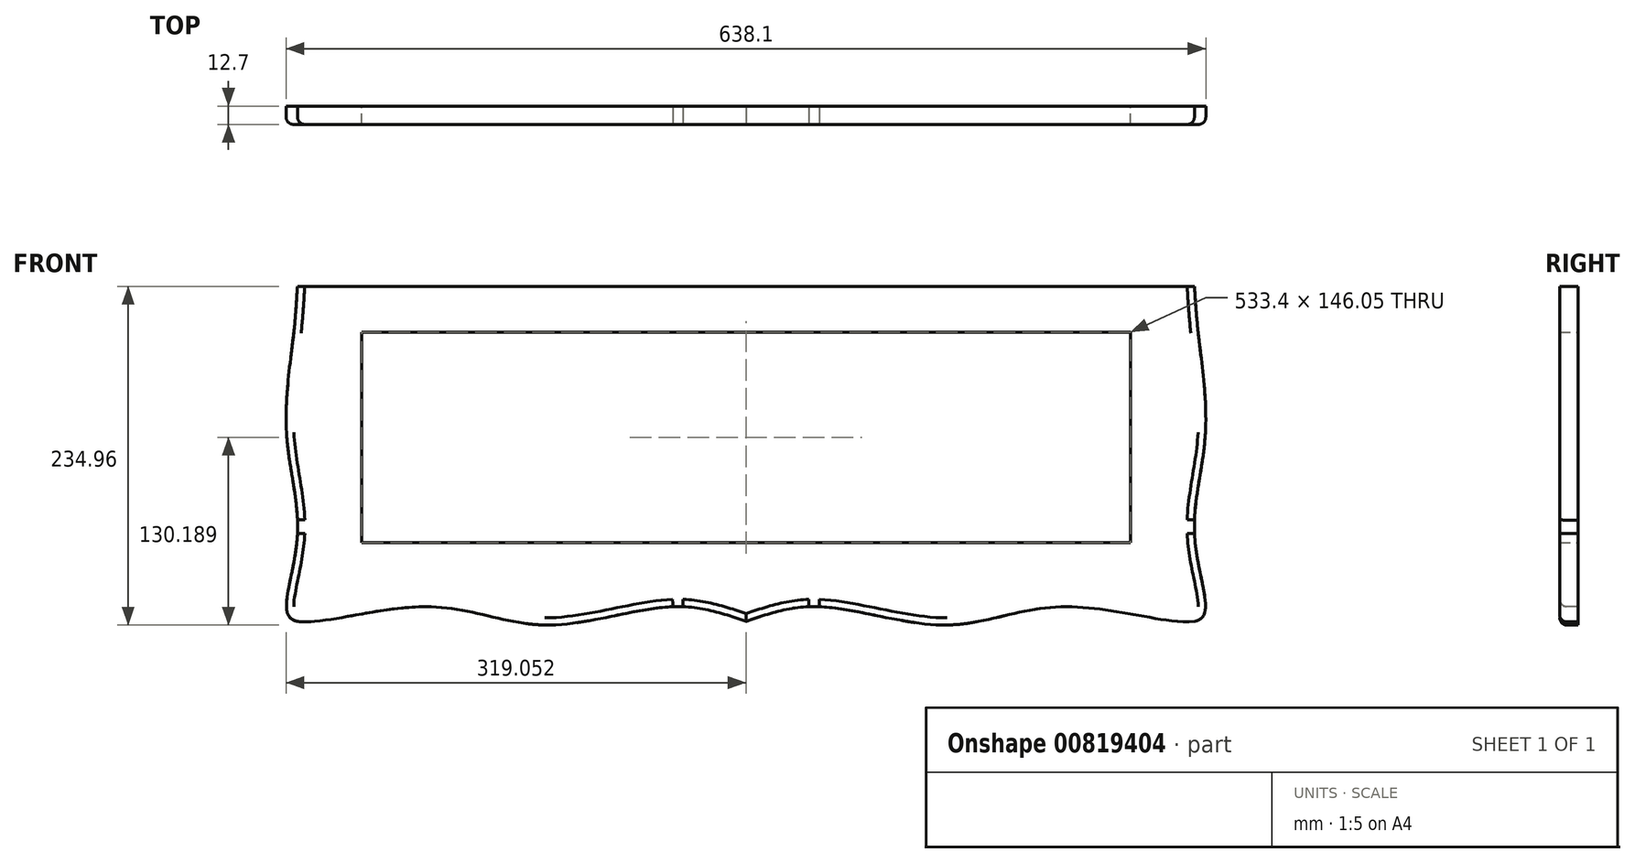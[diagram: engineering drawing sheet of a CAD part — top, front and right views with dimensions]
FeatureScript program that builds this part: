
annotation { "Feature Type Name" : "Feature", "Feature Type Description" : "" }
export const myFeature = defineFeature(function(context is Context, id is Id, definition is map)
    precondition{}
    {
        {
            var Q0;
            Q0=qCreatedBy(makeId("Front.planeOp"),FACE);
            var sketch = newSketch(context, id + "F0", { "sketchPlane" : qUnion([Q0])});
            skLineSegment(sketch, "E0.bottom", {"start": v(-290.57, 108.48) * mm, "end": v(331.73, 108.48) * mm});
            skLineSegment(sketch, "E0.top", {"start": v(-290.57, -113.77) * mm, "end": v(331.73, -113.77) * mm});
            skLineSegment(sketch, "E0.left", {"start": v(-290.57, 108.48) * mm, "end": v(-290.57, -113.77) * mm});
            skLineSegment(sketch, "E0.right", {"start": v(331.73, 108.48) * mm, "end": v(331.73, -113.77) * mm});
            skPoint(sketch, "E1", {"position": v(20.58, 108.48) * mm});
            skLineSegment(sketch, "E2.bottom", {"start": v(-246.12, 76.73) * mm, "end": v(287.28, 76.73) * mm});
            skLineSegment(sketch, "E2.top", {"start": v(-246.12, -69.32) * mm, "end": v(287.28, -69.32) * mm});
            skLineSegment(sketch, "E2.left", {"start": v(-246.12, 76.73) * mm, "end": v(-246.12, -69.32) * mm});
            skLineSegment(sketch, "E2.right", {"start": v(287.28, 76.73) * mm, "end": v(287.28, -69.32) * mm});
            skSolve(sketch);
        }
        {
            var Q0;
            Q0=makeQuery(id+"F0.imprint","IMPRINT",FACE,{"disambiguationData":[TD([[makeQuery(id+"F0.imprint","IMPRINT",EDGE,{"derivedFrom":sQuery(id+"F0.wireOp",EDGE,"E0.bottom")}),-1.0]])]});
            extrude(context, id + "F1", {"entities" : qUnion([Q0]), "depth" : 12.7 * mm, "offsetDistance" : 25.4 * mm});
        }
        {
            var Q0;
            Q0=makeQuery(id+"F1.opExtrude","CAP_FACE",FACE,{"disambiguationData":[OSD([sQuery(id+"F0.wireOp",EDGE,"E0.bottom"),sQuery(id+"F0.wireOp",EDGE,"E0.top"),sQuery(id+"F0.wireOp",EDGE,"E0.left"),sQuery(id+"F0.wireOp",EDGE,"E0.right")])],"isStart":false});
            var sketch = newSketch(context, id + "F2", { "sketchPlane" : qUnion([Q0])});
            skPoint(sketch, "E3", {"position": v(20.58, 108.48) * mm});
            skSolve(sketch);
        }
        {
            var Q0;
            {var subQ0=sQuery(id+"F0.wireOp",EDGE,"E0.right");var subQ1=sQuery(id+"F0.wireOp",EDGE,"E0.bottom");var subQ2=sQuery(id+"F0.wireOp",EDGE,"E0.left");var subQ3=sQuery(id+"F0.wireOp",EDGE,"E0.top");Q0=makeQuery(id+"FjgwLtvUwF4HY63_1.boolean.opBoolean","SPLIT",FACE,{"disambiguationData":[TD([makeQuery(id+"F1.opExtrude","SWEPT_FACE",FACE,{"disambiguationData":[OSD([subQ1])]})])],"derivedFrom":makeQuery(id+"F1.opExtrude","CAP_FACE",FACE,{"disambiguationData":[OSD([subQ1,subQ3,subQ2,subQ0])],"isStart":false})});}
            var sketch = newSketch(context, id + "F3", { "sketchPlane" : qUnion([Q0])});
            skPoint(sketch, "E4", {"position": v(-290.57, -62.97) * mm});
            skPoint(sketch, "E5", {"position": v(-290.57, 6.88) * mm});
            skPoint(sketch, "E6", {"position": v(-290.57, 76.73) * mm});
            skLineSegment(sketch, "E7", {"start": v(-290.57, 76.73) * mm, "end": v(-293.1, 76.73) * mm});
            skLineSegment(sketch, "E8", {"start": v(-290.57, 6.88) * mm, "end": v(-298.19, 6.88) * mm});
            skLineSegment(sketch, "E9", {"start": v(-290.57, -113.77) * mm, "end": v(-298.19, -113.77) * mm});
            skLineSegment(sketch, "E10", {"start": v(-290.57, -113.77) * mm, "end": v(-290.57, -123.93) * mm});
            skPoint(sketch, "E11", {"position": v(-201.67, -113.77) * mm});
            skPoint(sketch, "E12", {"position": v(20.58, -113.77) * mm});
            skPoint(sketch, "E13", {"position": v(-30.22, -113.77) * mm});
            skPoint(sketch, "E14", {"position": v(-119.12, -113.77) * mm});
            skPoint(sketch, "E15", {"position": v(71.38, -113.77) * mm});
            skPoint(sketch, "E16", {"position": v(160.28, -113.77) * mm});
            skPoint(sketch, "E17", {"position": v(242.83, -113.77) * mm});
            skPoint(sketch, "E18", {"position": v(331.73, -62.97) * mm});
            skPoint(sketch, "E19", {"position": v(331.73, 6.88) * mm});
            skPoint(sketch, "E20", {"position": v(331.73, 76.73) * mm});
            skLineSegment(sketch, "E21", {"start": v(331.73, 76.73) * mm, "end": v(334.27, 76.73) * mm});
            skLineSegment(sketch, "E22", {"start": v(331.73, 6.88) * mm, "end": v(339.35, 6.88) * mm});
            skLineSegment(sketch, "E23", {"start": v(331.73, -113.77) * mm, "end": v(339.35, -113.77) * mm});
            skLineSegment(sketch, "E24", {"start": v(331.73, -113.77) * mm, "end": v(331.73, -123.93) * mm});
            skLineSegment(sketch, "E25", {"start": v(-119.12, -113.77) * mm, "end": v(-119.12, -126.47) * mm});
            skLineSegment(sketch, "E26", {"start": v(20.58, -113.77) * mm, "end": v(20.58, -123.93) * mm});
            skLineSegment(sketch, "E27", {"start": v(160.28, -113.77) * mm, "end": v(160.28, -126.47) * mm});
            skFitSpline(sketch, "E28", {"points": [v(-290.57, 108.48) * mm, v(-293.1, 76.73) * mm, v(-298.19, 6.88) * mm, v(-290.57, -62.97) * mm, v(-298.19, -113.77) * mm, v(-290.57, -123.93) * mm, v(-201.67, -113.77) * mm, v(-119.12, -126.47) * mm, v(-30.22, -113.77) * mm, v(20.58, -123.93) * mm], "startDerivative": vector(-26.2, -341.82) * mm, "endDerivative": vector(438.15, -148.5) * mm});
            skFitSpline(sketch, "E29", {"points": [v(331.73, 108.48) * mm, v(334.27, 76.73) * mm, v(339.35, 6.88) * mm, v(331.73, -62.97) * mm, v(339.35, -113.77) * mm, v(331.73, -123.93) * mm, v(242.83, -113.77) * mm, v(160.28, -126.47) * mm, v(71.38, -113.77) * mm, v(20.58, -123.93) * mm], "startDerivative": vector(26.2, -341.82) * mm, "endDerivative": vector(-438.15, -148.5) * mm});
            skSolve(sketch);
        }
        {
            var Q0;
            {var subQ0=sQuery(id+"F3.wireOp",EDGE,"E26");Q0=makeQuery(id+"F3.imprint","IMPRINT",FACE,{"disambiguationData":[TD([[makeQuery(id+"F3.imprint","IMPRINT",EDGE,{"derivedFrom":subQ0}),-1.0]])]});}
            var Q1;
            {var subQ0=sQuery(id+"F3.wireOp",EDGE,"E26");Q1=makeQuery(id+"F3.imprint","IMPRINT",FACE,{"disambiguationData":[TD([[makeQuery(id+"F3.imprint","IMPRINT",EDGE,{"derivedFrom":subQ0}),1.0]])]});}
            var Q2;
            {var subQ0=sQuery(id+"F3.wireOp",EDGE,"E25");Q2=makeQuery(id+"F3.imprint","IMPRINT",FACE,{"disambiguationData":[TD([[makeQuery(id+"F3.imprint","IMPRINT",EDGE,{"derivedFrom":subQ0}),1.0]])]});}
            var Q3;
            {var subQ0=sQuery(id+"F3.wireOp",EDGE,"E25");Q3=makeQuery(id+"F3.imprint","IMPRINT",FACE,{"disambiguationData":[TD([[makeQuery(id+"F3.imprint","IMPRINT",EDGE,{"derivedFrom":subQ0}),-1.0]])]});}
            var Q4;
            {var subQ0=sQuery(id+"F3.wireOp",EDGE,"E10");Q4=makeQuery(id+"F3.imprint","IMPRINT",FACE,{"disambiguationData":[TD([[makeQuery(id+"F3.imprint","IMPRINT",EDGE,{"derivedFrom":subQ0}),1.0]])]});}
            var Q5;
            {var subQ0=sQuery(id+"F3.wireOp",EDGE,"E9");Q5=makeQuery(id+"F3.imprint","IMPRINT",FACE,{"disambiguationData":[TD([[makeQuery(id+"F3.imprint","IMPRINT",EDGE,{"derivedFrom":subQ0}),1.0]])]});}
            var Q6;
            {var subQ0=sQuery(id+"F3.wireOp",EDGE,"E9");Q6=makeQuery(id+"F3.imprint","IMPRINT",FACE,{"disambiguationData":[TD([[makeQuery(id+"F3.imprint","IMPRINT",EDGE,{"derivedFrom":subQ0}),-1.0]])]});}
            var Q7;
            {var subQ0=sQuery(id+"F3.wireOp",EDGE,"E8");Q7=makeQuery(id+"F3.imprint","IMPRINT",FACE,{"disambiguationData":[TD([[makeQuery(id+"F3.imprint","IMPRINT",EDGE,{"derivedFrom":subQ0}),1.0]])]});}
            var Q8;
            {var subQ0=sQuery(id+"F3.wireOp",EDGE,"E7");Q8=makeQuery(id+"F3.imprint","IMPRINT",FACE,{"disambiguationData":[TD([[makeQuery(id+"F3.imprint","IMPRINT",EDGE,{"derivedFrom":subQ0}),1.0]])]});}
            var Q9;
            {var subQ0=makeQuery(id+"F1.opExtrude","CAP_EDGE",EDGE,{"disambiguationData":[OSD([sQuery(id+"F0.wireOp",EDGE,"E0.bottom")])],"isStart":false});Q9=makeQuery(id+"F3.imprint","IMPRINT",FACE,{"disambiguationData":[TD([[makeQuery(id+"F3.imprint","IMPRINT",EDGE,{"derivedFrom":subQ0}),-1.0]])]});}
            var Q10;
            {var subQ0=sQuery(id+"F3.wireOp",EDGE,"E27");Q10=makeQuery(id+"F3.imprint","IMPRINT",FACE,{"disambiguationData":[TD([[makeQuery(id+"F3.imprint","IMPRINT",EDGE,{"derivedFrom":subQ0}),-1.0]])]});}
            var Q11;
            {var subQ0=sQuery(id+"F3.wireOp",EDGE,"E27");Q11=makeQuery(id+"F3.imprint","IMPRINT",FACE,{"disambiguationData":[TD([[makeQuery(id+"F3.imprint","IMPRINT",EDGE,{"derivedFrom":subQ0}),1.0]])]});}
            var Q12;
            {var subQ0=sQuery(id+"F3.wireOp",EDGE,"E24");Q12=makeQuery(id+"F3.imprint","IMPRINT",FACE,{"disambiguationData":[TD([[makeQuery(id+"F3.imprint","IMPRINT",EDGE,{"derivedFrom":subQ0}),-1.0]])]});}
            var Q13;
            {var subQ0=sQuery(id+"F3.wireOp",EDGE,"E23");Q13=makeQuery(id+"F3.imprint","IMPRINT",FACE,{"disambiguationData":[TD([[makeQuery(id+"F3.imprint","IMPRINT",EDGE,{"derivedFrom":subQ0}),-1.0]])]});}
            var Q14;
            {var subQ0=sQuery(id+"F3.wireOp",EDGE,"E23");Q14=makeQuery(id+"F3.imprint","IMPRINT",FACE,{"disambiguationData":[TD([[makeQuery(id+"F3.imprint","IMPRINT",EDGE,{"derivedFrom":subQ0}),1.0]])]});}
            var Q15;
            {var subQ0=sQuery(id+"F3.wireOp",EDGE,"E22");Q15=makeQuery(id+"F3.imprint","IMPRINT",FACE,{"disambiguationData":[TD([[makeQuery(id+"F3.imprint","IMPRINT",EDGE,{"derivedFrom":subQ0}),-1.0]])]});}
            var Q16;
            {var subQ0=sQuery(id+"F3.wireOp",EDGE,"E21");Q16=makeQuery(id+"F3.imprint","IMPRINT",FACE,{"disambiguationData":[TD([[makeQuery(id+"F3.imprint","IMPRINT",EDGE,{"derivedFrom":subQ0}),-1.0]])]});}
            var Q17;
            {var subQ0=sQuery(id+"F3.wireOp",EDGE,"E21");Q17=makeQuery(id+"F3.imprint","IMPRINT",FACE,{"disambiguationData":[TD([[makeQuery(id+"F3.imprint","IMPRINT",EDGE,{"derivedFrom":subQ0}),1.0]])]});}
            var Q18;
            {var subQ0=sQuery(id+"F3.wireOp",EDGE,"E7");Q18=makeQuery(id+"F3.imprint","IMPRINT",FACE,{"disambiguationData":[TD([[makeQuery(id+"F3.imprint","IMPRINT",EDGE,{"derivedFrom":subQ0}),-1.0]])]});}
            extrude(context, id + "F4", {"entities" : qUnion([Q0, Q1, Q2, Q3, Q4, Q5, Q6, Q7, Q8, Q9, Q10, Q11, Q12, Q13, Q14, Q15, Q16, Q17, Q18]), "operationType" : NewBodyOperationType.ADD, "depth" : -12.7 * mm, "offsetDistance" : 25.4 * mm});
        }
        {
            var Q0;
            {var subQ0=sQuery(id+"F3.wireOp",EDGE,"8007402e-1a4e-4a06-85a5-2af08e553504");var subQ1=sQuery(id+"F0.wireOp",EDGE,"E0.left");var subQ2=sQuery(id+"F0.wireOp",EDGE,"E0.top");var subQ3=sQuery(id+"F0.wireOp",EDGE,"E0.bottom");Q0=makeQuery(id+"F4.boolean.opBoolean","SPLIT",EDGE,{"disambiguationData":[TD([makeQuery(id+"F1.opExtrude","CAP_FACE",FACE,{"disambiguationData":[OSD([subQ3,subQ2,subQ1,sQuery(id+"F0.wireOp",EDGE,"E0.right")])],"isStart":false}),makeQuery(id+"F1.opExtrude","SWEPT_FACE",FACE,{"disambiguationData":[OSD([subQ2])]}),makeQuery(id+"F1.opExtrude","SWEPT_FACE",FACE,{"disambiguationData":[OSD([subQ1])]}),makeQuery(id+"F4.opExtrude","SWEPT_FACE",FACE,{"disambiguationData":[OSD([subQ0])]}),makeQuery(id+"F4.opExtrude","CAP_FACE",FACE,{"disambiguationData":[OSD([subQ3,sQuery(id+"F2.wireOp",EDGE,"fcba4419-a2ee-464f-be9d-58f11bf3418b.sketch_text.stroke-0"),sQuery(id+"F2.wireOp",EDGE,"fcba4419-a2ee-464f-be9d-58f11bf3418b.sketch_text.stroke-1"),sQuery(id+"F2.wireOp",EDGE,"fcba4419-a2ee-464f-be9d-58f11bf3418b.sketch_text.stroke-2"),sQuery(id+"F2.wireOp",EDGE,"fcba4419-a2ee-464f-be9d-58f11bf3418b.sketch_text.stroke-3"),sQuery(id+"F2.wireOp",EDGE,"fcba4419-a2ee-464f-be9d-58f11bf3418b.sketch_text.stroke-4"),sQuery(id+"F2.wireOp",EDGE,"fcba4419-a2ee-464f-be9d-58f11bf3418b.sketch_text.stroke-5"),sQuery(id+"F2.wireOp",EDGE,"fcba4419-a2ee-464f-be9d-58f11bf3418b.sketch_text.stroke-6"),sQuery(id+"F2.wireOp",EDGE,"fcba4419-a2ee-464f-be9d-58f11bf3418b.sketch_text.stroke-7"),sQuery(id+"F2.wireOp",EDGE,"fcba4419-a2ee-464f-be9d-58f11bf3418b.sketch_text.stroke-8"),sQuery(id+"F2.wireOp",EDGE,"fcba4419-a2ee-464f-be9d-58f11bf3418b.sketch_text.stroke-9"),sQuery(id+"F2.wireOp",EDGE,"fcba4419-a2ee-464f-be9d-58f11bf3418b.sketch_text.stroke-10"),sQuery(id+"F2.wireOp",EDGE,"fcba4419-a2ee-464f-be9d-58f11bf3418b.sketch_text.stroke-11"),sQuery(id+"F2.wireOp",EDGE,"fcba4419-a2ee-464f-be9d-58f11bf3418b.sketch_text.stroke-12"),sQuery(id+"F2.wireOp",EDGE,"fcba4419-a2ee-464f-be9d-58f11bf3418b.sketch_text.stroke-13"),sQuery(id+"F2.wireOp",EDGE,"fcba4419-a2ee-464f-be9d-58f11bf3418b.sketch_text.stroke-14"),sQuery(id+"F2.wireOp",EDGE,"fcba4419-a2ee-464f-be9d-58f11bf3418b.sketch_text.stroke-15"),sQuery(id+"F2.wireOp",EDGE,"fcba4419-a2ee-464f-be9d-58f11bf3418b.sketch_text.stroke-16"),sQuery(id+"F2.wireOp",EDGE,"fcba4419-a2ee-464f-be9d-58f11bf3418b.sketch_text.stroke-17"),sQuery(id+"F2.wireOp",EDGE,"fcba4419-a2ee-464f-be9d-58f11bf3418b.sketch_text.stroke-18"),sQuery(id+"F2.wireOp",EDGE,"fcba4419-a2ee-464f-be9d-58f11bf3418b.sketch_text.stroke-19"),sQuery(id+"F2.wireOp",EDGE,"fcba4419-a2ee-464f-be9d-58f11bf3418b.sketch_text.stroke-20"),sQuery(id+"F2.wireOp",EDGE,"fcba4419-a2ee-464f-be9d-58f11bf3418b.sketch_text.stroke-21"),sQuery(id+"F2.wireOp",EDGE,"fcba4419-a2ee-464f-be9d-58f11bf3418b.sketch_text.stroke-22"),sQuery(id+"F2.wireOp",EDGE,"fcba4419-a2ee-464f-be9d-58f11bf3418b.sketch_text.stroke-23"),sQuery(id+"F2.wireOp",EDGE,"fcba4419-a2ee-464f-be9d-58f11bf3418b.sketch_text.stroke-24"),sQuery(id+"F2.wireOp",EDGE,"fcba4419-a2ee-464f-be9d-58f11bf3418b.sketch_text.stroke-25"),sQuery(id+"F2.wireOp",EDGE,"fcba4419-a2ee-464f-be9d-58f11bf3418b.sketch_text.stroke-26"),sQuery(id+"F2.wireOp",EDGE,"fcba4419-a2ee-464f-be9d-58f11bf3418b.sketch_text.stroke-27"),sQuery(id+"F2.wireOp",EDGE,"fcba4419-a2ee-464f-be9d-58f11bf3418b.sketch_text.stroke-28"),sQuery(id+"F2.wireOp",EDGE,"fcba4419-a2ee-464f-be9d-58f11bf3418b.sketch_text.stroke-29"),sQuery(id+"F2.wireOp",EDGE,"fcba4419-a2ee-464f-be9d-58f11bf3418b.sketch_text.stroke-30"),sQuery(id+"F2.wireOp",EDGE,"fcba4419-a2ee-464f-be9d-58f11bf3418b.sketch_text.stroke-31"),sQuery(id+"F2.wireOp",EDGE,"fcba4419-a2ee-464f-be9d-58f11bf3418b.sketch_text.stroke-32"),sQuery(id+"F2.wireOp",EDGE,"fcba4419-a2ee-464f-be9d-58f11bf3418b.sketch_text.stroke-33"),sQuery(id+"F2.wireOp",EDGE,"fcba4419-a2ee-464f-be9d-58f11bf3418b.sketch_text.stroke-34"),sQuery(id+"F2.wireOp",EDGE,"fcba4419-a2ee-464f-be9d-58f11bf3418b.sketch_text.stroke-35"),sQuery(id+"F2.wireOp",EDGE,"fcba4419-a2ee-464f-be9d-58f11bf3418b.sketch_text.stroke-36"),sQuery(id+"F2.wireOp",EDGE,"fcba4419-a2ee-464f-be9d-58f11bf3418b.sketch_text.stroke-37"),sQuery(id+"F2.wireOp",EDGE,"fcba4419-a2ee-464f-be9d-58f11bf3418b.sketch_text.stroke-38"),sQuery(id+"F2.wireOp",EDGE,"fcba4419-a2ee-464f-be9d-58f11bf3418b.sketch_text.stroke-39"),sQuery(id+"F2.wireOp",EDGE,"fcba4419-a2ee-464f-be9d-58f11bf3418b.sketch_text.stroke-40"),sQuery(id+"F2.wireOp",EDGE,"fcba4419-a2ee-464f-be9d-58f11bf3418b.sketch_text.stroke-41"),sQuery(id+"F2.wireOp",EDGE,"fcba4419-a2ee-464f-be9d-58f11bf3418b.sketch_text.stroke-42"),sQuery(id+"F2.wireOp",EDGE,"fcba4419-a2ee-464f-be9d-58f11bf3418b.sketch_text.stroke-43"),sQuery(id+"F2.wireOp",EDGE,"fcba4419-a2ee-464f-be9d-58f11bf3418b.sketch_text.stroke-44"),sQuery(id+"F2.wireOp",EDGE,"fcba4419-a2ee-464f-be9d-58f11bf3418b.sketch_text.stroke-45"),sQuery(id+"F2.wireOp",EDGE,"fcba4419-a2ee-464f-be9d-58f11bf3418b.sketch_text.stroke-46"),sQuery(id+"F2.wireOp",EDGE,"fcba4419-a2ee-464f-be9d-58f11bf3418b.sketch_text.stroke-47"),sQuery(id+"F2.wireOp",EDGE,"fcba4419-a2ee-464f-be9d-58f11bf3418b.sketch_text.stroke-48"),sQuery(id+"F2.wireOp",EDGE,"fcba4419-a2ee-464f-be9d-58f11bf3418b.sketch_text.stroke-49"),sQuery(id+"F2.wireOp",EDGE,"fcba4419-a2ee-464f-be9d-58f11bf3418b.sketch_text.stroke-50"),sQuery(id+"F2.wireOp",EDGE,"fcba4419-a2ee-464f-be9d-58f11bf3418b.sketch_text.stroke-51"),sQuery(id+"F2.wireOp",EDGE,"fcba4419-a2ee-464f-be9d-58f11bf3418b.sketch_text.stroke-52"),sQuery(id+"F2.wireOp",EDGE,"fcba4419-a2ee-464f-be9d-58f11bf3418b.sketch_text.stroke-53"),sQuery(id+"F2.wireOp",EDGE,"fcba4419-a2ee-464f-be9d-58f11bf3418b.sketch_text.stroke-54"),sQuery(id+"F2.wireOp",EDGE,"fcba4419-a2ee-464f-be9d-58f11bf3418b.sketch_text.stroke-55"),sQuery(id+"F2.wireOp",EDGE,"fcba4419-a2ee-464f-be9d-58f11bf3418b.sketch_text.stroke-56"),sQuery(id+"F2.wireOp",EDGE,"fcba4419-a2ee-464f-be9d-58f11bf3418b.sketch_text.stroke-57"),sQuery(id+"F2.wireOp",EDGE,"fcba4419-a2ee-464f-be9d-58f11bf3418b.sketch_text.stroke-58"),sQuery(id+"F2.wireOp",EDGE,"fcba4419-a2ee-464f-be9d-58f11bf3418b.sketch_text.stroke-59"),sQuery(id+"F2.wireOp",EDGE,"fcba4419-a2ee-464f-be9d-58f11bf3418b.sketch_text.stroke-60"),sQuery(id+"F2.wireOp",EDGE,"fcba4419-a2ee-464f-be9d-58f11bf3418b.sketch_text.stroke-61"),sQuery(id+"F2.wireOp",EDGE,"fcba4419-a2ee-464f-be9d-58f11bf3418b.sketch_text.stroke-62"),sQuery(id+"F2.wireOp",EDGE,"fcba4419-a2ee-464f-be9d-58f11bf3418b.sketch_text.stroke-63"),sQuery(id+"F2.wireOp",EDGE,"fcba4419-a2ee-464f-be9d-58f11bf3418b.sketch_text.stroke-64"),sQuery(id+"F2.wireOp",EDGE,"fcba4419-a2ee-464f-be9d-58f11bf3418b.sketch_text.stroke-65"),sQuery(id+"F2.wireOp",EDGE,"fcba4419-a2ee-464f-be9d-58f11bf3418b.sketch_text.stroke-66"),sQuery(id+"F2.wireOp",EDGE,"fcba4419-a2ee-464f-be9d-58f11bf3418b.sketch_text.stroke-67"),sQuery(id+"F2.wireOp",EDGE,"fcba4419-a2ee-464f-be9d-58f11bf3418b.sketch_text.stroke-68"),sQuery(id+"F2.wireOp",EDGE,"fcba4419-a2ee-464f-be9d-58f11bf3418b.sketch_text.stroke-69"),sQuery(id+"F2.wireOp",EDGE,"fcba4419-a2ee-464f-be9d-58f11bf3418b.sketch_text.stroke-70"),sQuery(id+"F2.wireOp",EDGE,"fcba4419-a2ee-464f-be9d-58f11bf3418b.sketch_text.stroke-71"),sQuery(id+"F2.wireOp",EDGE,"fcba4419-a2ee-464f-be9d-58f11bf3418b.sketch_text.stroke-72"),sQuery(id+"F2.wireOp",EDGE,"fcba4419-a2ee-464f-be9d-58f11bf3418b.sketch_text.stroke-73"),sQuery(id+"F2.wireOp",EDGE,"fcba4419-a2ee-464f-be9d-58f11bf3418b.sketch_text.stroke-74"),sQuery(id+"F2.wireOp",EDGE,"fcba4419-a2ee-464f-be9d-58f11bf3418b.sketch_text.stroke-75"),sQuery(id+"F2.wireOp",EDGE,"fcba4419-a2ee-464f-be9d-58f11bf3418b.sketch_text.stroke-76"),sQuery(id+"F2.wireOp",EDGE,"fcba4419-a2ee-464f-be9d-58f11bf3418b.sketch_text.stroke-77"),sQuery(id+"F2.wireOp",EDGE,"fcba4419-a2ee-464f-be9d-58f11bf3418b.sketch_text.stroke-78"),sQuery(id+"F2.wireOp",EDGE,"fcba4419-a2ee-464f-be9d-58f11bf3418b.sketch_text.stroke-79"),sQuery(id+"F2.wireOp",EDGE,"fcba4419-a2ee-464f-be9d-58f11bf3418b.sketch_text.stroke-80"),sQuery(id+"F2.wireOp",EDGE,"fcba4419-a2ee-464f-be9d-58f11bf3418b.sketch_text.stroke-81"),sQuery(id+"F2.wireOp",EDGE,"fcba4419-a2ee-464f-be9d-58f11bf3418b.sketch_text.stroke-82"),sQuery(id+"F2.wireOp",EDGE,"fcba4419-a2ee-464f-be9d-58f11bf3418b.sketch_text.stroke-83"),sQuery(id+"F2.wireOp",EDGE,"fcba4419-a2ee-464f-be9d-58f11bf3418b.sketch_text.stroke-84"),sQuery(id+"F2.wireOp",EDGE,"fcba4419-a2ee-464f-be9d-58f11bf3418b.sketch_text.stroke-85"),sQuery(id+"F2.wireOp",EDGE,"fcba4419-a2ee-464f-be9d-58f11bf3418b.sketch_text.stroke-86"),sQuery(id+"F2.wireOp",EDGE,"fcba4419-a2ee-464f-be9d-58f11bf3418b.sketch_text.stroke-87"),sQuery(id+"F2.wireOp",EDGE,"fcba4419-a2ee-464f-be9d-58f11bf3418b.sketch_text.stroke-88"),sQuery(id+"F2.wireOp",EDGE,"fcba4419-a2ee-464f-be9d-58f11bf3418b.sketch_text.stroke-89"),sQuery(id+"F2.wireOp",EDGE,"fcba4419-a2ee-464f-be9d-58f11bf3418b.sketch_text.stroke-90"),sQuery(id+"F2.wireOp",EDGE,"fcba4419-a2ee-464f-be9d-58f11bf3418b.sketch_text.stroke-91"),sQuery(id+"F2.wireOp",EDGE,"fcba4419-a2ee-464f-be9d-58f11bf3418b.sketch_text.stroke-92"),sQuery(id+"F2.wireOp",EDGE,"fcba4419-a2ee-464f-be9d-58f11bf3418b.sketch_text.stroke-93"),sQuery(id+"F2.wireOp",EDGE,"fcba4419-a2ee-464f-be9d-58f11bf3418b.sketch_text.stroke-94"),sQuery(id+"F2.wireOp",EDGE,"fcba4419-a2ee-464f-be9d-58f11bf3418b.sketch_text.stroke-95"),sQuery(id+"F2.wireOp",EDGE,"fcba4419-a2ee-464f-be9d-58f11bf3418b.sketch_text.stroke-96"),sQuery(id+"F2.wireOp",EDGE,"fcba4419-a2ee-464f-be9d-58f11bf3418b.sketch_text.stroke-97"),sQuery(id+"F2.wireOp",EDGE,"fcba4419-a2ee-464f-be9d-58f11bf3418b.sketch_text.stroke-98"),sQuery(id+"F2.wireOp",EDGE,"fcba4419-a2ee-464f-be9d-58f11bf3418b.sketch_text.stroke-99"),sQuery(id+"F2.wireOp",EDGE,"fcba4419-a2ee-464f-be9d-58f11bf3418b.sketch_text.stroke-100"),sQuery(id+"F2.wireOp",EDGE,"fcba4419-a2ee-464f-be9d-58f11bf3418b.sketch_text.stroke-101"),sQuery(id+"F2.wireOp",EDGE,"fcba4419-a2ee-464f-be9d-58f11bf3418b.sketch_text.stroke-102"),sQuery(id+"F2.wireOp",EDGE,"fcba4419-a2ee-464f-be9d-58f11bf3418b.sketch_text.stroke-103"),sQuery(id+"F2.wireOp",EDGE,"fcba4419-a2ee-464f-be9d-58f11bf3418b.sketch_text.stroke-104"),sQuery(id+"F2.wireOp",EDGE,"fcba4419-a2ee-464f-be9d-58f11bf3418b.sketch_text.stroke-105"),sQuery(id+"F2.wireOp",EDGE,"fcba4419-a2ee-464f-be9d-58f11bf3418b.sketch_text.stroke-106"),sQuery(id+"F2.wireOp",EDGE,"fcba4419-a2ee-464f-be9d-58f11bf3418b.sketch_text.stroke-107"),sQuery(id+"F2.wireOp",EDGE,"fcba4419-a2ee-464f-be9d-58f11bf3418b.sketch_text.stroke-108"),sQuery(id+"F2.wireOp",EDGE,"fcba4419-a2ee-464f-be9d-58f11bf3418b.sketch_text.stroke-109"),sQuery(id+"F2.wireOp",EDGE,"fcba4419-a2ee-464f-be9d-58f11bf3418b.sketch_text.stroke-110"),sQuery(id+"F2.wireOp",EDGE,"fcba4419-a2ee-464f-be9d-58f11bf3418b.sketch_text.stroke-111"),sQuery(id+"F2.wireOp",EDGE,"fcba4419-a2ee-464f-be9d-58f11bf3418b.sketch_text.stroke-112"),sQuery(id+"F2.wireOp",EDGE,"fcba4419-a2ee-464f-be9d-58f11bf3418b.sketch_text.stroke-113"),sQuery(id+"F2.wireOp",EDGE,"fcba4419-a2ee-464f-be9d-58f11bf3418b.sketch_text.stroke-114"),sQuery(id+"F2.wireOp",EDGE,"fcba4419-a2ee-464f-be9d-58f11bf3418b.sketch_text.stroke-115"),sQuery(id+"F2.wireOp",EDGE,"fcba4419-a2ee-464f-be9d-58f11bf3418b.sketch_text.stroke-116"),sQuery(id+"F2.wireOp",EDGE,"fcba4419-a2ee-464f-be9d-58f11bf3418b.sketch_text.stroke-117"),sQuery(id+"F2.wireOp",EDGE,"fcba4419-a2ee-464f-be9d-58f11bf3418b.sketch_text.stroke-118"),sQuery(id+"F2.wireOp",EDGE,"fcba4419-a2ee-464f-be9d-58f11bf3418b.sketch_text.stroke-119"),sQuery(id+"F2.wireOp",EDGE,"fcba4419-a2ee-464f-be9d-58f11bf3418b.sketch_text.stroke-120"),sQuery(id+"F2.wireOp",EDGE,"fcba4419-a2ee-464f-be9d-58f11bf3418b.sketch_text.stroke-121"),sQuery(id+"F2.wireOp",EDGE,"fcba4419-a2ee-464f-be9d-58f11bf3418b.sketch_text.stroke-122"),sQuery(id+"F2.wireOp",EDGE,"fcba4419-a2ee-464f-be9d-58f11bf3418b.sketch_text.stroke-123"),sQuery(id+"F2.wireOp",EDGE,"fcba4419-a2ee-464f-be9d-58f11bf3418b.sketch_text.stroke-124"),sQuery(id+"F2.wireOp",EDGE,"fcba4419-a2ee-464f-be9d-58f11bf3418b.sketch_text.stroke-125"),sQuery(id+"F2.wireOp",EDGE,"fcba4419-a2ee-464f-be9d-58f11bf3418b.sketch_text.stroke-126"),sQuery(id+"F2.wireOp",EDGE,"fcba4419-a2ee-464f-be9d-58f11bf3418b.sketch_text.stroke-127"),sQuery(id+"F2.wireOp",EDGE,"fcba4419-a2ee-464f-be9d-58f11bf3418b.sketch_text.stroke-128"),sQuery(id+"F2.wireOp",EDGE,"fcba4419-a2ee-464f-be9d-58f11bf3418b.sketch_text.stroke-129"),sQuery(id+"F2.wireOp",EDGE,"fcba4419-a2ee-464f-be9d-58f11bf3418b.sketch_text.stroke-130"),sQuery(id+"F2.wireOp",EDGE,"fcba4419-a2ee-464f-be9d-58f11bf3418b.sketch_text.stroke-131"),sQuery(id+"F2.wireOp",EDGE,"fcba4419-a2ee-464f-be9d-58f11bf3418b.sketch_text.stroke-132"),sQuery(id+"F2.wireOp",EDGE,"fcba4419-a2ee-464f-be9d-58f11bf3418b.sketch_text.stroke-133"),sQuery(id+"F2.wireOp",EDGE,"fcba4419-a2ee-464f-be9d-58f11bf3418b.sketch_text.stroke-134"),sQuery(id+"F2.wireOp",EDGE,"fcba4419-a2ee-464f-be9d-58f11bf3418b.sketch_text.stroke-135"),sQuery(id+"F2.wireOp",EDGE,"fcba4419-a2ee-464f-be9d-58f11bf3418b.sketch_text.stroke-136"),sQuery(id+"F2.wireOp",EDGE,"fcba4419-a2ee-464f-be9d-58f11bf3418b.sketch_text.stroke-137"),sQuery(id+"F2.wireOp",EDGE,"fcba4419-a2ee-464f-be9d-58f11bf3418b.sketch_text.stroke-138"),sQuery(id+"F2.wireOp",EDGE,"fcba4419-a2ee-464f-be9d-58f11bf3418b.sketch_text.stroke-139"),sQuery(id+"F2.wireOp",EDGE,"fcba4419-a2ee-464f-be9d-58f11bf3418b.sketch_text.stroke-140"),sQuery(id+"F2.wireOp",EDGE,"fcba4419-a2ee-464f-be9d-58f11bf3418b.sketch_text.stroke-141"),sQuery(id+"F2.wireOp",EDGE,"fcba4419-a2ee-464f-be9d-58f11bf3418b.sketch_text.stroke-142"),sQuery(id+"F2.wireOp",EDGE,"fcba4419-a2ee-464f-be9d-58f11bf3418b.sketch_text.stroke-143"),sQuery(id+"F2.wireOp",EDGE,"fcba4419-a2ee-464f-be9d-58f11bf3418b.sketch_text.stroke-144"),sQuery(id+"F2.wireOp",EDGE,"fcba4419-a2ee-464f-be9d-58f11bf3418b.sketch_text.stroke-145"),sQuery(id+"F2.wireOp",EDGE,"fcba4419-a2ee-464f-be9d-58f11bf3418b.sketch_text.stroke-146"),sQuery(id+"F2.wireOp",EDGE,"fcba4419-a2ee-464f-be9d-58f11bf3418b.sketch_text.stroke-147"),sQuery(id+"F2.wireOp",EDGE,"fcba4419-a2ee-464f-be9d-58f11bf3418b.sketch_text.stroke-148"),sQuery(id+"F2.wireOp",EDGE,"fcba4419-a2ee-464f-be9d-58f11bf3418b.sketch_text.stroke-149"),sQuery(id+"F2.wireOp",EDGE,"fcba4419-a2ee-464f-be9d-58f11bf3418b.sketch_text.stroke-150"),sQuery(id+"F2.wireOp",EDGE,"fcba4419-a2ee-464f-be9d-58f11bf3418b.sketch_text.stroke-151"),sQuery(id+"F2.wireOp",EDGE,"fcba4419-a2ee-464f-be9d-58f11bf3418b.sketch_text.stroke-152"),sQuery(id+"F2.wireOp",EDGE,"fcba4419-a2ee-464f-be9d-58f11bf3418b.sketch_text.stroke-153"),sQuery(id+"F2.wireOp",EDGE,"fcba4419-a2ee-464f-be9d-58f11bf3418b.sketch_text.stroke-154"),sQuery(id+"F2.wireOp",EDGE,"fcba4419-a2ee-464f-be9d-58f11bf3418b.sketch_text.stroke-155"),sQuery(id+"F2.wireOp",EDGE,"fcba4419-a2ee-464f-be9d-58f11bf3418b.sketch_text.stroke-156"),sQuery(id+"F2.wireOp",EDGE,"fcba4419-a2ee-464f-be9d-58f11bf3418b.sketch_text.stroke-157"),sQuery(id+"F2.wireOp",EDGE,"fcba4419-a2ee-464f-be9d-58f11bf3418b.sketch_text.stroke-158"),sQuery(id+"F2.wireOp",EDGE,"fcba4419-a2ee-464f-be9d-58f11bf3418b.sketch_text.stroke-159"),sQuery(id+"F2.wireOp",EDGE,"fcba4419-a2ee-464f-be9d-58f11bf3418b.sketch_text.stroke-160"),sQuery(id+"F2.wireOp",EDGE,"fcba4419-a2ee-464f-be9d-58f11bf3418b.sketch_text.stroke-161"),sQuery(id+"F2.wireOp",EDGE,"fcba4419-a2ee-464f-be9d-58f11bf3418b.sketch_text.stroke-162"),sQuery(id+"F2.wireOp",EDGE,"fcba4419-a2ee-464f-be9d-58f11bf3418b.sketch_text.stroke-163"),sQuery(id+"F2.wireOp",EDGE,"fcba4419-a2ee-464f-be9d-58f11bf3418b.sketch_text.stroke-164"),sQuery(id+"F2.wireOp",EDGE,"fcba4419-a2ee-464f-be9d-58f11bf3418b.sketch_text.stroke-165"),sQuery(id+"F2.wireOp",EDGE,"fcba4419-a2ee-464f-be9d-58f11bf3418b.sketch_text.stroke-166"),sQuery(id+"F2.wireOp",EDGE,"fcba4419-a2ee-464f-be9d-58f11bf3418b.sketch_text.stroke-167"),sQuery(id+"F2.wireOp",EDGE,"fcba4419-a2ee-464f-be9d-58f11bf3418b.sketch_text.stroke-168"),sQuery(id+"F2.wireOp",EDGE,"fcba4419-a2ee-464f-be9d-58f11bf3418b.sketch_text.stroke-169"),sQuery(id+"F2.wireOp",EDGE,"fcba4419-a2ee-464f-be9d-58f11bf3418b.sketch_text.stroke-170"),sQuery(id+"F2.wireOp",EDGE,"fcba4419-a2ee-464f-be9d-58f11bf3418b.sketch_text.stroke-171"),sQuery(id+"F2.wireOp",EDGE,"fcba4419-a2ee-464f-be9d-58f11bf3418b.sketch_text.stroke-172"),sQuery(id+"F2.wireOp",EDGE,"fcba4419-a2ee-464f-be9d-58f11bf3418b.sketch_text.stroke-173"),sQuery(id+"FHMxAyK4CFUKdhS_1.wireOp",EDGE,"1cb9c079-ea9b-4899-8069-e0e3048e911d.sketch_text.stroke-0"),sQuery(id+"FHMxAyK4CFUKdhS_1.wireOp",EDGE,"1cb9c079-ea9b-4899-8069-e0e3048e911d.sketch_text.stroke-1"),sQuery(id+"FHMxAyK4CFUKdhS_1.wireOp",EDGE,"1cb9c079-ea9b-4899-8069-e0e3048e911d.sketch_text.stroke-2"),sQuery(id+"FHMxAyK4CFUKdhS_1.wireOp",EDGE,"1cb9c079-ea9b-4899-8069-e0e3048e911d.sketch_text.stroke-3"),sQuery(id+"FHMxAyK4CFUKdhS_1.wireOp",EDGE,"1cb9c079-ea9b-4899-8069-e0e3048e911d.sketch_text.stroke-4"),sQuery(id+"FHMxAyK4CFUKdhS_1.wireOp",EDGE,"1cb9c079-ea9b-4899-8069-e0e3048e911d.sketch_text.stroke-5"),sQuery(id+"FHMxAyK4CFUKdhS_1.wireOp",EDGE,"1cb9c079-ea9b-4899-8069-e0e3048e911d.sketch_text.stroke-6"),sQuery(id+"FHMxAyK4CFUKdhS_1.wireOp",EDGE,"1cb9c079-ea9b-4899-8069-e0e3048e911d.sketch_text.stroke-7"),sQuery(id+"FHMxAyK4CFUKdhS_1.wireOp",EDGE,"1cb9c079-ea9b-4899-8069-e0e3048e911d.sketch_text.stroke-8"),sQuery(id+"FHMxAyK4CFUKdhS_1.wireOp",EDGE,"1cb9c079-ea9b-4899-8069-e0e3048e911d.sketch_text.stroke-9"),sQuery(id+"FHMxAyK4CFUKdhS_1.wireOp",EDGE,"1cb9c079-ea9b-4899-8069-e0e3048e911d.sketch_text.stroke-10"),sQuery(id+"FHMxAyK4CFUKdhS_1.wireOp",EDGE,"1cb9c079-ea9b-4899-8069-e0e3048e911d.sketch_text.stroke-11"),sQuery(id+"FHMxAyK4CFUKdhS_1.wireOp",EDGE,"1cb9c079-ea9b-4899-8069-e0e3048e911d.sketch_text.stroke-12"),sQuery(id+"FHMxAyK4CFUKdhS_1.wireOp",EDGE,"1cb9c079-ea9b-4899-8069-e0e3048e911d.sketch_text.stroke-13"),sQuery(id+"FHMxAyK4CFUKdhS_1.wireOp",EDGE,"1cb9c079-ea9b-4899-8069-e0e3048e911d.sketch_text.stroke-14"),sQuery(id+"FHMxAyK4CFUKdhS_1.wireOp",EDGE,"1cb9c079-ea9b-4899-8069-e0e3048e911d.sketch_text.stroke-15"),sQuery(id+"FHMxAyK4CFUKdhS_1.wireOp",EDGE,"1cb9c079-ea9b-4899-8069-e0e3048e911d.sketch_text.stroke-16"),sQuery(id+"FHMxAyK4CFUKdhS_1.wireOp",EDGE,"1cb9c079-ea9b-4899-8069-e0e3048e911d.sketch_text.stroke-17"),sQuery(id+"FHMxAyK4CFUKdhS_1.wireOp",EDGE,"1cb9c079-ea9b-4899-8069-e0e3048e911d.sketch_text.stroke-18"),sQuery(id+"FHMxAyK4CFUKdhS_1.wireOp",EDGE,"1cb9c079-ea9b-4899-8069-e0e3048e911d.sketch_text.stroke-19"),sQuery(id+"FHMxAyK4CFUKdhS_1.wireOp",EDGE,"1cb9c079-ea9b-4899-8069-e0e3048e911d.sketch_text.stroke-20"),sQuery(id+"FHMxAyK4CFUKdhS_1.wireOp",EDGE,"1cb9c079-ea9b-4899-8069-e0e3048e911d.sketch_text.stroke-21"),sQuery(id+"FHMxAyK4CFUKdhS_1.wireOp",EDGE,"1cb9c079-ea9b-4899-8069-e0e3048e911d.sketch_text.stroke-22"),sQuery(id+"FHMxAyK4CFUKdhS_1.wireOp",EDGE,"1cb9c079-ea9b-4899-8069-e0e3048e911d.sketch_text.stroke-23"),sQuery(id+"FHMxAyK4CFUKdhS_1.wireOp",EDGE,"1cb9c079-ea9b-4899-8069-e0e3048e911d.sketch_text.stroke-24"),sQuery(id+"FHMxAyK4CFUKdhS_1.wireOp",EDGE,"1cb9c079-ea9b-4899-8069-e0e3048e911d.sketch_text.stroke-25"),sQuery(id+"FHMxAyK4CFUKdhS_1.wireOp",EDGE,"1cb9c079-ea9b-4899-8069-e0e3048e911d.sketch_text.stroke-26"),sQuery(id+"FHMxAyK4CFUKdhS_1.wireOp",EDGE,"1cb9c079-ea9b-4899-8069-e0e3048e911d.sketch_text.stroke-27"),sQuery(id+"FHMxAyK4CFUKdhS_1.wireOp",EDGE,"1cb9c079-ea9b-4899-8069-e0e3048e911d.sketch_text.stroke-28"),sQuery(id+"FHMxAyK4CFUKdhS_1.wireOp",EDGE,"1cb9c079-ea9b-4899-8069-e0e3048e911d.sketch_text.stroke-29"),sQuery(id+"FHMxAyK4CFUKdhS_1.wireOp",EDGE,"1cb9c079-ea9b-4899-8069-e0e3048e911d.sketch_text.stroke-30"),sQuery(id+"FHMxAyK4CFUKdhS_1.wireOp",EDGE,"1cb9c079-ea9b-4899-8069-e0e3048e911d.sketch_text.stroke-31"),sQuery(id+"FHMxAyK4CFUKdhS_1.wireOp",EDGE,"1cb9c079-ea9b-4899-8069-e0e3048e911d.sketch_text.stroke-32"),sQuery(id+"FHMxAyK4CFUKdhS_1.wireOp",EDGE,"1cb9c079-ea9b-4899-8069-e0e3048e911d.sketch_text.stroke-33"),sQuery(id+"FHMxAyK4CFUKdhS_1.wireOp",EDGE,"1cb9c079-ea9b-4899-8069-e0e3048e911d.sketch_text.stroke-34"),sQuery(id+"FHMxAyK4CFUKdhS_1.wireOp",EDGE,"1cb9c079-ea9b-4899-8069-e0e3048e911d.sketch_text.stroke-35"),sQuery(id+"FHMxAyK4CFUKdhS_1.wireOp",EDGE,"1cb9c079-ea9b-4899-8069-e0e3048e911d.sketch_text.stroke-36"),sQuery(id+"FHMxAyK4CFUKdhS_1.wireOp",EDGE,"1cb9c079-ea9b-4899-8069-e0e3048e911d.sketch_text.stroke-37"),sQuery(id+"FHMxAyK4CFUKdhS_1.wireOp",EDGE,"1cb9c079-ea9b-4899-8069-e0e3048e911d.sketch_text.stroke-38"),sQuery(id+"FHMxAyK4CFUKdhS_1.wireOp",EDGE,"1cb9c079-ea9b-4899-8069-e0e3048e911d.sketch_text.stroke-39"),sQuery(id+"FHMxAyK4CFUKdhS_1.wireOp",EDGE,"1cb9c079-ea9b-4899-8069-e0e3048e911d.sketch_text.stroke-40"),sQuery(id+"FHMxAyK4CFUKdhS_1.wireOp",EDGE,"1cb9c079-ea9b-4899-8069-e0e3048e911d.sketch_text.stroke-41"),sQuery(id+"FHMxAyK4CFUKdhS_1.wireOp",EDGE,"1cb9c079-ea9b-4899-8069-e0e3048e911d.sketch_text.stroke-42"),sQuery(id+"FHMxAyK4CFUKdhS_1.wireOp",EDGE,"1cb9c079-ea9b-4899-8069-e0e3048e911d.sketch_text.stroke-43"),sQuery(id+"FHMxAyK4CFUKdhS_1.wireOp",EDGE,"1cb9c079-ea9b-4899-8069-e0e3048e911d.sketch_text.stroke-44"),sQuery(id+"FHMxAyK4CFUKdhS_1.wireOp",EDGE,"1cb9c079-ea9b-4899-8069-e0e3048e911d.sketch_text.stroke-45"),sQuery(id+"FHMxAyK4CFUKdhS_1.wireOp",EDGE,"1cb9c079-ea9b-4899-8069-e0e3048e911d.sketch_text.stroke-46"),sQuery(id+"FHMxAyK4CFUKdhS_1.wireOp",EDGE,"1cb9c079-ea9b-4899-8069-e0e3048e911d.sketch_text.stroke-47"),sQuery(id+"FHMxAyK4CFUKdhS_1.wireOp",EDGE,"1cb9c079-ea9b-4899-8069-e0e3048e911d.sketch_text.stroke-48"),sQuery(id+"FHMxAyK4CFUKdhS_1.wireOp",EDGE,"1cb9c079-ea9b-4899-8069-e0e3048e911d.sketch_text.stroke-49"),sQuery(id+"FHMxAyK4CFUKdhS_1.wireOp",EDGE,"1cb9c079-ea9b-4899-8069-e0e3048e911d.sketch_text.stroke-50"),sQuery(id+"FHMxAyK4CFUKdhS_1.wireOp",EDGE,"1cb9c079-ea9b-4899-8069-e0e3048e911d.sketch_text.stroke-51"),sQuery(id+"FHMxAyK4CFUKdhS_1.wireOp",EDGE,"1cb9c079-ea9b-4899-8069-e0e3048e911d.sketch_text.stroke-52"),sQuery(id+"FHMxAyK4CFUKdhS_1.wireOp",EDGE,"1cb9c079-ea9b-4899-8069-e0e3048e911d.sketch_text.stroke-53"),sQuery(id+"FHMxAyK4CFUKdhS_1.wireOp",EDGE,"1cb9c079-ea9b-4899-8069-e0e3048e911d.sketch_text.stroke-54"),sQuery(id+"FHMxAyK4CFUKdhS_1.wireOp",EDGE,"1cb9c079-ea9b-4899-8069-e0e3048e911d.sketch_text.stroke-55"),sQuery(id+"FHMxAyK4CFUKdhS_1.wireOp",EDGE,"1cb9c079-ea9b-4899-8069-e0e3048e911d.sketch_text.stroke-56"),sQuery(id+"FHMxAyK4CFUKdhS_1.wireOp",EDGE,"1cb9c079-ea9b-4899-8069-e0e3048e911d.sketch_text.stroke-57"),sQuery(id+"FHMxAyK4CFUKdhS_1.wireOp",EDGE,"1cb9c079-ea9b-4899-8069-e0e3048e911d.sketch_text.stroke-58"),sQuery(id+"FHMxAyK4CFUKdhS_1.wireOp",EDGE,"1cb9c079-ea9b-4899-8069-e0e3048e911d.sketch_text.stroke-59"),sQuery(id+"FHMxAyK4CFUKdhS_1.wireOp",EDGE,"1cb9c079-ea9b-4899-8069-e0e3048e911d.sketch_text.stroke-60"),sQuery(id+"FHMxAyK4CFUKdhS_1.wireOp",EDGE,"1cb9c079-ea9b-4899-8069-e0e3048e911d.sketch_text.stroke-61"),sQuery(id+"FHMxAyK4CFUKdhS_1.wireOp",EDGE,"1cb9c079-ea9b-4899-8069-e0e3048e911d.sketch_text.stroke-62"),sQuery(id+"FHMxAyK4CFUKdhS_1.wireOp",EDGE,"1cb9c079-ea9b-4899-8069-e0e3048e911d.sketch_text.stroke-71"),sQuery(id+"FHMxAyK4CFUKdhS_1.wireOp",EDGE,"1cb9c079-ea9b-4899-8069-e0e3048e911d.sketch_text.stroke-72"),sQuery(id+"FHMxAyK4CFUKdhS_1.wireOp",EDGE,"1cb9c079-ea9b-4899-8069-e0e3048e911d.sketch_text.stroke-73"),sQuery(id+"FHMxAyK4CFUKdhS_1.wireOp",EDGE,"1cb9c079-ea9b-4899-8069-e0e3048e911d.sketch_text.stroke-74"),sQuery(id+"FHMxAyK4CFUKdhS_1.wireOp",EDGE,"1cb9c079-ea9b-4899-8069-e0e3048e911d.sketch_text.stroke-75"),sQuery(id+"FHMxAyK4CFUKdhS_1.wireOp",EDGE,"1cb9c079-ea9b-4899-8069-e0e3048e911d.sketch_text.stroke-76"),sQuery(id+"FHMxAyK4CFUKdhS_1.wireOp",EDGE,"1cb9c079-ea9b-4899-8069-e0e3048e911d.sketch_text.stroke-77"),sQuery(id+"FHMxAyK4CFUKdhS_1.wireOp",EDGE,"1cb9c079-ea9b-4899-8069-e0e3048e911d.sketch_text.stroke-78"),sQuery(id+"FHMxAyK4CFUKdhS_1.wireOp",EDGE,"1cb9c079-ea9b-4899-8069-e0e3048e911d.sketch_text.stroke-79"),sQuery(id+"FHMxAyK4CFUKdhS_1.wireOp",EDGE,"1cb9c079-ea9b-4899-8069-e0e3048e911d.sketch_text.stroke-80"),sQuery(id+"FHMxAyK4CFUKdhS_1.wireOp",EDGE,"1cb9c079-ea9b-4899-8069-e0e3048e911d.sketch_text.stroke-81"),sQuery(id+"FHMxAyK4CFUKdhS_1.wireOp",EDGE,"1cb9c079-ea9b-4899-8069-e0e3048e911d.sketch_text.stroke-82"),sQuery(id+"FHMxAyK4CFUKdhS_1.wireOp",EDGE,"1cb9c079-ea9b-4899-8069-e0e3048e911d.sketch_text.stroke-83"),sQuery(id+"FHMxAyK4CFUKdhS_1.wireOp",EDGE,"1cb9c079-ea9b-4899-8069-e0e3048e911d.sketch_text.stroke-84"),sQuery(id+"FHMxAyK4CFUKdhS_1.wireOp",EDGE,"1cb9c079-ea9b-4899-8069-e0e3048e911d.sketch_text.stroke-85"),sQuery(id+"FHMxAyK4CFUKdhS_1.wireOp",EDGE,"1cb9c079-ea9b-4899-8069-e0e3048e911d.sketch_text.stroke-86"),sQuery(id+"FHMxAyK4CFUKdhS_1.wireOp",EDGE,"1cb9c079-ea9b-4899-8069-e0e3048e911d.sketch_text.stroke-87"),sQuery(id+"FHMxAyK4CFUKdhS_1.wireOp",EDGE,"1cb9c079-ea9b-4899-8069-e0e3048e911d.sketch_text.stroke-88"),sQuery(id+"FHMxAyK4CFUKdhS_1.wireOp",EDGE,"1cb9c079-ea9b-4899-8069-e0e3048e911d.sketch_text.stroke-89"),sQuery(id+"FHMxAyK4CFUKdhS_1.wireOp",EDGE,"1cb9c079-ea9b-4899-8069-e0e3048e911d.sketch_text.stroke-90"),sQuery(id+"FHMxAyK4CFUKdhS_1.wireOp",EDGE,"1cb9c079-ea9b-4899-8069-e0e3048e911d.sketch_text.stroke-91"),sQuery(id+"FHMxAyK4CFUKdhS_1.wireOp",EDGE,"1cb9c079-ea9b-4899-8069-e0e3048e911d.sketch_text.stroke-92"),sQuery(id+"FHMxAyK4CFUKdhS_1.wireOp",EDGE,"1cb9c079-ea9b-4899-8069-e0e3048e911d.sketch_text.stroke-93"),sQuery(id+"FHMxAyK4CFUKdhS_1.wireOp",EDGE,"1cb9c079-ea9b-4899-8069-e0e3048e911d.sketch_text.stroke-94"),sQuery(id+"FHMxAyK4CFUKdhS_1.wireOp",EDGE,"1cb9c079-ea9b-4899-8069-e0e3048e911d.sketch_text.stroke-95"),sQuery(id+"FHMxAyK4CFUKdhS_1.wireOp",EDGE,"1cb9c079-ea9b-4899-8069-e0e3048e911d.sketch_text.stroke-96"),sQuery(id+"FHMxAyK4CFUKdhS_1.wireOp",EDGE,"1cb9c079-ea9b-4899-8069-e0e3048e911d.sketch_text.stroke-97"),sQuery(id+"FHMxAyK4CFUKdhS_1.wireOp",EDGE,"1cb9c079-ea9b-4899-8069-e0e3048e911d.sketch_text.stroke-103"),sQuery(id+"FHMxAyK4CFUKdhS_1.wireOp",EDGE,"1cb9c079-ea9b-4899-8069-e0e3048e911d.sketch_text.stroke-104"),sQuery(id+"FHMxAyK4CFUKdhS_1.wireOp",EDGE,"1cb9c079-ea9b-4899-8069-e0e3048e911d.sketch_text.stroke-105"),sQuery(id+"FHMxAyK4CFUKdhS_1.wireOp",EDGE,"1cb9c079-ea9b-4899-8069-e0e3048e911d.sketch_text.stroke-106"),sQuery(id+"FHMxAyK4CFUKdhS_1.wireOp",EDGE,"1cb9c079-ea9b-4899-8069-e0e3048e911d.sketch_text.stroke-107"),sQuery(id+"FHMxAyK4CFUKdhS_1.wireOp",EDGE,"1cb9c079-ea9b-4899-8069-e0e3048e911d.sketch_text.stroke-108"),sQuery(id+"FHMxAyK4CFUKdhS_1.wireOp",EDGE,"1cb9c079-ea9b-4899-8069-e0e3048e911d.sketch_text.stroke-109"),sQuery(id+"FHMxAyK4CFUKdhS_1.wireOp",EDGE,"1cb9c079-ea9b-4899-8069-e0e3048e911d.sketch_text.stroke-110"),sQuery(id+"FHMxAyK4CFUKdhS_1.wireOp",EDGE,"1cb9c079-ea9b-4899-8069-e0e3048e911d.sketch_text.stroke-111"),sQuery(id+"FHMxAyK4CFUKdhS_1.wireOp",EDGE,"1cb9c079-ea9b-4899-8069-e0e3048e911d.sketch_text.stroke-112"),sQuery(id+"FHMxAyK4CFUKdhS_1.wireOp",EDGE,"1cb9c079-ea9b-4899-8069-e0e3048e911d.sketch_text.stroke-113"),sQuery(id+"FHMxAyK4CFUKdhS_1.wireOp",EDGE,"1cb9c079-ea9b-4899-8069-e0e3048e911d.sketch_text.stroke-114"),sQuery(id+"FHMxAyK4CFUKdhS_1.wireOp",EDGE,"1cb9c079-ea9b-4899-8069-e0e3048e911d.sketch_text.stroke-115"),sQuery(id+"FHMxAyK4CFUKdhS_1.wireOp",EDGE,"1cb9c079-ea9b-4899-8069-e0e3048e911d.sketch_text.stroke-116"),sQuery(id+"FHMxAyK4CFUKdhS_1.wireOp",EDGE,"1cb9c079-ea9b-4899-8069-e0e3048e911d.sketch_text.stroke-117"),sQuery(id+"FHMxAyK4CFUKdhS_1.wireOp",EDGE,"1cb9c079-ea9b-4899-8069-e0e3048e911d.sketch_text.stroke-118"),sQuery(id+"FHMxAyK4CFUKdhS_1.wireOp",EDGE,"1cb9c079-ea9b-4899-8069-e0e3048e911d.sketch_text.stroke-119"),sQuery(id+"FHMxAyK4CFUKdhS_1.wireOp",EDGE,"1cb9c079-ea9b-4899-8069-e0e3048e911d.sketch_text.stroke-120"),sQuery(id+"FHMxAyK4CFUKdhS_1.wireOp",EDGE,"1cb9c079-ea9b-4899-8069-e0e3048e911d.sketch_text.stroke-121"),sQuery(id+"FHMxAyK4CFUKdhS_1.wireOp",EDGE,"1cb9c079-ea9b-4899-8069-e0e3048e911d.sketch_text.stroke-122"),sQuery(id+"FHMxAyK4CFUKdhS_1.wireOp",EDGE,"1cb9c079-ea9b-4899-8069-e0e3048e911d.sketch_text.stroke-123"),sQuery(id+"FHMxAyK4CFUKdhS_1.wireOp",EDGE,"1cb9c079-ea9b-4899-8069-e0e3048e911d.sketch_text.stroke-124"),sQuery(id+"FHMxAyK4CFUKdhS_1.wireOp",EDGE,"1cb9c079-ea9b-4899-8069-e0e3048e911d.sketch_text.stroke-125"),sQuery(id+"FHMxAyK4CFUKdhS_1.wireOp",EDGE,"1cb9c079-ea9b-4899-8069-e0e3048e911d.sketch_text.stroke-126"),sQuery(id+"FHMxAyK4CFUKdhS_1.wireOp",EDGE,"1cb9c079-ea9b-4899-8069-e0e3048e911d.sketch_text.stroke-127"),sQuery(id+"FHMxAyK4CFUKdhS_1.wireOp",EDGE,"1cb9c079-ea9b-4899-8069-e0e3048e911d.sketch_text.stroke-128"),sQuery(id+"FHMxAyK4CFUKdhS_1.wireOp",EDGE,"1cb9c079-ea9b-4899-8069-e0e3048e911d.sketch_text.stroke-129"),sQuery(id+"FHMxAyK4CFUKdhS_1.wireOp",EDGE,"1cb9c079-ea9b-4899-8069-e0e3048e911d.sketch_text.stroke-130"),sQuery(id+"FHMxAyK4CFUKdhS_1.wireOp",EDGE,"1cb9c079-ea9b-4899-8069-e0e3048e911d.sketch_text.stroke-131"),sQuery(id+"FHMxAyK4CFUKdhS_1.wireOp",EDGE,"1cb9c079-ea9b-4899-8069-e0e3048e911d.sketch_text.stroke-132"),sQuery(id+"FHMxAyK4CFUKdhS_1.wireOp",EDGE,"1cb9c079-ea9b-4899-8069-e0e3048e911d.sketch_text.stroke-133"),sQuery(id+"FHMxAyK4CFUKdhS_1.wireOp",EDGE,"1cb9c079-ea9b-4899-8069-e0e3048e911d.sketch_text.stroke-134"),sQuery(id+"FHMxAyK4CFUKdhS_1.wireOp",EDGE,"1cb9c079-ea9b-4899-8069-e0e3048e911d.sketch_text.stroke-135"),sQuery(id+"FHMxAyK4CFUKdhS_1.wireOp",EDGE,"1cb9c079-ea9b-4899-8069-e0e3048e911d.sketch_text.stroke-136"),sQuery(id+"FHMxAyK4CFUKdhS_1.wireOp",EDGE,"1cb9c079-ea9b-4899-8069-e0e3048e911d.sketch_text.stroke-137"),sQuery(id+"FHMxAyK4CFUKdhS_1.wireOp",EDGE,"1cb9c079-ea9b-4899-8069-e0e3048e911d.sketch_text.stroke-138"),sQuery(id+"FHMxAyK4CFUKdhS_1.wireOp",EDGE,"1cb9c079-ea9b-4899-8069-e0e3048e911d.sketch_text.stroke-139"),sQuery(id+"FHMxAyK4CFUKdhS_1.wireOp",EDGE,"1cb9c079-ea9b-4899-8069-e0e3048e911d.sketch_text.stroke-140"),sQuery(id+"FHMxAyK4CFUKdhS_1.wireOp",EDGE,"1cb9c079-ea9b-4899-8069-e0e3048e911d.sketch_text.stroke-141"),sQuery(id+"FHMxAyK4CFUKdhS_1.wireOp",EDGE,"1cb9c079-ea9b-4899-8069-e0e3048e911d.sketch_text.stroke-142"),sQuery(id+"FHMxAyK4CFUKdhS_1.wireOp",EDGE,"1cb9c079-ea9b-4899-8069-e0e3048e911d.sketch_text.stroke-143"),sQuery(id+"FHMxAyK4CFUKdhS_1.wireOp",EDGE,"1cb9c079-ea9b-4899-8069-e0e3048e911d.sketch_text.stroke-144"),sQuery(id+"FHMxAyK4CFUKdhS_1.wireOp",EDGE,"1cb9c079-ea9b-4899-8069-e0e3048e911d.sketch_text.stroke-145"),sQuery(id+"FHMxAyK4CFUKdhS_1.wireOp",EDGE,"1cb9c079-ea9b-4899-8069-e0e3048e911d.sketch_text.stroke-146"),sQuery(id+"FHMxAyK4CFUKdhS_1.wireOp",EDGE,"1cb9c079-ea9b-4899-8069-e0e3048e911d.sketch_text.stroke-147"),sQuery(id+"FHMxAyK4CFUKdhS_1.wireOp",EDGE,"1cb9c079-ea9b-4899-8069-e0e3048e911d.sketch_text.stroke-148"),sQuery(id+"FHMxAyK4CFUKdhS_1.wireOp",EDGE,"1cb9c079-ea9b-4899-8069-e0e3048e911d.sketch_text.stroke-149"),sQuery(id+"FHMxAyK4CFUKdhS_1.wireOp",EDGE,"1cb9c079-ea9b-4899-8069-e0e3048e911d.sketch_text.stroke-150"),sQuery(id+"FHMxAyK4CFUKdhS_1.wireOp",EDGE,"1cb9c079-ea9b-4899-8069-e0e3048e911d.sketch_text.stroke-151"),sQuery(id+"FHMxAyK4CFUKdhS_1.wireOp",EDGE,"1cb9c079-ea9b-4899-8069-e0e3048e911d.sketch_text.stroke-152"),sQuery(id+"FHMxAyK4CFUKdhS_1.wireOp",EDGE,"1cb9c079-ea9b-4899-8069-e0e3048e911d.sketch_text.stroke-153"),sQuery(id+"FHMxAyK4CFUKdhS_1.wireOp",EDGE,"1cb9c079-ea9b-4899-8069-e0e3048e911d.sketch_text.stroke-159"),sQuery(id+"FHMxAyK4CFUKdhS_1.wireOp",EDGE,"1cb9c079-ea9b-4899-8069-e0e3048e911d.sketch_text.stroke-160"),sQuery(id+"FHMxAyK4CFUKdhS_1.wireOp",EDGE,"1cb9c079-ea9b-4899-8069-e0e3048e911d.sketch_text.stroke-161"),sQuery(id+"FHMxAyK4CFUKdhS_1.wireOp",EDGE,"1cb9c079-ea9b-4899-8069-e0e3048e911d.sketch_text.stroke-162"),sQuery(id+"FHMxAyK4CFUKdhS_1.wireOp",EDGE,"1cb9c079-ea9b-4899-8069-e0e3048e911d.sketch_text.stroke-163"),sQuery(id+"FHMxAyK4CFUKdhS_1.wireOp",EDGE,"1cb9c079-ea9b-4899-8069-e0e3048e911d.sketch_text.stroke-164"),sQuery(id+"FHMxAyK4CFUKdhS_1.wireOp",EDGE,"1cb9c079-ea9b-4899-8069-e0e3048e911d.sketch_text.stroke-165"),sQuery(id+"FHMxAyK4CFUKdhS_1.wireOp",EDGE,"1cb9c079-ea9b-4899-8069-e0e3048e911d.sketch_text.stroke-166"),sQuery(id+"FHMxAyK4CFUKdhS_1.wireOp",EDGE,"1cb9c079-ea9b-4899-8069-e0e3048e911d.sketch_text.stroke-167"),sQuery(id+"FHMxAyK4CFUKdhS_1.wireOp",EDGE,"1cb9c079-ea9b-4899-8069-e0e3048e911d.sketch_text.stroke-168"),sQuery(id+"FHMxAyK4CFUKdhS_1.wireOp",EDGE,"1cb9c079-ea9b-4899-8069-e0e3048e911d.sketch_text.stroke-169"),sQuery(id+"FHMxAyK4CFUKdhS_1.wireOp",EDGE,"1cb9c079-ea9b-4899-8069-e0e3048e911d.sketch_text.stroke-170"),sQuery(id+"FHMxAyK4CFUKdhS_1.wireOp",EDGE,"1cb9c079-ea9b-4899-8069-e0e3048e911d.sketch_text.stroke-171"),sQuery(id+"FHMxAyK4CFUKdhS_1.wireOp",EDGE,"1cb9c079-ea9b-4899-8069-e0e3048e911d.sketch_text.stroke-172"),sQuery(id+"FHMxAyK4CFUKdhS_1.wireOp",EDGE,"1cb9c079-ea9b-4899-8069-e0e3048e911d.sketch_text.stroke-173"),sQuery(id+"FHMxAyK4CFUKdhS_1.wireOp",EDGE,"1cb9c079-ea9b-4899-8069-e0e3048e911d.sketch_text.stroke-174"),sQuery(id+"FHMxAyK4CFUKdhS_1.wireOp",EDGE,"1cb9c079-ea9b-4899-8069-e0e3048e911d.sketch_text.stroke-175"),sQuery(id+"FHMxAyK4CFUKdhS_1.wireOp",EDGE,"1cb9c079-ea9b-4899-8069-e0e3048e911d.sketch_text.stroke-176"),sQuery(id+"FHMxAyK4CFUKdhS_1.wireOp",EDGE,"1cb9c079-ea9b-4899-8069-e0e3048e911d.sketch_text.stroke-177"),sQuery(id+"FHMxAyK4CFUKdhS_1.wireOp",EDGE,"1cb9c079-ea9b-4899-8069-e0e3048e911d.sketch_text.stroke-178"),sQuery(id+"FHMxAyK4CFUKdhS_1.wireOp",EDGE,"1cb9c079-ea9b-4899-8069-e0e3048e911d.sketch_text.stroke-179"),sQuery(id+"FHMxAyK4CFUKdhS_1.wireOp",EDGE,"1cb9c079-ea9b-4899-8069-e0e3048e911d.sketch_text.stroke-180"),subQ0,sQuery(id+"F3.wireOp",EDGE,"6ee83ff3-586e-4dbe-aaea-af71240543bd")])],"isStart":true})])],"derivedFrom":makeQuery(id+"F4.opExtrude","CAP_EDGE",EDGE,{"disambiguationData":[OSD([subQ0])],"isStart":true})});}
            var Q1;
            Q1=makeQuery(id+"F1.opExtrude","CAP_EDGE",EDGE,{"disambiguationData":[OSD([sQuery(id+"F0.wireOp",EDGE,"E0.left")])],"isStart":false});
            var Q2;
            {var subQ0=sQuery(id+"F0.wireOp",EDGE,"E0.top");var subQ1=sQuery(id+"F0.wireOp",EDGE,"E0.bottom");var subQ2=sQuery(id+"F3.wireOp",EDGE,"8007402e-1a4e-4a06-85a5-2af08e553504");Q2=makeQuery(id+"F4.boolean.opBoolean","SPLIT",EDGE,{"disambiguationData":[TD([makeQuery(id+"F1.opExtrude","CAP_FACE",FACE,{"disambiguationData":[OSD([subQ1,subQ0,sQuery(id+"F0.wireOp",EDGE,"E0.left"),sQuery(id+"F0.wireOp",EDGE,"E0.right")])],"isStart":false}),makeQuery(id+"F1.opExtrude","SWEPT_FACE",FACE,{"disambiguationData":[OSD([subQ0])]}),makeQuery(id+"F4.opExtrude","SWEPT_FACE",FACE,{"disambiguationData":[OSD([subQ2])]}),makeQuery(id+"F4.opExtrude","CAP_FACE",FACE,{"disambiguationData":[OSD([subQ1,sQuery(id+"F2.wireOp",EDGE,"fcba4419-a2ee-464f-be9d-58f11bf3418b.sketch_text.stroke-0"),sQuery(id+"F2.wireOp",EDGE,"fcba4419-a2ee-464f-be9d-58f11bf3418b.sketch_text.stroke-1"),sQuery(id+"F2.wireOp",EDGE,"fcba4419-a2ee-464f-be9d-58f11bf3418b.sketch_text.stroke-2"),sQuery(id+"F2.wireOp",EDGE,"fcba4419-a2ee-464f-be9d-58f11bf3418b.sketch_text.stroke-3"),sQuery(id+"F2.wireOp",EDGE,"fcba4419-a2ee-464f-be9d-58f11bf3418b.sketch_text.stroke-4"),sQuery(id+"F2.wireOp",EDGE,"fcba4419-a2ee-464f-be9d-58f11bf3418b.sketch_text.stroke-5"),sQuery(id+"F2.wireOp",EDGE,"fcba4419-a2ee-464f-be9d-58f11bf3418b.sketch_text.stroke-6"),sQuery(id+"F2.wireOp",EDGE,"fcba4419-a2ee-464f-be9d-58f11bf3418b.sketch_text.stroke-7"),sQuery(id+"F2.wireOp",EDGE,"fcba4419-a2ee-464f-be9d-58f11bf3418b.sketch_text.stroke-8"),sQuery(id+"F2.wireOp",EDGE,"fcba4419-a2ee-464f-be9d-58f11bf3418b.sketch_text.stroke-9"),sQuery(id+"F2.wireOp",EDGE,"fcba4419-a2ee-464f-be9d-58f11bf3418b.sketch_text.stroke-10"),sQuery(id+"F2.wireOp",EDGE,"fcba4419-a2ee-464f-be9d-58f11bf3418b.sketch_text.stroke-11"),sQuery(id+"F2.wireOp",EDGE,"fcba4419-a2ee-464f-be9d-58f11bf3418b.sketch_text.stroke-12"),sQuery(id+"F2.wireOp",EDGE,"fcba4419-a2ee-464f-be9d-58f11bf3418b.sketch_text.stroke-13"),sQuery(id+"F2.wireOp",EDGE,"fcba4419-a2ee-464f-be9d-58f11bf3418b.sketch_text.stroke-14"),sQuery(id+"F2.wireOp",EDGE,"fcba4419-a2ee-464f-be9d-58f11bf3418b.sketch_text.stroke-15"),sQuery(id+"F2.wireOp",EDGE,"fcba4419-a2ee-464f-be9d-58f11bf3418b.sketch_text.stroke-16"),sQuery(id+"F2.wireOp",EDGE,"fcba4419-a2ee-464f-be9d-58f11bf3418b.sketch_text.stroke-17"),sQuery(id+"F2.wireOp",EDGE,"fcba4419-a2ee-464f-be9d-58f11bf3418b.sketch_text.stroke-18"),sQuery(id+"F2.wireOp",EDGE,"fcba4419-a2ee-464f-be9d-58f11bf3418b.sketch_text.stroke-19"),sQuery(id+"F2.wireOp",EDGE,"fcba4419-a2ee-464f-be9d-58f11bf3418b.sketch_text.stroke-20"),sQuery(id+"F2.wireOp",EDGE,"fcba4419-a2ee-464f-be9d-58f11bf3418b.sketch_text.stroke-21"),sQuery(id+"F2.wireOp",EDGE,"fcba4419-a2ee-464f-be9d-58f11bf3418b.sketch_text.stroke-22"),sQuery(id+"F2.wireOp",EDGE,"fcba4419-a2ee-464f-be9d-58f11bf3418b.sketch_text.stroke-23"),sQuery(id+"F2.wireOp",EDGE,"fcba4419-a2ee-464f-be9d-58f11bf3418b.sketch_text.stroke-24"),sQuery(id+"F2.wireOp",EDGE,"fcba4419-a2ee-464f-be9d-58f11bf3418b.sketch_text.stroke-25"),sQuery(id+"F2.wireOp",EDGE,"fcba4419-a2ee-464f-be9d-58f11bf3418b.sketch_text.stroke-26"),sQuery(id+"F2.wireOp",EDGE,"fcba4419-a2ee-464f-be9d-58f11bf3418b.sketch_text.stroke-27"),sQuery(id+"F2.wireOp",EDGE,"fcba4419-a2ee-464f-be9d-58f11bf3418b.sketch_text.stroke-28"),sQuery(id+"F2.wireOp",EDGE,"fcba4419-a2ee-464f-be9d-58f11bf3418b.sketch_text.stroke-29"),sQuery(id+"F2.wireOp",EDGE,"fcba4419-a2ee-464f-be9d-58f11bf3418b.sketch_text.stroke-30"),sQuery(id+"F2.wireOp",EDGE,"fcba4419-a2ee-464f-be9d-58f11bf3418b.sketch_text.stroke-31"),sQuery(id+"F2.wireOp",EDGE,"fcba4419-a2ee-464f-be9d-58f11bf3418b.sketch_text.stroke-32"),sQuery(id+"F2.wireOp",EDGE,"fcba4419-a2ee-464f-be9d-58f11bf3418b.sketch_text.stroke-33"),sQuery(id+"F2.wireOp",EDGE,"fcba4419-a2ee-464f-be9d-58f11bf3418b.sketch_text.stroke-34"),sQuery(id+"F2.wireOp",EDGE,"fcba4419-a2ee-464f-be9d-58f11bf3418b.sketch_text.stroke-35"),sQuery(id+"F2.wireOp",EDGE,"fcba4419-a2ee-464f-be9d-58f11bf3418b.sketch_text.stroke-36"),sQuery(id+"F2.wireOp",EDGE,"fcba4419-a2ee-464f-be9d-58f11bf3418b.sketch_text.stroke-37"),sQuery(id+"F2.wireOp",EDGE,"fcba4419-a2ee-464f-be9d-58f11bf3418b.sketch_text.stroke-38"),sQuery(id+"F2.wireOp",EDGE,"fcba4419-a2ee-464f-be9d-58f11bf3418b.sketch_text.stroke-39"),sQuery(id+"F2.wireOp",EDGE,"fcba4419-a2ee-464f-be9d-58f11bf3418b.sketch_text.stroke-40"),sQuery(id+"F2.wireOp",EDGE,"fcba4419-a2ee-464f-be9d-58f11bf3418b.sketch_text.stroke-41"),sQuery(id+"F2.wireOp",EDGE,"fcba4419-a2ee-464f-be9d-58f11bf3418b.sketch_text.stroke-42"),sQuery(id+"F2.wireOp",EDGE,"fcba4419-a2ee-464f-be9d-58f11bf3418b.sketch_text.stroke-43"),sQuery(id+"F2.wireOp",EDGE,"fcba4419-a2ee-464f-be9d-58f11bf3418b.sketch_text.stroke-44"),sQuery(id+"F2.wireOp",EDGE,"fcba4419-a2ee-464f-be9d-58f11bf3418b.sketch_text.stroke-45"),sQuery(id+"F2.wireOp",EDGE,"fcba4419-a2ee-464f-be9d-58f11bf3418b.sketch_text.stroke-46"),sQuery(id+"F2.wireOp",EDGE,"fcba4419-a2ee-464f-be9d-58f11bf3418b.sketch_text.stroke-47"),sQuery(id+"F2.wireOp",EDGE,"fcba4419-a2ee-464f-be9d-58f11bf3418b.sketch_text.stroke-48"),sQuery(id+"F2.wireOp",EDGE,"fcba4419-a2ee-464f-be9d-58f11bf3418b.sketch_text.stroke-49"),sQuery(id+"F2.wireOp",EDGE,"fcba4419-a2ee-464f-be9d-58f11bf3418b.sketch_text.stroke-50"),sQuery(id+"F2.wireOp",EDGE,"fcba4419-a2ee-464f-be9d-58f11bf3418b.sketch_text.stroke-51"),sQuery(id+"F2.wireOp",EDGE,"fcba4419-a2ee-464f-be9d-58f11bf3418b.sketch_text.stroke-52"),sQuery(id+"F2.wireOp",EDGE,"fcba4419-a2ee-464f-be9d-58f11bf3418b.sketch_text.stroke-53"),sQuery(id+"F2.wireOp",EDGE,"fcba4419-a2ee-464f-be9d-58f11bf3418b.sketch_text.stroke-54"),sQuery(id+"F2.wireOp",EDGE,"fcba4419-a2ee-464f-be9d-58f11bf3418b.sketch_text.stroke-55"),sQuery(id+"F2.wireOp",EDGE,"fcba4419-a2ee-464f-be9d-58f11bf3418b.sketch_text.stroke-56"),sQuery(id+"F2.wireOp",EDGE,"fcba4419-a2ee-464f-be9d-58f11bf3418b.sketch_text.stroke-57"),sQuery(id+"F2.wireOp",EDGE,"fcba4419-a2ee-464f-be9d-58f11bf3418b.sketch_text.stroke-58"),sQuery(id+"F2.wireOp",EDGE,"fcba4419-a2ee-464f-be9d-58f11bf3418b.sketch_text.stroke-59"),sQuery(id+"F2.wireOp",EDGE,"fcba4419-a2ee-464f-be9d-58f11bf3418b.sketch_text.stroke-60"),sQuery(id+"F2.wireOp",EDGE,"fcba4419-a2ee-464f-be9d-58f11bf3418b.sketch_text.stroke-61"),sQuery(id+"F2.wireOp",EDGE,"fcba4419-a2ee-464f-be9d-58f11bf3418b.sketch_text.stroke-62"),sQuery(id+"F2.wireOp",EDGE,"fcba4419-a2ee-464f-be9d-58f11bf3418b.sketch_text.stroke-63"),sQuery(id+"F2.wireOp",EDGE,"fcba4419-a2ee-464f-be9d-58f11bf3418b.sketch_text.stroke-64"),sQuery(id+"F2.wireOp",EDGE,"fcba4419-a2ee-464f-be9d-58f11bf3418b.sketch_text.stroke-65"),sQuery(id+"F2.wireOp",EDGE,"fcba4419-a2ee-464f-be9d-58f11bf3418b.sketch_text.stroke-66"),sQuery(id+"F2.wireOp",EDGE,"fcba4419-a2ee-464f-be9d-58f11bf3418b.sketch_text.stroke-67"),sQuery(id+"F2.wireOp",EDGE,"fcba4419-a2ee-464f-be9d-58f11bf3418b.sketch_text.stroke-68"),sQuery(id+"F2.wireOp",EDGE,"fcba4419-a2ee-464f-be9d-58f11bf3418b.sketch_text.stroke-69"),sQuery(id+"F2.wireOp",EDGE,"fcba4419-a2ee-464f-be9d-58f11bf3418b.sketch_text.stroke-70"),sQuery(id+"F2.wireOp",EDGE,"fcba4419-a2ee-464f-be9d-58f11bf3418b.sketch_text.stroke-71"),sQuery(id+"F2.wireOp",EDGE,"fcba4419-a2ee-464f-be9d-58f11bf3418b.sketch_text.stroke-72"),sQuery(id+"F2.wireOp",EDGE,"fcba4419-a2ee-464f-be9d-58f11bf3418b.sketch_text.stroke-73"),sQuery(id+"F2.wireOp",EDGE,"fcba4419-a2ee-464f-be9d-58f11bf3418b.sketch_text.stroke-74"),sQuery(id+"F2.wireOp",EDGE,"fcba4419-a2ee-464f-be9d-58f11bf3418b.sketch_text.stroke-75"),sQuery(id+"F2.wireOp",EDGE,"fcba4419-a2ee-464f-be9d-58f11bf3418b.sketch_text.stroke-76"),sQuery(id+"F2.wireOp",EDGE,"fcba4419-a2ee-464f-be9d-58f11bf3418b.sketch_text.stroke-77"),sQuery(id+"F2.wireOp",EDGE,"fcba4419-a2ee-464f-be9d-58f11bf3418b.sketch_text.stroke-78"),sQuery(id+"F2.wireOp",EDGE,"fcba4419-a2ee-464f-be9d-58f11bf3418b.sketch_text.stroke-79"),sQuery(id+"F2.wireOp",EDGE,"fcba4419-a2ee-464f-be9d-58f11bf3418b.sketch_text.stroke-80"),sQuery(id+"F2.wireOp",EDGE,"fcba4419-a2ee-464f-be9d-58f11bf3418b.sketch_text.stroke-81"),sQuery(id+"F2.wireOp",EDGE,"fcba4419-a2ee-464f-be9d-58f11bf3418b.sketch_text.stroke-82"),sQuery(id+"F2.wireOp",EDGE,"fcba4419-a2ee-464f-be9d-58f11bf3418b.sketch_text.stroke-83"),sQuery(id+"F2.wireOp",EDGE,"fcba4419-a2ee-464f-be9d-58f11bf3418b.sketch_text.stroke-84"),sQuery(id+"F2.wireOp",EDGE,"fcba4419-a2ee-464f-be9d-58f11bf3418b.sketch_text.stroke-85"),sQuery(id+"F2.wireOp",EDGE,"fcba4419-a2ee-464f-be9d-58f11bf3418b.sketch_text.stroke-86"),sQuery(id+"F2.wireOp",EDGE,"fcba4419-a2ee-464f-be9d-58f11bf3418b.sketch_text.stroke-87"),sQuery(id+"F2.wireOp",EDGE,"fcba4419-a2ee-464f-be9d-58f11bf3418b.sketch_text.stroke-88"),sQuery(id+"F2.wireOp",EDGE,"fcba4419-a2ee-464f-be9d-58f11bf3418b.sketch_text.stroke-89"),sQuery(id+"F2.wireOp",EDGE,"fcba4419-a2ee-464f-be9d-58f11bf3418b.sketch_text.stroke-90"),sQuery(id+"F2.wireOp",EDGE,"fcba4419-a2ee-464f-be9d-58f11bf3418b.sketch_text.stroke-91"),sQuery(id+"F2.wireOp",EDGE,"fcba4419-a2ee-464f-be9d-58f11bf3418b.sketch_text.stroke-92"),sQuery(id+"F2.wireOp",EDGE,"fcba4419-a2ee-464f-be9d-58f11bf3418b.sketch_text.stroke-93"),sQuery(id+"F2.wireOp",EDGE,"fcba4419-a2ee-464f-be9d-58f11bf3418b.sketch_text.stroke-94"),sQuery(id+"F2.wireOp",EDGE,"fcba4419-a2ee-464f-be9d-58f11bf3418b.sketch_text.stroke-95"),sQuery(id+"F2.wireOp",EDGE,"fcba4419-a2ee-464f-be9d-58f11bf3418b.sketch_text.stroke-96"),sQuery(id+"F2.wireOp",EDGE,"fcba4419-a2ee-464f-be9d-58f11bf3418b.sketch_text.stroke-97"),sQuery(id+"F2.wireOp",EDGE,"fcba4419-a2ee-464f-be9d-58f11bf3418b.sketch_text.stroke-98"),sQuery(id+"F2.wireOp",EDGE,"fcba4419-a2ee-464f-be9d-58f11bf3418b.sketch_text.stroke-99"),sQuery(id+"F2.wireOp",EDGE,"fcba4419-a2ee-464f-be9d-58f11bf3418b.sketch_text.stroke-100"),sQuery(id+"F2.wireOp",EDGE,"fcba4419-a2ee-464f-be9d-58f11bf3418b.sketch_text.stroke-101"),sQuery(id+"F2.wireOp",EDGE,"fcba4419-a2ee-464f-be9d-58f11bf3418b.sketch_text.stroke-102"),sQuery(id+"F2.wireOp",EDGE,"fcba4419-a2ee-464f-be9d-58f11bf3418b.sketch_text.stroke-103"),sQuery(id+"F2.wireOp",EDGE,"fcba4419-a2ee-464f-be9d-58f11bf3418b.sketch_text.stroke-104"),sQuery(id+"F2.wireOp",EDGE,"fcba4419-a2ee-464f-be9d-58f11bf3418b.sketch_text.stroke-105"),sQuery(id+"F2.wireOp",EDGE,"fcba4419-a2ee-464f-be9d-58f11bf3418b.sketch_text.stroke-106"),sQuery(id+"F2.wireOp",EDGE,"fcba4419-a2ee-464f-be9d-58f11bf3418b.sketch_text.stroke-107"),sQuery(id+"F2.wireOp",EDGE,"fcba4419-a2ee-464f-be9d-58f11bf3418b.sketch_text.stroke-108"),sQuery(id+"F2.wireOp",EDGE,"fcba4419-a2ee-464f-be9d-58f11bf3418b.sketch_text.stroke-109"),sQuery(id+"F2.wireOp",EDGE,"fcba4419-a2ee-464f-be9d-58f11bf3418b.sketch_text.stroke-110"),sQuery(id+"F2.wireOp",EDGE,"fcba4419-a2ee-464f-be9d-58f11bf3418b.sketch_text.stroke-111"),sQuery(id+"F2.wireOp",EDGE,"fcba4419-a2ee-464f-be9d-58f11bf3418b.sketch_text.stroke-112"),sQuery(id+"F2.wireOp",EDGE,"fcba4419-a2ee-464f-be9d-58f11bf3418b.sketch_text.stroke-113"),sQuery(id+"F2.wireOp",EDGE,"fcba4419-a2ee-464f-be9d-58f11bf3418b.sketch_text.stroke-114"),sQuery(id+"F2.wireOp",EDGE,"fcba4419-a2ee-464f-be9d-58f11bf3418b.sketch_text.stroke-115"),sQuery(id+"F2.wireOp",EDGE,"fcba4419-a2ee-464f-be9d-58f11bf3418b.sketch_text.stroke-116"),sQuery(id+"F2.wireOp",EDGE,"fcba4419-a2ee-464f-be9d-58f11bf3418b.sketch_text.stroke-117"),sQuery(id+"F2.wireOp",EDGE,"fcba4419-a2ee-464f-be9d-58f11bf3418b.sketch_text.stroke-118"),sQuery(id+"F2.wireOp",EDGE,"fcba4419-a2ee-464f-be9d-58f11bf3418b.sketch_text.stroke-119"),sQuery(id+"F2.wireOp",EDGE,"fcba4419-a2ee-464f-be9d-58f11bf3418b.sketch_text.stroke-120"),sQuery(id+"F2.wireOp",EDGE,"fcba4419-a2ee-464f-be9d-58f11bf3418b.sketch_text.stroke-121"),sQuery(id+"F2.wireOp",EDGE,"fcba4419-a2ee-464f-be9d-58f11bf3418b.sketch_text.stroke-122"),sQuery(id+"F2.wireOp",EDGE,"fcba4419-a2ee-464f-be9d-58f11bf3418b.sketch_text.stroke-123"),sQuery(id+"F2.wireOp",EDGE,"fcba4419-a2ee-464f-be9d-58f11bf3418b.sketch_text.stroke-124"),sQuery(id+"F2.wireOp",EDGE,"fcba4419-a2ee-464f-be9d-58f11bf3418b.sketch_text.stroke-125"),sQuery(id+"F2.wireOp",EDGE,"fcba4419-a2ee-464f-be9d-58f11bf3418b.sketch_text.stroke-126"),sQuery(id+"F2.wireOp",EDGE,"fcba4419-a2ee-464f-be9d-58f11bf3418b.sketch_text.stroke-127"),sQuery(id+"F2.wireOp",EDGE,"fcba4419-a2ee-464f-be9d-58f11bf3418b.sketch_text.stroke-128"),sQuery(id+"F2.wireOp",EDGE,"fcba4419-a2ee-464f-be9d-58f11bf3418b.sketch_text.stroke-129"),sQuery(id+"F2.wireOp",EDGE,"fcba4419-a2ee-464f-be9d-58f11bf3418b.sketch_text.stroke-130"),sQuery(id+"F2.wireOp",EDGE,"fcba4419-a2ee-464f-be9d-58f11bf3418b.sketch_text.stroke-131"),sQuery(id+"F2.wireOp",EDGE,"fcba4419-a2ee-464f-be9d-58f11bf3418b.sketch_text.stroke-132"),sQuery(id+"F2.wireOp",EDGE,"fcba4419-a2ee-464f-be9d-58f11bf3418b.sketch_text.stroke-133"),sQuery(id+"F2.wireOp",EDGE,"fcba4419-a2ee-464f-be9d-58f11bf3418b.sketch_text.stroke-134"),sQuery(id+"F2.wireOp",EDGE,"fcba4419-a2ee-464f-be9d-58f11bf3418b.sketch_text.stroke-135"),sQuery(id+"F2.wireOp",EDGE,"fcba4419-a2ee-464f-be9d-58f11bf3418b.sketch_text.stroke-136"),sQuery(id+"F2.wireOp",EDGE,"fcba4419-a2ee-464f-be9d-58f11bf3418b.sketch_text.stroke-137"),sQuery(id+"F2.wireOp",EDGE,"fcba4419-a2ee-464f-be9d-58f11bf3418b.sketch_text.stroke-138"),sQuery(id+"F2.wireOp",EDGE,"fcba4419-a2ee-464f-be9d-58f11bf3418b.sketch_text.stroke-139"),sQuery(id+"F2.wireOp",EDGE,"fcba4419-a2ee-464f-be9d-58f11bf3418b.sketch_text.stroke-140"),sQuery(id+"F2.wireOp",EDGE,"fcba4419-a2ee-464f-be9d-58f11bf3418b.sketch_text.stroke-141"),sQuery(id+"F2.wireOp",EDGE,"fcba4419-a2ee-464f-be9d-58f11bf3418b.sketch_text.stroke-142"),sQuery(id+"F2.wireOp",EDGE,"fcba4419-a2ee-464f-be9d-58f11bf3418b.sketch_text.stroke-143"),sQuery(id+"F2.wireOp",EDGE,"fcba4419-a2ee-464f-be9d-58f11bf3418b.sketch_text.stroke-144"),sQuery(id+"F2.wireOp",EDGE,"fcba4419-a2ee-464f-be9d-58f11bf3418b.sketch_text.stroke-145"),sQuery(id+"F2.wireOp",EDGE,"fcba4419-a2ee-464f-be9d-58f11bf3418b.sketch_text.stroke-146"),sQuery(id+"F2.wireOp",EDGE,"fcba4419-a2ee-464f-be9d-58f11bf3418b.sketch_text.stroke-147"),sQuery(id+"F2.wireOp",EDGE,"fcba4419-a2ee-464f-be9d-58f11bf3418b.sketch_text.stroke-148"),sQuery(id+"F2.wireOp",EDGE,"fcba4419-a2ee-464f-be9d-58f11bf3418b.sketch_text.stroke-149"),sQuery(id+"F2.wireOp",EDGE,"fcba4419-a2ee-464f-be9d-58f11bf3418b.sketch_text.stroke-150"),sQuery(id+"F2.wireOp",EDGE,"fcba4419-a2ee-464f-be9d-58f11bf3418b.sketch_text.stroke-151"),sQuery(id+"F2.wireOp",EDGE,"fcba4419-a2ee-464f-be9d-58f11bf3418b.sketch_text.stroke-152"),sQuery(id+"F2.wireOp",EDGE,"fcba4419-a2ee-464f-be9d-58f11bf3418b.sketch_text.stroke-153"),sQuery(id+"F2.wireOp",EDGE,"fcba4419-a2ee-464f-be9d-58f11bf3418b.sketch_text.stroke-154"),sQuery(id+"F2.wireOp",EDGE,"fcba4419-a2ee-464f-be9d-58f11bf3418b.sketch_text.stroke-155"),sQuery(id+"F2.wireOp",EDGE,"fcba4419-a2ee-464f-be9d-58f11bf3418b.sketch_text.stroke-156"),sQuery(id+"F2.wireOp",EDGE,"fcba4419-a2ee-464f-be9d-58f11bf3418b.sketch_text.stroke-157"),sQuery(id+"F2.wireOp",EDGE,"fcba4419-a2ee-464f-be9d-58f11bf3418b.sketch_text.stroke-158"),sQuery(id+"F2.wireOp",EDGE,"fcba4419-a2ee-464f-be9d-58f11bf3418b.sketch_text.stroke-159"),sQuery(id+"F2.wireOp",EDGE,"fcba4419-a2ee-464f-be9d-58f11bf3418b.sketch_text.stroke-160"),sQuery(id+"F2.wireOp",EDGE,"fcba4419-a2ee-464f-be9d-58f11bf3418b.sketch_text.stroke-161"),sQuery(id+"F2.wireOp",EDGE,"fcba4419-a2ee-464f-be9d-58f11bf3418b.sketch_text.stroke-162"),sQuery(id+"F2.wireOp",EDGE,"fcba4419-a2ee-464f-be9d-58f11bf3418b.sketch_text.stroke-163"),sQuery(id+"F2.wireOp",EDGE,"fcba4419-a2ee-464f-be9d-58f11bf3418b.sketch_text.stroke-164"),sQuery(id+"F2.wireOp",EDGE,"fcba4419-a2ee-464f-be9d-58f11bf3418b.sketch_text.stroke-165"),sQuery(id+"F2.wireOp",EDGE,"fcba4419-a2ee-464f-be9d-58f11bf3418b.sketch_text.stroke-166"),sQuery(id+"F2.wireOp",EDGE,"fcba4419-a2ee-464f-be9d-58f11bf3418b.sketch_text.stroke-167"),sQuery(id+"F2.wireOp",EDGE,"fcba4419-a2ee-464f-be9d-58f11bf3418b.sketch_text.stroke-168"),sQuery(id+"F2.wireOp",EDGE,"fcba4419-a2ee-464f-be9d-58f11bf3418b.sketch_text.stroke-169"),sQuery(id+"F2.wireOp",EDGE,"fcba4419-a2ee-464f-be9d-58f11bf3418b.sketch_text.stroke-170"),sQuery(id+"F2.wireOp",EDGE,"fcba4419-a2ee-464f-be9d-58f11bf3418b.sketch_text.stroke-171"),sQuery(id+"F2.wireOp",EDGE,"fcba4419-a2ee-464f-be9d-58f11bf3418b.sketch_text.stroke-172"),sQuery(id+"F2.wireOp",EDGE,"fcba4419-a2ee-464f-be9d-58f11bf3418b.sketch_text.stroke-173"),sQuery(id+"FHMxAyK4CFUKdhS_1.wireOp",EDGE,"1cb9c079-ea9b-4899-8069-e0e3048e911d.sketch_text.stroke-0"),sQuery(id+"FHMxAyK4CFUKdhS_1.wireOp",EDGE,"1cb9c079-ea9b-4899-8069-e0e3048e911d.sketch_text.stroke-1"),sQuery(id+"FHMxAyK4CFUKdhS_1.wireOp",EDGE,"1cb9c079-ea9b-4899-8069-e0e3048e911d.sketch_text.stroke-2"),sQuery(id+"FHMxAyK4CFUKdhS_1.wireOp",EDGE,"1cb9c079-ea9b-4899-8069-e0e3048e911d.sketch_text.stroke-3"),sQuery(id+"FHMxAyK4CFUKdhS_1.wireOp",EDGE,"1cb9c079-ea9b-4899-8069-e0e3048e911d.sketch_text.stroke-4"),sQuery(id+"FHMxAyK4CFUKdhS_1.wireOp",EDGE,"1cb9c079-ea9b-4899-8069-e0e3048e911d.sketch_text.stroke-5"),sQuery(id+"FHMxAyK4CFUKdhS_1.wireOp",EDGE,"1cb9c079-ea9b-4899-8069-e0e3048e911d.sketch_text.stroke-6"),sQuery(id+"FHMxAyK4CFUKdhS_1.wireOp",EDGE,"1cb9c079-ea9b-4899-8069-e0e3048e911d.sketch_text.stroke-7"),sQuery(id+"FHMxAyK4CFUKdhS_1.wireOp",EDGE,"1cb9c079-ea9b-4899-8069-e0e3048e911d.sketch_text.stroke-8"),sQuery(id+"FHMxAyK4CFUKdhS_1.wireOp",EDGE,"1cb9c079-ea9b-4899-8069-e0e3048e911d.sketch_text.stroke-9"),sQuery(id+"FHMxAyK4CFUKdhS_1.wireOp",EDGE,"1cb9c079-ea9b-4899-8069-e0e3048e911d.sketch_text.stroke-10"),sQuery(id+"FHMxAyK4CFUKdhS_1.wireOp",EDGE,"1cb9c079-ea9b-4899-8069-e0e3048e911d.sketch_text.stroke-11"),sQuery(id+"FHMxAyK4CFUKdhS_1.wireOp",EDGE,"1cb9c079-ea9b-4899-8069-e0e3048e911d.sketch_text.stroke-12"),sQuery(id+"FHMxAyK4CFUKdhS_1.wireOp",EDGE,"1cb9c079-ea9b-4899-8069-e0e3048e911d.sketch_text.stroke-13"),sQuery(id+"FHMxAyK4CFUKdhS_1.wireOp",EDGE,"1cb9c079-ea9b-4899-8069-e0e3048e911d.sketch_text.stroke-14"),sQuery(id+"FHMxAyK4CFUKdhS_1.wireOp",EDGE,"1cb9c079-ea9b-4899-8069-e0e3048e911d.sketch_text.stroke-15"),sQuery(id+"FHMxAyK4CFUKdhS_1.wireOp",EDGE,"1cb9c079-ea9b-4899-8069-e0e3048e911d.sketch_text.stroke-16"),sQuery(id+"FHMxAyK4CFUKdhS_1.wireOp",EDGE,"1cb9c079-ea9b-4899-8069-e0e3048e911d.sketch_text.stroke-17"),sQuery(id+"FHMxAyK4CFUKdhS_1.wireOp",EDGE,"1cb9c079-ea9b-4899-8069-e0e3048e911d.sketch_text.stroke-18"),sQuery(id+"FHMxAyK4CFUKdhS_1.wireOp",EDGE,"1cb9c079-ea9b-4899-8069-e0e3048e911d.sketch_text.stroke-19"),sQuery(id+"FHMxAyK4CFUKdhS_1.wireOp",EDGE,"1cb9c079-ea9b-4899-8069-e0e3048e911d.sketch_text.stroke-20"),sQuery(id+"FHMxAyK4CFUKdhS_1.wireOp",EDGE,"1cb9c079-ea9b-4899-8069-e0e3048e911d.sketch_text.stroke-21"),sQuery(id+"FHMxAyK4CFUKdhS_1.wireOp",EDGE,"1cb9c079-ea9b-4899-8069-e0e3048e911d.sketch_text.stroke-22"),sQuery(id+"FHMxAyK4CFUKdhS_1.wireOp",EDGE,"1cb9c079-ea9b-4899-8069-e0e3048e911d.sketch_text.stroke-23"),sQuery(id+"FHMxAyK4CFUKdhS_1.wireOp",EDGE,"1cb9c079-ea9b-4899-8069-e0e3048e911d.sketch_text.stroke-24"),sQuery(id+"FHMxAyK4CFUKdhS_1.wireOp",EDGE,"1cb9c079-ea9b-4899-8069-e0e3048e911d.sketch_text.stroke-25"),sQuery(id+"FHMxAyK4CFUKdhS_1.wireOp",EDGE,"1cb9c079-ea9b-4899-8069-e0e3048e911d.sketch_text.stroke-26"),sQuery(id+"FHMxAyK4CFUKdhS_1.wireOp",EDGE,"1cb9c079-ea9b-4899-8069-e0e3048e911d.sketch_text.stroke-27"),sQuery(id+"FHMxAyK4CFUKdhS_1.wireOp",EDGE,"1cb9c079-ea9b-4899-8069-e0e3048e911d.sketch_text.stroke-28"),sQuery(id+"FHMxAyK4CFUKdhS_1.wireOp",EDGE,"1cb9c079-ea9b-4899-8069-e0e3048e911d.sketch_text.stroke-29"),sQuery(id+"FHMxAyK4CFUKdhS_1.wireOp",EDGE,"1cb9c079-ea9b-4899-8069-e0e3048e911d.sketch_text.stroke-30"),sQuery(id+"FHMxAyK4CFUKdhS_1.wireOp",EDGE,"1cb9c079-ea9b-4899-8069-e0e3048e911d.sketch_text.stroke-31"),sQuery(id+"FHMxAyK4CFUKdhS_1.wireOp",EDGE,"1cb9c079-ea9b-4899-8069-e0e3048e911d.sketch_text.stroke-32"),sQuery(id+"FHMxAyK4CFUKdhS_1.wireOp",EDGE,"1cb9c079-ea9b-4899-8069-e0e3048e911d.sketch_text.stroke-33"),sQuery(id+"FHMxAyK4CFUKdhS_1.wireOp",EDGE,"1cb9c079-ea9b-4899-8069-e0e3048e911d.sketch_text.stroke-34"),sQuery(id+"FHMxAyK4CFUKdhS_1.wireOp",EDGE,"1cb9c079-ea9b-4899-8069-e0e3048e911d.sketch_text.stroke-35"),sQuery(id+"FHMxAyK4CFUKdhS_1.wireOp",EDGE,"1cb9c079-ea9b-4899-8069-e0e3048e911d.sketch_text.stroke-36"),sQuery(id+"FHMxAyK4CFUKdhS_1.wireOp",EDGE,"1cb9c079-ea9b-4899-8069-e0e3048e911d.sketch_text.stroke-37"),sQuery(id+"FHMxAyK4CFUKdhS_1.wireOp",EDGE,"1cb9c079-ea9b-4899-8069-e0e3048e911d.sketch_text.stroke-38"),sQuery(id+"FHMxAyK4CFUKdhS_1.wireOp",EDGE,"1cb9c079-ea9b-4899-8069-e0e3048e911d.sketch_text.stroke-39"),sQuery(id+"FHMxAyK4CFUKdhS_1.wireOp",EDGE,"1cb9c079-ea9b-4899-8069-e0e3048e911d.sketch_text.stroke-40"),sQuery(id+"FHMxAyK4CFUKdhS_1.wireOp",EDGE,"1cb9c079-ea9b-4899-8069-e0e3048e911d.sketch_text.stroke-41"),sQuery(id+"FHMxAyK4CFUKdhS_1.wireOp",EDGE,"1cb9c079-ea9b-4899-8069-e0e3048e911d.sketch_text.stroke-42"),sQuery(id+"FHMxAyK4CFUKdhS_1.wireOp",EDGE,"1cb9c079-ea9b-4899-8069-e0e3048e911d.sketch_text.stroke-43"),sQuery(id+"FHMxAyK4CFUKdhS_1.wireOp",EDGE,"1cb9c079-ea9b-4899-8069-e0e3048e911d.sketch_text.stroke-44"),sQuery(id+"FHMxAyK4CFUKdhS_1.wireOp",EDGE,"1cb9c079-ea9b-4899-8069-e0e3048e911d.sketch_text.stroke-45"),sQuery(id+"FHMxAyK4CFUKdhS_1.wireOp",EDGE,"1cb9c079-ea9b-4899-8069-e0e3048e911d.sketch_text.stroke-46"),sQuery(id+"FHMxAyK4CFUKdhS_1.wireOp",EDGE,"1cb9c079-ea9b-4899-8069-e0e3048e911d.sketch_text.stroke-47"),sQuery(id+"FHMxAyK4CFUKdhS_1.wireOp",EDGE,"1cb9c079-ea9b-4899-8069-e0e3048e911d.sketch_text.stroke-48"),sQuery(id+"FHMxAyK4CFUKdhS_1.wireOp",EDGE,"1cb9c079-ea9b-4899-8069-e0e3048e911d.sketch_text.stroke-49"),sQuery(id+"FHMxAyK4CFUKdhS_1.wireOp",EDGE,"1cb9c079-ea9b-4899-8069-e0e3048e911d.sketch_text.stroke-50"),sQuery(id+"FHMxAyK4CFUKdhS_1.wireOp",EDGE,"1cb9c079-ea9b-4899-8069-e0e3048e911d.sketch_text.stroke-51"),sQuery(id+"FHMxAyK4CFUKdhS_1.wireOp",EDGE,"1cb9c079-ea9b-4899-8069-e0e3048e911d.sketch_text.stroke-52"),sQuery(id+"FHMxAyK4CFUKdhS_1.wireOp",EDGE,"1cb9c079-ea9b-4899-8069-e0e3048e911d.sketch_text.stroke-53"),sQuery(id+"FHMxAyK4CFUKdhS_1.wireOp",EDGE,"1cb9c079-ea9b-4899-8069-e0e3048e911d.sketch_text.stroke-54"),sQuery(id+"FHMxAyK4CFUKdhS_1.wireOp",EDGE,"1cb9c079-ea9b-4899-8069-e0e3048e911d.sketch_text.stroke-55"),sQuery(id+"FHMxAyK4CFUKdhS_1.wireOp",EDGE,"1cb9c079-ea9b-4899-8069-e0e3048e911d.sketch_text.stroke-56"),sQuery(id+"FHMxAyK4CFUKdhS_1.wireOp",EDGE,"1cb9c079-ea9b-4899-8069-e0e3048e911d.sketch_text.stroke-57"),sQuery(id+"FHMxAyK4CFUKdhS_1.wireOp",EDGE,"1cb9c079-ea9b-4899-8069-e0e3048e911d.sketch_text.stroke-58"),sQuery(id+"FHMxAyK4CFUKdhS_1.wireOp",EDGE,"1cb9c079-ea9b-4899-8069-e0e3048e911d.sketch_text.stroke-59"),sQuery(id+"FHMxAyK4CFUKdhS_1.wireOp",EDGE,"1cb9c079-ea9b-4899-8069-e0e3048e911d.sketch_text.stroke-60"),sQuery(id+"FHMxAyK4CFUKdhS_1.wireOp",EDGE,"1cb9c079-ea9b-4899-8069-e0e3048e911d.sketch_text.stroke-61"),sQuery(id+"FHMxAyK4CFUKdhS_1.wireOp",EDGE,"1cb9c079-ea9b-4899-8069-e0e3048e911d.sketch_text.stroke-62"),sQuery(id+"FHMxAyK4CFUKdhS_1.wireOp",EDGE,"1cb9c079-ea9b-4899-8069-e0e3048e911d.sketch_text.stroke-71"),sQuery(id+"FHMxAyK4CFUKdhS_1.wireOp",EDGE,"1cb9c079-ea9b-4899-8069-e0e3048e911d.sketch_text.stroke-72"),sQuery(id+"FHMxAyK4CFUKdhS_1.wireOp",EDGE,"1cb9c079-ea9b-4899-8069-e0e3048e911d.sketch_text.stroke-73"),sQuery(id+"FHMxAyK4CFUKdhS_1.wireOp",EDGE,"1cb9c079-ea9b-4899-8069-e0e3048e911d.sketch_text.stroke-74"),sQuery(id+"FHMxAyK4CFUKdhS_1.wireOp",EDGE,"1cb9c079-ea9b-4899-8069-e0e3048e911d.sketch_text.stroke-75"),sQuery(id+"FHMxAyK4CFUKdhS_1.wireOp",EDGE,"1cb9c079-ea9b-4899-8069-e0e3048e911d.sketch_text.stroke-76"),sQuery(id+"FHMxAyK4CFUKdhS_1.wireOp",EDGE,"1cb9c079-ea9b-4899-8069-e0e3048e911d.sketch_text.stroke-77"),sQuery(id+"FHMxAyK4CFUKdhS_1.wireOp",EDGE,"1cb9c079-ea9b-4899-8069-e0e3048e911d.sketch_text.stroke-78"),sQuery(id+"FHMxAyK4CFUKdhS_1.wireOp",EDGE,"1cb9c079-ea9b-4899-8069-e0e3048e911d.sketch_text.stroke-79"),sQuery(id+"FHMxAyK4CFUKdhS_1.wireOp",EDGE,"1cb9c079-ea9b-4899-8069-e0e3048e911d.sketch_text.stroke-80"),sQuery(id+"FHMxAyK4CFUKdhS_1.wireOp",EDGE,"1cb9c079-ea9b-4899-8069-e0e3048e911d.sketch_text.stroke-81"),sQuery(id+"FHMxAyK4CFUKdhS_1.wireOp",EDGE,"1cb9c079-ea9b-4899-8069-e0e3048e911d.sketch_text.stroke-82"),sQuery(id+"FHMxAyK4CFUKdhS_1.wireOp",EDGE,"1cb9c079-ea9b-4899-8069-e0e3048e911d.sketch_text.stroke-83"),sQuery(id+"FHMxAyK4CFUKdhS_1.wireOp",EDGE,"1cb9c079-ea9b-4899-8069-e0e3048e911d.sketch_text.stroke-84"),sQuery(id+"FHMxAyK4CFUKdhS_1.wireOp",EDGE,"1cb9c079-ea9b-4899-8069-e0e3048e911d.sketch_text.stroke-85"),sQuery(id+"FHMxAyK4CFUKdhS_1.wireOp",EDGE,"1cb9c079-ea9b-4899-8069-e0e3048e911d.sketch_text.stroke-86"),sQuery(id+"FHMxAyK4CFUKdhS_1.wireOp",EDGE,"1cb9c079-ea9b-4899-8069-e0e3048e911d.sketch_text.stroke-87"),sQuery(id+"FHMxAyK4CFUKdhS_1.wireOp",EDGE,"1cb9c079-ea9b-4899-8069-e0e3048e911d.sketch_text.stroke-88"),sQuery(id+"FHMxAyK4CFUKdhS_1.wireOp",EDGE,"1cb9c079-ea9b-4899-8069-e0e3048e911d.sketch_text.stroke-89"),sQuery(id+"FHMxAyK4CFUKdhS_1.wireOp",EDGE,"1cb9c079-ea9b-4899-8069-e0e3048e911d.sketch_text.stroke-90"),sQuery(id+"FHMxAyK4CFUKdhS_1.wireOp",EDGE,"1cb9c079-ea9b-4899-8069-e0e3048e911d.sketch_text.stroke-91"),sQuery(id+"FHMxAyK4CFUKdhS_1.wireOp",EDGE,"1cb9c079-ea9b-4899-8069-e0e3048e911d.sketch_text.stroke-92"),sQuery(id+"FHMxAyK4CFUKdhS_1.wireOp",EDGE,"1cb9c079-ea9b-4899-8069-e0e3048e911d.sketch_text.stroke-93"),sQuery(id+"FHMxAyK4CFUKdhS_1.wireOp",EDGE,"1cb9c079-ea9b-4899-8069-e0e3048e911d.sketch_text.stroke-94"),sQuery(id+"FHMxAyK4CFUKdhS_1.wireOp",EDGE,"1cb9c079-ea9b-4899-8069-e0e3048e911d.sketch_text.stroke-95"),sQuery(id+"FHMxAyK4CFUKdhS_1.wireOp",EDGE,"1cb9c079-ea9b-4899-8069-e0e3048e911d.sketch_text.stroke-96"),sQuery(id+"FHMxAyK4CFUKdhS_1.wireOp",EDGE,"1cb9c079-ea9b-4899-8069-e0e3048e911d.sketch_text.stroke-97"),sQuery(id+"FHMxAyK4CFUKdhS_1.wireOp",EDGE,"1cb9c079-ea9b-4899-8069-e0e3048e911d.sketch_text.stroke-103"),sQuery(id+"FHMxAyK4CFUKdhS_1.wireOp",EDGE,"1cb9c079-ea9b-4899-8069-e0e3048e911d.sketch_text.stroke-104"),sQuery(id+"FHMxAyK4CFUKdhS_1.wireOp",EDGE,"1cb9c079-ea9b-4899-8069-e0e3048e911d.sketch_text.stroke-105"),sQuery(id+"FHMxAyK4CFUKdhS_1.wireOp",EDGE,"1cb9c079-ea9b-4899-8069-e0e3048e911d.sketch_text.stroke-106"),sQuery(id+"FHMxAyK4CFUKdhS_1.wireOp",EDGE,"1cb9c079-ea9b-4899-8069-e0e3048e911d.sketch_text.stroke-107"),sQuery(id+"FHMxAyK4CFUKdhS_1.wireOp",EDGE,"1cb9c079-ea9b-4899-8069-e0e3048e911d.sketch_text.stroke-108"),sQuery(id+"FHMxAyK4CFUKdhS_1.wireOp",EDGE,"1cb9c079-ea9b-4899-8069-e0e3048e911d.sketch_text.stroke-109"),sQuery(id+"FHMxAyK4CFUKdhS_1.wireOp",EDGE,"1cb9c079-ea9b-4899-8069-e0e3048e911d.sketch_text.stroke-110"),sQuery(id+"FHMxAyK4CFUKdhS_1.wireOp",EDGE,"1cb9c079-ea9b-4899-8069-e0e3048e911d.sketch_text.stroke-111"),sQuery(id+"FHMxAyK4CFUKdhS_1.wireOp",EDGE,"1cb9c079-ea9b-4899-8069-e0e3048e911d.sketch_text.stroke-112"),sQuery(id+"FHMxAyK4CFUKdhS_1.wireOp",EDGE,"1cb9c079-ea9b-4899-8069-e0e3048e911d.sketch_text.stroke-113"),sQuery(id+"FHMxAyK4CFUKdhS_1.wireOp",EDGE,"1cb9c079-ea9b-4899-8069-e0e3048e911d.sketch_text.stroke-114"),sQuery(id+"FHMxAyK4CFUKdhS_1.wireOp",EDGE,"1cb9c079-ea9b-4899-8069-e0e3048e911d.sketch_text.stroke-115"),sQuery(id+"FHMxAyK4CFUKdhS_1.wireOp",EDGE,"1cb9c079-ea9b-4899-8069-e0e3048e911d.sketch_text.stroke-116"),sQuery(id+"FHMxAyK4CFUKdhS_1.wireOp",EDGE,"1cb9c079-ea9b-4899-8069-e0e3048e911d.sketch_text.stroke-117"),sQuery(id+"FHMxAyK4CFUKdhS_1.wireOp",EDGE,"1cb9c079-ea9b-4899-8069-e0e3048e911d.sketch_text.stroke-118"),sQuery(id+"FHMxAyK4CFUKdhS_1.wireOp",EDGE,"1cb9c079-ea9b-4899-8069-e0e3048e911d.sketch_text.stroke-119"),sQuery(id+"FHMxAyK4CFUKdhS_1.wireOp",EDGE,"1cb9c079-ea9b-4899-8069-e0e3048e911d.sketch_text.stroke-120"),sQuery(id+"FHMxAyK4CFUKdhS_1.wireOp",EDGE,"1cb9c079-ea9b-4899-8069-e0e3048e911d.sketch_text.stroke-121"),sQuery(id+"FHMxAyK4CFUKdhS_1.wireOp",EDGE,"1cb9c079-ea9b-4899-8069-e0e3048e911d.sketch_text.stroke-122"),sQuery(id+"FHMxAyK4CFUKdhS_1.wireOp",EDGE,"1cb9c079-ea9b-4899-8069-e0e3048e911d.sketch_text.stroke-123"),sQuery(id+"FHMxAyK4CFUKdhS_1.wireOp",EDGE,"1cb9c079-ea9b-4899-8069-e0e3048e911d.sketch_text.stroke-124"),sQuery(id+"FHMxAyK4CFUKdhS_1.wireOp",EDGE,"1cb9c079-ea9b-4899-8069-e0e3048e911d.sketch_text.stroke-125"),sQuery(id+"FHMxAyK4CFUKdhS_1.wireOp",EDGE,"1cb9c079-ea9b-4899-8069-e0e3048e911d.sketch_text.stroke-126"),sQuery(id+"FHMxAyK4CFUKdhS_1.wireOp",EDGE,"1cb9c079-ea9b-4899-8069-e0e3048e911d.sketch_text.stroke-127"),sQuery(id+"FHMxAyK4CFUKdhS_1.wireOp",EDGE,"1cb9c079-ea9b-4899-8069-e0e3048e911d.sketch_text.stroke-128"),sQuery(id+"FHMxAyK4CFUKdhS_1.wireOp",EDGE,"1cb9c079-ea9b-4899-8069-e0e3048e911d.sketch_text.stroke-129"),sQuery(id+"FHMxAyK4CFUKdhS_1.wireOp",EDGE,"1cb9c079-ea9b-4899-8069-e0e3048e911d.sketch_text.stroke-130"),sQuery(id+"FHMxAyK4CFUKdhS_1.wireOp",EDGE,"1cb9c079-ea9b-4899-8069-e0e3048e911d.sketch_text.stroke-131"),sQuery(id+"FHMxAyK4CFUKdhS_1.wireOp",EDGE,"1cb9c079-ea9b-4899-8069-e0e3048e911d.sketch_text.stroke-132"),sQuery(id+"FHMxAyK4CFUKdhS_1.wireOp",EDGE,"1cb9c079-ea9b-4899-8069-e0e3048e911d.sketch_text.stroke-133"),sQuery(id+"FHMxAyK4CFUKdhS_1.wireOp",EDGE,"1cb9c079-ea9b-4899-8069-e0e3048e911d.sketch_text.stroke-134"),sQuery(id+"FHMxAyK4CFUKdhS_1.wireOp",EDGE,"1cb9c079-ea9b-4899-8069-e0e3048e911d.sketch_text.stroke-135"),sQuery(id+"FHMxAyK4CFUKdhS_1.wireOp",EDGE,"1cb9c079-ea9b-4899-8069-e0e3048e911d.sketch_text.stroke-136"),sQuery(id+"FHMxAyK4CFUKdhS_1.wireOp",EDGE,"1cb9c079-ea9b-4899-8069-e0e3048e911d.sketch_text.stroke-137"),sQuery(id+"FHMxAyK4CFUKdhS_1.wireOp",EDGE,"1cb9c079-ea9b-4899-8069-e0e3048e911d.sketch_text.stroke-138"),sQuery(id+"FHMxAyK4CFUKdhS_1.wireOp",EDGE,"1cb9c079-ea9b-4899-8069-e0e3048e911d.sketch_text.stroke-139"),sQuery(id+"FHMxAyK4CFUKdhS_1.wireOp",EDGE,"1cb9c079-ea9b-4899-8069-e0e3048e911d.sketch_text.stroke-140"),sQuery(id+"FHMxAyK4CFUKdhS_1.wireOp",EDGE,"1cb9c079-ea9b-4899-8069-e0e3048e911d.sketch_text.stroke-141"),sQuery(id+"FHMxAyK4CFUKdhS_1.wireOp",EDGE,"1cb9c079-ea9b-4899-8069-e0e3048e911d.sketch_text.stroke-142"),sQuery(id+"FHMxAyK4CFUKdhS_1.wireOp",EDGE,"1cb9c079-ea9b-4899-8069-e0e3048e911d.sketch_text.stroke-143"),sQuery(id+"FHMxAyK4CFUKdhS_1.wireOp",EDGE,"1cb9c079-ea9b-4899-8069-e0e3048e911d.sketch_text.stroke-144"),sQuery(id+"FHMxAyK4CFUKdhS_1.wireOp",EDGE,"1cb9c079-ea9b-4899-8069-e0e3048e911d.sketch_text.stroke-145"),sQuery(id+"FHMxAyK4CFUKdhS_1.wireOp",EDGE,"1cb9c079-ea9b-4899-8069-e0e3048e911d.sketch_text.stroke-146"),sQuery(id+"FHMxAyK4CFUKdhS_1.wireOp",EDGE,"1cb9c079-ea9b-4899-8069-e0e3048e911d.sketch_text.stroke-147"),sQuery(id+"FHMxAyK4CFUKdhS_1.wireOp",EDGE,"1cb9c079-ea9b-4899-8069-e0e3048e911d.sketch_text.stroke-148"),sQuery(id+"FHMxAyK4CFUKdhS_1.wireOp",EDGE,"1cb9c079-ea9b-4899-8069-e0e3048e911d.sketch_text.stroke-149"),sQuery(id+"FHMxAyK4CFUKdhS_1.wireOp",EDGE,"1cb9c079-ea9b-4899-8069-e0e3048e911d.sketch_text.stroke-150"),sQuery(id+"FHMxAyK4CFUKdhS_1.wireOp",EDGE,"1cb9c079-ea9b-4899-8069-e0e3048e911d.sketch_text.stroke-151"),sQuery(id+"FHMxAyK4CFUKdhS_1.wireOp",EDGE,"1cb9c079-ea9b-4899-8069-e0e3048e911d.sketch_text.stroke-152"),sQuery(id+"FHMxAyK4CFUKdhS_1.wireOp",EDGE,"1cb9c079-ea9b-4899-8069-e0e3048e911d.sketch_text.stroke-153"),sQuery(id+"FHMxAyK4CFUKdhS_1.wireOp",EDGE,"1cb9c079-ea9b-4899-8069-e0e3048e911d.sketch_text.stroke-159"),sQuery(id+"FHMxAyK4CFUKdhS_1.wireOp",EDGE,"1cb9c079-ea9b-4899-8069-e0e3048e911d.sketch_text.stroke-160"),sQuery(id+"FHMxAyK4CFUKdhS_1.wireOp",EDGE,"1cb9c079-ea9b-4899-8069-e0e3048e911d.sketch_text.stroke-161"),sQuery(id+"FHMxAyK4CFUKdhS_1.wireOp",EDGE,"1cb9c079-ea9b-4899-8069-e0e3048e911d.sketch_text.stroke-162"),sQuery(id+"FHMxAyK4CFUKdhS_1.wireOp",EDGE,"1cb9c079-ea9b-4899-8069-e0e3048e911d.sketch_text.stroke-163"),sQuery(id+"FHMxAyK4CFUKdhS_1.wireOp",EDGE,"1cb9c079-ea9b-4899-8069-e0e3048e911d.sketch_text.stroke-164"),sQuery(id+"FHMxAyK4CFUKdhS_1.wireOp",EDGE,"1cb9c079-ea9b-4899-8069-e0e3048e911d.sketch_text.stroke-165"),sQuery(id+"FHMxAyK4CFUKdhS_1.wireOp",EDGE,"1cb9c079-ea9b-4899-8069-e0e3048e911d.sketch_text.stroke-166"),sQuery(id+"FHMxAyK4CFUKdhS_1.wireOp",EDGE,"1cb9c079-ea9b-4899-8069-e0e3048e911d.sketch_text.stroke-167"),sQuery(id+"FHMxAyK4CFUKdhS_1.wireOp",EDGE,"1cb9c079-ea9b-4899-8069-e0e3048e911d.sketch_text.stroke-168"),sQuery(id+"FHMxAyK4CFUKdhS_1.wireOp",EDGE,"1cb9c079-ea9b-4899-8069-e0e3048e911d.sketch_text.stroke-169"),sQuery(id+"FHMxAyK4CFUKdhS_1.wireOp",EDGE,"1cb9c079-ea9b-4899-8069-e0e3048e911d.sketch_text.stroke-170"),sQuery(id+"FHMxAyK4CFUKdhS_1.wireOp",EDGE,"1cb9c079-ea9b-4899-8069-e0e3048e911d.sketch_text.stroke-171"),sQuery(id+"FHMxAyK4CFUKdhS_1.wireOp",EDGE,"1cb9c079-ea9b-4899-8069-e0e3048e911d.sketch_text.stroke-172"),sQuery(id+"FHMxAyK4CFUKdhS_1.wireOp",EDGE,"1cb9c079-ea9b-4899-8069-e0e3048e911d.sketch_text.stroke-173"),sQuery(id+"FHMxAyK4CFUKdhS_1.wireOp",EDGE,"1cb9c079-ea9b-4899-8069-e0e3048e911d.sketch_text.stroke-174"),sQuery(id+"FHMxAyK4CFUKdhS_1.wireOp",EDGE,"1cb9c079-ea9b-4899-8069-e0e3048e911d.sketch_text.stroke-175"),sQuery(id+"FHMxAyK4CFUKdhS_1.wireOp",EDGE,"1cb9c079-ea9b-4899-8069-e0e3048e911d.sketch_text.stroke-176"),sQuery(id+"FHMxAyK4CFUKdhS_1.wireOp",EDGE,"1cb9c079-ea9b-4899-8069-e0e3048e911d.sketch_text.stroke-177"),sQuery(id+"FHMxAyK4CFUKdhS_1.wireOp",EDGE,"1cb9c079-ea9b-4899-8069-e0e3048e911d.sketch_text.stroke-178"),sQuery(id+"FHMxAyK4CFUKdhS_1.wireOp",EDGE,"1cb9c079-ea9b-4899-8069-e0e3048e911d.sketch_text.stroke-179"),sQuery(id+"FHMxAyK4CFUKdhS_1.wireOp",EDGE,"1cb9c079-ea9b-4899-8069-e0e3048e911d.sketch_text.stroke-180"),subQ2,sQuery(id+"F3.wireOp",EDGE,"6ee83ff3-586e-4dbe-aaea-af71240543bd")])],"isStart":true})])],"derivedFrom":makeQuery(id+"F4.opExtrude","CAP_EDGE",EDGE,{"disambiguationData":[OSD([subQ2])],"isStart":true})});}
            var Q3;
            {var subQ0=sQuery(id+"F3.wireOp",EDGE,"8007402e-1a4e-4a06-85a5-2af08e553504");var subQ1=sQuery(id+"F0.wireOp",EDGE,"E0.top");var subQ2=sQuery(id+"F3.wireOp",EDGE,"6ee83ff3-586e-4dbe-aaea-af71240543bd");var subQ3=sQuery(id+"F0.wireOp",EDGE,"E0.bottom");Q3=makeQuery(id+"F4.boolean.opBoolean","SPLIT",EDGE,{"disambiguationData":[TD([makeQuery(id+"F1.opExtrude","CAP_FACE",FACE,{"disambiguationData":[OSD([subQ3,subQ1,sQuery(id+"F0.wireOp",EDGE,"E0.left"),sQuery(id+"F0.wireOp",EDGE,"E0.right")])],"isStart":false}),makeQuery(id+"F1.opExtrude","SWEPT_FACE",FACE,{"disambiguationData":[OSD([subQ1])]}),makeQuery(id+"F4.opExtrude","SWEPT_FACE",FACE,{"disambiguationData":[OSD([subQ0])]}),makeQuery(id+"F4.opExtrude","CAP_FACE",FACE,{"disambiguationData":[OSD([subQ3,sQuery(id+"F2.wireOp",EDGE,"fcba4419-a2ee-464f-be9d-58f11bf3418b.sketch_text.stroke-0"),sQuery(id+"F2.wireOp",EDGE,"fcba4419-a2ee-464f-be9d-58f11bf3418b.sketch_text.stroke-1"),sQuery(id+"F2.wireOp",EDGE,"fcba4419-a2ee-464f-be9d-58f11bf3418b.sketch_text.stroke-2"),sQuery(id+"F2.wireOp",EDGE,"fcba4419-a2ee-464f-be9d-58f11bf3418b.sketch_text.stroke-3"),sQuery(id+"F2.wireOp",EDGE,"fcba4419-a2ee-464f-be9d-58f11bf3418b.sketch_text.stroke-4"),sQuery(id+"F2.wireOp",EDGE,"fcba4419-a2ee-464f-be9d-58f11bf3418b.sketch_text.stroke-5"),sQuery(id+"F2.wireOp",EDGE,"fcba4419-a2ee-464f-be9d-58f11bf3418b.sketch_text.stroke-6"),sQuery(id+"F2.wireOp",EDGE,"fcba4419-a2ee-464f-be9d-58f11bf3418b.sketch_text.stroke-7"),sQuery(id+"F2.wireOp",EDGE,"fcba4419-a2ee-464f-be9d-58f11bf3418b.sketch_text.stroke-8"),sQuery(id+"F2.wireOp",EDGE,"fcba4419-a2ee-464f-be9d-58f11bf3418b.sketch_text.stroke-9"),sQuery(id+"F2.wireOp",EDGE,"fcba4419-a2ee-464f-be9d-58f11bf3418b.sketch_text.stroke-10"),sQuery(id+"F2.wireOp",EDGE,"fcba4419-a2ee-464f-be9d-58f11bf3418b.sketch_text.stroke-11"),sQuery(id+"F2.wireOp",EDGE,"fcba4419-a2ee-464f-be9d-58f11bf3418b.sketch_text.stroke-12"),sQuery(id+"F2.wireOp",EDGE,"fcba4419-a2ee-464f-be9d-58f11bf3418b.sketch_text.stroke-13"),sQuery(id+"F2.wireOp",EDGE,"fcba4419-a2ee-464f-be9d-58f11bf3418b.sketch_text.stroke-14"),sQuery(id+"F2.wireOp",EDGE,"fcba4419-a2ee-464f-be9d-58f11bf3418b.sketch_text.stroke-15"),sQuery(id+"F2.wireOp",EDGE,"fcba4419-a2ee-464f-be9d-58f11bf3418b.sketch_text.stroke-16"),sQuery(id+"F2.wireOp",EDGE,"fcba4419-a2ee-464f-be9d-58f11bf3418b.sketch_text.stroke-17"),sQuery(id+"F2.wireOp",EDGE,"fcba4419-a2ee-464f-be9d-58f11bf3418b.sketch_text.stroke-18"),sQuery(id+"F2.wireOp",EDGE,"fcba4419-a2ee-464f-be9d-58f11bf3418b.sketch_text.stroke-19"),sQuery(id+"F2.wireOp",EDGE,"fcba4419-a2ee-464f-be9d-58f11bf3418b.sketch_text.stroke-20"),sQuery(id+"F2.wireOp",EDGE,"fcba4419-a2ee-464f-be9d-58f11bf3418b.sketch_text.stroke-21"),sQuery(id+"F2.wireOp",EDGE,"fcba4419-a2ee-464f-be9d-58f11bf3418b.sketch_text.stroke-22"),sQuery(id+"F2.wireOp",EDGE,"fcba4419-a2ee-464f-be9d-58f11bf3418b.sketch_text.stroke-23"),sQuery(id+"F2.wireOp",EDGE,"fcba4419-a2ee-464f-be9d-58f11bf3418b.sketch_text.stroke-24"),sQuery(id+"F2.wireOp",EDGE,"fcba4419-a2ee-464f-be9d-58f11bf3418b.sketch_text.stroke-25"),sQuery(id+"F2.wireOp",EDGE,"fcba4419-a2ee-464f-be9d-58f11bf3418b.sketch_text.stroke-26"),sQuery(id+"F2.wireOp",EDGE,"fcba4419-a2ee-464f-be9d-58f11bf3418b.sketch_text.stroke-27"),sQuery(id+"F2.wireOp",EDGE,"fcba4419-a2ee-464f-be9d-58f11bf3418b.sketch_text.stroke-28"),sQuery(id+"F2.wireOp",EDGE,"fcba4419-a2ee-464f-be9d-58f11bf3418b.sketch_text.stroke-29"),sQuery(id+"F2.wireOp",EDGE,"fcba4419-a2ee-464f-be9d-58f11bf3418b.sketch_text.stroke-30"),sQuery(id+"F2.wireOp",EDGE,"fcba4419-a2ee-464f-be9d-58f11bf3418b.sketch_text.stroke-31"),sQuery(id+"F2.wireOp",EDGE,"fcba4419-a2ee-464f-be9d-58f11bf3418b.sketch_text.stroke-32"),sQuery(id+"F2.wireOp",EDGE,"fcba4419-a2ee-464f-be9d-58f11bf3418b.sketch_text.stroke-33"),sQuery(id+"F2.wireOp",EDGE,"fcba4419-a2ee-464f-be9d-58f11bf3418b.sketch_text.stroke-34"),sQuery(id+"F2.wireOp",EDGE,"fcba4419-a2ee-464f-be9d-58f11bf3418b.sketch_text.stroke-35"),sQuery(id+"F2.wireOp",EDGE,"fcba4419-a2ee-464f-be9d-58f11bf3418b.sketch_text.stroke-36"),sQuery(id+"F2.wireOp",EDGE,"fcba4419-a2ee-464f-be9d-58f11bf3418b.sketch_text.stroke-37"),sQuery(id+"F2.wireOp",EDGE,"fcba4419-a2ee-464f-be9d-58f11bf3418b.sketch_text.stroke-38"),sQuery(id+"F2.wireOp",EDGE,"fcba4419-a2ee-464f-be9d-58f11bf3418b.sketch_text.stroke-39"),sQuery(id+"F2.wireOp",EDGE,"fcba4419-a2ee-464f-be9d-58f11bf3418b.sketch_text.stroke-40"),sQuery(id+"F2.wireOp",EDGE,"fcba4419-a2ee-464f-be9d-58f11bf3418b.sketch_text.stroke-41"),sQuery(id+"F2.wireOp",EDGE,"fcba4419-a2ee-464f-be9d-58f11bf3418b.sketch_text.stroke-42"),sQuery(id+"F2.wireOp",EDGE,"fcba4419-a2ee-464f-be9d-58f11bf3418b.sketch_text.stroke-43"),sQuery(id+"F2.wireOp",EDGE,"fcba4419-a2ee-464f-be9d-58f11bf3418b.sketch_text.stroke-44"),sQuery(id+"F2.wireOp",EDGE,"fcba4419-a2ee-464f-be9d-58f11bf3418b.sketch_text.stroke-45"),sQuery(id+"F2.wireOp",EDGE,"fcba4419-a2ee-464f-be9d-58f11bf3418b.sketch_text.stroke-46"),sQuery(id+"F2.wireOp",EDGE,"fcba4419-a2ee-464f-be9d-58f11bf3418b.sketch_text.stroke-47"),sQuery(id+"F2.wireOp",EDGE,"fcba4419-a2ee-464f-be9d-58f11bf3418b.sketch_text.stroke-48"),sQuery(id+"F2.wireOp",EDGE,"fcba4419-a2ee-464f-be9d-58f11bf3418b.sketch_text.stroke-49"),sQuery(id+"F2.wireOp",EDGE,"fcba4419-a2ee-464f-be9d-58f11bf3418b.sketch_text.stroke-50"),sQuery(id+"F2.wireOp",EDGE,"fcba4419-a2ee-464f-be9d-58f11bf3418b.sketch_text.stroke-51"),sQuery(id+"F2.wireOp",EDGE,"fcba4419-a2ee-464f-be9d-58f11bf3418b.sketch_text.stroke-52"),sQuery(id+"F2.wireOp",EDGE,"fcba4419-a2ee-464f-be9d-58f11bf3418b.sketch_text.stroke-53"),sQuery(id+"F2.wireOp",EDGE,"fcba4419-a2ee-464f-be9d-58f11bf3418b.sketch_text.stroke-54"),sQuery(id+"F2.wireOp",EDGE,"fcba4419-a2ee-464f-be9d-58f11bf3418b.sketch_text.stroke-55"),sQuery(id+"F2.wireOp",EDGE,"fcba4419-a2ee-464f-be9d-58f11bf3418b.sketch_text.stroke-56"),sQuery(id+"F2.wireOp",EDGE,"fcba4419-a2ee-464f-be9d-58f11bf3418b.sketch_text.stroke-57"),sQuery(id+"F2.wireOp",EDGE,"fcba4419-a2ee-464f-be9d-58f11bf3418b.sketch_text.stroke-58"),sQuery(id+"F2.wireOp",EDGE,"fcba4419-a2ee-464f-be9d-58f11bf3418b.sketch_text.stroke-59"),sQuery(id+"F2.wireOp",EDGE,"fcba4419-a2ee-464f-be9d-58f11bf3418b.sketch_text.stroke-60"),sQuery(id+"F2.wireOp",EDGE,"fcba4419-a2ee-464f-be9d-58f11bf3418b.sketch_text.stroke-61"),sQuery(id+"F2.wireOp",EDGE,"fcba4419-a2ee-464f-be9d-58f11bf3418b.sketch_text.stroke-62"),sQuery(id+"F2.wireOp",EDGE,"fcba4419-a2ee-464f-be9d-58f11bf3418b.sketch_text.stroke-63"),sQuery(id+"F2.wireOp",EDGE,"fcba4419-a2ee-464f-be9d-58f11bf3418b.sketch_text.stroke-64"),sQuery(id+"F2.wireOp",EDGE,"fcba4419-a2ee-464f-be9d-58f11bf3418b.sketch_text.stroke-65"),sQuery(id+"F2.wireOp",EDGE,"fcba4419-a2ee-464f-be9d-58f11bf3418b.sketch_text.stroke-66"),sQuery(id+"F2.wireOp",EDGE,"fcba4419-a2ee-464f-be9d-58f11bf3418b.sketch_text.stroke-67"),sQuery(id+"F2.wireOp",EDGE,"fcba4419-a2ee-464f-be9d-58f11bf3418b.sketch_text.stroke-68"),sQuery(id+"F2.wireOp",EDGE,"fcba4419-a2ee-464f-be9d-58f11bf3418b.sketch_text.stroke-69"),sQuery(id+"F2.wireOp",EDGE,"fcba4419-a2ee-464f-be9d-58f11bf3418b.sketch_text.stroke-70"),sQuery(id+"F2.wireOp",EDGE,"fcba4419-a2ee-464f-be9d-58f11bf3418b.sketch_text.stroke-71"),sQuery(id+"F2.wireOp",EDGE,"fcba4419-a2ee-464f-be9d-58f11bf3418b.sketch_text.stroke-72"),sQuery(id+"F2.wireOp",EDGE,"fcba4419-a2ee-464f-be9d-58f11bf3418b.sketch_text.stroke-73"),sQuery(id+"F2.wireOp",EDGE,"fcba4419-a2ee-464f-be9d-58f11bf3418b.sketch_text.stroke-74"),sQuery(id+"F2.wireOp",EDGE,"fcba4419-a2ee-464f-be9d-58f11bf3418b.sketch_text.stroke-75"),sQuery(id+"F2.wireOp",EDGE,"fcba4419-a2ee-464f-be9d-58f11bf3418b.sketch_text.stroke-76"),sQuery(id+"F2.wireOp",EDGE,"fcba4419-a2ee-464f-be9d-58f11bf3418b.sketch_text.stroke-77"),sQuery(id+"F2.wireOp",EDGE,"fcba4419-a2ee-464f-be9d-58f11bf3418b.sketch_text.stroke-78"),sQuery(id+"F2.wireOp",EDGE,"fcba4419-a2ee-464f-be9d-58f11bf3418b.sketch_text.stroke-79"),sQuery(id+"F2.wireOp",EDGE,"fcba4419-a2ee-464f-be9d-58f11bf3418b.sketch_text.stroke-80"),sQuery(id+"F2.wireOp",EDGE,"fcba4419-a2ee-464f-be9d-58f11bf3418b.sketch_text.stroke-81"),sQuery(id+"F2.wireOp",EDGE,"fcba4419-a2ee-464f-be9d-58f11bf3418b.sketch_text.stroke-82"),sQuery(id+"F2.wireOp",EDGE,"fcba4419-a2ee-464f-be9d-58f11bf3418b.sketch_text.stroke-83"),sQuery(id+"F2.wireOp",EDGE,"fcba4419-a2ee-464f-be9d-58f11bf3418b.sketch_text.stroke-84"),sQuery(id+"F2.wireOp",EDGE,"fcba4419-a2ee-464f-be9d-58f11bf3418b.sketch_text.stroke-85"),sQuery(id+"F2.wireOp",EDGE,"fcba4419-a2ee-464f-be9d-58f11bf3418b.sketch_text.stroke-86"),sQuery(id+"F2.wireOp",EDGE,"fcba4419-a2ee-464f-be9d-58f11bf3418b.sketch_text.stroke-87"),sQuery(id+"F2.wireOp",EDGE,"fcba4419-a2ee-464f-be9d-58f11bf3418b.sketch_text.stroke-88"),sQuery(id+"F2.wireOp",EDGE,"fcba4419-a2ee-464f-be9d-58f11bf3418b.sketch_text.stroke-89"),sQuery(id+"F2.wireOp",EDGE,"fcba4419-a2ee-464f-be9d-58f11bf3418b.sketch_text.stroke-90"),sQuery(id+"F2.wireOp",EDGE,"fcba4419-a2ee-464f-be9d-58f11bf3418b.sketch_text.stroke-91"),sQuery(id+"F2.wireOp",EDGE,"fcba4419-a2ee-464f-be9d-58f11bf3418b.sketch_text.stroke-92"),sQuery(id+"F2.wireOp",EDGE,"fcba4419-a2ee-464f-be9d-58f11bf3418b.sketch_text.stroke-93"),sQuery(id+"F2.wireOp",EDGE,"fcba4419-a2ee-464f-be9d-58f11bf3418b.sketch_text.stroke-94"),sQuery(id+"F2.wireOp",EDGE,"fcba4419-a2ee-464f-be9d-58f11bf3418b.sketch_text.stroke-95"),sQuery(id+"F2.wireOp",EDGE,"fcba4419-a2ee-464f-be9d-58f11bf3418b.sketch_text.stroke-96"),sQuery(id+"F2.wireOp",EDGE,"fcba4419-a2ee-464f-be9d-58f11bf3418b.sketch_text.stroke-97"),sQuery(id+"F2.wireOp",EDGE,"fcba4419-a2ee-464f-be9d-58f11bf3418b.sketch_text.stroke-98"),sQuery(id+"F2.wireOp",EDGE,"fcba4419-a2ee-464f-be9d-58f11bf3418b.sketch_text.stroke-99"),sQuery(id+"F2.wireOp",EDGE,"fcba4419-a2ee-464f-be9d-58f11bf3418b.sketch_text.stroke-100"),sQuery(id+"F2.wireOp",EDGE,"fcba4419-a2ee-464f-be9d-58f11bf3418b.sketch_text.stroke-101"),sQuery(id+"F2.wireOp",EDGE,"fcba4419-a2ee-464f-be9d-58f11bf3418b.sketch_text.stroke-102"),sQuery(id+"F2.wireOp",EDGE,"fcba4419-a2ee-464f-be9d-58f11bf3418b.sketch_text.stroke-103"),sQuery(id+"F2.wireOp",EDGE,"fcba4419-a2ee-464f-be9d-58f11bf3418b.sketch_text.stroke-104"),sQuery(id+"F2.wireOp",EDGE,"fcba4419-a2ee-464f-be9d-58f11bf3418b.sketch_text.stroke-105"),sQuery(id+"F2.wireOp",EDGE,"fcba4419-a2ee-464f-be9d-58f11bf3418b.sketch_text.stroke-106"),sQuery(id+"F2.wireOp",EDGE,"fcba4419-a2ee-464f-be9d-58f11bf3418b.sketch_text.stroke-107"),sQuery(id+"F2.wireOp",EDGE,"fcba4419-a2ee-464f-be9d-58f11bf3418b.sketch_text.stroke-108"),sQuery(id+"F2.wireOp",EDGE,"fcba4419-a2ee-464f-be9d-58f11bf3418b.sketch_text.stroke-109"),sQuery(id+"F2.wireOp",EDGE,"fcba4419-a2ee-464f-be9d-58f11bf3418b.sketch_text.stroke-110"),sQuery(id+"F2.wireOp",EDGE,"fcba4419-a2ee-464f-be9d-58f11bf3418b.sketch_text.stroke-111"),sQuery(id+"F2.wireOp",EDGE,"fcba4419-a2ee-464f-be9d-58f11bf3418b.sketch_text.stroke-112"),sQuery(id+"F2.wireOp",EDGE,"fcba4419-a2ee-464f-be9d-58f11bf3418b.sketch_text.stroke-113"),sQuery(id+"F2.wireOp",EDGE,"fcba4419-a2ee-464f-be9d-58f11bf3418b.sketch_text.stroke-114"),sQuery(id+"F2.wireOp",EDGE,"fcba4419-a2ee-464f-be9d-58f11bf3418b.sketch_text.stroke-115"),sQuery(id+"F2.wireOp",EDGE,"fcba4419-a2ee-464f-be9d-58f11bf3418b.sketch_text.stroke-116"),sQuery(id+"F2.wireOp",EDGE,"fcba4419-a2ee-464f-be9d-58f11bf3418b.sketch_text.stroke-117"),sQuery(id+"F2.wireOp",EDGE,"fcba4419-a2ee-464f-be9d-58f11bf3418b.sketch_text.stroke-118"),sQuery(id+"F2.wireOp",EDGE,"fcba4419-a2ee-464f-be9d-58f11bf3418b.sketch_text.stroke-119"),sQuery(id+"F2.wireOp",EDGE,"fcba4419-a2ee-464f-be9d-58f11bf3418b.sketch_text.stroke-120"),sQuery(id+"F2.wireOp",EDGE,"fcba4419-a2ee-464f-be9d-58f11bf3418b.sketch_text.stroke-121"),sQuery(id+"F2.wireOp",EDGE,"fcba4419-a2ee-464f-be9d-58f11bf3418b.sketch_text.stroke-122"),sQuery(id+"F2.wireOp",EDGE,"fcba4419-a2ee-464f-be9d-58f11bf3418b.sketch_text.stroke-123"),sQuery(id+"F2.wireOp",EDGE,"fcba4419-a2ee-464f-be9d-58f11bf3418b.sketch_text.stroke-124"),sQuery(id+"F2.wireOp",EDGE,"fcba4419-a2ee-464f-be9d-58f11bf3418b.sketch_text.stroke-125"),sQuery(id+"F2.wireOp",EDGE,"fcba4419-a2ee-464f-be9d-58f11bf3418b.sketch_text.stroke-126"),sQuery(id+"F2.wireOp",EDGE,"fcba4419-a2ee-464f-be9d-58f11bf3418b.sketch_text.stroke-127"),sQuery(id+"F2.wireOp",EDGE,"fcba4419-a2ee-464f-be9d-58f11bf3418b.sketch_text.stroke-128"),sQuery(id+"F2.wireOp",EDGE,"fcba4419-a2ee-464f-be9d-58f11bf3418b.sketch_text.stroke-129"),sQuery(id+"F2.wireOp",EDGE,"fcba4419-a2ee-464f-be9d-58f11bf3418b.sketch_text.stroke-130"),sQuery(id+"F2.wireOp",EDGE,"fcba4419-a2ee-464f-be9d-58f11bf3418b.sketch_text.stroke-131"),sQuery(id+"F2.wireOp",EDGE,"fcba4419-a2ee-464f-be9d-58f11bf3418b.sketch_text.stroke-132"),sQuery(id+"F2.wireOp",EDGE,"fcba4419-a2ee-464f-be9d-58f11bf3418b.sketch_text.stroke-133"),sQuery(id+"F2.wireOp",EDGE,"fcba4419-a2ee-464f-be9d-58f11bf3418b.sketch_text.stroke-134"),sQuery(id+"F2.wireOp",EDGE,"fcba4419-a2ee-464f-be9d-58f11bf3418b.sketch_text.stroke-135"),sQuery(id+"F2.wireOp",EDGE,"fcba4419-a2ee-464f-be9d-58f11bf3418b.sketch_text.stroke-136"),sQuery(id+"F2.wireOp",EDGE,"fcba4419-a2ee-464f-be9d-58f11bf3418b.sketch_text.stroke-137"),sQuery(id+"F2.wireOp",EDGE,"fcba4419-a2ee-464f-be9d-58f11bf3418b.sketch_text.stroke-138"),sQuery(id+"F2.wireOp",EDGE,"fcba4419-a2ee-464f-be9d-58f11bf3418b.sketch_text.stroke-139"),sQuery(id+"F2.wireOp",EDGE,"fcba4419-a2ee-464f-be9d-58f11bf3418b.sketch_text.stroke-140"),sQuery(id+"F2.wireOp",EDGE,"fcba4419-a2ee-464f-be9d-58f11bf3418b.sketch_text.stroke-141"),sQuery(id+"F2.wireOp",EDGE,"fcba4419-a2ee-464f-be9d-58f11bf3418b.sketch_text.stroke-142"),sQuery(id+"F2.wireOp",EDGE,"fcba4419-a2ee-464f-be9d-58f11bf3418b.sketch_text.stroke-143"),sQuery(id+"F2.wireOp",EDGE,"fcba4419-a2ee-464f-be9d-58f11bf3418b.sketch_text.stroke-144"),sQuery(id+"F2.wireOp",EDGE,"fcba4419-a2ee-464f-be9d-58f11bf3418b.sketch_text.stroke-145"),sQuery(id+"F2.wireOp",EDGE,"fcba4419-a2ee-464f-be9d-58f11bf3418b.sketch_text.stroke-146"),sQuery(id+"F2.wireOp",EDGE,"fcba4419-a2ee-464f-be9d-58f11bf3418b.sketch_text.stroke-147"),sQuery(id+"F2.wireOp",EDGE,"fcba4419-a2ee-464f-be9d-58f11bf3418b.sketch_text.stroke-148"),sQuery(id+"F2.wireOp",EDGE,"fcba4419-a2ee-464f-be9d-58f11bf3418b.sketch_text.stroke-149"),sQuery(id+"F2.wireOp",EDGE,"fcba4419-a2ee-464f-be9d-58f11bf3418b.sketch_text.stroke-150"),sQuery(id+"F2.wireOp",EDGE,"fcba4419-a2ee-464f-be9d-58f11bf3418b.sketch_text.stroke-151"),sQuery(id+"F2.wireOp",EDGE,"fcba4419-a2ee-464f-be9d-58f11bf3418b.sketch_text.stroke-152"),sQuery(id+"F2.wireOp",EDGE,"fcba4419-a2ee-464f-be9d-58f11bf3418b.sketch_text.stroke-153"),sQuery(id+"F2.wireOp",EDGE,"fcba4419-a2ee-464f-be9d-58f11bf3418b.sketch_text.stroke-154"),sQuery(id+"F2.wireOp",EDGE,"fcba4419-a2ee-464f-be9d-58f11bf3418b.sketch_text.stroke-155"),sQuery(id+"F2.wireOp",EDGE,"fcba4419-a2ee-464f-be9d-58f11bf3418b.sketch_text.stroke-156"),sQuery(id+"F2.wireOp",EDGE,"fcba4419-a2ee-464f-be9d-58f11bf3418b.sketch_text.stroke-157"),sQuery(id+"F2.wireOp",EDGE,"fcba4419-a2ee-464f-be9d-58f11bf3418b.sketch_text.stroke-158"),sQuery(id+"F2.wireOp",EDGE,"fcba4419-a2ee-464f-be9d-58f11bf3418b.sketch_text.stroke-159"),sQuery(id+"F2.wireOp",EDGE,"fcba4419-a2ee-464f-be9d-58f11bf3418b.sketch_text.stroke-160"),sQuery(id+"F2.wireOp",EDGE,"fcba4419-a2ee-464f-be9d-58f11bf3418b.sketch_text.stroke-161"),sQuery(id+"F2.wireOp",EDGE,"fcba4419-a2ee-464f-be9d-58f11bf3418b.sketch_text.stroke-162"),sQuery(id+"F2.wireOp",EDGE,"fcba4419-a2ee-464f-be9d-58f11bf3418b.sketch_text.stroke-163"),sQuery(id+"F2.wireOp",EDGE,"fcba4419-a2ee-464f-be9d-58f11bf3418b.sketch_text.stroke-164"),sQuery(id+"F2.wireOp",EDGE,"fcba4419-a2ee-464f-be9d-58f11bf3418b.sketch_text.stroke-165"),sQuery(id+"F2.wireOp",EDGE,"fcba4419-a2ee-464f-be9d-58f11bf3418b.sketch_text.stroke-166"),sQuery(id+"F2.wireOp",EDGE,"fcba4419-a2ee-464f-be9d-58f11bf3418b.sketch_text.stroke-167"),sQuery(id+"F2.wireOp",EDGE,"fcba4419-a2ee-464f-be9d-58f11bf3418b.sketch_text.stroke-168"),sQuery(id+"F2.wireOp",EDGE,"fcba4419-a2ee-464f-be9d-58f11bf3418b.sketch_text.stroke-169"),sQuery(id+"F2.wireOp",EDGE,"fcba4419-a2ee-464f-be9d-58f11bf3418b.sketch_text.stroke-170"),sQuery(id+"F2.wireOp",EDGE,"fcba4419-a2ee-464f-be9d-58f11bf3418b.sketch_text.stroke-171"),sQuery(id+"F2.wireOp",EDGE,"fcba4419-a2ee-464f-be9d-58f11bf3418b.sketch_text.stroke-172"),sQuery(id+"F2.wireOp",EDGE,"fcba4419-a2ee-464f-be9d-58f11bf3418b.sketch_text.stroke-173"),sQuery(id+"FHMxAyK4CFUKdhS_1.wireOp",EDGE,"1cb9c079-ea9b-4899-8069-e0e3048e911d.sketch_text.stroke-0"),sQuery(id+"FHMxAyK4CFUKdhS_1.wireOp",EDGE,"1cb9c079-ea9b-4899-8069-e0e3048e911d.sketch_text.stroke-1"),sQuery(id+"FHMxAyK4CFUKdhS_1.wireOp",EDGE,"1cb9c079-ea9b-4899-8069-e0e3048e911d.sketch_text.stroke-2"),sQuery(id+"FHMxAyK4CFUKdhS_1.wireOp",EDGE,"1cb9c079-ea9b-4899-8069-e0e3048e911d.sketch_text.stroke-3"),sQuery(id+"FHMxAyK4CFUKdhS_1.wireOp",EDGE,"1cb9c079-ea9b-4899-8069-e0e3048e911d.sketch_text.stroke-4"),sQuery(id+"FHMxAyK4CFUKdhS_1.wireOp",EDGE,"1cb9c079-ea9b-4899-8069-e0e3048e911d.sketch_text.stroke-5"),sQuery(id+"FHMxAyK4CFUKdhS_1.wireOp",EDGE,"1cb9c079-ea9b-4899-8069-e0e3048e911d.sketch_text.stroke-6"),sQuery(id+"FHMxAyK4CFUKdhS_1.wireOp",EDGE,"1cb9c079-ea9b-4899-8069-e0e3048e911d.sketch_text.stroke-7"),sQuery(id+"FHMxAyK4CFUKdhS_1.wireOp",EDGE,"1cb9c079-ea9b-4899-8069-e0e3048e911d.sketch_text.stroke-8"),sQuery(id+"FHMxAyK4CFUKdhS_1.wireOp",EDGE,"1cb9c079-ea9b-4899-8069-e0e3048e911d.sketch_text.stroke-9"),sQuery(id+"FHMxAyK4CFUKdhS_1.wireOp",EDGE,"1cb9c079-ea9b-4899-8069-e0e3048e911d.sketch_text.stroke-10"),sQuery(id+"FHMxAyK4CFUKdhS_1.wireOp",EDGE,"1cb9c079-ea9b-4899-8069-e0e3048e911d.sketch_text.stroke-11"),sQuery(id+"FHMxAyK4CFUKdhS_1.wireOp",EDGE,"1cb9c079-ea9b-4899-8069-e0e3048e911d.sketch_text.stroke-12"),sQuery(id+"FHMxAyK4CFUKdhS_1.wireOp",EDGE,"1cb9c079-ea9b-4899-8069-e0e3048e911d.sketch_text.stroke-13"),sQuery(id+"FHMxAyK4CFUKdhS_1.wireOp",EDGE,"1cb9c079-ea9b-4899-8069-e0e3048e911d.sketch_text.stroke-14"),sQuery(id+"FHMxAyK4CFUKdhS_1.wireOp",EDGE,"1cb9c079-ea9b-4899-8069-e0e3048e911d.sketch_text.stroke-15"),sQuery(id+"FHMxAyK4CFUKdhS_1.wireOp",EDGE,"1cb9c079-ea9b-4899-8069-e0e3048e911d.sketch_text.stroke-16"),sQuery(id+"FHMxAyK4CFUKdhS_1.wireOp",EDGE,"1cb9c079-ea9b-4899-8069-e0e3048e911d.sketch_text.stroke-17"),sQuery(id+"FHMxAyK4CFUKdhS_1.wireOp",EDGE,"1cb9c079-ea9b-4899-8069-e0e3048e911d.sketch_text.stroke-18"),sQuery(id+"FHMxAyK4CFUKdhS_1.wireOp",EDGE,"1cb9c079-ea9b-4899-8069-e0e3048e911d.sketch_text.stroke-19"),sQuery(id+"FHMxAyK4CFUKdhS_1.wireOp",EDGE,"1cb9c079-ea9b-4899-8069-e0e3048e911d.sketch_text.stroke-20"),sQuery(id+"FHMxAyK4CFUKdhS_1.wireOp",EDGE,"1cb9c079-ea9b-4899-8069-e0e3048e911d.sketch_text.stroke-21"),sQuery(id+"FHMxAyK4CFUKdhS_1.wireOp",EDGE,"1cb9c079-ea9b-4899-8069-e0e3048e911d.sketch_text.stroke-22"),sQuery(id+"FHMxAyK4CFUKdhS_1.wireOp",EDGE,"1cb9c079-ea9b-4899-8069-e0e3048e911d.sketch_text.stroke-23"),sQuery(id+"FHMxAyK4CFUKdhS_1.wireOp",EDGE,"1cb9c079-ea9b-4899-8069-e0e3048e911d.sketch_text.stroke-24"),sQuery(id+"FHMxAyK4CFUKdhS_1.wireOp",EDGE,"1cb9c079-ea9b-4899-8069-e0e3048e911d.sketch_text.stroke-25"),sQuery(id+"FHMxAyK4CFUKdhS_1.wireOp",EDGE,"1cb9c079-ea9b-4899-8069-e0e3048e911d.sketch_text.stroke-26"),sQuery(id+"FHMxAyK4CFUKdhS_1.wireOp",EDGE,"1cb9c079-ea9b-4899-8069-e0e3048e911d.sketch_text.stroke-27"),sQuery(id+"FHMxAyK4CFUKdhS_1.wireOp",EDGE,"1cb9c079-ea9b-4899-8069-e0e3048e911d.sketch_text.stroke-28"),sQuery(id+"FHMxAyK4CFUKdhS_1.wireOp",EDGE,"1cb9c079-ea9b-4899-8069-e0e3048e911d.sketch_text.stroke-29"),sQuery(id+"FHMxAyK4CFUKdhS_1.wireOp",EDGE,"1cb9c079-ea9b-4899-8069-e0e3048e911d.sketch_text.stroke-30"),sQuery(id+"FHMxAyK4CFUKdhS_1.wireOp",EDGE,"1cb9c079-ea9b-4899-8069-e0e3048e911d.sketch_text.stroke-31"),sQuery(id+"FHMxAyK4CFUKdhS_1.wireOp",EDGE,"1cb9c079-ea9b-4899-8069-e0e3048e911d.sketch_text.stroke-32"),sQuery(id+"FHMxAyK4CFUKdhS_1.wireOp",EDGE,"1cb9c079-ea9b-4899-8069-e0e3048e911d.sketch_text.stroke-33"),sQuery(id+"FHMxAyK4CFUKdhS_1.wireOp",EDGE,"1cb9c079-ea9b-4899-8069-e0e3048e911d.sketch_text.stroke-34"),sQuery(id+"FHMxAyK4CFUKdhS_1.wireOp",EDGE,"1cb9c079-ea9b-4899-8069-e0e3048e911d.sketch_text.stroke-35"),sQuery(id+"FHMxAyK4CFUKdhS_1.wireOp",EDGE,"1cb9c079-ea9b-4899-8069-e0e3048e911d.sketch_text.stroke-36"),sQuery(id+"FHMxAyK4CFUKdhS_1.wireOp",EDGE,"1cb9c079-ea9b-4899-8069-e0e3048e911d.sketch_text.stroke-37"),sQuery(id+"FHMxAyK4CFUKdhS_1.wireOp",EDGE,"1cb9c079-ea9b-4899-8069-e0e3048e911d.sketch_text.stroke-38"),sQuery(id+"FHMxAyK4CFUKdhS_1.wireOp",EDGE,"1cb9c079-ea9b-4899-8069-e0e3048e911d.sketch_text.stroke-39"),sQuery(id+"FHMxAyK4CFUKdhS_1.wireOp",EDGE,"1cb9c079-ea9b-4899-8069-e0e3048e911d.sketch_text.stroke-40"),sQuery(id+"FHMxAyK4CFUKdhS_1.wireOp",EDGE,"1cb9c079-ea9b-4899-8069-e0e3048e911d.sketch_text.stroke-41"),sQuery(id+"FHMxAyK4CFUKdhS_1.wireOp",EDGE,"1cb9c079-ea9b-4899-8069-e0e3048e911d.sketch_text.stroke-42"),sQuery(id+"FHMxAyK4CFUKdhS_1.wireOp",EDGE,"1cb9c079-ea9b-4899-8069-e0e3048e911d.sketch_text.stroke-43"),sQuery(id+"FHMxAyK4CFUKdhS_1.wireOp",EDGE,"1cb9c079-ea9b-4899-8069-e0e3048e911d.sketch_text.stroke-44"),sQuery(id+"FHMxAyK4CFUKdhS_1.wireOp",EDGE,"1cb9c079-ea9b-4899-8069-e0e3048e911d.sketch_text.stroke-45"),sQuery(id+"FHMxAyK4CFUKdhS_1.wireOp",EDGE,"1cb9c079-ea9b-4899-8069-e0e3048e911d.sketch_text.stroke-46"),sQuery(id+"FHMxAyK4CFUKdhS_1.wireOp",EDGE,"1cb9c079-ea9b-4899-8069-e0e3048e911d.sketch_text.stroke-47"),sQuery(id+"FHMxAyK4CFUKdhS_1.wireOp",EDGE,"1cb9c079-ea9b-4899-8069-e0e3048e911d.sketch_text.stroke-48"),sQuery(id+"FHMxAyK4CFUKdhS_1.wireOp",EDGE,"1cb9c079-ea9b-4899-8069-e0e3048e911d.sketch_text.stroke-49"),sQuery(id+"FHMxAyK4CFUKdhS_1.wireOp",EDGE,"1cb9c079-ea9b-4899-8069-e0e3048e911d.sketch_text.stroke-50"),sQuery(id+"FHMxAyK4CFUKdhS_1.wireOp",EDGE,"1cb9c079-ea9b-4899-8069-e0e3048e911d.sketch_text.stroke-51"),sQuery(id+"FHMxAyK4CFUKdhS_1.wireOp",EDGE,"1cb9c079-ea9b-4899-8069-e0e3048e911d.sketch_text.stroke-52"),sQuery(id+"FHMxAyK4CFUKdhS_1.wireOp",EDGE,"1cb9c079-ea9b-4899-8069-e0e3048e911d.sketch_text.stroke-53"),sQuery(id+"FHMxAyK4CFUKdhS_1.wireOp",EDGE,"1cb9c079-ea9b-4899-8069-e0e3048e911d.sketch_text.stroke-54"),sQuery(id+"FHMxAyK4CFUKdhS_1.wireOp",EDGE,"1cb9c079-ea9b-4899-8069-e0e3048e911d.sketch_text.stroke-55"),sQuery(id+"FHMxAyK4CFUKdhS_1.wireOp",EDGE,"1cb9c079-ea9b-4899-8069-e0e3048e911d.sketch_text.stroke-56"),sQuery(id+"FHMxAyK4CFUKdhS_1.wireOp",EDGE,"1cb9c079-ea9b-4899-8069-e0e3048e911d.sketch_text.stroke-57"),sQuery(id+"FHMxAyK4CFUKdhS_1.wireOp",EDGE,"1cb9c079-ea9b-4899-8069-e0e3048e911d.sketch_text.stroke-58"),sQuery(id+"FHMxAyK4CFUKdhS_1.wireOp",EDGE,"1cb9c079-ea9b-4899-8069-e0e3048e911d.sketch_text.stroke-59"),sQuery(id+"FHMxAyK4CFUKdhS_1.wireOp",EDGE,"1cb9c079-ea9b-4899-8069-e0e3048e911d.sketch_text.stroke-60"),sQuery(id+"FHMxAyK4CFUKdhS_1.wireOp",EDGE,"1cb9c079-ea9b-4899-8069-e0e3048e911d.sketch_text.stroke-61"),sQuery(id+"FHMxAyK4CFUKdhS_1.wireOp",EDGE,"1cb9c079-ea9b-4899-8069-e0e3048e911d.sketch_text.stroke-62"),sQuery(id+"FHMxAyK4CFUKdhS_1.wireOp",EDGE,"1cb9c079-ea9b-4899-8069-e0e3048e911d.sketch_text.stroke-71"),sQuery(id+"FHMxAyK4CFUKdhS_1.wireOp",EDGE,"1cb9c079-ea9b-4899-8069-e0e3048e911d.sketch_text.stroke-72"),sQuery(id+"FHMxAyK4CFUKdhS_1.wireOp",EDGE,"1cb9c079-ea9b-4899-8069-e0e3048e911d.sketch_text.stroke-73"),sQuery(id+"FHMxAyK4CFUKdhS_1.wireOp",EDGE,"1cb9c079-ea9b-4899-8069-e0e3048e911d.sketch_text.stroke-74"),sQuery(id+"FHMxAyK4CFUKdhS_1.wireOp",EDGE,"1cb9c079-ea9b-4899-8069-e0e3048e911d.sketch_text.stroke-75"),sQuery(id+"FHMxAyK4CFUKdhS_1.wireOp",EDGE,"1cb9c079-ea9b-4899-8069-e0e3048e911d.sketch_text.stroke-76"),sQuery(id+"FHMxAyK4CFUKdhS_1.wireOp",EDGE,"1cb9c079-ea9b-4899-8069-e0e3048e911d.sketch_text.stroke-77"),sQuery(id+"FHMxAyK4CFUKdhS_1.wireOp",EDGE,"1cb9c079-ea9b-4899-8069-e0e3048e911d.sketch_text.stroke-78"),sQuery(id+"FHMxAyK4CFUKdhS_1.wireOp",EDGE,"1cb9c079-ea9b-4899-8069-e0e3048e911d.sketch_text.stroke-79"),sQuery(id+"FHMxAyK4CFUKdhS_1.wireOp",EDGE,"1cb9c079-ea9b-4899-8069-e0e3048e911d.sketch_text.stroke-80"),sQuery(id+"FHMxAyK4CFUKdhS_1.wireOp",EDGE,"1cb9c079-ea9b-4899-8069-e0e3048e911d.sketch_text.stroke-81"),sQuery(id+"FHMxAyK4CFUKdhS_1.wireOp",EDGE,"1cb9c079-ea9b-4899-8069-e0e3048e911d.sketch_text.stroke-82"),sQuery(id+"FHMxAyK4CFUKdhS_1.wireOp",EDGE,"1cb9c079-ea9b-4899-8069-e0e3048e911d.sketch_text.stroke-83"),sQuery(id+"FHMxAyK4CFUKdhS_1.wireOp",EDGE,"1cb9c079-ea9b-4899-8069-e0e3048e911d.sketch_text.stroke-84"),sQuery(id+"FHMxAyK4CFUKdhS_1.wireOp",EDGE,"1cb9c079-ea9b-4899-8069-e0e3048e911d.sketch_text.stroke-85"),sQuery(id+"FHMxAyK4CFUKdhS_1.wireOp",EDGE,"1cb9c079-ea9b-4899-8069-e0e3048e911d.sketch_text.stroke-86"),sQuery(id+"FHMxAyK4CFUKdhS_1.wireOp",EDGE,"1cb9c079-ea9b-4899-8069-e0e3048e911d.sketch_text.stroke-87"),sQuery(id+"FHMxAyK4CFUKdhS_1.wireOp",EDGE,"1cb9c079-ea9b-4899-8069-e0e3048e911d.sketch_text.stroke-88"),sQuery(id+"FHMxAyK4CFUKdhS_1.wireOp",EDGE,"1cb9c079-ea9b-4899-8069-e0e3048e911d.sketch_text.stroke-89"),sQuery(id+"FHMxAyK4CFUKdhS_1.wireOp",EDGE,"1cb9c079-ea9b-4899-8069-e0e3048e911d.sketch_text.stroke-90"),sQuery(id+"FHMxAyK4CFUKdhS_1.wireOp",EDGE,"1cb9c079-ea9b-4899-8069-e0e3048e911d.sketch_text.stroke-91"),sQuery(id+"FHMxAyK4CFUKdhS_1.wireOp",EDGE,"1cb9c079-ea9b-4899-8069-e0e3048e911d.sketch_text.stroke-92"),sQuery(id+"FHMxAyK4CFUKdhS_1.wireOp",EDGE,"1cb9c079-ea9b-4899-8069-e0e3048e911d.sketch_text.stroke-93"),sQuery(id+"FHMxAyK4CFUKdhS_1.wireOp",EDGE,"1cb9c079-ea9b-4899-8069-e0e3048e911d.sketch_text.stroke-94"),sQuery(id+"FHMxAyK4CFUKdhS_1.wireOp",EDGE,"1cb9c079-ea9b-4899-8069-e0e3048e911d.sketch_text.stroke-95"),sQuery(id+"FHMxAyK4CFUKdhS_1.wireOp",EDGE,"1cb9c079-ea9b-4899-8069-e0e3048e911d.sketch_text.stroke-96"),sQuery(id+"FHMxAyK4CFUKdhS_1.wireOp",EDGE,"1cb9c079-ea9b-4899-8069-e0e3048e911d.sketch_text.stroke-97"),sQuery(id+"FHMxAyK4CFUKdhS_1.wireOp",EDGE,"1cb9c079-ea9b-4899-8069-e0e3048e911d.sketch_text.stroke-103"),sQuery(id+"FHMxAyK4CFUKdhS_1.wireOp",EDGE,"1cb9c079-ea9b-4899-8069-e0e3048e911d.sketch_text.stroke-104"),sQuery(id+"FHMxAyK4CFUKdhS_1.wireOp",EDGE,"1cb9c079-ea9b-4899-8069-e0e3048e911d.sketch_text.stroke-105"),sQuery(id+"FHMxAyK4CFUKdhS_1.wireOp",EDGE,"1cb9c079-ea9b-4899-8069-e0e3048e911d.sketch_text.stroke-106"),sQuery(id+"FHMxAyK4CFUKdhS_1.wireOp",EDGE,"1cb9c079-ea9b-4899-8069-e0e3048e911d.sketch_text.stroke-107"),sQuery(id+"FHMxAyK4CFUKdhS_1.wireOp",EDGE,"1cb9c079-ea9b-4899-8069-e0e3048e911d.sketch_text.stroke-108"),sQuery(id+"FHMxAyK4CFUKdhS_1.wireOp",EDGE,"1cb9c079-ea9b-4899-8069-e0e3048e911d.sketch_text.stroke-109"),sQuery(id+"FHMxAyK4CFUKdhS_1.wireOp",EDGE,"1cb9c079-ea9b-4899-8069-e0e3048e911d.sketch_text.stroke-110"),sQuery(id+"FHMxAyK4CFUKdhS_1.wireOp",EDGE,"1cb9c079-ea9b-4899-8069-e0e3048e911d.sketch_text.stroke-111"),sQuery(id+"FHMxAyK4CFUKdhS_1.wireOp",EDGE,"1cb9c079-ea9b-4899-8069-e0e3048e911d.sketch_text.stroke-112"),sQuery(id+"FHMxAyK4CFUKdhS_1.wireOp",EDGE,"1cb9c079-ea9b-4899-8069-e0e3048e911d.sketch_text.stroke-113"),sQuery(id+"FHMxAyK4CFUKdhS_1.wireOp",EDGE,"1cb9c079-ea9b-4899-8069-e0e3048e911d.sketch_text.stroke-114"),sQuery(id+"FHMxAyK4CFUKdhS_1.wireOp",EDGE,"1cb9c079-ea9b-4899-8069-e0e3048e911d.sketch_text.stroke-115"),sQuery(id+"FHMxAyK4CFUKdhS_1.wireOp",EDGE,"1cb9c079-ea9b-4899-8069-e0e3048e911d.sketch_text.stroke-116"),sQuery(id+"FHMxAyK4CFUKdhS_1.wireOp",EDGE,"1cb9c079-ea9b-4899-8069-e0e3048e911d.sketch_text.stroke-117"),sQuery(id+"FHMxAyK4CFUKdhS_1.wireOp",EDGE,"1cb9c079-ea9b-4899-8069-e0e3048e911d.sketch_text.stroke-118"),sQuery(id+"FHMxAyK4CFUKdhS_1.wireOp",EDGE,"1cb9c079-ea9b-4899-8069-e0e3048e911d.sketch_text.stroke-119"),sQuery(id+"FHMxAyK4CFUKdhS_1.wireOp",EDGE,"1cb9c079-ea9b-4899-8069-e0e3048e911d.sketch_text.stroke-120"),sQuery(id+"FHMxAyK4CFUKdhS_1.wireOp",EDGE,"1cb9c079-ea9b-4899-8069-e0e3048e911d.sketch_text.stroke-121"),sQuery(id+"FHMxAyK4CFUKdhS_1.wireOp",EDGE,"1cb9c079-ea9b-4899-8069-e0e3048e911d.sketch_text.stroke-122"),sQuery(id+"FHMxAyK4CFUKdhS_1.wireOp",EDGE,"1cb9c079-ea9b-4899-8069-e0e3048e911d.sketch_text.stroke-123"),sQuery(id+"FHMxAyK4CFUKdhS_1.wireOp",EDGE,"1cb9c079-ea9b-4899-8069-e0e3048e911d.sketch_text.stroke-124"),sQuery(id+"FHMxAyK4CFUKdhS_1.wireOp",EDGE,"1cb9c079-ea9b-4899-8069-e0e3048e911d.sketch_text.stroke-125"),sQuery(id+"FHMxAyK4CFUKdhS_1.wireOp",EDGE,"1cb9c079-ea9b-4899-8069-e0e3048e911d.sketch_text.stroke-126"),sQuery(id+"FHMxAyK4CFUKdhS_1.wireOp",EDGE,"1cb9c079-ea9b-4899-8069-e0e3048e911d.sketch_text.stroke-127"),sQuery(id+"FHMxAyK4CFUKdhS_1.wireOp",EDGE,"1cb9c079-ea9b-4899-8069-e0e3048e911d.sketch_text.stroke-128"),sQuery(id+"FHMxAyK4CFUKdhS_1.wireOp",EDGE,"1cb9c079-ea9b-4899-8069-e0e3048e911d.sketch_text.stroke-129"),sQuery(id+"FHMxAyK4CFUKdhS_1.wireOp",EDGE,"1cb9c079-ea9b-4899-8069-e0e3048e911d.sketch_text.stroke-130"),sQuery(id+"FHMxAyK4CFUKdhS_1.wireOp",EDGE,"1cb9c079-ea9b-4899-8069-e0e3048e911d.sketch_text.stroke-131"),sQuery(id+"FHMxAyK4CFUKdhS_1.wireOp",EDGE,"1cb9c079-ea9b-4899-8069-e0e3048e911d.sketch_text.stroke-132"),sQuery(id+"FHMxAyK4CFUKdhS_1.wireOp",EDGE,"1cb9c079-ea9b-4899-8069-e0e3048e911d.sketch_text.stroke-133"),sQuery(id+"FHMxAyK4CFUKdhS_1.wireOp",EDGE,"1cb9c079-ea9b-4899-8069-e0e3048e911d.sketch_text.stroke-134"),sQuery(id+"FHMxAyK4CFUKdhS_1.wireOp",EDGE,"1cb9c079-ea9b-4899-8069-e0e3048e911d.sketch_text.stroke-135"),sQuery(id+"FHMxAyK4CFUKdhS_1.wireOp",EDGE,"1cb9c079-ea9b-4899-8069-e0e3048e911d.sketch_text.stroke-136"),sQuery(id+"FHMxAyK4CFUKdhS_1.wireOp",EDGE,"1cb9c079-ea9b-4899-8069-e0e3048e911d.sketch_text.stroke-137"),sQuery(id+"FHMxAyK4CFUKdhS_1.wireOp",EDGE,"1cb9c079-ea9b-4899-8069-e0e3048e911d.sketch_text.stroke-138"),sQuery(id+"FHMxAyK4CFUKdhS_1.wireOp",EDGE,"1cb9c079-ea9b-4899-8069-e0e3048e911d.sketch_text.stroke-139"),sQuery(id+"FHMxAyK4CFUKdhS_1.wireOp",EDGE,"1cb9c079-ea9b-4899-8069-e0e3048e911d.sketch_text.stroke-140"),sQuery(id+"FHMxAyK4CFUKdhS_1.wireOp",EDGE,"1cb9c079-ea9b-4899-8069-e0e3048e911d.sketch_text.stroke-141"),sQuery(id+"FHMxAyK4CFUKdhS_1.wireOp",EDGE,"1cb9c079-ea9b-4899-8069-e0e3048e911d.sketch_text.stroke-142"),sQuery(id+"FHMxAyK4CFUKdhS_1.wireOp",EDGE,"1cb9c079-ea9b-4899-8069-e0e3048e911d.sketch_text.stroke-143"),sQuery(id+"FHMxAyK4CFUKdhS_1.wireOp",EDGE,"1cb9c079-ea9b-4899-8069-e0e3048e911d.sketch_text.stroke-144"),sQuery(id+"FHMxAyK4CFUKdhS_1.wireOp",EDGE,"1cb9c079-ea9b-4899-8069-e0e3048e911d.sketch_text.stroke-145"),sQuery(id+"FHMxAyK4CFUKdhS_1.wireOp",EDGE,"1cb9c079-ea9b-4899-8069-e0e3048e911d.sketch_text.stroke-146"),sQuery(id+"FHMxAyK4CFUKdhS_1.wireOp",EDGE,"1cb9c079-ea9b-4899-8069-e0e3048e911d.sketch_text.stroke-147"),sQuery(id+"FHMxAyK4CFUKdhS_1.wireOp",EDGE,"1cb9c079-ea9b-4899-8069-e0e3048e911d.sketch_text.stroke-148"),sQuery(id+"FHMxAyK4CFUKdhS_1.wireOp",EDGE,"1cb9c079-ea9b-4899-8069-e0e3048e911d.sketch_text.stroke-149"),sQuery(id+"FHMxAyK4CFUKdhS_1.wireOp",EDGE,"1cb9c079-ea9b-4899-8069-e0e3048e911d.sketch_text.stroke-150"),sQuery(id+"FHMxAyK4CFUKdhS_1.wireOp",EDGE,"1cb9c079-ea9b-4899-8069-e0e3048e911d.sketch_text.stroke-151"),sQuery(id+"FHMxAyK4CFUKdhS_1.wireOp",EDGE,"1cb9c079-ea9b-4899-8069-e0e3048e911d.sketch_text.stroke-152"),sQuery(id+"FHMxAyK4CFUKdhS_1.wireOp",EDGE,"1cb9c079-ea9b-4899-8069-e0e3048e911d.sketch_text.stroke-153"),sQuery(id+"FHMxAyK4CFUKdhS_1.wireOp",EDGE,"1cb9c079-ea9b-4899-8069-e0e3048e911d.sketch_text.stroke-159"),sQuery(id+"FHMxAyK4CFUKdhS_1.wireOp",EDGE,"1cb9c079-ea9b-4899-8069-e0e3048e911d.sketch_text.stroke-160"),sQuery(id+"FHMxAyK4CFUKdhS_1.wireOp",EDGE,"1cb9c079-ea9b-4899-8069-e0e3048e911d.sketch_text.stroke-161"),sQuery(id+"FHMxAyK4CFUKdhS_1.wireOp",EDGE,"1cb9c079-ea9b-4899-8069-e0e3048e911d.sketch_text.stroke-162"),sQuery(id+"FHMxAyK4CFUKdhS_1.wireOp",EDGE,"1cb9c079-ea9b-4899-8069-e0e3048e911d.sketch_text.stroke-163"),sQuery(id+"FHMxAyK4CFUKdhS_1.wireOp",EDGE,"1cb9c079-ea9b-4899-8069-e0e3048e911d.sketch_text.stroke-164"),sQuery(id+"FHMxAyK4CFUKdhS_1.wireOp",EDGE,"1cb9c079-ea9b-4899-8069-e0e3048e911d.sketch_text.stroke-165"),sQuery(id+"FHMxAyK4CFUKdhS_1.wireOp",EDGE,"1cb9c079-ea9b-4899-8069-e0e3048e911d.sketch_text.stroke-166"),sQuery(id+"FHMxAyK4CFUKdhS_1.wireOp",EDGE,"1cb9c079-ea9b-4899-8069-e0e3048e911d.sketch_text.stroke-167"),sQuery(id+"FHMxAyK4CFUKdhS_1.wireOp",EDGE,"1cb9c079-ea9b-4899-8069-e0e3048e911d.sketch_text.stroke-168"),sQuery(id+"FHMxAyK4CFUKdhS_1.wireOp",EDGE,"1cb9c079-ea9b-4899-8069-e0e3048e911d.sketch_text.stroke-169"),sQuery(id+"FHMxAyK4CFUKdhS_1.wireOp",EDGE,"1cb9c079-ea9b-4899-8069-e0e3048e911d.sketch_text.stroke-170"),sQuery(id+"FHMxAyK4CFUKdhS_1.wireOp",EDGE,"1cb9c079-ea9b-4899-8069-e0e3048e911d.sketch_text.stroke-171"),sQuery(id+"FHMxAyK4CFUKdhS_1.wireOp",EDGE,"1cb9c079-ea9b-4899-8069-e0e3048e911d.sketch_text.stroke-172"),sQuery(id+"FHMxAyK4CFUKdhS_1.wireOp",EDGE,"1cb9c079-ea9b-4899-8069-e0e3048e911d.sketch_text.stroke-173"),sQuery(id+"FHMxAyK4CFUKdhS_1.wireOp",EDGE,"1cb9c079-ea9b-4899-8069-e0e3048e911d.sketch_text.stroke-174"),sQuery(id+"FHMxAyK4CFUKdhS_1.wireOp",EDGE,"1cb9c079-ea9b-4899-8069-e0e3048e911d.sketch_text.stroke-175"),sQuery(id+"FHMxAyK4CFUKdhS_1.wireOp",EDGE,"1cb9c079-ea9b-4899-8069-e0e3048e911d.sketch_text.stroke-176"),sQuery(id+"FHMxAyK4CFUKdhS_1.wireOp",EDGE,"1cb9c079-ea9b-4899-8069-e0e3048e911d.sketch_text.stroke-177"),sQuery(id+"FHMxAyK4CFUKdhS_1.wireOp",EDGE,"1cb9c079-ea9b-4899-8069-e0e3048e911d.sketch_text.stroke-178"),sQuery(id+"FHMxAyK4CFUKdhS_1.wireOp",EDGE,"1cb9c079-ea9b-4899-8069-e0e3048e911d.sketch_text.stroke-179"),sQuery(id+"FHMxAyK4CFUKdhS_1.wireOp",EDGE,"1cb9c079-ea9b-4899-8069-e0e3048e911d.sketch_text.stroke-180"),subQ0,subQ2])],"isStart":true}),makeQuery(id+"F4.opExtrude","SWEPT_FACE",FACE,{"disambiguationData":[OSD([subQ2])]})])],"derivedFrom":makeQuery(id+"F4.opExtrude","CAP_EDGE",EDGE,{"disambiguationData":[OSD([subQ0])],"isStart":true})});}
            var Q4;
            {var subQ0=sQuery(id+"F0.wireOp",EDGE,"E0.top");var subQ1=sQuery(id+"F0.wireOp",EDGE,"E0.bottom");var subQ2=sQuery(id+"F3.wireOp",EDGE,"8007402e-1a4e-4a06-85a5-2af08e553504");Q4=makeQuery(id+"F4.boolean.opBoolean","SPLIT",EDGE,{"disambiguationData":[TD([makeQuery(id+"F1.opExtrude","CAP_FACE",FACE,{"disambiguationData":[OSD([subQ1,subQ0,sQuery(id+"F0.wireOp",EDGE,"E0.left"),sQuery(id+"F0.wireOp",EDGE,"E0.right")])],"isStart":false}),makeQuery(id+"F1.opExtrude","SWEPT_FACE",FACE,{"disambiguationData":[OSD([subQ0])]}),makeQuery(id+"F4.opExtrude","SWEPT_FACE",FACE,{"disambiguationData":[OSD([subQ2])]}),makeQuery(id+"F4.opExtrude","CAP_FACE",FACE,{"disambiguationData":[OSD([subQ1,sQuery(id+"F2.wireOp",EDGE,"fcba4419-a2ee-464f-be9d-58f11bf3418b.sketch_text.stroke-0"),sQuery(id+"F2.wireOp",EDGE,"fcba4419-a2ee-464f-be9d-58f11bf3418b.sketch_text.stroke-1"),sQuery(id+"F2.wireOp",EDGE,"fcba4419-a2ee-464f-be9d-58f11bf3418b.sketch_text.stroke-2"),sQuery(id+"F2.wireOp",EDGE,"fcba4419-a2ee-464f-be9d-58f11bf3418b.sketch_text.stroke-3"),sQuery(id+"F2.wireOp",EDGE,"fcba4419-a2ee-464f-be9d-58f11bf3418b.sketch_text.stroke-4"),sQuery(id+"F2.wireOp",EDGE,"fcba4419-a2ee-464f-be9d-58f11bf3418b.sketch_text.stroke-5"),sQuery(id+"F2.wireOp",EDGE,"fcba4419-a2ee-464f-be9d-58f11bf3418b.sketch_text.stroke-6"),sQuery(id+"F2.wireOp",EDGE,"fcba4419-a2ee-464f-be9d-58f11bf3418b.sketch_text.stroke-7"),sQuery(id+"F2.wireOp",EDGE,"fcba4419-a2ee-464f-be9d-58f11bf3418b.sketch_text.stroke-8"),sQuery(id+"F2.wireOp",EDGE,"fcba4419-a2ee-464f-be9d-58f11bf3418b.sketch_text.stroke-9"),sQuery(id+"F2.wireOp",EDGE,"fcba4419-a2ee-464f-be9d-58f11bf3418b.sketch_text.stroke-10"),sQuery(id+"F2.wireOp",EDGE,"fcba4419-a2ee-464f-be9d-58f11bf3418b.sketch_text.stroke-11"),sQuery(id+"F2.wireOp",EDGE,"fcba4419-a2ee-464f-be9d-58f11bf3418b.sketch_text.stroke-12"),sQuery(id+"F2.wireOp",EDGE,"fcba4419-a2ee-464f-be9d-58f11bf3418b.sketch_text.stroke-13"),sQuery(id+"F2.wireOp",EDGE,"fcba4419-a2ee-464f-be9d-58f11bf3418b.sketch_text.stroke-14"),sQuery(id+"F2.wireOp",EDGE,"fcba4419-a2ee-464f-be9d-58f11bf3418b.sketch_text.stroke-15"),sQuery(id+"F2.wireOp",EDGE,"fcba4419-a2ee-464f-be9d-58f11bf3418b.sketch_text.stroke-16"),sQuery(id+"F2.wireOp",EDGE,"fcba4419-a2ee-464f-be9d-58f11bf3418b.sketch_text.stroke-17"),sQuery(id+"F2.wireOp",EDGE,"fcba4419-a2ee-464f-be9d-58f11bf3418b.sketch_text.stroke-18"),sQuery(id+"F2.wireOp",EDGE,"fcba4419-a2ee-464f-be9d-58f11bf3418b.sketch_text.stroke-19"),sQuery(id+"F2.wireOp",EDGE,"fcba4419-a2ee-464f-be9d-58f11bf3418b.sketch_text.stroke-20"),sQuery(id+"F2.wireOp",EDGE,"fcba4419-a2ee-464f-be9d-58f11bf3418b.sketch_text.stroke-21"),sQuery(id+"F2.wireOp",EDGE,"fcba4419-a2ee-464f-be9d-58f11bf3418b.sketch_text.stroke-22"),sQuery(id+"F2.wireOp",EDGE,"fcba4419-a2ee-464f-be9d-58f11bf3418b.sketch_text.stroke-23"),sQuery(id+"F2.wireOp",EDGE,"fcba4419-a2ee-464f-be9d-58f11bf3418b.sketch_text.stroke-24"),sQuery(id+"F2.wireOp",EDGE,"fcba4419-a2ee-464f-be9d-58f11bf3418b.sketch_text.stroke-25"),sQuery(id+"F2.wireOp",EDGE,"fcba4419-a2ee-464f-be9d-58f11bf3418b.sketch_text.stroke-26"),sQuery(id+"F2.wireOp",EDGE,"fcba4419-a2ee-464f-be9d-58f11bf3418b.sketch_text.stroke-27"),sQuery(id+"F2.wireOp",EDGE,"fcba4419-a2ee-464f-be9d-58f11bf3418b.sketch_text.stroke-28"),sQuery(id+"F2.wireOp",EDGE,"fcba4419-a2ee-464f-be9d-58f11bf3418b.sketch_text.stroke-29"),sQuery(id+"F2.wireOp",EDGE,"fcba4419-a2ee-464f-be9d-58f11bf3418b.sketch_text.stroke-30"),sQuery(id+"F2.wireOp",EDGE,"fcba4419-a2ee-464f-be9d-58f11bf3418b.sketch_text.stroke-31"),sQuery(id+"F2.wireOp",EDGE,"fcba4419-a2ee-464f-be9d-58f11bf3418b.sketch_text.stroke-32"),sQuery(id+"F2.wireOp",EDGE,"fcba4419-a2ee-464f-be9d-58f11bf3418b.sketch_text.stroke-33"),sQuery(id+"F2.wireOp",EDGE,"fcba4419-a2ee-464f-be9d-58f11bf3418b.sketch_text.stroke-34"),sQuery(id+"F2.wireOp",EDGE,"fcba4419-a2ee-464f-be9d-58f11bf3418b.sketch_text.stroke-35"),sQuery(id+"F2.wireOp",EDGE,"fcba4419-a2ee-464f-be9d-58f11bf3418b.sketch_text.stroke-36"),sQuery(id+"F2.wireOp",EDGE,"fcba4419-a2ee-464f-be9d-58f11bf3418b.sketch_text.stroke-37"),sQuery(id+"F2.wireOp",EDGE,"fcba4419-a2ee-464f-be9d-58f11bf3418b.sketch_text.stroke-38"),sQuery(id+"F2.wireOp",EDGE,"fcba4419-a2ee-464f-be9d-58f11bf3418b.sketch_text.stroke-39"),sQuery(id+"F2.wireOp",EDGE,"fcba4419-a2ee-464f-be9d-58f11bf3418b.sketch_text.stroke-40"),sQuery(id+"F2.wireOp",EDGE,"fcba4419-a2ee-464f-be9d-58f11bf3418b.sketch_text.stroke-41"),sQuery(id+"F2.wireOp",EDGE,"fcba4419-a2ee-464f-be9d-58f11bf3418b.sketch_text.stroke-42"),sQuery(id+"F2.wireOp",EDGE,"fcba4419-a2ee-464f-be9d-58f11bf3418b.sketch_text.stroke-43"),sQuery(id+"F2.wireOp",EDGE,"fcba4419-a2ee-464f-be9d-58f11bf3418b.sketch_text.stroke-44"),sQuery(id+"F2.wireOp",EDGE,"fcba4419-a2ee-464f-be9d-58f11bf3418b.sketch_text.stroke-45"),sQuery(id+"F2.wireOp",EDGE,"fcba4419-a2ee-464f-be9d-58f11bf3418b.sketch_text.stroke-46"),sQuery(id+"F2.wireOp",EDGE,"fcba4419-a2ee-464f-be9d-58f11bf3418b.sketch_text.stroke-47"),sQuery(id+"F2.wireOp",EDGE,"fcba4419-a2ee-464f-be9d-58f11bf3418b.sketch_text.stroke-48"),sQuery(id+"F2.wireOp",EDGE,"fcba4419-a2ee-464f-be9d-58f11bf3418b.sketch_text.stroke-49"),sQuery(id+"F2.wireOp",EDGE,"fcba4419-a2ee-464f-be9d-58f11bf3418b.sketch_text.stroke-50"),sQuery(id+"F2.wireOp",EDGE,"fcba4419-a2ee-464f-be9d-58f11bf3418b.sketch_text.stroke-51"),sQuery(id+"F2.wireOp",EDGE,"fcba4419-a2ee-464f-be9d-58f11bf3418b.sketch_text.stroke-52"),sQuery(id+"F2.wireOp",EDGE,"fcba4419-a2ee-464f-be9d-58f11bf3418b.sketch_text.stroke-53"),sQuery(id+"F2.wireOp",EDGE,"fcba4419-a2ee-464f-be9d-58f11bf3418b.sketch_text.stroke-54"),sQuery(id+"F2.wireOp",EDGE,"fcba4419-a2ee-464f-be9d-58f11bf3418b.sketch_text.stroke-55"),sQuery(id+"F2.wireOp",EDGE,"fcba4419-a2ee-464f-be9d-58f11bf3418b.sketch_text.stroke-56"),sQuery(id+"F2.wireOp",EDGE,"fcba4419-a2ee-464f-be9d-58f11bf3418b.sketch_text.stroke-57"),sQuery(id+"F2.wireOp",EDGE,"fcba4419-a2ee-464f-be9d-58f11bf3418b.sketch_text.stroke-58"),sQuery(id+"F2.wireOp",EDGE,"fcba4419-a2ee-464f-be9d-58f11bf3418b.sketch_text.stroke-59"),sQuery(id+"F2.wireOp",EDGE,"fcba4419-a2ee-464f-be9d-58f11bf3418b.sketch_text.stroke-60"),sQuery(id+"F2.wireOp",EDGE,"fcba4419-a2ee-464f-be9d-58f11bf3418b.sketch_text.stroke-61"),sQuery(id+"F2.wireOp",EDGE,"fcba4419-a2ee-464f-be9d-58f11bf3418b.sketch_text.stroke-62"),sQuery(id+"F2.wireOp",EDGE,"fcba4419-a2ee-464f-be9d-58f11bf3418b.sketch_text.stroke-63"),sQuery(id+"F2.wireOp",EDGE,"fcba4419-a2ee-464f-be9d-58f11bf3418b.sketch_text.stroke-64"),sQuery(id+"F2.wireOp",EDGE,"fcba4419-a2ee-464f-be9d-58f11bf3418b.sketch_text.stroke-65"),sQuery(id+"F2.wireOp",EDGE,"fcba4419-a2ee-464f-be9d-58f11bf3418b.sketch_text.stroke-66"),sQuery(id+"F2.wireOp",EDGE,"fcba4419-a2ee-464f-be9d-58f11bf3418b.sketch_text.stroke-67"),sQuery(id+"F2.wireOp",EDGE,"fcba4419-a2ee-464f-be9d-58f11bf3418b.sketch_text.stroke-68"),sQuery(id+"F2.wireOp",EDGE,"fcba4419-a2ee-464f-be9d-58f11bf3418b.sketch_text.stroke-69"),sQuery(id+"F2.wireOp",EDGE,"fcba4419-a2ee-464f-be9d-58f11bf3418b.sketch_text.stroke-70"),sQuery(id+"F2.wireOp",EDGE,"fcba4419-a2ee-464f-be9d-58f11bf3418b.sketch_text.stroke-71"),sQuery(id+"F2.wireOp",EDGE,"fcba4419-a2ee-464f-be9d-58f11bf3418b.sketch_text.stroke-72"),sQuery(id+"F2.wireOp",EDGE,"fcba4419-a2ee-464f-be9d-58f11bf3418b.sketch_text.stroke-73"),sQuery(id+"F2.wireOp",EDGE,"fcba4419-a2ee-464f-be9d-58f11bf3418b.sketch_text.stroke-74"),sQuery(id+"F2.wireOp",EDGE,"fcba4419-a2ee-464f-be9d-58f11bf3418b.sketch_text.stroke-75"),sQuery(id+"F2.wireOp",EDGE,"fcba4419-a2ee-464f-be9d-58f11bf3418b.sketch_text.stroke-76"),sQuery(id+"F2.wireOp",EDGE,"fcba4419-a2ee-464f-be9d-58f11bf3418b.sketch_text.stroke-77"),sQuery(id+"F2.wireOp",EDGE,"fcba4419-a2ee-464f-be9d-58f11bf3418b.sketch_text.stroke-78"),sQuery(id+"F2.wireOp",EDGE,"fcba4419-a2ee-464f-be9d-58f11bf3418b.sketch_text.stroke-79"),sQuery(id+"F2.wireOp",EDGE,"fcba4419-a2ee-464f-be9d-58f11bf3418b.sketch_text.stroke-80"),sQuery(id+"F2.wireOp",EDGE,"fcba4419-a2ee-464f-be9d-58f11bf3418b.sketch_text.stroke-81"),sQuery(id+"F2.wireOp",EDGE,"fcba4419-a2ee-464f-be9d-58f11bf3418b.sketch_text.stroke-82"),sQuery(id+"F2.wireOp",EDGE,"fcba4419-a2ee-464f-be9d-58f11bf3418b.sketch_text.stroke-83"),sQuery(id+"F2.wireOp",EDGE,"fcba4419-a2ee-464f-be9d-58f11bf3418b.sketch_text.stroke-84"),sQuery(id+"F2.wireOp",EDGE,"fcba4419-a2ee-464f-be9d-58f11bf3418b.sketch_text.stroke-85"),sQuery(id+"F2.wireOp",EDGE,"fcba4419-a2ee-464f-be9d-58f11bf3418b.sketch_text.stroke-86"),sQuery(id+"F2.wireOp",EDGE,"fcba4419-a2ee-464f-be9d-58f11bf3418b.sketch_text.stroke-87"),sQuery(id+"F2.wireOp",EDGE,"fcba4419-a2ee-464f-be9d-58f11bf3418b.sketch_text.stroke-88"),sQuery(id+"F2.wireOp",EDGE,"fcba4419-a2ee-464f-be9d-58f11bf3418b.sketch_text.stroke-89"),sQuery(id+"F2.wireOp",EDGE,"fcba4419-a2ee-464f-be9d-58f11bf3418b.sketch_text.stroke-90"),sQuery(id+"F2.wireOp",EDGE,"fcba4419-a2ee-464f-be9d-58f11bf3418b.sketch_text.stroke-91"),sQuery(id+"F2.wireOp",EDGE,"fcba4419-a2ee-464f-be9d-58f11bf3418b.sketch_text.stroke-92"),sQuery(id+"F2.wireOp",EDGE,"fcba4419-a2ee-464f-be9d-58f11bf3418b.sketch_text.stroke-93"),sQuery(id+"F2.wireOp",EDGE,"fcba4419-a2ee-464f-be9d-58f11bf3418b.sketch_text.stroke-94"),sQuery(id+"F2.wireOp",EDGE,"fcba4419-a2ee-464f-be9d-58f11bf3418b.sketch_text.stroke-95"),sQuery(id+"F2.wireOp",EDGE,"fcba4419-a2ee-464f-be9d-58f11bf3418b.sketch_text.stroke-96"),sQuery(id+"F2.wireOp",EDGE,"fcba4419-a2ee-464f-be9d-58f11bf3418b.sketch_text.stroke-97"),sQuery(id+"F2.wireOp",EDGE,"fcba4419-a2ee-464f-be9d-58f11bf3418b.sketch_text.stroke-98"),sQuery(id+"F2.wireOp",EDGE,"fcba4419-a2ee-464f-be9d-58f11bf3418b.sketch_text.stroke-99"),sQuery(id+"F2.wireOp",EDGE,"fcba4419-a2ee-464f-be9d-58f11bf3418b.sketch_text.stroke-100"),sQuery(id+"F2.wireOp",EDGE,"fcba4419-a2ee-464f-be9d-58f11bf3418b.sketch_text.stroke-101"),sQuery(id+"F2.wireOp",EDGE,"fcba4419-a2ee-464f-be9d-58f11bf3418b.sketch_text.stroke-102"),sQuery(id+"F2.wireOp",EDGE,"fcba4419-a2ee-464f-be9d-58f11bf3418b.sketch_text.stroke-103"),sQuery(id+"F2.wireOp",EDGE,"fcba4419-a2ee-464f-be9d-58f11bf3418b.sketch_text.stroke-104"),sQuery(id+"F2.wireOp",EDGE,"fcba4419-a2ee-464f-be9d-58f11bf3418b.sketch_text.stroke-105"),sQuery(id+"F2.wireOp",EDGE,"fcba4419-a2ee-464f-be9d-58f11bf3418b.sketch_text.stroke-106"),sQuery(id+"F2.wireOp",EDGE,"fcba4419-a2ee-464f-be9d-58f11bf3418b.sketch_text.stroke-107"),sQuery(id+"F2.wireOp",EDGE,"fcba4419-a2ee-464f-be9d-58f11bf3418b.sketch_text.stroke-108"),sQuery(id+"F2.wireOp",EDGE,"fcba4419-a2ee-464f-be9d-58f11bf3418b.sketch_text.stroke-109"),sQuery(id+"F2.wireOp",EDGE,"fcba4419-a2ee-464f-be9d-58f11bf3418b.sketch_text.stroke-110"),sQuery(id+"F2.wireOp",EDGE,"fcba4419-a2ee-464f-be9d-58f11bf3418b.sketch_text.stroke-111"),sQuery(id+"F2.wireOp",EDGE,"fcba4419-a2ee-464f-be9d-58f11bf3418b.sketch_text.stroke-112"),sQuery(id+"F2.wireOp",EDGE,"fcba4419-a2ee-464f-be9d-58f11bf3418b.sketch_text.stroke-113"),sQuery(id+"F2.wireOp",EDGE,"fcba4419-a2ee-464f-be9d-58f11bf3418b.sketch_text.stroke-114"),sQuery(id+"F2.wireOp",EDGE,"fcba4419-a2ee-464f-be9d-58f11bf3418b.sketch_text.stroke-115"),sQuery(id+"F2.wireOp",EDGE,"fcba4419-a2ee-464f-be9d-58f11bf3418b.sketch_text.stroke-116"),sQuery(id+"F2.wireOp",EDGE,"fcba4419-a2ee-464f-be9d-58f11bf3418b.sketch_text.stroke-117"),sQuery(id+"F2.wireOp",EDGE,"fcba4419-a2ee-464f-be9d-58f11bf3418b.sketch_text.stroke-118"),sQuery(id+"F2.wireOp",EDGE,"fcba4419-a2ee-464f-be9d-58f11bf3418b.sketch_text.stroke-119"),sQuery(id+"F2.wireOp",EDGE,"fcba4419-a2ee-464f-be9d-58f11bf3418b.sketch_text.stroke-120"),sQuery(id+"F2.wireOp",EDGE,"fcba4419-a2ee-464f-be9d-58f11bf3418b.sketch_text.stroke-121"),sQuery(id+"F2.wireOp",EDGE,"fcba4419-a2ee-464f-be9d-58f11bf3418b.sketch_text.stroke-122"),sQuery(id+"F2.wireOp",EDGE,"fcba4419-a2ee-464f-be9d-58f11bf3418b.sketch_text.stroke-123"),sQuery(id+"F2.wireOp",EDGE,"fcba4419-a2ee-464f-be9d-58f11bf3418b.sketch_text.stroke-124"),sQuery(id+"F2.wireOp",EDGE,"fcba4419-a2ee-464f-be9d-58f11bf3418b.sketch_text.stroke-125"),sQuery(id+"F2.wireOp",EDGE,"fcba4419-a2ee-464f-be9d-58f11bf3418b.sketch_text.stroke-126"),sQuery(id+"F2.wireOp",EDGE,"fcba4419-a2ee-464f-be9d-58f11bf3418b.sketch_text.stroke-127"),sQuery(id+"F2.wireOp",EDGE,"fcba4419-a2ee-464f-be9d-58f11bf3418b.sketch_text.stroke-128"),sQuery(id+"F2.wireOp",EDGE,"fcba4419-a2ee-464f-be9d-58f11bf3418b.sketch_text.stroke-129"),sQuery(id+"F2.wireOp",EDGE,"fcba4419-a2ee-464f-be9d-58f11bf3418b.sketch_text.stroke-130"),sQuery(id+"F2.wireOp",EDGE,"fcba4419-a2ee-464f-be9d-58f11bf3418b.sketch_text.stroke-131"),sQuery(id+"F2.wireOp",EDGE,"fcba4419-a2ee-464f-be9d-58f11bf3418b.sketch_text.stroke-132"),sQuery(id+"F2.wireOp",EDGE,"fcba4419-a2ee-464f-be9d-58f11bf3418b.sketch_text.stroke-133"),sQuery(id+"F2.wireOp",EDGE,"fcba4419-a2ee-464f-be9d-58f11bf3418b.sketch_text.stroke-134"),sQuery(id+"F2.wireOp",EDGE,"fcba4419-a2ee-464f-be9d-58f11bf3418b.sketch_text.stroke-135"),sQuery(id+"F2.wireOp",EDGE,"fcba4419-a2ee-464f-be9d-58f11bf3418b.sketch_text.stroke-136"),sQuery(id+"F2.wireOp",EDGE,"fcba4419-a2ee-464f-be9d-58f11bf3418b.sketch_text.stroke-137"),sQuery(id+"F2.wireOp",EDGE,"fcba4419-a2ee-464f-be9d-58f11bf3418b.sketch_text.stroke-138"),sQuery(id+"F2.wireOp",EDGE,"fcba4419-a2ee-464f-be9d-58f11bf3418b.sketch_text.stroke-139"),sQuery(id+"F2.wireOp",EDGE,"fcba4419-a2ee-464f-be9d-58f11bf3418b.sketch_text.stroke-140"),sQuery(id+"F2.wireOp",EDGE,"fcba4419-a2ee-464f-be9d-58f11bf3418b.sketch_text.stroke-141"),sQuery(id+"F2.wireOp",EDGE,"fcba4419-a2ee-464f-be9d-58f11bf3418b.sketch_text.stroke-142"),sQuery(id+"F2.wireOp",EDGE,"fcba4419-a2ee-464f-be9d-58f11bf3418b.sketch_text.stroke-143"),sQuery(id+"F2.wireOp",EDGE,"fcba4419-a2ee-464f-be9d-58f11bf3418b.sketch_text.stroke-144"),sQuery(id+"F2.wireOp",EDGE,"fcba4419-a2ee-464f-be9d-58f11bf3418b.sketch_text.stroke-145"),sQuery(id+"F2.wireOp",EDGE,"fcba4419-a2ee-464f-be9d-58f11bf3418b.sketch_text.stroke-146"),sQuery(id+"F2.wireOp",EDGE,"fcba4419-a2ee-464f-be9d-58f11bf3418b.sketch_text.stroke-147"),sQuery(id+"F2.wireOp",EDGE,"fcba4419-a2ee-464f-be9d-58f11bf3418b.sketch_text.stroke-148"),sQuery(id+"F2.wireOp",EDGE,"fcba4419-a2ee-464f-be9d-58f11bf3418b.sketch_text.stroke-149"),sQuery(id+"F2.wireOp",EDGE,"fcba4419-a2ee-464f-be9d-58f11bf3418b.sketch_text.stroke-150"),sQuery(id+"F2.wireOp",EDGE,"fcba4419-a2ee-464f-be9d-58f11bf3418b.sketch_text.stroke-151"),sQuery(id+"F2.wireOp",EDGE,"fcba4419-a2ee-464f-be9d-58f11bf3418b.sketch_text.stroke-152"),sQuery(id+"F2.wireOp",EDGE,"fcba4419-a2ee-464f-be9d-58f11bf3418b.sketch_text.stroke-153"),sQuery(id+"F2.wireOp",EDGE,"fcba4419-a2ee-464f-be9d-58f11bf3418b.sketch_text.stroke-154"),sQuery(id+"F2.wireOp",EDGE,"fcba4419-a2ee-464f-be9d-58f11bf3418b.sketch_text.stroke-155"),sQuery(id+"F2.wireOp",EDGE,"fcba4419-a2ee-464f-be9d-58f11bf3418b.sketch_text.stroke-156"),sQuery(id+"F2.wireOp",EDGE,"fcba4419-a2ee-464f-be9d-58f11bf3418b.sketch_text.stroke-157"),sQuery(id+"F2.wireOp",EDGE,"fcba4419-a2ee-464f-be9d-58f11bf3418b.sketch_text.stroke-158"),sQuery(id+"F2.wireOp",EDGE,"fcba4419-a2ee-464f-be9d-58f11bf3418b.sketch_text.stroke-159"),sQuery(id+"F2.wireOp",EDGE,"fcba4419-a2ee-464f-be9d-58f11bf3418b.sketch_text.stroke-160"),sQuery(id+"F2.wireOp",EDGE,"fcba4419-a2ee-464f-be9d-58f11bf3418b.sketch_text.stroke-161"),sQuery(id+"F2.wireOp",EDGE,"fcba4419-a2ee-464f-be9d-58f11bf3418b.sketch_text.stroke-162"),sQuery(id+"F2.wireOp",EDGE,"fcba4419-a2ee-464f-be9d-58f11bf3418b.sketch_text.stroke-163"),sQuery(id+"F2.wireOp",EDGE,"fcba4419-a2ee-464f-be9d-58f11bf3418b.sketch_text.stroke-164"),sQuery(id+"F2.wireOp",EDGE,"fcba4419-a2ee-464f-be9d-58f11bf3418b.sketch_text.stroke-165"),sQuery(id+"F2.wireOp",EDGE,"fcba4419-a2ee-464f-be9d-58f11bf3418b.sketch_text.stroke-166"),sQuery(id+"F2.wireOp",EDGE,"fcba4419-a2ee-464f-be9d-58f11bf3418b.sketch_text.stroke-167"),sQuery(id+"F2.wireOp",EDGE,"fcba4419-a2ee-464f-be9d-58f11bf3418b.sketch_text.stroke-168"),sQuery(id+"F2.wireOp",EDGE,"fcba4419-a2ee-464f-be9d-58f11bf3418b.sketch_text.stroke-169"),sQuery(id+"F2.wireOp",EDGE,"fcba4419-a2ee-464f-be9d-58f11bf3418b.sketch_text.stroke-170"),sQuery(id+"F2.wireOp",EDGE,"fcba4419-a2ee-464f-be9d-58f11bf3418b.sketch_text.stroke-171"),sQuery(id+"F2.wireOp",EDGE,"fcba4419-a2ee-464f-be9d-58f11bf3418b.sketch_text.stroke-172"),sQuery(id+"F2.wireOp",EDGE,"fcba4419-a2ee-464f-be9d-58f11bf3418b.sketch_text.stroke-173"),sQuery(id+"FHMxAyK4CFUKdhS_1.wireOp",EDGE,"1cb9c079-ea9b-4899-8069-e0e3048e911d.sketch_text.stroke-0"),sQuery(id+"FHMxAyK4CFUKdhS_1.wireOp",EDGE,"1cb9c079-ea9b-4899-8069-e0e3048e911d.sketch_text.stroke-1"),sQuery(id+"FHMxAyK4CFUKdhS_1.wireOp",EDGE,"1cb9c079-ea9b-4899-8069-e0e3048e911d.sketch_text.stroke-2"),sQuery(id+"FHMxAyK4CFUKdhS_1.wireOp",EDGE,"1cb9c079-ea9b-4899-8069-e0e3048e911d.sketch_text.stroke-3"),sQuery(id+"FHMxAyK4CFUKdhS_1.wireOp",EDGE,"1cb9c079-ea9b-4899-8069-e0e3048e911d.sketch_text.stroke-4"),sQuery(id+"FHMxAyK4CFUKdhS_1.wireOp",EDGE,"1cb9c079-ea9b-4899-8069-e0e3048e911d.sketch_text.stroke-5"),sQuery(id+"FHMxAyK4CFUKdhS_1.wireOp",EDGE,"1cb9c079-ea9b-4899-8069-e0e3048e911d.sketch_text.stroke-6"),sQuery(id+"FHMxAyK4CFUKdhS_1.wireOp",EDGE,"1cb9c079-ea9b-4899-8069-e0e3048e911d.sketch_text.stroke-7"),sQuery(id+"FHMxAyK4CFUKdhS_1.wireOp",EDGE,"1cb9c079-ea9b-4899-8069-e0e3048e911d.sketch_text.stroke-8"),sQuery(id+"FHMxAyK4CFUKdhS_1.wireOp",EDGE,"1cb9c079-ea9b-4899-8069-e0e3048e911d.sketch_text.stroke-9"),sQuery(id+"FHMxAyK4CFUKdhS_1.wireOp",EDGE,"1cb9c079-ea9b-4899-8069-e0e3048e911d.sketch_text.stroke-10"),sQuery(id+"FHMxAyK4CFUKdhS_1.wireOp",EDGE,"1cb9c079-ea9b-4899-8069-e0e3048e911d.sketch_text.stroke-11"),sQuery(id+"FHMxAyK4CFUKdhS_1.wireOp",EDGE,"1cb9c079-ea9b-4899-8069-e0e3048e911d.sketch_text.stroke-12"),sQuery(id+"FHMxAyK4CFUKdhS_1.wireOp",EDGE,"1cb9c079-ea9b-4899-8069-e0e3048e911d.sketch_text.stroke-13"),sQuery(id+"FHMxAyK4CFUKdhS_1.wireOp",EDGE,"1cb9c079-ea9b-4899-8069-e0e3048e911d.sketch_text.stroke-14"),sQuery(id+"FHMxAyK4CFUKdhS_1.wireOp",EDGE,"1cb9c079-ea9b-4899-8069-e0e3048e911d.sketch_text.stroke-15"),sQuery(id+"FHMxAyK4CFUKdhS_1.wireOp",EDGE,"1cb9c079-ea9b-4899-8069-e0e3048e911d.sketch_text.stroke-16"),sQuery(id+"FHMxAyK4CFUKdhS_1.wireOp",EDGE,"1cb9c079-ea9b-4899-8069-e0e3048e911d.sketch_text.stroke-17"),sQuery(id+"FHMxAyK4CFUKdhS_1.wireOp",EDGE,"1cb9c079-ea9b-4899-8069-e0e3048e911d.sketch_text.stroke-18"),sQuery(id+"FHMxAyK4CFUKdhS_1.wireOp",EDGE,"1cb9c079-ea9b-4899-8069-e0e3048e911d.sketch_text.stroke-19"),sQuery(id+"FHMxAyK4CFUKdhS_1.wireOp",EDGE,"1cb9c079-ea9b-4899-8069-e0e3048e911d.sketch_text.stroke-20"),sQuery(id+"FHMxAyK4CFUKdhS_1.wireOp",EDGE,"1cb9c079-ea9b-4899-8069-e0e3048e911d.sketch_text.stroke-21"),sQuery(id+"FHMxAyK4CFUKdhS_1.wireOp",EDGE,"1cb9c079-ea9b-4899-8069-e0e3048e911d.sketch_text.stroke-22"),sQuery(id+"FHMxAyK4CFUKdhS_1.wireOp",EDGE,"1cb9c079-ea9b-4899-8069-e0e3048e911d.sketch_text.stroke-23"),sQuery(id+"FHMxAyK4CFUKdhS_1.wireOp",EDGE,"1cb9c079-ea9b-4899-8069-e0e3048e911d.sketch_text.stroke-24"),sQuery(id+"FHMxAyK4CFUKdhS_1.wireOp",EDGE,"1cb9c079-ea9b-4899-8069-e0e3048e911d.sketch_text.stroke-25"),sQuery(id+"FHMxAyK4CFUKdhS_1.wireOp",EDGE,"1cb9c079-ea9b-4899-8069-e0e3048e911d.sketch_text.stroke-26"),sQuery(id+"FHMxAyK4CFUKdhS_1.wireOp",EDGE,"1cb9c079-ea9b-4899-8069-e0e3048e911d.sketch_text.stroke-27"),sQuery(id+"FHMxAyK4CFUKdhS_1.wireOp",EDGE,"1cb9c079-ea9b-4899-8069-e0e3048e911d.sketch_text.stroke-28"),sQuery(id+"FHMxAyK4CFUKdhS_1.wireOp",EDGE,"1cb9c079-ea9b-4899-8069-e0e3048e911d.sketch_text.stroke-29"),sQuery(id+"FHMxAyK4CFUKdhS_1.wireOp",EDGE,"1cb9c079-ea9b-4899-8069-e0e3048e911d.sketch_text.stroke-30"),sQuery(id+"FHMxAyK4CFUKdhS_1.wireOp",EDGE,"1cb9c079-ea9b-4899-8069-e0e3048e911d.sketch_text.stroke-31"),sQuery(id+"FHMxAyK4CFUKdhS_1.wireOp",EDGE,"1cb9c079-ea9b-4899-8069-e0e3048e911d.sketch_text.stroke-32"),sQuery(id+"FHMxAyK4CFUKdhS_1.wireOp",EDGE,"1cb9c079-ea9b-4899-8069-e0e3048e911d.sketch_text.stroke-33"),sQuery(id+"FHMxAyK4CFUKdhS_1.wireOp",EDGE,"1cb9c079-ea9b-4899-8069-e0e3048e911d.sketch_text.stroke-34"),sQuery(id+"FHMxAyK4CFUKdhS_1.wireOp",EDGE,"1cb9c079-ea9b-4899-8069-e0e3048e911d.sketch_text.stroke-35"),sQuery(id+"FHMxAyK4CFUKdhS_1.wireOp",EDGE,"1cb9c079-ea9b-4899-8069-e0e3048e911d.sketch_text.stroke-36"),sQuery(id+"FHMxAyK4CFUKdhS_1.wireOp",EDGE,"1cb9c079-ea9b-4899-8069-e0e3048e911d.sketch_text.stroke-37"),sQuery(id+"FHMxAyK4CFUKdhS_1.wireOp",EDGE,"1cb9c079-ea9b-4899-8069-e0e3048e911d.sketch_text.stroke-38"),sQuery(id+"FHMxAyK4CFUKdhS_1.wireOp",EDGE,"1cb9c079-ea9b-4899-8069-e0e3048e911d.sketch_text.stroke-39"),sQuery(id+"FHMxAyK4CFUKdhS_1.wireOp",EDGE,"1cb9c079-ea9b-4899-8069-e0e3048e911d.sketch_text.stroke-40"),sQuery(id+"FHMxAyK4CFUKdhS_1.wireOp",EDGE,"1cb9c079-ea9b-4899-8069-e0e3048e911d.sketch_text.stroke-41"),sQuery(id+"FHMxAyK4CFUKdhS_1.wireOp",EDGE,"1cb9c079-ea9b-4899-8069-e0e3048e911d.sketch_text.stroke-42"),sQuery(id+"FHMxAyK4CFUKdhS_1.wireOp",EDGE,"1cb9c079-ea9b-4899-8069-e0e3048e911d.sketch_text.stroke-43"),sQuery(id+"FHMxAyK4CFUKdhS_1.wireOp",EDGE,"1cb9c079-ea9b-4899-8069-e0e3048e911d.sketch_text.stroke-44"),sQuery(id+"FHMxAyK4CFUKdhS_1.wireOp",EDGE,"1cb9c079-ea9b-4899-8069-e0e3048e911d.sketch_text.stroke-45"),sQuery(id+"FHMxAyK4CFUKdhS_1.wireOp",EDGE,"1cb9c079-ea9b-4899-8069-e0e3048e911d.sketch_text.stroke-46"),sQuery(id+"FHMxAyK4CFUKdhS_1.wireOp",EDGE,"1cb9c079-ea9b-4899-8069-e0e3048e911d.sketch_text.stroke-47"),sQuery(id+"FHMxAyK4CFUKdhS_1.wireOp",EDGE,"1cb9c079-ea9b-4899-8069-e0e3048e911d.sketch_text.stroke-48"),sQuery(id+"FHMxAyK4CFUKdhS_1.wireOp",EDGE,"1cb9c079-ea9b-4899-8069-e0e3048e911d.sketch_text.stroke-49"),sQuery(id+"FHMxAyK4CFUKdhS_1.wireOp",EDGE,"1cb9c079-ea9b-4899-8069-e0e3048e911d.sketch_text.stroke-50"),sQuery(id+"FHMxAyK4CFUKdhS_1.wireOp",EDGE,"1cb9c079-ea9b-4899-8069-e0e3048e911d.sketch_text.stroke-51"),sQuery(id+"FHMxAyK4CFUKdhS_1.wireOp",EDGE,"1cb9c079-ea9b-4899-8069-e0e3048e911d.sketch_text.stroke-52"),sQuery(id+"FHMxAyK4CFUKdhS_1.wireOp",EDGE,"1cb9c079-ea9b-4899-8069-e0e3048e911d.sketch_text.stroke-53"),sQuery(id+"FHMxAyK4CFUKdhS_1.wireOp",EDGE,"1cb9c079-ea9b-4899-8069-e0e3048e911d.sketch_text.stroke-54"),sQuery(id+"FHMxAyK4CFUKdhS_1.wireOp",EDGE,"1cb9c079-ea9b-4899-8069-e0e3048e911d.sketch_text.stroke-55"),sQuery(id+"FHMxAyK4CFUKdhS_1.wireOp",EDGE,"1cb9c079-ea9b-4899-8069-e0e3048e911d.sketch_text.stroke-56"),sQuery(id+"FHMxAyK4CFUKdhS_1.wireOp",EDGE,"1cb9c079-ea9b-4899-8069-e0e3048e911d.sketch_text.stroke-57"),sQuery(id+"FHMxAyK4CFUKdhS_1.wireOp",EDGE,"1cb9c079-ea9b-4899-8069-e0e3048e911d.sketch_text.stroke-58"),sQuery(id+"FHMxAyK4CFUKdhS_1.wireOp",EDGE,"1cb9c079-ea9b-4899-8069-e0e3048e911d.sketch_text.stroke-59"),sQuery(id+"FHMxAyK4CFUKdhS_1.wireOp",EDGE,"1cb9c079-ea9b-4899-8069-e0e3048e911d.sketch_text.stroke-60"),sQuery(id+"FHMxAyK4CFUKdhS_1.wireOp",EDGE,"1cb9c079-ea9b-4899-8069-e0e3048e911d.sketch_text.stroke-61"),sQuery(id+"FHMxAyK4CFUKdhS_1.wireOp",EDGE,"1cb9c079-ea9b-4899-8069-e0e3048e911d.sketch_text.stroke-62"),sQuery(id+"FHMxAyK4CFUKdhS_1.wireOp",EDGE,"1cb9c079-ea9b-4899-8069-e0e3048e911d.sketch_text.stroke-71"),sQuery(id+"FHMxAyK4CFUKdhS_1.wireOp",EDGE,"1cb9c079-ea9b-4899-8069-e0e3048e911d.sketch_text.stroke-72"),sQuery(id+"FHMxAyK4CFUKdhS_1.wireOp",EDGE,"1cb9c079-ea9b-4899-8069-e0e3048e911d.sketch_text.stroke-73"),sQuery(id+"FHMxAyK4CFUKdhS_1.wireOp",EDGE,"1cb9c079-ea9b-4899-8069-e0e3048e911d.sketch_text.stroke-74"),sQuery(id+"FHMxAyK4CFUKdhS_1.wireOp",EDGE,"1cb9c079-ea9b-4899-8069-e0e3048e911d.sketch_text.stroke-75"),sQuery(id+"FHMxAyK4CFUKdhS_1.wireOp",EDGE,"1cb9c079-ea9b-4899-8069-e0e3048e911d.sketch_text.stroke-76"),sQuery(id+"FHMxAyK4CFUKdhS_1.wireOp",EDGE,"1cb9c079-ea9b-4899-8069-e0e3048e911d.sketch_text.stroke-77"),sQuery(id+"FHMxAyK4CFUKdhS_1.wireOp",EDGE,"1cb9c079-ea9b-4899-8069-e0e3048e911d.sketch_text.stroke-78"),sQuery(id+"FHMxAyK4CFUKdhS_1.wireOp",EDGE,"1cb9c079-ea9b-4899-8069-e0e3048e911d.sketch_text.stroke-79"),sQuery(id+"FHMxAyK4CFUKdhS_1.wireOp",EDGE,"1cb9c079-ea9b-4899-8069-e0e3048e911d.sketch_text.stroke-80"),sQuery(id+"FHMxAyK4CFUKdhS_1.wireOp",EDGE,"1cb9c079-ea9b-4899-8069-e0e3048e911d.sketch_text.stroke-81"),sQuery(id+"FHMxAyK4CFUKdhS_1.wireOp",EDGE,"1cb9c079-ea9b-4899-8069-e0e3048e911d.sketch_text.stroke-82"),sQuery(id+"FHMxAyK4CFUKdhS_1.wireOp",EDGE,"1cb9c079-ea9b-4899-8069-e0e3048e911d.sketch_text.stroke-83"),sQuery(id+"FHMxAyK4CFUKdhS_1.wireOp",EDGE,"1cb9c079-ea9b-4899-8069-e0e3048e911d.sketch_text.stroke-84"),sQuery(id+"FHMxAyK4CFUKdhS_1.wireOp",EDGE,"1cb9c079-ea9b-4899-8069-e0e3048e911d.sketch_text.stroke-85"),sQuery(id+"FHMxAyK4CFUKdhS_1.wireOp",EDGE,"1cb9c079-ea9b-4899-8069-e0e3048e911d.sketch_text.stroke-86"),sQuery(id+"FHMxAyK4CFUKdhS_1.wireOp",EDGE,"1cb9c079-ea9b-4899-8069-e0e3048e911d.sketch_text.stroke-87"),sQuery(id+"FHMxAyK4CFUKdhS_1.wireOp",EDGE,"1cb9c079-ea9b-4899-8069-e0e3048e911d.sketch_text.stroke-88"),sQuery(id+"FHMxAyK4CFUKdhS_1.wireOp",EDGE,"1cb9c079-ea9b-4899-8069-e0e3048e911d.sketch_text.stroke-89"),sQuery(id+"FHMxAyK4CFUKdhS_1.wireOp",EDGE,"1cb9c079-ea9b-4899-8069-e0e3048e911d.sketch_text.stroke-90"),sQuery(id+"FHMxAyK4CFUKdhS_1.wireOp",EDGE,"1cb9c079-ea9b-4899-8069-e0e3048e911d.sketch_text.stroke-91"),sQuery(id+"FHMxAyK4CFUKdhS_1.wireOp",EDGE,"1cb9c079-ea9b-4899-8069-e0e3048e911d.sketch_text.stroke-92"),sQuery(id+"FHMxAyK4CFUKdhS_1.wireOp",EDGE,"1cb9c079-ea9b-4899-8069-e0e3048e911d.sketch_text.stroke-93"),sQuery(id+"FHMxAyK4CFUKdhS_1.wireOp",EDGE,"1cb9c079-ea9b-4899-8069-e0e3048e911d.sketch_text.stroke-94"),sQuery(id+"FHMxAyK4CFUKdhS_1.wireOp",EDGE,"1cb9c079-ea9b-4899-8069-e0e3048e911d.sketch_text.stroke-95"),sQuery(id+"FHMxAyK4CFUKdhS_1.wireOp",EDGE,"1cb9c079-ea9b-4899-8069-e0e3048e911d.sketch_text.stroke-96"),sQuery(id+"FHMxAyK4CFUKdhS_1.wireOp",EDGE,"1cb9c079-ea9b-4899-8069-e0e3048e911d.sketch_text.stroke-97"),sQuery(id+"FHMxAyK4CFUKdhS_1.wireOp",EDGE,"1cb9c079-ea9b-4899-8069-e0e3048e911d.sketch_text.stroke-103"),sQuery(id+"FHMxAyK4CFUKdhS_1.wireOp",EDGE,"1cb9c079-ea9b-4899-8069-e0e3048e911d.sketch_text.stroke-104"),sQuery(id+"FHMxAyK4CFUKdhS_1.wireOp",EDGE,"1cb9c079-ea9b-4899-8069-e0e3048e911d.sketch_text.stroke-105"),sQuery(id+"FHMxAyK4CFUKdhS_1.wireOp",EDGE,"1cb9c079-ea9b-4899-8069-e0e3048e911d.sketch_text.stroke-106"),sQuery(id+"FHMxAyK4CFUKdhS_1.wireOp",EDGE,"1cb9c079-ea9b-4899-8069-e0e3048e911d.sketch_text.stroke-107"),sQuery(id+"FHMxAyK4CFUKdhS_1.wireOp",EDGE,"1cb9c079-ea9b-4899-8069-e0e3048e911d.sketch_text.stroke-108"),sQuery(id+"FHMxAyK4CFUKdhS_1.wireOp",EDGE,"1cb9c079-ea9b-4899-8069-e0e3048e911d.sketch_text.stroke-109"),sQuery(id+"FHMxAyK4CFUKdhS_1.wireOp",EDGE,"1cb9c079-ea9b-4899-8069-e0e3048e911d.sketch_text.stroke-110"),sQuery(id+"FHMxAyK4CFUKdhS_1.wireOp",EDGE,"1cb9c079-ea9b-4899-8069-e0e3048e911d.sketch_text.stroke-111"),sQuery(id+"FHMxAyK4CFUKdhS_1.wireOp",EDGE,"1cb9c079-ea9b-4899-8069-e0e3048e911d.sketch_text.stroke-112"),sQuery(id+"FHMxAyK4CFUKdhS_1.wireOp",EDGE,"1cb9c079-ea9b-4899-8069-e0e3048e911d.sketch_text.stroke-113"),sQuery(id+"FHMxAyK4CFUKdhS_1.wireOp",EDGE,"1cb9c079-ea9b-4899-8069-e0e3048e911d.sketch_text.stroke-114"),sQuery(id+"FHMxAyK4CFUKdhS_1.wireOp",EDGE,"1cb9c079-ea9b-4899-8069-e0e3048e911d.sketch_text.stroke-115"),sQuery(id+"FHMxAyK4CFUKdhS_1.wireOp",EDGE,"1cb9c079-ea9b-4899-8069-e0e3048e911d.sketch_text.stroke-116"),sQuery(id+"FHMxAyK4CFUKdhS_1.wireOp",EDGE,"1cb9c079-ea9b-4899-8069-e0e3048e911d.sketch_text.stroke-117"),sQuery(id+"FHMxAyK4CFUKdhS_1.wireOp",EDGE,"1cb9c079-ea9b-4899-8069-e0e3048e911d.sketch_text.stroke-118"),sQuery(id+"FHMxAyK4CFUKdhS_1.wireOp",EDGE,"1cb9c079-ea9b-4899-8069-e0e3048e911d.sketch_text.stroke-119"),sQuery(id+"FHMxAyK4CFUKdhS_1.wireOp",EDGE,"1cb9c079-ea9b-4899-8069-e0e3048e911d.sketch_text.stroke-120"),sQuery(id+"FHMxAyK4CFUKdhS_1.wireOp",EDGE,"1cb9c079-ea9b-4899-8069-e0e3048e911d.sketch_text.stroke-121"),sQuery(id+"FHMxAyK4CFUKdhS_1.wireOp",EDGE,"1cb9c079-ea9b-4899-8069-e0e3048e911d.sketch_text.stroke-122"),sQuery(id+"FHMxAyK4CFUKdhS_1.wireOp",EDGE,"1cb9c079-ea9b-4899-8069-e0e3048e911d.sketch_text.stroke-123"),sQuery(id+"FHMxAyK4CFUKdhS_1.wireOp",EDGE,"1cb9c079-ea9b-4899-8069-e0e3048e911d.sketch_text.stroke-124"),sQuery(id+"FHMxAyK4CFUKdhS_1.wireOp",EDGE,"1cb9c079-ea9b-4899-8069-e0e3048e911d.sketch_text.stroke-125"),sQuery(id+"FHMxAyK4CFUKdhS_1.wireOp",EDGE,"1cb9c079-ea9b-4899-8069-e0e3048e911d.sketch_text.stroke-126"),sQuery(id+"FHMxAyK4CFUKdhS_1.wireOp",EDGE,"1cb9c079-ea9b-4899-8069-e0e3048e911d.sketch_text.stroke-127"),sQuery(id+"FHMxAyK4CFUKdhS_1.wireOp",EDGE,"1cb9c079-ea9b-4899-8069-e0e3048e911d.sketch_text.stroke-128"),sQuery(id+"FHMxAyK4CFUKdhS_1.wireOp",EDGE,"1cb9c079-ea9b-4899-8069-e0e3048e911d.sketch_text.stroke-129"),sQuery(id+"FHMxAyK4CFUKdhS_1.wireOp",EDGE,"1cb9c079-ea9b-4899-8069-e0e3048e911d.sketch_text.stroke-130"),sQuery(id+"FHMxAyK4CFUKdhS_1.wireOp",EDGE,"1cb9c079-ea9b-4899-8069-e0e3048e911d.sketch_text.stroke-131"),sQuery(id+"FHMxAyK4CFUKdhS_1.wireOp",EDGE,"1cb9c079-ea9b-4899-8069-e0e3048e911d.sketch_text.stroke-132"),sQuery(id+"FHMxAyK4CFUKdhS_1.wireOp",EDGE,"1cb9c079-ea9b-4899-8069-e0e3048e911d.sketch_text.stroke-133"),sQuery(id+"FHMxAyK4CFUKdhS_1.wireOp",EDGE,"1cb9c079-ea9b-4899-8069-e0e3048e911d.sketch_text.stroke-134"),sQuery(id+"FHMxAyK4CFUKdhS_1.wireOp",EDGE,"1cb9c079-ea9b-4899-8069-e0e3048e911d.sketch_text.stroke-135"),sQuery(id+"FHMxAyK4CFUKdhS_1.wireOp",EDGE,"1cb9c079-ea9b-4899-8069-e0e3048e911d.sketch_text.stroke-136"),sQuery(id+"FHMxAyK4CFUKdhS_1.wireOp",EDGE,"1cb9c079-ea9b-4899-8069-e0e3048e911d.sketch_text.stroke-137"),sQuery(id+"FHMxAyK4CFUKdhS_1.wireOp",EDGE,"1cb9c079-ea9b-4899-8069-e0e3048e911d.sketch_text.stroke-138"),sQuery(id+"FHMxAyK4CFUKdhS_1.wireOp",EDGE,"1cb9c079-ea9b-4899-8069-e0e3048e911d.sketch_text.stroke-139"),sQuery(id+"FHMxAyK4CFUKdhS_1.wireOp",EDGE,"1cb9c079-ea9b-4899-8069-e0e3048e911d.sketch_text.stroke-140"),sQuery(id+"FHMxAyK4CFUKdhS_1.wireOp",EDGE,"1cb9c079-ea9b-4899-8069-e0e3048e911d.sketch_text.stroke-141"),sQuery(id+"FHMxAyK4CFUKdhS_1.wireOp",EDGE,"1cb9c079-ea9b-4899-8069-e0e3048e911d.sketch_text.stroke-142"),sQuery(id+"FHMxAyK4CFUKdhS_1.wireOp",EDGE,"1cb9c079-ea9b-4899-8069-e0e3048e911d.sketch_text.stroke-143"),sQuery(id+"FHMxAyK4CFUKdhS_1.wireOp",EDGE,"1cb9c079-ea9b-4899-8069-e0e3048e911d.sketch_text.stroke-144"),sQuery(id+"FHMxAyK4CFUKdhS_1.wireOp",EDGE,"1cb9c079-ea9b-4899-8069-e0e3048e911d.sketch_text.stroke-145"),sQuery(id+"FHMxAyK4CFUKdhS_1.wireOp",EDGE,"1cb9c079-ea9b-4899-8069-e0e3048e911d.sketch_text.stroke-146"),sQuery(id+"FHMxAyK4CFUKdhS_1.wireOp",EDGE,"1cb9c079-ea9b-4899-8069-e0e3048e911d.sketch_text.stroke-147"),sQuery(id+"FHMxAyK4CFUKdhS_1.wireOp",EDGE,"1cb9c079-ea9b-4899-8069-e0e3048e911d.sketch_text.stroke-148"),sQuery(id+"FHMxAyK4CFUKdhS_1.wireOp",EDGE,"1cb9c079-ea9b-4899-8069-e0e3048e911d.sketch_text.stroke-149"),sQuery(id+"FHMxAyK4CFUKdhS_1.wireOp",EDGE,"1cb9c079-ea9b-4899-8069-e0e3048e911d.sketch_text.stroke-150"),sQuery(id+"FHMxAyK4CFUKdhS_1.wireOp",EDGE,"1cb9c079-ea9b-4899-8069-e0e3048e911d.sketch_text.stroke-151"),sQuery(id+"FHMxAyK4CFUKdhS_1.wireOp",EDGE,"1cb9c079-ea9b-4899-8069-e0e3048e911d.sketch_text.stroke-152"),sQuery(id+"FHMxAyK4CFUKdhS_1.wireOp",EDGE,"1cb9c079-ea9b-4899-8069-e0e3048e911d.sketch_text.stroke-153"),sQuery(id+"FHMxAyK4CFUKdhS_1.wireOp",EDGE,"1cb9c079-ea9b-4899-8069-e0e3048e911d.sketch_text.stroke-159"),sQuery(id+"FHMxAyK4CFUKdhS_1.wireOp",EDGE,"1cb9c079-ea9b-4899-8069-e0e3048e911d.sketch_text.stroke-160"),sQuery(id+"FHMxAyK4CFUKdhS_1.wireOp",EDGE,"1cb9c079-ea9b-4899-8069-e0e3048e911d.sketch_text.stroke-161"),sQuery(id+"FHMxAyK4CFUKdhS_1.wireOp",EDGE,"1cb9c079-ea9b-4899-8069-e0e3048e911d.sketch_text.stroke-162"),sQuery(id+"FHMxAyK4CFUKdhS_1.wireOp",EDGE,"1cb9c079-ea9b-4899-8069-e0e3048e911d.sketch_text.stroke-163"),sQuery(id+"FHMxAyK4CFUKdhS_1.wireOp",EDGE,"1cb9c079-ea9b-4899-8069-e0e3048e911d.sketch_text.stroke-164"),sQuery(id+"FHMxAyK4CFUKdhS_1.wireOp",EDGE,"1cb9c079-ea9b-4899-8069-e0e3048e911d.sketch_text.stroke-165"),sQuery(id+"FHMxAyK4CFUKdhS_1.wireOp",EDGE,"1cb9c079-ea9b-4899-8069-e0e3048e911d.sketch_text.stroke-166"),sQuery(id+"FHMxAyK4CFUKdhS_1.wireOp",EDGE,"1cb9c079-ea9b-4899-8069-e0e3048e911d.sketch_text.stroke-167"),sQuery(id+"FHMxAyK4CFUKdhS_1.wireOp",EDGE,"1cb9c079-ea9b-4899-8069-e0e3048e911d.sketch_text.stroke-168"),sQuery(id+"FHMxAyK4CFUKdhS_1.wireOp",EDGE,"1cb9c079-ea9b-4899-8069-e0e3048e911d.sketch_text.stroke-169"),sQuery(id+"FHMxAyK4CFUKdhS_1.wireOp",EDGE,"1cb9c079-ea9b-4899-8069-e0e3048e911d.sketch_text.stroke-170"),sQuery(id+"FHMxAyK4CFUKdhS_1.wireOp",EDGE,"1cb9c079-ea9b-4899-8069-e0e3048e911d.sketch_text.stroke-171"),sQuery(id+"FHMxAyK4CFUKdhS_1.wireOp",EDGE,"1cb9c079-ea9b-4899-8069-e0e3048e911d.sketch_text.stroke-172"),sQuery(id+"FHMxAyK4CFUKdhS_1.wireOp",EDGE,"1cb9c079-ea9b-4899-8069-e0e3048e911d.sketch_text.stroke-173"),sQuery(id+"FHMxAyK4CFUKdhS_1.wireOp",EDGE,"1cb9c079-ea9b-4899-8069-e0e3048e911d.sketch_text.stroke-174"),sQuery(id+"FHMxAyK4CFUKdhS_1.wireOp",EDGE,"1cb9c079-ea9b-4899-8069-e0e3048e911d.sketch_text.stroke-175"),sQuery(id+"FHMxAyK4CFUKdhS_1.wireOp",EDGE,"1cb9c079-ea9b-4899-8069-e0e3048e911d.sketch_text.stroke-176"),sQuery(id+"FHMxAyK4CFUKdhS_1.wireOp",EDGE,"1cb9c079-ea9b-4899-8069-e0e3048e911d.sketch_text.stroke-177"),sQuery(id+"FHMxAyK4CFUKdhS_1.wireOp",EDGE,"1cb9c079-ea9b-4899-8069-e0e3048e911d.sketch_text.stroke-178"),sQuery(id+"FHMxAyK4CFUKdhS_1.wireOp",EDGE,"1cb9c079-ea9b-4899-8069-e0e3048e911d.sketch_text.stroke-179"),sQuery(id+"FHMxAyK4CFUKdhS_1.wireOp",EDGE,"1cb9c079-ea9b-4899-8069-e0e3048e911d.sketch_text.stroke-180"),subQ2,sQuery(id+"F3.wireOp",EDGE,"6ee83ff3-586e-4dbe-aaea-af71240543bd")])],"isStart":true})]),OD(1.0)],"derivedFrom":makeQuery(id+"F1.opExtrude","CAP_EDGE",EDGE,{"disambiguationData":[OSD([subQ0])],"isStart":false})});}
            var Q5;
            {var subQ0=sQuery(id+"F0.wireOp",EDGE,"E0.top");var subQ1=sQuery(id+"F0.wireOp",EDGE,"E0.bottom");var subQ2=sQuery(id+"F3.wireOp",EDGE,"8007402e-1a4e-4a06-85a5-2af08e553504");Q5=makeQuery(id+"F4.boolean.opBoolean","SPLIT",EDGE,{"disambiguationData":[TD([makeQuery(id+"F1.opExtrude","CAP_FACE",FACE,{"disambiguationData":[OSD([subQ1,subQ0,sQuery(id+"F0.wireOp",EDGE,"E0.left"),sQuery(id+"F0.wireOp",EDGE,"E0.right")])],"isStart":false}),makeQuery(id+"F1.opExtrude","SWEPT_FACE",FACE,{"disambiguationData":[OSD([subQ0])]}),makeQuery(id+"F4.opExtrude","SWEPT_FACE",FACE,{"disambiguationData":[OSD([subQ2])]}),makeQuery(id+"F4.opExtrude","CAP_FACE",FACE,{"disambiguationData":[OSD([subQ1,sQuery(id+"F2.wireOp",EDGE,"fcba4419-a2ee-464f-be9d-58f11bf3418b.sketch_text.stroke-0"),sQuery(id+"F2.wireOp",EDGE,"fcba4419-a2ee-464f-be9d-58f11bf3418b.sketch_text.stroke-1"),sQuery(id+"F2.wireOp",EDGE,"fcba4419-a2ee-464f-be9d-58f11bf3418b.sketch_text.stroke-2"),sQuery(id+"F2.wireOp",EDGE,"fcba4419-a2ee-464f-be9d-58f11bf3418b.sketch_text.stroke-3"),sQuery(id+"F2.wireOp",EDGE,"fcba4419-a2ee-464f-be9d-58f11bf3418b.sketch_text.stroke-4"),sQuery(id+"F2.wireOp",EDGE,"fcba4419-a2ee-464f-be9d-58f11bf3418b.sketch_text.stroke-5"),sQuery(id+"F2.wireOp",EDGE,"fcba4419-a2ee-464f-be9d-58f11bf3418b.sketch_text.stroke-6"),sQuery(id+"F2.wireOp",EDGE,"fcba4419-a2ee-464f-be9d-58f11bf3418b.sketch_text.stroke-7"),sQuery(id+"F2.wireOp",EDGE,"fcba4419-a2ee-464f-be9d-58f11bf3418b.sketch_text.stroke-8"),sQuery(id+"F2.wireOp",EDGE,"fcba4419-a2ee-464f-be9d-58f11bf3418b.sketch_text.stroke-9"),sQuery(id+"F2.wireOp",EDGE,"fcba4419-a2ee-464f-be9d-58f11bf3418b.sketch_text.stroke-10"),sQuery(id+"F2.wireOp",EDGE,"fcba4419-a2ee-464f-be9d-58f11bf3418b.sketch_text.stroke-11"),sQuery(id+"F2.wireOp",EDGE,"fcba4419-a2ee-464f-be9d-58f11bf3418b.sketch_text.stroke-12"),sQuery(id+"F2.wireOp",EDGE,"fcba4419-a2ee-464f-be9d-58f11bf3418b.sketch_text.stroke-13"),sQuery(id+"F2.wireOp",EDGE,"fcba4419-a2ee-464f-be9d-58f11bf3418b.sketch_text.stroke-14"),sQuery(id+"F2.wireOp",EDGE,"fcba4419-a2ee-464f-be9d-58f11bf3418b.sketch_text.stroke-15"),sQuery(id+"F2.wireOp",EDGE,"fcba4419-a2ee-464f-be9d-58f11bf3418b.sketch_text.stroke-16"),sQuery(id+"F2.wireOp",EDGE,"fcba4419-a2ee-464f-be9d-58f11bf3418b.sketch_text.stroke-17"),sQuery(id+"F2.wireOp",EDGE,"fcba4419-a2ee-464f-be9d-58f11bf3418b.sketch_text.stroke-18"),sQuery(id+"F2.wireOp",EDGE,"fcba4419-a2ee-464f-be9d-58f11bf3418b.sketch_text.stroke-19"),sQuery(id+"F2.wireOp",EDGE,"fcba4419-a2ee-464f-be9d-58f11bf3418b.sketch_text.stroke-20"),sQuery(id+"F2.wireOp",EDGE,"fcba4419-a2ee-464f-be9d-58f11bf3418b.sketch_text.stroke-21"),sQuery(id+"F2.wireOp",EDGE,"fcba4419-a2ee-464f-be9d-58f11bf3418b.sketch_text.stroke-22"),sQuery(id+"F2.wireOp",EDGE,"fcba4419-a2ee-464f-be9d-58f11bf3418b.sketch_text.stroke-23"),sQuery(id+"F2.wireOp",EDGE,"fcba4419-a2ee-464f-be9d-58f11bf3418b.sketch_text.stroke-24"),sQuery(id+"F2.wireOp",EDGE,"fcba4419-a2ee-464f-be9d-58f11bf3418b.sketch_text.stroke-25"),sQuery(id+"F2.wireOp",EDGE,"fcba4419-a2ee-464f-be9d-58f11bf3418b.sketch_text.stroke-26"),sQuery(id+"F2.wireOp",EDGE,"fcba4419-a2ee-464f-be9d-58f11bf3418b.sketch_text.stroke-27"),sQuery(id+"F2.wireOp",EDGE,"fcba4419-a2ee-464f-be9d-58f11bf3418b.sketch_text.stroke-28"),sQuery(id+"F2.wireOp",EDGE,"fcba4419-a2ee-464f-be9d-58f11bf3418b.sketch_text.stroke-29"),sQuery(id+"F2.wireOp",EDGE,"fcba4419-a2ee-464f-be9d-58f11bf3418b.sketch_text.stroke-30"),sQuery(id+"F2.wireOp",EDGE,"fcba4419-a2ee-464f-be9d-58f11bf3418b.sketch_text.stroke-31"),sQuery(id+"F2.wireOp",EDGE,"fcba4419-a2ee-464f-be9d-58f11bf3418b.sketch_text.stroke-32"),sQuery(id+"F2.wireOp",EDGE,"fcba4419-a2ee-464f-be9d-58f11bf3418b.sketch_text.stroke-33"),sQuery(id+"F2.wireOp",EDGE,"fcba4419-a2ee-464f-be9d-58f11bf3418b.sketch_text.stroke-34"),sQuery(id+"F2.wireOp",EDGE,"fcba4419-a2ee-464f-be9d-58f11bf3418b.sketch_text.stroke-35"),sQuery(id+"F2.wireOp",EDGE,"fcba4419-a2ee-464f-be9d-58f11bf3418b.sketch_text.stroke-36"),sQuery(id+"F2.wireOp",EDGE,"fcba4419-a2ee-464f-be9d-58f11bf3418b.sketch_text.stroke-37"),sQuery(id+"F2.wireOp",EDGE,"fcba4419-a2ee-464f-be9d-58f11bf3418b.sketch_text.stroke-38"),sQuery(id+"F2.wireOp",EDGE,"fcba4419-a2ee-464f-be9d-58f11bf3418b.sketch_text.stroke-39"),sQuery(id+"F2.wireOp",EDGE,"fcba4419-a2ee-464f-be9d-58f11bf3418b.sketch_text.stroke-40"),sQuery(id+"F2.wireOp",EDGE,"fcba4419-a2ee-464f-be9d-58f11bf3418b.sketch_text.stroke-41"),sQuery(id+"F2.wireOp",EDGE,"fcba4419-a2ee-464f-be9d-58f11bf3418b.sketch_text.stroke-42"),sQuery(id+"F2.wireOp",EDGE,"fcba4419-a2ee-464f-be9d-58f11bf3418b.sketch_text.stroke-43"),sQuery(id+"F2.wireOp",EDGE,"fcba4419-a2ee-464f-be9d-58f11bf3418b.sketch_text.stroke-44"),sQuery(id+"F2.wireOp",EDGE,"fcba4419-a2ee-464f-be9d-58f11bf3418b.sketch_text.stroke-45"),sQuery(id+"F2.wireOp",EDGE,"fcba4419-a2ee-464f-be9d-58f11bf3418b.sketch_text.stroke-46"),sQuery(id+"F2.wireOp",EDGE,"fcba4419-a2ee-464f-be9d-58f11bf3418b.sketch_text.stroke-47"),sQuery(id+"F2.wireOp",EDGE,"fcba4419-a2ee-464f-be9d-58f11bf3418b.sketch_text.stroke-48"),sQuery(id+"F2.wireOp",EDGE,"fcba4419-a2ee-464f-be9d-58f11bf3418b.sketch_text.stroke-49"),sQuery(id+"F2.wireOp",EDGE,"fcba4419-a2ee-464f-be9d-58f11bf3418b.sketch_text.stroke-50"),sQuery(id+"F2.wireOp",EDGE,"fcba4419-a2ee-464f-be9d-58f11bf3418b.sketch_text.stroke-51"),sQuery(id+"F2.wireOp",EDGE,"fcba4419-a2ee-464f-be9d-58f11bf3418b.sketch_text.stroke-52"),sQuery(id+"F2.wireOp",EDGE,"fcba4419-a2ee-464f-be9d-58f11bf3418b.sketch_text.stroke-53"),sQuery(id+"F2.wireOp",EDGE,"fcba4419-a2ee-464f-be9d-58f11bf3418b.sketch_text.stroke-54"),sQuery(id+"F2.wireOp",EDGE,"fcba4419-a2ee-464f-be9d-58f11bf3418b.sketch_text.stroke-55"),sQuery(id+"F2.wireOp",EDGE,"fcba4419-a2ee-464f-be9d-58f11bf3418b.sketch_text.stroke-56"),sQuery(id+"F2.wireOp",EDGE,"fcba4419-a2ee-464f-be9d-58f11bf3418b.sketch_text.stroke-57"),sQuery(id+"F2.wireOp",EDGE,"fcba4419-a2ee-464f-be9d-58f11bf3418b.sketch_text.stroke-58"),sQuery(id+"F2.wireOp",EDGE,"fcba4419-a2ee-464f-be9d-58f11bf3418b.sketch_text.stroke-59"),sQuery(id+"F2.wireOp",EDGE,"fcba4419-a2ee-464f-be9d-58f11bf3418b.sketch_text.stroke-60"),sQuery(id+"F2.wireOp",EDGE,"fcba4419-a2ee-464f-be9d-58f11bf3418b.sketch_text.stroke-61"),sQuery(id+"F2.wireOp",EDGE,"fcba4419-a2ee-464f-be9d-58f11bf3418b.sketch_text.stroke-62"),sQuery(id+"F2.wireOp",EDGE,"fcba4419-a2ee-464f-be9d-58f11bf3418b.sketch_text.stroke-63"),sQuery(id+"F2.wireOp",EDGE,"fcba4419-a2ee-464f-be9d-58f11bf3418b.sketch_text.stroke-64"),sQuery(id+"F2.wireOp",EDGE,"fcba4419-a2ee-464f-be9d-58f11bf3418b.sketch_text.stroke-65"),sQuery(id+"F2.wireOp",EDGE,"fcba4419-a2ee-464f-be9d-58f11bf3418b.sketch_text.stroke-66"),sQuery(id+"F2.wireOp",EDGE,"fcba4419-a2ee-464f-be9d-58f11bf3418b.sketch_text.stroke-67"),sQuery(id+"F2.wireOp",EDGE,"fcba4419-a2ee-464f-be9d-58f11bf3418b.sketch_text.stroke-68"),sQuery(id+"F2.wireOp",EDGE,"fcba4419-a2ee-464f-be9d-58f11bf3418b.sketch_text.stroke-69"),sQuery(id+"F2.wireOp",EDGE,"fcba4419-a2ee-464f-be9d-58f11bf3418b.sketch_text.stroke-70"),sQuery(id+"F2.wireOp",EDGE,"fcba4419-a2ee-464f-be9d-58f11bf3418b.sketch_text.stroke-71"),sQuery(id+"F2.wireOp",EDGE,"fcba4419-a2ee-464f-be9d-58f11bf3418b.sketch_text.stroke-72"),sQuery(id+"F2.wireOp",EDGE,"fcba4419-a2ee-464f-be9d-58f11bf3418b.sketch_text.stroke-73"),sQuery(id+"F2.wireOp",EDGE,"fcba4419-a2ee-464f-be9d-58f11bf3418b.sketch_text.stroke-74"),sQuery(id+"F2.wireOp",EDGE,"fcba4419-a2ee-464f-be9d-58f11bf3418b.sketch_text.stroke-75"),sQuery(id+"F2.wireOp",EDGE,"fcba4419-a2ee-464f-be9d-58f11bf3418b.sketch_text.stroke-76"),sQuery(id+"F2.wireOp",EDGE,"fcba4419-a2ee-464f-be9d-58f11bf3418b.sketch_text.stroke-77"),sQuery(id+"F2.wireOp",EDGE,"fcba4419-a2ee-464f-be9d-58f11bf3418b.sketch_text.stroke-78"),sQuery(id+"F2.wireOp",EDGE,"fcba4419-a2ee-464f-be9d-58f11bf3418b.sketch_text.stroke-79"),sQuery(id+"F2.wireOp",EDGE,"fcba4419-a2ee-464f-be9d-58f11bf3418b.sketch_text.stroke-80"),sQuery(id+"F2.wireOp",EDGE,"fcba4419-a2ee-464f-be9d-58f11bf3418b.sketch_text.stroke-81"),sQuery(id+"F2.wireOp",EDGE,"fcba4419-a2ee-464f-be9d-58f11bf3418b.sketch_text.stroke-82"),sQuery(id+"F2.wireOp",EDGE,"fcba4419-a2ee-464f-be9d-58f11bf3418b.sketch_text.stroke-83"),sQuery(id+"F2.wireOp",EDGE,"fcba4419-a2ee-464f-be9d-58f11bf3418b.sketch_text.stroke-84"),sQuery(id+"F2.wireOp",EDGE,"fcba4419-a2ee-464f-be9d-58f11bf3418b.sketch_text.stroke-85"),sQuery(id+"F2.wireOp",EDGE,"fcba4419-a2ee-464f-be9d-58f11bf3418b.sketch_text.stroke-86"),sQuery(id+"F2.wireOp",EDGE,"fcba4419-a2ee-464f-be9d-58f11bf3418b.sketch_text.stroke-87"),sQuery(id+"F2.wireOp",EDGE,"fcba4419-a2ee-464f-be9d-58f11bf3418b.sketch_text.stroke-88"),sQuery(id+"F2.wireOp",EDGE,"fcba4419-a2ee-464f-be9d-58f11bf3418b.sketch_text.stroke-89"),sQuery(id+"F2.wireOp",EDGE,"fcba4419-a2ee-464f-be9d-58f11bf3418b.sketch_text.stroke-90"),sQuery(id+"F2.wireOp",EDGE,"fcba4419-a2ee-464f-be9d-58f11bf3418b.sketch_text.stroke-91"),sQuery(id+"F2.wireOp",EDGE,"fcba4419-a2ee-464f-be9d-58f11bf3418b.sketch_text.stroke-92"),sQuery(id+"F2.wireOp",EDGE,"fcba4419-a2ee-464f-be9d-58f11bf3418b.sketch_text.stroke-93"),sQuery(id+"F2.wireOp",EDGE,"fcba4419-a2ee-464f-be9d-58f11bf3418b.sketch_text.stroke-94"),sQuery(id+"F2.wireOp",EDGE,"fcba4419-a2ee-464f-be9d-58f11bf3418b.sketch_text.stroke-95"),sQuery(id+"F2.wireOp",EDGE,"fcba4419-a2ee-464f-be9d-58f11bf3418b.sketch_text.stroke-96"),sQuery(id+"F2.wireOp",EDGE,"fcba4419-a2ee-464f-be9d-58f11bf3418b.sketch_text.stroke-97"),sQuery(id+"F2.wireOp",EDGE,"fcba4419-a2ee-464f-be9d-58f11bf3418b.sketch_text.stroke-98"),sQuery(id+"F2.wireOp",EDGE,"fcba4419-a2ee-464f-be9d-58f11bf3418b.sketch_text.stroke-99"),sQuery(id+"F2.wireOp",EDGE,"fcba4419-a2ee-464f-be9d-58f11bf3418b.sketch_text.stroke-100"),sQuery(id+"F2.wireOp",EDGE,"fcba4419-a2ee-464f-be9d-58f11bf3418b.sketch_text.stroke-101"),sQuery(id+"F2.wireOp",EDGE,"fcba4419-a2ee-464f-be9d-58f11bf3418b.sketch_text.stroke-102"),sQuery(id+"F2.wireOp",EDGE,"fcba4419-a2ee-464f-be9d-58f11bf3418b.sketch_text.stroke-103"),sQuery(id+"F2.wireOp",EDGE,"fcba4419-a2ee-464f-be9d-58f11bf3418b.sketch_text.stroke-104"),sQuery(id+"F2.wireOp",EDGE,"fcba4419-a2ee-464f-be9d-58f11bf3418b.sketch_text.stroke-105"),sQuery(id+"F2.wireOp",EDGE,"fcba4419-a2ee-464f-be9d-58f11bf3418b.sketch_text.stroke-106"),sQuery(id+"F2.wireOp",EDGE,"fcba4419-a2ee-464f-be9d-58f11bf3418b.sketch_text.stroke-107"),sQuery(id+"F2.wireOp",EDGE,"fcba4419-a2ee-464f-be9d-58f11bf3418b.sketch_text.stroke-108"),sQuery(id+"F2.wireOp",EDGE,"fcba4419-a2ee-464f-be9d-58f11bf3418b.sketch_text.stroke-109"),sQuery(id+"F2.wireOp",EDGE,"fcba4419-a2ee-464f-be9d-58f11bf3418b.sketch_text.stroke-110"),sQuery(id+"F2.wireOp",EDGE,"fcba4419-a2ee-464f-be9d-58f11bf3418b.sketch_text.stroke-111"),sQuery(id+"F2.wireOp",EDGE,"fcba4419-a2ee-464f-be9d-58f11bf3418b.sketch_text.stroke-112"),sQuery(id+"F2.wireOp",EDGE,"fcba4419-a2ee-464f-be9d-58f11bf3418b.sketch_text.stroke-113"),sQuery(id+"F2.wireOp",EDGE,"fcba4419-a2ee-464f-be9d-58f11bf3418b.sketch_text.stroke-114"),sQuery(id+"F2.wireOp",EDGE,"fcba4419-a2ee-464f-be9d-58f11bf3418b.sketch_text.stroke-115"),sQuery(id+"F2.wireOp",EDGE,"fcba4419-a2ee-464f-be9d-58f11bf3418b.sketch_text.stroke-116"),sQuery(id+"F2.wireOp",EDGE,"fcba4419-a2ee-464f-be9d-58f11bf3418b.sketch_text.stroke-117"),sQuery(id+"F2.wireOp",EDGE,"fcba4419-a2ee-464f-be9d-58f11bf3418b.sketch_text.stroke-118"),sQuery(id+"F2.wireOp",EDGE,"fcba4419-a2ee-464f-be9d-58f11bf3418b.sketch_text.stroke-119"),sQuery(id+"F2.wireOp",EDGE,"fcba4419-a2ee-464f-be9d-58f11bf3418b.sketch_text.stroke-120"),sQuery(id+"F2.wireOp",EDGE,"fcba4419-a2ee-464f-be9d-58f11bf3418b.sketch_text.stroke-121"),sQuery(id+"F2.wireOp",EDGE,"fcba4419-a2ee-464f-be9d-58f11bf3418b.sketch_text.stroke-122"),sQuery(id+"F2.wireOp",EDGE,"fcba4419-a2ee-464f-be9d-58f11bf3418b.sketch_text.stroke-123"),sQuery(id+"F2.wireOp",EDGE,"fcba4419-a2ee-464f-be9d-58f11bf3418b.sketch_text.stroke-124"),sQuery(id+"F2.wireOp",EDGE,"fcba4419-a2ee-464f-be9d-58f11bf3418b.sketch_text.stroke-125"),sQuery(id+"F2.wireOp",EDGE,"fcba4419-a2ee-464f-be9d-58f11bf3418b.sketch_text.stroke-126"),sQuery(id+"F2.wireOp",EDGE,"fcba4419-a2ee-464f-be9d-58f11bf3418b.sketch_text.stroke-127"),sQuery(id+"F2.wireOp",EDGE,"fcba4419-a2ee-464f-be9d-58f11bf3418b.sketch_text.stroke-128"),sQuery(id+"F2.wireOp",EDGE,"fcba4419-a2ee-464f-be9d-58f11bf3418b.sketch_text.stroke-129"),sQuery(id+"F2.wireOp",EDGE,"fcba4419-a2ee-464f-be9d-58f11bf3418b.sketch_text.stroke-130"),sQuery(id+"F2.wireOp",EDGE,"fcba4419-a2ee-464f-be9d-58f11bf3418b.sketch_text.stroke-131"),sQuery(id+"F2.wireOp",EDGE,"fcba4419-a2ee-464f-be9d-58f11bf3418b.sketch_text.stroke-132"),sQuery(id+"F2.wireOp",EDGE,"fcba4419-a2ee-464f-be9d-58f11bf3418b.sketch_text.stroke-133"),sQuery(id+"F2.wireOp",EDGE,"fcba4419-a2ee-464f-be9d-58f11bf3418b.sketch_text.stroke-134"),sQuery(id+"F2.wireOp",EDGE,"fcba4419-a2ee-464f-be9d-58f11bf3418b.sketch_text.stroke-135"),sQuery(id+"F2.wireOp",EDGE,"fcba4419-a2ee-464f-be9d-58f11bf3418b.sketch_text.stroke-136"),sQuery(id+"F2.wireOp",EDGE,"fcba4419-a2ee-464f-be9d-58f11bf3418b.sketch_text.stroke-137"),sQuery(id+"F2.wireOp",EDGE,"fcba4419-a2ee-464f-be9d-58f11bf3418b.sketch_text.stroke-138"),sQuery(id+"F2.wireOp",EDGE,"fcba4419-a2ee-464f-be9d-58f11bf3418b.sketch_text.stroke-139"),sQuery(id+"F2.wireOp",EDGE,"fcba4419-a2ee-464f-be9d-58f11bf3418b.sketch_text.stroke-140"),sQuery(id+"F2.wireOp",EDGE,"fcba4419-a2ee-464f-be9d-58f11bf3418b.sketch_text.stroke-141"),sQuery(id+"F2.wireOp",EDGE,"fcba4419-a2ee-464f-be9d-58f11bf3418b.sketch_text.stroke-142"),sQuery(id+"F2.wireOp",EDGE,"fcba4419-a2ee-464f-be9d-58f11bf3418b.sketch_text.stroke-143"),sQuery(id+"F2.wireOp",EDGE,"fcba4419-a2ee-464f-be9d-58f11bf3418b.sketch_text.stroke-144"),sQuery(id+"F2.wireOp",EDGE,"fcba4419-a2ee-464f-be9d-58f11bf3418b.sketch_text.stroke-145"),sQuery(id+"F2.wireOp",EDGE,"fcba4419-a2ee-464f-be9d-58f11bf3418b.sketch_text.stroke-146"),sQuery(id+"F2.wireOp",EDGE,"fcba4419-a2ee-464f-be9d-58f11bf3418b.sketch_text.stroke-147"),sQuery(id+"F2.wireOp",EDGE,"fcba4419-a2ee-464f-be9d-58f11bf3418b.sketch_text.stroke-148"),sQuery(id+"F2.wireOp",EDGE,"fcba4419-a2ee-464f-be9d-58f11bf3418b.sketch_text.stroke-149"),sQuery(id+"F2.wireOp",EDGE,"fcba4419-a2ee-464f-be9d-58f11bf3418b.sketch_text.stroke-150"),sQuery(id+"F2.wireOp",EDGE,"fcba4419-a2ee-464f-be9d-58f11bf3418b.sketch_text.stroke-151"),sQuery(id+"F2.wireOp",EDGE,"fcba4419-a2ee-464f-be9d-58f11bf3418b.sketch_text.stroke-152"),sQuery(id+"F2.wireOp",EDGE,"fcba4419-a2ee-464f-be9d-58f11bf3418b.sketch_text.stroke-153"),sQuery(id+"F2.wireOp",EDGE,"fcba4419-a2ee-464f-be9d-58f11bf3418b.sketch_text.stroke-154"),sQuery(id+"F2.wireOp",EDGE,"fcba4419-a2ee-464f-be9d-58f11bf3418b.sketch_text.stroke-155"),sQuery(id+"F2.wireOp",EDGE,"fcba4419-a2ee-464f-be9d-58f11bf3418b.sketch_text.stroke-156"),sQuery(id+"F2.wireOp",EDGE,"fcba4419-a2ee-464f-be9d-58f11bf3418b.sketch_text.stroke-157"),sQuery(id+"F2.wireOp",EDGE,"fcba4419-a2ee-464f-be9d-58f11bf3418b.sketch_text.stroke-158"),sQuery(id+"F2.wireOp",EDGE,"fcba4419-a2ee-464f-be9d-58f11bf3418b.sketch_text.stroke-159"),sQuery(id+"F2.wireOp",EDGE,"fcba4419-a2ee-464f-be9d-58f11bf3418b.sketch_text.stroke-160"),sQuery(id+"F2.wireOp",EDGE,"fcba4419-a2ee-464f-be9d-58f11bf3418b.sketch_text.stroke-161"),sQuery(id+"F2.wireOp",EDGE,"fcba4419-a2ee-464f-be9d-58f11bf3418b.sketch_text.stroke-162"),sQuery(id+"F2.wireOp",EDGE,"fcba4419-a2ee-464f-be9d-58f11bf3418b.sketch_text.stroke-163"),sQuery(id+"F2.wireOp",EDGE,"fcba4419-a2ee-464f-be9d-58f11bf3418b.sketch_text.stroke-164"),sQuery(id+"F2.wireOp",EDGE,"fcba4419-a2ee-464f-be9d-58f11bf3418b.sketch_text.stroke-165"),sQuery(id+"F2.wireOp",EDGE,"fcba4419-a2ee-464f-be9d-58f11bf3418b.sketch_text.stroke-166"),sQuery(id+"F2.wireOp",EDGE,"fcba4419-a2ee-464f-be9d-58f11bf3418b.sketch_text.stroke-167"),sQuery(id+"F2.wireOp",EDGE,"fcba4419-a2ee-464f-be9d-58f11bf3418b.sketch_text.stroke-168"),sQuery(id+"F2.wireOp",EDGE,"fcba4419-a2ee-464f-be9d-58f11bf3418b.sketch_text.stroke-169"),sQuery(id+"F2.wireOp",EDGE,"fcba4419-a2ee-464f-be9d-58f11bf3418b.sketch_text.stroke-170"),sQuery(id+"F2.wireOp",EDGE,"fcba4419-a2ee-464f-be9d-58f11bf3418b.sketch_text.stroke-171"),sQuery(id+"F2.wireOp",EDGE,"fcba4419-a2ee-464f-be9d-58f11bf3418b.sketch_text.stroke-172"),sQuery(id+"F2.wireOp",EDGE,"fcba4419-a2ee-464f-be9d-58f11bf3418b.sketch_text.stroke-173"),sQuery(id+"FHMxAyK4CFUKdhS_1.wireOp",EDGE,"1cb9c079-ea9b-4899-8069-e0e3048e911d.sketch_text.stroke-0"),sQuery(id+"FHMxAyK4CFUKdhS_1.wireOp",EDGE,"1cb9c079-ea9b-4899-8069-e0e3048e911d.sketch_text.stroke-1"),sQuery(id+"FHMxAyK4CFUKdhS_1.wireOp",EDGE,"1cb9c079-ea9b-4899-8069-e0e3048e911d.sketch_text.stroke-2"),sQuery(id+"FHMxAyK4CFUKdhS_1.wireOp",EDGE,"1cb9c079-ea9b-4899-8069-e0e3048e911d.sketch_text.stroke-3"),sQuery(id+"FHMxAyK4CFUKdhS_1.wireOp",EDGE,"1cb9c079-ea9b-4899-8069-e0e3048e911d.sketch_text.stroke-4"),sQuery(id+"FHMxAyK4CFUKdhS_1.wireOp",EDGE,"1cb9c079-ea9b-4899-8069-e0e3048e911d.sketch_text.stroke-5"),sQuery(id+"FHMxAyK4CFUKdhS_1.wireOp",EDGE,"1cb9c079-ea9b-4899-8069-e0e3048e911d.sketch_text.stroke-6"),sQuery(id+"FHMxAyK4CFUKdhS_1.wireOp",EDGE,"1cb9c079-ea9b-4899-8069-e0e3048e911d.sketch_text.stroke-7"),sQuery(id+"FHMxAyK4CFUKdhS_1.wireOp",EDGE,"1cb9c079-ea9b-4899-8069-e0e3048e911d.sketch_text.stroke-8"),sQuery(id+"FHMxAyK4CFUKdhS_1.wireOp",EDGE,"1cb9c079-ea9b-4899-8069-e0e3048e911d.sketch_text.stroke-9"),sQuery(id+"FHMxAyK4CFUKdhS_1.wireOp",EDGE,"1cb9c079-ea9b-4899-8069-e0e3048e911d.sketch_text.stroke-10"),sQuery(id+"FHMxAyK4CFUKdhS_1.wireOp",EDGE,"1cb9c079-ea9b-4899-8069-e0e3048e911d.sketch_text.stroke-11"),sQuery(id+"FHMxAyK4CFUKdhS_1.wireOp",EDGE,"1cb9c079-ea9b-4899-8069-e0e3048e911d.sketch_text.stroke-12"),sQuery(id+"FHMxAyK4CFUKdhS_1.wireOp",EDGE,"1cb9c079-ea9b-4899-8069-e0e3048e911d.sketch_text.stroke-13"),sQuery(id+"FHMxAyK4CFUKdhS_1.wireOp",EDGE,"1cb9c079-ea9b-4899-8069-e0e3048e911d.sketch_text.stroke-14"),sQuery(id+"FHMxAyK4CFUKdhS_1.wireOp",EDGE,"1cb9c079-ea9b-4899-8069-e0e3048e911d.sketch_text.stroke-15"),sQuery(id+"FHMxAyK4CFUKdhS_1.wireOp",EDGE,"1cb9c079-ea9b-4899-8069-e0e3048e911d.sketch_text.stroke-16"),sQuery(id+"FHMxAyK4CFUKdhS_1.wireOp",EDGE,"1cb9c079-ea9b-4899-8069-e0e3048e911d.sketch_text.stroke-17"),sQuery(id+"FHMxAyK4CFUKdhS_1.wireOp",EDGE,"1cb9c079-ea9b-4899-8069-e0e3048e911d.sketch_text.stroke-18"),sQuery(id+"FHMxAyK4CFUKdhS_1.wireOp",EDGE,"1cb9c079-ea9b-4899-8069-e0e3048e911d.sketch_text.stroke-19"),sQuery(id+"FHMxAyK4CFUKdhS_1.wireOp",EDGE,"1cb9c079-ea9b-4899-8069-e0e3048e911d.sketch_text.stroke-20"),sQuery(id+"FHMxAyK4CFUKdhS_1.wireOp",EDGE,"1cb9c079-ea9b-4899-8069-e0e3048e911d.sketch_text.stroke-21"),sQuery(id+"FHMxAyK4CFUKdhS_1.wireOp",EDGE,"1cb9c079-ea9b-4899-8069-e0e3048e911d.sketch_text.stroke-22"),sQuery(id+"FHMxAyK4CFUKdhS_1.wireOp",EDGE,"1cb9c079-ea9b-4899-8069-e0e3048e911d.sketch_text.stroke-23"),sQuery(id+"FHMxAyK4CFUKdhS_1.wireOp",EDGE,"1cb9c079-ea9b-4899-8069-e0e3048e911d.sketch_text.stroke-24"),sQuery(id+"FHMxAyK4CFUKdhS_1.wireOp",EDGE,"1cb9c079-ea9b-4899-8069-e0e3048e911d.sketch_text.stroke-25"),sQuery(id+"FHMxAyK4CFUKdhS_1.wireOp",EDGE,"1cb9c079-ea9b-4899-8069-e0e3048e911d.sketch_text.stroke-26"),sQuery(id+"FHMxAyK4CFUKdhS_1.wireOp",EDGE,"1cb9c079-ea9b-4899-8069-e0e3048e911d.sketch_text.stroke-27"),sQuery(id+"FHMxAyK4CFUKdhS_1.wireOp",EDGE,"1cb9c079-ea9b-4899-8069-e0e3048e911d.sketch_text.stroke-28"),sQuery(id+"FHMxAyK4CFUKdhS_1.wireOp",EDGE,"1cb9c079-ea9b-4899-8069-e0e3048e911d.sketch_text.stroke-29"),sQuery(id+"FHMxAyK4CFUKdhS_1.wireOp",EDGE,"1cb9c079-ea9b-4899-8069-e0e3048e911d.sketch_text.stroke-30"),sQuery(id+"FHMxAyK4CFUKdhS_1.wireOp",EDGE,"1cb9c079-ea9b-4899-8069-e0e3048e911d.sketch_text.stroke-31"),sQuery(id+"FHMxAyK4CFUKdhS_1.wireOp",EDGE,"1cb9c079-ea9b-4899-8069-e0e3048e911d.sketch_text.stroke-32"),sQuery(id+"FHMxAyK4CFUKdhS_1.wireOp",EDGE,"1cb9c079-ea9b-4899-8069-e0e3048e911d.sketch_text.stroke-33"),sQuery(id+"FHMxAyK4CFUKdhS_1.wireOp",EDGE,"1cb9c079-ea9b-4899-8069-e0e3048e911d.sketch_text.stroke-34"),sQuery(id+"FHMxAyK4CFUKdhS_1.wireOp",EDGE,"1cb9c079-ea9b-4899-8069-e0e3048e911d.sketch_text.stroke-35"),sQuery(id+"FHMxAyK4CFUKdhS_1.wireOp",EDGE,"1cb9c079-ea9b-4899-8069-e0e3048e911d.sketch_text.stroke-36"),sQuery(id+"FHMxAyK4CFUKdhS_1.wireOp",EDGE,"1cb9c079-ea9b-4899-8069-e0e3048e911d.sketch_text.stroke-37"),sQuery(id+"FHMxAyK4CFUKdhS_1.wireOp",EDGE,"1cb9c079-ea9b-4899-8069-e0e3048e911d.sketch_text.stroke-38"),sQuery(id+"FHMxAyK4CFUKdhS_1.wireOp",EDGE,"1cb9c079-ea9b-4899-8069-e0e3048e911d.sketch_text.stroke-39"),sQuery(id+"FHMxAyK4CFUKdhS_1.wireOp",EDGE,"1cb9c079-ea9b-4899-8069-e0e3048e911d.sketch_text.stroke-40"),sQuery(id+"FHMxAyK4CFUKdhS_1.wireOp",EDGE,"1cb9c079-ea9b-4899-8069-e0e3048e911d.sketch_text.stroke-41"),sQuery(id+"FHMxAyK4CFUKdhS_1.wireOp",EDGE,"1cb9c079-ea9b-4899-8069-e0e3048e911d.sketch_text.stroke-42"),sQuery(id+"FHMxAyK4CFUKdhS_1.wireOp",EDGE,"1cb9c079-ea9b-4899-8069-e0e3048e911d.sketch_text.stroke-43"),sQuery(id+"FHMxAyK4CFUKdhS_1.wireOp",EDGE,"1cb9c079-ea9b-4899-8069-e0e3048e911d.sketch_text.stroke-44"),sQuery(id+"FHMxAyK4CFUKdhS_1.wireOp",EDGE,"1cb9c079-ea9b-4899-8069-e0e3048e911d.sketch_text.stroke-45"),sQuery(id+"FHMxAyK4CFUKdhS_1.wireOp",EDGE,"1cb9c079-ea9b-4899-8069-e0e3048e911d.sketch_text.stroke-46"),sQuery(id+"FHMxAyK4CFUKdhS_1.wireOp",EDGE,"1cb9c079-ea9b-4899-8069-e0e3048e911d.sketch_text.stroke-47"),sQuery(id+"FHMxAyK4CFUKdhS_1.wireOp",EDGE,"1cb9c079-ea9b-4899-8069-e0e3048e911d.sketch_text.stroke-48"),sQuery(id+"FHMxAyK4CFUKdhS_1.wireOp",EDGE,"1cb9c079-ea9b-4899-8069-e0e3048e911d.sketch_text.stroke-49"),sQuery(id+"FHMxAyK4CFUKdhS_1.wireOp",EDGE,"1cb9c079-ea9b-4899-8069-e0e3048e911d.sketch_text.stroke-50"),sQuery(id+"FHMxAyK4CFUKdhS_1.wireOp",EDGE,"1cb9c079-ea9b-4899-8069-e0e3048e911d.sketch_text.stroke-51"),sQuery(id+"FHMxAyK4CFUKdhS_1.wireOp",EDGE,"1cb9c079-ea9b-4899-8069-e0e3048e911d.sketch_text.stroke-52"),sQuery(id+"FHMxAyK4CFUKdhS_1.wireOp",EDGE,"1cb9c079-ea9b-4899-8069-e0e3048e911d.sketch_text.stroke-53"),sQuery(id+"FHMxAyK4CFUKdhS_1.wireOp",EDGE,"1cb9c079-ea9b-4899-8069-e0e3048e911d.sketch_text.stroke-54"),sQuery(id+"FHMxAyK4CFUKdhS_1.wireOp",EDGE,"1cb9c079-ea9b-4899-8069-e0e3048e911d.sketch_text.stroke-55"),sQuery(id+"FHMxAyK4CFUKdhS_1.wireOp",EDGE,"1cb9c079-ea9b-4899-8069-e0e3048e911d.sketch_text.stroke-56"),sQuery(id+"FHMxAyK4CFUKdhS_1.wireOp",EDGE,"1cb9c079-ea9b-4899-8069-e0e3048e911d.sketch_text.stroke-57"),sQuery(id+"FHMxAyK4CFUKdhS_1.wireOp",EDGE,"1cb9c079-ea9b-4899-8069-e0e3048e911d.sketch_text.stroke-58"),sQuery(id+"FHMxAyK4CFUKdhS_1.wireOp",EDGE,"1cb9c079-ea9b-4899-8069-e0e3048e911d.sketch_text.stroke-59"),sQuery(id+"FHMxAyK4CFUKdhS_1.wireOp",EDGE,"1cb9c079-ea9b-4899-8069-e0e3048e911d.sketch_text.stroke-60"),sQuery(id+"FHMxAyK4CFUKdhS_1.wireOp",EDGE,"1cb9c079-ea9b-4899-8069-e0e3048e911d.sketch_text.stroke-61"),sQuery(id+"FHMxAyK4CFUKdhS_1.wireOp",EDGE,"1cb9c079-ea9b-4899-8069-e0e3048e911d.sketch_text.stroke-62"),sQuery(id+"FHMxAyK4CFUKdhS_1.wireOp",EDGE,"1cb9c079-ea9b-4899-8069-e0e3048e911d.sketch_text.stroke-71"),sQuery(id+"FHMxAyK4CFUKdhS_1.wireOp",EDGE,"1cb9c079-ea9b-4899-8069-e0e3048e911d.sketch_text.stroke-72"),sQuery(id+"FHMxAyK4CFUKdhS_1.wireOp",EDGE,"1cb9c079-ea9b-4899-8069-e0e3048e911d.sketch_text.stroke-73"),sQuery(id+"FHMxAyK4CFUKdhS_1.wireOp",EDGE,"1cb9c079-ea9b-4899-8069-e0e3048e911d.sketch_text.stroke-74"),sQuery(id+"FHMxAyK4CFUKdhS_1.wireOp",EDGE,"1cb9c079-ea9b-4899-8069-e0e3048e911d.sketch_text.stroke-75"),sQuery(id+"FHMxAyK4CFUKdhS_1.wireOp",EDGE,"1cb9c079-ea9b-4899-8069-e0e3048e911d.sketch_text.stroke-76"),sQuery(id+"FHMxAyK4CFUKdhS_1.wireOp",EDGE,"1cb9c079-ea9b-4899-8069-e0e3048e911d.sketch_text.stroke-77"),sQuery(id+"FHMxAyK4CFUKdhS_1.wireOp",EDGE,"1cb9c079-ea9b-4899-8069-e0e3048e911d.sketch_text.stroke-78"),sQuery(id+"FHMxAyK4CFUKdhS_1.wireOp",EDGE,"1cb9c079-ea9b-4899-8069-e0e3048e911d.sketch_text.stroke-79"),sQuery(id+"FHMxAyK4CFUKdhS_1.wireOp",EDGE,"1cb9c079-ea9b-4899-8069-e0e3048e911d.sketch_text.stroke-80"),sQuery(id+"FHMxAyK4CFUKdhS_1.wireOp",EDGE,"1cb9c079-ea9b-4899-8069-e0e3048e911d.sketch_text.stroke-81"),sQuery(id+"FHMxAyK4CFUKdhS_1.wireOp",EDGE,"1cb9c079-ea9b-4899-8069-e0e3048e911d.sketch_text.stroke-82"),sQuery(id+"FHMxAyK4CFUKdhS_1.wireOp",EDGE,"1cb9c079-ea9b-4899-8069-e0e3048e911d.sketch_text.stroke-83"),sQuery(id+"FHMxAyK4CFUKdhS_1.wireOp",EDGE,"1cb9c079-ea9b-4899-8069-e0e3048e911d.sketch_text.stroke-84"),sQuery(id+"FHMxAyK4CFUKdhS_1.wireOp",EDGE,"1cb9c079-ea9b-4899-8069-e0e3048e911d.sketch_text.stroke-85"),sQuery(id+"FHMxAyK4CFUKdhS_1.wireOp",EDGE,"1cb9c079-ea9b-4899-8069-e0e3048e911d.sketch_text.stroke-86"),sQuery(id+"FHMxAyK4CFUKdhS_1.wireOp",EDGE,"1cb9c079-ea9b-4899-8069-e0e3048e911d.sketch_text.stroke-87"),sQuery(id+"FHMxAyK4CFUKdhS_1.wireOp",EDGE,"1cb9c079-ea9b-4899-8069-e0e3048e911d.sketch_text.stroke-88"),sQuery(id+"FHMxAyK4CFUKdhS_1.wireOp",EDGE,"1cb9c079-ea9b-4899-8069-e0e3048e911d.sketch_text.stroke-89"),sQuery(id+"FHMxAyK4CFUKdhS_1.wireOp",EDGE,"1cb9c079-ea9b-4899-8069-e0e3048e911d.sketch_text.stroke-90"),sQuery(id+"FHMxAyK4CFUKdhS_1.wireOp",EDGE,"1cb9c079-ea9b-4899-8069-e0e3048e911d.sketch_text.stroke-91"),sQuery(id+"FHMxAyK4CFUKdhS_1.wireOp",EDGE,"1cb9c079-ea9b-4899-8069-e0e3048e911d.sketch_text.stroke-92"),sQuery(id+"FHMxAyK4CFUKdhS_1.wireOp",EDGE,"1cb9c079-ea9b-4899-8069-e0e3048e911d.sketch_text.stroke-93"),sQuery(id+"FHMxAyK4CFUKdhS_1.wireOp",EDGE,"1cb9c079-ea9b-4899-8069-e0e3048e911d.sketch_text.stroke-94"),sQuery(id+"FHMxAyK4CFUKdhS_1.wireOp",EDGE,"1cb9c079-ea9b-4899-8069-e0e3048e911d.sketch_text.stroke-95"),sQuery(id+"FHMxAyK4CFUKdhS_1.wireOp",EDGE,"1cb9c079-ea9b-4899-8069-e0e3048e911d.sketch_text.stroke-96"),sQuery(id+"FHMxAyK4CFUKdhS_1.wireOp",EDGE,"1cb9c079-ea9b-4899-8069-e0e3048e911d.sketch_text.stroke-97"),sQuery(id+"FHMxAyK4CFUKdhS_1.wireOp",EDGE,"1cb9c079-ea9b-4899-8069-e0e3048e911d.sketch_text.stroke-103"),sQuery(id+"FHMxAyK4CFUKdhS_1.wireOp",EDGE,"1cb9c079-ea9b-4899-8069-e0e3048e911d.sketch_text.stroke-104"),sQuery(id+"FHMxAyK4CFUKdhS_1.wireOp",EDGE,"1cb9c079-ea9b-4899-8069-e0e3048e911d.sketch_text.stroke-105"),sQuery(id+"FHMxAyK4CFUKdhS_1.wireOp",EDGE,"1cb9c079-ea9b-4899-8069-e0e3048e911d.sketch_text.stroke-106"),sQuery(id+"FHMxAyK4CFUKdhS_1.wireOp",EDGE,"1cb9c079-ea9b-4899-8069-e0e3048e911d.sketch_text.stroke-107"),sQuery(id+"FHMxAyK4CFUKdhS_1.wireOp",EDGE,"1cb9c079-ea9b-4899-8069-e0e3048e911d.sketch_text.stroke-108"),sQuery(id+"FHMxAyK4CFUKdhS_1.wireOp",EDGE,"1cb9c079-ea9b-4899-8069-e0e3048e911d.sketch_text.stroke-109"),sQuery(id+"FHMxAyK4CFUKdhS_1.wireOp",EDGE,"1cb9c079-ea9b-4899-8069-e0e3048e911d.sketch_text.stroke-110"),sQuery(id+"FHMxAyK4CFUKdhS_1.wireOp",EDGE,"1cb9c079-ea9b-4899-8069-e0e3048e911d.sketch_text.stroke-111"),sQuery(id+"FHMxAyK4CFUKdhS_1.wireOp",EDGE,"1cb9c079-ea9b-4899-8069-e0e3048e911d.sketch_text.stroke-112"),sQuery(id+"FHMxAyK4CFUKdhS_1.wireOp",EDGE,"1cb9c079-ea9b-4899-8069-e0e3048e911d.sketch_text.stroke-113"),sQuery(id+"FHMxAyK4CFUKdhS_1.wireOp",EDGE,"1cb9c079-ea9b-4899-8069-e0e3048e911d.sketch_text.stroke-114"),sQuery(id+"FHMxAyK4CFUKdhS_1.wireOp",EDGE,"1cb9c079-ea9b-4899-8069-e0e3048e911d.sketch_text.stroke-115"),sQuery(id+"FHMxAyK4CFUKdhS_1.wireOp",EDGE,"1cb9c079-ea9b-4899-8069-e0e3048e911d.sketch_text.stroke-116"),sQuery(id+"FHMxAyK4CFUKdhS_1.wireOp",EDGE,"1cb9c079-ea9b-4899-8069-e0e3048e911d.sketch_text.stroke-117"),sQuery(id+"FHMxAyK4CFUKdhS_1.wireOp",EDGE,"1cb9c079-ea9b-4899-8069-e0e3048e911d.sketch_text.stroke-118"),sQuery(id+"FHMxAyK4CFUKdhS_1.wireOp",EDGE,"1cb9c079-ea9b-4899-8069-e0e3048e911d.sketch_text.stroke-119"),sQuery(id+"FHMxAyK4CFUKdhS_1.wireOp",EDGE,"1cb9c079-ea9b-4899-8069-e0e3048e911d.sketch_text.stroke-120"),sQuery(id+"FHMxAyK4CFUKdhS_1.wireOp",EDGE,"1cb9c079-ea9b-4899-8069-e0e3048e911d.sketch_text.stroke-121"),sQuery(id+"FHMxAyK4CFUKdhS_1.wireOp",EDGE,"1cb9c079-ea9b-4899-8069-e0e3048e911d.sketch_text.stroke-122"),sQuery(id+"FHMxAyK4CFUKdhS_1.wireOp",EDGE,"1cb9c079-ea9b-4899-8069-e0e3048e911d.sketch_text.stroke-123"),sQuery(id+"FHMxAyK4CFUKdhS_1.wireOp",EDGE,"1cb9c079-ea9b-4899-8069-e0e3048e911d.sketch_text.stroke-124"),sQuery(id+"FHMxAyK4CFUKdhS_1.wireOp",EDGE,"1cb9c079-ea9b-4899-8069-e0e3048e911d.sketch_text.stroke-125"),sQuery(id+"FHMxAyK4CFUKdhS_1.wireOp",EDGE,"1cb9c079-ea9b-4899-8069-e0e3048e911d.sketch_text.stroke-126"),sQuery(id+"FHMxAyK4CFUKdhS_1.wireOp",EDGE,"1cb9c079-ea9b-4899-8069-e0e3048e911d.sketch_text.stroke-127"),sQuery(id+"FHMxAyK4CFUKdhS_1.wireOp",EDGE,"1cb9c079-ea9b-4899-8069-e0e3048e911d.sketch_text.stroke-128"),sQuery(id+"FHMxAyK4CFUKdhS_1.wireOp",EDGE,"1cb9c079-ea9b-4899-8069-e0e3048e911d.sketch_text.stroke-129"),sQuery(id+"FHMxAyK4CFUKdhS_1.wireOp",EDGE,"1cb9c079-ea9b-4899-8069-e0e3048e911d.sketch_text.stroke-130"),sQuery(id+"FHMxAyK4CFUKdhS_1.wireOp",EDGE,"1cb9c079-ea9b-4899-8069-e0e3048e911d.sketch_text.stroke-131"),sQuery(id+"FHMxAyK4CFUKdhS_1.wireOp",EDGE,"1cb9c079-ea9b-4899-8069-e0e3048e911d.sketch_text.stroke-132"),sQuery(id+"FHMxAyK4CFUKdhS_1.wireOp",EDGE,"1cb9c079-ea9b-4899-8069-e0e3048e911d.sketch_text.stroke-133"),sQuery(id+"FHMxAyK4CFUKdhS_1.wireOp",EDGE,"1cb9c079-ea9b-4899-8069-e0e3048e911d.sketch_text.stroke-134"),sQuery(id+"FHMxAyK4CFUKdhS_1.wireOp",EDGE,"1cb9c079-ea9b-4899-8069-e0e3048e911d.sketch_text.stroke-135"),sQuery(id+"FHMxAyK4CFUKdhS_1.wireOp",EDGE,"1cb9c079-ea9b-4899-8069-e0e3048e911d.sketch_text.stroke-136"),sQuery(id+"FHMxAyK4CFUKdhS_1.wireOp",EDGE,"1cb9c079-ea9b-4899-8069-e0e3048e911d.sketch_text.stroke-137"),sQuery(id+"FHMxAyK4CFUKdhS_1.wireOp",EDGE,"1cb9c079-ea9b-4899-8069-e0e3048e911d.sketch_text.stroke-138"),sQuery(id+"FHMxAyK4CFUKdhS_1.wireOp",EDGE,"1cb9c079-ea9b-4899-8069-e0e3048e911d.sketch_text.stroke-139"),sQuery(id+"FHMxAyK4CFUKdhS_1.wireOp",EDGE,"1cb9c079-ea9b-4899-8069-e0e3048e911d.sketch_text.stroke-140"),sQuery(id+"FHMxAyK4CFUKdhS_1.wireOp",EDGE,"1cb9c079-ea9b-4899-8069-e0e3048e911d.sketch_text.stroke-141"),sQuery(id+"FHMxAyK4CFUKdhS_1.wireOp",EDGE,"1cb9c079-ea9b-4899-8069-e0e3048e911d.sketch_text.stroke-142"),sQuery(id+"FHMxAyK4CFUKdhS_1.wireOp",EDGE,"1cb9c079-ea9b-4899-8069-e0e3048e911d.sketch_text.stroke-143"),sQuery(id+"FHMxAyK4CFUKdhS_1.wireOp",EDGE,"1cb9c079-ea9b-4899-8069-e0e3048e911d.sketch_text.stroke-144"),sQuery(id+"FHMxAyK4CFUKdhS_1.wireOp",EDGE,"1cb9c079-ea9b-4899-8069-e0e3048e911d.sketch_text.stroke-145"),sQuery(id+"FHMxAyK4CFUKdhS_1.wireOp",EDGE,"1cb9c079-ea9b-4899-8069-e0e3048e911d.sketch_text.stroke-146"),sQuery(id+"FHMxAyK4CFUKdhS_1.wireOp",EDGE,"1cb9c079-ea9b-4899-8069-e0e3048e911d.sketch_text.stroke-147"),sQuery(id+"FHMxAyK4CFUKdhS_1.wireOp",EDGE,"1cb9c079-ea9b-4899-8069-e0e3048e911d.sketch_text.stroke-148"),sQuery(id+"FHMxAyK4CFUKdhS_1.wireOp",EDGE,"1cb9c079-ea9b-4899-8069-e0e3048e911d.sketch_text.stroke-149"),sQuery(id+"FHMxAyK4CFUKdhS_1.wireOp",EDGE,"1cb9c079-ea9b-4899-8069-e0e3048e911d.sketch_text.stroke-150"),sQuery(id+"FHMxAyK4CFUKdhS_1.wireOp",EDGE,"1cb9c079-ea9b-4899-8069-e0e3048e911d.sketch_text.stroke-151"),sQuery(id+"FHMxAyK4CFUKdhS_1.wireOp",EDGE,"1cb9c079-ea9b-4899-8069-e0e3048e911d.sketch_text.stroke-152"),sQuery(id+"FHMxAyK4CFUKdhS_1.wireOp",EDGE,"1cb9c079-ea9b-4899-8069-e0e3048e911d.sketch_text.stroke-153"),sQuery(id+"FHMxAyK4CFUKdhS_1.wireOp",EDGE,"1cb9c079-ea9b-4899-8069-e0e3048e911d.sketch_text.stroke-159"),sQuery(id+"FHMxAyK4CFUKdhS_1.wireOp",EDGE,"1cb9c079-ea9b-4899-8069-e0e3048e911d.sketch_text.stroke-160"),sQuery(id+"FHMxAyK4CFUKdhS_1.wireOp",EDGE,"1cb9c079-ea9b-4899-8069-e0e3048e911d.sketch_text.stroke-161"),sQuery(id+"FHMxAyK4CFUKdhS_1.wireOp",EDGE,"1cb9c079-ea9b-4899-8069-e0e3048e911d.sketch_text.stroke-162"),sQuery(id+"FHMxAyK4CFUKdhS_1.wireOp",EDGE,"1cb9c079-ea9b-4899-8069-e0e3048e911d.sketch_text.stroke-163"),sQuery(id+"FHMxAyK4CFUKdhS_1.wireOp",EDGE,"1cb9c079-ea9b-4899-8069-e0e3048e911d.sketch_text.stroke-164"),sQuery(id+"FHMxAyK4CFUKdhS_1.wireOp",EDGE,"1cb9c079-ea9b-4899-8069-e0e3048e911d.sketch_text.stroke-165"),sQuery(id+"FHMxAyK4CFUKdhS_1.wireOp",EDGE,"1cb9c079-ea9b-4899-8069-e0e3048e911d.sketch_text.stroke-166"),sQuery(id+"FHMxAyK4CFUKdhS_1.wireOp",EDGE,"1cb9c079-ea9b-4899-8069-e0e3048e911d.sketch_text.stroke-167"),sQuery(id+"FHMxAyK4CFUKdhS_1.wireOp",EDGE,"1cb9c079-ea9b-4899-8069-e0e3048e911d.sketch_text.stroke-168"),sQuery(id+"FHMxAyK4CFUKdhS_1.wireOp",EDGE,"1cb9c079-ea9b-4899-8069-e0e3048e911d.sketch_text.stroke-169"),sQuery(id+"FHMxAyK4CFUKdhS_1.wireOp",EDGE,"1cb9c079-ea9b-4899-8069-e0e3048e911d.sketch_text.stroke-170"),sQuery(id+"FHMxAyK4CFUKdhS_1.wireOp",EDGE,"1cb9c079-ea9b-4899-8069-e0e3048e911d.sketch_text.stroke-171"),sQuery(id+"FHMxAyK4CFUKdhS_1.wireOp",EDGE,"1cb9c079-ea9b-4899-8069-e0e3048e911d.sketch_text.stroke-172"),sQuery(id+"FHMxAyK4CFUKdhS_1.wireOp",EDGE,"1cb9c079-ea9b-4899-8069-e0e3048e911d.sketch_text.stroke-173"),sQuery(id+"FHMxAyK4CFUKdhS_1.wireOp",EDGE,"1cb9c079-ea9b-4899-8069-e0e3048e911d.sketch_text.stroke-174"),sQuery(id+"FHMxAyK4CFUKdhS_1.wireOp",EDGE,"1cb9c079-ea9b-4899-8069-e0e3048e911d.sketch_text.stroke-175"),sQuery(id+"FHMxAyK4CFUKdhS_1.wireOp",EDGE,"1cb9c079-ea9b-4899-8069-e0e3048e911d.sketch_text.stroke-176"),sQuery(id+"FHMxAyK4CFUKdhS_1.wireOp",EDGE,"1cb9c079-ea9b-4899-8069-e0e3048e911d.sketch_text.stroke-177"),sQuery(id+"FHMxAyK4CFUKdhS_1.wireOp",EDGE,"1cb9c079-ea9b-4899-8069-e0e3048e911d.sketch_text.stroke-178"),sQuery(id+"FHMxAyK4CFUKdhS_1.wireOp",EDGE,"1cb9c079-ea9b-4899-8069-e0e3048e911d.sketch_text.stroke-179"),sQuery(id+"FHMxAyK4CFUKdhS_1.wireOp",EDGE,"1cb9c079-ea9b-4899-8069-e0e3048e911d.sketch_text.stroke-180"),subQ2,sQuery(id+"F3.wireOp",EDGE,"6ee83ff3-586e-4dbe-aaea-af71240543bd")])],"isStart":true})]),OD(0.0)],"derivedFrom":makeQuery(id+"F1.opExtrude","CAP_EDGE",EDGE,{"disambiguationData":[OSD([subQ0])],"isStart":false})});}
            var Q6;
            {var subQ0=sQuery(id+"F3.wireOp",EDGE,"6ee83ff3-586e-4dbe-aaea-af71240543bd");var subQ1=sQuery(id+"F0.wireOp",EDGE,"E0.bottom");var subQ2=sQuery(id+"F0.wireOp",EDGE,"E0.right");Q6=makeQuery(id+"F4.boolean.opBoolean","SPLIT",EDGE,{"disambiguationData":[TD([makeQuery(id+"F1.opExtrude","SWEPT_FACE",FACE,{"disambiguationData":[OSD([subQ1])]}),makeQuery(id+"F1.opExtrude","CAP_FACE",FACE,{"disambiguationData":[OSD([subQ1,sQuery(id+"F0.wireOp",EDGE,"E0.top"),sQuery(id+"F0.wireOp",EDGE,"E0.left"),subQ2])],"isStart":false}),makeQuery(id+"F1.opExtrude","SWEPT_FACE",FACE,{"disambiguationData":[OSD([subQ2])]}),makeQuery(id+"F4.opExtrude","CAP_FACE",FACE,{"disambiguationData":[OSD([subQ1,sQuery(id+"F2.wireOp",EDGE,"fcba4419-a2ee-464f-be9d-58f11bf3418b.sketch_text.stroke-0"),sQuery(id+"F2.wireOp",EDGE,"fcba4419-a2ee-464f-be9d-58f11bf3418b.sketch_text.stroke-1"),sQuery(id+"F2.wireOp",EDGE,"fcba4419-a2ee-464f-be9d-58f11bf3418b.sketch_text.stroke-2"),sQuery(id+"F2.wireOp",EDGE,"fcba4419-a2ee-464f-be9d-58f11bf3418b.sketch_text.stroke-3"),sQuery(id+"F2.wireOp",EDGE,"fcba4419-a2ee-464f-be9d-58f11bf3418b.sketch_text.stroke-4"),sQuery(id+"F2.wireOp",EDGE,"fcba4419-a2ee-464f-be9d-58f11bf3418b.sketch_text.stroke-5"),sQuery(id+"F2.wireOp",EDGE,"fcba4419-a2ee-464f-be9d-58f11bf3418b.sketch_text.stroke-6"),sQuery(id+"F2.wireOp",EDGE,"fcba4419-a2ee-464f-be9d-58f11bf3418b.sketch_text.stroke-7"),sQuery(id+"F2.wireOp",EDGE,"fcba4419-a2ee-464f-be9d-58f11bf3418b.sketch_text.stroke-8"),sQuery(id+"F2.wireOp",EDGE,"fcba4419-a2ee-464f-be9d-58f11bf3418b.sketch_text.stroke-9"),sQuery(id+"F2.wireOp",EDGE,"fcba4419-a2ee-464f-be9d-58f11bf3418b.sketch_text.stroke-10"),sQuery(id+"F2.wireOp",EDGE,"fcba4419-a2ee-464f-be9d-58f11bf3418b.sketch_text.stroke-11"),sQuery(id+"F2.wireOp",EDGE,"fcba4419-a2ee-464f-be9d-58f11bf3418b.sketch_text.stroke-12"),sQuery(id+"F2.wireOp",EDGE,"fcba4419-a2ee-464f-be9d-58f11bf3418b.sketch_text.stroke-13"),sQuery(id+"F2.wireOp",EDGE,"fcba4419-a2ee-464f-be9d-58f11bf3418b.sketch_text.stroke-14"),sQuery(id+"F2.wireOp",EDGE,"fcba4419-a2ee-464f-be9d-58f11bf3418b.sketch_text.stroke-15"),sQuery(id+"F2.wireOp",EDGE,"fcba4419-a2ee-464f-be9d-58f11bf3418b.sketch_text.stroke-16"),sQuery(id+"F2.wireOp",EDGE,"fcba4419-a2ee-464f-be9d-58f11bf3418b.sketch_text.stroke-17"),sQuery(id+"F2.wireOp",EDGE,"fcba4419-a2ee-464f-be9d-58f11bf3418b.sketch_text.stroke-18"),sQuery(id+"F2.wireOp",EDGE,"fcba4419-a2ee-464f-be9d-58f11bf3418b.sketch_text.stroke-19"),sQuery(id+"F2.wireOp",EDGE,"fcba4419-a2ee-464f-be9d-58f11bf3418b.sketch_text.stroke-20"),sQuery(id+"F2.wireOp",EDGE,"fcba4419-a2ee-464f-be9d-58f11bf3418b.sketch_text.stroke-21"),sQuery(id+"F2.wireOp",EDGE,"fcba4419-a2ee-464f-be9d-58f11bf3418b.sketch_text.stroke-22"),sQuery(id+"F2.wireOp",EDGE,"fcba4419-a2ee-464f-be9d-58f11bf3418b.sketch_text.stroke-23"),sQuery(id+"F2.wireOp",EDGE,"fcba4419-a2ee-464f-be9d-58f11bf3418b.sketch_text.stroke-24"),sQuery(id+"F2.wireOp",EDGE,"fcba4419-a2ee-464f-be9d-58f11bf3418b.sketch_text.stroke-25"),sQuery(id+"F2.wireOp",EDGE,"fcba4419-a2ee-464f-be9d-58f11bf3418b.sketch_text.stroke-26"),sQuery(id+"F2.wireOp",EDGE,"fcba4419-a2ee-464f-be9d-58f11bf3418b.sketch_text.stroke-27"),sQuery(id+"F2.wireOp",EDGE,"fcba4419-a2ee-464f-be9d-58f11bf3418b.sketch_text.stroke-28"),sQuery(id+"F2.wireOp",EDGE,"fcba4419-a2ee-464f-be9d-58f11bf3418b.sketch_text.stroke-29"),sQuery(id+"F2.wireOp",EDGE,"fcba4419-a2ee-464f-be9d-58f11bf3418b.sketch_text.stroke-30"),sQuery(id+"F2.wireOp",EDGE,"fcba4419-a2ee-464f-be9d-58f11bf3418b.sketch_text.stroke-31"),sQuery(id+"F2.wireOp",EDGE,"fcba4419-a2ee-464f-be9d-58f11bf3418b.sketch_text.stroke-32"),sQuery(id+"F2.wireOp",EDGE,"fcba4419-a2ee-464f-be9d-58f11bf3418b.sketch_text.stroke-33"),sQuery(id+"F2.wireOp",EDGE,"fcba4419-a2ee-464f-be9d-58f11bf3418b.sketch_text.stroke-34"),sQuery(id+"F2.wireOp",EDGE,"fcba4419-a2ee-464f-be9d-58f11bf3418b.sketch_text.stroke-35"),sQuery(id+"F2.wireOp",EDGE,"fcba4419-a2ee-464f-be9d-58f11bf3418b.sketch_text.stroke-36"),sQuery(id+"F2.wireOp",EDGE,"fcba4419-a2ee-464f-be9d-58f11bf3418b.sketch_text.stroke-37"),sQuery(id+"F2.wireOp",EDGE,"fcba4419-a2ee-464f-be9d-58f11bf3418b.sketch_text.stroke-38"),sQuery(id+"F2.wireOp",EDGE,"fcba4419-a2ee-464f-be9d-58f11bf3418b.sketch_text.stroke-39"),sQuery(id+"F2.wireOp",EDGE,"fcba4419-a2ee-464f-be9d-58f11bf3418b.sketch_text.stroke-40"),sQuery(id+"F2.wireOp",EDGE,"fcba4419-a2ee-464f-be9d-58f11bf3418b.sketch_text.stroke-41"),sQuery(id+"F2.wireOp",EDGE,"fcba4419-a2ee-464f-be9d-58f11bf3418b.sketch_text.stroke-42"),sQuery(id+"F2.wireOp",EDGE,"fcba4419-a2ee-464f-be9d-58f11bf3418b.sketch_text.stroke-43"),sQuery(id+"F2.wireOp",EDGE,"fcba4419-a2ee-464f-be9d-58f11bf3418b.sketch_text.stroke-44"),sQuery(id+"F2.wireOp",EDGE,"fcba4419-a2ee-464f-be9d-58f11bf3418b.sketch_text.stroke-45"),sQuery(id+"F2.wireOp",EDGE,"fcba4419-a2ee-464f-be9d-58f11bf3418b.sketch_text.stroke-46"),sQuery(id+"F2.wireOp",EDGE,"fcba4419-a2ee-464f-be9d-58f11bf3418b.sketch_text.stroke-47"),sQuery(id+"F2.wireOp",EDGE,"fcba4419-a2ee-464f-be9d-58f11bf3418b.sketch_text.stroke-48"),sQuery(id+"F2.wireOp",EDGE,"fcba4419-a2ee-464f-be9d-58f11bf3418b.sketch_text.stroke-49"),sQuery(id+"F2.wireOp",EDGE,"fcba4419-a2ee-464f-be9d-58f11bf3418b.sketch_text.stroke-50"),sQuery(id+"F2.wireOp",EDGE,"fcba4419-a2ee-464f-be9d-58f11bf3418b.sketch_text.stroke-51"),sQuery(id+"F2.wireOp",EDGE,"fcba4419-a2ee-464f-be9d-58f11bf3418b.sketch_text.stroke-52"),sQuery(id+"F2.wireOp",EDGE,"fcba4419-a2ee-464f-be9d-58f11bf3418b.sketch_text.stroke-53"),sQuery(id+"F2.wireOp",EDGE,"fcba4419-a2ee-464f-be9d-58f11bf3418b.sketch_text.stroke-54"),sQuery(id+"F2.wireOp",EDGE,"fcba4419-a2ee-464f-be9d-58f11bf3418b.sketch_text.stroke-55"),sQuery(id+"F2.wireOp",EDGE,"fcba4419-a2ee-464f-be9d-58f11bf3418b.sketch_text.stroke-56"),sQuery(id+"F2.wireOp",EDGE,"fcba4419-a2ee-464f-be9d-58f11bf3418b.sketch_text.stroke-57"),sQuery(id+"F2.wireOp",EDGE,"fcba4419-a2ee-464f-be9d-58f11bf3418b.sketch_text.stroke-58"),sQuery(id+"F2.wireOp",EDGE,"fcba4419-a2ee-464f-be9d-58f11bf3418b.sketch_text.stroke-59"),sQuery(id+"F2.wireOp",EDGE,"fcba4419-a2ee-464f-be9d-58f11bf3418b.sketch_text.stroke-60"),sQuery(id+"F2.wireOp",EDGE,"fcba4419-a2ee-464f-be9d-58f11bf3418b.sketch_text.stroke-61"),sQuery(id+"F2.wireOp",EDGE,"fcba4419-a2ee-464f-be9d-58f11bf3418b.sketch_text.stroke-62"),sQuery(id+"F2.wireOp",EDGE,"fcba4419-a2ee-464f-be9d-58f11bf3418b.sketch_text.stroke-63"),sQuery(id+"F2.wireOp",EDGE,"fcba4419-a2ee-464f-be9d-58f11bf3418b.sketch_text.stroke-64"),sQuery(id+"F2.wireOp",EDGE,"fcba4419-a2ee-464f-be9d-58f11bf3418b.sketch_text.stroke-65"),sQuery(id+"F2.wireOp",EDGE,"fcba4419-a2ee-464f-be9d-58f11bf3418b.sketch_text.stroke-66"),sQuery(id+"F2.wireOp",EDGE,"fcba4419-a2ee-464f-be9d-58f11bf3418b.sketch_text.stroke-67"),sQuery(id+"F2.wireOp",EDGE,"fcba4419-a2ee-464f-be9d-58f11bf3418b.sketch_text.stroke-68"),sQuery(id+"F2.wireOp",EDGE,"fcba4419-a2ee-464f-be9d-58f11bf3418b.sketch_text.stroke-69"),sQuery(id+"F2.wireOp",EDGE,"fcba4419-a2ee-464f-be9d-58f11bf3418b.sketch_text.stroke-70"),sQuery(id+"F2.wireOp",EDGE,"fcba4419-a2ee-464f-be9d-58f11bf3418b.sketch_text.stroke-71"),sQuery(id+"F2.wireOp",EDGE,"fcba4419-a2ee-464f-be9d-58f11bf3418b.sketch_text.stroke-72"),sQuery(id+"F2.wireOp",EDGE,"fcba4419-a2ee-464f-be9d-58f11bf3418b.sketch_text.stroke-73"),sQuery(id+"F2.wireOp",EDGE,"fcba4419-a2ee-464f-be9d-58f11bf3418b.sketch_text.stroke-74"),sQuery(id+"F2.wireOp",EDGE,"fcba4419-a2ee-464f-be9d-58f11bf3418b.sketch_text.stroke-75"),sQuery(id+"F2.wireOp",EDGE,"fcba4419-a2ee-464f-be9d-58f11bf3418b.sketch_text.stroke-76"),sQuery(id+"F2.wireOp",EDGE,"fcba4419-a2ee-464f-be9d-58f11bf3418b.sketch_text.stroke-77"),sQuery(id+"F2.wireOp",EDGE,"fcba4419-a2ee-464f-be9d-58f11bf3418b.sketch_text.stroke-78"),sQuery(id+"F2.wireOp",EDGE,"fcba4419-a2ee-464f-be9d-58f11bf3418b.sketch_text.stroke-79"),sQuery(id+"F2.wireOp",EDGE,"fcba4419-a2ee-464f-be9d-58f11bf3418b.sketch_text.stroke-80"),sQuery(id+"F2.wireOp",EDGE,"fcba4419-a2ee-464f-be9d-58f11bf3418b.sketch_text.stroke-81"),sQuery(id+"F2.wireOp",EDGE,"fcba4419-a2ee-464f-be9d-58f11bf3418b.sketch_text.stroke-82"),sQuery(id+"F2.wireOp",EDGE,"fcba4419-a2ee-464f-be9d-58f11bf3418b.sketch_text.stroke-83"),sQuery(id+"F2.wireOp",EDGE,"fcba4419-a2ee-464f-be9d-58f11bf3418b.sketch_text.stroke-84"),sQuery(id+"F2.wireOp",EDGE,"fcba4419-a2ee-464f-be9d-58f11bf3418b.sketch_text.stroke-85"),sQuery(id+"F2.wireOp",EDGE,"fcba4419-a2ee-464f-be9d-58f11bf3418b.sketch_text.stroke-86"),sQuery(id+"F2.wireOp",EDGE,"fcba4419-a2ee-464f-be9d-58f11bf3418b.sketch_text.stroke-87"),sQuery(id+"F2.wireOp",EDGE,"fcba4419-a2ee-464f-be9d-58f11bf3418b.sketch_text.stroke-88"),sQuery(id+"F2.wireOp",EDGE,"fcba4419-a2ee-464f-be9d-58f11bf3418b.sketch_text.stroke-89"),sQuery(id+"F2.wireOp",EDGE,"fcba4419-a2ee-464f-be9d-58f11bf3418b.sketch_text.stroke-90"),sQuery(id+"F2.wireOp",EDGE,"fcba4419-a2ee-464f-be9d-58f11bf3418b.sketch_text.stroke-91"),sQuery(id+"F2.wireOp",EDGE,"fcba4419-a2ee-464f-be9d-58f11bf3418b.sketch_text.stroke-92"),sQuery(id+"F2.wireOp",EDGE,"fcba4419-a2ee-464f-be9d-58f11bf3418b.sketch_text.stroke-93"),sQuery(id+"F2.wireOp",EDGE,"fcba4419-a2ee-464f-be9d-58f11bf3418b.sketch_text.stroke-94"),sQuery(id+"F2.wireOp",EDGE,"fcba4419-a2ee-464f-be9d-58f11bf3418b.sketch_text.stroke-95"),sQuery(id+"F2.wireOp",EDGE,"fcba4419-a2ee-464f-be9d-58f11bf3418b.sketch_text.stroke-96"),sQuery(id+"F2.wireOp",EDGE,"fcba4419-a2ee-464f-be9d-58f11bf3418b.sketch_text.stroke-97"),sQuery(id+"F2.wireOp",EDGE,"fcba4419-a2ee-464f-be9d-58f11bf3418b.sketch_text.stroke-98"),sQuery(id+"F2.wireOp",EDGE,"fcba4419-a2ee-464f-be9d-58f11bf3418b.sketch_text.stroke-99"),sQuery(id+"F2.wireOp",EDGE,"fcba4419-a2ee-464f-be9d-58f11bf3418b.sketch_text.stroke-100"),sQuery(id+"F2.wireOp",EDGE,"fcba4419-a2ee-464f-be9d-58f11bf3418b.sketch_text.stroke-101"),sQuery(id+"F2.wireOp",EDGE,"fcba4419-a2ee-464f-be9d-58f11bf3418b.sketch_text.stroke-102"),sQuery(id+"F2.wireOp",EDGE,"fcba4419-a2ee-464f-be9d-58f11bf3418b.sketch_text.stroke-103"),sQuery(id+"F2.wireOp",EDGE,"fcba4419-a2ee-464f-be9d-58f11bf3418b.sketch_text.stroke-104"),sQuery(id+"F2.wireOp",EDGE,"fcba4419-a2ee-464f-be9d-58f11bf3418b.sketch_text.stroke-105"),sQuery(id+"F2.wireOp",EDGE,"fcba4419-a2ee-464f-be9d-58f11bf3418b.sketch_text.stroke-106"),sQuery(id+"F2.wireOp",EDGE,"fcba4419-a2ee-464f-be9d-58f11bf3418b.sketch_text.stroke-107"),sQuery(id+"F2.wireOp",EDGE,"fcba4419-a2ee-464f-be9d-58f11bf3418b.sketch_text.stroke-108"),sQuery(id+"F2.wireOp",EDGE,"fcba4419-a2ee-464f-be9d-58f11bf3418b.sketch_text.stroke-109"),sQuery(id+"F2.wireOp",EDGE,"fcba4419-a2ee-464f-be9d-58f11bf3418b.sketch_text.stroke-110"),sQuery(id+"F2.wireOp",EDGE,"fcba4419-a2ee-464f-be9d-58f11bf3418b.sketch_text.stroke-111"),sQuery(id+"F2.wireOp",EDGE,"fcba4419-a2ee-464f-be9d-58f11bf3418b.sketch_text.stroke-112"),sQuery(id+"F2.wireOp",EDGE,"fcba4419-a2ee-464f-be9d-58f11bf3418b.sketch_text.stroke-113"),sQuery(id+"F2.wireOp",EDGE,"fcba4419-a2ee-464f-be9d-58f11bf3418b.sketch_text.stroke-114"),sQuery(id+"F2.wireOp",EDGE,"fcba4419-a2ee-464f-be9d-58f11bf3418b.sketch_text.stroke-115"),sQuery(id+"F2.wireOp",EDGE,"fcba4419-a2ee-464f-be9d-58f11bf3418b.sketch_text.stroke-116"),sQuery(id+"F2.wireOp",EDGE,"fcba4419-a2ee-464f-be9d-58f11bf3418b.sketch_text.stroke-117"),sQuery(id+"F2.wireOp",EDGE,"fcba4419-a2ee-464f-be9d-58f11bf3418b.sketch_text.stroke-118"),sQuery(id+"F2.wireOp",EDGE,"fcba4419-a2ee-464f-be9d-58f11bf3418b.sketch_text.stroke-119"),sQuery(id+"F2.wireOp",EDGE,"fcba4419-a2ee-464f-be9d-58f11bf3418b.sketch_text.stroke-120"),sQuery(id+"F2.wireOp",EDGE,"fcba4419-a2ee-464f-be9d-58f11bf3418b.sketch_text.stroke-121"),sQuery(id+"F2.wireOp",EDGE,"fcba4419-a2ee-464f-be9d-58f11bf3418b.sketch_text.stroke-122"),sQuery(id+"F2.wireOp",EDGE,"fcba4419-a2ee-464f-be9d-58f11bf3418b.sketch_text.stroke-123"),sQuery(id+"F2.wireOp",EDGE,"fcba4419-a2ee-464f-be9d-58f11bf3418b.sketch_text.stroke-124"),sQuery(id+"F2.wireOp",EDGE,"fcba4419-a2ee-464f-be9d-58f11bf3418b.sketch_text.stroke-125"),sQuery(id+"F2.wireOp",EDGE,"fcba4419-a2ee-464f-be9d-58f11bf3418b.sketch_text.stroke-126"),sQuery(id+"F2.wireOp",EDGE,"fcba4419-a2ee-464f-be9d-58f11bf3418b.sketch_text.stroke-127"),sQuery(id+"F2.wireOp",EDGE,"fcba4419-a2ee-464f-be9d-58f11bf3418b.sketch_text.stroke-128"),sQuery(id+"F2.wireOp",EDGE,"fcba4419-a2ee-464f-be9d-58f11bf3418b.sketch_text.stroke-129"),sQuery(id+"F2.wireOp",EDGE,"fcba4419-a2ee-464f-be9d-58f11bf3418b.sketch_text.stroke-130"),sQuery(id+"F2.wireOp",EDGE,"fcba4419-a2ee-464f-be9d-58f11bf3418b.sketch_text.stroke-131"),sQuery(id+"F2.wireOp",EDGE,"fcba4419-a2ee-464f-be9d-58f11bf3418b.sketch_text.stroke-132"),sQuery(id+"F2.wireOp",EDGE,"fcba4419-a2ee-464f-be9d-58f11bf3418b.sketch_text.stroke-133"),sQuery(id+"F2.wireOp",EDGE,"fcba4419-a2ee-464f-be9d-58f11bf3418b.sketch_text.stroke-134"),sQuery(id+"F2.wireOp",EDGE,"fcba4419-a2ee-464f-be9d-58f11bf3418b.sketch_text.stroke-135"),sQuery(id+"F2.wireOp",EDGE,"fcba4419-a2ee-464f-be9d-58f11bf3418b.sketch_text.stroke-136"),sQuery(id+"F2.wireOp",EDGE,"fcba4419-a2ee-464f-be9d-58f11bf3418b.sketch_text.stroke-137"),sQuery(id+"F2.wireOp",EDGE,"fcba4419-a2ee-464f-be9d-58f11bf3418b.sketch_text.stroke-138"),sQuery(id+"F2.wireOp",EDGE,"fcba4419-a2ee-464f-be9d-58f11bf3418b.sketch_text.stroke-139"),sQuery(id+"F2.wireOp",EDGE,"fcba4419-a2ee-464f-be9d-58f11bf3418b.sketch_text.stroke-140"),sQuery(id+"F2.wireOp",EDGE,"fcba4419-a2ee-464f-be9d-58f11bf3418b.sketch_text.stroke-141"),sQuery(id+"F2.wireOp",EDGE,"fcba4419-a2ee-464f-be9d-58f11bf3418b.sketch_text.stroke-142"),sQuery(id+"F2.wireOp",EDGE,"fcba4419-a2ee-464f-be9d-58f11bf3418b.sketch_text.stroke-143"),sQuery(id+"F2.wireOp",EDGE,"fcba4419-a2ee-464f-be9d-58f11bf3418b.sketch_text.stroke-144"),sQuery(id+"F2.wireOp",EDGE,"fcba4419-a2ee-464f-be9d-58f11bf3418b.sketch_text.stroke-145"),sQuery(id+"F2.wireOp",EDGE,"fcba4419-a2ee-464f-be9d-58f11bf3418b.sketch_text.stroke-146"),sQuery(id+"F2.wireOp",EDGE,"fcba4419-a2ee-464f-be9d-58f11bf3418b.sketch_text.stroke-147"),sQuery(id+"F2.wireOp",EDGE,"fcba4419-a2ee-464f-be9d-58f11bf3418b.sketch_text.stroke-148"),sQuery(id+"F2.wireOp",EDGE,"fcba4419-a2ee-464f-be9d-58f11bf3418b.sketch_text.stroke-149"),sQuery(id+"F2.wireOp",EDGE,"fcba4419-a2ee-464f-be9d-58f11bf3418b.sketch_text.stroke-150"),sQuery(id+"F2.wireOp",EDGE,"fcba4419-a2ee-464f-be9d-58f11bf3418b.sketch_text.stroke-151"),sQuery(id+"F2.wireOp",EDGE,"fcba4419-a2ee-464f-be9d-58f11bf3418b.sketch_text.stroke-152"),sQuery(id+"F2.wireOp",EDGE,"fcba4419-a2ee-464f-be9d-58f11bf3418b.sketch_text.stroke-153"),sQuery(id+"F2.wireOp",EDGE,"fcba4419-a2ee-464f-be9d-58f11bf3418b.sketch_text.stroke-154"),sQuery(id+"F2.wireOp",EDGE,"fcba4419-a2ee-464f-be9d-58f11bf3418b.sketch_text.stroke-155"),sQuery(id+"F2.wireOp",EDGE,"fcba4419-a2ee-464f-be9d-58f11bf3418b.sketch_text.stroke-156"),sQuery(id+"F2.wireOp",EDGE,"fcba4419-a2ee-464f-be9d-58f11bf3418b.sketch_text.stroke-157"),sQuery(id+"F2.wireOp",EDGE,"fcba4419-a2ee-464f-be9d-58f11bf3418b.sketch_text.stroke-158"),sQuery(id+"F2.wireOp",EDGE,"fcba4419-a2ee-464f-be9d-58f11bf3418b.sketch_text.stroke-159"),sQuery(id+"F2.wireOp",EDGE,"fcba4419-a2ee-464f-be9d-58f11bf3418b.sketch_text.stroke-160"),sQuery(id+"F2.wireOp",EDGE,"fcba4419-a2ee-464f-be9d-58f11bf3418b.sketch_text.stroke-161"),sQuery(id+"F2.wireOp",EDGE,"fcba4419-a2ee-464f-be9d-58f11bf3418b.sketch_text.stroke-162"),sQuery(id+"F2.wireOp",EDGE,"fcba4419-a2ee-464f-be9d-58f11bf3418b.sketch_text.stroke-163"),sQuery(id+"F2.wireOp",EDGE,"fcba4419-a2ee-464f-be9d-58f11bf3418b.sketch_text.stroke-164"),sQuery(id+"F2.wireOp",EDGE,"fcba4419-a2ee-464f-be9d-58f11bf3418b.sketch_text.stroke-165"),sQuery(id+"F2.wireOp",EDGE,"fcba4419-a2ee-464f-be9d-58f11bf3418b.sketch_text.stroke-166"),sQuery(id+"F2.wireOp",EDGE,"fcba4419-a2ee-464f-be9d-58f11bf3418b.sketch_text.stroke-167"),sQuery(id+"F2.wireOp",EDGE,"fcba4419-a2ee-464f-be9d-58f11bf3418b.sketch_text.stroke-168"),sQuery(id+"F2.wireOp",EDGE,"fcba4419-a2ee-464f-be9d-58f11bf3418b.sketch_text.stroke-169"),sQuery(id+"F2.wireOp",EDGE,"fcba4419-a2ee-464f-be9d-58f11bf3418b.sketch_text.stroke-170"),sQuery(id+"F2.wireOp",EDGE,"fcba4419-a2ee-464f-be9d-58f11bf3418b.sketch_text.stroke-171"),sQuery(id+"F2.wireOp",EDGE,"fcba4419-a2ee-464f-be9d-58f11bf3418b.sketch_text.stroke-172"),sQuery(id+"F2.wireOp",EDGE,"fcba4419-a2ee-464f-be9d-58f11bf3418b.sketch_text.stroke-173"),sQuery(id+"FHMxAyK4CFUKdhS_1.wireOp",EDGE,"1cb9c079-ea9b-4899-8069-e0e3048e911d.sketch_text.stroke-0"),sQuery(id+"FHMxAyK4CFUKdhS_1.wireOp",EDGE,"1cb9c079-ea9b-4899-8069-e0e3048e911d.sketch_text.stroke-1"),sQuery(id+"FHMxAyK4CFUKdhS_1.wireOp",EDGE,"1cb9c079-ea9b-4899-8069-e0e3048e911d.sketch_text.stroke-2"),sQuery(id+"FHMxAyK4CFUKdhS_1.wireOp",EDGE,"1cb9c079-ea9b-4899-8069-e0e3048e911d.sketch_text.stroke-3"),sQuery(id+"FHMxAyK4CFUKdhS_1.wireOp",EDGE,"1cb9c079-ea9b-4899-8069-e0e3048e911d.sketch_text.stroke-4"),sQuery(id+"FHMxAyK4CFUKdhS_1.wireOp",EDGE,"1cb9c079-ea9b-4899-8069-e0e3048e911d.sketch_text.stroke-5"),sQuery(id+"FHMxAyK4CFUKdhS_1.wireOp",EDGE,"1cb9c079-ea9b-4899-8069-e0e3048e911d.sketch_text.stroke-6"),sQuery(id+"FHMxAyK4CFUKdhS_1.wireOp",EDGE,"1cb9c079-ea9b-4899-8069-e0e3048e911d.sketch_text.stroke-7"),sQuery(id+"FHMxAyK4CFUKdhS_1.wireOp",EDGE,"1cb9c079-ea9b-4899-8069-e0e3048e911d.sketch_text.stroke-8"),sQuery(id+"FHMxAyK4CFUKdhS_1.wireOp",EDGE,"1cb9c079-ea9b-4899-8069-e0e3048e911d.sketch_text.stroke-9"),sQuery(id+"FHMxAyK4CFUKdhS_1.wireOp",EDGE,"1cb9c079-ea9b-4899-8069-e0e3048e911d.sketch_text.stroke-10"),sQuery(id+"FHMxAyK4CFUKdhS_1.wireOp",EDGE,"1cb9c079-ea9b-4899-8069-e0e3048e911d.sketch_text.stroke-11"),sQuery(id+"FHMxAyK4CFUKdhS_1.wireOp",EDGE,"1cb9c079-ea9b-4899-8069-e0e3048e911d.sketch_text.stroke-12"),sQuery(id+"FHMxAyK4CFUKdhS_1.wireOp",EDGE,"1cb9c079-ea9b-4899-8069-e0e3048e911d.sketch_text.stroke-13"),sQuery(id+"FHMxAyK4CFUKdhS_1.wireOp",EDGE,"1cb9c079-ea9b-4899-8069-e0e3048e911d.sketch_text.stroke-14"),sQuery(id+"FHMxAyK4CFUKdhS_1.wireOp",EDGE,"1cb9c079-ea9b-4899-8069-e0e3048e911d.sketch_text.stroke-15"),sQuery(id+"FHMxAyK4CFUKdhS_1.wireOp",EDGE,"1cb9c079-ea9b-4899-8069-e0e3048e911d.sketch_text.stroke-16"),sQuery(id+"FHMxAyK4CFUKdhS_1.wireOp",EDGE,"1cb9c079-ea9b-4899-8069-e0e3048e911d.sketch_text.stroke-17"),sQuery(id+"FHMxAyK4CFUKdhS_1.wireOp",EDGE,"1cb9c079-ea9b-4899-8069-e0e3048e911d.sketch_text.stroke-18"),sQuery(id+"FHMxAyK4CFUKdhS_1.wireOp",EDGE,"1cb9c079-ea9b-4899-8069-e0e3048e911d.sketch_text.stroke-19"),sQuery(id+"FHMxAyK4CFUKdhS_1.wireOp",EDGE,"1cb9c079-ea9b-4899-8069-e0e3048e911d.sketch_text.stroke-20"),sQuery(id+"FHMxAyK4CFUKdhS_1.wireOp",EDGE,"1cb9c079-ea9b-4899-8069-e0e3048e911d.sketch_text.stroke-21"),sQuery(id+"FHMxAyK4CFUKdhS_1.wireOp",EDGE,"1cb9c079-ea9b-4899-8069-e0e3048e911d.sketch_text.stroke-22"),sQuery(id+"FHMxAyK4CFUKdhS_1.wireOp",EDGE,"1cb9c079-ea9b-4899-8069-e0e3048e911d.sketch_text.stroke-23"),sQuery(id+"FHMxAyK4CFUKdhS_1.wireOp",EDGE,"1cb9c079-ea9b-4899-8069-e0e3048e911d.sketch_text.stroke-24"),sQuery(id+"FHMxAyK4CFUKdhS_1.wireOp",EDGE,"1cb9c079-ea9b-4899-8069-e0e3048e911d.sketch_text.stroke-25"),sQuery(id+"FHMxAyK4CFUKdhS_1.wireOp",EDGE,"1cb9c079-ea9b-4899-8069-e0e3048e911d.sketch_text.stroke-26"),sQuery(id+"FHMxAyK4CFUKdhS_1.wireOp",EDGE,"1cb9c079-ea9b-4899-8069-e0e3048e911d.sketch_text.stroke-27"),sQuery(id+"FHMxAyK4CFUKdhS_1.wireOp",EDGE,"1cb9c079-ea9b-4899-8069-e0e3048e911d.sketch_text.stroke-28"),sQuery(id+"FHMxAyK4CFUKdhS_1.wireOp",EDGE,"1cb9c079-ea9b-4899-8069-e0e3048e911d.sketch_text.stroke-29"),sQuery(id+"FHMxAyK4CFUKdhS_1.wireOp",EDGE,"1cb9c079-ea9b-4899-8069-e0e3048e911d.sketch_text.stroke-30"),sQuery(id+"FHMxAyK4CFUKdhS_1.wireOp",EDGE,"1cb9c079-ea9b-4899-8069-e0e3048e911d.sketch_text.stroke-31"),sQuery(id+"FHMxAyK4CFUKdhS_1.wireOp",EDGE,"1cb9c079-ea9b-4899-8069-e0e3048e911d.sketch_text.stroke-32"),sQuery(id+"FHMxAyK4CFUKdhS_1.wireOp",EDGE,"1cb9c079-ea9b-4899-8069-e0e3048e911d.sketch_text.stroke-33"),sQuery(id+"FHMxAyK4CFUKdhS_1.wireOp",EDGE,"1cb9c079-ea9b-4899-8069-e0e3048e911d.sketch_text.stroke-34"),sQuery(id+"FHMxAyK4CFUKdhS_1.wireOp",EDGE,"1cb9c079-ea9b-4899-8069-e0e3048e911d.sketch_text.stroke-35"),sQuery(id+"FHMxAyK4CFUKdhS_1.wireOp",EDGE,"1cb9c079-ea9b-4899-8069-e0e3048e911d.sketch_text.stroke-36"),sQuery(id+"FHMxAyK4CFUKdhS_1.wireOp",EDGE,"1cb9c079-ea9b-4899-8069-e0e3048e911d.sketch_text.stroke-37"),sQuery(id+"FHMxAyK4CFUKdhS_1.wireOp",EDGE,"1cb9c079-ea9b-4899-8069-e0e3048e911d.sketch_text.stroke-38"),sQuery(id+"FHMxAyK4CFUKdhS_1.wireOp",EDGE,"1cb9c079-ea9b-4899-8069-e0e3048e911d.sketch_text.stroke-39"),sQuery(id+"FHMxAyK4CFUKdhS_1.wireOp",EDGE,"1cb9c079-ea9b-4899-8069-e0e3048e911d.sketch_text.stroke-40"),sQuery(id+"FHMxAyK4CFUKdhS_1.wireOp",EDGE,"1cb9c079-ea9b-4899-8069-e0e3048e911d.sketch_text.stroke-41"),sQuery(id+"FHMxAyK4CFUKdhS_1.wireOp",EDGE,"1cb9c079-ea9b-4899-8069-e0e3048e911d.sketch_text.stroke-42"),sQuery(id+"FHMxAyK4CFUKdhS_1.wireOp",EDGE,"1cb9c079-ea9b-4899-8069-e0e3048e911d.sketch_text.stroke-43"),sQuery(id+"FHMxAyK4CFUKdhS_1.wireOp",EDGE,"1cb9c079-ea9b-4899-8069-e0e3048e911d.sketch_text.stroke-44"),sQuery(id+"FHMxAyK4CFUKdhS_1.wireOp",EDGE,"1cb9c079-ea9b-4899-8069-e0e3048e911d.sketch_text.stroke-45"),sQuery(id+"FHMxAyK4CFUKdhS_1.wireOp",EDGE,"1cb9c079-ea9b-4899-8069-e0e3048e911d.sketch_text.stroke-46"),sQuery(id+"FHMxAyK4CFUKdhS_1.wireOp",EDGE,"1cb9c079-ea9b-4899-8069-e0e3048e911d.sketch_text.stroke-47"),sQuery(id+"FHMxAyK4CFUKdhS_1.wireOp",EDGE,"1cb9c079-ea9b-4899-8069-e0e3048e911d.sketch_text.stroke-48"),sQuery(id+"FHMxAyK4CFUKdhS_1.wireOp",EDGE,"1cb9c079-ea9b-4899-8069-e0e3048e911d.sketch_text.stroke-49"),sQuery(id+"FHMxAyK4CFUKdhS_1.wireOp",EDGE,"1cb9c079-ea9b-4899-8069-e0e3048e911d.sketch_text.stroke-50"),sQuery(id+"FHMxAyK4CFUKdhS_1.wireOp",EDGE,"1cb9c079-ea9b-4899-8069-e0e3048e911d.sketch_text.stroke-51"),sQuery(id+"FHMxAyK4CFUKdhS_1.wireOp",EDGE,"1cb9c079-ea9b-4899-8069-e0e3048e911d.sketch_text.stroke-52"),sQuery(id+"FHMxAyK4CFUKdhS_1.wireOp",EDGE,"1cb9c079-ea9b-4899-8069-e0e3048e911d.sketch_text.stroke-53"),sQuery(id+"FHMxAyK4CFUKdhS_1.wireOp",EDGE,"1cb9c079-ea9b-4899-8069-e0e3048e911d.sketch_text.stroke-54"),sQuery(id+"FHMxAyK4CFUKdhS_1.wireOp",EDGE,"1cb9c079-ea9b-4899-8069-e0e3048e911d.sketch_text.stroke-55"),sQuery(id+"FHMxAyK4CFUKdhS_1.wireOp",EDGE,"1cb9c079-ea9b-4899-8069-e0e3048e911d.sketch_text.stroke-56"),sQuery(id+"FHMxAyK4CFUKdhS_1.wireOp",EDGE,"1cb9c079-ea9b-4899-8069-e0e3048e911d.sketch_text.stroke-57"),sQuery(id+"FHMxAyK4CFUKdhS_1.wireOp",EDGE,"1cb9c079-ea9b-4899-8069-e0e3048e911d.sketch_text.stroke-58"),sQuery(id+"FHMxAyK4CFUKdhS_1.wireOp",EDGE,"1cb9c079-ea9b-4899-8069-e0e3048e911d.sketch_text.stroke-59"),sQuery(id+"FHMxAyK4CFUKdhS_1.wireOp",EDGE,"1cb9c079-ea9b-4899-8069-e0e3048e911d.sketch_text.stroke-60"),sQuery(id+"FHMxAyK4CFUKdhS_1.wireOp",EDGE,"1cb9c079-ea9b-4899-8069-e0e3048e911d.sketch_text.stroke-61"),sQuery(id+"FHMxAyK4CFUKdhS_1.wireOp",EDGE,"1cb9c079-ea9b-4899-8069-e0e3048e911d.sketch_text.stroke-62"),sQuery(id+"FHMxAyK4CFUKdhS_1.wireOp",EDGE,"1cb9c079-ea9b-4899-8069-e0e3048e911d.sketch_text.stroke-71"),sQuery(id+"FHMxAyK4CFUKdhS_1.wireOp",EDGE,"1cb9c079-ea9b-4899-8069-e0e3048e911d.sketch_text.stroke-72"),sQuery(id+"FHMxAyK4CFUKdhS_1.wireOp",EDGE,"1cb9c079-ea9b-4899-8069-e0e3048e911d.sketch_text.stroke-73"),sQuery(id+"FHMxAyK4CFUKdhS_1.wireOp",EDGE,"1cb9c079-ea9b-4899-8069-e0e3048e911d.sketch_text.stroke-74"),sQuery(id+"FHMxAyK4CFUKdhS_1.wireOp",EDGE,"1cb9c079-ea9b-4899-8069-e0e3048e911d.sketch_text.stroke-75"),sQuery(id+"FHMxAyK4CFUKdhS_1.wireOp",EDGE,"1cb9c079-ea9b-4899-8069-e0e3048e911d.sketch_text.stroke-76"),sQuery(id+"FHMxAyK4CFUKdhS_1.wireOp",EDGE,"1cb9c079-ea9b-4899-8069-e0e3048e911d.sketch_text.stroke-77"),sQuery(id+"FHMxAyK4CFUKdhS_1.wireOp",EDGE,"1cb9c079-ea9b-4899-8069-e0e3048e911d.sketch_text.stroke-78"),sQuery(id+"FHMxAyK4CFUKdhS_1.wireOp",EDGE,"1cb9c079-ea9b-4899-8069-e0e3048e911d.sketch_text.stroke-79"),sQuery(id+"FHMxAyK4CFUKdhS_1.wireOp",EDGE,"1cb9c079-ea9b-4899-8069-e0e3048e911d.sketch_text.stroke-80"),sQuery(id+"FHMxAyK4CFUKdhS_1.wireOp",EDGE,"1cb9c079-ea9b-4899-8069-e0e3048e911d.sketch_text.stroke-81"),sQuery(id+"FHMxAyK4CFUKdhS_1.wireOp",EDGE,"1cb9c079-ea9b-4899-8069-e0e3048e911d.sketch_text.stroke-82"),sQuery(id+"FHMxAyK4CFUKdhS_1.wireOp",EDGE,"1cb9c079-ea9b-4899-8069-e0e3048e911d.sketch_text.stroke-83"),sQuery(id+"FHMxAyK4CFUKdhS_1.wireOp",EDGE,"1cb9c079-ea9b-4899-8069-e0e3048e911d.sketch_text.stroke-84"),sQuery(id+"FHMxAyK4CFUKdhS_1.wireOp",EDGE,"1cb9c079-ea9b-4899-8069-e0e3048e911d.sketch_text.stroke-85"),sQuery(id+"FHMxAyK4CFUKdhS_1.wireOp",EDGE,"1cb9c079-ea9b-4899-8069-e0e3048e911d.sketch_text.stroke-86"),sQuery(id+"FHMxAyK4CFUKdhS_1.wireOp",EDGE,"1cb9c079-ea9b-4899-8069-e0e3048e911d.sketch_text.stroke-87"),sQuery(id+"FHMxAyK4CFUKdhS_1.wireOp",EDGE,"1cb9c079-ea9b-4899-8069-e0e3048e911d.sketch_text.stroke-88"),sQuery(id+"FHMxAyK4CFUKdhS_1.wireOp",EDGE,"1cb9c079-ea9b-4899-8069-e0e3048e911d.sketch_text.stroke-89"),sQuery(id+"FHMxAyK4CFUKdhS_1.wireOp",EDGE,"1cb9c079-ea9b-4899-8069-e0e3048e911d.sketch_text.stroke-90"),sQuery(id+"FHMxAyK4CFUKdhS_1.wireOp",EDGE,"1cb9c079-ea9b-4899-8069-e0e3048e911d.sketch_text.stroke-91"),sQuery(id+"FHMxAyK4CFUKdhS_1.wireOp",EDGE,"1cb9c079-ea9b-4899-8069-e0e3048e911d.sketch_text.stroke-92"),sQuery(id+"FHMxAyK4CFUKdhS_1.wireOp",EDGE,"1cb9c079-ea9b-4899-8069-e0e3048e911d.sketch_text.stroke-93"),sQuery(id+"FHMxAyK4CFUKdhS_1.wireOp",EDGE,"1cb9c079-ea9b-4899-8069-e0e3048e911d.sketch_text.stroke-94"),sQuery(id+"FHMxAyK4CFUKdhS_1.wireOp",EDGE,"1cb9c079-ea9b-4899-8069-e0e3048e911d.sketch_text.stroke-95"),sQuery(id+"FHMxAyK4CFUKdhS_1.wireOp",EDGE,"1cb9c079-ea9b-4899-8069-e0e3048e911d.sketch_text.stroke-96"),sQuery(id+"FHMxAyK4CFUKdhS_1.wireOp",EDGE,"1cb9c079-ea9b-4899-8069-e0e3048e911d.sketch_text.stroke-97"),sQuery(id+"FHMxAyK4CFUKdhS_1.wireOp",EDGE,"1cb9c079-ea9b-4899-8069-e0e3048e911d.sketch_text.stroke-103"),sQuery(id+"FHMxAyK4CFUKdhS_1.wireOp",EDGE,"1cb9c079-ea9b-4899-8069-e0e3048e911d.sketch_text.stroke-104"),sQuery(id+"FHMxAyK4CFUKdhS_1.wireOp",EDGE,"1cb9c079-ea9b-4899-8069-e0e3048e911d.sketch_text.stroke-105"),sQuery(id+"FHMxAyK4CFUKdhS_1.wireOp",EDGE,"1cb9c079-ea9b-4899-8069-e0e3048e911d.sketch_text.stroke-106"),sQuery(id+"FHMxAyK4CFUKdhS_1.wireOp",EDGE,"1cb9c079-ea9b-4899-8069-e0e3048e911d.sketch_text.stroke-107"),sQuery(id+"FHMxAyK4CFUKdhS_1.wireOp",EDGE,"1cb9c079-ea9b-4899-8069-e0e3048e911d.sketch_text.stroke-108"),sQuery(id+"FHMxAyK4CFUKdhS_1.wireOp",EDGE,"1cb9c079-ea9b-4899-8069-e0e3048e911d.sketch_text.stroke-109"),sQuery(id+"FHMxAyK4CFUKdhS_1.wireOp",EDGE,"1cb9c079-ea9b-4899-8069-e0e3048e911d.sketch_text.stroke-110"),sQuery(id+"FHMxAyK4CFUKdhS_1.wireOp",EDGE,"1cb9c079-ea9b-4899-8069-e0e3048e911d.sketch_text.stroke-111"),sQuery(id+"FHMxAyK4CFUKdhS_1.wireOp",EDGE,"1cb9c079-ea9b-4899-8069-e0e3048e911d.sketch_text.stroke-112"),sQuery(id+"FHMxAyK4CFUKdhS_1.wireOp",EDGE,"1cb9c079-ea9b-4899-8069-e0e3048e911d.sketch_text.stroke-113"),sQuery(id+"FHMxAyK4CFUKdhS_1.wireOp",EDGE,"1cb9c079-ea9b-4899-8069-e0e3048e911d.sketch_text.stroke-114"),sQuery(id+"FHMxAyK4CFUKdhS_1.wireOp",EDGE,"1cb9c079-ea9b-4899-8069-e0e3048e911d.sketch_text.stroke-115"),sQuery(id+"FHMxAyK4CFUKdhS_1.wireOp",EDGE,"1cb9c079-ea9b-4899-8069-e0e3048e911d.sketch_text.stroke-116"),sQuery(id+"FHMxAyK4CFUKdhS_1.wireOp",EDGE,"1cb9c079-ea9b-4899-8069-e0e3048e911d.sketch_text.stroke-117"),sQuery(id+"FHMxAyK4CFUKdhS_1.wireOp",EDGE,"1cb9c079-ea9b-4899-8069-e0e3048e911d.sketch_text.stroke-118"),sQuery(id+"FHMxAyK4CFUKdhS_1.wireOp",EDGE,"1cb9c079-ea9b-4899-8069-e0e3048e911d.sketch_text.stroke-119"),sQuery(id+"FHMxAyK4CFUKdhS_1.wireOp",EDGE,"1cb9c079-ea9b-4899-8069-e0e3048e911d.sketch_text.stroke-120"),sQuery(id+"FHMxAyK4CFUKdhS_1.wireOp",EDGE,"1cb9c079-ea9b-4899-8069-e0e3048e911d.sketch_text.stroke-121"),sQuery(id+"FHMxAyK4CFUKdhS_1.wireOp",EDGE,"1cb9c079-ea9b-4899-8069-e0e3048e911d.sketch_text.stroke-122"),sQuery(id+"FHMxAyK4CFUKdhS_1.wireOp",EDGE,"1cb9c079-ea9b-4899-8069-e0e3048e911d.sketch_text.stroke-123"),sQuery(id+"FHMxAyK4CFUKdhS_1.wireOp",EDGE,"1cb9c079-ea9b-4899-8069-e0e3048e911d.sketch_text.stroke-124"),sQuery(id+"FHMxAyK4CFUKdhS_1.wireOp",EDGE,"1cb9c079-ea9b-4899-8069-e0e3048e911d.sketch_text.stroke-125"),sQuery(id+"FHMxAyK4CFUKdhS_1.wireOp",EDGE,"1cb9c079-ea9b-4899-8069-e0e3048e911d.sketch_text.stroke-126"),sQuery(id+"FHMxAyK4CFUKdhS_1.wireOp",EDGE,"1cb9c079-ea9b-4899-8069-e0e3048e911d.sketch_text.stroke-127"),sQuery(id+"FHMxAyK4CFUKdhS_1.wireOp",EDGE,"1cb9c079-ea9b-4899-8069-e0e3048e911d.sketch_text.stroke-128"),sQuery(id+"FHMxAyK4CFUKdhS_1.wireOp",EDGE,"1cb9c079-ea9b-4899-8069-e0e3048e911d.sketch_text.stroke-129"),sQuery(id+"FHMxAyK4CFUKdhS_1.wireOp",EDGE,"1cb9c079-ea9b-4899-8069-e0e3048e911d.sketch_text.stroke-130"),sQuery(id+"FHMxAyK4CFUKdhS_1.wireOp",EDGE,"1cb9c079-ea9b-4899-8069-e0e3048e911d.sketch_text.stroke-131"),sQuery(id+"FHMxAyK4CFUKdhS_1.wireOp",EDGE,"1cb9c079-ea9b-4899-8069-e0e3048e911d.sketch_text.stroke-132"),sQuery(id+"FHMxAyK4CFUKdhS_1.wireOp",EDGE,"1cb9c079-ea9b-4899-8069-e0e3048e911d.sketch_text.stroke-133"),sQuery(id+"FHMxAyK4CFUKdhS_1.wireOp",EDGE,"1cb9c079-ea9b-4899-8069-e0e3048e911d.sketch_text.stroke-134"),sQuery(id+"FHMxAyK4CFUKdhS_1.wireOp",EDGE,"1cb9c079-ea9b-4899-8069-e0e3048e911d.sketch_text.stroke-135"),sQuery(id+"FHMxAyK4CFUKdhS_1.wireOp",EDGE,"1cb9c079-ea9b-4899-8069-e0e3048e911d.sketch_text.stroke-136"),sQuery(id+"FHMxAyK4CFUKdhS_1.wireOp",EDGE,"1cb9c079-ea9b-4899-8069-e0e3048e911d.sketch_text.stroke-137"),sQuery(id+"FHMxAyK4CFUKdhS_1.wireOp",EDGE,"1cb9c079-ea9b-4899-8069-e0e3048e911d.sketch_text.stroke-138"),sQuery(id+"FHMxAyK4CFUKdhS_1.wireOp",EDGE,"1cb9c079-ea9b-4899-8069-e0e3048e911d.sketch_text.stroke-139"),sQuery(id+"FHMxAyK4CFUKdhS_1.wireOp",EDGE,"1cb9c079-ea9b-4899-8069-e0e3048e911d.sketch_text.stroke-140"),sQuery(id+"FHMxAyK4CFUKdhS_1.wireOp",EDGE,"1cb9c079-ea9b-4899-8069-e0e3048e911d.sketch_text.stroke-141"),sQuery(id+"FHMxAyK4CFUKdhS_1.wireOp",EDGE,"1cb9c079-ea9b-4899-8069-e0e3048e911d.sketch_text.stroke-142"),sQuery(id+"FHMxAyK4CFUKdhS_1.wireOp",EDGE,"1cb9c079-ea9b-4899-8069-e0e3048e911d.sketch_text.stroke-143"),sQuery(id+"FHMxAyK4CFUKdhS_1.wireOp",EDGE,"1cb9c079-ea9b-4899-8069-e0e3048e911d.sketch_text.stroke-144"),sQuery(id+"FHMxAyK4CFUKdhS_1.wireOp",EDGE,"1cb9c079-ea9b-4899-8069-e0e3048e911d.sketch_text.stroke-145"),sQuery(id+"FHMxAyK4CFUKdhS_1.wireOp",EDGE,"1cb9c079-ea9b-4899-8069-e0e3048e911d.sketch_text.stroke-146"),sQuery(id+"FHMxAyK4CFUKdhS_1.wireOp",EDGE,"1cb9c079-ea9b-4899-8069-e0e3048e911d.sketch_text.stroke-147"),sQuery(id+"FHMxAyK4CFUKdhS_1.wireOp",EDGE,"1cb9c079-ea9b-4899-8069-e0e3048e911d.sketch_text.stroke-148"),sQuery(id+"FHMxAyK4CFUKdhS_1.wireOp",EDGE,"1cb9c079-ea9b-4899-8069-e0e3048e911d.sketch_text.stroke-149"),sQuery(id+"FHMxAyK4CFUKdhS_1.wireOp",EDGE,"1cb9c079-ea9b-4899-8069-e0e3048e911d.sketch_text.stroke-150"),sQuery(id+"FHMxAyK4CFUKdhS_1.wireOp",EDGE,"1cb9c079-ea9b-4899-8069-e0e3048e911d.sketch_text.stroke-151"),sQuery(id+"FHMxAyK4CFUKdhS_1.wireOp",EDGE,"1cb9c079-ea9b-4899-8069-e0e3048e911d.sketch_text.stroke-152"),sQuery(id+"FHMxAyK4CFUKdhS_1.wireOp",EDGE,"1cb9c079-ea9b-4899-8069-e0e3048e911d.sketch_text.stroke-153"),sQuery(id+"FHMxAyK4CFUKdhS_1.wireOp",EDGE,"1cb9c079-ea9b-4899-8069-e0e3048e911d.sketch_text.stroke-159"),sQuery(id+"FHMxAyK4CFUKdhS_1.wireOp",EDGE,"1cb9c079-ea9b-4899-8069-e0e3048e911d.sketch_text.stroke-160"),sQuery(id+"FHMxAyK4CFUKdhS_1.wireOp",EDGE,"1cb9c079-ea9b-4899-8069-e0e3048e911d.sketch_text.stroke-161"),sQuery(id+"FHMxAyK4CFUKdhS_1.wireOp",EDGE,"1cb9c079-ea9b-4899-8069-e0e3048e911d.sketch_text.stroke-162"),sQuery(id+"FHMxAyK4CFUKdhS_1.wireOp",EDGE,"1cb9c079-ea9b-4899-8069-e0e3048e911d.sketch_text.stroke-163"),sQuery(id+"FHMxAyK4CFUKdhS_1.wireOp",EDGE,"1cb9c079-ea9b-4899-8069-e0e3048e911d.sketch_text.stroke-164"),sQuery(id+"FHMxAyK4CFUKdhS_1.wireOp",EDGE,"1cb9c079-ea9b-4899-8069-e0e3048e911d.sketch_text.stroke-165"),sQuery(id+"FHMxAyK4CFUKdhS_1.wireOp",EDGE,"1cb9c079-ea9b-4899-8069-e0e3048e911d.sketch_text.stroke-166"),sQuery(id+"FHMxAyK4CFUKdhS_1.wireOp",EDGE,"1cb9c079-ea9b-4899-8069-e0e3048e911d.sketch_text.stroke-167"),sQuery(id+"FHMxAyK4CFUKdhS_1.wireOp",EDGE,"1cb9c079-ea9b-4899-8069-e0e3048e911d.sketch_text.stroke-168"),sQuery(id+"FHMxAyK4CFUKdhS_1.wireOp",EDGE,"1cb9c079-ea9b-4899-8069-e0e3048e911d.sketch_text.stroke-169"),sQuery(id+"FHMxAyK4CFUKdhS_1.wireOp",EDGE,"1cb9c079-ea9b-4899-8069-e0e3048e911d.sketch_text.stroke-170"),sQuery(id+"FHMxAyK4CFUKdhS_1.wireOp",EDGE,"1cb9c079-ea9b-4899-8069-e0e3048e911d.sketch_text.stroke-171"),sQuery(id+"FHMxAyK4CFUKdhS_1.wireOp",EDGE,"1cb9c079-ea9b-4899-8069-e0e3048e911d.sketch_text.stroke-172"),sQuery(id+"FHMxAyK4CFUKdhS_1.wireOp",EDGE,"1cb9c079-ea9b-4899-8069-e0e3048e911d.sketch_text.stroke-173"),sQuery(id+"FHMxAyK4CFUKdhS_1.wireOp",EDGE,"1cb9c079-ea9b-4899-8069-e0e3048e911d.sketch_text.stroke-174"),sQuery(id+"FHMxAyK4CFUKdhS_1.wireOp",EDGE,"1cb9c079-ea9b-4899-8069-e0e3048e911d.sketch_text.stroke-175"),sQuery(id+"FHMxAyK4CFUKdhS_1.wireOp",EDGE,"1cb9c079-ea9b-4899-8069-e0e3048e911d.sketch_text.stroke-176"),sQuery(id+"FHMxAyK4CFUKdhS_1.wireOp",EDGE,"1cb9c079-ea9b-4899-8069-e0e3048e911d.sketch_text.stroke-177"),sQuery(id+"FHMxAyK4CFUKdhS_1.wireOp",EDGE,"1cb9c079-ea9b-4899-8069-e0e3048e911d.sketch_text.stroke-178"),sQuery(id+"FHMxAyK4CFUKdhS_1.wireOp",EDGE,"1cb9c079-ea9b-4899-8069-e0e3048e911d.sketch_text.stroke-179"),sQuery(id+"FHMxAyK4CFUKdhS_1.wireOp",EDGE,"1cb9c079-ea9b-4899-8069-e0e3048e911d.sketch_text.stroke-180"),sQuery(id+"F3.wireOp",EDGE,"8007402e-1a4e-4a06-85a5-2af08e553504"),subQ0])],"isStart":true}),makeQuery(id+"F4.opExtrude","SWEPT_FACE",FACE,{"disambiguationData":[OSD([subQ0])]})])],"derivedFrom":makeQuery(id+"F4.opExtrude","CAP_EDGE",EDGE,{"disambiguationData":[OSD([subQ0])],"isStart":true})});}
            var Q7;
            {var subQ0=sQuery(id+"F0.wireOp",EDGE,"E0.right");var subQ1=sQuery(id+"F0.wireOp",EDGE,"E0.top");var subQ2=sQuery(id+"F3.wireOp",EDGE,"6ee83ff3-586e-4dbe-aaea-af71240543bd");var subQ3=sQuery(id+"F0.wireOp",EDGE,"E0.bottom");Q7=makeQuery(id+"F4.boolean.opBoolean","SPLIT",EDGE,{"disambiguationData":[TD([makeQuery(id+"F1.opExtrude","CAP_FACE",FACE,{"disambiguationData":[OSD([subQ3,subQ1,sQuery(id+"F0.wireOp",EDGE,"E0.left"),subQ0])],"isStart":false}),makeQuery(id+"F1.opExtrude","SWEPT_FACE",FACE,{"disambiguationData":[OSD([subQ1])]}),makeQuery(id+"F1.opExtrude","SWEPT_FACE",FACE,{"disambiguationData":[OSD([subQ0])]}),makeQuery(id+"F4.opExtrude","CAP_FACE",FACE,{"disambiguationData":[OSD([subQ3,sQuery(id+"F2.wireOp",EDGE,"fcba4419-a2ee-464f-be9d-58f11bf3418b.sketch_text.stroke-0"),sQuery(id+"F2.wireOp",EDGE,"fcba4419-a2ee-464f-be9d-58f11bf3418b.sketch_text.stroke-1"),sQuery(id+"F2.wireOp",EDGE,"fcba4419-a2ee-464f-be9d-58f11bf3418b.sketch_text.stroke-2"),sQuery(id+"F2.wireOp",EDGE,"fcba4419-a2ee-464f-be9d-58f11bf3418b.sketch_text.stroke-3"),sQuery(id+"F2.wireOp",EDGE,"fcba4419-a2ee-464f-be9d-58f11bf3418b.sketch_text.stroke-4"),sQuery(id+"F2.wireOp",EDGE,"fcba4419-a2ee-464f-be9d-58f11bf3418b.sketch_text.stroke-5"),sQuery(id+"F2.wireOp",EDGE,"fcba4419-a2ee-464f-be9d-58f11bf3418b.sketch_text.stroke-6"),sQuery(id+"F2.wireOp",EDGE,"fcba4419-a2ee-464f-be9d-58f11bf3418b.sketch_text.stroke-7"),sQuery(id+"F2.wireOp",EDGE,"fcba4419-a2ee-464f-be9d-58f11bf3418b.sketch_text.stroke-8"),sQuery(id+"F2.wireOp",EDGE,"fcba4419-a2ee-464f-be9d-58f11bf3418b.sketch_text.stroke-9"),sQuery(id+"F2.wireOp",EDGE,"fcba4419-a2ee-464f-be9d-58f11bf3418b.sketch_text.stroke-10"),sQuery(id+"F2.wireOp",EDGE,"fcba4419-a2ee-464f-be9d-58f11bf3418b.sketch_text.stroke-11"),sQuery(id+"F2.wireOp",EDGE,"fcba4419-a2ee-464f-be9d-58f11bf3418b.sketch_text.stroke-12"),sQuery(id+"F2.wireOp",EDGE,"fcba4419-a2ee-464f-be9d-58f11bf3418b.sketch_text.stroke-13"),sQuery(id+"F2.wireOp",EDGE,"fcba4419-a2ee-464f-be9d-58f11bf3418b.sketch_text.stroke-14"),sQuery(id+"F2.wireOp",EDGE,"fcba4419-a2ee-464f-be9d-58f11bf3418b.sketch_text.stroke-15"),sQuery(id+"F2.wireOp",EDGE,"fcba4419-a2ee-464f-be9d-58f11bf3418b.sketch_text.stroke-16"),sQuery(id+"F2.wireOp",EDGE,"fcba4419-a2ee-464f-be9d-58f11bf3418b.sketch_text.stroke-17"),sQuery(id+"F2.wireOp",EDGE,"fcba4419-a2ee-464f-be9d-58f11bf3418b.sketch_text.stroke-18"),sQuery(id+"F2.wireOp",EDGE,"fcba4419-a2ee-464f-be9d-58f11bf3418b.sketch_text.stroke-19"),sQuery(id+"F2.wireOp",EDGE,"fcba4419-a2ee-464f-be9d-58f11bf3418b.sketch_text.stroke-20"),sQuery(id+"F2.wireOp",EDGE,"fcba4419-a2ee-464f-be9d-58f11bf3418b.sketch_text.stroke-21"),sQuery(id+"F2.wireOp",EDGE,"fcba4419-a2ee-464f-be9d-58f11bf3418b.sketch_text.stroke-22"),sQuery(id+"F2.wireOp",EDGE,"fcba4419-a2ee-464f-be9d-58f11bf3418b.sketch_text.stroke-23"),sQuery(id+"F2.wireOp",EDGE,"fcba4419-a2ee-464f-be9d-58f11bf3418b.sketch_text.stroke-24"),sQuery(id+"F2.wireOp",EDGE,"fcba4419-a2ee-464f-be9d-58f11bf3418b.sketch_text.stroke-25"),sQuery(id+"F2.wireOp",EDGE,"fcba4419-a2ee-464f-be9d-58f11bf3418b.sketch_text.stroke-26"),sQuery(id+"F2.wireOp",EDGE,"fcba4419-a2ee-464f-be9d-58f11bf3418b.sketch_text.stroke-27"),sQuery(id+"F2.wireOp",EDGE,"fcba4419-a2ee-464f-be9d-58f11bf3418b.sketch_text.stroke-28"),sQuery(id+"F2.wireOp",EDGE,"fcba4419-a2ee-464f-be9d-58f11bf3418b.sketch_text.stroke-29"),sQuery(id+"F2.wireOp",EDGE,"fcba4419-a2ee-464f-be9d-58f11bf3418b.sketch_text.stroke-30"),sQuery(id+"F2.wireOp",EDGE,"fcba4419-a2ee-464f-be9d-58f11bf3418b.sketch_text.stroke-31"),sQuery(id+"F2.wireOp",EDGE,"fcba4419-a2ee-464f-be9d-58f11bf3418b.sketch_text.stroke-32"),sQuery(id+"F2.wireOp",EDGE,"fcba4419-a2ee-464f-be9d-58f11bf3418b.sketch_text.stroke-33"),sQuery(id+"F2.wireOp",EDGE,"fcba4419-a2ee-464f-be9d-58f11bf3418b.sketch_text.stroke-34"),sQuery(id+"F2.wireOp",EDGE,"fcba4419-a2ee-464f-be9d-58f11bf3418b.sketch_text.stroke-35"),sQuery(id+"F2.wireOp",EDGE,"fcba4419-a2ee-464f-be9d-58f11bf3418b.sketch_text.stroke-36"),sQuery(id+"F2.wireOp",EDGE,"fcba4419-a2ee-464f-be9d-58f11bf3418b.sketch_text.stroke-37"),sQuery(id+"F2.wireOp",EDGE,"fcba4419-a2ee-464f-be9d-58f11bf3418b.sketch_text.stroke-38"),sQuery(id+"F2.wireOp",EDGE,"fcba4419-a2ee-464f-be9d-58f11bf3418b.sketch_text.stroke-39"),sQuery(id+"F2.wireOp",EDGE,"fcba4419-a2ee-464f-be9d-58f11bf3418b.sketch_text.stroke-40"),sQuery(id+"F2.wireOp",EDGE,"fcba4419-a2ee-464f-be9d-58f11bf3418b.sketch_text.stroke-41"),sQuery(id+"F2.wireOp",EDGE,"fcba4419-a2ee-464f-be9d-58f11bf3418b.sketch_text.stroke-42"),sQuery(id+"F2.wireOp",EDGE,"fcba4419-a2ee-464f-be9d-58f11bf3418b.sketch_text.stroke-43"),sQuery(id+"F2.wireOp",EDGE,"fcba4419-a2ee-464f-be9d-58f11bf3418b.sketch_text.stroke-44"),sQuery(id+"F2.wireOp",EDGE,"fcba4419-a2ee-464f-be9d-58f11bf3418b.sketch_text.stroke-45"),sQuery(id+"F2.wireOp",EDGE,"fcba4419-a2ee-464f-be9d-58f11bf3418b.sketch_text.stroke-46"),sQuery(id+"F2.wireOp",EDGE,"fcba4419-a2ee-464f-be9d-58f11bf3418b.sketch_text.stroke-47"),sQuery(id+"F2.wireOp",EDGE,"fcba4419-a2ee-464f-be9d-58f11bf3418b.sketch_text.stroke-48"),sQuery(id+"F2.wireOp",EDGE,"fcba4419-a2ee-464f-be9d-58f11bf3418b.sketch_text.stroke-49"),sQuery(id+"F2.wireOp",EDGE,"fcba4419-a2ee-464f-be9d-58f11bf3418b.sketch_text.stroke-50"),sQuery(id+"F2.wireOp",EDGE,"fcba4419-a2ee-464f-be9d-58f11bf3418b.sketch_text.stroke-51"),sQuery(id+"F2.wireOp",EDGE,"fcba4419-a2ee-464f-be9d-58f11bf3418b.sketch_text.stroke-52"),sQuery(id+"F2.wireOp",EDGE,"fcba4419-a2ee-464f-be9d-58f11bf3418b.sketch_text.stroke-53"),sQuery(id+"F2.wireOp",EDGE,"fcba4419-a2ee-464f-be9d-58f11bf3418b.sketch_text.stroke-54"),sQuery(id+"F2.wireOp",EDGE,"fcba4419-a2ee-464f-be9d-58f11bf3418b.sketch_text.stroke-55"),sQuery(id+"F2.wireOp",EDGE,"fcba4419-a2ee-464f-be9d-58f11bf3418b.sketch_text.stroke-56"),sQuery(id+"F2.wireOp",EDGE,"fcba4419-a2ee-464f-be9d-58f11bf3418b.sketch_text.stroke-57"),sQuery(id+"F2.wireOp",EDGE,"fcba4419-a2ee-464f-be9d-58f11bf3418b.sketch_text.stroke-58"),sQuery(id+"F2.wireOp",EDGE,"fcba4419-a2ee-464f-be9d-58f11bf3418b.sketch_text.stroke-59"),sQuery(id+"F2.wireOp",EDGE,"fcba4419-a2ee-464f-be9d-58f11bf3418b.sketch_text.stroke-60"),sQuery(id+"F2.wireOp",EDGE,"fcba4419-a2ee-464f-be9d-58f11bf3418b.sketch_text.stroke-61"),sQuery(id+"F2.wireOp",EDGE,"fcba4419-a2ee-464f-be9d-58f11bf3418b.sketch_text.stroke-62"),sQuery(id+"F2.wireOp",EDGE,"fcba4419-a2ee-464f-be9d-58f11bf3418b.sketch_text.stroke-63"),sQuery(id+"F2.wireOp",EDGE,"fcba4419-a2ee-464f-be9d-58f11bf3418b.sketch_text.stroke-64"),sQuery(id+"F2.wireOp",EDGE,"fcba4419-a2ee-464f-be9d-58f11bf3418b.sketch_text.stroke-65"),sQuery(id+"F2.wireOp",EDGE,"fcba4419-a2ee-464f-be9d-58f11bf3418b.sketch_text.stroke-66"),sQuery(id+"F2.wireOp",EDGE,"fcba4419-a2ee-464f-be9d-58f11bf3418b.sketch_text.stroke-67"),sQuery(id+"F2.wireOp",EDGE,"fcba4419-a2ee-464f-be9d-58f11bf3418b.sketch_text.stroke-68"),sQuery(id+"F2.wireOp",EDGE,"fcba4419-a2ee-464f-be9d-58f11bf3418b.sketch_text.stroke-69"),sQuery(id+"F2.wireOp",EDGE,"fcba4419-a2ee-464f-be9d-58f11bf3418b.sketch_text.stroke-70"),sQuery(id+"F2.wireOp",EDGE,"fcba4419-a2ee-464f-be9d-58f11bf3418b.sketch_text.stroke-71"),sQuery(id+"F2.wireOp",EDGE,"fcba4419-a2ee-464f-be9d-58f11bf3418b.sketch_text.stroke-72"),sQuery(id+"F2.wireOp",EDGE,"fcba4419-a2ee-464f-be9d-58f11bf3418b.sketch_text.stroke-73"),sQuery(id+"F2.wireOp",EDGE,"fcba4419-a2ee-464f-be9d-58f11bf3418b.sketch_text.stroke-74"),sQuery(id+"F2.wireOp",EDGE,"fcba4419-a2ee-464f-be9d-58f11bf3418b.sketch_text.stroke-75"),sQuery(id+"F2.wireOp",EDGE,"fcba4419-a2ee-464f-be9d-58f11bf3418b.sketch_text.stroke-76"),sQuery(id+"F2.wireOp",EDGE,"fcba4419-a2ee-464f-be9d-58f11bf3418b.sketch_text.stroke-77"),sQuery(id+"F2.wireOp",EDGE,"fcba4419-a2ee-464f-be9d-58f11bf3418b.sketch_text.stroke-78"),sQuery(id+"F2.wireOp",EDGE,"fcba4419-a2ee-464f-be9d-58f11bf3418b.sketch_text.stroke-79"),sQuery(id+"F2.wireOp",EDGE,"fcba4419-a2ee-464f-be9d-58f11bf3418b.sketch_text.stroke-80"),sQuery(id+"F2.wireOp",EDGE,"fcba4419-a2ee-464f-be9d-58f11bf3418b.sketch_text.stroke-81"),sQuery(id+"F2.wireOp",EDGE,"fcba4419-a2ee-464f-be9d-58f11bf3418b.sketch_text.stroke-82"),sQuery(id+"F2.wireOp",EDGE,"fcba4419-a2ee-464f-be9d-58f11bf3418b.sketch_text.stroke-83"),sQuery(id+"F2.wireOp",EDGE,"fcba4419-a2ee-464f-be9d-58f11bf3418b.sketch_text.stroke-84"),sQuery(id+"F2.wireOp",EDGE,"fcba4419-a2ee-464f-be9d-58f11bf3418b.sketch_text.stroke-85"),sQuery(id+"F2.wireOp",EDGE,"fcba4419-a2ee-464f-be9d-58f11bf3418b.sketch_text.stroke-86"),sQuery(id+"F2.wireOp",EDGE,"fcba4419-a2ee-464f-be9d-58f11bf3418b.sketch_text.stroke-87"),sQuery(id+"F2.wireOp",EDGE,"fcba4419-a2ee-464f-be9d-58f11bf3418b.sketch_text.stroke-88"),sQuery(id+"F2.wireOp",EDGE,"fcba4419-a2ee-464f-be9d-58f11bf3418b.sketch_text.stroke-89"),sQuery(id+"F2.wireOp",EDGE,"fcba4419-a2ee-464f-be9d-58f11bf3418b.sketch_text.stroke-90"),sQuery(id+"F2.wireOp",EDGE,"fcba4419-a2ee-464f-be9d-58f11bf3418b.sketch_text.stroke-91"),sQuery(id+"F2.wireOp",EDGE,"fcba4419-a2ee-464f-be9d-58f11bf3418b.sketch_text.stroke-92"),sQuery(id+"F2.wireOp",EDGE,"fcba4419-a2ee-464f-be9d-58f11bf3418b.sketch_text.stroke-93"),sQuery(id+"F2.wireOp",EDGE,"fcba4419-a2ee-464f-be9d-58f11bf3418b.sketch_text.stroke-94"),sQuery(id+"F2.wireOp",EDGE,"fcba4419-a2ee-464f-be9d-58f11bf3418b.sketch_text.stroke-95"),sQuery(id+"F2.wireOp",EDGE,"fcba4419-a2ee-464f-be9d-58f11bf3418b.sketch_text.stroke-96"),sQuery(id+"F2.wireOp",EDGE,"fcba4419-a2ee-464f-be9d-58f11bf3418b.sketch_text.stroke-97"),sQuery(id+"F2.wireOp",EDGE,"fcba4419-a2ee-464f-be9d-58f11bf3418b.sketch_text.stroke-98"),sQuery(id+"F2.wireOp",EDGE,"fcba4419-a2ee-464f-be9d-58f11bf3418b.sketch_text.stroke-99"),sQuery(id+"F2.wireOp",EDGE,"fcba4419-a2ee-464f-be9d-58f11bf3418b.sketch_text.stroke-100"),sQuery(id+"F2.wireOp",EDGE,"fcba4419-a2ee-464f-be9d-58f11bf3418b.sketch_text.stroke-101"),sQuery(id+"F2.wireOp",EDGE,"fcba4419-a2ee-464f-be9d-58f11bf3418b.sketch_text.stroke-102"),sQuery(id+"F2.wireOp",EDGE,"fcba4419-a2ee-464f-be9d-58f11bf3418b.sketch_text.stroke-103"),sQuery(id+"F2.wireOp",EDGE,"fcba4419-a2ee-464f-be9d-58f11bf3418b.sketch_text.stroke-104"),sQuery(id+"F2.wireOp",EDGE,"fcba4419-a2ee-464f-be9d-58f11bf3418b.sketch_text.stroke-105"),sQuery(id+"F2.wireOp",EDGE,"fcba4419-a2ee-464f-be9d-58f11bf3418b.sketch_text.stroke-106"),sQuery(id+"F2.wireOp",EDGE,"fcba4419-a2ee-464f-be9d-58f11bf3418b.sketch_text.stroke-107"),sQuery(id+"F2.wireOp",EDGE,"fcba4419-a2ee-464f-be9d-58f11bf3418b.sketch_text.stroke-108"),sQuery(id+"F2.wireOp",EDGE,"fcba4419-a2ee-464f-be9d-58f11bf3418b.sketch_text.stroke-109"),sQuery(id+"F2.wireOp",EDGE,"fcba4419-a2ee-464f-be9d-58f11bf3418b.sketch_text.stroke-110"),sQuery(id+"F2.wireOp",EDGE,"fcba4419-a2ee-464f-be9d-58f11bf3418b.sketch_text.stroke-111"),sQuery(id+"F2.wireOp",EDGE,"fcba4419-a2ee-464f-be9d-58f11bf3418b.sketch_text.stroke-112"),sQuery(id+"F2.wireOp",EDGE,"fcba4419-a2ee-464f-be9d-58f11bf3418b.sketch_text.stroke-113"),sQuery(id+"F2.wireOp",EDGE,"fcba4419-a2ee-464f-be9d-58f11bf3418b.sketch_text.stroke-114"),sQuery(id+"F2.wireOp",EDGE,"fcba4419-a2ee-464f-be9d-58f11bf3418b.sketch_text.stroke-115"),sQuery(id+"F2.wireOp",EDGE,"fcba4419-a2ee-464f-be9d-58f11bf3418b.sketch_text.stroke-116"),sQuery(id+"F2.wireOp",EDGE,"fcba4419-a2ee-464f-be9d-58f11bf3418b.sketch_text.stroke-117"),sQuery(id+"F2.wireOp",EDGE,"fcba4419-a2ee-464f-be9d-58f11bf3418b.sketch_text.stroke-118"),sQuery(id+"F2.wireOp",EDGE,"fcba4419-a2ee-464f-be9d-58f11bf3418b.sketch_text.stroke-119"),sQuery(id+"F2.wireOp",EDGE,"fcba4419-a2ee-464f-be9d-58f11bf3418b.sketch_text.stroke-120"),sQuery(id+"F2.wireOp",EDGE,"fcba4419-a2ee-464f-be9d-58f11bf3418b.sketch_text.stroke-121"),sQuery(id+"F2.wireOp",EDGE,"fcba4419-a2ee-464f-be9d-58f11bf3418b.sketch_text.stroke-122"),sQuery(id+"F2.wireOp",EDGE,"fcba4419-a2ee-464f-be9d-58f11bf3418b.sketch_text.stroke-123"),sQuery(id+"F2.wireOp",EDGE,"fcba4419-a2ee-464f-be9d-58f11bf3418b.sketch_text.stroke-124"),sQuery(id+"F2.wireOp",EDGE,"fcba4419-a2ee-464f-be9d-58f11bf3418b.sketch_text.stroke-125"),sQuery(id+"F2.wireOp",EDGE,"fcba4419-a2ee-464f-be9d-58f11bf3418b.sketch_text.stroke-126"),sQuery(id+"F2.wireOp",EDGE,"fcba4419-a2ee-464f-be9d-58f11bf3418b.sketch_text.stroke-127"),sQuery(id+"F2.wireOp",EDGE,"fcba4419-a2ee-464f-be9d-58f11bf3418b.sketch_text.stroke-128"),sQuery(id+"F2.wireOp",EDGE,"fcba4419-a2ee-464f-be9d-58f11bf3418b.sketch_text.stroke-129"),sQuery(id+"F2.wireOp",EDGE,"fcba4419-a2ee-464f-be9d-58f11bf3418b.sketch_text.stroke-130"),sQuery(id+"F2.wireOp",EDGE,"fcba4419-a2ee-464f-be9d-58f11bf3418b.sketch_text.stroke-131"),sQuery(id+"F2.wireOp",EDGE,"fcba4419-a2ee-464f-be9d-58f11bf3418b.sketch_text.stroke-132"),sQuery(id+"F2.wireOp",EDGE,"fcba4419-a2ee-464f-be9d-58f11bf3418b.sketch_text.stroke-133"),sQuery(id+"F2.wireOp",EDGE,"fcba4419-a2ee-464f-be9d-58f11bf3418b.sketch_text.stroke-134"),sQuery(id+"F2.wireOp",EDGE,"fcba4419-a2ee-464f-be9d-58f11bf3418b.sketch_text.stroke-135"),sQuery(id+"F2.wireOp",EDGE,"fcba4419-a2ee-464f-be9d-58f11bf3418b.sketch_text.stroke-136"),sQuery(id+"F2.wireOp",EDGE,"fcba4419-a2ee-464f-be9d-58f11bf3418b.sketch_text.stroke-137"),sQuery(id+"F2.wireOp",EDGE,"fcba4419-a2ee-464f-be9d-58f11bf3418b.sketch_text.stroke-138"),sQuery(id+"F2.wireOp",EDGE,"fcba4419-a2ee-464f-be9d-58f11bf3418b.sketch_text.stroke-139"),sQuery(id+"F2.wireOp",EDGE,"fcba4419-a2ee-464f-be9d-58f11bf3418b.sketch_text.stroke-140"),sQuery(id+"F2.wireOp",EDGE,"fcba4419-a2ee-464f-be9d-58f11bf3418b.sketch_text.stroke-141"),sQuery(id+"F2.wireOp",EDGE,"fcba4419-a2ee-464f-be9d-58f11bf3418b.sketch_text.stroke-142"),sQuery(id+"F2.wireOp",EDGE,"fcba4419-a2ee-464f-be9d-58f11bf3418b.sketch_text.stroke-143"),sQuery(id+"F2.wireOp",EDGE,"fcba4419-a2ee-464f-be9d-58f11bf3418b.sketch_text.stroke-144"),sQuery(id+"F2.wireOp",EDGE,"fcba4419-a2ee-464f-be9d-58f11bf3418b.sketch_text.stroke-145"),sQuery(id+"F2.wireOp",EDGE,"fcba4419-a2ee-464f-be9d-58f11bf3418b.sketch_text.stroke-146"),sQuery(id+"F2.wireOp",EDGE,"fcba4419-a2ee-464f-be9d-58f11bf3418b.sketch_text.stroke-147"),sQuery(id+"F2.wireOp",EDGE,"fcba4419-a2ee-464f-be9d-58f11bf3418b.sketch_text.stroke-148"),sQuery(id+"F2.wireOp",EDGE,"fcba4419-a2ee-464f-be9d-58f11bf3418b.sketch_text.stroke-149"),sQuery(id+"F2.wireOp",EDGE,"fcba4419-a2ee-464f-be9d-58f11bf3418b.sketch_text.stroke-150"),sQuery(id+"F2.wireOp",EDGE,"fcba4419-a2ee-464f-be9d-58f11bf3418b.sketch_text.stroke-151"),sQuery(id+"F2.wireOp",EDGE,"fcba4419-a2ee-464f-be9d-58f11bf3418b.sketch_text.stroke-152"),sQuery(id+"F2.wireOp",EDGE,"fcba4419-a2ee-464f-be9d-58f11bf3418b.sketch_text.stroke-153"),sQuery(id+"F2.wireOp",EDGE,"fcba4419-a2ee-464f-be9d-58f11bf3418b.sketch_text.stroke-154"),sQuery(id+"F2.wireOp",EDGE,"fcba4419-a2ee-464f-be9d-58f11bf3418b.sketch_text.stroke-155"),sQuery(id+"F2.wireOp",EDGE,"fcba4419-a2ee-464f-be9d-58f11bf3418b.sketch_text.stroke-156"),sQuery(id+"F2.wireOp",EDGE,"fcba4419-a2ee-464f-be9d-58f11bf3418b.sketch_text.stroke-157"),sQuery(id+"F2.wireOp",EDGE,"fcba4419-a2ee-464f-be9d-58f11bf3418b.sketch_text.stroke-158"),sQuery(id+"F2.wireOp",EDGE,"fcba4419-a2ee-464f-be9d-58f11bf3418b.sketch_text.stroke-159"),sQuery(id+"F2.wireOp",EDGE,"fcba4419-a2ee-464f-be9d-58f11bf3418b.sketch_text.stroke-160"),sQuery(id+"F2.wireOp",EDGE,"fcba4419-a2ee-464f-be9d-58f11bf3418b.sketch_text.stroke-161"),sQuery(id+"F2.wireOp",EDGE,"fcba4419-a2ee-464f-be9d-58f11bf3418b.sketch_text.stroke-162"),sQuery(id+"F2.wireOp",EDGE,"fcba4419-a2ee-464f-be9d-58f11bf3418b.sketch_text.stroke-163"),sQuery(id+"F2.wireOp",EDGE,"fcba4419-a2ee-464f-be9d-58f11bf3418b.sketch_text.stroke-164"),sQuery(id+"F2.wireOp",EDGE,"fcba4419-a2ee-464f-be9d-58f11bf3418b.sketch_text.stroke-165"),sQuery(id+"F2.wireOp",EDGE,"fcba4419-a2ee-464f-be9d-58f11bf3418b.sketch_text.stroke-166"),sQuery(id+"F2.wireOp",EDGE,"fcba4419-a2ee-464f-be9d-58f11bf3418b.sketch_text.stroke-167"),sQuery(id+"F2.wireOp",EDGE,"fcba4419-a2ee-464f-be9d-58f11bf3418b.sketch_text.stroke-168"),sQuery(id+"F2.wireOp",EDGE,"fcba4419-a2ee-464f-be9d-58f11bf3418b.sketch_text.stroke-169"),sQuery(id+"F2.wireOp",EDGE,"fcba4419-a2ee-464f-be9d-58f11bf3418b.sketch_text.stroke-170"),sQuery(id+"F2.wireOp",EDGE,"fcba4419-a2ee-464f-be9d-58f11bf3418b.sketch_text.stroke-171"),sQuery(id+"F2.wireOp",EDGE,"fcba4419-a2ee-464f-be9d-58f11bf3418b.sketch_text.stroke-172"),sQuery(id+"F2.wireOp",EDGE,"fcba4419-a2ee-464f-be9d-58f11bf3418b.sketch_text.stroke-173"),sQuery(id+"FHMxAyK4CFUKdhS_1.wireOp",EDGE,"1cb9c079-ea9b-4899-8069-e0e3048e911d.sketch_text.stroke-0"),sQuery(id+"FHMxAyK4CFUKdhS_1.wireOp",EDGE,"1cb9c079-ea9b-4899-8069-e0e3048e911d.sketch_text.stroke-1"),sQuery(id+"FHMxAyK4CFUKdhS_1.wireOp",EDGE,"1cb9c079-ea9b-4899-8069-e0e3048e911d.sketch_text.stroke-2"),sQuery(id+"FHMxAyK4CFUKdhS_1.wireOp",EDGE,"1cb9c079-ea9b-4899-8069-e0e3048e911d.sketch_text.stroke-3"),sQuery(id+"FHMxAyK4CFUKdhS_1.wireOp",EDGE,"1cb9c079-ea9b-4899-8069-e0e3048e911d.sketch_text.stroke-4"),sQuery(id+"FHMxAyK4CFUKdhS_1.wireOp",EDGE,"1cb9c079-ea9b-4899-8069-e0e3048e911d.sketch_text.stroke-5"),sQuery(id+"FHMxAyK4CFUKdhS_1.wireOp",EDGE,"1cb9c079-ea9b-4899-8069-e0e3048e911d.sketch_text.stroke-6"),sQuery(id+"FHMxAyK4CFUKdhS_1.wireOp",EDGE,"1cb9c079-ea9b-4899-8069-e0e3048e911d.sketch_text.stroke-7"),sQuery(id+"FHMxAyK4CFUKdhS_1.wireOp",EDGE,"1cb9c079-ea9b-4899-8069-e0e3048e911d.sketch_text.stroke-8"),sQuery(id+"FHMxAyK4CFUKdhS_1.wireOp",EDGE,"1cb9c079-ea9b-4899-8069-e0e3048e911d.sketch_text.stroke-9"),sQuery(id+"FHMxAyK4CFUKdhS_1.wireOp",EDGE,"1cb9c079-ea9b-4899-8069-e0e3048e911d.sketch_text.stroke-10"),sQuery(id+"FHMxAyK4CFUKdhS_1.wireOp",EDGE,"1cb9c079-ea9b-4899-8069-e0e3048e911d.sketch_text.stroke-11"),sQuery(id+"FHMxAyK4CFUKdhS_1.wireOp",EDGE,"1cb9c079-ea9b-4899-8069-e0e3048e911d.sketch_text.stroke-12"),sQuery(id+"FHMxAyK4CFUKdhS_1.wireOp",EDGE,"1cb9c079-ea9b-4899-8069-e0e3048e911d.sketch_text.stroke-13"),sQuery(id+"FHMxAyK4CFUKdhS_1.wireOp",EDGE,"1cb9c079-ea9b-4899-8069-e0e3048e911d.sketch_text.stroke-14"),sQuery(id+"FHMxAyK4CFUKdhS_1.wireOp",EDGE,"1cb9c079-ea9b-4899-8069-e0e3048e911d.sketch_text.stroke-15"),sQuery(id+"FHMxAyK4CFUKdhS_1.wireOp",EDGE,"1cb9c079-ea9b-4899-8069-e0e3048e911d.sketch_text.stroke-16"),sQuery(id+"FHMxAyK4CFUKdhS_1.wireOp",EDGE,"1cb9c079-ea9b-4899-8069-e0e3048e911d.sketch_text.stroke-17"),sQuery(id+"FHMxAyK4CFUKdhS_1.wireOp",EDGE,"1cb9c079-ea9b-4899-8069-e0e3048e911d.sketch_text.stroke-18"),sQuery(id+"FHMxAyK4CFUKdhS_1.wireOp",EDGE,"1cb9c079-ea9b-4899-8069-e0e3048e911d.sketch_text.stroke-19"),sQuery(id+"FHMxAyK4CFUKdhS_1.wireOp",EDGE,"1cb9c079-ea9b-4899-8069-e0e3048e911d.sketch_text.stroke-20"),sQuery(id+"FHMxAyK4CFUKdhS_1.wireOp",EDGE,"1cb9c079-ea9b-4899-8069-e0e3048e911d.sketch_text.stroke-21"),sQuery(id+"FHMxAyK4CFUKdhS_1.wireOp",EDGE,"1cb9c079-ea9b-4899-8069-e0e3048e911d.sketch_text.stroke-22"),sQuery(id+"FHMxAyK4CFUKdhS_1.wireOp",EDGE,"1cb9c079-ea9b-4899-8069-e0e3048e911d.sketch_text.stroke-23"),sQuery(id+"FHMxAyK4CFUKdhS_1.wireOp",EDGE,"1cb9c079-ea9b-4899-8069-e0e3048e911d.sketch_text.stroke-24"),sQuery(id+"FHMxAyK4CFUKdhS_1.wireOp",EDGE,"1cb9c079-ea9b-4899-8069-e0e3048e911d.sketch_text.stroke-25"),sQuery(id+"FHMxAyK4CFUKdhS_1.wireOp",EDGE,"1cb9c079-ea9b-4899-8069-e0e3048e911d.sketch_text.stroke-26"),sQuery(id+"FHMxAyK4CFUKdhS_1.wireOp",EDGE,"1cb9c079-ea9b-4899-8069-e0e3048e911d.sketch_text.stroke-27"),sQuery(id+"FHMxAyK4CFUKdhS_1.wireOp",EDGE,"1cb9c079-ea9b-4899-8069-e0e3048e911d.sketch_text.stroke-28"),sQuery(id+"FHMxAyK4CFUKdhS_1.wireOp",EDGE,"1cb9c079-ea9b-4899-8069-e0e3048e911d.sketch_text.stroke-29"),sQuery(id+"FHMxAyK4CFUKdhS_1.wireOp",EDGE,"1cb9c079-ea9b-4899-8069-e0e3048e911d.sketch_text.stroke-30"),sQuery(id+"FHMxAyK4CFUKdhS_1.wireOp",EDGE,"1cb9c079-ea9b-4899-8069-e0e3048e911d.sketch_text.stroke-31"),sQuery(id+"FHMxAyK4CFUKdhS_1.wireOp",EDGE,"1cb9c079-ea9b-4899-8069-e0e3048e911d.sketch_text.stroke-32"),sQuery(id+"FHMxAyK4CFUKdhS_1.wireOp",EDGE,"1cb9c079-ea9b-4899-8069-e0e3048e911d.sketch_text.stroke-33"),sQuery(id+"FHMxAyK4CFUKdhS_1.wireOp",EDGE,"1cb9c079-ea9b-4899-8069-e0e3048e911d.sketch_text.stroke-34"),sQuery(id+"FHMxAyK4CFUKdhS_1.wireOp",EDGE,"1cb9c079-ea9b-4899-8069-e0e3048e911d.sketch_text.stroke-35"),sQuery(id+"FHMxAyK4CFUKdhS_1.wireOp",EDGE,"1cb9c079-ea9b-4899-8069-e0e3048e911d.sketch_text.stroke-36"),sQuery(id+"FHMxAyK4CFUKdhS_1.wireOp",EDGE,"1cb9c079-ea9b-4899-8069-e0e3048e911d.sketch_text.stroke-37"),sQuery(id+"FHMxAyK4CFUKdhS_1.wireOp",EDGE,"1cb9c079-ea9b-4899-8069-e0e3048e911d.sketch_text.stroke-38"),sQuery(id+"FHMxAyK4CFUKdhS_1.wireOp",EDGE,"1cb9c079-ea9b-4899-8069-e0e3048e911d.sketch_text.stroke-39"),sQuery(id+"FHMxAyK4CFUKdhS_1.wireOp",EDGE,"1cb9c079-ea9b-4899-8069-e0e3048e911d.sketch_text.stroke-40"),sQuery(id+"FHMxAyK4CFUKdhS_1.wireOp",EDGE,"1cb9c079-ea9b-4899-8069-e0e3048e911d.sketch_text.stroke-41"),sQuery(id+"FHMxAyK4CFUKdhS_1.wireOp",EDGE,"1cb9c079-ea9b-4899-8069-e0e3048e911d.sketch_text.stroke-42"),sQuery(id+"FHMxAyK4CFUKdhS_1.wireOp",EDGE,"1cb9c079-ea9b-4899-8069-e0e3048e911d.sketch_text.stroke-43"),sQuery(id+"FHMxAyK4CFUKdhS_1.wireOp",EDGE,"1cb9c079-ea9b-4899-8069-e0e3048e911d.sketch_text.stroke-44"),sQuery(id+"FHMxAyK4CFUKdhS_1.wireOp",EDGE,"1cb9c079-ea9b-4899-8069-e0e3048e911d.sketch_text.stroke-45"),sQuery(id+"FHMxAyK4CFUKdhS_1.wireOp",EDGE,"1cb9c079-ea9b-4899-8069-e0e3048e911d.sketch_text.stroke-46"),sQuery(id+"FHMxAyK4CFUKdhS_1.wireOp",EDGE,"1cb9c079-ea9b-4899-8069-e0e3048e911d.sketch_text.stroke-47"),sQuery(id+"FHMxAyK4CFUKdhS_1.wireOp",EDGE,"1cb9c079-ea9b-4899-8069-e0e3048e911d.sketch_text.stroke-48"),sQuery(id+"FHMxAyK4CFUKdhS_1.wireOp",EDGE,"1cb9c079-ea9b-4899-8069-e0e3048e911d.sketch_text.stroke-49"),sQuery(id+"FHMxAyK4CFUKdhS_1.wireOp",EDGE,"1cb9c079-ea9b-4899-8069-e0e3048e911d.sketch_text.stroke-50"),sQuery(id+"FHMxAyK4CFUKdhS_1.wireOp",EDGE,"1cb9c079-ea9b-4899-8069-e0e3048e911d.sketch_text.stroke-51"),sQuery(id+"FHMxAyK4CFUKdhS_1.wireOp",EDGE,"1cb9c079-ea9b-4899-8069-e0e3048e911d.sketch_text.stroke-52"),sQuery(id+"FHMxAyK4CFUKdhS_1.wireOp",EDGE,"1cb9c079-ea9b-4899-8069-e0e3048e911d.sketch_text.stroke-53"),sQuery(id+"FHMxAyK4CFUKdhS_1.wireOp",EDGE,"1cb9c079-ea9b-4899-8069-e0e3048e911d.sketch_text.stroke-54"),sQuery(id+"FHMxAyK4CFUKdhS_1.wireOp",EDGE,"1cb9c079-ea9b-4899-8069-e0e3048e911d.sketch_text.stroke-55"),sQuery(id+"FHMxAyK4CFUKdhS_1.wireOp",EDGE,"1cb9c079-ea9b-4899-8069-e0e3048e911d.sketch_text.stroke-56"),sQuery(id+"FHMxAyK4CFUKdhS_1.wireOp",EDGE,"1cb9c079-ea9b-4899-8069-e0e3048e911d.sketch_text.stroke-57"),sQuery(id+"FHMxAyK4CFUKdhS_1.wireOp",EDGE,"1cb9c079-ea9b-4899-8069-e0e3048e911d.sketch_text.stroke-58"),sQuery(id+"FHMxAyK4CFUKdhS_1.wireOp",EDGE,"1cb9c079-ea9b-4899-8069-e0e3048e911d.sketch_text.stroke-59"),sQuery(id+"FHMxAyK4CFUKdhS_1.wireOp",EDGE,"1cb9c079-ea9b-4899-8069-e0e3048e911d.sketch_text.stroke-60"),sQuery(id+"FHMxAyK4CFUKdhS_1.wireOp",EDGE,"1cb9c079-ea9b-4899-8069-e0e3048e911d.sketch_text.stroke-61"),sQuery(id+"FHMxAyK4CFUKdhS_1.wireOp",EDGE,"1cb9c079-ea9b-4899-8069-e0e3048e911d.sketch_text.stroke-62"),sQuery(id+"FHMxAyK4CFUKdhS_1.wireOp",EDGE,"1cb9c079-ea9b-4899-8069-e0e3048e911d.sketch_text.stroke-71"),sQuery(id+"FHMxAyK4CFUKdhS_1.wireOp",EDGE,"1cb9c079-ea9b-4899-8069-e0e3048e911d.sketch_text.stroke-72"),sQuery(id+"FHMxAyK4CFUKdhS_1.wireOp",EDGE,"1cb9c079-ea9b-4899-8069-e0e3048e911d.sketch_text.stroke-73"),sQuery(id+"FHMxAyK4CFUKdhS_1.wireOp",EDGE,"1cb9c079-ea9b-4899-8069-e0e3048e911d.sketch_text.stroke-74"),sQuery(id+"FHMxAyK4CFUKdhS_1.wireOp",EDGE,"1cb9c079-ea9b-4899-8069-e0e3048e911d.sketch_text.stroke-75"),sQuery(id+"FHMxAyK4CFUKdhS_1.wireOp",EDGE,"1cb9c079-ea9b-4899-8069-e0e3048e911d.sketch_text.stroke-76"),sQuery(id+"FHMxAyK4CFUKdhS_1.wireOp",EDGE,"1cb9c079-ea9b-4899-8069-e0e3048e911d.sketch_text.stroke-77"),sQuery(id+"FHMxAyK4CFUKdhS_1.wireOp",EDGE,"1cb9c079-ea9b-4899-8069-e0e3048e911d.sketch_text.stroke-78"),sQuery(id+"FHMxAyK4CFUKdhS_1.wireOp",EDGE,"1cb9c079-ea9b-4899-8069-e0e3048e911d.sketch_text.stroke-79"),sQuery(id+"FHMxAyK4CFUKdhS_1.wireOp",EDGE,"1cb9c079-ea9b-4899-8069-e0e3048e911d.sketch_text.stroke-80"),sQuery(id+"FHMxAyK4CFUKdhS_1.wireOp",EDGE,"1cb9c079-ea9b-4899-8069-e0e3048e911d.sketch_text.stroke-81"),sQuery(id+"FHMxAyK4CFUKdhS_1.wireOp",EDGE,"1cb9c079-ea9b-4899-8069-e0e3048e911d.sketch_text.stroke-82"),sQuery(id+"FHMxAyK4CFUKdhS_1.wireOp",EDGE,"1cb9c079-ea9b-4899-8069-e0e3048e911d.sketch_text.stroke-83"),sQuery(id+"FHMxAyK4CFUKdhS_1.wireOp",EDGE,"1cb9c079-ea9b-4899-8069-e0e3048e911d.sketch_text.stroke-84"),sQuery(id+"FHMxAyK4CFUKdhS_1.wireOp",EDGE,"1cb9c079-ea9b-4899-8069-e0e3048e911d.sketch_text.stroke-85"),sQuery(id+"FHMxAyK4CFUKdhS_1.wireOp",EDGE,"1cb9c079-ea9b-4899-8069-e0e3048e911d.sketch_text.stroke-86"),sQuery(id+"FHMxAyK4CFUKdhS_1.wireOp",EDGE,"1cb9c079-ea9b-4899-8069-e0e3048e911d.sketch_text.stroke-87"),sQuery(id+"FHMxAyK4CFUKdhS_1.wireOp",EDGE,"1cb9c079-ea9b-4899-8069-e0e3048e911d.sketch_text.stroke-88"),sQuery(id+"FHMxAyK4CFUKdhS_1.wireOp",EDGE,"1cb9c079-ea9b-4899-8069-e0e3048e911d.sketch_text.stroke-89"),sQuery(id+"FHMxAyK4CFUKdhS_1.wireOp",EDGE,"1cb9c079-ea9b-4899-8069-e0e3048e911d.sketch_text.stroke-90"),sQuery(id+"FHMxAyK4CFUKdhS_1.wireOp",EDGE,"1cb9c079-ea9b-4899-8069-e0e3048e911d.sketch_text.stroke-91"),sQuery(id+"FHMxAyK4CFUKdhS_1.wireOp",EDGE,"1cb9c079-ea9b-4899-8069-e0e3048e911d.sketch_text.stroke-92"),sQuery(id+"FHMxAyK4CFUKdhS_1.wireOp",EDGE,"1cb9c079-ea9b-4899-8069-e0e3048e911d.sketch_text.stroke-93"),sQuery(id+"FHMxAyK4CFUKdhS_1.wireOp",EDGE,"1cb9c079-ea9b-4899-8069-e0e3048e911d.sketch_text.stroke-94"),sQuery(id+"FHMxAyK4CFUKdhS_1.wireOp",EDGE,"1cb9c079-ea9b-4899-8069-e0e3048e911d.sketch_text.stroke-95"),sQuery(id+"FHMxAyK4CFUKdhS_1.wireOp",EDGE,"1cb9c079-ea9b-4899-8069-e0e3048e911d.sketch_text.stroke-96"),sQuery(id+"FHMxAyK4CFUKdhS_1.wireOp",EDGE,"1cb9c079-ea9b-4899-8069-e0e3048e911d.sketch_text.stroke-97"),sQuery(id+"FHMxAyK4CFUKdhS_1.wireOp",EDGE,"1cb9c079-ea9b-4899-8069-e0e3048e911d.sketch_text.stroke-103"),sQuery(id+"FHMxAyK4CFUKdhS_1.wireOp",EDGE,"1cb9c079-ea9b-4899-8069-e0e3048e911d.sketch_text.stroke-104"),sQuery(id+"FHMxAyK4CFUKdhS_1.wireOp",EDGE,"1cb9c079-ea9b-4899-8069-e0e3048e911d.sketch_text.stroke-105"),sQuery(id+"FHMxAyK4CFUKdhS_1.wireOp",EDGE,"1cb9c079-ea9b-4899-8069-e0e3048e911d.sketch_text.stroke-106"),sQuery(id+"FHMxAyK4CFUKdhS_1.wireOp",EDGE,"1cb9c079-ea9b-4899-8069-e0e3048e911d.sketch_text.stroke-107"),sQuery(id+"FHMxAyK4CFUKdhS_1.wireOp",EDGE,"1cb9c079-ea9b-4899-8069-e0e3048e911d.sketch_text.stroke-108"),sQuery(id+"FHMxAyK4CFUKdhS_1.wireOp",EDGE,"1cb9c079-ea9b-4899-8069-e0e3048e911d.sketch_text.stroke-109"),sQuery(id+"FHMxAyK4CFUKdhS_1.wireOp",EDGE,"1cb9c079-ea9b-4899-8069-e0e3048e911d.sketch_text.stroke-110"),sQuery(id+"FHMxAyK4CFUKdhS_1.wireOp",EDGE,"1cb9c079-ea9b-4899-8069-e0e3048e911d.sketch_text.stroke-111"),sQuery(id+"FHMxAyK4CFUKdhS_1.wireOp",EDGE,"1cb9c079-ea9b-4899-8069-e0e3048e911d.sketch_text.stroke-112"),sQuery(id+"FHMxAyK4CFUKdhS_1.wireOp",EDGE,"1cb9c079-ea9b-4899-8069-e0e3048e911d.sketch_text.stroke-113"),sQuery(id+"FHMxAyK4CFUKdhS_1.wireOp",EDGE,"1cb9c079-ea9b-4899-8069-e0e3048e911d.sketch_text.stroke-114"),sQuery(id+"FHMxAyK4CFUKdhS_1.wireOp",EDGE,"1cb9c079-ea9b-4899-8069-e0e3048e911d.sketch_text.stroke-115"),sQuery(id+"FHMxAyK4CFUKdhS_1.wireOp",EDGE,"1cb9c079-ea9b-4899-8069-e0e3048e911d.sketch_text.stroke-116"),sQuery(id+"FHMxAyK4CFUKdhS_1.wireOp",EDGE,"1cb9c079-ea9b-4899-8069-e0e3048e911d.sketch_text.stroke-117"),sQuery(id+"FHMxAyK4CFUKdhS_1.wireOp",EDGE,"1cb9c079-ea9b-4899-8069-e0e3048e911d.sketch_text.stroke-118"),sQuery(id+"FHMxAyK4CFUKdhS_1.wireOp",EDGE,"1cb9c079-ea9b-4899-8069-e0e3048e911d.sketch_text.stroke-119"),sQuery(id+"FHMxAyK4CFUKdhS_1.wireOp",EDGE,"1cb9c079-ea9b-4899-8069-e0e3048e911d.sketch_text.stroke-120"),sQuery(id+"FHMxAyK4CFUKdhS_1.wireOp",EDGE,"1cb9c079-ea9b-4899-8069-e0e3048e911d.sketch_text.stroke-121"),sQuery(id+"FHMxAyK4CFUKdhS_1.wireOp",EDGE,"1cb9c079-ea9b-4899-8069-e0e3048e911d.sketch_text.stroke-122"),sQuery(id+"FHMxAyK4CFUKdhS_1.wireOp",EDGE,"1cb9c079-ea9b-4899-8069-e0e3048e911d.sketch_text.stroke-123"),sQuery(id+"FHMxAyK4CFUKdhS_1.wireOp",EDGE,"1cb9c079-ea9b-4899-8069-e0e3048e911d.sketch_text.stroke-124"),sQuery(id+"FHMxAyK4CFUKdhS_1.wireOp",EDGE,"1cb9c079-ea9b-4899-8069-e0e3048e911d.sketch_text.stroke-125"),sQuery(id+"FHMxAyK4CFUKdhS_1.wireOp",EDGE,"1cb9c079-ea9b-4899-8069-e0e3048e911d.sketch_text.stroke-126"),sQuery(id+"FHMxAyK4CFUKdhS_1.wireOp",EDGE,"1cb9c079-ea9b-4899-8069-e0e3048e911d.sketch_text.stroke-127"),sQuery(id+"FHMxAyK4CFUKdhS_1.wireOp",EDGE,"1cb9c079-ea9b-4899-8069-e0e3048e911d.sketch_text.stroke-128"),sQuery(id+"FHMxAyK4CFUKdhS_1.wireOp",EDGE,"1cb9c079-ea9b-4899-8069-e0e3048e911d.sketch_text.stroke-129"),sQuery(id+"FHMxAyK4CFUKdhS_1.wireOp",EDGE,"1cb9c079-ea9b-4899-8069-e0e3048e911d.sketch_text.stroke-130"),sQuery(id+"FHMxAyK4CFUKdhS_1.wireOp",EDGE,"1cb9c079-ea9b-4899-8069-e0e3048e911d.sketch_text.stroke-131"),sQuery(id+"FHMxAyK4CFUKdhS_1.wireOp",EDGE,"1cb9c079-ea9b-4899-8069-e0e3048e911d.sketch_text.stroke-132"),sQuery(id+"FHMxAyK4CFUKdhS_1.wireOp",EDGE,"1cb9c079-ea9b-4899-8069-e0e3048e911d.sketch_text.stroke-133"),sQuery(id+"FHMxAyK4CFUKdhS_1.wireOp",EDGE,"1cb9c079-ea9b-4899-8069-e0e3048e911d.sketch_text.stroke-134"),sQuery(id+"FHMxAyK4CFUKdhS_1.wireOp",EDGE,"1cb9c079-ea9b-4899-8069-e0e3048e911d.sketch_text.stroke-135"),sQuery(id+"FHMxAyK4CFUKdhS_1.wireOp",EDGE,"1cb9c079-ea9b-4899-8069-e0e3048e911d.sketch_text.stroke-136"),sQuery(id+"FHMxAyK4CFUKdhS_1.wireOp",EDGE,"1cb9c079-ea9b-4899-8069-e0e3048e911d.sketch_text.stroke-137"),sQuery(id+"FHMxAyK4CFUKdhS_1.wireOp",EDGE,"1cb9c079-ea9b-4899-8069-e0e3048e911d.sketch_text.stroke-138"),sQuery(id+"FHMxAyK4CFUKdhS_1.wireOp",EDGE,"1cb9c079-ea9b-4899-8069-e0e3048e911d.sketch_text.stroke-139"),sQuery(id+"FHMxAyK4CFUKdhS_1.wireOp",EDGE,"1cb9c079-ea9b-4899-8069-e0e3048e911d.sketch_text.stroke-140"),sQuery(id+"FHMxAyK4CFUKdhS_1.wireOp",EDGE,"1cb9c079-ea9b-4899-8069-e0e3048e911d.sketch_text.stroke-141"),sQuery(id+"FHMxAyK4CFUKdhS_1.wireOp",EDGE,"1cb9c079-ea9b-4899-8069-e0e3048e911d.sketch_text.stroke-142"),sQuery(id+"FHMxAyK4CFUKdhS_1.wireOp",EDGE,"1cb9c079-ea9b-4899-8069-e0e3048e911d.sketch_text.stroke-143"),sQuery(id+"FHMxAyK4CFUKdhS_1.wireOp",EDGE,"1cb9c079-ea9b-4899-8069-e0e3048e911d.sketch_text.stroke-144"),sQuery(id+"FHMxAyK4CFUKdhS_1.wireOp",EDGE,"1cb9c079-ea9b-4899-8069-e0e3048e911d.sketch_text.stroke-145"),sQuery(id+"FHMxAyK4CFUKdhS_1.wireOp",EDGE,"1cb9c079-ea9b-4899-8069-e0e3048e911d.sketch_text.stroke-146"),sQuery(id+"FHMxAyK4CFUKdhS_1.wireOp",EDGE,"1cb9c079-ea9b-4899-8069-e0e3048e911d.sketch_text.stroke-147"),sQuery(id+"FHMxAyK4CFUKdhS_1.wireOp",EDGE,"1cb9c079-ea9b-4899-8069-e0e3048e911d.sketch_text.stroke-148"),sQuery(id+"FHMxAyK4CFUKdhS_1.wireOp",EDGE,"1cb9c079-ea9b-4899-8069-e0e3048e911d.sketch_text.stroke-149"),sQuery(id+"FHMxAyK4CFUKdhS_1.wireOp",EDGE,"1cb9c079-ea9b-4899-8069-e0e3048e911d.sketch_text.stroke-150"),sQuery(id+"FHMxAyK4CFUKdhS_1.wireOp",EDGE,"1cb9c079-ea9b-4899-8069-e0e3048e911d.sketch_text.stroke-151"),sQuery(id+"FHMxAyK4CFUKdhS_1.wireOp",EDGE,"1cb9c079-ea9b-4899-8069-e0e3048e911d.sketch_text.stroke-152"),sQuery(id+"FHMxAyK4CFUKdhS_1.wireOp",EDGE,"1cb9c079-ea9b-4899-8069-e0e3048e911d.sketch_text.stroke-153"),sQuery(id+"FHMxAyK4CFUKdhS_1.wireOp",EDGE,"1cb9c079-ea9b-4899-8069-e0e3048e911d.sketch_text.stroke-159"),sQuery(id+"FHMxAyK4CFUKdhS_1.wireOp",EDGE,"1cb9c079-ea9b-4899-8069-e0e3048e911d.sketch_text.stroke-160"),sQuery(id+"FHMxAyK4CFUKdhS_1.wireOp",EDGE,"1cb9c079-ea9b-4899-8069-e0e3048e911d.sketch_text.stroke-161"),sQuery(id+"FHMxAyK4CFUKdhS_1.wireOp",EDGE,"1cb9c079-ea9b-4899-8069-e0e3048e911d.sketch_text.stroke-162"),sQuery(id+"FHMxAyK4CFUKdhS_1.wireOp",EDGE,"1cb9c079-ea9b-4899-8069-e0e3048e911d.sketch_text.stroke-163"),sQuery(id+"FHMxAyK4CFUKdhS_1.wireOp",EDGE,"1cb9c079-ea9b-4899-8069-e0e3048e911d.sketch_text.stroke-164"),sQuery(id+"FHMxAyK4CFUKdhS_1.wireOp",EDGE,"1cb9c079-ea9b-4899-8069-e0e3048e911d.sketch_text.stroke-165"),sQuery(id+"FHMxAyK4CFUKdhS_1.wireOp",EDGE,"1cb9c079-ea9b-4899-8069-e0e3048e911d.sketch_text.stroke-166"),sQuery(id+"FHMxAyK4CFUKdhS_1.wireOp",EDGE,"1cb9c079-ea9b-4899-8069-e0e3048e911d.sketch_text.stroke-167"),sQuery(id+"FHMxAyK4CFUKdhS_1.wireOp",EDGE,"1cb9c079-ea9b-4899-8069-e0e3048e911d.sketch_text.stroke-168"),sQuery(id+"FHMxAyK4CFUKdhS_1.wireOp",EDGE,"1cb9c079-ea9b-4899-8069-e0e3048e911d.sketch_text.stroke-169"),sQuery(id+"FHMxAyK4CFUKdhS_1.wireOp",EDGE,"1cb9c079-ea9b-4899-8069-e0e3048e911d.sketch_text.stroke-170"),sQuery(id+"FHMxAyK4CFUKdhS_1.wireOp",EDGE,"1cb9c079-ea9b-4899-8069-e0e3048e911d.sketch_text.stroke-171"),sQuery(id+"FHMxAyK4CFUKdhS_1.wireOp",EDGE,"1cb9c079-ea9b-4899-8069-e0e3048e911d.sketch_text.stroke-172"),sQuery(id+"FHMxAyK4CFUKdhS_1.wireOp",EDGE,"1cb9c079-ea9b-4899-8069-e0e3048e911d.sketch_text.stroke-173"),sQuery(id+"FHMxAyK4CFUKdhS_1.wireOp",EDGE,"1cb9c079-ea9b-4899-8069-e0e3048e911d.sketch_text.stroke-174"),sQuery(id+"FHMxAyK4CFUKdhS_1.wireOp",EDGE,"1cb9c079-ea9b-4899-8069-e0e3048e911d.sketch_text.stroke-175"),sQuery(id+"FHMxAyK4CFUKdhS_1.wireOp",EDGE,"1cb9c079-ea9b-4899-8069-e0e3048e911d.sketch_text.stroke-176"),sQuery(id+"FHMxAyK4CFUKdhS_1.wireOp",EDGE,"1cb9c079-ea9b-4899-8069-e0e3048e911d.sketch_text.stroke-177"),sQuery(id+"FHMxAyK4CFUKdhS_1.wireOp",EDGE,"1cb9c079-ea9b-4899-8069-e0e3048e911d.sketch_text.stroke-178"),sQuery(id+"FHMxAyK4CFUKdhS_1.wireOp",EDGE,"1cb9c079-ea9b-4899-8069-e0e3048e911d.sketch_text.stroke-179"),sQuery(id+"FHMxAyK4CFUKdhS_1.wireOp",EDGE,"1cb9c079-ea9b-4899-8069-e0e3048e911d.sketch_text.stroke-180"),sQuery(id+"F3.wireOp",EDGE,"8007402e-1a4e-4a06-85a5-2af08e553504"),subQ2])],"isStart":true}),makeQuery(id+"F4.opExtrude","SWEPT_FACE",FACE,{"disambiguationData":[OSD([subQ2])]})])],"derivedFrom":makeQuery(id+"F4.opExtrude","CAP_EDGE",EDGE,{"disambiguationData":[OSD([subQ2])],"isStart":true})});}
            var Q8;
            Q8=makeQuery(id+"F1.opExtrude","CAP_EDGE",EDGE,{"disambiguationData":[OSD([sQuery(id+"F0.wireOp",EDGE,"E0.right")])],"isStart":false});
            var Q9;
            {var subQ0=sQuery(id+"F0.wireOp",EDGE,"E0.top");var subQ1=sQuery(id+"F0.wireOp",EDGE,"E0.bottom");var subQ2=sQuery(id+"F3.wireOp",EDGE,"6ee83ff3-586e-4dbe-aaea-af71240543bd");Q9=makeQuery(id+"F4.boolean.opBoolean","SPLIT",EDGE,{"disambiguationData":[TD([makeQuery(id+"F1.opExtrude","CAP_FACE",FACE,{"disambiguationData":[OSD([subQ1,subQ0,sQuery(id+"F0.wireOp",EDGE,"E0.left"),sQuery(id+"F0.wireOp",EDGE,"E0.right")])],"isStart":false}),makeQuery(id+"F1.opExtrude","SWEPT_FACE",FACE,{"disambiguationData":[OSD([subQ0])]}),makeQuery(id+"F4.opExtrude","CAP_FACE",FACE,{"disambiguationData":[OSD([subQ1,sQuery(id+"F2.wireOp",EDGE,"fcba4419-a2ee-464f-be9d-58f11bf3418b.sketch_text.stroke-0"),sQuery(id+"F2.wireOp",EDGE,"fcba4419-a2ee-464f-be9d-58f11bf3418b.sketch_text.stroke-1"),sQuery(id+"F2.wireOp",EDGE,"fcba4419-a2ee-464f-be9d-58f11bf3418b.sketch_text.stroke-2"),sQuery(id+"F2.wireOp",EDGE,"fcba4419-a2ee-464f-be9d-58f11bf3418b.sketch_text.stroke-3"),sQuery(id+"F2.wireOp",EDGE,"fcba4419-a2ee-464f-be9d-58f11bf3418b.sketch_text.stroke-4"),sQuery(id+"F2.wireOp",EDGE,"fcba4419-a2ee-464f-be9d-58f11bf3418b.sketch_text.stroke-5"),sQuery(id+"F2.wireOp",EDGE,"fcba4419-a2ee-464f-be9d-58f11bf3418b.sketch_text.stroke-6"),sQuery(id+"F2.wireOp",EDGE,"fcba4419-a2ee-464f-be9d-58f11bf3418b.sketch_text.stroke-7"),sQuery(id+"F2.wireOp",EDGE,"fcba4419-a2ee-464f-be9d-58f11bf3418b.sketch_text.stroke-8"),sQuery(id+"F2.wireOp",EDGE,"fcba4419-a2ee-464f-be9d-58f11bf3418b.sketch_text.stroke-9"),sQuery(id+"F2.wireOp",EDGE,"fcba4419-a2ee-464f-be9d-58f11bf3418b.sketch_text.stroke-10"),sQuery(id+"F2.wireOp",EDGE,"fcba4419-a2ee-464f-be9d-58f11bf3418b.sketch_text.stroke-11"),sQuery(id+"F2.wireOp",EDGE,"fcba4419-a2ee-464f-be9d-58f11bf3418b.sketch_text.stroke-12"),sQuery(id+"F2.wireOp",EDGE,"fcba4419-a2ee-464f-be9d-58f11bf3418b.sketch_text.stroke-13"),sQuery(id+"F2.wireOp",EDGE,"fcba4419-a2ee-464f-be9d-58f11bf3418b.sketch_text.stroke-14"),sQuery(id+"F2.wireOp",EDGE,"fcba4419-a2ee-464f-be9d-58f11bf3418b.sketch_text.stroke-15"),sQuery(id+"F2.wireOp",EDGE,"fcba4419-a2ee-464f-be9d-58f11bf3418b.sketch_text.stroke-16"),sQuery(id+"F2.wireOp",EDGE,"fcba4419-a2ee-464f-be9d-58f11bf3418b.sketch_text.stroke-17"),sQuery(id+"F2.wireOp",EDGE,"fcba4419-a2ee-464f-be9d-58f11bf3418b.sketch_text.stroke-18"),sQuery(id+"F2.wireOp",EDGE,"fcba4419-a2ee-464f-be9d-58f11bf3418b.sketch_text.stroke-19"),sQuery(id+"F2.wireOp",EDGE,"fcba4419-a2ee-464f-be9d-58f11bf3418b.sketch_text.stroke-20"),sQuery(id+"F2.wireOp",EDGE,"fcba4419-a2ee-464f-be9d-58f11bf3418b.sketch_text.stroke-21"),sQuery(id+"F2.wireOp",EDGE,"fcba4419-a2ee-464f-be9d-58f11bf3418b.sketch_text.stroke-22"),sQuery(id+"F2.wireOp",EDGE,"fcba4419-a2ee-464f-be9d-58f11bf3418b.sketch_text.stroke-23"),sQuery(id+"F2.wireOp",EDGE,"fcba4419-a2ee-464f-be9d-58f11bf3418b.sketch_text.stroke-24"),sQuery(id+"F2.wireOp",EDGE,"fcba4419-a2ee-464f-be9d-58f11bf3418b.sketch_text.stroke-25"),sQuery(id+"F2.wireOp",EDGE,"fcba4419-a2ee-464f-be9d-58f11bf3418b.sketch_text.stroke-26"),sQuery(id+"F2.wireOp",EDGE,"fcba4419-a2ee-464f-be9d-58f11bf3418b.sketch_text.stroke-27"),sQuery(id+"F2.wireOp",EDGE,"fcba4419-a2ee-464f-be9d-58f11bf3418b.sketch_text.stroke-28"),sQuery(id+"F2.wireOp",EDGE,"fcba4419-a2ee-464f-be9d-58f11bf3418b.sketch_text.stroke-29"),sQuery(id+"F2.wireOp",EDGE,"fcba4419-a2ee-464f-be9d-58f11bf3418b.sketch_text.stroke-30"),sQuery(id+"F2.wireOp",EDGE,"fcba4419-a2ee-464f-be9d-58f11bf3418b.sketch_text.stroke-31"),sQuery(id+"F2.wireOp",EDGE,"fcba4419-a2ee-464f-be9d-58f11bf3418b.sketch_text.stroke-32"),sQuery(id+"F2.wireOp",EDGE,"fcba4419-a2ee-464f-be9d-58f11bf3418b.sketch_text.stroke-33"),sQuery(id+"F2.wireOp",EDGE,"fcba4419-a2ee-464f-be9d-58f11bf3418b.sketch_text.stroke-34"),sQuery(id+"F2.wireOp",EDGE,"fcba4419-a2ee-464f-be9d-58f11bf3418b.sketch_text.stroke-35"),sQuery(id+"F2.wireOp",EDGE,"fcba4419-a2ee-464f-be9d-58f11bf3418b.sketch_text.stroke-36"),sQuery(id+"F2.wireOp",EDGE,"fcba4419-a2ee-464f-be9d-58f11bf3418b.sketch_text.stroke-37"),sQuery(id+"F2.wireOp",EDGE,"fcba4419-a2ee-464f-be9d-58f11bf3418b.sketch_text.stroke-38"),sQuery(id+"F2.wireOp",EDGE,"fcba4419-a2ee-464f-be9d-58f11bf3418b.sketch_text.stroke-39"),sQuery(id+"F2.wireOp",EDGE,"fcba4419-a2ee-464f-be9d-58f11bf3418b.sketch_text.stroke-40"),sQuery(id+"F2.wireOp",EDGE,"fcba4419-a2ee-464f-be9d-58f11bf3418b.sketch_text.stroke-41"),sQuery(id+"F2.wireOp",EDGE,"fcba4419-a2ee-464f-be9d-58f11bf3418b.sketch_text.stroke-42"),sQuery(id+"F2.wireOp",EDGE,"fcba4419-a2ee-464f-be9d-58f11bf3418b.sketch_text.stroke-43"),sQuery(id+"F2.wireOp",EDGE,"fcba4419-a2ee-464f-be9d-58f11bf3418b.sketch_text.stroke-44"),sQuery(id+"F2.wireOp",EDGE,"fcba4419-a2ee-464f-be9d-58f11bf3418b.sketch_text.stroke-45"),sQuery(id+"F2.wireOp",EDGE,"fcba4419-a2ee-464f-be9d-58f11bf3418b.sketch_text.stroke-46"),sQuery(id+"F2.wireOp",EDGE,"fcba4419-a2ee-464f-be9d-58f11bf3418b.sketch_text.stroke-47"),sQuery(id+"F2.wireOp",EDGE,"fcba4419-a2ee-464f-be9d-58f11bf3418b.sketch_text.stroke-48"),sQuery(id+"F2.wireOp",EDGE,"fcba4419-a2ee-464f-be9d-58f11bf3418b.sketch_text.stroke-49"),sQuery(id+"F2.wireOp",EDGE,"fcba4419-a2ee-464f-be9d-58f11bf3418b.sketch_text.stroke-50"),sQuery(id+"F2.wireOp",EDGE,"fcba4419-a2ee-464f-be9d-58f11bf3418b.sketch_text.stroke-51"),sQuery(id+"F2.wireOp",EDGE,"fcba4419-a2ee-464f-be9d-58f11bf3418b.sketch_text.stroke-52"),sQuery(id+"F2.wireOp",EDGE,"fcba4419-a2ee-464f-be9d-58f11bf3418b.sketch_text.stroke-53"),sQuery(id+"F2.wireOp",EDGE,"fcba4419-a2ee-464f-be9d-58f11bf3418b.sketch_text.stroke-54"),sQuery(id+"F2.wireOp",EDGE,"fcba4419-a2ee-464f-be9d-58f11bf3418b.sketch_text.stroke-55"),sQuery(id+"F2.wireOp",EDGE,"fcba4419-a2ee-464f-be9d-58f11bf3418b.sketch_text.stroke-56"),sQuery(id+"F2.wireOp",EDGE,"fcba4419-a2ee-464f-be9d-58f11bf3418b.sketch_text.stroke-57"),sQuery(id+"F2.wireOp",EDGE,"fcba4419-a2ee-464f-be9d-58f11bf3418b.sketch_text.stroke-58"),sQuery(id+"F2.wireOp",EDGE,"fcba4419-a2ee-464f-be9d-58f11bf3418b.sketch_text.stroke-59"),sQuery(id+"F2.wireOp",EDGE,"fcba4419-a2ee-464f-be9d-58f11bf3418b.sketch_text.stroke-60"),sQuery(id+"F2.wireOp",EDGE,"fcba4419-a2ee-464f-be9d-58f11bf3418b.sketch_text.stroke-61"),sQuery(id+"F2.wireOp",EDGE,"fcba4419-a2ee-464f-be9d-58f11bf3418b.sketch_text.stroke-62"),sQuery(id+"F2.wireOp",EDGE,"fcba4419-a2ee-464f-be9d-58f11bf3418b.sketch_text.stroke-63"),sQuery(id+"F2.wireOp",EDGE,"fcba4419-a2ee-464f-be9d-58f11bf3418b.sketch_text.stroke-64"),sQuery(id+"F2.wireOp",EDGE,"fcba4419-a2ee-464f-be9d-58f11bf3418b.sketch_text.stroke-65"),sQuery(id+"F2.wireOp",EDGE,"fcba4419-a2ee-464f-be9d-58f11bf3418b.sketch_text.stroke-66"),sQuery(id+"F2.wireOp",EDGE,"fcba4419-a2ee-464f-be9d-58f11bf3418b.sketch_text.stroke-67"),sQuery(id+"F2.wireOp",EDGE,"fcba4419-a2ee-464f-be9d-58f11bf3418b.sketch_text.stroke-68"),sQuery(id+"F2.wireOp",EDGE,"fcba4419-a2ee-464f-be9d-58f11bf3418b.sketch_text.stroke-69"),sQuery(id+"F2.wireOp",EDGE,"fcba4419-a2ee-464f-be9d-58f11bf3418b.sketch_text.stroke-70"),sQuery(id+"F2.wireOp",EDGE,"fcba4419-a2ee-464f-be9d-58f11bf3418b.sketch_text.stroke-71"),sQuery(id+"F2.wireOp",EDGE,"fcba4419-a2ee-464f-be9d-58f11bf3418b.sketch_text.stroke-72"),sQuery(id+"F2.wireOp",EDGE,"fcba4419-a2ee-464f-be9d-58f11bf3418b.sketch_text.stroke-73"),sQuery(id+"F2.wireOp",EDGE,"fcba4419-a2ee-464f-be9d-58f11bf3418b.sketch_text.stroke-74"),sQuery(id+"F2.wireOp",EDGE,"fcba4419-a2ee-464f-be9d-58f11bf3418b.sketch_text.stroke-75"),sQuery(id+"F2.wireOp",EDGE,"fcba4419-a2ee-464f-be9d-58f11bf3418b.sketch_text.stroke-76"),sQuery(id+"F2.wireOp",EDGE,"fcba4419-a2ee-464f-be9d-58f11bf3418b.sketch_text.stroke-77"),sQuery(id+"F2.wireOp",EDGE,"fcba4419-a2ee-464f-be9d-58f11bf3418b.sketch_text.stroke-78"),sQuery(id+"F2.wireOp",EDGE,"fcba4419-a2ee-464f-be9d-58f11bf3418b.sketch_text.stroke-79"),sQuery(id+"F2.wireOp",EDGE,"fcba4419-a2ee-464f-be9d-58f11bf3418b.sketch_text.stroke-80"),sQuery(id+"F2.wireOp",EDGE,"fcba4419-a2ee-464f-be9d-58f11bf3418b.sketch_text.stroke-81"),sQuery(id+"F2.wireOp",EDGE,"fcba4419-a2ee-464f-be9d-58f11bf3418b.sketch_text.stroke-82"),sQuery(id+"F2.wireOp",EDGE,"fcba4419-a2ee-464f-be9d-58f11bf3418b.sketch_text.stroke-83"),sQuery(id+"F2.wireOp",EDGE,"fcba4419-a2ee-464f-be9d-58f11bf3418b.sketch_text.stroke-84"),sQuery(id+"F2.wireOp",EDGE,"fcba4419-a2ee-464f-be9d-58f11bf3418b.sketch_text.stroke-85"),sQuery(id+"F2.wireOp",EDGE,"fcba4419-a2ee-464f-be9d-58f11bf3418b.sketch_text.stroke-86"),sQuery(id+"F2.wireOp",EDGE,"fcba4419-a2ee-464f-be9d-58f11bf3418b.sketch_text.stroke-87"),sQuery(id+"F2.wireOp",EDGE,"fcba4419-a2ee-464f-be9d-58f11bf3418b.sketch_text.stroke-88"),sQuery(id+"F2.wireOp",EDGE,"fcba4419-a2ee-464f-be9d-58f11bf3418b.sketch_text.stroke-89"),sQuery(id+"F2.wireOp",EDGE,"fcba4419-a2ee-464f-be9d-58f11bf3418b.sketch_text.stroke-90"),sQuery(id+"F2.wireOp",EDGE,"fcba4419-a2ee-464f-be9d-58f11bf3418b.sketch_text.stroke-91"),sQuery(id+"F2.wireOp",EDGE,"fcba4419-a2ee-464f-be9d-58f11bf3418b.sketch_text.stroke-92"),sQuery(id+"F2.wireOp",EDGE,"fcba4419-a2ee-464f-be9d-58f11bf3418b.sketch_text.stroke-93"),sQuery(id+"F2.wireOp",EDGE,"fcba4419-a2ee-464f-be9d-58f11bf3418b.sketch_text.stroke-94"),sQuery(id+"F2.wireOp",EDGE,"fcba4419-a2ee-464f-be9d-58f11bf3418b.sketch_text.stroke-95"),sQuery(id+"F2.wireOp",EDGE,"fcba4419-a2ee-464f-be9d-58f11bf3418b.sketch_text.stroke-96"),sQuery(id+"F2.wireOp",EDGE,"fcba4419-a2ee-464f-be9d-58f11bf3418b.sketch_text.stroke-97"),sQuery(id+"F2.wireOp",EDGE,"fcba4419-a2ee-464f-be9d-58f11bf3418b.sketch_text.stroke-98"),sQuery(id+"F2.wireOp",EDGE,"fcba4419-a2ee-464f-be9d-58f11bf3418b.sketch_text.stroke-99"),sQuery(id+"F2.wireOp",EDGE,"fcba4419-a2ee-464f-be9d-58f11bf3418b.sketch_text.stroke-100"),sQuery(id+"F2.wireOp",EDGE,"fcba4419-a2ee-464f-be9d-58f11bf3418b.sketch_text.stroke-101"),sQuery(id+"F2.wireOp",EDGE,"fcba4419-a2ee-464f-be9d-58f11bf3418b.sketch_text.stroke-102"),sQuery(id+"F2.wireOp",EDGE,"fcba4419-a2ee-464f-be9d-58f11bf3418b.sketch_text.stroke-103"),sQuery(id+"F2.wireOp",EDGE,"fcba4419-a2ee-464f-be9d-58f11bf3418b.sketch_text.stroke-104"),sQuery(id+"F2.wireOp",EDGE,"fcba4419-a2ee-464f-be9d-58f11bf3418b.sketch_text.stroke-105"),sQuery(id+"F2.wireOp",EDGE,"fcba4419-a2ee-464f-be9d-58f11bf3418b.sketch_text.stroke-106"),sQuery(id+"F2.wireOp",EDGE,"fcba4419-a2ee-464f-be9d-58f11bf3418b.sketch_text.stroke-107"),sQuery(id+"F2.wireOp",EDGE,"fcba4419-a2ee-464f-be9d-58f11bf3418b.sketch_text.stroke-108"),sQuery(id+"F2.wireOp",EDGE,"fcba4419-a2ee-464f-be9d-58f11bf3418b.sketch_text.stroke-109"),sQuery(id+"F2.wireOp",EDGE,"fcba4419-a2ee-464f-be9d-58f11bf3418b.sketch_text.stroke-110"),sQuery(id+"F2.wireOp",EDGE,"fcba4419-a2ee-464f-be9d-58f11bf3418b.sketch_text.stroke-111"),sQuery(id+"F2.wireOp",EDGE,"fcba4419-a2ee-464f-be9d-58f11bf3418b.sketch_text.stroke-112"),sQuery(id+"F2.wireOp",EDGE,"fcba4419-a2ee-464f-be9d-58f11bf3418b.sketch_text.stroke-113"),sQuery(id+"F2.wireOp",EDGE,"fcba4419-a2ee-464f-be9d-58f11bf3418b.sketch_text.stroke-114"),sQuery(id+"F2.wireOp",EDGE,"fcba4419-a2ee-464f-be9d-58f11bf3418b.sketch_text.stroke-115"),sQuery(id+"F2.wireOp",EDGE,"fcba4419-a2ee-464f-be9d-58f11bf3418b.sketch_text.stroke-116"),sQuery(id+"F2.wireOp",EDGE,"fcba4419-a2ee-464f-be9d-58f11bf3418b.sketch_text.stroke-117"),sQuery(id+"F2.wireOp",EDGE,"fcba4419-a2ee-464f-be9d-58f11bf3418b.sketch_text.stroke-118"),sQuery(id+"F2.wireOp",EDGE,"fcba4419-a2ee-464f-be9d-58f11bf3418b.sketch_text.stroke-119"),sQuery(id+"F2.wireOp",EDGE,"fcba4419-a2ee-464f-be9d-58f11bf3418b.sketch_text.stroke-120"),sQuery(id+"F2.wireOp",EDGE,"fcba4419-a2ee-464f-be9d-58f11bf3418b.sketch_text.stroke-121"),sQuery(id+"F2.wireOp",EDGE,"fcba4419-a2ee-464f-be9d-58f11bf3418b.sketch_text.stroke-122"),sQuery(id+"F2.wireOp",EDGE,"fcba4419-a2ee-464f-be9d-58f11bf3418b.sketch_text.stroke-123"),sQuery(id+"F2.wireOp",EDGE,"fcba4419-a2ee-464f-be9d-58f11bf3418b.sketch_text.stroke-124"),sQuery(id+"F2.wireOp",EDGE,"fcba4419-a2ee-464f-be9d-58f11bf3418b.sketch_text.stroke-125"),sQuery(id+"F2.wireOp",EDGE,"fcba4419-a2ee-464f-be9d-58f11bf3418b.sketch_text.stroke-126"),sQuery(id+"F2.wireOp",EDGE,"fcba4419-a2ee-464f-be9d-58f11bf3418b.sketch_text.stroke-127"),sQuery(id+"F2.wireOp",EDGE,"fcba4419-a2ee-464f-be9d-58f11bf3418b.sketch_text.stroke-128"),sQuery(id+"F2.wireOp",EDGE,"fcba4419-a2ee-464f-be9d-58f11bf3418b.sketch_text.stroke-129"),sQuery(id+"F2.wireOp",EDGE,"fcba4419-a2ee-464f-be9d-58f11bf3418b.sketch_text.stroke-130"),sQuery(id+"F2.wireOp",EDGE,"fcba4419-a2ee-464f-be9d-58f11bf3418b.sketch_text.stroke-131"),sQuery(id+"F2.wireOp",EDGE,"fcba4419-a2ee-464f-be9d-58f11bf3418b.sketch_text.stroke-132"),sQuery(id+"F2.wireOp",EDGE,"fcba4419-a2ee-464f-be9d-58f11bf3418b.sketch_text.stroke-133"),sQuery(id+"F2.wireOp",EDGE,"fcba4419-a2ee-464f-be9d-58f11bf3418b.sketch_text.stroke-134"),sQuery(id+"F2.wireOp",EDGE,"fcba4419-a2ee-464f-be9d-58f11bf3418b.sketch_text.stroke-135"),sQuery(id+"F2.wireOp",EDGE,"fcba4419-a2ee-464f-be9d-58f11bf3418b.sketch_text.stroke-136"),sQuery(id+"F2.wireOp",EDGE,"fcba4419-a2ee-464f-be9d-58f11bf3418b.sketch_text.stroke-137"),sQuery(id+"F2.wireOp",EDGE,"fcba4419-a2ee-464f-be9d-58f11bf3418b.sketch_text.stroke-138"),sQuery(id+"F2.wireOp",EDGE,"fcba4419-a2ee-464f-be9d-58f11bf3418b.sketch_text.stroke-139"),sQuery(id+"F2.wireOp",EDGE,"fcba4419-a2ee-464f-be9d-58f11bf3418b.sketch_text.stroke-140"),sQuery(id+"F2.wireOp",EDGE,"fcba4419-a2ee-464f-be9d-58f11bf3418b.sketch_text.stroke-141"),sQuery(id+"F2.wireOp",EDGE,"fcba4419-a2ee-464f-be9d-58f11bf3418b.sketch_text.stroke-142"),sQuery(id+"F2.wireOp",EDGE,"fcba4419-a2ee-464f-be9d-58f11bf3418b.sketch_text.stroke-143"),sQuery(id+"F2.wireOp",EDGE,"fcba4419-a2ee-464f-be9d-58f11bf3418b.sketch_text.stroke-144"),sQuery(id+"F2.wireOp",EDGE,"fcba4419-a2ee-464f-be9d-58f11bf3418b.sketch_text.stroke-145"),sQuery(id+"F2.wireOp",EDGE,"fcba4419-a2ee-464f-be9d-58f11bf3418b.sketch_text.stroke-146"),sQuery(id+"F2.wireOp",EDGE,"fcba4419-a2ee-464f-be9d-58f11bf3418b.sketch_text.stroke-147"),sQuery(id+"F2.wireOp",EDGE,"fcba4419-a2ee-464f-be9d-58f11bf3418b.sketch_text.stroke-148"),sQuery(id+"F2.wireOp",EDGE,"fcba4419-a2ee-464f-be9d-58f11bf3418b.sketch_text.stroke-149"),sQuery(id+"F2.wireOp",EDGE,"fcba4419-a2ee-464f-be9d-58f11bf3418b.sketch_text.stroke-150"),sQuery(id+"F2.wireOp",EDGE,"fcba4419-a2ee-464f-be9d-58f11bf3418b.sketch_text.stroke-151"),sQuery(id+"F2.wireOp",EDGE,"fcba4419-a2ee-464f-be9d-58f11bf3418b.sketch_text.stroke-152"),sQuery(id+"F2.wireOp",EDGE,"fcba4419-a2ee-464f-be9d-58f11bf3418b.sketch_text.stroke-153"),sQuery(id+"F2.wireOp",EDGE,"fcba4419-a2ee-464f-be9d-58f11bf3418b.sketch_text.stroke-154"),sQuery(id+"F2.wireOp",EDGE,"fcba4419-a2ee-464f-be9d-58f11bf3418b.sketch_text.stroke-155"),sQuery(id+"F2.wireOp",EDGE,"fcba4419-a2ee-464f-be9d-58f11bf3418b.sketch_text.stroke-156"),sQuery(id+"F2.wireOp",EDGE,"fcba4419-a2ee-464f-be9d-58f11bf3418b.sketch_text.stroke-157"),sQuery(id+"F2.wireOp",EDGE,"fcba4419-a2ee-464f-be9d-58f11bf3418b.sketch_text.stroke-158"),sQuery(id+"F2.wireOp",EDGE,"fcba4419-a2ee-464f-be9d-58f11bf3418b.sketch_text.stroke-159"),sQuery(id+"F2.wireOp",EDGE,"fcba4419-a2ee-464f-be9d-58f11bf3418b.sketch_text.stroke-160"),sQuery(id+"F2.wireOp",EDGE,"fcba4419-a2ee-464f-be9d-58f11bf3418b.sketch_text.stroke-161"),sQuery(id+"F2.wireOp",EDGE,"fcba4419-a2ee-464f-be9d-58f11bf3418b.sketch_text.stroke-162"),sQuery(id+"F2.wireOp",EDGE,"fcba4419-a2ee-464f-be9d-58f11bf3418b.sketch_text.stroke-163"),sQuery(id+"F2.wireOp",EDGE,"fcba4419-a2ee-464f-be9d-58f11bf3418b.sketch_text.stroke-164"),sQuery(id+"F2.wireOp",EDGE,"fcba4419-a2ee-464f-be9d-58f11bf3418b.sketch_text.stroke-165"),sQuery(id+"F2.wireOp",EDGE,"fcba4419-a2ee-464f-be9d-58f11bf3418b.sketch_text.stroke-166"),sQuery(id+"F2.wireOp",EDGE,"fcba4419-a2ee-464f-be9d-58f11bf3418b.sketch_text.stroke-167"),sQuery(id+"F2.wireOp",EDGE,"fcba4419-a2ee-464f-be9d-58f11bf3418b.sketch_text.stroke-168"),sQuery(id+"F2.wireOp",EDGE,"fcba4419-a2ee-464f-be9d-58f11bf3418b.sketch_text.stroke-169"),sQuery(id+"F2.wireOp",EDGE,"fcba4419-a2ee-464f-be9d-58f11bf3418b.sketch_text.stroke-170"),sQuery(id+"F2.wireOp",EDGE,"fcba4419-a2ee-464f-be9d-58f11bf3418b.sketch_text.stroke-171"),sQuery(id+"F2.wireOp",EDGE,"fcba4419-a2ee-464f-be9d-58f11bf3418b.sketch_text.stroke-172"),sQuery(id+"F2.wireOp",EDGE,"fcba4419-a2ee-464f-be9d-58f11bf3418b.sketch_text.stroke-173"),sQuery(id+"FHMxAyK4CFUKdhS_1.wireOp",EDGE,"1cb9c079-ea9b-4899-8069-e0e3048e911d.sketch_text.stroke-0"),sQuery(id+"FHMxAyK4CFUKdhS_1.wireOp",EDGE,"1cb9c079-ea9b-4899-8069-e0e3048e911d.sketch_text.stroke-1"),sQuery(id+"FHMxAyK4CFUKdhS_1.wireOp",EDGE,"1cb9c079-ea9b-4899-8069-e0e3048e911d.sketch_text.stroke-2"),sQuery(id+"FHMxAyK4CFUKdhS_1.wireOp",EDGE,"1cb9c079-ea9b-4899-8069-e0e3048e911d.sketch_text.stroke-3"),sQuery(id+"FHMxAyK4CFUKdhS_1.wireOp",EDGE,"1cb9c079-ea9b-4899-8069-e0e3048e911d.sketch_text.stroke-4"),sQuery(id+"FHMxAyK4CFUKdhS_1.wireOp",EDGE,"1cb9c079-ea9b-4899-8069-e0e3048e911d.sketch_text.stroke-5"),sQuery(id+"FHMxAyK4CFUKdhS_1.wireOp",EDGE,"1cb9c079-ea9b-4899-8069-e0e3048e911d.sketch_text.stroke-6"),sQuery(id+"FHMxAyK4CFUKdhS_1.wireOp",EDGE,"1cb9c079-ea9b-4899-8069-e0e3048e911d.sketch_text.stroke-7"),sQuery(id+"FHMxAyK4CFUKdhS_1.wireOp",EDGE,"1cb9c079-ea9b-4899-8069-e0e3048e911d.sketch_text.stroke-8"),sQuery(id+"FHMxAyK4CFUKdhS_1.wireOp",EDGE,"1cb9c079-ea9b-4899-8069-e0e3048e911d.sketch_text.stroke-9"),sQuery(id+"FHMxAyK4CFUKdhS_1.wireOp",EDGE,"1cb9c079-ea9b-4899-8069-e0e3048e911d.sketch_text.stroke-10"),sQuery(id+"FHMxAyK4CFUKdhS_1.wireOp",EDGE,"1cb9c079-ea9b-4899-8069-e0e3048e911d.sketch_text.stroke-11"),sQuery(id+"FHMxAyK4CFUKdhS_1.wireOp",EDGE,"1cb9c079-ea9b-4899-8069-e0e3048e911d.sketch_text.stroke-12"),sQuery(id+"FHMxAyK4CFUKdhS_1.wireOp",EDGE,"1cb9c079-ea9b-4899-8069-e0e3048e911d.sketch_text.stroke-13"),sQuery(id+"FHMxAyK4CFUKdhS_1.wireOp",EDGE,"1cb9c079-ea9b-4899-8069-e0e3048e911d.sketch_text.stroke-14"),sQuery(id+"FHMxAyK4CFUKdhS_1.wireOp",EDGE,"1cb9c079-ea9b-4899-8069-e0e3048e911d.sketch_text.stroke-15"),sQuery(id+"FHMxAyK4CFUKdhS_1.wireOp",EDGE,"1cb9c079-ea9b-4899-8069-e0e3048e911d.sketch_text.stroke-16"),sQuery(id+"FHMxAyK4CFUKdhS_1.wireOp",EDGE,"1cb9c079-ea9b-4899-8069-e0e3048e911d.sketch_text.stroke-17"),sQuery(id+"FHMxAyK4CFUKdhS_1.wireOp",EDGE,"1cb9c079-ea9b-4899-8069-e0e3048e911d.sketch_text.stroke-18"),sQuery(id+"FHMxAyK4CFUKdhS_1.wireOp",EDGE,"1cb9c079-ea9b-4899-8069-e0e3048e911d.sketch_text.stroke-19"),sQuery(id+"FHMxAyK4CFUKdhS_1.wireOp",EDGE,"1cb9c079-ea9b-4899-8069-e0e3048e911d.sketch_text.stroke-20"),sQuery(id+"FHMxAyK4CFUKdhS_1.wireOp",EDGE,"1cb9c079-ea9b-4899-8069-e0e3048e911d.sketch_text.stroke-21"),sQuery(id+"FHMxAyK4CFUKdhS_1.wireOp",EDGE,"1cb9c079-ea9b-4899-8069-e0e3048e911d.sketch_text.stroke-22"),sQuery(id+"FHMxAyK4CFUKdhS_1.wireOp",EDGE,"1cb9c079-ea9b-4899-8069-e0e3048e911d.sketch_text.stroke-23"),sQuery(id+"FHMxAyK4CFUKdhS_1.wireOp",EDGE,"1cb9c079-ea9b-4899-8069-e0e3048e911d.sketch_text.stroke-24"),sQuery(id+"FHMxAyK4CFUKdhS_1.wireOp",EDGE,"1cb9c079-ea9b-4899-8069-e0e3048e911d.sketch_text.stroke-25"),sQuery(id+"FHMxAyK4CFUKdhS_1.wireOp",EDGE,"1cb9c079-ea9b-4899-8069-e0e3048e911d.sketch_text.stroke-26"),sQuery(id+"FHMxAyK4CFUKdhS_1.wireOp",EDGE,"1cb9c079-ea9b-4899-8069-e0e3048e911d.sketch_text.stroke-27"),sQuery(id+"FHMxAyK4CFUKdhS_1.wireOp",EDGE,"1cb9c079-ea9b-4899-8069-e0e3048e911d.sketch_text.stroke-28"),sQuery(id+"FHMxAyK4CFUKdhS_1.wireOp",EDGE,"1cb9c079-ea9b-4899-8069-e0e3048e911d.sketch_text.stroke-29"),sQuery(id+"FHMxAyK4CFUKdhS_1.wireOp",EDGE,"1cb9c079-ea9b-4899-8069-e0e3048e911d.sketch_text.stroke-30"),sQuery(id+"FHMxAyK4CFUKdhS_1.wireOp",EDGE,"1cb9c079-ea9b-4899-8069-e0e3048e911d.sketch_text.stroke-31"),sQuery(id+"FHMxAyK4CFUKdhS_1.wireOp",EDGE,"1cb9c079-ea9b-4899-8069-e0e3048e911d.sketch_text.stroke-32"),sQuery(id+"FHMxAyK4CFUKdhS_1.wireOp",EDGE,"1cb9c079-ea9b-4899-8069-e0e3048e911d.sketch_text.stroke-33"),sQuery(id+"FHMxAyK4CFUKdhS_1.wireOp",EDGE,"1cb9c079-ea9b-4899-8069-e0e3048e911d.sketch_text.stroke-34"),sQuery(id+"FHMxAyK4CFUKdhS_1.wireOp",EDGE,"1cb9c079-ea9b-4899-8069-e0e3048e911d.sketch_text.stroke-35"),sQuery(id+"FHMxAyK4CFUKdhS_1.wireOp",EDGE,"1cb9c079-ea9b-4899-8069-e0e3048e911d.sketch_text.stroke-36"),sQuery(id+"FHMxAyK4CFUKdhS_1.wireOp",EDGE,"1cb9c079-ea9b-4899-8069-e0e3048e911d.sketch_text.stroke-37"),sQuery(id+"FHMxAyK4CFUKdhS_1.wireOp",EDGE,"1cb9c079-ea9b-4899-8069-e0e3048e911d.sketch_text.stroke-38"),sQuery(id+"FHMxAyK4CFUKdhS_1.wireOp",EDGE,"1cb9c079-ea9b-4899-8069-e0e3048e911d.sketch_text.stroke-39"),sQuery(id+"FHMxAyK4CFUKdhS_1.wireOp",EDGE,"1cb9c079-ea9b-4899-8069-e0e3048e911d.sketch_text.stroke-40"),sQuery(id+"FHMxAyK4CFUKdhS_1.wireOp",EDGE,"1cb9c079-ea9b-4899-8069-e0e3048e911d.sketch_text.stroke-41"),sQuery(id+"FHMxAyK4CFUKdhS_1.wireOp",EDGE,"1cb9c079-ea9b-4899-8069-e0e3048e911d.sketch_text.stroke-42"),sQuery(id+"FHMxAyK4CFUKdhS_1.wireOp",EDGE,"1cb9c079-ea9b-4899-8069-e0e3048e911d.sketch_text.stroke-43"),sQuery(id+"FHMxAyK4CFUKdhS_1.wireOp",EDGE,"1cb9c079-ea9b-4899-8069-e0e3048e911d.sketch_text.stroke-44"),sQuery(id+"FHMxAyK4CFUKdhS_1.wireOp",EDGE,"1cb9c079-ea9b-4899-8069-e0e3048e911d.sketch_text.stroke-45"),sQuery(id+"FHMxAyK4CFUKdhS_1.wireOp",EDGE,"1cb9c079-ea9b-4899-8069-e0e3048e911d.sketch_text.stroke-46"),sQuery(id+"FHMxAyK4CFUKdhS_1.wireOp",EDGE,"1cb9c079-ea9b-4899-8069-e0e3048e911d.sketch_text.stroke-47"),sQuery(id+"FHMxAyK4CFUKdhS_1.wireOp",EDGE,"1cb9c079-ea9b-4899-8069-e0e3048e911d.sketch_text.stroke-48"),sQuery(id+"FHMxAyK4CFUKdhS_1.wireOp",EDGE,"1cb9c079-ea9b-4899-8069-e0e3048e911d.sketch_text.stroke-49"),sQuery(id+"FHMxAyK4CFUKdhS_1.wireOp",EDGE,"1cb9c079-ea9b-4899-8069-e0e3048e911d.sketch_text.stroke-50"),sQuery(id+"FHMxAyK4CFUKdhS_1.wireOp",EDGE,"1cb9c079-ea9b-4899-8069-e0e3048e911d.sketch_text.stroke-51"),sQuery(id+"FHMxAyK4CFUKdhS_1.wireOp",EDGE,"1cb9c079-ea9b-4899-8069-e0e3048e911d.sketch_text.stroke-52"),sQuery(id+"FHMxAyK4CFUKdhS_1.wireOp",EDGE,"1cb9c079-ea9b-4899-8069-e0e3048e911d.sketch_text.stroke-53"),sQuery(id+"FHMxAyK4CFUKdhS_1.wireOp",EDGE,"1cb9c079-ea9b-4899-8069-e0e3048e911d.sketch_text.stroke-54"),sQuery(id+"FHMxAyK4CFUKdhS_1.wireOp",EDGE,"1cb9c079-ea9b-4899-8069-e0e3048e911d.sketch_text.stroke-55"),sQuery(id+"FHMxAyK4CFUKdhS_1.wireOp",EDGE,"1cb9c079-ea9b-4899-8069-e0e3048e911d.sketch_text.stroke-56"),sQuery(id+"FHMxAyK4CFUKdhS_1.wireOp",EDGE,"1cb9c079-ea9b-4899-8069-e0e3048e911d.sketch_text.stroke-57"),sQuery(id+"FHMxAyK4CFUKdhS_1.wireOp",EDGE,"1cb9c079-ea9b-4899-8069-e0e3048e911d.sketch_text.stroke-58"),sQuery(id+"FHMxAyK4CFUKdhS_1.wireOp",EDGE,"1cb9c079-ea9b-4899-8069-e0e3048e911d.sketch_text.stroke-59"),sQuery(id+"FHMxAyK4CFUKdhS_1.wireOp",EDGE,"1cb9c079-ea9b-4899-8069-e0e3048e911d.sketch_text.stroke-60"),sQuery(id+"FHMxAyK4CFUKdhS_1.wireOp",EDGE,"1cb9c079-ea9b-4899-8069-e0e3048e911d.sketch_text.stroke-61"),sQuery(id+"FHMxAyK4CFUKdhS_1.wireOp",EDGE,"1cb9c079-ea9b-4899-8069-e0e3048e911d.sketch_text.stroke-62"),sQuery(id+"FHMxAyK4CFUKdhS_1.wireOp",EDGE,"1cb9c079-ea9b-4899-8069-e0e3048e911d.sketch_text.stroke-71"),sQuery(id+"FHMxAyK4CFUKdhS_1.wireOp",EDGE,"1cb9c079-ea9b-4899-8069-e0e3048e911d.sketch_text.stroke-72"),sQuery(id+"FHMxAyK4CFUKdhS_1.wireOp",EDGE,"1cb9c079-ea9b-4899-8069-e0e3048e911d.sketch_text.stroke-73"),sQuery(id+"FHMxAyK4CFUKdhS_1.wireOp",EDGE,"1cb9c079-ea9b-4899-8069-e0e3048e911d.sketch_text.stroke-74"),sQuery(id+"FHMxAyK4CFUKdhS_1.wireOp",EDGE,"1cb9c079-ea9b-4899-8069-e0e3048e911d.sketch_text.stroke-75"),sQuery(id+"FHMxAyK4CFUKdhS_1.wireOp",EDGE,"1cb9c079-ea9b-4899-8069-e0e3048e911d.sketch_text.stroke-76"),sQuery(id+"FHMxAyK4CFUKdhS_1.wireOp",EDGE,"1cb9c079-ea9b-4899-8069-e0e3048e911d.sketch_text.stroke-77"),sQuery(id+"FHMxAyK4CFUKdhS_1.wireOp",EDGE,"1cb9c079-ea9b-4899-8069-e0e3048e911d.sketch_text.stroke-78"),sQuery(id+"FHMxAyK4CFUKdhS_1.wireOp",EDGE,"1cb9c079-ea9b-4899-8069-e0e3048e911d.sketch_text.stroke-79"),sQuery(id+"FHMxAyK4CFUKdhS_1.wireOp",EDGE,"1cb9c079-ea9b-4899-8069-e0e3048e911d.sketch_text.stroke-80"),sQuery(id+"FHMxAyK4CFUKdhS_1.wireOp",EDGE,"1cb9c079-ea9b-4899-8069-e0e3048e911d.sketch_text.stroke-81"),sQuery(id+"FHMxAyK4CFUKdhS_1.wireOp",EDGE,"1cb9c079-ea9b-4899-8069-e0e3048e911d.sketch_text.stroke-82"),sQuery(id+"FHMxAyK4CFUKdhS_1.wireOp",EDGE,"1cb9c079-ea9b-4899-8069-e0e3048e911d.sketch_text.stroke-83"),sQuery(id+"FHMxAyK4CFUKdhS_1.wireOp",EDGE,"1cb9c079-ea9b-4899-8069-e0e3048e911d.sketch_text.stroke-84"),sQuery(id+"FHMxAyK4CFUKdhS_1.wireOp",EDGE,"1cb9c079-ea9b-4899-8069-e0e3048e911d.sketch_text.stroke-85"),sQuery(id+"FHMxAyK4CFUKdhS_1.wireOp",EDGE,"1cb9c079-ea9b-4899-8069-e0e3048e911d.sketch_text.stroke-86"),sQuery(id+"FHMxAyK4CFUKdhS_1.wireOp",EDGE,"1cb9c079-ea9b-4899-8069-e0e3048e911d.sketch_text.stroke-87"),sQuery(id+"FHMxAyK4CFUKdhS_1.wireOp",EDGE,"1cb9c079-ea9b-4899-8069-e0e3048e911d.sketch_text.stroke-88"),sQuery(id+"FHMxAyK4CFUKdhS_1.wireOp",EDGE,"1cb9c079-ea9b-4899-8069-e0e3048e911d.sketch_text.stroke-89"),sQuery(id+"FHMxAyK4CFUKdhS_1.wireOp",EDGE,"1cb9c079-ea9b-4899-8069-e0e3048e911d.sketch_text.stroke-90"),sQuery(id+"FHMxAyK4CFUKdhS_1.wireOp",EDGE,"1cb9c079-ea9b-4899-8069-e0e3048e911d.sketch_text.stroke-91"),sQuery(id+"FHMxAyK4CFUKdhS_1.wireOp",EDGE,"1cb9c079-ea9b-4899-8069-e0e3048e911d.sketch_text.stroke-92"),sQuery(id+"FHMxAyK4CFUKdhS_1.wireOp",EDGE,"1cb9c079-ea9b-4899-8069-e0e3048e911d.sketch_text.stroke-93"),sQuery(id+"FHMxAyK4CFUKdhS_1.wireOp",EDGE,"1cb9c079-ea9b-4899-8069-e0e3048e911d.sketch_text.stroke-94"),sQuery(id+"FHMxAyK4CFUKdhS_1.wireOp",EDGE,"1cb9c079-ea9b-4899-8069-e0e3048e911d.sketch_text.stroke-95"),sQuery(id+"FHMxAyK4CFUKdhS_1.wireOp",EDGE,"1cb9c079-ea9b-4899-8069-e0e3048e911d.sketch_text.stroke-96"),sQuery(id+"FHMxAyK4CFUKdhS_1.wireOp",EDGE,"1cb9c079-ea9b-4899-8069-e0e3048e911d.sketch_text.stroke-97"),sQuery(id+"FHMxAyK4CFUKdhS_1.wireOp",EDGE,"1cb9c079-ea9b-4899-8069-e0e3048e911d.sketch_text.stroke-103"),sQuery(id+"FHMxAyK4CFUKdhS_1.wireOp",EDGE,"1cb9c079-ea9b-4899-8069-e0e3048e911d.sketch_text.stroke-104"),sQuery(id+"FHMxAyK4CFUKdhS_1.wireOp",EDGE,"1cb9c079-ea9b-4899-8069-e0e3048e911d.sketch_text.stroke-105"),sQuery(id+"FHMxAyK4CFUKdhS_1.wireOp",EDGE,"1cb9c079-ea9b-4899-8069-e0e3048e911d.sketch_text.stroke-106"),sQuery(id+"FHMxAyK4CFUKdhS_1.wireOp",EDGE,"1cb9c079-ea9b-4899-8069-e0e3048e911d.sketch_text.stroke-107"),sQuery(id+"FHMxAyK4CFUKdhS_1.wireOp",EDGE,"1cb9c079-ea9b-4899-8069-e0e3048e911d.sketch_text.stroke-108"),sQuery(id+"FHMxAyK4CFUKdhS_1.wireOp",EDGE,"1cb9c079-ea9b-4899-8069-e0e3048e911d.sketch_text.stroke-109"),sQuery(id+"FHMxAyK4CFUKdhS_1.wireOp",EDGE,"1cb9c079-ea9b-4899-8069-e0e3048e911d.sketch_text.stroke-110"),sQuery(id+"FHMxAyK4CFUKdhS_1.wireOp",EDGE,"1cb9c079-ea9b-4899-8069-e0e3048e911d.sketch_text.stroke-111"),sQuery(id+"FHMxAyK4CFUKdhS_1.wireOp",EDGE,"1cb9c079-ea9b-4899-8069-e0e3048e911d.sketch_text.stroke-112"),sQuery(id+"FHMxAyK4CFUKdhS_1.wireOp",EDGE,"1cb9c079-ea9b-4899-8069-e0e3048e911d.sketch_text.stroke-113"),sQuery(id+"FHMxAyK4CFUKdhS_1.wireOp",EDGE,"1cb9c079-ea9b-4899-8069-e0e3048e911d.sketch_text.stroke-114"),sQuery(id+"FHMxAyK4CFUKdhS_1.wireOp",EDGE,"1cb9c079-ea9b-4899-8069-e0e3048e911d.sketch_text.stroke-115"),sQuery(id+"FHMxAyK4CFUKdhS_1.wireOp",EDGE,"1cb9c079-ea9b-4899-8069-e0e3048e911d.sketch_text.stroke-116"),sQuery(id+"FHMxAyK4CFUKdhS_1.wireOp",EDGE,"1cb9c079-ea9b-4899-8069-e0e3048e911d.sketch_text.stroke-117"),sQuery(id+"FHMxAyK4CFUKdhS_1.wireOp",EDGE,"1cb9c079-ea9b-4899-8069-e0e3048e911d.sketch_text.stroke-118"),sQuery(id+"FHMxAyK4CFUKdhS_1.wireOp",EDGE,"1cb9c079-ea9b-4899-8069-e0e3048e911d.sketch_text.stroke-119"),sQuery(id+"FHMxAyK4CFUKdhS_1.wireOp",EDGE,"1cb9c079-ea9b-4899-8069-e0e3048e911d.sketch_text.stroke-120"),sQuery(id+"FHMxAyK4CFUKdhS_1.wireOp",EDGE,"1cb9c079-ea9b-4899-8069-e0e3048e911d.sketch_text.stroke-121"),sQuery(id+"FHMxAyK4CFUKdhS_1.wireOp",EDGE,"1cb9c079-ea9b-4899-8069-e0e3048e911d.sketch_text.stroke-122"),sQuery(id+"FHMxAyK4CFUKdhS_1.wireOp",EDGE,"1cb9c079-ea9b-4899-8069-e0e3048e911d.sketch_text.stroke-123"),sQuery(id+"FHMxAyK4CFUKdhS_1.wireOp",EDGE,"1cb9c079-ea9b-4899-8069-e0e3048e911d.sketch_text.stroke-124"),sQuery(id+"FHMxAyK4CFUKdhS_1.wireOp",EDGE,"1cb9c079-ea9b-4899-8069-e0e3048e911d.sketch_text.stroke-125"),sQuery(id+"FHMxAyK4CFUKdhS_1.wireOp",EDGE,"1cb9c079-ea9b-4899-8069-e0e3048e911d.sketch_text.stroke-126"),sQuery(id+"FHMxAyK4CFUKdhS_1.wireOp",EDGE,"1cb9c079-ea9b-4899-8069-e0e3048e911d.sketch_text.stroke-127"),sQuery(id+"FHMxAyK4CFUKdhS_1.wireOp",EDGE,"1cb9c079-ea9b-4899-8069-e0e3048e911d.sketch_text.stroke-128"),sQuery(id+"FHMxAyK4CFUKdhS_1.wireOp",EDGE,"1cb9c079-ea9b-4899-8069-e0e3048e911d.sketch_text.stroke-129"),sQuery(id+"FHMxAyK4CFUKdhS_1.wireOp",EDGE,"1cb9c079-ea9b-4899-8069-e0e3048e911d.sketch_text.stroke-130"),sQuery(id+"FHMxAyK4CFUKdhS_1.wireOp",EDGE,"1cb9c079-ea9b-4899-8069-e0e3048e911d.sketch_text.stroke-131"),sQuery(id+"FHMxAyK4CFUKdhS_1.wireOp",EDGE,"1cb9c079-ea9b-4899-8069-e0e3048e911d.sketch_text.stroke-132"),sQuery(id+"FHMxAyK4CFUKdhS_1.wireOp",EDGE,"1cb9c079-ea9b-4899-8069-e0e3048e911d.sketch_text.stroke-133"),sQuery(id+"FHMxAyK4CFUKdhS_1.wireOp",EDGE,"1cb9c079-ea9b-4899-8069-e0e3048e911d.sketch_text.stroke-134"),sQuery(id+"FHMxAyK4CFUKdhS_1.wireOp",EDGE,"1cb9c079-ea9b-4899-8069-e0e3048e911d.sketch_text.stroke-135"),sQuery(id+"FHMxAyK4CFUKdhS_1.wireOp",EDGE,"1cb9c079-ea9b-4899-8069-e0e3048e911d.sketch_text.stroke-136"),sQuery(id+"FHMxAyK4CFUKdhS_1.wireOp",EDGE,"1cb9c079-ea9b-4899-8069-e0e3048e911d.sketch_text.stroke-137"),sQuery(id+"FHMxAyK4CFUKdhS_1.wireOp",EDGE,"1cb9c079-ea9b-4899-8069-e0e3048e911d.sketch_text.stroke-138"),sQuery(id+"FHMxAyK4CFUKdhS_1.wireOp",EDGE,"1cb9c079-ea9b-4899-8069-e0e3048e911d.sketch_text.stroke-139"),sQuery(id+"FHMxAyK4CFUKdhS_1.wireOp",EDGE,"1cb9c079-ea9b-4899-8069-e0e3048e911d.sketch_text.stroke-140"),sQuery(id+"FHMxAyK4CFUKdhS_1.wireOp",EDGE,"1cb9c079-ea9b-4899-8069-e0e3048e911d.sketch_text.stroke-141"),sQuery(id+"FHMxAyK4CFUKdhS_1.wireOp",EDGE,"1cb9c079-ea9b-4899-8069-e0e3048e911d.sketch_text.stroke-142"),sQuery(id+"FHMxAyK4CFUKdhS_1.wireOp",EDGE,"1cb9c079-ea9b-4899-8069-e0e3048e911d.sketch_text.stroke-143"),sQuery(id+"FHMxAyK4CFUKdhS_1.wireOp",EDGE,"1cb9c079-ea9b-4899-8069-e0e3048e911d.sketch_text.stroke-144"),sQuery(id+"FHMxAyK4CFUKdhS_1.wireOp",EDGE,"1cb9c079-ea9b-4899-8069-e0e3048e911d.sketch_text.stroke-145"),sQuery(id+"FHMxAyK4CFUKdhS_1.wireOp",EDGE,"1cb9c079-ea9b-4899-8069-e0e3048e911d.sketch_text.stroke-146"),sQuery(id+"FHMxAyK4CFUKdhS_1.wireOp",EDGE,"1cb9c079-ea9b-4899-8069-e0e3048e911d.sketch_text.stroke-147"),sQuery(id+"FHMxAyK4CFUKdhS_1.wireOp",EDGE,"1cb9c079-ea9b-4899-8069-e0e3048e911d.sketch_text.stroke-148"),sQuery(id+"FHMxAyK4CFUKdhS_1.wireOp",EDGE,"1cb9c079-ea9b-4899-8069-e0e3048e911d.sketch_text.stroke-149"),sQuery(id+"FHMxAyK4CFUKdhS_1.wireOp",EDGE,"1cb9c079-ea9b-4899-8069-e0e3048e911d.sketch_text.stroke-150"),sQuery(id+"FHMxAyK4CFUKdhS_1.wireOp",EDGE,"1cb9c079-ea9b-4899-8069-e0e3048e911d.sketch_text.stroke-151"),sQuery(id+"FHMxAyK4CFUKdhS_1.wireOp",EDGE,"1cb9c079-ea9b-4899-8069-e0e3048e911d.sketch_text.stroke-152"),sQuery(id+"FHMxAyK4CFUKdhS_1.wireOp",EDGE,"1cb9c079-ea9b-4899-8069-e0e3048e911d.sketch_text.stroke-153"),sQuery(id+"FHMxAyK4CFUKdhS_1.wireOp",EDGE,"1cb9c079-ea9b-4899-8069-e0e3048e911d.sketch_text.stroke-159"),sQuery(id+"FHMxAyK4CFUKdhS_1.wireOp",EDGE,"1cb9c079-ea9b-4899-8069-e0e3048e911d.sketch_text.stroke-160"),sQuery(id+"FHMxAyK4CFUKdhS_1.wireOp",EDGE,"1cb9c079-ea9b-4899-8069-e0e3048e911d.sketch_text.stroke-161"),sQuery(id+"FHMxAyK4CFUKdhS_1.wireOp",EDGE,"1cb9c079-ea9b-4899-8069-e0e3048e911d.sketch_text.stroke-162"),sQuery(id+"FHMxAyK4CFUKdhS_1.wireOp",EDGE,"1cb9c079-ea9b-4899-8069-e0e3048e911d.sketch_text.stroke-163"),sQuery(id+"FHMxAyK4CFUKdhS_1.wireOp",EDGE,"1cb9c079-ea9b-4899-8069-e0e3048e911d.sketch_text.stroke-164"),sQuery(id+"FHMxAyK4CFUKdhS_1.wireOp",EDGE,"1cb9c079-ea9b-4899-8069-e0e3048e911d.sketch_text.stroke-165"),sQuery(id+"FHMxAyK4CFUKdhS_1.wireOp",EDGE,"1cb9c079-ea9b-4899-8069-e0e3048e911d.sketch_text.stroke-166"),sQuery(id+"FHMxAyK4CFUKdhS_1.wireOp",EDGE,"1cb9c079-ea9b-4899-8069-e0e3048e911d.sketch_text.stroke-167"),sQuery(id+"FHMxAyK4CFUKdhS_1.wireOp",EDGE,"1cb9c079-ea9b-4899-8069-e0e3048e911d.sketch_text.stroke-168"),sQuery(id+"FHMxAyK4CFUKdhS_1.wireOp",EDGE,"1cb9c079-ea9b-4899-8069-e0e3048e911d.sketch_text.stroke-169"),sQuery(id+"FHMxAyK4CFUKdhS_1.wireOp",EDGE,"1cb9c079-ea9b-4899-8069-e0e3048e911d.sketch_text.stroke-170"),sQuery(id+"FHMxAyK4CFUKdhS_1.wireOp",EDGE,"1cb9c079-ea9b-4899-8069-e0e3048e911d.sketch_text.stroke-171"),sQuery(id+"FHMxAyK4CFUKdhS_1.wireOp",EDGE,"1cb9c079-ea9b-4899-8069-e0e3048e911d.sketch_text.stroke-172"),sQuery(id+"FHMxAyK4CFUKdhS_1.wireOp",EDGE,"1cb9c079-ea9b-4899-8069-e0e3048e911d.sketch_text.stroke-173"),sQuery(id+"FHMxAyK4CFUKdhS_1.wireOp",EDGE,"1cb9c079-ea9b-4899-8069-e0e3048e911d.sketch_text.stroke-174"),sQuery(id+"FHMxAyK4CFUKdhS_1.wireOp",EDGE,"1cb9c079-ea9b-4899-8069-e0e3048e911d.sketch_text.stroke-175"),sQuery(id+"FHMxAyK4CFUKdhS_1.wireOp",EDGE,"1cb9c079-ea9b-4899-8069-e0e3048e911d.sketch_text.stroke-176"),sQuery(id+"FHMxAyK4CFUKdhS_1.wireOp",EDGE,"1cb9c079-ea9b-4899-8069-e0e3048e911d.sketch_text.stroke-177"),sQuery(id+"FHMxAyK4CFUKdhS_1.wireOp",EDGE,"1cb9c079-ea9b-4899-8069-e0e3048e911d.sketch_text.stroke-178"),sQuery(id+"FHMxAyK4CFUKdhS_1.wireOp",EDGE,"1cb9c079-ea9b-4899-8069-e0e3048e911d.sketch_text.stroke-179"),sQuery(id+"FHMxAyK4CFUKdhS_1.wireOp",EDGE,"1cb9c079-ea9b-4899-8069-e0e3048e911d.sketch_text.stroke-180"),sQuery(id+"F3.wireOp",EDGE,"8007402e-1a4e-4a06-85a5-2af08e553504"),subQ2])],"isStart":true}),makeQuery(id+"F4.opExtrude","SWEPT_FACE",FACE,{"disambiguationData":[OSD([subQ2])]})])],"derivedFrom":makeQuery(id+"F4.opExtrude","CAP_EDGE",EDGE,{"disambiguationData":[OSD([subQ2])],"isStart":true})});}
            var Q10;
            {var subQ0=sQuery(id+"F3.wireOp",EDGE,"8007402e-1a4e-4a06-85a5-2af08e553504");var subQ1=sQuery(id+"F0.wireOp",EDGE,"E0.top");var subQ2=sQuery(id+"F3.wireOp",EDGE,"6ee83ff3-586e-4dbe-aaea-af71240543bd");var subQ3=sQuery(id+"F0.wireOp",EDGE,"E0.bottom");Q10=makeQuery(id+"F4.boolean.opBoolean","SPLIT",EDGE,{"disambiguationData":[TD([makeQuery(id+"F1.opExtrude","CAP_FACE",FACE,{"disambiguationData":[OSD([subQ3,subQ1,sQuery(id+"F0.wireOp",EDGE,"E0.left"),sQuery(id+"F0.wireOp",EDGE,"E0.right")])],"isStart":false}),makeQuery(id+"F1.opExtrude","SWEPT_FACE",FACE,{"disambiguationData":[OSD([subQ1])]}),makeQuery(id+"F4.opExtrude","SWEPT_FACE",FACE,{"disambiguationData":[OSD([subQ0])]}),makeQuery(id+"F4.opExtrude","CAP_FACE",FACE,{"disambiguationData":[OSD([subQ3,sQuery(id+"F2.wireOp",EDGE,"fcba4419-a2ee-464f-be9d-58f11bf3418b.sketch_text.stroke-0"),sQuery(id+"F2.wireOp",EDGE,"fcba4419-a2ee-464f-be9d-58f11bf3418b.sketch_text.stroke-1"),sQuery(id+"F2.wireOp",EDGE,"fcba4419-a2ee-464f-be9d-58f11bf3418b.sketch_text.stroke-2"),sQuery(id+"F2.wireOp",EDGE,"fcba4419-a2ee-464f-be9d-58f11bf3418b.sketch_text.stroke-3"),sQuery(id+"F2.wireOp",EDGE,"fcba4419-a2ee-464f-be9d-58f11bf3418b.sketch_text.stroke-4"),sQuery(id+"F2.wireOp",EDGE,"fcba4419-a2ee-464f-be9d-58f11bf3418b.sketch_text.stroke-5"),sQuery(id+"F2.wireOp",EDGE,"fcba4419-a2ee-464f-be9d-58f11bf3418b.sketch_text.stroke-6"),sQuery(id+"F2.wireOp",EDGE,"fcba4419-a2ee-464f-be9d-58f11bf3418b.sketch_text.stroke-7"),sQuery(id+"F2.wireOp",EDGE,"fcba4419-a2ee-464f-be9d-58f11bf3418b.sketch_text.stroke-8"),sQuery(id+"F2.wireOp",EDGE,"fcba4419-a2ee-464f-be9d-58f11bf3418b.sketch_text.stroke-9"),sQuery(id+"F2.wireOp",EDGE,"fcba4419-a2ee-464f-be9d-58f11bf3418b.sketch_text.stroke-10"),sQuery(id+"F2.wireOp",EDGE,"fcba4419-a2ee-464f-be9d-58f11bf3418b.sketch_text.stroke-11"),sQuery(id+"F2.wireOp",EDGE,"fcba4419-a2ee-464f-be9d-58f11bf3418b.sketch_text.stroke-12"),sQuery(id+"F2.wireOp",EDGE,"fcba4419-a2ee-464f-be9d-58f11bf3418b.sketch_text.stroke-13"),sQuery(id+"F2.wireOp",EDGE,"fcba4419-a2ee-464f-be9d-58f11bf3418b.sketch_text.stroke-14"),sQuery(id+"F2.wireOp",EDGE,"fcba4419-a2ee-464f-be9d-58f11bf3418b.sketch_text.stroke-15"),sQuery(id+"F2.wireOp",EDGE,"fcba4419-a2ee-464f-be9d-58f11bf3418b.sketch_text.stroke-16"),sQuery(id+"F2.wireOp",EDGE,"fcba4419-a2ee-464f-be9d-58f11bf3418b.sketch_text.stroke-17"),sQuery(id+"F2.wireOp",EDGE,"fcba4419-a2ee-464f-be9d-58f11bf3418b.sketch_text.stroke-18"),sQuery(id+"F2.wireOp",EDGE,"fcba4419-a2ee-464f-be9d-58f11bf3418b.sketch_text.stroke-19"),sQuery(id+"F2.wireOp",EDGE,"fcba4419-a2ee-464f-be9d-58f11bf3418b.sketch_text.stroke-20"),sQuery(id+"F2.wireOp",EDGE,"fcba4419-a2ee-464f-be9d-58f11bf3418b.sketch_text.stroke-21"),sQuery(id+"F2.wireOp",EDGE,"fcba4419-a2ee-464f-be9d-58f11bf3418b.sketch_text.stroke-22"),sQuery(id+"F2.wireOp",EDGE,"fcba4419-a2ee-464f-be9d-58f11bf3418b.sketch_text.stroke-23"),sQuery(id+"F2.wireOp",EDGE,"fcba4419-a2ee-464f-be9d-58f11bf3418b.sketch_text.stroke-24"),sQuery(id+"F2.wireOp",EDGE,"fcba4419-a2ee-464f-be9d-58f11bf3418b.sketch_text.stroke-25"),sQuery(id+"F2.wireOp",EDGE,"fcba4419-a2ee-464f-be9d-58f11bf3418b.sketch_text.stroke-26"),sQuery(id+"F2.wireOp",EDGE,"fcba4419-a2ee-464f-be9d-58f11bf3418b.sketch_text.stroke-27"),sQuery(id+"F2.wireOp",EDGE,"fcba4419-a2ee-464f-be9d-58f11bf3418b.sketch_text.stroke-28"),sQuery(id+"F2.wireOp",EDGE,"fcba4419-a2ee-464f-be9d-58f11bf3418b.sketch_text.stroke-29"),sQuery(id+"F2.wireOp",EDGE,"fcba4419-a2ee-464f-be9d-58f11bf3418b.sketch_text.stroke-30"),sQuery(id+"F2.wireOp",EDGE,"fcba4419-a2ee-464f-be9d-58f11bf3418b.sketch_text.stroke-31"),sQuery(id+"F2.wireOp",EDGE,"fcba4419-a2ee-464f-be9d-58f11bf3418b.sketch_text.stroke-32"),sQuery(id+"F2.wireOp",EDGE,"fcba4419-a2ee-464f-be9d-58f11bf3418b.sketch_text.stroke-33"),sQuery(id+"F2.wireOp",EDGE,"fcba4419-a2ee-464f-be9d-58f11bf3418b.sketch_text.stroke-34"),sQuery(id+"F2.wireOp",EDGE,"fcba4419-a2ee-464f-be9d-58f11bf3418b.sketch_text.stroke-35"),sQuery(id+"F2.wireOp",EDGE,"fcba4419-a2ee-464f-be9d-58f11bf3418b.sketch_text.stroke-36"),sQuery(id+"F2.wireOp",EDGE,"fcba4419-a2ee-464f-be9d-58f11bf3418b.sketch_text.stroke-37"),sQuery(id+"F2.wireOp",EDGE,"fcba4419-a2ee-464f-be9d-58f11bf3418b.sketch_text.stroke-38"),sQuery(id+"F2.wireOp",EDGE,"fcba4419-a2ee-464f-be9d-58f11bf3418b.sketch_text.stroke-39"),sQuery(id+"F2.wireOp",EDGE,"fcba4419-a2ee-464f-be9d-58f11bf3418b.sketch_text.stroke-40"),sQuery(id+"F2.wireOp",EDGE,"fcba4419-a2ee-464f-be9d-58f11bf3418b.sketch_text.stroke-41"),sQuery(id+"F2.wireOp",EDGE,"fcba4419-a2ee-464f-be9d-58f11bf3418b.sketch_text.stroke-42"),sQuery(id+"F2.wireOp",EDGE,"fcba4419-a2ee-464f-be9d-58f11bf3418b.sketch_text.stroke-43"),sQuery(id+"F2.wireOp",EDGE,"fcba4419-a2ee-464f-be9d-58f11bf3418b.sketch_text.stroke-44"),sQuery(id+"F2.wireOp",EDGE,"fcba4419-a2ee-464f-be9d-58f11bf3418b.sketch_text.stroke-45"),sQuery(id+"F2.wireOp",EDGE,"fcba4419-a2ee-464f-be9d-58f11bf3418b.sketch_text.stroke-46"),sQuery(id+"F2.wireOp",EDGE,"fcba4419-a2ee-464f-be9d-58f11bf3418b.sketch_text.stroke-47"),sQuery(id+"F2.wireOp",EDGE,"fcba4419-a2ee-464f-be9d-58f11bf3418b.sketch_text.stroke-48"),sQuery(id+"F2.wireOp",EDGE,"fcba4419-a2ee-464f-be9d-58f11bf3418b.sketch_text.stroke-49"),sQuery(id+"F2.wireOp",EDGE,"fcba4419-a2ee-464f-be9d-58f11bf3418b.sketch_text.stroke-50"),sQuery(id+"F2.wireOp",EDGE,"fcba4419-a2ee-464f-be9d-58f11bf3418b.sketch_text.stroke-51"),sQuery(id+"F2.wireOp",EDGE,"fcba4419-a2ee-464f-be9d-58f11bf3418b.sketch_text.stroke-52"),sQuery(id+"F2.wireOp",EDGE,"fcba4419-a2ee-464f-be9d-58f11bf3418b.sketch_text.stroke-53"),sQuery(id+"F2.wireOp",EDGE,"fcba4419-a2ee-464f-be9d-58f11bf3418b.sketch_text.stroke-54"),sQuery(id+"F2.wireOp",EDGE,"fcba4419-a2ee-464f-be9d-58f11bf3418b.sketch_text.stroke-55"),sQuery(id+"F2.wireOp",EDGE,"fcba4419-a2ee-464f-be9d-58f11bf3418b.sketch_text.stroke-56"),sQuery(id+"F2.wireOp",EDGE,"fcba4419-a2ee-464f-be9d-58f11bf3418b.sketch_text.stroke-57"),sQuery(id+"F2.wireOp",EDGE,"fcba4419-a2ee-464f-be9d-58f11bf3418b.sketch_text.stroke-58"),sQuery(id+"F2.wireOp",EDGE,"fcba4419-a2ee-464f-be9d-58f11bf3418b.sketch_text.stroke-59"),sQuery(id+"F2.wireOp",EDGE,"fcba4419-a2ee-464f-be9d-58f11bf3418b.sketch_text.stroke-60"),sQuery(id+"F2.wireOp",EDGE,"fcba4419-a2ee-464f-be9d-58f11bf3418b.sketch_text.stroke-61"),sQuery(id+"F2.wireOp",EDGE,"fcba4419-a2ee-464f-be9d-58f11bf3418b.sketch_text.stroke-62"),sQuery(id+"F2.wireOp",EDGE,"fcba4419-a2ee-464f-be9d-58f11bf3418b.sketch_text.stroke-63"),sQuery(id+"F2.wireOp",EDGE,"fcba4419-a2ee-464f-be9d-58f11bf3418b.sketch_text.stroke-64"),sQuery(id+"F2.wireOp",EDGE,"fcba4419-a2ee-464f-be9d-58f11bf3418b.sketch_text.stroke-65"),sQuery(id+"F2.wireOp",EDGE,"fcba4419-a2ee-464f-be9d-58f11bf3418b.sketch_text.stroke-66"),sQuery(id+"F2.wireOp",EDGE,"fcba4419-a2ee-464f-be9d-58f11bf3418b.sketch_text.stroke-67"),sQuery(id+"F2.wireOp",EDGE,"fcba4419-a2ee-464f-be9d-58f11bf3418b.sketch_text.stroke-68"),sQuery(id+"F2.wireOp",EDGE,"fcba4419-a2ee-464f-be9d-58f11bf3418b.sketch_text.stroke-69"),sQuery(id+"F2.wireOp",EDGE,"fcba4419-a2ee-464f-be9d-58f11bf3418b.sketch_text.stroke-70"),sQuery(id+"F2.wireOp",EDGE,"fcba4419-a2ee-464f-be9d-58f11bf3418b.sketch_text.stroke-71"),sQuery(id+"F2.wireOp",EDGE,"fcba4419-a2ee-464f-be9d-58f11bf3418b.sketch_text.stroke-72"),sQuery(id+"F2.wireOp",EDGE,"fcba4419-a2ee-464f-be9d-58f11bf3418b.sketch_text.stroke-73"),sQuery(id+"F2.wireOp",EDGE,"fcba4419-a2ee-464f-be9d-58f11bf3418b.sketch_text.stroke-74"),sQuery(id+"F2.wireOp",EDGE,"fcba4419-a2ee-464f-be9d-58f11bf3418b.sketch_text.stroke-75"),sQuery(id+"F2.wireOp",EDGE,"fcba4419-a2ee-464f-be9d-58f11bf3418b.sketch_text.stroke-76"),sQuery(id+"F2.wireOp",EDGE,"fcba4419-a2ee-464f-be9d-58f11bf3418b.sketch_text.stroke-77"),sQuery(id+"F2.wireOp",EDGE,"fcba4419-a2ee-464f-be9d-58f11bf3418b.sketch_text.stroke-78"),sQuery(id+"F2.wireOp",EDGE,"fcba4419-a2ee-464f-be9d-58f11bf3418b.sketch_text.stroke-79"),sQuery(id+"F2.wireOp",EDGE,"fcba4419-a2ee-464f-be9d-58f11bf3418b.sketch_text.stroke-80"),sQuery(id+"F2.wireOp",EDGE,"fcba4419-a2ee-464f-be9d-58f11bf3418b.sketch_text.stroke-81"),sQuery(id+"F2.wireOp",EDGE,"fcba4419-a2ee-464f-be9d-58f11bf3418b.sketch_text.stroke-82"),sQuery(id+"F2.wireOp",EDGE,"fcba4419-a2ee-464f-be9d-58f11bf3418b.sketch_text.stroke-83"),sQuery(id+"F2.wireOp",EDGE,"fcba4419-a2ee-464f-be9d-58f11bf3418b.sketch_text.stroke-84"),sQuery(id+"F2.wireOp",EDGE,"fcba4419-a2ee-464f-be9d-58f11bf3418b.sketch_text.stroke-85"),sQuery(id+"F2.wireOp",EDGE,"fcba4419-a2ee-464f-be9d-58f11bf3418b.sketch_text.stroke-86"),sQuery(id+"F2.wireOp",EDGE,"fcba4419-a2ee-464f-be9d-58f11bf3418b.sketch_text.stroke-87"),sQuery(id+"F2.wireOp",EDGE,"fcba4419-a2ee-464f-be9d-58f11bf3418b.sketch_text.stroke-88"),sQuery(id+"F2.wireOp",EDGE,"fcba4419-a2ee-464f-be9d-58f11bf3418b.sketch_text.stroke-89"),sQuery(id+"F2.wireOp",EDGE,"fcba4419-a2ee-464f-be9d-58f11bf3418b.sketch_text.stroke-90"),sQuery(id+"F2.wireOp",EDGE,"fcba4419-a2ee-464f-be9d-58f11bf3418b.sketch_text.stroke-91"),sQuery(id+"F2.wireOp",EDGE,"fcba4419-a2ee-464f-be9d-58f11bf3418b.sketch_text.stroke-92"),sQuery(id+"F2.wireOp",EDGE,"fcba4419-a2ee-464f-be9d-58f11bf3418b.sketch_text.stroke-93"),sQuery(id+"F2.wireOp",EDGE,"fcba4419-a2ee-464f-be9d-58f11bf3418b.sketch_text.stroke-94"),sQuery(id+"F2.wireOp",EDGE,"fcba4419-a2ee-464f-be9d-58f11bf3418b.sketch_text.stroke-95"),sQuery(id+"F2.wireOp",EDGE,"fcba4419-a2ee-464f-be9d-58f11bf3418b.sketch_text.stroke-96"),sQuery(id+"F2.wireOp",EDGE,"fcba4419-a2ee-464f-be9d-58f11bf3418b.sketch_text.stroke-97"),sQuery(id+"F2.wireOp",EDGE,"fcba4419-a2ee-464f-be9d-58f11bf3418b.sketch_text.stroke-98"),sQuery(id+"F2.wireOp",EDGE,"fcba4419-a2ee-464f-be9d-58f11bf3418b.sketch_text.stroke-99"),sQuery(id+"F2.wireOp",EDGE,"fcba4419-a2ee-464f-be9d-58f11bf3418b.sketch_text.stroke-100"),sQuery(id+"F2.wireOp",EDGE,"fcba4419-a2ee-464f-be9d-58f11bf3418b.sketch_text.stroke-101"),sQuery(id+"F2.wireOp",EDGE,"fcba4419-a2ee-464f-be9d-58f11bf3418b.sketch_text.stroke-102"),sQuery(id+"F2.wireOp",EDGE,"fcba4419-a2ee-464f-be9d-58f11bf3418b.sketch_text.stroke-103"),sQuery(id+"F2.wireOp",EDGE,"fcba4419-a2ee-464f-be9d-58f11bf3418b.sketch_text.stroke-104"),sQuery(id+"F2.wireOp",EDGE,"fcba4419-a2ee-464f-be9d-58f11bf3418b.sketch_text.stroke-105"),sQuery(id+"F2.wireOp",EDGE,"fcba4419-a2ee-464f-be9d-58f11bf3418b.sketch_text.stroke-106"),sQuery(id+"F2.wireOp",EDGE,"fcba4419-a2ee-464f-be9d-58f11bf3418b.sketch_text.stroke-107"),sQuery(id+"F2.wireOp",EDGE,"fcba4419-a2ee-464f-be9d-58f11bf3418b.sketch_text.stroke-108"),sQuery(id+"F2.wireOp",EDGE,"fcba4419-a2ee-464f-be9d-58f11bf3418b.sketch_text.stroke-109"),sQuery(id+"F2.wireOp",EDGE,"fcba4419-a2ee-464f-be9d-58f11bf3418b.sketch_text.stroke-110"),sQuery(id+"F2.wireOp",EDGE,"fcba4419-a2ee-464f-be9d-58f11bf3418b.sketch_text.stroke-111"),sQuery(id+"F2.wireOp",EDGE,"fcba4419-a2ee-464f-be9d-58f11bf3418b.sketch_text.stroke-112"),sQuery(id+"F2.wireOp",EDGE,"fcba4419-a2ee-464f-be9d-58f11bf3418b.sketch_text.stroke-113"),sQuery(id+"F2.wireOp",EDGE,"fcba4419-a2ee-464f-be9d-58f11bf3418b.sketch_text.stroke-114"),sQuery(id+"F2.wireOp",EDGE,"fcba4419-a2ee-464f-be9d-58f11bf3418b.sketch_text.stroke-115"),sQuery(id+"F2.wireOp",EDGE,"fcba4419-a2ee-464f-be9d-58f11bf3418b.sketch_text.stroke-116"),sQuery(id+"F2.wireOp",EDGE,"fcba4419-a2ee-464f-be9d-58f11bf3418b.sketch_text.stroke-117"),sQuery(id+"F2.wireOp",EDGE,"fcba4419-a2ee-464f-be9d-58f11bf3418b.sketch_text.stroke-118"),sQuery(id+"F2.wireOp",EDGE,"fcba4419-a2ee-464f-be9d-58f11bf3418b.sketch_text.stroke-119"),sQuery(id+"F2.wireOp",EDGE,"fcba4419-a2ee-464f-be9d-58f11bf3418b.sketch_text.stroke-120"),sQuery(id+"F2.wireOp",EDGE,"fcba4419-a2ee-464f-be9d-58f11bf3418b.sketch_text.stroke-121"),sQuery(id+"F2.wireOp",EDGE,"fcba4419-a2ee-464f-be9d-58f11bf3418b.sketch_text.stroke-122"),sQuery(id+"F2.wireOp",EDGE,"fcba4419-a2ee-464f-be9d-58f11bf3418b.sketch_text.stroke-123"),sQuery(id+"F2.wireOp",EDGE,"fcba4419-a2ee-464f-be9d-58f11bf3418b.sketch_text.stroke-124"),sQuery(id+"F2.wireOp",EDGE,"fcba4419-a2ee-464f-be9d-58f11bf3418b.sketch_text.stroke-125"),sQuery(id+"F2.wireOp",EDGE,"fcba4419-a2ee-464f-be9d-58f11bf3418b.sketch_text.stroke-126"),sQuery(id+"F2.wireOp",EDGE,"fcba4419-a2ee-464f-be9d-58f11bf3418b.sketch_text.stroke-127"),sQuery(id+"F2.wireOp",EDGE,"fcba4419-a2ee-464f-be9d-58f11bf3418b.sketch_text.stroke-128"),sQuery(id+"F2.wireOp",EDGE,"fcba4419-a2ee-464f-be9d-58f11bf3418b.sketch_text.stroke-129"),sQuery(id+"F2.wireOp",EDGE,"fcba4419-a2ee-464f-be9d-58f11bf3418b.sketch_text.stroke-130"),sQuery(id+"F2.wireOp",EDGE,"fcba4419-a2ee-464f-be9d-58f11bf3418b.sketch_text.stroke-131"),sQuery(id+"F2.wireOp",EDGE,"fcba4419-a2ee-464f-be9d-58f11bf3418b.sketch_text.stroke-132"),sQuery(id+"F2.wireOp",EDGE,"fcba4419-a2ee-464f-be9d-58f11bf3418b.sketch_text.stroke-133"),sQuery(id+"F2.wireOp",EDGE,"fcba4419-a2ee-464f-be9d-58f11bf3418b.sketch_text.stroke-134"),sQuery(id+"F2.wireOp",EDGE,"fcba4419-a2ee-464f-be9d-58f11bf3418b.sketch_text.stroke-135"),sQuery(id+"F2.wireOp",EDGE,"fcba4419-a2ee-464f-be9d-58f11bf3418b.sketch_text.stroke-136"),sQuery(id+"F2.wireOp",EDGE,"fcba4419-a2ee-464f-be9d-58f11bf3418b.sketch_text.stroke-137"),sQuery(id+"F2.wireOp",EDGE,"fcba4419-a2ee-464f-be9d-58f11bf3418b.sketch_text.stroke-138"),sQuery(id+"F2.wireOp",EDGE,"fcba4419-a2ee-464f-be9d-58f11bf3418b.sketch_text.stroke-139"),sQuery(id+"F2.wireOp",EDGE,"fcba4419-a2ee-464f-be9d-58f11bf3418b.sketch_text.stroke-140"),sQuery(id+"F2.wireOp",EDGE,"fcba4419-a2ee-464f-be9d-58f11bf3418b.sketch_text.stroke-141"),sQuery(id+"F2.wireOp",EDGE,"fcba4419-a2ee-464f-be9d-58f11bf3418b.sketch_text.stroke-142"),sQuery(id+"F2.wireOp",EDGE,"fcba4419-a2ee-464f-be9d-58f11bf3418b.sketch_text.stroke-143"),sQuery(id+"F2.wireOp",EDGE,"fcba4419-a2ee-464f-be9d-58f11bf3418b.sketch_text.stroke-144"),sQuery(id+"F2.wireOp",EDGE,"fcba4419-a2ee-464f-be9d-58f11bf3418b.sketch_text.stroke-145"),sQuery(id+"F2.wireOp",EDGE,"fcba4419-a2ee-464f-be9d-58f11bf3418b.sketch_text.stroke-146"),sQuery(id+"F2.wireOp",EDGE,"fcba4419-a2ee-464f-be9d-58f11bf3418b.sketch_text.stroke-147"),sQuery(id+"F2.wireOp",EDGE,"fcba4419-a2ee-464f-be9d-58f11bf3418b.sketch_text.stroke-148"),sQuery(id+"F2.wireOp",EDGE,"fcba4419-a2ee-464f-be9d-58f11bf3418b.sketch_text.stroke-149"),sQuery(id+"F2.wireOp",EDGE,"fcba4419-a2ee-464f-be9d-58f11bf3418b.sketch_text.stroke-150"),sQuery(id+"F2.wireOp",EDGE,"fcba4419-a2ee-464f-be9d-58f11bf3418b.sketch_text.stroke-151"),sQuery(id+"F2.wireOp",EDGE,"fcba4419-a2ee-464f-be9d-58f11bf3418b.sketch_text.stroke-152"),sQuery(id+"F2.wireOp",EDGE,"fcba4419-a2ee-464f-be9d-58f11bf3418b.sketch_text.stroke-153"),sQuery(id+"F2.wireOp",EDGE,"fcba4419-a2ee-464f-be9d-58f11bf3418b.sketch_text.stroke-154"),sQuery(id+"F2.wireOp",EDGE,"fcba4419-a2ee-464f-be9d-58f11bf3418b.sketch_text.stroke-155"),sQuery(id+"F2.wireOp",EDGE,"fcba4419-a2ee-464f-be9d-58f11bf3418b.sketch_text.stroke-156"),sQuery(id+"F2.wireOp",EDGE,"fcba4419-a2ee-464f-be9d-58f11bf3418b.sketch_text.stroke-157"),sQuery(id+"F2.wireOp",EDGE,"fcba4419-a2ee-464f-be9d-58f11bf3418b.sketch_text.stroke-158"),sQuery(id+"F2.wireOp",EDGE,"fcba4419-a2ee-464f-be9d-58f11bf3418b.sketch_text.stroke-159"),sQuery(id+"F2.wireOp",EDGE,"fcba4419-a2ee-464f-be9d-58f11bf3418b.sketch_text.stroke-160"),sQuery(id+"F2.wireOp",EDGE,"fcba4419-a2ee-464f-be9d-58f11bf3418b.sketch_text.stroke-161"),sQuery(id+"F2.wireOp",EDGE,"fcba4419-a2ee-464f-be9d-58f11bf3418b.sketch_text.stroke-162"),sQuery(id+"F2.wireOp",EDGE,"fcba4419-a2ee-464f-be9d-58f11bf3418b.sketch_text.stroke-163"),sQuery(id+"F2.wireOp",EDGE,"fcba4419-a2ee-464f-be9d-58f11bf3418b.sketch_text.stroke-164"),sQuery(id+"F2.wireOp",EDGE,"fcba4419-a2ee-464f-be9d-58f11bf3418b.sketch_text.stroke-165"),sQuery(id+"F2.wireOp",EDGE,"fcba4419-a2ee-464f-be9d-58f11bf3418b.sketch_text.stroke-166"),sQuery(id+"F2.wireOp",EDGE,"fcba4419-a2ee-464f-be9d-58f11bf3418b.sketch_text.stroke-167"),sQuery(id+"F2.wireOp",EDGE,"fcba4419-a2ee-464f-be9d-58f11bf3418b.sketch_text.stroke-168"),sQuery(id+"F2.wireOp",EDGE,"fcba4419-a2ee-464f-be9d-58f11bf3418b.sketch_text.stroke-169"),sQuery(id+"F2.wireOp",EDGE,"fcba4419-a2ee-464f-be9d-58f11bf3418b.sketch_text.stroke-170"),sQuery(id+"F2.wireOp",EDGE,"fcba4419-a2ee-464f-be9d-58f11bf3418b.sketch_text.stroke-171"),sQuery(id+"F2.wireOp",EDGE,"fcba4419-a2ee-464f-be9d-58f11bf3418b.sketch_text.stroke-172"),sQuery(id+"F2.wireOp",EDGE,"fcba4419-a2ee-464f-be9d-58f11bf3418b.sketch_text.stroke-173"),sQuery(id+"FHMxAyK4CFUKdhS_1.wireOp",EDGE,"1cb9c079-ea9b-4899-8069-e0e3048e911d.sketch_text.stroke-0"),sQuery(id+"FHMxAyK4CFUKdhS_1.wireOp",EDGE,"1cb9c079-ea9b-4899-8069-e0e3048e911d.sketch_text.stroke-1"),sQuery(id+"FHMxAyK4CFUKdhS_1.wireOp",EDGE,"1cb9c079-ea9b-4899-8069-e0e3048e911d.sketch_text.stroke-2"),sQuery(id+"FHMxAyK4CFUKdhS_1.wireOp",EDGE,"1cb9c079-ea9b-4899-8069-e0e3048e911d.sketch_text.stroke-3"),sQuery(id+"FHMxAyK4CFUKdhS_1.wireOp",EDGE,"1cb9c079-ea9b-4899-8069-e0e3048e911d.sketch_text.stroke-4"),sQuery(id+"FHMxAyK4CFUKdhS_1.wireOp",EDGE,"1cb9c079-ea9b-4899-8069-e0e3048e911d.sketch_text.stroke-5"),sQuery(id+"FHMxAyK4CFUKdhS_1.wireOp",EDGE,"1cb9c079-ea9b-4899-8069-e0e3048e911d.sketch_text.stroke-6"),sQuery(id+"FHMxAyK4CFUKdhS_1.wireOp",EDGE,"1cb9c079-ea9b-4899-8069-e0e3048e911d.sketch_text.stroke-7"),sQuery(id+"FHMxAyK4CFUKdhS_1.wireOp",EDGE,"1cb9c079-ea9b-4899-8069-e0e3048e911d.sketch_text.stroke-8"),sQuery(id+"FHMxAyK4CFUKdhS_1.wireOp",EDGE,"1cb9c079-ea9b-4899-8069-e0e3048e911d.sketch_text.stroke-9"),sQuery(id+"FHMxAyK4CFUKdhS_1.wireOp",EDGE,"1cb9c079-ea9b-4899-8069-e0e3048e911d.sketch_text.stroke-10"),sQuery(id+"FHMxAyK4CFUKdhS_1.wireOp",EDGE,"1cb9c079-ea9b-4899-8069-e0e3048e911d.sketch_text.stroke-11"),sQuery(id+"FHMxAyK4CFUKdhS_1.wireOp",EDGE,"1cb9c079-ea9b-4899-8069-e0e3048e911d.sketch_text.stroke-12"),sQuery(id+"FHMxAyK4CFUKdhS_1.wireOp",EDGE,"1cb9c079-ea9b-4899-8069-e0e3048e911d.sketch_text.stroke-13"),sQuery(id+"FHMxAyK4CFUKdhS_1.wireOp",EDGE,"1cb9c079-ea9b-4899-8069-e0e3048e911d.sketch_text.stroke-14"),sQuery(id+"FHMxAyK4CFUKdhS_1.wireOp",EDGE,"1cb9c079-ea9b-4899-8069-e0e3048e911d.sketch_text.stroke-15"),sQuery(id+"FHMxAyK4CFUKdhS_1.wireOp",EDGE,"1cb9c079-ea9b-4899-8069-e0e3048e911d.sketch_text.stroke-16"),sQuery(id+"FHMxAyK4CFUKdhS_1.wireOp",EDGE,"1cb9c079-ea9b-4899-8069-e0e3048e911d.sketch_text.stroke-17"),sQuery(id+"FHMxAyK4CFUKdhS_1.wireOp",EDGE,"1cb9c079-ea9b-4899-8069-e0e3048e911d.sketch_text.stroke-18"),sQuery(id+"FHMxAyK4CFUKdhS_1.wireOp",EDGE,"1cb9c079-ea9b-4899-8069-e0e3048e911d.sketch_text.stroke-19"),sQuery(id+"FHMxAyK4CFUKdhS_1.wireOp",EDGE,"1cb9c079-ea9b-4899-8069-e0e3048e911d.sketch_text.stroke-20"),sQuery(id+"FHMxAyK4CFUKdhS_1.wireOp",EDGE,"1cb9c079-ea9b-4899-8069-e0e3048e911d.sketch_text.stroke-21"),sQuery(id+"FHMxAyK4CFUKdhS_1.wireOp",EDGE,"1cb9c079-ea9b-4899-8069-e0e3048e911d.sketch_text.stroke-22"),sQuery(id+"FHMxAyK4CFUKdhS_1.wireOp",EDGE,"1cb9c079-ea9b-4899-8069-e0e3048e911d.sketch_text.stroke-23"),sQuery(id+"FHMxAyK4CFUKdhS_1.wireOp",EDGE,"1cb9c079-ea9b-4899-8069-e0e3048e911d.sketch_text.stroke-24"),sQuery(id+"FHMxAyK4CFUKdhS_1.wireOp",EDGE,"1cb9c079-ea9b-4899-8069-e0e3048e911d.sketch_text.stroke-25"),sQuery(id+"FHMxAyK4CFUKdhS_1.wireOp",EDGE,"1cb9c079-ea9b-4899-8069-e0e3048e911d.sketch_text.stroke-26"),sQuery(id+"FHMxAyK4CFUKdhS_1.wireOp",EDGE,"1cb9c079-ea9b-4899-8069-e0e3048e911d.sketch_text.stroke-27"),sQuery(id+"FHMxAyK4CFUKdhS_1.wireOp",EDGE,"1cb9c079-ea9b-4899-8069-e0e3048e911d.sketch_text.stroke-28"),sQuery(id+"FHMxAyK4CFUKdhS_1.wireOp",EDGE,"1cb9c079-ea9b-4899-8069-e0e3048e911d.sketch_text.stroke-29"),sQuery(id+"FHMxAyK4CFUKdhS_1.wireOp",EDGE,"1cb9c079-ea9b-4899-8069-e0e3048e911d.sketch_text.stroke-30"),sQuery(id+"FHMxAyK4CFUKdhS_1.wireOp",EDGE,"1cb9c079-ea9b-4899-8069-e0e3048e911d.sketch_text.stroke-31"),sQuery(id+"FHMxAyK4CFUKdhS_1.wireOp",EDGE,"1cb9c079-ea9b-4899-8069-e0e3048e911d.sketch_text.stroke-32"),sQuery(id+"FHMxAyK4CFUKdhS_1.wireOp",EDGE,"1cb9c079-ea9b-4899-8069-e0e3048e911d.sketch_text.stroke-33"),sQuery(id+"FHMxAyK4CFUKdhS_1.wireOp",EDGE,"1cb9c079-ea9b-4899-8069-e0e3048e911d.sketch_text.stroke-34"),sQuery(id+"FHMxAyK4CFUKdhS_1.wireOp",EDGE,"1cb9c079-ea9b-4899-8069-e0e3048e911d.sketch_text.stroke-35"),sQuery(id+"FHMxAyK4CFUKdhS_1.wireOp",EDGE,"1cb9c079-ea9b-4899-8069-e0e3048e911d.sketch_text.stroke-36"),sQuery(id+"FHMxAyK4CFUKdhS_1.wireOp",EDGE,"1cb9c079-ea9b-4899-8069-e0e3048e911d.sketch_text.stroke-37"),sQuery(id+"FHMxAyK4CFUKdhS_1.wireOp",EDGE,"1cb9c079-ea9b-4899-8069-e0e3048e911d.sketch_text.stroke-38"),sQuery(id+"FHMxAyK4CFUKdhS_1.wireOp",EDGE,"1cb9c079-ea9b-4899-8069-e0e3048e911d.sketch_text.stroke-39"),sQuery(id+"FHMxAyK4CFUKdhS_1.wireOp",EDGE,"1cb9c079-ea9b-4899-8069-e0e3048e911d.sketch_text.stroke-40"),sQuery(id+"FHMxAyK4CFUKdhS_1.wireOp",EDGE,"1cb9c079-ea9b-4899-8069-e0e3048e911d.sketch_text.stroke-41"),sQuery(id+"FHMxAyK4CFUKdhS_1.wireOp",EDGE,"1cb9c079-ea9b-4899-8069-e0e3048e911d.sketch_text.stroke-42"),sQuery(id+"FHMxAyK4CFUKdhS_1.wireOp",EDGE,"1cb9c079-ea9b-4899-8069-e0e3048e911d.sketch_text.stroke-43"),sQuery(id+"FHMxAyK4CFUKdhS_1.wireOp",EDGE,"1cb9c079-ea9b-4899-8069-e0e3048e911d.sketch_text.stroke-44"),sQuery(id+"FHMxAyK4CFUKdhS_1.wireOp",EDGE,"1cb9c079-ea9b-4899-8069-e0e3048e911d.sketch_text.stroke-45"),sQuery(id+"FHMxAyK4CFUKdhS_1.wireOp",EDGE,"1cb9c079-ea9b-4899-8069-e0e3048e911d.sketch_text.stroke-46"),sQuery(id+"FHMxAyK4CFUKdhS_1.wireOp",EDGE,"1cb9c079-ea9b-4899-8069-e0e3048e911d.sketch_text.stroke-47"),sQuery(id+"FHMxAyK4CFUKdhS_1.wireOp",EDGE,"1cb9c079-ea9b-4899-8069-e0e3048e911d.sketch_text.stroke-48"),sQuery(id+"FHMxAyK4CFUKdhS_1.wireOp",EDGE,"1cb9c079-ea9b-4899-8069-e0e3048e911d.sketch_text.stroke-49"),sQuery(id+"FHMxAyK4CFUKdhS_1.wireOp",EDGE,"1cb9c079-ea9b-4899-8069-e0e3048e911d.sketch_text.stroke-50"),sQuery(id+"FHMxAyK4CFUKdhS_1.wireOp",EDGE,"1cb9c079-ea9b-4899-8069-e0e3048e911d.sketch_text.stroke-51"),sQuery(id+"FHMxAyK4CFUKdhS_1.wireOp",EDGE,"1cb9c079-ea9b-4899-8069-e0e3048e911d.sketch_text.stroke-52"),sQuery(id+"FHMxAyK4CFUKdhS_1.wireOp",EDGE,"1cb9c079-ea9b-4899-8069-e0e3048e911d.sketch_text.stroke-53"),sQuery(id+"FHMxAyK4CFUKdhS_1.wireOp",EDGE,"1cb9c079-ea9b-4899-8069-e0e3048e911d.sketch_text.stroke-54"),sQuery(id+"FHMxAyK4CFUKdhS_1.wireOp",EDGE,"1cb9c079-ea9b-4899-8069-e0e3048e911d.sketch_text.stroke-55"),sQuery(id+"FHMxAyK4CFUKdhS_1.wireOp",EDGE,"1cb9c079-ea9b-4899-8069-e0e3048e911d.sketch_text.stroke-56"),sQuery(id+"FHMxAyK4CFUKdhS_1.wireOp",EDGE,"1cb9c079-ea9b-4899-8069-e0e3048e911d.sketch_text.stroke-57"),sQuery(id+"FHMxAyK4CFUKdhS_1.wireOp",EDGE,"1cb9c079-ea9b-4899-8069-e0e3048e911d.sketch_text.stroke-58"),sQuery(id+"FHMxAyK4CFUKdhS_1.wireOp",EDGE,"1cb9c079-ea9b-4899-8069-e0e3048e911d.sketch_text.stroke-59"),sQuery(id+"FHMxAyK4CFUKdhS_1.wireOp",EDGE,"1cb9c079-ea9b-4899-8069-e0e3048e911d.sketch_text.stroke-60"),sQuery(id+"FHMxAyK4CFUKdhS_1.wireOp",EDGE,"1cb9c079-ea9b-4899-8069-e0e3048e911d.sketch_text.stroke-61"),sQuery(id+"FHMxAyK4CFUKdhS_1.wireOp",EDGE,"1cb9c079-ea9b-4899-8069-e0e3048e911d.sketch_text.stroke-62"),sQuery(id+"FHMxAyK4CFUKdhS_1.wireOp",EDGE,"1cb9c079-ea9b-4899-8069-e0e3048e911d.sketch_text.stroke-71"),sQuery(id+"FHMxAyK4CFUKdhS_1.wireOp",EDGE,"1cb9c079-ea9b-4899-8069-e0e3048e911d.sketch_text.stroke-72"),sQuery(id+"FHMxAyK4CFUKdhS_1.wireOp",EDGE,"1cb9c079-ea9b-4899-8069-e0e3048e911d.sketch_text.stroke-73"),sQuery(id+"FHMxAyK4CFUKdhS_1.wireOp",EDGE,"1cb9c079-ea9b-4899-8069-e0e3048e911d.sketch_text.stroke-74"),sQuery(id+"FHMxAyK4CFUKdhS_1.wireOp",EDGE,"1cb9c079-ea9b-4899-8069-e0e3048e911d.sketch_text.stroke-75"),sQuery(id+"FHMxAyK4CFUKdhS_1.wireOp",EDGE,"1cb9c079-ea9b-4899-8069-e0e3048e911d.sketch_text.stroke-76"),sQuery(id+"FHMxAyK4CFUKdhS_1.wireOp",EDGE,"1cb9c079-ea9b-4899-8069-e0e3048e911d.sketch_text.stroke-77"),sQuery(id+"FHMxAyK4CFUKdhS_1.wireOp",EDGE,"1cb9c079-ea9b-4899-8069-e0e3048e911d.sketch_text.stroke-78"),sQuery(id+"FHMxAyK4CFUKdhS_1.wireOp",EDGE,"1cb9c079-ea9b-4899-8069-e0e3048e911d.sketch_text.stroke-79"),sQuery(id+"FHMxAyK4CFUKdhS_1.wireOp",EDGE,"1cb9c079-ea9b-4899-8069-e0e3048e911d.sketch_text.stroke-80"),sQuery(id+"FHMxAyK4CFUKdhS_1.wireOp",EDGE,"1cb9c079-ea9b-4899-8069-e0e3048e911d.sketch_text.stroke-81"),sQuery(id+"FHMxAyK4CFUKdhS_1.wireOp",EDGE,"1cb9c079-ea9b-4899-8069-e0e3048e911d.sketch_text.stroke-82"),sQuery(id+"FHMxAyK4CFUKdhS_1.wireOp",EDGE,"1cb9c079-ea9b-4899-8069-e0e3048e911d.sketch_text.stroke-83"),sQuery(id+"FHMxAyK4CFUKdhS_1.wireOp",EDGE,"1cb9c079-ea9b-4899-8069-e0e3048e911d.sketch_text.stroke-84"),sQuery(id+"FHMxAyK4CFUKdhS_1.wireOp",EDGE,"1cb9c079-ea9b-4899-8069-e0e3048e911d.sketch_text.stroke-85"),sQuery(id+"FHMxAyK4CFUKdhS_1.wireOp",EDGE,"1cb9c079-ea9b-4899-8069-e0e3048e911d.sketch_text.stroke-86"),sQuery(id+"FHMxAyK4CFUKdhS_1.wireOp",EDGE,"1cb9c079-ea9b-4899-8069-e0e3048e911d.sketch_text.stroke-87"),sQuery(id+"FHMxAyK4CFUKdhS_1.wireOp",EDGE,"1cb9c079-ea9b-4899-8069-e0e3048e911d.sketch_text.stroke-88"),sQuery(id+"FHMxAyK4CFUKdhS_1.wireOp",EDGE,"1cb9c079-ea9b-4899-8069-e0e3048e911d.sketch_text.stroke-89"),sQuery(id+"FHMxAyK4CFUKdhS_1.wireOp",EDGE,"1cb9c079-ea9b-4899-8069-e0e3048e911d.sketch_text.stroke-90"),sQuery(id+"FHMxAyK4CFUKdhS_1.wireOp",EDGE,"1cb9c079-ea9b-4899-8069-e0e3048e911d.sketch_text.stroke-91"),sQuery(id+"FHMxAyK4CFUKdhS_1.wireOp",EDGE,"1cb9c079-ea9b-4899-8069-e0e3048e911d.sketch_text.stroke-92"),sQuery(id+"FHMxAyK4CFUKdhS_1.wireOp",EDGE,"1cb9c079-ea9b-4899-8069-e0e3048e911d.sketch_text.stroke-93"),sQuery(id+"FHMxAyK4CFUKdhS_1.wireOp",EDGE,"1cb9c079-ea9b-4899-8069-e0e3048e911d.sketch_text.stroke-94"),sQuery(id+"FHMxAyK4CFUKdhS_1.wireOp",EDGE,"1cb9c079-ea9b-4899-8069-e0e3048e911d.sketch_text.stroke-95"),sQuery(id+"FHMxAyK4CFUKdhS_1.wireOp",EDGE,"1cb9c079-ea9b-4899-8069-e0e3048e911d.sketch_text.stroke-96"),sQuery(id+"FHMxAyK4CFUKdhS_1.wireOp",EDGE,"1cb9c079-ea9b-4899-8069-e0e3048e911d.sketch_text.stroke-97"),sQuery(id+"FHMxAyK4CFUKdhS_1.wireOp",EDGE,"1cb9c079-ea9b-4899-8069-e0e3048e911d.sketch_text.stroke-103"),sQuery(id+"FHMxAyK4CFUKdhS_1.wireOp",EDGE,"1cb9c079-ea9b-4899-8069-e0e3048e911d.sketch_text.stroke-104"),sQuery(id+"FHMxAyK4CFUKdhS_1.wireOp",EDGE,"1cb9c079-ea9b-4899-8069-e0e3048e911d.sketch_text.stroke-105"),sQuery(id+"FHMxAyK4CFUKdhS_1.wireOp",EDGE,"1cb9c079-ea9b-4899-8069-e0e3048e911d.sketch_text.stroke-106"),sQuery(id+"FHMxAyK4CFUKdhS_1.wireOp",EDGE,"1cb9c079-ea9b-4899-8069-e0e3048e911d.sketch_text.stroke-107"),sQuery(id+"FHMxAyK4CFUKdhS_1.wireOp",EDGE,"1cb9c079-ea9b-4899-8069-e0e3048e911d.sketch_text.stroke-108"),sQuery(id+"FHMxAyK4CFUKdhS_1.wireOp",EDGE,"1cb9c079-ea9b-4899-8069-e0e3048e911d.sketch_text.stroke-109"),sQuery(id+"FHMxAyK4CFUKdhS_1.wireOp",EDGE,"1cb9c079-ea9b-4899-8069-e0e3048e911d.sketch_text.stroke-110"),sQuery(id+"FHMxAyK4CFUKdhS_1.wireOp",EDGE,"1cb9c079-ea9b-4899-8069-e0e3048e911d.sketch_text.stroke-111"),sQuery(id+"FHMxAyK4CFUKdhS_1.wireOp",EDGE,"1cb9c079-ea9b-4899-8069-e0e3048e911d.sketch_text.stroke-112"),sQuery(id+"FHMxAyK4CFUKdhS_1.wireOp",EDGE,"1cb9c079-ea9b-4899-8069-e0e3048e911d.sketch_text.stroke-113"),sQuery(id+"FHMxAyK4CFUKdhS_1.wireOp",EDGE,"1cb9c079-ea9b-4899-8069-e0e3048e911d.sketch_text.stroke-114"),sQuery(id+"FHMxAyK4CFUKdhS_1.wireOp",EDGE,"1cb9c079-ea9b-4899-8069-e0e3048e911d.sketch_text.stroke-115"),sQuery(id+"FHMxAyK4CFUKdhS_1.wireOp",EDGE,"1cb9c079-ea9b-4899-8069-e0e3048e911d.sketch_text.stroke-116"),sQuery(id+"FHMxAyK4CFUKdhS_1.wireOp",EDGE,"1cb9c079-ea9b-4899-8069-e0e3048e911d.sketch_text.stroke-117"),sQuery(id+"FHMxAyK4CFUKdhS_1.wireOp",EDGE,"1cb9c079-ea9b-4899-8069-e0e3048e911d.sketch_text.stroke-118"),sQuery(id+"FHMxAyK4CFUKdhS_1.wireOp",EDGE,"1cb9c079-ea9b-4899-8069-e0e3048e911d.sketch_text.stroke-119"),sQuery(id+"FHMxAyK4CFUKdhS_1.wireOp",EDGE,"1cb9c079-ea9b-4899-8069-e0e3048e911d.sketch_text.stroke-120"),sQuery(id+"FHMxAyK4CFUKdhS_1.wireOp",EDGE,"1cb9c079-ea9b-4899-8069-e0e3048e911d.sketch_text.stroke-121"),sQuery(id+"FHMxAyK4CFUKdhS_1.wireOp",EDGE,"1cb9c079-ea9b-4899-8069-e0e3048e911d.sketch_text.stroke-122"),sQuery(id+"FHMxAyK4CFUKdhS_1.wireOp",EDGE,"1cb9c079-ea9b-4899-8069-e0e3048e911d.sketch_text.stroke-123"),sQuery(id+"FHMxAyK4CFUKdhS_1.wireOp",EDGE,"1cb9c079-ea9b-4899-8069-e0e3048e911d.sketch_text.stroke-124"),sQuery(id+"FHMxAyK4CFUKdhS_1.wireOp",EDGE,"1cb9c079-ea9b-4899-8069-e0e3048e911d.sketch_text.stroke-125"),sQuery(id+"FHMxAyK4CFUKdhS_1.wireOp",EDGE,"1cb9c079-ea9b-4899-8069-e0e3048e911d.sketch_text.stroke-126"),sQuery(id+"FHMxAyK4CFUKdhS_1.wireOp",EDGE,"1cb9c079-ea9b-4899-8069-e0e3048e911d.sketch_text.stroke-127"),sQuery(id+"FHMxAyK4CFUKdhS_1.wireOp",EDGE,"1cb9c079-ea9b-4899-8069-e0e3048e911d.sketch_text.stroke-128"),sQuery(id+"FHMxAyK4CFUKdhS_1.wireOp",EDGE,"1cb9c079-ea9b-4899-8069-e0e3048e911d.sketch_text.stroke-129"),sQuery(id+"FHMxAyK4CFUKdhS_1.wireOp",EDGE,"1cb9c079-ea9b-4899-8069-e0e3048e911d.sketch_text.stroke-130"),sQuery(id+"FHMxAyK4CFUKdhS_1.wireOp",EDGE,"1cb9c079-ea9b-4899-8069-e0e3048e911d.sketch_text.stroke-131"),sQuery(id+"FHMxAyK4CFUKdhS_1.wireOp",EDGE,"1cb9c079-ea9b-4899-8069-e0e3048e911d.sketch_text.stroke-132"),sQuery(id+"FHMxAyK4CFUKdhS_1.wireOp",EDGE,"1cb9c079-ea9b-4899-8069-e0e3048e911d.sketch_text.stroke-133"),sQuery(id+"FHMxAyK4CFUKdhS_1.wireOp",EDGE,"1cb9c079-ea9b-4899-8069-e0e3048e911d.sketch_text.stroke-134"),sQuery(id+"FHMxAyK4CFUKdhS_1.wireOp",EDGE,"1cb9c079-ea9b-4899-8069-e0e3048e911d.sketch_text.stroke-135"),sQuery(id+"FHMxAyK4CFUKdhS_1.wireOp",EDGE,"1cb9c079-ea9b-4899-8069-e0e3048e911d.sketch_text.stroke-136"),sQuery(id+"FHMxAyK4CFUKdhS_1.wireOp",EDGE,"1cb9c079-ea9b-4899-8069-e0e3048e911d.sketch_text.stroke-137"),sQuery(id+"FHMxAyK4CFUKdhS_1.wireOp",EDGE,"1cb9c079-ea9b-4899-8069-e0e3048e911d.sketch_text.stroke-138"),sQuery(id+"FHMxAyK4CFUKdhS_1.wireOp",EDGE,"1cb9c079-ea9b-4899-8069-e0e3048e911d.sketch_text.stroke-139"),sQuery(id+"FHMxAyK4CFUKdhS_1.wireOp",EDGE,"1cb9c079-ea9b-4899-8069-e0e3048e911d.sketch_text.stroke-140"),sQuery(id+"FHMxAyK4CFUKdhS_1.wireOp",EDGE,"1cb9c079-ea9b-4899-8069-e0e3048e911d.sketch_text.stroke-141"),sQuery(id+"FHMxAyK4CFUKdhS_1.wireOp",EDGE,"1cb9c079-ea9b-4899-8069-e0e3048e911d.sketch_text.stroke-142"),sQuery(id+"FHMxAyK4CFUKdhS_1.wireOp",EDGE,"1cb9c079-ea9b-4899-8069-e0e3048e911d.sketch_text.stroke-143"),sQuery(id+"FHMxAyK4CFUKdhS_1.wireOp",EDGE,"1cb9c079-ea9b-4899-8069-e0e3048e911d.sketch_text.stroke-144"),sQuery(id+"FHMxAyK4CFUKdhS_1.wireOp",EDGE,"1cb9c079-ea9b-4899-8069-e0e3048e911d.sketch_text.stroke-145"),sQuery(id+"FHMxAyK4CFUKdhS_1.wireOp",EDGE,"1cb9c079-ea9b-4899-8069-e0e3048e911d.sketch_text.stroke-146"),sQuery(id+"FHMxAyK4CFUKdhS_1.wireOp",EDGE,"1cb9c079-ea9b-4899-8069-e0e3048e911d.sketch_text.stroke-147"),sQuery(id+"FHMxAyK4CFUKdhS_1.wireOp",EDGE,"1cb9c079-ea9b-4899-8069-e0e3048e911d.sketch_text.stroke-148"),sQuery(id+"FHMxAyK4CFUKdhS_1.wireOp",EDGE,"1cb9c079-ea9b-4899-8069-e0e3048e911d.sketch_text.stroke-149"),sQuery(id+"FHMxAyK4CFUKdhS_1.wireOp",EDGE,"1cb9c079-ea9b-4899-8069-e0e3048e911d.sketch_text.stroke-150"),sQuery(id+"FHMxAyK4CFUKdhS_1.wireOp",EDGE,"1cb9c079-ea9b-4899-8069-e0e3048e911d.sketch_text.stroke-151"),sQuery(id+"FHMxAyK4CFUKdhS_1.wireOp",EDGE,"1cb9c079-ea9b-4899-8069-e0e3048e911d.sketch_text.stroke-152"),sQuery(id+"FHMxAyK4CFUKdhS_1.wireOp",EDGE,"1cb9c079-ea9b-4899-8069-e0e3048e911d.sketch_text.stroke-153"),sQuery(id+"FHMxAyK4CFUKdhS_1.wireOp",EDGE,"1cb9c079-ea9b-4899-8069-e0e3048e911d.sketch_text.stroke-159"),sQuery(id+"FHMxAyK4CFUKdhS_1.wireOp",EDGE,"1cb9c079-ea9b-4899-8069-e0e3048e911d.sketch_text.stroke-160"),sQuery(id+"FHMxAyK4CFUKdhS_1.wireOp",EDGE,"1cb9c079-ea9b-4899-8069-e0e3048e911d.sketch_text.stroke-161"),sQuery(id+"FHMxAyK4CFUKdhS_1.wireOp",EDGE,"1cb9c079-ea9b-4899-8069-e0e3048e911d.sketch_text.stroke-162"),sQuery(id+"FHMxAyK4CFUKdhS_1.wireOp",EDGE,"1cb9c079-ea9b-4899-8069-e0e3048e911d.sketch_text.stroke-163"),sQuery(id+"FHMxAyK4CFUKdhS_1.wireOp",EDGE,"1cb9c079-ea9b-4899-8069-e0e3048e911d.sketch_text.stroke-164"),sQuery(id+"FHMxAyK4CFUKdhS_1.wireOp",EDGE,"1cb9c079-ea9b-4899-8069-e0e3048e911d.sketch_text.stroke-165"),sQuery(id+"FHMxAyK4CFUKdhS_1.wireOp",EDGE,"1cb9c079-ea9b-4899-8069-e0e3048e911d.sketch_text.stroke-166"),sQuery(id+"FHMxAyK4CFUKdhS_1.wireOp",EDGE,"1cb9c079-ea9b-4899-8069-e0e3048e911d.sketch_text.stroke-167"),sQuery(id+"FHMxAyK4CFUKdhS_1.wireOp",EDGE,"1cb9c079-ea9b-4899-8069-e0e3048e911d.sketch_text.stroke-168"),sQuery(id+"FHMxAyK4CFUKdhS_1.wireOp",EDGE,"1cb9c079-ea9b-4899-8069-e0e3048e911d.sketch_text.stroke-169"),sQuery(id+"FHMxAyK4CFUKdhS_1.wireOp",EDGE,"1cb9c079-ea9b-4899-8069-e0e3048e911d.sketch_text.stroke-170"),sQuery(id+"FHMxAyK4CFUKdhS_1.wireOp",EDGE,"1cb9c079-ea9b-4899-8069-e0e3048e911d.sketch_text.stroke-171"),sQuery(id+"FHMxAyK4CFUKdhS_1.wireOp",EDGE,"1cb9c079-ea9b-4899-8069-e0e3048e911d.sketch_text.stroke-172"),sQuery(id+"FHMxAyK4CFUKdhS_1.wireOp",EDGE,"1cb9c079-ea9b-4899-8069-e0e3048e911d.sketch_text.stroke-173"),sQuery(id+"FHMxAyK4CFUKdhS_1.wireOp",EDGE,"1cb9c079-ea9b-4899-8069-e0e3048e911d.sketch_text.stroke-174"),sQuery(id+"FHMxAyK4CFUKdhS_1.wireOp",EDGE,"1cb9c079-ea9b-4899-8069-e0e3048e911d.sketch_text.stroke-175"),sQuery(id+"FHMxAyK4CFUKdhS_1.wireOp",EDGE,"1cb9c079-ea9b-4899-8069-e0e3048e911d.sketch_text.stroke-176"),sQuery(id+"FHMxAyK4CFUKdhS_1.wireOp",EDGE,"1cb9c079-ea9b-4899-8069-e0e3048e911d.sketch_text.stroke-177"),sQuery(id+"FHMxAyK4CFUKdhS_1.wireOp",EDGE,"1cb9c079-ea9b-4899-8069-e0e3048e911d.sketch_text.stroke-178"),sQuery(id+"FHMxAyK4CFUKdhS_1.wireOp",EDGE,"1cb9c079-ea9b-4899-8069-e0e3048e911d.sketch_text.stroke-179"),sQuery(id+"FHMxAyK4CFUKdhS_1.wireOp",EDGE,"1cb9c079-ea9b-4899-8069-e0e3048e911d.sketch_text.stroke-180"),subQ0,subQ2])],"isStart":true}),makeQuery(id+"F4.opExtrude","SWEPT_FACE",FACE,{"disambiguationData":[OSD([subQ2])]})])],"derivedFrom":makeQuery(id+"F4.opExtrude","CAP_EDGE",EDGE,{"disambiguationData":[OSD([subQ2])],"isStart":true})});}
            var Q11;
            {var subQ0=sQuery(id+"F0.wireOp",EDGE,"E0.top");var subQ1=sQuery(id+"F0.wireOp",EDGE,"E0.bottom");var subQ2=sQuery(id+"F3.wireOp",EDGE,"6ee83ff3-586e-4dbe-aaea-af71240543bd");Q11=makeQuery(id+"F4.boolean.opBoolean","SPLIT",EDGE,{"disambiguationData":[TD([makeQuery(id+"F1.opExtrude","CAP_FACE",FACE,{"disambiguationData":[OSD([subQ1,subQ0,sQuery(id+"F0.wireOp",EDGE,"E0.left"),sQuery(id+"F0.wireOp",EDGE,"E0.right")])],"isStart":false}),makeQuery(id+"F1.opExtrude","SWEPT_FACE",FACE,{"disambiguationData":[OSD([subQ0])]}),makeQuery(id+"F4.opExtrude","CAP_FACE",FACE,{"disambiguationData":[OSD([subQ1,sQuery(id+"F2.wireOp",EDGE,"fcba4419-a2ee-464f-be9d-58f11bf3418b.sketch_text.stroke-0"),sQuery(id+"F2.wireOp",EDGE,"fcba4419-a2ee-464f-be9d-58f11bf3418b.sketch_text.stroke-1"),sQuery(id+"F2.wireOp",EDGE,"fcba4419-a2ee-464f-be9d-58f11bf3418b.sketch_text.stroke-2"),sQuery(id+"F2.wireOp",EDGE,"fcba4419-a2ee-464f-be9d-58f11bf3418b.sketch_text.stroke-3"),sQuery(id+"F2.wireOp",EDGE,"fcba4419-a2ee-464f-be9d-58f11bf3418b.sketch_text.stroke-4"),sQuery(id+"F2.wireOp",EDGE,"fcba4419-a2ee-464f-be9d-58f11bf3418b.sketch_text.stroke-5"),sQuery(id+"F2.wireOp",EDGE,"fcba4419-a2ee-464f-be9d-58f11bf3418b.sketch_text.stroke-6"),sQuery(id+"F2.wireOp",EDGE,"fcba4419-a2ee-464f-be9d-58f11bf3418b.sketch_text.stroke-7"),sQuery(id+"F2.wireOp",EDGE,"fcba4419-a2ee-464f-be9d-58f11bf3418b.sketch_text.stroke-8"),sQuery(id+"F2.wireOp",EDGE,"fcba4419-a2ee-464f-be9d-58f11bf3418b.sketch_text.stroke-9"),sQuery(id+"F2.wireOp",EDGE,"fcba4419-a2ee-464f-be9d-58f11bf3418b.sketch_text.stroke-10"),sQuery(id+"F2.wireOp",EDGE,"fcba4419-a2ee-464f-be9d-58f11bf3418b.sketch_text.stroke-11"),sQuery(id+"F2.wireOp",EDGE,"fcba4419-a2ee-464f-be9d-58f11bf3418b.sketch_text.stroke-12"),sQuery(id+"F2.wireOp",EDGE,"fcba4419-a2ee-464f-be9d-58f11bf3418b.sketch_text.stroke-13"),sQuery(id+"F2.wireOp",EDGE,"fcba4419-a2ee-464f-be9d-58f11bf3418b.sketch_text.stroke-14"),sQuery(id+"F2.wireOp",EDGE,"fcba4419-a2ee-464f-be9d-58f11bf3418b.sketch_text.stroke-15"),sQuery(id+"F2.wireOp",EDGE,"fcba4419-a2ee-464f-be9d-58f11bf3418b.sketch_text.stroke-16"),sQuery(id+"F2.wireOp",EDGE,"fcba4419-a2ee-464f-be9d-58f11bf3418b.sketch_text.stroke-17"),sQuery(id+"F2.wireOp",EDGE,"fcba4419-a2ee-464f-be9d-58f11bf3418b.sketch_text.stroke-18"),sQuery(id+"F2.wireOp",EDGE,"fcba4419-a2ee-464f-be9d-58f11bf3418b.sketch_text.stroke-19"),sQuery(id+"F2.wireOp",EDGE,"fcba4419-a2ee-464f-be9d-58f11bf3418b.sketch_text.stroke-20"),sQuery(id+"F2.wireOp",EDGE,"fcba4419-a2ee-464f-be9d-58f11bf3418b.sketch_text.stroke-21"),sQuery(id+"F2.wireOp",EDGE,"fcba4419-a2ee-464f-be9d-58f11bf3418b.sketch_text.stroke-22"),sQuery(id+"F2.wireOp",EDGE,"fcba4419-a2ee-464f-be9d-58f11bf3418b.sketch_text.stroke-23"),sQuery(id+"F2.wireOp",EDGE,"fcba4419-a2ee-464f-be9d-58f11bf3418b.sketch_text.stroke-24"),sQuery(id+"F2.wireOp",EDGE,"fcba4419-a2ee-464f-be9d-58f11bf3418b.sketch_text.stroke-25"),sQuery(id+"F2.wireOp",EDGE,"fcba4419-a2ee-464f-be9d-58f11bf3418b.sketch_text.stroke-26"),sQuery(id+"F2.wireOp",EDGE,"fcba4419-a2ee-464f-be9d-58f11bf3418b.sketch_text.stroke-27"),sQuery(id+"F2.wireOp",EDGE,"fcba4419-a2ee-464f-be9d-58f11bf3418b.sketch_text.stroke-28"),sQuery(id+"F2.wireOp",EDGE,"fcba4419-a2ee-464f-be9d-58f11bf3418b.sketch_text.stroke-29"),sQuery(id+"F2.wireOp",EDGE,"fcba4419-a2ee-464f-be9d-58f11bf3418b.sketch_text.stroke-30"),sQuery(id+"F2.wireOp",EDGE,"fcba4419-a2ee-464f-be9d-58f11bf3418b.sketch_text.stroke-31"),sQuery(id+"F2.wireOp",EDGE,"fcba4419-a2ee-464f-be9d-58f11bf3418b.sketch_text.stroke-32"),sQuery(id+"F2.wireOp",EDGE,"fcba4419-a2ee-464f-be9d-58f11bf3418b.sketch_text.stroke-33"),sQuery(id+"F2.wireOp",EDGE,"fcba4419-a2ee-464f-be9d-58f11bf3418b.sketch_text.stroke-34"),sQuery(id+"F2.wireOp",EDGE,"fcba4419-a2ee-464f-be9d-58f11bf3418b.sketch_text.stroke-35"),sQuery(id+"F2.wireOp",EDGE,"fcba4419-a2ee-464f-be9d-58f11bf3418b.sketch_text.stroke-36"),sQuery(id+"F2.wireOp",EDGE,"fcba4419-a2ee-464f-be9d-58f11bf3418b.sketch_text.stroke-37"),sQuery(id+"F2.wireOp",EDGE,"fcba4419-a2ee-464f-be9d-58f11bf3418b.sketch_text.stroke-38"),sQuery(id+"F2.wireOp",EDGE,"fcba4419-a2ee-464f-be9d-58f11bf3418b.sketch_text.stroke-39"),sQuery(id+"F2.wireOp",EDGE,"fcba4419-a2ee-464f-be9d-58f11bf3418b.sketch_text.stroke-40"),sQuery(id+"F2.wireOp",EDGE,"fcba4419-a2ee-464f-be9d-58f11bf3418b.sketch_text.stroke-41"),sQuery(id+"F2.wireOp",EDGE,"fcba4419-a2ee-464f-be9d-58f11bf3418b.sketch_text.stroke-42"),sQuery(id+"F2.wireOp",EDGE,"fcba4419-a2ee-464f-be9d-58f11bf3418b.sketch_text.stroke-43"),sQuery(id+"F2.wireOp",EDGE,"fcba4419-a2ee-464f-be9d-58f11bf3418b.sketch_text.stroke-44"),sQuery(id+"F2.wireOp",EDGE,"fcba4419-a2ee-464f-be9d-58f11bf3418b.sketch_text.stroke-45"),sQuery(id+"F2.wireOp",EDGE,"fcba4419-a2ee-464f-be9d-58f11bf3418b.sketch_text.stroke-46"),sQuery(id+"F2.wireOp",EDGE,"fcba4419-a2ee-464f-be9d-58f11bf3418b.sketch_text.stroke-47"),sQuery(id+"F2.wireOp",EDGE,"fcba4419-a2ee-464f-be9d-58f11bf3418b.sketch_text.stroke-48"),sQuery(id+"F2.wireOp",EDGE,"fcba4419-a2ee-464f-be9d-58f11bf3418b.sketch_text.stroke-49"),sQuery(id+"F2.wireOp",EDGE,"fcba4419-a2ee-464f-be9d-58f11bf3418b.sketch_text.stroke-50"),sQuery(id+"F2.wireOp",EDGE,"fcba4419-a2ee-464f-be9d-58f11bf3418b.sketch_text.stroke-51"),sQuery(id+"F2.wireOp",EDGE,"fcba4419-a2ee-464f-be9d-58f11bf3418b.sketch_text.stroke-52"),sQuery(id+"F2.wireOp",EDGE,"fcba4419-a2ee-464f-be9d-58f11bf3418b.sketch_text.stroke-53"),sQuery(id+"F2.wireOp",EDGE,"fcba4419-a2ee-464f-be9d-58f11bf3418b.sketch_text.stroke-54"),sQuery(id+"F2.wireOp",EDGE,"fcba4419-a2ee-464f-be9d-58f11bf3418b.sketch_text.stroke-55"),sQuery(id+"F2.wireOp",EDGE,"fcba4419-a2ee-464f-be9d-58f11bf3418b.sketch_text.stroke-56"),sQuery(id+"F2.wireOp",EDGE,"fcba4419-a2ee-464f-be9d-58f11bf3418b.sketch_text.stroke-57"),sQuery(id+"F2.wireOp",EDGE,"fcba4419-a2ee-464f-be9d-58f11bf3418b.sketch_text.stroke-58"),sQuery(id+"F2.wireOp",EDGE,"fcba4419-a2ee-464f-be9d-58f11bf3418b.sketch_text.stroke-59"),sQuery(id+"F2.wireOp",EDGE,"fcba4419-a2ee-464f-be9d-58f11bf3418b.sketch_text.stroke-60"),sQuery(id+"F2.wireOp",EDGE,"fcba4419-a2ee-464f-be9d-58f11bf3418b.sketch_text.stroke-61"),sQuery(id+"F2.wireOp",EDGE,"fcba4419-a2ee-464f-be9d-58f11bf3418b.sketch_text.stroke-62"),sQuery(id+"F2.wireOp",EDGE,"fcba4419-a2ee-464f-be9d-58f11bf3418b.sketch_text.stroke-63"),sQuery(id+"F2.wireOp",EDGE,"fcba4419-a2ee-464f-be9d-58f11bf3418b.sketch_text.stroke-64"),sQuery(id+"F2.wireOp",EDGE,"fcba4419-a2ee-464f-be9d-58f11bf3418b.sketch_text.stroke-65"),sQuery(id+"F2.wireOp",EDGE,"fcba4419-a2ee-464f-be9d-58f11bf3418b.sketch_text.stroke-66"),sQuery(id+"F2.wireOp",EDGE,"fcba4419-a2ee-464f-be9d-58f11bf3418b.sketch_text.stroke-67"),sQuery(id+"F2.wireOp",EDGE,"fcba4419-a2ee-464f-be9d-58f11bf3418b.sketch_text.stroke-68"),sQuery(id+"F2.wireOp",EDGE,"fcba4419-a2ee-464f-be9d-58f11bf3418b.sketch_text.stroke-69"),sQuery(id+"F2.wireOp",EDGE,"fcba4419-a2ee-464f-be9d-58f11bf3418b.sketch_text.stroke-70"),sQuery(id+"F2.wireOp",EDGE,"fcba4419-a2ee-464f-be9d-58f11bf3418b.sketch_text.stroke-71"),sQuery(id+"F2.wireOp",EDGE,"fcba4419-a2ee-464f-be9d-58f11bf3418b.sketch_text.stroke-72"),sQuery(id+"F2.wireOp",EDGE,"fcba4419-a2ee-464f-be9d-58f11bf3418b.sketch_text.stroke-73"),sQuery(id+"F2.wireOp",EDGE,"fcba4419-a2ee-464f-be9d-58f11bf3418b.sketch_text.stroke-74"),sQuery(id+"F2.wireOp",EDGE,"fcba4419-a2ee-464f-be9d-58f11bf3418b.sketch_text.stroke-75"),sQuery(id+"F2.wireOp",EDGE,"fcba4419-a2ee-464f-be9d-58f11bf3418b.sketch_text.stroke-76"),sQuery(id+"F2.wireOp",EDGE,"fcba4419-a2ee-464f-be9d-58f11bf3418b.sketch_text.stroke-77"),sQuery(id+"F2.wireOp",EDGE,"fcba4419-a2ee-464f-be9d-58f11bf3418b.sketch_text.stroke-78"),sQuery(id+"F2.wireOp",EDGE,"fcba4419-a2ee-464f-be9d-58f11bf3418b.sketch_text.stroke-79"),sQuery(id+"F2.wireOp",EDGE,"fcba4419-a2ee-464f-be9d-58f11bf3418b.sketch_text.stroke-80"),sQuery(id+"F2.wireOp",EDGE,"fcba4419-a2ee-464f-be9d-58f11bf3418b.sketch_text.stroke-81"),sQuery(id+"F2.wireOp",EDGE,"fcba4419-a2ee-464f-be9d-58f11bf3418b.sketch_text.stroke-82"),sQuery(id+"F2.wireOp",EDGE,"fcba4419-a2ee-464f-be9d-58f11bf3418b.sketch_text.stroke-83"),sQuery(id+"F2.wireOp",EDGE,"fcba4419-a2ee-464f-be9d-58f11bf3418b.sketch_text.stroke-84"),sQuery(id+"F2.wireOp",EDGE,"fcba4419-a2ee-464f-be9d-58f11bf3418b.sketch_text.stroke-85"),sQuery(id+"F2.wireOp",EDGE,"fcba4419-a2ee-464f-be9d-58f11bf3418b.sketch_text.stroke-86"),sQuery(id+"F2.wireOp",EDGE,"fcba4419-a2ee-464f-be9d-58f11bf3418b.sketch_text.stroke-87"),sQuery(id+"F2.wireOp",EDGE,"fcba4419-a2ee-464f-be9d-58f11bf3418b.sketch_text.stroke-88"),sQuery(id+"F2.wireOp",EDGE,"fcba4419-a2ee-464f-be9d-58f11bf3418b.sketch_text.stroke-89"),sQuery(id+"F2.wireOp",EDGE,"fcba4419-a2ee-464f-be9d-58f11bf3418b.sketch_text.stroke-90"),sQuery(id+"F2.wireOp",EDGE,"fcba4419-a2ee-464f-be9d-58f11bf3418b.sketch_text.stroke-91"),sQuery(id+"F2.wireOp",EDGE,"fcba4419-a2ee-464f-be9d-58f11bf3418b.sketch_text.stroke-92"),sQuery(id+"F2.wireOp",EDGE,"fcba4419-a2ee-464f-be9d-58f11bf3418b.sketch_text.stroke-93"),sQuery(id+"F2.wireOp",EDGE,"fcba4419-a2ee-464f-be9d-58f11bf3418b.sketch_text.stroke-94"),sQuery(id+"F2.wireOp",EDGE,"fcba4419-a2ee-464f-be9d-58f11bf3418b.sketch_text.stroke-95"),sQuery(id+"F2.wireOp",EDGE,"fcba4419-a2ee-464f-be9d-58f11bf3418b.sketch_text.stroke-96"),sQuery(id+"F2.wireOp",EDGE,"fcba4419-a2ee-464f-be9d-58f11bf3418b.sketch_text.stroke-97"),sQuery(id+"F2.wireOp",EDGE,"fcba4419-a2ee-464f-be9d-58f11bf3418b.sketch_text.stroke-98"),sQuery(id+"F2.wireOp",EDGE,"fcba4419-a2ee-464f-be9d-58f11bf3418b.sketch_text.stroke-99"),sQuery(id+"F2.wireOp",EDGE,"fcba4419-a2ee-464f-be9d-58f11bf3418b.sketch_text.stroke-100"),sQuery(id+"F2.wireOp",EDGE,"fcba4419-a2ee-464f-be9d-58f11bf3418b.sketch_text.stroke-101"),sQuery(id+"F2.wireOp",EDGE,"fcba4419-a2ee-464f-be9d-58f11bf3418b.sketch_text.stroke-102"),sQuery(id+"F2.wireOp",EDGE,"fcba4419-a2ee-464f-be9d-58f11bf3418b.sketch_text.stroke-103"),sQuery(id+"F2.wireOp",EDGE,"fcba4419-a2ee-464f-be9d-58f11bf3418b.sketch_text.stroke-104"),sQuery(id+"F2.wireOp",EDGE,"fcba4419-a2ee-464f-be9d-58f11bf3418b.sketch_text.stroke-105"),sQuery(id+"F2.wireOp",EDGE,"fcba4419-a2ee-464f-be9d-58f11bf3418b.sketch_text.stroke-106"),sQuery(id+"F2.wireOp",EDGE,"fcba4419-a2ee-464f-be9d-58f11bf3418b.sketch_text.stroke-107"),sQuery(id+"F2.wireOp",EDGE,"fcba4419-a2ee-464f-be9d-58f11bf3418b.sketch_text.stroke-108"),sQuery(id+"F2.wireOp",EDGE,"fcba4419-a2ee-464f-be9d-58f11bf3418b.sketch_text.stroke-109"),sQuery(id+"F2.wireOp",EDGE,"fcba4419-a2ee-464f-be9d-58f11bf3418b.sketch_text.stroke-110"),sQuery(id+"F2.wireOp",EDGE,"fcba4419-a2ee-464f-be9d-58f11bf3418b.sketch_text.stroke-111"),sQuery(id+"F2.wireOp",EDGE,"fcba4419-a2ee-464f-be9d-58f11bf3418b.sketch_text.stroke-112"),sQuery(id+"F2.wireOp",EDGE,"fcba4419-a2ee-464f-be9d-58f11bf3418b.sketch_text.stroke-113"),sQuery(id+"F2.wireOp",EDGE,"fcba4419-a2ee-464f-be9d-58f11bf3418b.sketch_text.stroke-114"),sQuery(id+"F2.wireOp",EDGE,"fcba4419-a2ee-464f-be9d-58f11bf3418b.sketch_text.stroke-115"),sQuery(id+"F2.wireOp",EDGE,"fcba4419-a2ee-464f-be9d-58f11bf3418b.sketch_text.stroke-116"),sQuery(id+"F2.wireOp",EDGE,"fcba4419-a2ee-464f-be9d-58f11bf3418b.sketch_text.stroke-117"),sQuery(id+"F2.wireOp",EDGE,"fcba4419-a2ee-464f-be9d-58f11bf3418b.sketch_text.stroke-118"),sQuery(id+"F2.wireOp",EDGE,"fcba4419-a2ee-464f-be9d-58f11bf3418b.sketch_text.stroke-119"),sQuery(id+"F2.wireOp",EDGE,"fcba4419-a2ee-464f-be9d-58f11bf3418b.sketch_text.stroke-120"),sQuery(id+"F2.wireOp",EDGE,"fcba4419-a2ee-464f-be9d-58f11bf3418b.sketch_text.stroke-121"),sQuery(id+"F2.wireOp",EDGE,"fcba4419-a2ee-464f-be9d-58f11bf3418b.sketch_text.stroke-122"),sQuery(id+"F2.wireOp",EDGE,"fcba4419-a2ee-464f-be9d-58f11bf3418b.sketch_text.stroke-123"),sQuery(id+"F2.wireOp",EDGE,"fcba4419-a2ee-464f-be9d-58f11bf3418b.sketch_text.stroke-124"),sQuery(id+"F2.wireOp",EDGE,"fcba4419-a2ee-464f-be9d-58f11bf3418b.sketch_text.stroke-125"),sQuery(id+"F2.wireOp",EDGE,"fcba4419-a2ee-464f-be9d-58f11bf3418b.sketch_text.stroke-126"),sQuery(id+"F2.wireOp",EDGE,"fcba4419-a2ee-464f-be9d-58f11bf3418b.sketch_text.stroke-127"),sQuery(id+"F2.wireOp",EDGE,"fcba4419-a2ee-464f-be9d-58f11bf3418b.sketch_text.stroke-128"),sQuery(id+"F2.wireOp",EDGE,"fcba4419-a2ee-464f-be9d-58f11bf3418b.sketch_text.stroke-129"),sQuery(id+"F2.wireOp",EDGE,"fcba4419-a2ee-464f-be9d-58f11bf3418b.sketch_text.stroke-130"),sQuery(id+"F2.wireOp",EDGE,"fcba4419-a2ee-464f-be9d-58f11bf3418b.sketch_text.stroke-131"),sQuery(id+"F2.wireOp",EDGE,"fcba4419-a2ee-464f-be9d-58f11bf3418b.sketch_text.stroke-132"),sQuery(id+"F2.wireOp",EDGE,"fcba4419-a2ee-464f-be9d-58f11bf3418b.sketch_text.stroke-133"),sQuery(id+"F2.wireOp",EDGE,"fcba4419-a2ee-464f-be9d-58f11bf3418b.sketch_text.stroke-134"),sQuery(id+"F2.wireOp",EDGE,"fcba4419-a2ee-464f-be9d-58f11bf3418b.sketch_text.stroke-135"),sQuery(id+"F2.wireOp",EDGE,"fcba4419-a2ee-464f-be9d-58f11bf3418b.sketch_text.stroke-136"),sQuery(id+"F2.wireOp",EDGE,"fcba4419-a2ee-464f-be9d-58f11bf3418b.sketch_text.stroke-137"),sQuery(id+"F2.wireOp",EDGE,"fcba4419-a2ee-464f-be9d-58f11bf3418b.sketch_text.stroke-138"),sQuery(id+"F2.wireOp",EDGE,"fcba4419-a2ee-464f-be9d-58f11bf3418b.sketch_text.stroke-139"),sQuery(id+"F2.wireOp",EDGE,"fcba4419-a2ee-464f-be9d-58f11bf3418b.sketch_text.stroke-140"),sQuery(id+"F2.wireOp",EDGE,"fcba4419-a2ee-464f-be9d-58f11bf3418b.sketch_text.stroke-141"),sQuery(id+"F2.wireOp",EDGE,"fcba4419-a2ee-464f-be9d-58f11bf3418b.sketch_text.stroke-142"),sQuery(id+"F2.wireOp",EDGE,"fcba4419-a2ee-464f-be9d-58f11bf3418b.sketch_text.stroke-143"),sQuery(id+"F2.wireOp",EDGE,"fcba4419-a2ee-464f-be9d-58f11bf3418b.sketch_text.stroke-144"),sQuery(id+"F2.wireOp",EDGE,"fcba4419-a2ee-464f-be9d-58f11bf3418b.sketch_text.stroke-145"),sQuery(id+"F2.wireOp",EDGE,"fcba4419-a2ee-464f-be9d-58f11bf3418b.sketch_text.stroke-146"),sQuery(id+"F2.wireOp",EDGE,"fcba4419-a2ee-464f-be9d-58f11bf3418b.sketch_text.stroke-147"),sQuery(id+"F2.wireOp",EDGE,"fcba4419-a2ee-464f-be9d-58f11bf3418b.sketch_text.stroke-148"),sQuery(id+"F2.wireOp",EDGE,"fcba4419-a2ee-464f-be9d-58f11bf3418b.sketch_text.stroke-149"),sQuery(id+"F2.wireOp",EDGE,"fcba4419-a2ee-464f-be9d-58f11bf3418b.sketch_text.stroke-150"),sQuery(id+"F2.wireOp",EDGE,"fcba4419-a2ee-464f-be9d-58f11bf3418b.sketch_text.stroke-151"),sQuery(id+"F2.wireOp",EDGE,"fcba4419-a2ee-464f-be9d-58f11bf3418b.sketch_text.stroke-152"),sQuery(id+"F2.wireOp",EDGE,"fcba4419-a2ee-464f-be9d-58f11bf3418b.sketch_text.stroke-153"),sQuery(id+"F2.wireOp",EDGE,"fcba4419-a2ee-464f-be9d-58f11bf3418b.sketch_text.stroke-154"),sQuery(id+"F2.wireOp",EDGE,"fcba4419-a2ee-464f-be9d-58f11bf3418b.sketch_text.stroke-155"),sQuery(id+"F2.wireOp",EDGE,"fcba4419-a2ee-464f-be9d-58f11bf3418b.sketch_text.stroke-156"),sQuery(id+"F2.wireOp",EDGE,"fcba4419-a2ee-464f-be9d-58f11bf3418b.sketch_text.stroke-157"),sQuery(id+"F2.wireOp",EDGE,"fcba4419-a2ee-464f-be9d-58f11bf3418b.sketch_text.stroke-158"),sQuery(id+"F2.wireOp",EDGE,"fcba4419-a2ee-464f-be9d-58f11bf3418b.sketch_text.stroke-159"),sQuery(id+"F2.wireOp",EDGE,"fcba4419-a2ee-464f-be9d-58f11bf3418b.sketch_text.stroke-160"),sQuery(id+"F2.wireOp",EDGE,"fcba4419-a2ee-464f-be9d-58f11bf3418b.sketch_text.stroke-161"),sQuery(id+"F2.wireOp",EDGE,"fcba4419-a2ee-464f-be9d-58f11bf3418b.sketch_text.stroke-162"),sQuery(id+"F2.wireOp",EDGE,"fcba4419-a2ee-464f-be9d-58f11bf3418b.sketch_text.stroke-163"),sQuery(id+"F2.wireOp",EDGE,"fcba4419-a2ee-464f-be9d-58f11bf3418b.sketch_text.stroke-164"),sQuery(id+"F2.wireOp",EDGE,"fcba4419-a2ee-464f-be9d-58f11bf3418b.sketch_text.stroke-165"),sQuery(id+"F2.wireOp",EDGE,"fcba4419-a2ee-464f-be9d-58f11bf3418b.sketch_text.stroke-166"),sQuery(id+"F2.wireOp",EDGE,"fcba4419-a2ee-464f-be9d-58f11bf3418b.sketch_text.stroke-167"),sQuery(id+"F2.wireOp",EDGE,"fcba4419-a2ee-464f-be9d-58f11bf3418b.sketch_text.stroke-168"),sQuery(id+"F2.wireOp",EDGE,"fcba4419-a2ee-464f-be9d-58f11bf3418b.sketch_text.stroke-169"),sQuery(id+"F2.wireOp",EDGE,"fcba4419-a2ee-464f-be9d-58f11bf3418b.sketch_text.stroke-170"),sQuery(id+"F2.wireOp",EDGE,"fcba4419-a2ee-464f-be9d-58f11bf3418b.sketch_text.stroke-171"),sQuery(id+"F2.wireOp",EDGE,"fcba4419-a2ee-464f-be9d-58f11bf3418b.sketch_text.stroke-172"),sQuery(id+"F2.wireOp",EDGE,"fcba4419-a2ee-464f-be9d-58f11bf3418b.sketch_text.stroke-173"),sQuery(id+"FHMxAyK4CFUKdhS_1.wireOp",EDGE,"1cb9c079-ea9b-4899-8069-e0e3048e911d.sketch_text.stroke-0"),sQuery(id+"FHMxAyK4CFUKdhS_1.wireOp",EDGE,"1cb9c079-ea9b-4899-8069-e0e3048e911d.sketch_text.stroke-1"),sQuery(id+"FHMxAyK4CFUKdhS_1.wireOp",EDGE,"1cb9c079-ea9b-4899-8069-e0e3048e911d.sketch_text.stroke-2"),sQuery(id+"FHMxAyK4CFUKdhS_1.wireOp",EDGE,"1cb9c079-ea9b-4899-8069-e0e3048e911d.sketch_text.stroke-3"),sQuery(id+"FHMxAyK4CFUKdhS_1.wireOp",EDGE,"1cb9c079-ea9b-4899-8069-e0e3048e911d.sketch_text.stroke-4"),sQuery(id+"FHMxAyK4CFUKdhS_1.wireOp",EDGE,"1cb9c079-ea9b-4899-8069-e0e3048e911d.sketch_text.stroke-5"),sQuery(id+"FHMxAyK4CFUKdhS_1.wireOp",EDGE,"1cb9c079-ea9b-4899-8069-e0e3048e911d.sketch_text.stroke-6"),sQuery(id+"FHMxAyK4CFUKdhS_1.wireOp",EDGE,"1cb9c079-ea9b-4899-8069-e0e3048e911d.sketch_text.stroke-7"),sQuery(id+"FHMxAyK4CFUKdhS_1.wireOp",EDGE,"1cb9c079-ea9b-4899-8069-e0e3048e911d.sketch_text.stroke-8"),sQuery(id+"FHMxAyK4CFUKdhS_1.wireOp",EDGE,"1cb9c079-ea9b-4899-8069-e0e3048e911d.sketch_text.stroke-9"),sQuery(id+"FHMxAyK4CFUKdhS_1.wireOp",EDGE,"1cb9c079-ea9b-4899-8069-e0e3048e911d.sketch_text.stroke-10"),sQuery(id+"FHMxAyK4CFUKdhS_1.wireOp",EDGE,"1cb9c079-ea9b-4899-8069-e0e3048e911d.sketch_text.stroke-11"),sQuery(id+"FHMxAyK4CFUKdhS_1.wireOp",EDGE,"1cb9c079-ea9b-4899-8069-e0e3048e911d.sketch_text.stroke-12"),sQuery(id+"FHMxAyK4CFUKdhS_1.wireOp",EDGE,"1cb9c079-ea9b-4899-8069-e0e3048e911d.sketch_text.stroke-13"),sQuery(id+"FHMxAyK4CFUKdhS_1.wireOp",EDGE,"1cb9c079-ea9b-4899-8069-e0e3048e911d.sketch_text.stroke-14"),sQuery(id+"FHMxAyK4CFUKdhS_1.wireOp",EDGE,"1cb9c079-ea9b-4899-8069-e0e3048e911d.sketch_text.stroke-15"),sQuery(id+"FHMxAyK4CFUKdhS_1.wireOp",EDGE,"1cb9c079-ea9b-4899-8069-e0e3048e911d.sketch_text.stroke-16"),sQuery(id+"FHMxAyK4CFUKdhS_1.wireOp",EDGE,"1cb9c079-ea9b-4899-8069-e0e3048e911d.sketch_text.stroke-17"),sQuery(id+"FHMxAyK4CFUKdhS_1.wireOp",EDGE,"1cb9c079-ea9b-4899-8069-e0e3048e911d.sketch_text.stroke-18"),sQuery(id+"FHMxAyK4CFUKdhS_1.wireOp",EDGE,"1cb9c079-ea9b-4899-8069-e0e3048e911d.sketch_text.stroke-19"),sQuery(id+"FHMxAyK4CFUKdhS_1.wireOp",EDGE,"1cb9c079-ea9b-4899-8069-e0e3048e911d.sketch_text.stroke-20"),sQuery(id+"FHMxAyK4CFUKdhS_1.wireOp",EDGE,"1cb9c079-ea9b-4899-8069-e0e3048e911d.sketch_text.stroke-21"),sQuery(id+"FHMxAyK4CFUKdhS_1.wireOp",EDGE,"1cb9c079-ea9b-4899-8069-e0e3048e911d.sketch_text.stroke-22"),sQuery(id+"FHMxAyK4CFUKdhS_1.wireOp",EDGE,"1cb9c079-ea9b-4899-8069-e0e3048e911d.sketch_text.stroke-23"),sQuery(id+"FHMxAyK4CFUKdhS_1.wireOp",EDGE,"1cb9c079-ea9b-4899-8069-e0e3048e911d.sketch_text.stroke-24"),sQuery(id+"FHMxAyK4CFUKdhS_1.wireOp",EDGE,"1cb9c079-ea9b-4899-8069-e0e3048e911d.sketch_text.stroke-25"),sQuery(id+"FHMxAyK4CFUKdhS_1.wireOp",EDGE,"1cb9c079-ea9b-4899-8069-e0e3048e911d.sketch_text.stroke-26"),sQuery(id+"FHMxAyK4CFUKdhS_1.wireOp",EDGE,"1cb9c079-ea9b-4899-8069-e0e3048e911d.sketch_text.stroke-27"),sQuery(id+"FHMxAyK4CFUKdhS_1.wireOp",EDGE,"1cb9c079-ea9b-4899-8069-e0e3048e911d.sketch_text.stroke-28"),sQuery(id+"FHMxAyK4CFUKdhS_1.wireOp",EDGE,"1cb9c079-ea9b-4899-8069-e0e3048e911d.sketch_text.stroke-29"),sQuery(id+"FHMxAyK4CFUKdhS_1.wireOp",EDGE,"1cb9c079-ea9b-4899-8069-e0e3048e911d.sketch_text.stroke-30"),sQuery(id+"FHMxAyK4CFUKdhS_1.wireOp",EDGE,"1cb9c079-ea9b-4899-8069-e0e3048e911d.sketch_text.stroke-31"),sQuery(id+"FHMxAyK4CFUKdhS_1.wireOp",EDGE,"1cb9c079-ea9b-4899-8069-e0e3048e911d.sketch_text.stroke-32"),sQuery(id+"FHMxAyK4CFUKdhS_1.wireOp",EDGE,"1cb9c079-ea9b-4899-8069-e0e3048e911d.sketch_text.stroke-33"),sQuery(id+"FHMxAyK4CFUKdhS_1.wireOp",EDGE,"1cb9c079-ea9b-4899-8069-e0e3048e911d.sketch_text.stroke-34"),sQuery(id+"FHMxAyK4CFUKdhS_1.wireOp",EDGE,"1cb9c079-ea9b-4899-8069-e0e3048e911d.sketch_text.stroke-35"),sQuery(id+"FHMxAyK4CFUKdhS_1.wireOp",EDGE,"1cb9c079-ea9b-4899-8069-e0e3048e911d.sketch_text.stroke-36"),sQuery(id+"FHMxAyK4CFUKdhS_1.wireOp",EDGE,"1cb9c079-ea9b-4899-8069-e0e3048e911d.sketch_text.stroke-37"),sQuery(id+"FHMxAyK4CFUKdhS_1.wireOp",EDGE,"1cb9c079-ea9b-4899-8069-e0e3048e911d.sketch_text.stroke-38"),sQuery(id+"FHMxAyK4CFUKdhS_1.wireOp",EDGE,"1cb9c079-ea9b-4899-8069-e0e3048e911d.sketch_text.stroke-39"),sQuery(id+"FHMxAyK4CFUKdhS_1.wireOp",EDGE,"1cb9c079-ea9b-4899-8069-e0e3048e911d.sketch_text.stroke-40"),sQuery(id+"FHMxAyK4CFUKdhS_1.wireOp",EDGE,"1cb9c079-ea9b-4899-8069-e0e3048e911d.sketch_text.stroke-41"),sQuery(id+"FHMxAyK4CFUKdhS_1.wireOp",EDGE,"1cb9c079-ea9b-4899-8069-e0e3048e911d.sketch_text.stroke-42"),sQuery(id+"FHMxAyK4CFUKdhS_1.wireOp",EDGE,"1cb9c079-ea9b-4899-8069-e0e3048e911d.sketch_text.stroke-43"),sQuery(id+"FHMxAyK4CFUKdhS_1.wireOp",EDGE,"1cb9c079-ea9b-4899-8069-e0e3048e911d.sketch_text.stroke-44"),sQuery(id+"FHMxAyK4CFUKdhS_1.wireOp",EDGE,"1cb9c079-ea9b-4899-8069-e0e3048e911d.sketch_text.stroke-45"),sQuery(id+"FHMxAyK4CFUKdhS_1.wireOp",EDGE,"1cb9c079-ea9b-4899-8069-e0e3048e911d.sketch_text.stroke-46"),sQuery(id+"FHMxAyK4CFUKdhS_1.wireOp",EDGE,"1cb9c079-ea9b-4899-8069-e0e3048e911d.sketch_text.stroke-47"),sQuery(id+"FHMxAyK4CFUKdhS_1.wireOp",EDGE,"1cb9c079-ea9b-4899-8069-e0e3048e911d.sketch_text.stroke-48"),sQuery(id+"FHMxAyK4CFUKdhS_1.wireOp",EDGE,"1cb9c079-ea9b-4899-8069-e0e3048e911d.sketch_text.stroke-49"),sQuery(id+"FHMxAyK4CFUKdhS_1.wireOp",EDGE,"1cb9c079-ea9b-4899-8069-e0e3048e911d.sketch_text.stroke-50"),sQuery(id+"FHMxAyK4CFUKdhS_1.wireOp",EDGE,"1cb9c079-ea9b-4899-8069-e0e3048e911d.sketch_text.stroke-51"),sQuery(id+"FHMxAyK4CFUKdhS_1.wireOp",EDGE,"1cb9c079-ea9b-4899-8069-e0e3048e911d.sketch_text.stroke-52"),sQuery(id+"FHMxAyK4CFUKdhS_1.wireOp",EDGE,"1cb9c079-ea9b-4899-8069-e0e3048e911d.sketch_text.stroke-53"),sQuery(id+"FHMxAyK4CFUKdhS_1.wireOp",EDGE,"1cb9c079-ea9b-4899-8069-e0e3048e911d.sketch_text.stroke-54"),sQuery(id+"FHMxAyK4CFUKdhS_1.wireOp",EDGE,"1cb9c079-ea9b-4899-8069-e0e3048e911d.sketch_text.stroke-55"),sQuery(id+"FHMxAyK4CFUKdhS_1.wireOp",EDGE,"1cb9c079-ea9b-4899-8069-e0e3048e911d.sketch_text.stroke-56"),sQuery(id+"FHMxAyK4CFUKdhS_1.wireOp",EDGE,"1cb9c079-ea9b-4899-8069-e0e3048e911d.sketch_text.stroke-57"),sQuery(id+"FHMxAyK4CFUKdhS_1.wireOp",EDGE,"1cb9c079-ea9b-4899-8069-e0e3048e911d.sketch_text.stroke-58"),sQuery(id+"FHMxAyK4CFUKdhS_1.wireOp",EDGE,"1cb9c079-ea9b-4899-8069-e0e3048e911d.sketch_text.stroke-59"),sQuery(id+"FHMxAyK4CFUKdhS_1.wireOp",EDGE,"1cb9c079-ea9b-4899-8069-e0e3048e911d.sketch_text.stroke-60"),sQuery(id+"FHMxAyK4CFUKdhS_1.wireOp",EDGE,"1cb9c079-ea9b-4899-8069-e0e3048e911d.sketch_text.stroke-61"),sQuery(id+"FHMxAyK4CFUKdhS_1.wireOp",EDGE,"1cb9c079-ea9b-4899-8069-e0e3048e911d.sketch_text.stroke-62"),sQuery(id+"FHMxAyK4CFUKdhS_1.wireOp",EDGE,"1cb9c079-ea9b-4899-8069-e0e3048e911d.sketch_text.stroke-71"),sQuery(id+"FHMxAyK4CFUKdhS_1.wireOp",EDGE,"1cb9c079-ea9b-4899-8069-e0e3048e911d.sketch_text.stroke-72"),sQuery(id+"FHMxAyK4CFUKdhS_1.wireOp",EDGE,"1cb9c079-ea9b-4899-8069-e0e3048e911d.sketch_text.stroke-73"),sQuery(id+"FHMxAyK4CFUKdhS_1.wireOp",EDGE,"1cb9c079-ea9b-4899-8069-e0e3048e911d.sketch_text.stroke-74"),sQuery(id+"FHMxAyK4CFUKdhS_1.wireOp",EDGE,"1cb9c079-ea9b-4899-8069-e0e3048e911d.sketch_text.stroke-75"),sQuery(id+"FHMxAyK4CFUKdhS_1.wireOp",EDGE,"1cb9c079-ea9b-4899-8069-e0e3048e911d.sketch_text.stroke-76"),sQuery(id+"FHMxAyK4CFUKdhS_1.wireOp",EDGE,"1cb9c079-ea9b-4899-8069-e0e3048e911d.sketch_text.stroke-77"),sQuery(id+"FHMxAyK4CFUKdhS_1.wireOp",EDGE,"1cb9c079-ea9b-4899-8069-e0e3048e911d.sketch_text.stroke-78"),sQuery(id+"FHMxAyK4CFUKdhS_1.wireOp",EDGE,"1cb9c079-ea9b-4899-8069-e0e3048e911d.sketch_text.stroke-79"),sQuery(id+"FHMxAyK4CFUKdhS_1.wireOp",EDGE,"1cb9c079-ea9b-4899-8069-e0e3048e911d.sketch_text.stroke-80"),sQuery(id+"FHMxAyK4CFUKdhS_1.wireOp",EDGE,"1cb9c079-ea9b-4899-8069-e0e3048e911d.sketch_text.stroke-81"),sQuery(id+"FHMxAyK4CFUKdhS_1.wireOp",EDGE,"1cb9c079-ea9b-4899-8069-e0e3048e911d.sketch_text.stroke-82"),sQuery(id+"FHMxAyK4CFUKdhS_1.wireOp",EDGE,"1cb9c079-ea9b-4899-8069-e0e3048e911d.sketch_text.stroke-83"),sQuery(id+"FHMxAyK4CFUKdhS_1.wireOp",EDGE,"1cb9c079-ea9b-4899-8069-e0e3048e911d.sketch_text.stroke-84"),sQuery(id+"FHMxAyK4CFUKdhS_1.wireOp",EDGE,"1cb9c079-ea9b-4899-8069-e0e3048e911d.sketch_text.stroke-85"),sQuery(id+"FHMxAyK4CFUKdhS_1.wireOp",EDGE,"1cb9c079-ea9b-4899-8069-e0e3048e911d.sketch_text.stroke-86"),sQuery(id+"FHMxAyK4CFUKdhS_1.wireOp",EDGE,"1cb9c079-ea9b-4899-8069-e0e3048e911d.sketch_text.stroke-87"),sQuery(id+"FHMxAyK4CFUKdhS_1.wireOp",EDGE,"1cb9c079-ea9b-4899-8069-e0e3048e911d.sketch_text.stroke-88"),sQuery(id+"FHMxAyK4CFUKdhS_1.wireOp",EDGE,"1cb9c079-ea9b-4899-8069-e0e3048e911d.sketch_text.stroke-89"),sQuery(id+"FHMxAyK4CFUKdhS_1.wireOp",EDGE,"1cb9c079-ea9b-4899-8069-e0e3048e911d.sketch_text.stroke-90"),sQuery(id+"FHMxAyK4CFUKdhS_1.wireOp",EDGE,"1cb9c079-ea9b-4899-8069-e0e3048e911d.sketch_text.stroke-91"),sQuery(id+"FHMxAyK4CFUKdhS_1.wireOp",EDGE,"1cb9c079-ea9b-4899-8069-e0e3048e911d.sketch_text.stroke-92"),sQuery(id+"FHMxAyK4CFUKdhS_1.wireOp",EDGE,"1cb9c079-ea9b-4899-8069-e0e3048e911d.sketch_text.stroke-93"),sQuery(id+"FHMxAyK4CFUKdhS_1.wireOp",EDGE,"1cb9c079-ea9b-4899-8069-e0e3048e911d.sketch_text.stroke-94"),sQuery(id+"FHMxAyK4CFUKdhS_1.wireOp",EDGE,"1cb9c079-ea9b-4899-8069-e0e3048e911d.sketch_text.stroke-95"),sQuery(id+"FHMxAyK4CFUKdhS_1.wireOp",EDGE,"1cb9c079-ea9b-4899-8069-e0e3048e911d.sketch_text.stroke-96"),sQuery(id+"FHMxAyK4CFUKdhS_1.wireOp",EDGE,"1cb9c079-ea9b-4899-8069-e0e3048e911d.sketch_text.stroke-97"),sQuery(id+"FHMxAyK4CFUKdhS_1.wireOp",EDGE,"1cb9c079-ea9b-4899-8069-e0e3048e911d.sketch_text.stroke-103"),sQuery(id+"FHMxAyK4CFUKdhS_1.wireOp",EDGE,"1cb9c079-ea9b-4899-8069-e0e3048e911d.sketch_text.stroke-104"),sQuery(id+"FHMxAyK4CFUKdhS_1.wireOp",EDGE,"1cb9c079-ea9b-4899-8069-e0e3048e911d.sketch_text.stroke-105"),sQuery(id+"FHMxAyK4CFUKdhS_1.wireOp",EDGE,"1cb9c079-ea9b-4899-8069-e0e3048e911d.sketch_text.stroke-106"),sQuery(id+"FHMxAyK4CFUKdhS_1.wireOp",EDGE,"1cb9c079-ea9b-4899-8069-e0e3048e911d.sketch_text.stroke-107"),sQuery(id+"FHMxAyK4CFUKdhS_1.wireOp",EDGE,"1cb9c079-ea9b-4899-8069-e0e3048e911d.sketch_text.stroke-108"),sQuery(id+"FHMxAyK4CFUKdhS_1.wireOp",EDGE,"1cb9c079-ea9b-4899-8069-e0e3048e911d.sketch_text.stroke-109"),sQuery(id+"FHMxAyK4CFUKdhS_1.wireOp",EDGE,"1cb9c079-ea9b-4899-8069-e0e3048e911d.sketch_text.stroke-110"),sQuery(id+"FHMxAyK4CFUKdhS_1.wireOp",EDGE,"1cb9c079-ea9b-4899-8069-e0e3048e911d.sketch_text.stroke-111"),sQuery(id+"FHMxAyK4CFUKdhS_1.wireOp",EDGE,"1cb9c079-ea9b-4899-8069-e0e3048e911d.sketch_text.stroke-112"),sQuery(id+"FHMxAyK4CFUKdhS_1.wireOp",EDGE,"1cb9c079-ea9b-4899-8069-e0e3048e911d.sketch_text.stroke-113"),sQuery(id+"FHMxAyK4CFUKdhS_1.wireOp",EDGE,"1cb9c079-ea9b-4899-8069-e0e3048e911d.sketch_text.stroke-114"),sQuery(id+"FHMxAyK4CFUKdhS_1.wireOp",EDGE,"1cb9c079-ea9b-4899-8069-e0e3048e911d.sketch_text.stroke-115"),sQuery(id+"FHMxAyK4CFUKdhS_1.wireOp",EDGE,"1cb9c079-ea9b-4899-8069-e0e3048e911d.sketch_text.stroke-116"),sQuery(id+"FHMxAyK4CFUKdhS_1.wireOp",EDGE,"1cb9c079-ea9b-4899-8069-e0e3048e911d.sketch_text.stroke-117"),sQuery(id+"FHMxAyK4CFUKdhS_1.wireOp",EDGE,"1cb9c079-ea9b-4899-8069-e0e3048e911d.sketch_text.stroke-118"),sQuery(id+"FHMxAyK4CFUKdhS_1.wireOp",EDGE,"1cb9c079-ea9b-4899-8069-e0e3048e911d.sketch_text.stroke-119"),sQuery(id+"FHMxAyK4CFUKdhS_1.wireOp",EDGE,"1cb9c079-ea9b-4899-8069-e0e3048e911d.sketch_text.stroke-120"),sQuery(id+"FHMxAyK4CFUKdhS_1.wireOp",EDGE,"1cb9c079-ea9b-4899-8069-e0e3048e911d.sketch_text.stroke-121"),sQuery(id+"FHMxAyK4CFUKdhS_1.wireOp",EDGE,"1cb9c079-ea9b-4899-8069-e0e3048e911d.sketch_text.stroke-122"),sQuery(id+"FHMxAyK4CFUKdhS_1.wireOp",EDGE,"1cb9c079-ea9b-4899-8069-e0e3048e911d.sketch_text.stroke-123"),sQuery(id+"FHMxAyK4CFUKdhS_1.wireOp",EDGE,"1cb9c079-ea9b-4899-8069-e0e3048e911d.sketch_text.stroke-124"),sQuery(id+"FHMxAyK4CFUKdhS_1.wireOp",EDGE,"1cb9c079-ea9b-4899-8069-e0e3048e911d.sketch_text.stroke-125"),sQuery(id+"FHMxAyK4CFUKdhS_1.wireOp",EDGE,"1cb9c079-ea9b-4899-8069-e0e3048e911d.sketch_text.stroke-126"),sQuery(id+"FHMxAyK4CFUKdhS_1.wireOp",EDGE,"1cb9c079-ea9b-4899-8069-e0e3048e911d.sketch_text.stroke-127"),sQuery(id+"FHMxAyK4CFUKdhS_1.wireOp",EDGE,"1cb9c079-ea9b-4899-8069-e0e3048e911d.sketch_text.stroke-128"),sQuery(id+"FHMxAyK4CFUKdhS_1.wireOp",EDGE,"1cb9c079-ea9b-4899-8069-e0e3048e911d.sketch_text.stroke-129"),sQuery(id+"FHMxAyK4CFUKdhS_1.wireOp",EDGE,"1cb9c079-ea9b-4899-8069-e0e3048e911d.sketch_text.stroke-130"),sQuery(id+"FHMxAyK4CFUKdhS_1.wireOp",EDGE,"1cb9c079-ea9b-4899-8069-e0e3048e911d.sketch_text.stroke-131"),sQuery(id+"FHMxAyK4CFUKdhS_1.wireOp",EDGE,"1cb9c079-ea9b-4899-8069-e0e3048e911d.sketch_text.stroke-132"),sQuery(id+"FHMxAyK4CFUKdhS_1.wireOp",EDGE,"1cb9c079-ea9b-4899-8069-e0e3048e911d.sketch_text.stroke-133"),sQuery(id+"FHMxAyK4CFUKdhS_1.wireOp",EDGE,"1cb9c079-ea9b-4899-8069-e0e3048e911d.sketch_text.stroke-134"),sQuery(id+"FHMxAyK4CFUKdhS_1.wireOp",EDGE,"1cb9c079-ea9b-4899-8069-e0e3048e911d.sketch_text.stroke-135"),sQuery(id+"FHMxAyK4CFUKdhS_1.wireOp",EDGE,"1cb9c079-ea9b-4899-8069-e0e3048e911d.sketch_text.stroke-136"),sQuery(id+"FHMxAyK4CFUKdhS_1.wireOp",EDGE,"1cb9c079-ea9b-4899-8069-e0e3048e911d.sketch_text.stroke-137"),sQuery(id+"FHMxAyK4CFUKdhS_1.wireOp",EDGE,"1cb9c079-ea9b-4899-8069-e0e3048e911d.sketch_text.stroke-138"),sQuery(id+"FHMxAyK4CFUKdhS_1.wireOp",EDGE,"1cb9c079-ea9b-4899-8069-e0e3048e911d.sketch_text.stroke-139"),sQuery(id+"FHMxAyK4CFUKdhS_1.wireOp",EDGE,"1cb9c079-ea9b-4899-8069-e0e3048e911d.sketch_text.stroke-140"),sQuery(id+"FHMxAyK4CFUKdhS_1.wireOp",EDGE,"1cb9c079-ea9b-4899-8069-e0e3048e911d.sketch_text.stroke-141"),sQuery(id+"FHMxAyK4CFUKdhS_1.wireOp",EDGE,"1cb9c079-ea9b-4899-8069-e0e3048e911d.sketch_text.stroke-142"),sQuery(id+"FHMxAyK4CFUKdhS_1.wireOp",EDGE,"1cb9c079-ea9b-4899-8069-e0e3048e911d.sketch_text.stroke-143"),sQuery(id+"FHMxAyK4CFUKdhS_1.wireOp",EDGE,"1cb9c079-ea9b-4899-8069-e0e3048e911d.sketch_text.stroke-144"),sQuery(id+"FHMxAyK4CFUKdhS_1.wireOp",EDGE,"1cb9c079-ea9b-4899-8069-e0e3048e911d.sketch_text.stroke-145"),sQuery(id+"FHMxAyK4CFUKdhS_1.wireOp",EDGE,"1cb9c079-ea9b-4899-8069-e0e3048e911d.sketch_text.stroke-146"),sQuery(id+"FHMxAyK4CFUKdhS_1.wireOp",EDGE,"1cb9c079-ea9b-4899-8069-e0e3048e911d.sketch_text.stroke-147"),sQuery(id+"FHMxAyK4CFUKdhS_1.wireOp",EDGE,"1cb9c079-ea9b-4899-8069-e0e3048e911d.sketch_text.stroke-148"),sQuery(id+"FHMxAyK4CFUKdhS_1.wireOp",EDGE,"1cb9c079-ea9b-4899-8069-e0e3048e911d.sketch_text.stroke-149"),sQuery(id+"FHMxAyK4CFUKdhS_1.wireOp",EDGE,"1cb9c079-ea9b-4899-8069-e0e3048e911d.sketch_text.stroke-150"),sQuery(id+"FHMxAyK4CFUKdhS_1.wireOp",EDGE,"1cb9c079-ea9b-4899-8069-e0e3048e911d.sketch_text.stroke-151"),sQuery(id+"FHMxAyK4CFUKdhS_1.wireOp",EDGE,"1cb9c079-ea9b-4899-8069-e0e3048e911d.sketch_text.stroke-152"),sQuery(id+"FHMxAyK4CFUKdhS_1.wireOp",EDGE,"1cb9c079-ea9b-4899-8069-e0e3048e911d.sketch_text.stroke-153"),sQuery(id+"FHMxAyK4CFUKdhS_1.wireOp",EDGE,"1cb9c079-ea9b-4899-8069-e0e3048e911d.sketch_text.stroke-159"),sQuery(id+"FHMxAyK4CFUKdhS_1.wireOp",EDGE,"1cb9c079-ea9b-4899-8069-e0e3048e911d.sketch_text.stroke-160"),sQuery(id+"FHMxAyK4CFUKdhS_1.wireOp",EDGE,"1cb9c079-ea9b-4899-8069-e0e3048e911d.sketch_text.stroke-161"),sQuery(id+"FHMxAyK4CFUKdhS_1.wireOp",EDGE,"1cb9c079-ea9b-4899-8069-e0e3048e911d.sketch_text.stroke-162"),sQuery(id+"FHMxAyK4CFUKdhS_1.wireOp",EDGE,"1cb9c079-ea9b-4899-8069-e0e3048e911d.sketch_text.stroke-163"),sQuery(id+"FHMxAyK4CFUKdhS_1.wireOp",EDGE,"1cb9c079-ea9b-4899-8069-e0e3048e911d.sketch_text.stroke-164"),sQuery(id+"FHMxAyK4CFUKdhS_1.wireOp",EDGE,"1cb9c079-ea9b-4899-8069-e0e3048e911d.sketch_text.stroke-165"),sQuery(id+"FHMxAyK4CFUKdhS_1.wireOp",EDGE,"1cb9c079-ea9b-4899-8069-e0e3048e911d.sketch_text.stroke-166"),sQuery(id+"FHMxAyK4CFUKdhS_1.wireOp",EDGE,"1cb9c079-ea9b-4899-8069-e0e3048e911d.sketch_text.stroke-167"),sQuery(id+"FHMxAyK4CFUKdhS_1.wireOp",EDGE,"1cb9c079-ea9b-4899-8069-e0e3048e911d.sketch_text.stroke-168"),sQuery(id+"FHMxAyK4CFUKdhS_1.wireOp",EDGE,"1cb9c079-ea9b-4899-8069-e0e3048e911d.sketch_text.stroke-169"),sQuery(id+"FHMxAyK4CFUKdhS_1.wireOp",EDGE,"1cb9c079-ea9b-4899-8069-e0e3048e911d.sketch_text.stroke-170"),sQuery(id+"FHMxAyK4CFUKdhS_1.wireOp",EDGE,"1cb9c079-ea9b-4899-8069-e0e3048e911d.sketch_text.stroke-171"),sQuery(id+"FHMxAyK4CFUKdhS_1.wireOp",EDGE,"1cb9c079-ea9b-4899-8069-e0e3048e911d.sketch_text.stroke-172"),sQuery(id+"FHMxAyK4CFUKdhS_1.wireOp",EDGE,"1cb9c079-ea9b-4899-8069-e0e3048e911d.sketch_text.stroke-173"),sQuery(id+"FHMxAyK4CFUKdhS_1.wireOp",EDGE,"1cb9c079-ea9b-4899-8069-e0e3048e911d.sketch_text.stroke-174"),sQuery(id+"FHMxAyK4CFUKdhS_1.wireOp",EDGE,"1cb9c079-ea9b-4899-8069-e0e3048e911d.sketch_text.stroke-175"),sQuery(id+"FHMxAyK4CFUKdhS_1.wireOp",EDGE,"1cb9c079-ea9b-4899-8069-e0e3048e911d.sketch_text.stroke-176"),sQuery(id+"FHMxAyK4CFUKdhS_1.wireOp",EDGE,"1cb9c079-ea9b-4899-8069-e0e3048e911d.sketch_text.stroke-177"),sQuery(id+"FHMxAyK4CFUKdhS_1.wireOp",EDGE,"1cb9c079-ea9b-4899-8069-e0e3048e911d.sketch_text.stroke-178"),sQuery(id+"FHMxAyK4CFUKdhS_1.wireOp",EDGE,"1cb9c079-ea9b-4899-8069-e0e3048e911d.sketch_text.stroke-179"),sQuery(id+"FHMxAyK4CFUKdhS_1.wireOp",EDGE,"1cb9c079-ea9b-4899-8069-e0e3048e911d.sketch_text.stroke-180"),sQuery(id+"F3.wireOp",EDGE,"8007402e-1a4e-4a06-85a5-2af08e553504"),subQ2])],"isStart":true}),makeQuery(id+"F4.opExtrude","SWEPT_FACE",FACE,{"disambiguationData":[OSD([subQ2])]})]),OD(0.0)],"derivedFrom":makeQuery(id+"F1.opExtrude","CAP_EDGE",EDGE,{"disambiguationData":[OSD([subQ0])],"isStart":false})});}
            var Q12;
            {var subQ0=sQuery(id+"F0.wireOp",EDGE,"E0.top");var subQ1=sQuery(id+"F0.wireOp",EDGE,"E0.bottom");var subQ2=sQuery(id+"F3.wireOp",EDGE,"6ee83ff3-586e-4dbe-aaea-af71240543bd");Q12=makeQuery(id+"F4.boolean.opBoolean","SPLIT",EDGE,{"disambiguationData":[TD([makeQuery(id+"F1.opExtrude","CAP_FACE",FACE,{"disambiguationData":[OSD([subQ1,subQ0,sQuery(id+"F0.wireOp",EDGE,"E0.left"),sQuery(id+"F0.wireOp",EDGE,"E0.right")])],"isStart":false}),makeQuery(id+"F1.opExtrude","SWEPT_FACE",FACE,{"disambiguationData":[OSD([subQ0])]}),makeQuery(id+"F4.opExtrude","CAP_FACE",FACE,{"disambiguationData":[OSD([subQ1,sQuery(id+"F2.wireOp",EDGE,"fcba4419-a2ee-464f-be9d-58f11bf3418b.sketch_text.stroke-0"),sQuery(id+"F2.wireOp",EDGE,"fcba4419-a2ee-464f-be9d-58f11bf3418b.sketch_text.stroke-1"),sQuery(id+"F2.wireOp",EDGE,"fcba4419-a2ee-464f-be9d-58f11bf3418b.sketch_text.stroke-2"),sQuery(id+"F2.wireOp",EDGE,"fcba4419-a2ee-464f-be9d-58f11bf3418b.sketch_text.stroke-3"),sQuery(id+"F2.wireOp",EDGE,"fcba4419-a2ee-464f-be9d-58f11bf3418b.sketch_text.stroke-4"),sQuery(id+"F2.wireOp",EDGE,"fcba4419-a2ee-464f-be9d-58f11bf3418b.sketch_text.stroke-5"),sQuery(id+"F2.wireOp",EDGE,"fcba4419-a2ee-464f-be9d-58f11bf3418b.sketch_text.stroke-6"),sQuery(id+"F2.wireOp",EDGE,"fcba4419-a2ee-464f-be9d-58f11bf3418b.sketch_text.stroke-7"),sQuery(id+"F2.wireOp",EDGE,"fcba4419-a2ee-464f-be9d-58f11bf3418b.sketch_text.stroke-8"),sQuery(id+"F2.wireOp",EDGE,"fcba4419-a2ee-464f-be9d-58f11bf3418b.sketch_text.stroke-9"),sQuery(id+"F2.wireOp",EDGE,"fcba4419-a2ee-464f-be9d-58f11bf3418b.sketch_text.stroke-10"),sQuery(id+"F2.wireOp",EDGE,"fcba4419-a2ee-464f-be9d-58f11bf3418b.sketch_text.stroke-11"),sQuery(id+"F2.wireOp",EDGE,"fcba4419-a2ee-464f-be9d-58f11bf3418b.sketch_text.stroke-12"),sQuery(id+"F2.wireOp",EDGE,"fcba4419-a2ee-464f-be9d-58f11bf3418b.sketch_text.stroke-13"),sQuery(id+"F2.wireOp",EDGE,"fcba4419-a2ee-464f-be9d-58f11bf3418b.sketch_text.stroke-14"),sQuery(id+"F2.wireOp",EDGE,"fcba4419-a2ee-464f-be9d-58f11bf3418b.sketch_text.stroke-15"),sQuery(id+"F2.wireOp",EDGE,"fcba4419-a2ee-464f-be9d-58f11bf3418b.sketch_text.stroke-16"),sQuery(id+"F2.wireOp",EDGE,"fcba4419-a2ee-464f-be9d-58f11bf3418b.sketch_text.stroke-17"),sQuery(id+"F2.wireOp",EDGE,"fcba4419-a2ee-464f-be9d-58f11bf3418b.sketch_text.stroke-18"),sQuery(id+"F2.wireOp",EDGE,"fcba4419-a2ee-464f-be9d-58f11bf3418b.sketch_text.stroke-19"),sQuery(id+"F2.wireOp",EDGE,"fcba4419-a2ee-464f-be9d-58f11bf3418b.sketch_text.stroke-20"),sQuery(id+"F2.wireOp",EDGE,"fcba4419-a2ee-464f-be9d-58f11bf3418b.sketch_text.stroke-21"),sQuery(id+"F2.wireOp",EDGE,"fcba4419-a2ee-464f-be9d-58f11bf3418b.sketch_text.stroke-22"),sQuery(id+"F2.wireOp",EDGE,"fcba4419-a2ee-464f-be9d-58f11bf3418b.sketch_text.stroke-23"),sQuery(id+"F2.wireOp",EDGE,"fcba4419-a2ee-464f-be9d-58f11bf3418b.sketch_text.stroke-24"),sQuery(id+"F2.wireOp",EDGE,"fcba4419-a2ee-464f-be9d-58f11bf3418b.sketch_text.stroke-25"),sQuery(id+"F2.wireOp",EDGE,"fcba4419-a2ee-464f-be9d-58f11bf3418b.sketch_text.stroke-26"),sQuery(id+"F2.wireOp",EDGE,"fcba4419-a2ee-464f-be9d-58f11bf3418b.sketch_text.stroke-27"),sQuery(id+"F2.wireOp",EDGE,"fcba4419-a2ee-464f-be9d-58f11bf3418b.sketch_text.stroke-28"),sQuery(id+"F2.wireOp",EDGE,"fcba4419-a2ee-464f-be9d-58f11bf3418b.sketch_text.stroke-29"),sQuery(id+"F2.wireOp",EDGE,"fcba4419-a2ee-464f-be9d-58f11bf3418b.sketch_text.stroke-30"),sQuery(id+"F2.wireOp",EDGE,"fcba4419-a2ee-464f-be9d-58f11bf3418b.sketch_text.stroke-31"),sQuery(id+"F2.wireOp",EDGE,"fcba4419-a2ee-464f-be9d-58f11bf3418b.sketch_text.stroke-32"),sQuery(id+"F2.wireOp",EDGE,"fcba4419-a2ee-464f-be9d-58f11bf3418b.sketch_text.stroke-33"),sQuery(id+"F2.wireOp",EDGE,"fcba4419-a2ee-464f-be9d-58f11bf3418b.sketch_text.stroke-34"),sQuery(id+"F2.wireOp",EDGE,"fcba4419-a2ee-464f-be9d-58f11bf3418b.sketch_text.stroke-35"),sQuery(id+"F2.wireOp",EDGE,"fcba4419-a2ee-464f-be9d-58f11bf3418b.sketch_text.stroke-36"),sQuery(id+"F2.wireOp",EDGE,"fcba4419-a2ee-464f-be9d-58f11bf3418b.sketch_text.stroke-37"),sQuery(id+"F2.wireOp",EDGE,"fcba4419-a2ee-464f-be9d-58f11bf3418b.sketch_text.stroke-38"),sQuery(id+"F2.wireOp",EDGE,"fcba4419-a2ee-464f-be9d-58f11bf3418b.sketch_text.stroke-39"),sQuery(id+"F2.wireOp",EDGE,"fcba4419-a2ee-464f-be9d-58f11bf3418b.sketch_text.stroke-40"),sQuery(id+"F2.wireOp",EDGE,"fcba4419-a2ee-464f-be9d-58f11bf3418b.sketch_text.stroke-41"),sQuery(id+"F2.wireOp",EDGE,"fcba4419-a2ee-464f-be9d-58f11bf3418b.sketch_text.stroke-42"),sQuery(id+"F2.wireOp",EDGE,"fcba4419-a2ee-464f-be9d-58f11bf3418b.sketch_text.stroke-43"),sQuery(id+"F2.wireOp",EDGE,"fcba4419-a2ee-464f-be9d-58f11bf3418b.sketch_text.stroke-44"),sQuery(id+"F2.wireOp",EDGE,"fcba4419-a2ee-464f-be9d-58f11bf3418b.sketch_text.stroke-45"),sQuery(id+"F2.wireOp",EDGE,"fcba4419-a2ee-464f-be9d-58f11bf3418b.sketch_text.stroke-46"),sQuery(id+"F2.wireOp",EDGE,"fcba4419-a2ee-464f-be9d-58f11bf3418b.sketch_text.stroke-47"),sQuery(id+"F2.wireOp",EDGE,"fcba4419-a2ee-464f-be9d-58f11bf3418b.sketch_text.stroke-48"),sQuery(id+"F2.wireOp",EDGE,"fcba4419-a2ee-464f-be9d-58f11bf3418b.sketch_text.stroke-49"),sQuery(id+"F2.wireOp",EDGE,"fcba4419-a2ee-464f-be9d-58f11bf3418b.sketch_text.stroke-50"),sQuery(id+"F2.wireOp",EDGE,"fcba4419-a2ee-464f-be9d-58f11bf3418b.sketch_text.stroke-51"),sQuery(id+"F2.wireOp",EDGE,"fcba4419-a2ee-464f-be9d-58f11bf3418b.sketch_text.stroke-52"),sQuery(id+"F2.wireOp",EDGE,"fcba4419-a2ee-464f-be9d-58f11bf3418b.sketch_text.stroke-53"),sQuery(id+"F2.wireOp",EDGE,"fcba4419-a2ee-464f-be9d-58f11bf3418b.sketch_text.stroke-54"),sQuery(id+"F2.wireOp",EDGE,"fcba4419-a2ee-464f-be9d-58f11bf3418b.sketch_text.stroke-55"),sQuery(id+"F2.wireOp",EDGE,"fcba4419-a2ee-464f-be9d-58f11bf3418b.sketch_text.stroke-56"),sQuery(id+"F2.wireOp",EDGE,"fcba4419-a2ee-464f-be9d-58f11bf3418b.sketch_text.stroke-57"),sQuery(id+"F2.wireOp",EDGE,"fcba4419-a2ee-464f-be9d-58f11bf3418b.sketch_text.stroke-58"),sQuery(id+"F2.wireOp",EDGE,"fcba4419-a2ee-464f-be9d-58f11bf3418b.sketch_text.stroke-59"),sQuery(id+"F2.wireOp",EDGE,"fcba4419-a2ee-464f-be9d-58f11bf3418b.sketch_text.stroke-60"),sQuery(id+"F2.wireOp",EDGE,"fcba4419-a2ee-464f-be9d-58f11bf3418b.sketch_text.stroke-61"),sQuery(id+"F2.wireOp",EDGE,"fcba4419-a2ee-464f-be9d-58f11bf3418b.sketch_text.stroke-62"),sQuery(id+"F2.wireOp",EDGE,"fcba4419-a2ee-464f-be9d-58f11bf3418b.sketch_text.stroke-63"),sQuery(id+"F2.wireOp",EDGE,"fcba4419-a2ee-464f-be9d-58f11bf3418b.sketch_text.stroke-64"),sQuery(id+"F2.wireOp",EDGE,"fcba4419-a2ee-464f-be9d-58f11bf3418b.sketch_text.stroke-65"),sQuery(id+"F2.wireOp",EDGE,"fcba4419-a2ee-464f-be9d-58f11bf3418b.sketch_text.stroke-66"),sQuery(id+"F2.wireOp",EDGE,"fcba4419-a2ee-464f-be9d-58f11bf3418b.sketch_text.stroke-67"),sQuery(id+"F2.wireOp",EDGE,"fcba4419-a2ee-464f-be9d-58f11bf3418b.sketch_text.stroke-68"),sQuery(id+"F2.wireOp",EDGE,"fcba4419-a2ee-464f-be9d-58f11bf3418b.sketch_text.stroke-69"),sQuery(id+"F2.wireOp",EDGE,"fcba4419-a2ee-464f-be9d-58f11bf3418b.sketch_text.stroke-70"),sQuery(id+"F2.wireOp",EDGE,"fcba4419-a2ee-464f-be9d-58f11bf3418b.sketch_text.stroke-71"),sQuery(id+"F2.wireOp",EDGE,"fcba4419-a2ee-464f-be9d-58f11bf3418b.sketch_text.stroke-72"),sQuery(id+"F2.wireOp",EDGE,"fcba4419-a2ee-464f-be9d-58f11bf3418b.sketch_text.stroke-73"),sQuery(id+"F2.wireOp",EDGE,"fcba4419-a2ee-464f-be9d-58f11bf3418b.sketch_text.stroke-74"),sQuery(id+"F2.wireOp",EDGE,"fcba4419-a2ee-464f-be9d-58f11bf3418b.sketch_text.stroke-75"),sQuery(id+"F2.wireOp",EDGE,"fcba4419-a2ee-464f-be9d-58f11bf3418b.sketch_text.stroke-76"),sQuery(id+"F2.wireOp",EDGE,"fcba4419-a2ee-464f-be9d-58f11bf3418b.sketch_text.stroke-77"),sQuery(id+"F2.wireOp",EDGE,"fcba4419-a2ee-464f-be9d-58f11bf3418b.sketch_text.stroke-78"),sQuery(id+"F2.wireOp",EDGE,"fcba4419-a2ee-464f-be9d-58f11bf3418b.sketch_text.stroke-79"),sQuery(id+"F2.wireOp",EDGE,"fcba4419-a2ee-464f-be9d-58f11bf3418b.sketch_text.stroke-80"),sQuery(id+"F2.wireOp",EDGE,"fcba4419-a2ee-464f-be9d-58f11bf3418b.sketch_text.stroke-81"),sQuery(id+"F2.wireOp",EDGE,"fcba4419-a2ee-464f-be9d-58f11bf3418b.sketch_text.stroke-82"),sQuery(id+"F2.wireOp",EDGE,"fcba4419-a2ee-464f-be9d-58f11bf3418b.sketch_text.stroke-83"),sQuery(id+"F2.wireOp",EDGE,"fcba4419-a2ee-464f-be9d-58f11bf3418b.sketch_text.stroke-84"),sQuery(id+"F2.wireOp",EDGE,"fcba4419-a2ee-464f-be9d-58f11bf3418b.sketch_text.stroke-85"),sQuery(id+"F2.wireOp",EDGE,"fcba4419-a2ee-464f-be9d-58f11bf3418b.sketch_text.stroke-86"),sQuery(id+"F2.wireOp",EDGE,"fcba4419-a2ee-464f-be9d-58f11bf3418b.sketch_text.stroke-87"),sQuery(id+"F2.wireOp",EDGE,"fcba4419-a2ee-464f-be9d-58f11bf3418b.sketch_text.stroke-88"),sQuery(id+"F2.wireOp",EDGE,"fcba4419-a2ee-464f-be9d-58f11bf3418b.sketch_text.stroke-89"),sQuery(id+"F2.wireOp",EDGE,"fcba4419-a2ee-464f-be9d-58f11bf3418b.sketch_text.stroke-90"),sQuery(id+"F2.wireOp",EDGE,"fcba4419-a2ee-464f-be9d-58f11bf3418b.sketch_text.stroke-91"),sQuery(id+"F2.wireOp",EDGE,"fcba4419-a2ee-464f-be9d-58f11bf3418b.sketch_text.stroke-92"),sQuery(id+"F2.wireOp",EDGE,"fcba4419-a2ee-464f-be9d-58f11bf3418b.sketch_text.stroke-93"),sQuery(id+"F2.wireOp",EDGE,"fcba4419-a2ee-464f-be9d-58f11bf3418b.sketch_text.stroke-94"),sQuery(id+"F2.wireOp",EDGE,"fcba4419-a2ee-464f-be9d-58f11bf3418b.sketch_text.stroke-95"),sQuery(id+"F2.wireOp",EDGE,"fcba4419-a2ee-464f-be9d-58f11bf3418b.sketch_text.stroke-96"),sQuery(id+"F2.wireOp",EDGE,"fcba4419-a2ee-464f-be9d-58f11bf3418b.sketch_text.stroke-97"),sQuery(id+"F2.wireOp",EDGE,"fcba4419-a2ee-464f-be9d-58f11bf3418b.sketch_text.stroke-98"),sQuery(id+"F2.wireOp",EDGE,"fcba4419-a2ee-464f-be9d-58f11bf3418b.sketch_text.stroke-99"),sQuery(id+"F2.wireOp",EDGE,"fcba4419-a2ee-464f-be9d-58f11bf3418b.sketch_text.stroke-100"),sQuery(id+"F2.wireOp",EDGE,"fcba4419-a2ee-464f-be9d-58f11bf3418b.sketch_text.stroke-101"),sQuery(id+"F2.wireOp",EDGE,"fcba4419-a2ee-464f-be9d-58f11bf3418b.sketch_text.stroke-102"),sQuery(id+"F2.wireOp",EDGE,"fcba4419-a2ee-464f-be9d-58f11bf3418b.sketch_text.stroke-103"),sQuery(id+"F2.wireOp",EDGE,"fcba4419-a2ee-464f-be9d-58f11bf3418b.sketch_text.stroke-104"),sQuery(id+"F2.wireOp",EDGE,"fcba4419-a2ee-464f-be9d-58f11bf3418b.sketch_text.stroke-105"),sQuery(id+"F2.wireOp",EDGE,"fcba4419-a2ee-464f-be9d-58f11bf3418b.sketch_text.stroke-106"),sQuery(id+"F2.wireOp",EDGE,"fcba4419-a2ee-464f-be9d-58f11bf3418b.sketch_text.stroke-107"),sQuery(id+"F2.wireOp",EDGE,"fcba4419-a2ee-464f-be9d-58f11bf3418b.sketch_text.stroke-108"),sQuery(id+"F2.wireOp",EDGE,"fcba4419-a2ee-464f-be9d-58f11bf3418b.sketch_text.stroke-109"),sQuery(id+"F2.wireOp",EDGE,"fcba4419-a2ee-464f-be9d-58f11bf3418b.sketch_text.stroke-110"),sQuery(id+"F2.wireOp",EDGE,"fcba4419-a2ee-464f-be9d-58f11bf3418b.sketch_text.stroke-111"),sQuery(id+"F2.wireOp",EDGE,"fcba4419-a2ee-464f-be9d-58f11bf3418b.sketch_text.stroke-112"),sQuery(id+"F2.wireOp",EDGE,"fcba4419-a2ee-464f-be9d-58f11bf3418b.sketch_text.stroke-113"),sQuery(id+"F2.wireOp",EDGE,"fcba4419-a2ee-464f-be9d-58f11bf3418b.sketch_text.stroke-114"),sQuery(id+"F2.wireOp",EDGE,"fcba4419-a2ee-464f-be9d-58f11bf3418b.sketch_text.stroke-115"),sQuery(id+"F2.wireOp",EDGE,"fcba4419-a2ee-464f-be9d-58f11bf3418b.sketch_text.stroke-116"),sQuery(id+"F2.wireOp",EDGE,"fcba4419-a2ee-464f-be9d-58f11bf3418b.sketch_text.stroke-117"),sQuery(id+"F2.wireOp",EDGE,"fcba4419-a2ee-464f-be9d-58f11bf3418b.sketch_text.stroke-118"),sQuery(id+"F2.wireOp",EDGE,"fcba4419-a2ee-464f-be9d-58f11bf3418b.sketch_text.stroke-119"),sQuery(id+"F2.wireOp",EDGE,"fcba4419-a2ee-464f-be9d-58f11bf3418b.sketch_text.stroke-120"),sQuery(id+"F2.wireOp",EDGE,"fcba4419-a2ee-464f-be9d-58f11bf3418b.sketch_text.stroke-121"),sQuery(id+"F2.wireOp",EDGE,"fcba4419-a2ee-464f-be9d-58f11bf3418b.sketch_text.stroke-122"),sQuery(id+"F2.wireOp",EDGE,"fcba4419-a2ee-464f-be9d-58f11bf3418b.sketch_text.stroke-123"),sQuery(id+"F2.wireOp",EDGE,"fcba4419-a2ee-464f-be9d-58f11bf3418b.sketch_text.stroke-124"),sQuery(id+"F2.wireOp",EDGE,"fcba4419-a2ee-464f-be9d-58f11bf3418b.sketch_text.stroke-125"),sQuery(id+"F2.wireOp",EDGE,"fcba4419-a2ee-464f-be9d-58f11bf3418b.sketch_text.stroke-126"),sQuery(id+"F2.wireOp",EDGE,"fcba4419-a2ee-464f-be9d-58f11bf3418b.sketch_text.stroke-127"),sQuery(id+"F2.wireOp",EDGE,"fcba4419-a2ee-464f-be9d-58f11bf3418b.sketch_text.stroke-128"),sQuery(id+"F2.wireOp",EDGE,"fcba4419-a2ee-464f-be9d-58f11bf3418b.sketch_text.stroke-129"),sQuery(id+"F2.wireOp",EDGE,"fcba4419-a2ee-464f-be9d-58f11bf3418b.sketch_text.stroke-130"),sQuery(id+"F2.wireOp",EDGE,"fcba4419-a2ee-464f-be9d-58f11bf3418b.sketch_text.stroke-131"),sQuery(id+"F2.wireOp",EDGE,"fcba4419-a2ee-464f-be9d-58f11bf3418b.sketch_text.stroke-132"),sQuery(id+"F2.wireOp",EDGE,"fcba4419-a2ee-464f-be9d-58f11bf3418b.sketch_text.stroke-133"),sQuery(id+"F2.wireOp",EDGE,"fcba4419-a2ee-464f-be9d-58f11bf3418b.sketch_text.stroke-134"),sQuery(id+"F2.wireOp",EDGE,"fcba4419-a2ee-464f-be9d-58f11bf3418b.sketch_text.stroke-135"),sQuery(id+"F2.wireOp",EDGE,"fcba4419-a2ee-464f-be9d-58f11bf3418b.sketch_text.stroke-136"),sQuery(id+"F2.wireOp",EDGE,"fcba4419-a2ee-464f-be9d-58f11bf3418b.sketch_text.stroke-137"),sQuery(id+"F2.wireOp",EDGE,"fcba4419-a2ee-464f-be9d-58f11bf3418b.sketch_text.stroke-138"),sQuery(id+"F2.wireOp",EDGE,"fcba4419-a2ee-464f-be9d-58f11bf3418b.sketch_text.stroke-139"),sQuery(id+"F2.wireOp",EDGE,"fcba4419-a2ee-464f-be9d-58f11bf3418b.sketch_text.stroke-140"),sQuery(id+"F2.wireOp",EDGE,"fcba4419-a2ee-464f-be9d-58f11bf3418b.sketch_text.stroke-141"),sQuery(id+"F2.wireOp",EDGE,"fcba4419-a2ee-464f-be9d-58f11bf3418b.sketch_text.stroke-142"),sQuery(id+"F2.wireOp",EDGE,"fcba4419-a2ee-464f-be9d-58f11bf3418b.sketch_text.stroke-143"),sQuery(id+"F2.wireOp",EDGE,"fcba4419-a2ee-464f-be9d-58f11bf3418b.sketch_text.stroke-144"),sQuery(id+"F2.wireOp",EDGE,"fcba4419-a2ee-464f-be9d-58f11bf3418b.sketch_text.stroke-145"),sQuery(id+"F2.wireOp",EDGE,"fcba4419-a2ee-464f-be9d-58f11bf3418b.sketch_text.stroke-146"),sQuery(id+"F2.wireOp",EDGE,"fcba4419-a2ee-464f-be9d-58f11bf3418b.sketch_text.stroke-147"),sQuery(id+"F2.wireOp",EDGE,"fcba4419-a2ee-464f-be9d-58f11bf3418b.sketch_text.stroke-148"),sQuery(id+"F2.wireOp",EDGE,"fcba4419-a2ee-464f-be9d-58f11bf3418b.sketch_text.stroke-149"),sQuery(id+"F2.wireOp",EDGE,"fcba4419-a2ee-464f-be9d-58f11bf3418b.sketch_text.stroke-150"),sQuery(id+"F2.wireOp",EDGE,"fcba4419-a2ee-464f-be9d-58f11bf3418b.sketch_text.stroke-151"),sQuery(id+"F2.wireOp",EDGE,"fcba4419-a2ee-464f-be9d-58f11bf3418b.sketch_text.stroke-152"),sQuery(id+"F2.wireOp",EDGE,"fcba4419-a2ee-464f-be9d-58f11bf3418b.sketch_text.stroke-153"),sQuery(id+"F2.wireOp",EDGE,"fcba4419-a2ee-464f-be9d-58f11bf3418b.sketch_text.stroke-154"),sQuery(id+"F2.wireOp",EDGE,"fcba4419-a2ee-464f-be9d-58f11bf3418b.sketch_text.stroke-155"),sQuery(id+"F2.wireOp",EDGE,"fcba4419-a2ee-464f-be9d-58f11bf3418b.sketch_text.stroke-156"),sQuery(id+"F2.wireOp",EDGE,"fcba4419-a2ee-464f-be9d-58f11bf3418b.sketch_text.stroke-157"),sQuery(id+"F2.wireOp",EDGE,"fcba4419-a2ee-464f-be9d-58f11bf3418b.sketch_text.stroke-158"),sQuery(id+"F2.wireOp",EDGE,"fcba4419-a2ee-464f-be9d-58f11bf3418b.sketch_text.stroke-159"),sQuery(id+"F2.wireOp",EDGE,"fcba4419-a2ee-464f-be9d-58f11bf3418b.sketch_text.stroke-160"),sQuery(id+"F2.wireOp",EDGE,"fcba4419-a2ee-464f-be9d-58f11bf3418b.sketch_text.stroke-161"),sQuery(id+"F2.wireOp",EDGE,"fcba4419-a2ee-464f-be9d-58f11bf3418b.sketch_text.stroke-162"),sQuery(id+"F2.wireOp",EDGE,"fcba4419-a2ee-464f-be9d-58f11bf3418b.sketch_text.stroke-163"),sQuery(id+"F2.wireOp",EDGE,"fcba4419-a2ee-464f-be9d-58f11bf3418b.sketch_text.stroke-164"),sQuery(id+"F2.wireOp",EDGE,"fcba4419-a2ee-464f-be9d-58f11bf3418b.sketch_text.stroke-165"),sQuery(id+"F2.wireOp",EDGE,"fcba4419-a2ee-464f-be9d-58f11bf3418b.sketch_text.stroke-166"),sQuery(id+"F2.wireOp",EDGE,"fcba4419-a2ee-464f-be9d-58f11bf3418b.sketch_text.stroke-167"),sQuery(id+"F2.wireOp",EDGE,"fcba4419-a2ee-464f-be9d-58f11bf3418b.sketch_text.stroke-168"),sQuery(id+"F2.wireOp",EDGE,"fcba4419-a2ee-464f-be9d-58f11bf3418b.sketch_text.stroke-169"),sQuery(id+"F2.wireOp",EDGE,"fcba4419-a2ee-464f-be9d-58f11bf3418b.sketch_text.stroke-170"),sQuery(id+"F2.wireOp",EDGE,"fcba4419-a2ee-464f-be9d-58f11bf3418b.sketch_text.stroke-171"),sQuery(id+"F2.wireOp",EDGE,"fcba4419-a2ee-464f-be9d-58f11bf3418b.sketch_text.stroke-172"),sQuery(id+"F2.wireOp",EDGE,"fcba4419-a2ee-464f-be9d-58f11bf3418b.sketch_text.stroke-173"),sQuery(id+"FHMxAyK4CFUKdhS_1.wireOp",EDGE,"1cb9c079-ea9b-4899-8069-e0e3048e911d.sketch_text.stroke-0"),sQuery(id+"FHMxAyK4CFUKdhS_1.wireOp",EDGE,"1cb9c079-ea9b-4899-8069-e0e3048e911d.sketch_text.stroke-1"),sQuery(id+"FHMxAyK4CFUKdhS_1.wireOp",EDGE,"1cb9c079-ea9b-4899-8069-e0e3048e911d.sketch_text.stroke-2"),sQuery(id+"FHMxAyK4CFUKdhS_1.wireOp",EDGE,"1cb9c079-ea9b-4899-8069-e0e3048e911d.sketch_text.stroke-3"),sQuery(id+"FHMxAyK4CFUKdhS_1.wireOp",EDGE,"1cb9c079-ea9b-4899-8069-e0e3048e911d.sketch_text.stroke-4"),sQuery(id+"FHMxAyK4CFUKdhS_1.wireOp",EDGE,"1cb9c079-ea9b-4899-8069-e0e3048e911d.sketch_text.stroke-5"),sQuery(id+"FHMxAyK4CFUKdhS_1.wireOp",EDGE,"1cb9c079-ea9b-4899-8069-e0e3048e911d.sketch_text.stroke-6"),sQuery(id+"FHMxAyK4CFUKdhS_1.wireOp",EDGE,"1cb9c079-ea9b-4899-8069-e0e3048e911d.sketch_text.stroke-7"),sQuery(id+"FHMxAyK4CFUKdhS_1.wireOp",EDGE,"1cb9c079-ea9b-4899-8069-e0e3048e911d.sketch_text.stroke-8"),sQuery(id+"FHMxAyK4CFUKdhS_1.wireOp",EDGE,"1cb9c079-ea9b-4899-8069-e0e3048e911d.sketch_text.stroke-9"),sQuery(id+"FHMxAyK4CFUKdhS_1.wireOp",EDGE,"1cb9c079-ea9b-4899-8069-e0e3048e911d.sketch_text.stroke-10"),sQuery(id+"FHMxAyK4CFUKdhS_1.wireOp",EDGE,"1cb9c079-ea9b-4899-8069-e0e3048e911d.sketch_text.stroke-11"),sQuery(id+"FHMxAyK4CFUKdhS_1.wireOp",EDGE,"1cb9c079-ea9b-4899-8069-e0e3048e911d.sketch_text.stroke-12"),sQuery(id+"FHMxAyK4CFUKdhS_1.wireOp",EDGE,"1cb9c079-ea9b-4899-8069-e0e3048e911d.sketch_text.stroke-13"),sQuery(id+"FHMxAyK4CFUKdhS_1.wireOp",EDGE,"1cb9c079-ea9b-4899-8069-e0e3048e911d.sketch_text.stroke-14"),sQuery(id+"FHMxAyK4CFUKdhS_1.wireOp",EDGE,"1cb9c079-ea9b-4899-8069-e0e3048e911d.sketch_text.stroke-15"),sQuery(id+"FHMxAyK4CFUKdhS_1.wireOp",EDGE,"1cb9c079-ea9b-4899-8069-e0e3048e911d.sketch_text.stroke-16"),sQuery(id+"FHMxAyK4CFUKdhS_1.wireOp",EDGE,"1cb9c079-ea9b-4899-8069-e0e3048e911d.sketch_text.stroke-17"),sQuery(id+"FHMxAyK4CFUKdhS_1.wireOp",EDGE,"1cb9c079-ea9b-4899-8069-e0e3048e911d.sketch_text.stroke-18"),sQuery(id+"FHMxAyK4CFUKdhS_1.wireOp",EDGE,"1cb9c079-ea9b-4899-8069-e0e3048e911d.sketch_text.stroke-19"),sQuery(id+"FHMxAyK4CFUKdhS_1.wireOp",EDGE,"1cb9c079-ea9b-4899-8069-e0e3048e911d.sketch_text.stroke-20"),sQuery(id+"FHMxAyK4CFUKdhS_1.wireOp",EDGE,"1cb9c079-ea9b-4899-8069-e0e3048e911d.sketch_text.stroke-21"),sQuery(id+"FHMxAyK4CFUKdhS_1.wireOp",EDGE,"1cb9c079-ea9b-4899-8069-e0e3048e911d.sketch_text.stroke-22"),sQuery(id+"FHMxAyK4CFUKdhS_1.wireOp",EDGE,"1cb9c079-ea9b-4899-8069-e0e3048e911d.sketch_text.stroke-23"),sQuery(id+"FHMxAyK4CFUKdhS_1.wireOp",EDGE,"1cb9c079-ea9b-4899-8069-e0e3048e911d.sketch_text.stroke-24"),sQuery(id+"FHMxAyK4CFUKdhS_1.wireOp",EDGE,"1cb9c079-ea9b-4899-8069-e0e3048e911d.sketch_text.stroke-25"),sQuery(id+"FHMxAyK4CFUKdhS_1.wireOp",EDGE,"1cb9c079-ea9b-4899-8069-e0e3048e911d.sketch_text.stroke-26"),sQuery(id+"FHMxAyK4CFUKdhS_1.wireOp",EDGE,"1cb9c079-ea9b-4899-8069-e0e3048e911d.sketch_text.stroke-27"),sQuery(id+"FHMxAyK4CFUKdhS_1.wireOp",EDGE,"1cb9c079-ea9b-4899-8069-e0e3048e911d.sketch_text.stroke-28"),sQuery(id+"FHMxAyK4CFUKdhS_1.wireOp",EDGE,"1cb9c079-ea9b-4899-8069-e0e3048e911d.sketch_text.stroke-29"),sQuery(id+"FHMxAyK4CFUKdhS_1.wireOp",EDGE,"1cb9c079-ea9b-4899-8069-e0e3048e911d.sketch_text.stroke-30"),sQuery(id+"FHMxAyK4CFUKdhS_1.wireOp",EDGE,"1cb9c079-ea9b-4899-8069-e0e3048e911d.sketch_text.stroke-31"),sQuery(id+"FHMxAyK4CFUKdhS_1.wireOp",EDGE,"1cb9c079-ea9b-4899-8069-e0e3048e911d.sketch_text.stroke-32"),sQuery(id+"FHMxAyK4CFUKdhS_1.wireOp",EDGE,"1cb9c079-ea9b-4899-8069-e0e3048e911d.sketch_text.stroke-33"),sQuery(id+"FHMxAyK4CFUKdhS_1.wireOp",EDGE,"1cb9c079-ea9b-4899-8069-e0e3048e911d.sketch_text.stroke-34"),sQuery(id+"FHMxAyK4CFUKdhS_1.wireOp",EDGE,"1cb9c079-ea9b-4899-8069-e0e3048e911d.sketch_text.stroke-35"),sQuery(id+"FHMxAyK4CFUKdhS_1.wireOp",EDGE,"1cb9c079-ea9b-4899-8069-e0e3048e911d.sketch_text.stroke-36"),sQuery(id+"FHMxAyK4CFUKdhS_1.wireOp",EDGE,"1cb9c079-ea9b-4899-8069-e0e3048e911d.sketch_text.stroke-37"),sQuery(id+"FHMxAyK4CFUKdhS_1.wireOp",EDGE,"1cb9c079-ea9b-4899-8069-e0e3048e911d.sketch_text.stroke-38"),sQuery(id+"FHMxAyK4CFUKdhS_1.wireOp",EDGE,"1cb9c079-ea9b-4899-8069-e0e3048e911d.sketch_text.stroke-39"),sQuery(id+"FHMxAyK4CFUKdhS_1.wireOp",EDGE,"1cb9c079-ea9b-4899-8069-e0e3048e911d.sketch_text.stroke-40"),sQuery(id+"FHMxAyK4CFUKdhS_1.wireOp",EDGE,"1cb9c079-ea9b-4899-8069-e0e3048e911d.sketch_text.stroke-41"),sQuery(id+"FHMxAyK4CFUKdhS_1.wireOp",EDGE,"1cb9c079-ea9b-4899-8069-e0e3048e911d.sketch_text.stroke-42"),sQuery(id+"FHMxAyK4CFUKdhS_1.wireOp",EDGE,"1cb9c079-ea9b-4899-8069-e0e3048e911d.sketch_text.stroke-43"),sQuery(id+"FHMxAyK4CFUKdhS_1.wireOp",EDGE,"1cb9c079-ea9b-4899-8069-e0e3048e911d.sketch_text.stroke-44"),sQuery(id+"FHMxAyK4CFUKdhS_1.wireOp",EDGE,"1cb9c079-ea9b-4899-8069-e0e3048e911d.sketch_text.stroke-45"),sQuery(id+"FHMxAyK4CFUKdhS_1.wireOp",EDGE,"1cb9c079-ea9b-4899-8069-e0e3048e911d.sketch_text.stroke-46"),sQuery(id+"FHMxAyK4CFUKdhS_1.wireOp",EDGE,"1cb9c079-ea9b-4899-8069-e0e3048e911d.sketch_text.stroke-47"),sQuery(id+"FHMxAyK4CFUKdhS_1.wireOp",EDGE,"1cb9c079-ea9b-4899-8069-e0e3048e911d.sketch_text.stroke-48"),sQuery(id+"FHMxAyK4CFUKdhS_1.wireOp",EDGE,"1cb9c079-ea9b-4899-8069-e0e3048e911d.sketch_text.stroke-49"),sQuery(id+"FHMxAyK4CFUKdhS_1.wireOp",EDGE,"1cb9c079-ea9b-4899-8069-e0e3048e911d.sketch_text.stroke-50"),sQuery(id+"FHMxAyK4CFUKdhS_1.wireOp",EDGE,"1cb9c079-ea9b-4899-8069-e0e3048e911d.sketch_text.stroke-51"),sQuery(id+"FHMxAyK4CFUKdhS_1.wireOp",EDGE,"1cb9c079-ea9b-4899-8069-e0e3048e911d.sketch_text.stroke-52"),sQuery(id+"FHMxAyK4CFUKdhS_1.wireOp",EDGE,"1cb9c079-ea9b-4899-8069-e0e3048e911d.sketch_text.stroke-53"),sQuery(id+"FHMxAyK4CFUKdhS_1.wireOp",EDGE,"1cb9c079-ea9b-4899-8069-e0e3048e911d.sketch_text.stroke-54"),sQuery(id+"FHMxAyK4CFUKdhS_1.wireOp",EDGE,"1cb9c079-ea9b-4899-8069-e0e3048e911d.sketch_text.stroke-55"),sQuery(id+"FHMxAyK4CFUKdhS_1.wireOp",EDGE,"1cb9c079-ea9b-4899-8069-e0e3048e911d.sketch_text.stroke-56"),sQuery(id+"FHMxAyK4CFUKdhS_1.wireOp",EDGE,"1cb9c079-ea9b-4899-8069-e0e3048e911d.sketch_text.stroke-57"),sQuery(id+"FHMxAyK4CFUKdhS_1.wireOp",EDGE,"1cb9c079-ea9b-4899-8069-e0e3048e911d.sketch_text.stroke-58"),sQuery(id+"FHMxAyK4CFUKdhS_1.wireOp",EDGE,"1cb9c079-ea9b-4899-8069-e0e3048e911d.sketch_text.stroke-59"),sQuery(id+"FHMxAyK4CFUKdhS_1.wireOp",EDGE,"1cb9c079-ea9b-4899-8069-e0e3048e911d.sketch_text.stroke-60"),sQuery(id+"FHMxAyK4CFUKdhS_1.wireOp",EDGE,"1cb9c079-ea9b-4899-8069-e0e3048e911d.sketch_text.stroke-61"),sQuery(id+"FHMxAyK4CFUKdhS_1.wireOp",EDGE,"1cb9c079-ea9b-4899-8069-e0e3048e911d.sketch_text.stroke-62"),sQuery(id+"FHMxAyK4CFUKdhS_1.wireOp",EDGE,"1cb9c079-ea9b-4899-8069-e0e3048e911d.sketch_text.stroke-71"),sQuery(id+"FHMxAyK4CFUKdhS_1.wireOp",EDGE,"1cb9c079-ea9b-4899-8069-e0e3048e911d.sketch_text.stroke-72"),sQuery(id+"FHMxAyK4CFUKdhS_1.wireOp",EDGE,"1cb9c079-ea9b-4899-8069-e0e3048e911d.sketch_text.stroke-73"),sQuery(id+"FHMxAyK4CFUKdhS_1.wireOp",EDGE,"1cb9c079-ea9b-4899-8069-e0e3048e911d.sketch_text.stroke-74"),sQuery(id+"FHMxAyK4CFUKdhS_1.wireOp",EDGE,"1cb9c079-ea9b-4899-8069-e0e3048e911d.sketch_text.stroke-75"),sQuery(id+"FHMxAyK4CFUKdhS_1.wireOp",EDGE,"1cb9c079-ea9b-4899-8069-e0e3048e911d.sketch_text.stroke-76"),sQuery(id+"FHMxAyK4CFUKdhS_1.wireOp",EDGE,"1cb9c079-ea9b-4899-8069-e0e3048e911d.sketch_text.stroke-77"),sQuery(id+"FHMxAyK4CFUKdhS_1.wireOp",EDGE,"1cb9c079-ea9b-4899-8069-e0e3048e911d.sketch_text.stroke-78"),sQuery(id+"FHMxAyK4CFUKdhS_1.wireOp",EDGE,"1cb9c079-ea9b-4899-8069-e0e3048e911d.sketch_text.stroke-79"),sQuery(id+"FHMxAyK4CFUKdhS_1.wireOp",EDGE,"1cb9c079-ea9b-4899-8069-e0e3048e911d.sketch_text.stroke-80"),sQuery(id+"FHMxAyK4CFUKdhS_1.wireOp",EDGE,"1cb9c079-ea9b-4899-8069-e0e3048e911d.sketch_text.stroke-81"),sQuery(id+"FHMxAyK4CFUKdhS_1.wireOp",EDGE,"1cb9c079-ea9b-4899-8069-e0e3048e911d.sketch_text.stroke-82"),sQuery(id+"FHMxAyK4CFUKdhS_1.wireOp",EDGE,"1cb9c079-ea9b-4899-8069-e0e3048e911d.sketch_text.stroke-83"),sQuery(id+"FHMxAyK4CFUKdhS_1.wireOp",EDGE,"1cb9c079-ea9b-4899-8069-e0e3048e911d.sketch_text.stroke-84"),sQuery(id+"FHMxAyK4CFUKdhS_1.wireOp",EDGE,"1cb9c079-ea9b-4899-8069-e0e3048e911d.sketch_text.stroke-85"),sQuery(id+"FHMxAyK4CFUKdhS_1.wireOp",EDGE,"1cb9c079-ea9b-4899-8069-e0e3048e911d.sketch_text.stroke-86"),sQuery(id+"FHMxAyK4CFUKdhS_1.wireOp",EDGE,"1cb9c079-ea9b-4899-8069-e0e3048e911d.sketch_text.stroke-87"),sQuery(id+"FHMxAyK4CFUKdhS_1.wireOp",EDGE,"1cb9c079-ea9b-4899-8069-e0e3048e911d.sketch_text.stroke-88"),sQuery(id+"FHMxAyK4CFUKdhS_1.wireOp",EDGE,"1cb9c079-ea9b-4899-8069-e0e3048e911d.sketch_text.stroke-89"),sQuery(id+"FHMxAyK4CFUKdhS_1.wireOp",EDGE,"1cb9c079-ea9b-4899-8069-e0e3048e911d.sketch_text.stroke-90"),sQuery(id+"FHMxAyK4CFUKdhS_1.wireOp",EDGE,"1cb9c079-ea9b-4899-8069-e0e3048e911d.sketch_text.stroke-91"),sQuery(id+"FHMxAyK4CFUKdhS_1.wireOp",EDGE,"1cb9c079-ea9b-4899-8069-e0e3048e911d.sketch_text.stroke-92"),sQuery(id+"FHMxAyK4CFUKdhS_1.wireOp",EDGE,"1cb9c079-ea9b-4899-8069-e0e3048e911d.sketch_text.stroke-93"),sQuery(id+"FHMxAyK4CFUKdhS_1.wireOp",EDGE,"1cb9c079-ea9b-4899-8069-e0e3048e911d.sketch_text.stroke-94"),sQuery(id+"FHMxAyK4CFUKdhS_1.wireOp",EDGE,"1cb9c079-ea9b-4899-8069-e0e3048e911d.sketch_text.stroke-95"),sQuery(id+"FHMxAyK4CFUKdhS_1.wireOp",EDGE,"1cb9c079-ea9b-4899-8069-e0e3048e911d.sketch_text.stroke-96"),sQuery(id+"FHMxAyK4CFUKdhS_1.wireOp",EDGE,"1cb9c079-ea9b-4899-8069-e0e3048e911d.sketch_text.stroke-97"),sQuery(id+"FHMxAyK4CFUKdhS_1.wireOp",EDGE,"1cb9c079-ea9b-4899-8069-e0e3048e911d.sketch_text.stroke-103"),sQuery(id+"FHMxAyK4CFUKdhS_1.wireOp",EDGE,"1cb9c079-ea9b-4899-8069-e0e3048e911d.sketch_text.stroke-104"),sQuery(id+"FHMxAyK4CFUKdhS_1.wireOp",EDGE,"1cb9c079-ea9b-4899-8069-e0e3048e911d.sketch_text.stroke-105"),sQuery(id+"FHMxAyK4CFUKdhS_1.wireOp",EDGE,"1cb9c079-ea9b-4899-8069-e0e3048e911d.sketch_text.stroke-106"),sQuery(id+"FHMxAyK4CFUKdhS_1.wireOp",EDGE,"1cb9c079-ea9b-4899-8069-e0e3048e911d.sketch_text.stroke-107"),sQuery(id+"FHMxAyK4CFUKdhS_1.wireOp",EDGE,"1cb9c079-ea9b-4899-8069-e0e3048e911d.sketch_text.stroke-108"),sQuery(id+"FHMxAyK4CFUKdhS_1.wireOp",EDGE,"1cb9c079-ea9b-4899-8069-e0e3048e911d.sketch_text.stroke-109"),sQuery(id+"FHMxAyK4CFUKdhS_1.wireOp",EDGE,"1cb9c079-ea9b-4899-8069-e0e3048e911d.sketch_text.stroke-110"),sQuery(id+"FHMxAyK4CFUKdhS_1.wireOp",EDGE,"1cb9c079-ea9b-4899-8069-e0e3048e911d.sketch_text.stroke-111"),sQuery(id+"FHMxAyK4CFUKdhS_1.wireOp",EDGE,"1cb9c079-ea9b-4899-8069-e0e3048e911d.sketch_text.stroke-112"),sQuery(id+"FHMxAyK4CFUKdhS_1.wireOp",EDGE,"1cb9c079-ea9b-4899-8069-e0e3048e911d.sketch_text.stroke-113"),sQuery(id+"FHMxAyK4CFUKdhS_1.wireOp",EDGE,"1cb9c079-ea9b-4899-8069-e0e3048e911d.sketch_text.stroke-114"),sQuery(id+"FHMxAyK4CFUKdhS_1.wireOp",EDGE,"1cb9c079-ea9b-4899-8069-e0e3048e911d.sketch_text.stroke-115"),sQuery(id+"FHMxAyK4CFUKdhS_1.wireOp",EDGE,"1cb9c079-ea9b-4899-8069-e0e3048e911d.sketch_text.stroke-116"),sQuery(id+"FHMxAyK4CFUKdhS_1.wireOp",EDGE,"1cb9c079-ea9b-4899-8069-e0e3048e911d.sketch_text.stroke-117"),sQuery(id+"FHMxAyK4CFUKdhS_1.wireOp",EDGE,"1cb9c079-ea9b-4899-8069-e0e3048e911d.sketch_text.stroke-118"),sQuery(id+"FHMxAyK4CFUKdhS_1.wireOp",EDGE,"1cb9c079-ea9b-4899-8069-e0e3048e911d.sketch_text.stroke-119"),sQuery(id+"FHMxAyK4CFUKdhS_1.wireOp",EDGE,"1cb9c079-ea9b-4899-8069-e0e3048e911d.sketch_text.stroke-120"),sQuery(id+"FHMxAyK4CFUKdhS_1.wireOp",EDGE,"1cb9c079-ea9b-4899-8069-e0e3048e911d.sketch_text.stroke-121"),sQuery(id+"FHMxAyK4CFUKdhS_1.wireOp",EDGE,"1cb9c079-ea9b-4899-8069-e0e3048e911d.sketch_text.stroke-122"),sQuery(id+"FHMxAyK4CFUKdhS_1.wireOp",EDGE,"1cb9c079-ea9b-4899-8069-e0e3048e911d.sketch_text.stroke-123"),sQuery(id+"FHMxAyK4CFUKdhS_1.wireOp",EDGE,"1cb9c079-ea9b-4899-8069-e0e3048e911d.sketch_text.stroke-124"),sQuery(id+"FHMxAyK4CFUKdhS_1.wireOp",EDGE,"1cb9c079-ea9b-4899-8069-e0e3048e911d.sketch_text.stroke-125"),sQuery(id+"FHMxAyK4CFUKdhS_1.wireOp",EDGE,"1cb9c079-ea9b-4899-8069-e0e3048e911d.sketch_text.stroke-126"),sQuery(id+"FHMxAyK4CFUKdhS_1.wireOp",EDGE,"1cb9c079-ea9b-4899-8069-e0e3048e911d.sketch_text.stroke-127"),sQuery(id+"FHMxAyK4CFUKdhS_1.wireOp",EDGE,"1cb9c079-ea9b-4899-8069-e0e3048e911d.sketch_text.stroke-128"),sQuery(id+"FHMxAyK4CFUKdhS_1.wireOp",EDGE,"1cb9c079-ea9b-4899-8069-e0e3048e911d.sketch_text.stroke-129"),sQuery(id+"FHMxAyK4CFUKdhS_1.wireOp",EDGE,"1cb9c079-ea9b-4899-8069-e0e3048e911d.sketch_text.stroke-130"),sQuery(id+"FHMxAyK4CFUKdhS_1.wireOp",EDGE,"1cb9c079-ea9b-4899-8069-e0e3048e911d.sketch_text.stroke-131"),sQuery(id+"FHMxAyK4CFUKdhS_1.wireOp",EDGE,"1cb9c079-ea9b-4899-8069-e0e3048e911d.sketch_text.stroke-132"),sQuery(id+"FHMxAyK4CFUKdhS_1.wireOp",EDGE,"1cb9c079-ea9b-4899-8069-e0e3048e911d.sketch_text.stroke-133"),sQuery(id+"FHMxAyK4CFUKdhS_1.wireOp",EDGE,"1cb9c079-ea9b-4899-8069-e0e3048e911d.sketch_text.stroke-134"),sQuery(id+"FHMxAyK4CFUKdhS_1.wireOp",EDGE,"1cb9c079-ea9b-4899-8069-e0e3048e911d.sketch_text.stroke-135"),sQuery(id+"FHMxAyK4CFUKdhS_1.wireOp",EDGE,"1cb9c079-ea9b-4899-8069-e0e3048e911d.sketch_text.stroke-136"),sQuery(id+"FHMxAyK4CFUKdhS_1.wireOp",EDGE,"1cb9c079-ea9b-4899-8069-e0e3048e911d.sketch_text.stroke-137"),sQuery(id+"FHMxAyK4CFUKdhS_1.wireOp",EDGE,"1cb9c079-ea9b-4899-8069-e0e3048e911d.sketch_text.stroke-138"),sQuery(id+"FHMxAyK4CFUKdhS_1.wireOp",EDGE,"1cb9c079-ea9b-4899-8069-e0e3048e911d.sketch_text.stroke-139"),sQuery(id+"FHMxAyK4CFUKdhS_1.wireOp",EDGE,"1cb9c079-ea9b-4899-8069-e0e3048e911d.sketch_text.stroke-140"),sQuery(id+"FHMxAyK4CFUKdhS_1.wireOp",EDGE,"1cb9c079-ea9b-4899-8069-e0e3048e911d.sketch_text.stroke-141"),sQuery(id+"FHMxAyK4CFUKdhS_1.wireOp",EDGE,"1cb9c079-ea9b-4899-8069-e0e3048e911d.sketch_text.stroke-142"),sQuery(id+"FHMxAyK4CFUKdhS_1.wireOp",EDGE,"1cb9c079-ea9b-4899-8069-e0e3048e911d.sketch_text.stroke-143"),sQuery(id+"FHMxAyK4CFUKdhS_1.wireOp",EDGE,"1cb9c079-ea9b-4899-8069-e0e3048e911d.sketch_text.stroke-144"),sQuery(id+"FHMxAyK4CFUKdhS_1.wireOp",EDGE,"1cb9c079-ea9b-4899-8069-e0e3048e911d.sketch_text.stroke-145"),sQuery(id+"FHMxAyK4CFUKdhS_1.wireOp",EDGE,"1cb9c079-ea9b-4899-8069-e0e3048e911d.sketch_text.stroke-146"),sQuery(id+"FHMxAyK4CFUKdhS_1.wireOp",EDGE,"1cb9c079-ea9b-4899-8069-e0e3048e911d.sketch_text.stroke-147"),sQuery(id+"FHMxAyK4CFUKdhS_1.wireOp",EDGE,"1cb9c079-ea9b-4899-8069-e0e3048e911d.sketch_text.stroke-148"),sQuery(id+"FHMxAyK4CFUKdhS_1.wireOp",EDGE,"1cb9c079-ea9b-4899-8069-e0e3048e911d.sketch_text.stroke-149"),sQuery(id+"FHMxAyK4CFUKdhS_1.wireOp",EDGE,"1cb9c079-ea9b-4899-8069-e0e3048e911d.sketch_text.stroke-150"),sQuery(id+"FHMxAyK4CFUKdhS_1.wireOp",EDGE,"1cb9c079-ea9b-4899-8069-e0e3048e911d.sketch_text.stroke-151"),sQuery(id+"FHMxAyK4CFUKdhS_1.wireOp",EDGE,"1cb9c079-ea9b-4899-8069-e0e3048e911d.sketch_text.stroke-152"),sQuery(id+"FHMxAyK4CFUKdhS_1.wireOp",EDGE,"1cb9c079-ea9b-4899-8069-e0e3048e911d.sketch_text.stroke-153"),sQuery(id+"FHMxAyK4CFUKdhS_1.wireOp",EDGE,"1cb9c079-ea9b-4899-8069-e0e3048e911d.sketch_text.stroke-159"),sQuery(id+"FHMxAyK4CFUKdhS_1.wireOp",EDGE,"1cb9c079-ea9b-4899-8069-e0e3048e911d.sketch_text.stroke-160"),sQuery(id+"FHMxAyK4CFUKdhS_1.wireOp",EDGE,"1cb9c079-ea9b-4899-8069-e0e3048e911d.sketch_text.stroke-161"),sQuery(id+"FHMxAyK4CFUKdhS_1.wireOp",EDGE,"1cb9c079-ea9b-4899-8069-e0e3048e911d.sketch_text.stroke-162"),sQuery(id+"FHMxAyK4CFUKdhS_1.wireOp",EDGE,"1cb9c079-ea9b-4899-8069-e0e3048e911d.sketch_text.stroke-163"),sQuery(id+"FHMxAyK4CFUKdhS_1.wireOp",EDGE,"1cb9c079-ea9b-4899-8069-e0e3048e911d.sketch_text.stroke-164"),sQuery(id+"FHMxAyK4CFUKdhS_1.wireOp",EDGE,"1cb9c079-ea9b-4899-8069-e0e3048e911d.sketch_text.stroke-165"),sQuery(id+"FHMxAyK4CFUKdhS_1.wireOp",EDGE,"1cb9c079-ea9b-4899-8069-e0e3048e911d.sketch_text.stroke-166"),sQuery(id+"FHMxAyK4CFUKdhS_1.wireOp",EDGE,"1cb9c079-ea9b-4899-8069-e0e3048e911d.sketch_text.stroke-167"),sQuery(id+"FHMxAyK4CFUKdhS_1.wireOp",EDGE,"1cb9c079-ea9b-4899-8069-e0e3048e911d.sketch_text.stroke-168"),sQuery(id+"FHMxAyK4CFUKdhS_1.wireOp",EDGE,"1cb9c079-ea9b-4899-8069-e0e3048e911d.sketch_text.stroke-169"),sQuery(id+"FHMxAyK4CFUKdhS_1.wireOp",EDGE,"1cb9c079-ea9b-4899-8069-e0e3048e911d.sketch_text.stroke-170"),sQuery(id+"FHMxAyK4CFUKdhS_1.wireOp",EDGE,"1cb9c079-ea9b-4899-8069-e0e3048e911d.sketch_text.stroke-171"),sQuery(id+"FHMxAyK4CFUKdhS_1.wireOp",EDGE,"1cb9c079-ea9b-4899-8069-e0e3048e911d.sketch_text.stroke-172"),sQuery(id+"FHMxAyK4CFUKdhS_1.wireOp",EDGE,"1cb9c079-ea9b-4899-8069-e0e3048e911d.sketch_text.stroke-173"),sQuery(id+"FHMxAyK4CFUKdhS_1.wireOp",EDGE,"1cb9c079-ea9b-4899-8069-e0e3048e911d.sketch_text.stroke-174"),sQuery(id+"FHMxAyK4CFUKdhS_1.wireOp",EDGE,"1cb9c079-ea9b-4899-8069-e0e3048e911d.sketch_text.stroke-175"),sQuery(id+"FHMxAyK4CFUKdhS_1.wireOp",EDGE,"1cb9c079-ea9b-4899-8069-e0e3048e911d.sketch_text.stroke-176"),sQuery(id+"FHMxAyK4CFUKdhS_1.wireOp",EDGE,"1cb9c079-ea9b-4899-8069-e0e3048e911d.sketch_text.stroke-177"),sQuery(id+"FHMxAyK4CFUKdhS_1.wireOp",EDGE,"1cb9c079-ea9b-4899-8069-e0e3048e911d.sketch_text.stroke-178"),sQuery(id+"FHMxAyK4CFUKdhS_1.wireOp",EDGE,"1cb9c079-ea9b-4899-8069-e0e3048e911d.sketch_text.stroke-179"),sQuery(id+"FHMxAyK4CFUKdhS_1.wireOp",EDGE,"1cb9c079-ea9b-4899-8069-e0e3048e911d.sketch_text.stroke-180"),sQuery(id+"F3.wireOp",EDGE,"8007402e-1a4e-4a06-85a5-2af08e553504"),subQ2])],"isStart":true}),makeQuery(id+"F4.opExtrude","SWEPT_FACE",FACE,{"disambiguationData":[OSD([subQ2])]})]),OD(1.0)],"derivedFrom":makeQuery(id+"F1.opExtrude","CAP_EDGE",EDGE,{"disambiguationData":[OSD([subQ0])],"isStart":false})});}
            var Q13;
            {var subQ0=sQuery(id+"F0.wireOp",EDGE,"E0.top");var subQ1=sQuery(id+"F0.wireOp",EDGE,"E0.bottom");var subQ2=sQuery(id+"F3.wireOp",EDGE,"727ac2c1-f511-4829-95a7-a443ef16a4cd");Q13=makeQuery(id+"F4.boolean.opBoolean","SPLIT",EDGE,{"disambiguationData":[TD([makeQuery(id+"F1.opExtrude","CAP_FACE",FACE,{"disambiguationData":[OSD([subQ1,subQ0,sQuery(id+"F0.wireOp",EDGE,"E0.left"),sQuery(id+"F0.wireOp",EDGE,"E0.right")])],"isStart":false}),makeQuery(id+"F1.opExtrude","SWEPT_FACE",FACE,{"disambiguationData":[OSD([subQ0])]}),makeQuery(id+"F4.opExtrude","CAP_FACE",FACE,{"disambiguationData":[OSD([subQ1,sQuery(id+"F2.wireOp",EDGE,"fcba4419-a2ee-464f-be9d-58f11bf3418b.sketch_text.stroke-0"),sQuery(id+"F2.wireOp",EDGE,"fcba4419-a2ee-464f-be9d-58f11bf3418b.sketch_text.stroke-1"),sQuery(id+"F2.wireOp",EDGE,"fcba4419-a2ee-464f-be9d-58f11bf3418b.sketch_text.stroke-2"),sQuery(id+"F2.wireOp",EDGE,"fcba4419-a2ee-464f-be9d-58f11bf3418b.sketch_text.stroke-3"),sQuery(id+"F2.wireOp",EDGE,"fcba4419-a2ee-464f-be9d-58f11bf3418b.sketch_text.stroke-4"),sQuery(id+"F2.wireOp",EDGE,"fcba4419-a2ee-464f-be9d-58f11bf3418b.sketch_text.stroke-5"),sQuery(id+"F2.wireOp",EDGE,"fcba4419-a2ee-464f-be9d-58f11bf3418b.sketch_text.stroke-6"),sQuery(id+"F2.wireOp",EDGE,"fcba4419-a2ee-464f-be9d-58f11bf3418b.sketch_text.stroke-7"),sQuery(id+"F2.wireOp",EDGE,"fcba4419-a2ee-464f-be9d-58f11bf3418b.sketch_text.stroke-8"),sQuery(id+"F2.wireOp",EDGE,"fcba4419-a2ee-464f-be9d-58f11bf3418b.sketch_text.stroke-9"),sQuery(id+"F2.wireOp",EDGE,"fcba4419-a2ee-464f-be9d-58f11bf3418b.sketch_text.stroke-10"),sQuery(id+"F2.wireOp",EDGE,"fcba4419-a2ee-464f-be9d-58f11bf3418b.sketch_text.stroke-11"),sQuery(id+"F2.wireOp",EDGE,"fcba4419-a2ee-464f-be9d-58f11bf3418b.sketch_text.stroke-12"),sQuery(id+"F2.wireOp",EDGE,"fcba4419-a2ee-464f-be9d-58f11bf3418b.sketch_text.stroke-13"),sQuery(id+"F2.wireOp",EDGE,"fcba4419-a2ee-464f-be9d-58f11bf3418b.sketch_text.stroke-14"),sQuery(id+"F2.wireOp",EDGE,"fcba4419-a2ee-464f-be9d-58f11bf3418b.sketch_text.stroke-15"),sQuery(id+"F2.wireOp",EDGE,"fcba4419-a2ee-464f-be9d-58f11bf3418b.sketch_text.stroke-16"),sQuery(id+"F2.wireOp",EDGE,"fcba4419-a2ee-464f-be9d-58f11bf3418b.sketch_text.stroke-17"),sQuery(id+"F2.wireOp",EDGE,"fcba4419-a2ee-464f-be9d-58f11bf3418b.sketch_text.stroke-18"),sQuery(id+"F2.wireOp",EDGE,"fcba4419-a2ee-464f-be9d-58f11bf3418b.sketch_text.stroke-19"),sQuery(id+"F2.wireOp",EDGE,"fcba4419-a2ee-464f-be9d-58f11bf3418b.sketch_text.stroke-20"),sQuery(id+"F2.wireOp",EDGE,"fcba4419-a2ee-464f-be9d-58f11bf3418b.sketch_text.stroke-21"),sQuery(id+"F2.wireOp",EDGE,"fcba4419-a2ee-464f-be9d-58f11bf3418b.sketch_text.stroke-22"),sQuery(id+"F2.wireOp",EDGE,"fcba4419-a2ee-464f-be9d-58f11bf3418b.sketch_text.stroke-23"),sQuery(id+"F2.wireOp",EDGE,"fcba4419-a2ee-464f-be9d-58f11bf3418b.sketch_text.stroke-24"),sQuery(id+"F2.wireOp",EDGE,"fcba4419-a2ee-464f-be9d-58f11bf3418b.sketch_text.stroke-25"),sQuery(id+"F2.wireOp",EDGE,"fcba4419-a2ee-464f-be9d-58f11bf3418b.sketch_text.stroke-26"),sQuery(id+"F2.wireOp",EDGE,"fcba4419-a2ee-464f-be9d-58f11bf3418b.sketch_text.stroke-27"),sQuery(id+"F2.wireOp",EDGE,"fcba4419-a2ee-464f-be9d-58f11bf3418b.sketch_text.stroke-28"),sQuery(id+"F2.wireOp",EDGE,"fcba4419-a2ee-464f-be9d-58f11bf3418b.sketch_text.stroke-29"),sQuery(id+"F2.wireOp",EDGE,"fcba4419-a2ee-464f-be9d-58f11bf3418b.sketch_text.stroke-30"),sQuery(id+"F2.wireOp",EDGE,"fcba4419-a2ee-464f-be9d-58f11bf3418b.sketch_text.stroke-31"),sQuery(id+"F2.wireOp",EDGE,"fcba4419-a2ee-464f-be9d-58f11bf3418b.sketch_text.stroke-32"),sQuery(id+"F2.wireOp",EDGE,"fcba4419-a2ee-464f-be9d-58f11bf3418b.sketch_text.stroke-33"),sQuery(id+"F2.wireOp",EDGE,"fcba4419-a2ee-464f-be9d-58f11bf3418b.sketch_text.stroke-34"),sQuery(id+"F2.wireOp",EDGE,"fcba4419-a2ee-464f-be9d-58f11bf3418b.sketch_text.stroke-35"),sQuery(id+"F2.wireOp",EDGE,"fcba4419-a2ee-464f-be9d-58f11bf3418b.sketch_text.stroke-36"),sQuery(id+"F2.wireOp",EDGE,"fcba4419-a2ee-464f-be9d-58f11bf3418b.sketch_text.stroke-37"),sQuery(id+"F2.wireOp",EDGE,"fcba4419-a2ee-464f-be9d-58f11bf3418b.sketch_text.stroke-38"),sQuery(id+"F2.wireOp",EDGE,"fcba4419-a2ee-464f-be9d-58f11bf3418b.sketch_text.stroke-39"),sQuery(id+"F2.wireOp",EDGE,"fcba4419-a2ee-464f-be9d-58f11bf3418b.sketch_text.stroke-40"),sQuery(id+"F2.wireOp",EDGE,"fcba4419-a2ee-464f-be9d-58f11bf3418b.sketch_text.stroke-41"),sQuery(id+"F2.wireOp",EDGE,"fcba4419-a2ee-464f-be9d-58f11bf3418b.sketch_text.stroke-42"),sQuery(id+"F2.wireOp",EDGE,"fcba4419-a2ee-464f-be9d-58f11bf3418b.sketch_text.stroke-43"),sQuery(id+"F2.wireOp",EDGE,"fcba4419-a2ee-464f-be9d-58f11bf3418b.sketch_text.stroke-44"),sQuery(id+"F2.wireOp",EDGE,"fcba4419-a2ee-464f-be9d-58f11bf3418b.sketch_text.stroke-45"),sQuery(id+"F2.wireOp",EDGE,"fcba4419-a2ee-464f-be9d-58f11bf3418b.sketch_text.stroke-46"),sQuery(id+"F2.wireOp",EDGE,"fcba4419-a2ee-464f-be9d-58f11bf3418b.sketch_text.stroke-47"),sQuery(id+"F2.wireOp",EDGE,"fcba4419-a2ee-464f-be9d-58f11bf3418b.sketch_text.stroke-48"),sQuery(id+"F2.wireOp",EDGE,"fcba4419-a2ee-464f-be9d-58f11bf3418b.sketch_text.stroke-49"),sQuery(id+"F2.wireOp",EDGE,"fcba4419-a2ee-464f-be9d-58f11bf3418b.sketch_text.stroke-50"),sQuery(id+"F2.wireOp",EDGE,"fcba4419-a2ee-464f-be9d-58f11bf3418b.sketch_text.stroke-51"),sQuery(id+"F2.wireOp",EDGE,"fcba4419-a2ee-464f-be9d-58f11bf3418b.sketch_text.stroke-52"),sQuery(id+"F2.wireOp",EDGE,"fcba4419-a2ee-464f-be9d-58f11bf3418b.sketch_text.stroke-53"),sQuery(id+"F2.wireOp",EDGE,"fcba4419-a2ee-464f-be9d-58f11bf3418b.sketch_text.stroke-54"),sQuery(id+"F2.wireOp",EDGE,"fcba4419-a2ee-464f-be9d-58f11bf3418b.sketch_text.stroke-55"),sQuery(id+"F2.wireOp",EDGE,"fcba4419-a2ee-464f-be9d-58f11bf3418b.sketch_text.stroke-56"),sQuery(id+"F2.wireOp",EDGE,"fcba4419-a2ee-464f-be9d-58f11bf3418b.sketch_text.stroke-57"),sQuery(id+"F2.wireOp",EDGE,"fcba4419-a2ee-464f-be9d-58f11bf3418b.sketch_text.stroke-58"),sQuery(id+"F2.wireOp",EDGE,"fcba4419-a2ee-464f-be9d-58f11bf3418b.sketch_text.stroke-59"),sQuery(id+"F2.wireOp",EDGE,"fcba4419-a2ee-464f-be9d-58f11bf3418b.sketch_text.stroke-60"),sQuery(id+"F2.wireOp",EDGE,"fcba4419-a2ee-464f-be9d-58f11bf3418b.sketch_text.stroke-61"),sQuery(id+"F2.wireOp",EDGE,"fcba4419-a2ee-464f-be9d-58f11bf3418b.sketch_text.stroke-62"),sQuery(id+"F2.wireOp",EDGE,"fcba4419-a2ee-464f-be9d-58f11bf3418b.sketch_text.stroke-63"),sQuery(id+"F2.wireOp",EDGE,"fcba4419-a2ee-464f-be9d-58f11bf3418b.sketch_text.stroke-64"),sQuery(id+"F2.wireOp",EDGE,"fcba4419-a2ee-464f-be9d-58f11bf3418b.sketch_text.stroke-65"),sQuery(id+"F2.wireOp",EDGE,"fcba4419-a2ee-464f-be9d-58f11bf3418b.sketch_text.stroke-66"),sQuery(id+"F2.wireOp",EDGE,"fcba4419-a2ee-464f-be9d-58f11bf3418b.sketch_text.stroke-67"),sQuery(id+"F2.wireOp",EDGE,"fcba4419-a2ee-464f-be9d-58f11bf3418b.sketch_text.stroke-68"),sQuery(id+"F2.wireOp",EDGE,"fcba4419-a2ee-464f-be9d-58f11bf3418b.sketch_text.stroke-69"),sQuery(id+"F2.wireOp",EDGE,"fcba4419-a2ee-464f-be9d-58f11bf3418b.sketch_text.stroke-70"),sQuery(id+"F2.wireOp",EDGE,"fcba4419-a2ee-464f-be9d-58f11bf3418b.sketch_text.stroke-71"),sQuery(id+"F2.wireOp",EDGE,"fcba4419-a2ee-464f-be9d-58f11bf3418b.sketch_text.stroke-72"),sQuery(id+"F2.wireOp",EDGE,"fcba4419-a2ee-464f-be9d-58f11bf3418b.sketch_text.stroke-73"),sQuery(id+"F2.wireOp",EDGE,"fcba4419-a2ee-464f-be9d-58f11bf3418b.sketch_text.stroke-74"),sQuery(id+"F2.wireOp",EDGE,"fcba4419-a2ee-464f-be9d-58f11bf3418b.sketch_text.stroke-75"),sQuery(id+"F2.wireOp",EDGE,"fcba4419-a2ee-464f-be9d-58f11bf3418b.sketch_text.stroke-76"),sQuery(id+"F2.wireOp",EDGE,"fcba4419-a2ee-464f-be9d-58f11bf3418b.sketch_text.stroke-77"),sQuery(id+"F2.wireOp",EDGE,"fcba4419-a2ee-464f-be9d-58f11bf3418b.sketch_text.stroke-78"),sQuery(id+"F2.wireOp",EDGE,"fcba4419-a2ee-464f-be9d-58f11bf3418b.sketch_text.stroke-79"),sQuery(id+"F2.wireOp",EDGE,"fcba4419-a2ee-464f-be9d-58f11bf3418b.sketch_text.stroke-80"),sQuery(id+"F2.wireOp",EDGE,"fcba4419-a2ee-464f-be9d-58f11bf3418b.sketch_text.stroke-81"),sQuery(id+"F2.wireOp",EDGE,"fcba4419-a2ee-464f-be9d-58f11bf3418b.sketch_text.stroke-82"),sQuery(id+"F2.wireOp",EDGE,"fcba4419-a2ee-464f-be9d-58f11bf3418b.sketch_text.stroke-83"),sQuery(id+"F2.wireOp",EDGE,"fcba4419-a2ee-464f-be9d-58f11bf3418b.sketch_text.stroke-84"),sQuery(id+"F2.wireOp",EDGE,"fcba4419-a2ee-464f-be9d-58f11bf3418b.sketch_text.stroke-85"),sQuery(id+"F2.wireOp",EDGE,"fcba4419-a2ee-464f-be9d-58f11bf3418b.sketch_text.stroke-86"),sQuery(id+"F2.wireOp",EDGE,"fcba4419-a2ee-464f-be9d-58f11bf3418b.sketch_text.stroke-87"),sQuery(id+"F2.wireOp",EDGE,"fcba4419-a2ee-464f-be9d-58f11bf3418b.sketch_text.stroke-88"),sQuery(id+"F2.wireOp",EDGE,"fcba4419-a2ee-464f-be9d-58f11bf3418b.sketch_text.stroke-89"),sQuery(id+"F2.wireOp",EDGE,"fcba4419-a2ee-464f-be9d-58f11bf3418b.sketch_text.stroke-90"),sQuery(id+"F2.wireOp",EDGE,"fcba4419-a2ee-464f-be9d-58f11bf3418b.sketch_text.stroke-91"),sQuery(id+"F2.wireOp",EDGE,"fcba4419-a2ee-464f-be9d-58f11bf3418b.sketch_text.stroke-92"),sQuery(id+"F2.wireOp",EDGE,"fcba4419-a2ee-464f-be9d-58f11bf3418b.sketch_text.stroke-93"),sQuery(id+"F2.wireOp",EDGE,"fcba4419-a2ee-464f-be9d-58f11bf3418b.sketch_text.stroke-94"),sQuery(id+"F2.wireOp",EDGE,"fcba4419-a2ee-464f-be9d-58f11bf3418b.sketch_text.stroke-95"),sQuery(id+"F2.wireOp",EDGE,"fcba4419-a2ee-464f-be9d-58f11bf3418b.sketch_text.stroke-96"),sQuery(id+"F2.wireOp",EDGE,"fcba4419-a2ee-464f-be9d-58f11bf3418b.sketch_text.stroke-97"),sQuery(id+"F2.wireOp",EDGE,"fcba4419-a2ee-464f-be9d-58f11bf3418b.sketch_text.stroke-98"),sQuery(id+"F2.wireOp",EDGE,"fcba4419-a2ee-464f-be9d-58f11bf3418b.sketch_text.stroke-99"),sQuery(id+"F2.wireOp",EDGE,"fcba4419-a2ee-464f-be9d-58f11bf3418b.sketch_text.stroke-100"),sQuery(id+"F2.wireOp",EDGE,"fcba4419-a2ee-464f-be9d-58f11bf3418b.sketch_text.stroke-101"),sQuery(id+"F2.wireOp",EDGE,"fcba4419-a2ee-464f-be9d-58f11bf3418b.sketch_text.stroke-102"),sQuery(id+"F2.wireOp",EDGE,"fcba4419-a2ee-464f-be9d-58f11bf3418b.sketch_text.stroke-103"),sQuery(id+"F2.wireOp",EDGE,"fcba4419-a2ee-464f-be9d-58f11bf3418b.sketch_text.stroke-104"),sQuery(id+"F2.wireOp",EDGE,"fcba4419-a2ee-464f-be9d-58f11bf3418b.sketch_text.stroke-105"),sQuery(id+"F2.wireOp",EDGE,"fcba4419-a2ee-464f-be9d-58f11bf3418b.sketch_text.stroke-106"),sQuery(id+"F2.wireOp",EDGE,"fcba4419-a2ee-464f-be9d-58f11bf3418b.sketch_text.stroke-107"),sQuery(id+"F2.wireOp",EDGE,"fcba4419-a2ee-464f-be9d-58f11bf3418b.sketch_text.stroke-108"),sQuery(id+"F2.wireOp",EDGE,"fcba4419-a2ee-464f-be9d-58f11bf3418b.sketch_text.stroke-109"),sQuery(id+"F2.wireOp",EDGE,"fcba4419-a2ee-464f-be9d-58f11bf3418b.sketch_text.stroke-110"),sQuery(id+"F2.wireOp",EDGE,"fcba4419-a2ee-464f-be9d-58f11bf3418b.sketch_text.stroke-111"),sQuery(id+"F2.wireOp",EDGE,"fcba4419-a2ee-464f-be9d-58f11bf3418b.sketch_text.stroke-112"),sQuery(id+"F2.wireOp",EDGE,"fcba4419-a2ee-464f-be9d-58f11bf3418b.sketch_text.stroke-113"),sQuery(id+"F2.wireOp",EDGE,"fcba4419-a2ee-464f-be9d-58f11bf3418b.sketch_text.stroke-114"),sQuery(id+"F2.wireOp",EDGE,"fcba4419-a2ee-464f-be9d-58f11bf3418b.sketch_text.stroke-115"),sQuery(id+"F2.wireOp",EDGE,"fcba4419-a2ee-464f-be9d-58f11bf3418b.sketch_text.stroke-116"),sQuery(id+"F2.wireOp",EDGE,"fcba4419-a2ee-464f-be9d-58f11bf3418b.sketch_text.stroke-117"),sQuery(id+"F2.wireOp",EDGE,"fcba4419-a2ee-464f-be9d-58f11bf3418b.sketch_text.stroke-118"),sQuery(id+"F2.wireOp",EDGE,"fcba4419-a2ee-464f-be9d-58f11bf3418b.sketch_text.stroke-119"),sQuery(id+"F2.wireOp",EDGE,"fcba4419-a2ee-464f-be9d-58f11bf3418b.sketch_text.stroke-120"),sQuery(id+"F2.wireOp",EDGE,"fcba4419-a2ee-464f-be9d-58f11bf3418b.sketch_text.stroke-121"),sQuery(id+"F2.wireOp",EDGE,"fcba4419-a2ee-464f-be9d-58f11bf3418b.sketch_text.stroke-122"),sQuery(id+"F2.wireOp",EDGE,"fcba4419-a2ee-464f-be9d-58f11bf3418b.sketch_text.stroke-123"),sQuery(id+"F2.wireOp",EDGE,"fcba4419-a2ee-464f-be9d-58f11bf3418b.sketch_text.stroke-124"),sQuery(id+"F2.wireOp",EDGE,"fcba4419-a2ee-464f-be9d-58f11bf3418b.sketch_text.stroke-125"),sQuery(id+"F2.wireOp",EDGE,"fcba4419-a2ee-464f-be9d-58f11bf3418b.sketch_text.stroke-126"),sQuery(id+"F2.wireOp",EDGE,"fcba4419-a2ee-464f-be9d-58f11bf3418b.sketch_text.stroke-127"),sQuery(id+"F2.wireOp",EDGE,"fcba4419-a2ee-464f-be9d-58f11bf3418b.sketch_text.stroke-128"),sQuery(id+"F2.wireOp",EDGE,"fcba4419-a2ee-464f-be9d-58f11bf3418b.sketch_text.stroke-129"),sQuery(id+"F2.wireOp",EDGE,"fcba4419-a2ee-464f-be9d-58f11bf3418b.sketch_text.stroke-130"),sQuery(id+"F2.wireOp",EDGE,"fcba4419-a2ee-464f-be9d-58f11bf3418b.sketch_text.stroke-131"),sQuery(id+"F2.wireOp",EDGE,"fcba4419-a2ee-464f-be9d-58f11bf3418b.sketch_text.stroke-132"),sQuery(id+"F2.wireOp",EDGE,"fcba4419-a2ee-464f-be9d-58f11bf3418b.sketch_text.stroke-133"),sQuery(id+"F2.wireOp",EDGE,"fcba4419-a2ee-464f-be9d-58f11bf3418b.sketch_text.stroke-134"),sQuery(id+"F2.wireOp",EDGE,"fcba4419-a2ee-464f-be9d-58f11bf3418b.sketch_text.stroke-135"),sQuery(id+"F2.wireOp",EDGE,"fcba4419-a2ee-464f-be9d-58f11bf3418b.sketch_text.stroke-136"),sQuery(id+"F2.wireOp",EDGE,"fcba4419-a2ee-464f-be9d-58f11bf3418b.sketch_text.stroke-137"),sQuery(id+"F2.wireOp",EDGE,"fcba4419-a2ee-464f-be9d-58f11bf3418b.sketch_text.stroke-138"),sQuery(id+"F2.wireOp",EDGE,"fcba4419-a2ee-464f-be9d-58f11bf3418b.sketch_text.stroke-139"),sQuery(id+"F2.wireOp",EDGE,"fcba4419-a2ee-464f-be9d-58f11bf3418b.sketch_text.stroke-140"),sQuery(id+"F2.wireOp",EDGE,"fcba4419-a2ee-464f-be9d-58f11bf3418b.sketch_text.stroke-141"),sQuery(id+"F2.wireOp",EDGE,"fcba4419-a2ee-464f-be9d-58f11bf3418b.sketch_text.stroke-142"),sQuery(id+"F2.wireOp",EDGE,"fcba4419-a2ee-464f-be9d-58f11bf3418b.sketch_text.stroke-143"),sQuery(id+"F2.wireOp",EDGE,"fcba4419-a2ee-464f-be9d-58f11bf3418b.sketch_text.stroke-144"),sQuery(id+"F2.wireOp",EDGE,"fcba4419-a2ee-464f-be9d-58f11bf3418b.sketch_text.stroke-145"),sQuery(id+"F2.wireOp",EDGE,"fcba4419-a2ee-464f-be9d-58f11bf3418b.sketch_text.stroke-146"),sQuery(id+"F2.wireOp",EDGE,"fcba4419-a2ee-464f-be9d-58f11bf3418b.sketch_text.stroke-147"),sQuery(id+"F2.wireOp",EDGE,"fcba4419-a2ee-464f-be9d-58f11bf3418b.sketch_text.stroke-148"),sQuery(id+"F2.wireOp",EDGE,"fcba4419-a2ee-464f-be9d-58f11bf3418b.sketch_text.stroke-149"),sQuery(id+"F2.wireOp",EDGE,"fcba4419-a2ee-464f-be9d-58f11bf3418b.sketch_text.stroke-150"),sQuery(id+"F2.wireOp",EDGE,"fcba4419-a2ee-464f-be9d-58f11bf3418b.sketch_text.stroke-151"),sQuery(id+"F2.wireOp",EDGE,"fcba4419-a2ee-464f-be9d-58f11bf3418b.sketch_text.stroke-152"),sQuery(id+"F2.wireOp",EDGE,"fcba4419-a2ee-464f-be9d-58f11bf3418b.sketch_text.stroke-153"),sQuery(id+"F2.wireOp",EDGE,"fcba4419-a2ee-464f-be9d-58f11bf3418b.sketch_text.stroke-154"),sQuery(id+"F2.wireOp",EDGE,"fcba4419-a2ee-464f-be9d-58f11bf3418b.sketch_text.stroke-155"),sQuery(id+"F2.wireOp",EDGE,"fcba4419-a2ee-464f-be9d-58f11bf3418b.sketch_text.stroke-156"),sQuery(id+"F2.wireOp",EDGE,"fcba4419-a2ee-464f-be9d-58f11bf3418b.sketch_text.stroke-157"),sQuery(id+"F2.wireOp",EDGE,"fcba4419-a2ee-464f-be9d-58f11bf3418b.sketch_text.stroke-158"),sQuery(id+"F2.wireOp",EDGE,"fcba4419-a2ee-464f-be9d-58f11bf3418b.sketch_text.stroke-159"),sQuery(id+"F2.wireOp",EDGE,"fcba4419-a2ee-464f-be9d-58f11bf3418b.sketch_text.stroke-160"),sQuery(id+"F2.wireOp",EDGE,"fcba4419-a2ee-464f-be9d-58f11bf3418b.sketch_text.stroke-161"),sQuery(id+"F2.wireOp",EDGE,"fcba4419-a2ee-464f-be9d-58f11bf3418b.sketch_text.stroke-162"),sQuery(id+"F2.wireOp",EDGE,"fcba4419-a2ee-464f-be9d-58f11bf3418b.sketch_text.stroke-163"),sQuery(id+"F2.wireOp",EDGE,"fcba4419-a2ee-464f-be9d-58f11bf3418b.sketch_text.stroke-164"),sQuery(id+"F2.wireOp",EDGE,"fcba4419-a2ee-464f-be9d-58f11bf3418b.sketch_text.stroke-165"),sQuery(id+"F2.wireOp",EDGE,"fcba4419-a2ee-464f-be9d-58f11bf3418b.sketch_text.stroke-166"),sQuery(id+"F2.wireOp",EDGE,"fcba4419-a2ee-464f-be9d-58f11bf3418b.sketch_text.stroke-167"),sQuery(id+"F2.wireOp",EDGE,"fcba4419-a2ee-464f-be9d-58f11bf3418b.sketch_text.stroke-168"),sQuery(id+"F2.wireOp",EDGE,"fcba4419-a2ee-464f-be9d-58f11bf3418b.sketch_text.stroke-169"),sQuery(id+"F2.wireOp",EDGE,"fcba4419-a2ee-464f-be9d-58f11bf3418b.sketch_text.stroke-170"),sQuery(id+"F2.wireOp",EDGE,"fcba4419-a2ee-464f-be9d-58f11bf3418b.sketch_text.stroke-171"),sQuery(id+"F2.wireOp",EDGE,"fcba4419-a2ee-464f-be9d-58f11bf3418b.sketch_text.stroke-172"),sQuery(id+"F2.wireOp",EDGE,"fcba4419-a2ee-464f-be9d-58f11bf3418b.sketch_text.stroke-173"),sQuery(id+"FHMxAyK4CFUKdhS_1.wireOp",EDGE,"1cb9c079-ea9b-4899-8069-e0e3048e911d.sketch_text.stroke-0"),sQuery(id+"FHMxAyK4CFUKdhS_1.wireOp",EDGE,"1cb9c079-ea9b-4899-8069-e0e3048e911d.sketch_text.stroke-1"),sQuery(id+"FHMxAyK4CFUKdhS_1.wireOp",EDGE,"1cb9c079-ea9b-4899-8069-e0e3048e911d.sketch_text.stroke-2"),sQuery(id+"FHMxAyK4CFUKdhS_1.wireOp",EDGE,"1cb9c079-ea9b-4899-8069-e0e3048e911d.sketch_text.stroke-3"),sQuery(id+"FHMxAyK4CFUKdhS_1.wireOp",EDGE,"1cb9c079-ea9b-4899-8069-e0e3048e911d.sketch_text.stroke-4"),sQuery(id+"FHMxAyK4CFUKdhS_1.wireOp",EDGE,"1cb9c079-ea9b-4899-8069-e0e3048e911d.sketch_text.stroke-5"),sQuery(id+"FHMxAyK4CFUKdhS_1.wireOp",EDGE,"1cb9c079-ea9b-4899-8069-e0e3048e911d.sketch_text.stroke-6"),sQuery(id+"FHMxAyK4CFUKdhS_1.wireOp",EDGE,"1cb9c079-ea9b-4899-8069-e0e3048e911d.sketch_text.stroke-7"),sQuery(id+"FHMxAyK4CFUKdhS_1.wireOp",EDGE,"1cb9c079-ea9b-4899-8069-e0e3048e911d.sketch_text.stroke-8"),sQuery(id+"FHMxAyK4CFUKdhS_1.wireOp",EDGE,"1cb9c079-ea9b-4899-8069-e0e3048e911d.sketch_text.stroke-9"),sQuery(id+"FHMxAyK4CFUKdhS_1.wireOp",EDGE,"1cb9c079-ea9b-4899-8069-e0e3048e911d.sketch_text.stroke-10"),sQuery(id+"FHMxAyK4CFUKdhS_1.wireOp",EDGE,"1cb9c079-ea9b-4899-8069-e0e3048e911d.sketch_text.stroke-11"),sQuery(id+"FHMxAyK4CFUKdhS_1.wireOp",EDGE,"1cb9c079-ea9b-4899-8069-e0e3048e911d.sketch_text.stroke-12"),sQuery(id+"FHMxAyK4CFUKdhS_1.wireOp",EDGE,"1cb9c079-ea9b-4899-8069-e0e3048e911d.sketch_text.stroke-13"),sQuery(id+"FHMxAyK4CFUKdhS_1.wireOp",EDGE,"1cb9c079-ea9b-4899-8069-e0e3048e911d.sketch_text.stroke-14"),sQuery(id+"FHMxAyK4CFUKdhS_1.wireOp",EDGE,"1cb9c079-ea9b-4899-8069-e0e3048e911d.sketch_text.stroke-15"),sQuery(id+"FHMxAyK4CFUKdhS_1.wireOp",EDGE,"1cb9c079-ea9b-4899-8069-e0e3048e911d.sketch_text.stroke-16"),sQuery(id+"FHMxAyK4CFUKdhS_1.wireOp",EDGE,"1cb9c079-ea9b-4899-8069-e0e3048e911d.sketch_text.stroke-17"),sQuery(id+"FHMxAyK4CFUKdhS_1.wireOp",EDGE,"1cb9c079-ea9b-4899-8069-e0e3048e911d.sketch_text.stroke-18"),sQuery(id+"FHMxAyK4CFUKdhS_1.wireOp",EDGE,"1cb9c079-ea9b-4899-8069-e0e3048e911d.sketch_text.stroke-19"),sQuery(id+"FHMxAyK4CFUKdhS_1.wireOp",EDGE,"1cb9c079-ea9b-4899-8069-e0e3048e911d.sketch_text.stroke-20"),sQuery(id+"FHMxAyK4CFUKdhS_1.wireOp",EDGE,"1cb9c079-ea9b-4899-8069-e0e3048e911d.sketch_text.stroke-21"),sQuery(id+"FHMxAyK4CFUKdhS_1.wireOp",EDGE,"1cb9c079-ea9b-4899-8069-e0e3048e911d.sketch_text.stroke-22"),sQuery(id+"FHMxAyK4CFUKdhS_1.wireOp",EDGE,"1cb9c079-ea9b-4899-8069-e0e3048e911d.sketch_text.stroke-23"),sQuery(id+"FHMxAyK4CFUKdhS_1.wireOp",EDGE,"1cb9c079-ea9b-4899-8069-e0e3048e911d.sketch_text.stroke-24"),sQuery(id+"FHMxAyK4CFUKdhS_1.wireOp",EDGE,"1cb9c079-ea9b-4899-8069-e0e3048e911d.sketch_text.stroke-25"),sQuery(id+"FHMxAyK4CFUKdhS_1.wireOp",EDGE,"1cb9c079-ea9b-4899-8069-e0e3048e911d.sketch_text.stroke-26"),sQuery(id+"FHMxAyK4CFUKdhS_1.wireOp",EDGE,"1cb9c079-ea9b-4899-8069-e0e3048e911d.sketch_text.stroke-27"),sQuery(id+"FHMxAyK4CFUKdhS_1.wireOp",EDGE,"1cb9c079-ea9b-4899-8069-e0e3048e911d.sketch_text.stroke-28"),sQuery(id+"FHMxAyK4CFUKdhS_1.wireOp",EDGE,"1cb9c079-ea9b-4899-8069-e0e3048e911d.sketch_text.stroke-29"),sQuery(id+"FHMxAyK4CFUKdhS_1.wireOp",EDGE,"1cb9c079-ea9b-4899-8069-e0e3048e911d.sketch_text.stroke-30"),sQuery(id+"FHMxAyK4CFUKdhS_1.wireOp",EDGE,"1cb9c079-ea9b-4899-8069-e0e3048e911d.sketch_text.stroke-31"),sQuery(id+"FHMxAyK4CFUKdhS_1.wireOp",EDGE,"1cb9c079-ea9b-4899-8069-e0e3048e911d.sketch_text.stroke-32"),sQuery(id+"FHMxAyK4CFUKdhS_1.wireOp",EDGE,"1cb9c079-ea9b-4899-8069-e0e3048e911d.sketch_text.stroke-33"),sQuery(id+"FHMxAyK4CFUKdhS_1.wireOp",EDGE,"1cb9c079-ea9b-4899-8069-e0e3048e911d.sketch_text.stroke-34"),sQuery(id+"FHMxAyK4CFUKdhS_1.wireOp",EDGE,"1cb9c079-ea9b-4899-8069-e0e3048e911d.sketch_text.stroke-35"),sQuery(id+"FHMxAyK4CFUKdhS_1.wireOp",EDGE,"1cb9c079-ea9b-4899-8069-e0e3048e911d.sketch_text.stroke-36"),sQuery(id+"FHMxAyK4CFUKdhS_1.wireOp",EDGE,"1cb9c079-ea9b-4899-8069-e0e3048e911d.sketch_text.stroke-37"),sQuery(id+"FHMxAyK4CFUKdhS_1.wireOp",EDGE,"1cb9c079-ea9b-4899-8069-e0e3048e911d.sketch_text.stroke-38"),sQuery(id+"FHMxAyK4CFUKdhS_1.wireOp",EDGE,"1cb9c079-ea9b-4899-8069-e0e3048e911d.sketch_text.stroke-39"),sQuery(id+"FHMxAyK4CFUKdhS_1.wireOp",EDGE,"1cb9c079-ea9b-4899-8069-e0e3048e911d.sketch_text.stroke-40"),sQuery(id+"FHMxAyK4CFUKdhS_1.wireOp",EDGE,"1cb9c079-ea9b-4899-8069-e0e3048e911d.sketch_text.stroke-41"),sQuery(id+"FHMxAyK4CFUKdhS_1.wireOp",EDGE,"1cb9c079-ea9b-4899-8069-e0e3048e911d.sketch_text.stroke-42"),sQuery(id+"FHMxAyK4CFUKdhS_1.wireOp",EDGE,"1cb9c079-ea9b-4899-8069-e0e3048e911d.sketch_text.stroke-43"),sQuery(id+"FHMxAyK4CFUKdhS_1.wireOp",EDGE,"1cb9c079-ea9b-4899-8069-e0e3048e911d.sketch_text.stroke-44"),sQuery(id+"FHMxAyK4CFUKdhS_1.wireOp",EDGE,"1cb9c079-ea9b-4899-8069-e0e3048e911d.sketch_text.stroke-45"),sQuery(id+"FHMxAyK4CFUKdhS_1.wireOp",EDGE,"1cb9c079-ea9b-4899-8069-e0e3048e911d.sketch_text.stroke-46"),sQuery(id+"FHMxAyK4CFUKdhS_1.wireOp",EDGE,"1cb9c079-ea9b-4899-8069-e0e3048e911d.sketch_text.stroke-47"),sQuery(id+"FHMxAyK4CFUKdhS_1.wireOp",EDGE,"1cb9c079-ea9b-4899-8069-e0e3048e911d.sketch_text.stroke-48"),sQuery(id+"FHMxAyK4CFUKdhS_1.wireOp",EDGE,"1cb9c079-ea9b-4899-8069-e0e3048e911d.sketch_text.stroke-49"),sQuery(id+"FHMxAyK4CFUKdhS_1.wireOp",EDGE,"1cb9c079-ea9b-4899-8069-e0e3048e911d.sketch_text.stroke-50"),sQuery(id+"FHMxAyK4CFUKdhS_1.wireOp",EDGE,"1cb9c079-ea9b-4899-8069-e0e3048e911d.sketch_text.stroke-51"),sQuery(id+"FHMxAyK4CFUKdhS_1.wireOp",EDGE,"1cb9c079-ea9b-4899-8069-e0e3048e911d.sketch_text.stroke-52"),sQuery(id+"FHMxAyK4CFUKdhS_1.wireOp",EDGE,"1cb9c079-ea9b-4899-8069-e0e3048e911d.sketch_text.stroke-53"),sQuery(id+"FHMxAyK4CFUKdhS_1.wireOp",EDGE,"1cb9c079-ea9b-4899-8069-e0e3048e911d.sketch_text.stroke-54"),sQuery(id+"FHMxAyK4CFUKdhS_1.wireOp",EDGE,"1cb9c079-ea9b-4899-8069-e0e3048e911d.sketch_text.stroke-55"),sQuery(id+"FHMxAyK4CFUKdhS_1.wireOp",EDGE,"1cb9c079-ea9b-4899-8069-e0e3048e911d.sketch_text.stroke-56"),sQuery(id+"FHMxAyK4CFUKdhS_1.wireOp",EDGE,"1cb9c079-ea9b-4899-8069-e0e3048e911d.sketch_text.stroke-57"),sQuery(id+"FHMxAyK4CFUKdhS_1.wireOp",EDGE,"1cb9c079-ea9b-4899-8069-e0e3048e911d.sketch_text.stroke-58"),sQuery(id+"FHMxAyK4CFUKdhS_1.wireOp",EDGE,"1cb9c079-ea9b-4899-8069-e0e3048e911d.sketch_text.stroke-59"),sQuery(id+"FHMxAyK4CFUKdhS_1.wireOp",EDGE,"1cb9c079-ea9b-4899-8069-e0e3048e911d.sketch_text.stroke-60"),sQuery(id+"FHMxAyK4CFUKdhS_1.wireOp",EDGE,"1cb9c079-ea9b-4899-8069-e0e3048e911d.sketch_text.stroke-61"),sQuery(id+"FHMxAyK4CFUKdhS_1.wireOp",EDGE,"1cb9c079-ea9b-4899-8069-e0e3048e911d.sketch_text.stroke-62"),sQuery(id+"FHMxAyK4CFUKdhS_1.wireOp",EDGE,"1cb9c079-ea9b-4899-8069-e0e3048e911d.sketch_text.stroke-71"),sQuery(id+"FHMxAyK4CFUKdhS_1.wireOp",EDGE,"1cb9c079-ea9b-4899-8069-e0e3048e911d.sketch_text.stroke-72"),sQuery(id+"FHMxAyK4CFUKdhS_1.wireOp",EDGE,"1cb9c079-ea9b-4899-8069-e0e3048e911d.sketch_text.stroke-73"),sQuery(id+"FHMxAyK4CFUKdhS_1.wireOp",EDGE,"1cb9c079-ea9b-4899-8069-e0e3048e911d.sketch_text.stroke-74"),sQuery(id+"FHMxAyK4CFUKdhS_1.wireOp",EDGE,"1cb9c079-ea9b-4899-8069-e0e3048e911d.sketch_text.stroke-75"),sQuery(id+"FHMxAyK4CFUKdhS_1.wireOp",EDGE,"1cb9c079-ea9b-4899-8069-e0e3048e911d.sketch_text.stroke-76"),sQuery(id+"FHMxAyK4CFUKdhS_1.wireOp",EDGE,"1cb9c079-ea9b-4899-8069-e0e3048e911d.sketch_text.stroke-77"),sQuery(id+"FHMxAyK4CFUKdhS_1.wireOp",EDGE,"1cb9c079-ea9b-4899-8069-e0e3048e911d.sketch_text.stroke-78"),sQuery(id+"FHMxAyK4CFUKdhS_1.wireOp",EDGE,"1cb9c079-ea9b-4899-8069-e0e3048e911d.sketch_text.stroke-79"),sQuery(id+"FHMxAyK4CFUKdhS_1.wireOp",EDGE,"1cb9c079-ea9b-4899-8069-e0e3048e911d.sketch_text.stroke-80"),sQuery(id+"FHMxAyK4CFUKdhS_1.wireOp",EDGE,"1cb9c079-ea9b-4899-8069-e0e3048e911d.sketch_text.stroke-81"),sQuery(id+"FHMxAyK4CFUKdhS_1.wireOp",EDGE,"1cb9c079-ea9b-4899-8069-e0e3048e911d.sketch_text.stroke-82"),sQuery(id+"FHMxAyK4CFUKdhS_1.wireOp",EDGE,"1cb9c079-ea9b-4899-8069-e0e3048e911d.sketch_text.stroke-83"),sQuery(id+"FHMxAyK4CFUKdhS_1.wireOp",EDGE,"1cb9c079-ea9b-4899-8069-e0e3048e911d.sketch_text.stroke-84"),sQuery(id+"FHMxAyK4CFUKdhS_1.wireOp",EDGE,"1cb9c079-ea9b-4899-8069-e0e3048e911d.sketch_text.stroke-85"),sQuery(id+"FHMxAyK4CFUKdhS_1.wireOp",EDGE,"1cb9c079-ea9b-4899-8069-e0e3048e911d.sketch_text.stroke-86"),sQuery(id+"FHMxAyK4CFUKdhS_1.wireOp",EDGE,"1cb9c079-ea9b-4899-8069-e0e3048e911d.sketch_text.stroke-87"),sQuery(id+"FHMxAyK4CFUKdhS_1.wireOp",EDGE,"1cb9c079-ea9b-4899-8069-e0e3048e911d.sketch_text.stroke-88"),sQuery(id+"FHMxAyK4CFUKdhS_1.wireOp",EDGE,"1cb9c079-ea9b-4899-8069-e0e3048e911d.sketch_text.stroke-89"),sQuery(id+"FHMxAyK4CFUKdhS_1.wireOp",EDGE,"1cb9c079-ea9b-4899-8069-e0e3048e911d.sketch_text.stroke-90"),sQuery(id+"FHMxAyK4CFUKdhS_1.wireOp",EDGE,"1cb9c079-ea9b-4899-8069-e0e3048e911d.sketch_text.stroke-91"),sQuery(id+"FHMxAyK4CFUKdhS_1.wireOp",EDGE,"1cb9c079-ea9b-4899-8069-e0e3048e911d.sketch_text.stroke-92"),sQuery(id+"FHMxAyK4CFUKdhS_1.wireOp",EDGE,"1cb9c079-ea9b-4899-8069-e0e3048e911d.sketch_text.stroke-93"),sQuery(id+"FHMxAyK4CFUKdhS_1.wireOp",EDGE,"1cb9c079-ea9b-4899-8069-e0e3048e911d.sketch_text.stroke-94"),sQuery(id+"FHMxAyK4CFUKdhS_1.wireOp",EDGE,"1cb9c079-ea9b-4899-8069-e0e3048e911d.sketch_text.stroke-95"),sQuery(id+"FHMxAyK4CFUKdhS_1.wireOp",EDGE,"1cb9c079-ea9b-4899-8069-e0e3048e911d.sketch_text.stroke-96"),sQuery(id+"FHMxAyK4CFUKdhS_1.wireOp",EDGE,"1cb9c079-ea9b-4899-8069-e0e3048e911d.sketch_text.stroke-97"),sQuery(id+"FHMxAyK4CFUKdhS_1.wireOp",EDGE,"1cb9c079-ea9b-4899-8069-e0e3048e911d.sketch_text.stroke-103"),sQuery(id+"FHMxAyK4CFUKdhS_1.wireOp",EDGE,"1cb9c079-ea9b-4899-8069-e0e3048e911d.sketch_text.stroke-104"),sQuery(id+"FHMxAyK4CFUKdhS_1.wireOp",EDGE,"1cb9c079-ea9b-4899-8069-e0e3048e911d.sketch_text.stroke-105"),sQuery(id+"FHMxAyK4CFUKdhS_1.wireOp",EDGE,"1cb9c079-ea9b-4899-8069-e0e3048e911d.sketch_text.stroke-106"),sQuery(id+"FHMxAyK4CFUKdhS_1.wireOp",EDGE,"1cb9c079-ea9b-4899-8069-e0e3048e911d.sketch_text.stroke-107"),sQuery(id+"FHMxAyK4CFUKdhS_1.wireOp",EDGE,"1cb9c079-ea9b-4899-8069-e0e3048e911d.sketch_text.stroke-108"),sQuery(id+"FHMxAyK4CFUKdhS_1.wireOp",EDGE,"1cb9c079-ea9b-4899-8069-e0e3048e911d.sketch_text.stroke-109"),sQuery(id+"FHMxAyK4CFUKdhS_1.wireOp",EDGE,"1cb9c079-ea9b-4899-8069-e0e3048e911d.sketch_text.stroke-110"),sQuery(id+"FHMxAyK4CFUKdhS_1.wireOp",EDGE,"1cb9c079-ea9b-4899-8069-e0e3048e911d.sketch_text.stroke-111"),sQuery(id+"FHMxAyK4CFUKdhS_1.wireOp",EDGE,"1cb9c079-ea9b-4899-8069-e0e3048e911d.sketch_text.stroke-112"),sQuery(id+"FHMxAyK4CFUKdhS_1.wireOp",EDGE,"1cb9c079-ea9b-4899-8069-e0e3048e911d.sketch_text.stroke-113"),sQuery(id+"FHMxAyK4CFUKdhS_1.wireOp",EDGE,"1cb9c079-ea9b-4899-8069-e0e3048e911d.sketch_text.stroke-114"),sQuery(id+"FHMxAyK4CFUKdhS_1.wireOp",EDGE,"1cb9c079-ea9b-4899-8069-e0e3048e911d.sketch_text.stroke-115"),sQuery(id+"FHMxAyK4CFUKdhS_1.wireOp",EDGE,"1cb9c079-ea9b-4899-8069-e0e3048e911d.sketch_text.stroke-116"),sQuery(id+"FHMxAyK4CFUKdhS_1.wireOp",EDGE,"1cb9c079-ea9b-4899-8069-e0e3048e911d.sketch_text.stroke-117"),sQuery(id+"FHMxAyK4CFUKdhS_1.wireOp",EDGE,"1cb9c079-ea9b-4899-8069-e0e3048e911d.sketch_text.stroke-118"),sQuery(id+"FHMxAyK4CFUKdhS_1.wireOp",EDGE,"1cb9c079-ea9b-4899-8069-e0e3048e911d.sketch_text.stroke-119"),sQuery(id+"FHMxAyK4CFUKdhS_1.wireOp",EDGE,"1cb9c079-ea9b-4899-8069-e0e3048e911d.sketch_text.stroke-120"),sQuery(id+"FHMxAyK4CFUKdhS_1.wireOp",EDGE,"1cb9c079-ea9b-4899-8069-e0e3048e911d.sketch_text.stroke-121"),sQuery(id+"FHMxAyK4CFUKdhS_1.wireOp",EDGE,"1cb9c079-ea9b-4899-8069-e0e3048e911d.sketch_text.stroke-122"),sQuery(id+"FHMxAyK4CFUKdhS_1.wireOp",EDGE,"1cb9c079-ea9b-4899-8069-e0e3048e911d.sketch_text.stroke-123"),sQuery(id+"FHMxAyK4CFUKdhS_1.wireOp",EDGE,"1cb9c079-ea9b-4899-8069-e0e3048e911d.sketch_text.stroke-124"),sQuery(id+"FHMxAyK4CFUKdhS_1.wireOp",EDGE,"1cb9c079-ea9b-4899-8069-e0e3048e911d.sketch_text.stroke-125"),sQuery(id+"FHMxAyK4CFUKdhS_1.wireOp",EDGE,"1cb9c079-ea9b-4899-8069-e0e3048e911d.sketch_text.stroke-126"),sQuery(id+"FHMxAyK4CFUKdhS_1.wireOp",EDGE,"1cb9c079-ea9b-4899-8069-e0e3048e911d.sketch_text.stroke-127"),sQuery(id+"FHMxAyK4CFUKdhS_1.wireOp",EDGE,"1cb9c079-ea9b-4899-8069-e0e3048e911d.sketch_text.stroke-128"),sQuery(id+"FHMxAyK4CFUKdhS_1.wireOp",EDGE,"1cb9c079-ea9b-4899-8069-e0e3048e911d.sketch_text.stroke-129"),sQuery(id+"FHMxAyK4CFUKdhS_1.wireOp",EDGE,"1cb9c079-ea9b-4899-8069-e0e3048e911d.sketch_text.stroke-130"),sQuery(id+"FHMxAyK4CFUKdhS_1.wireOp",EDGE,"1cb9c079-ea9b-4899-8069-e0e3048e911d.sketch_text.stroke-131"),sQuery(id+"FHMxAyK4CFUKdhS_1.wireOp",EDGE,"1cb9c079-ea9b-4899-8069-e0e3048e911d.sketch_text.stroke-132"),sQuery(id+"FHMxAyK4CFUKdhS_1.wireOp",EDGE,"1cb9c079-ea9b-4899-8069-e0e3048e911d.sketch_text.stroke-133"),sQuery(id+"FHMxAyK4CFUKdhS_1.wireOp",EDGE,"1cb9c079-ea9b-4899-8069-e0e3048e911d.sketch_text.stroke-134"),sQuery(id+"FHMxAyK4CFUKdhS_1.wireOp",EDGE,"1cb9c079-ea9b-4899-8069-e0e3048e911d.sketch_text.stroke-135"),sQuery(id+"FHMxAyK4CFUKdhS_1.wireOp",EDGE,"1cb9c079-ea9b-4899-8069-e0e3048e911d.sketch_text.stroke-136"),sQuery(id+"FHMxAyK4CFUKdhS_1.wireOp",EDGE,"1cb9c079-ea9b-4899-8069-e0e3048e911d.sketch_text.stroke-137"),sQuery(id+"FHMxAyK4CFUKdhS_1.wireOp",EDGE,"1cb9c079-ea9b-4899-8069-e0e3048e911d.sketch_text.stroke-138"),sQuery(id+"FHMxAyK4CFUKdhS_1.wireOp",EDGE,"1cb9c079-ea9b-4899-8069-e0e3048e911d.sketch_text.stroke-139"),sQuery(id+"FHMxAyK4CFUKdhS_1.wireOp",EDGE,"1cb9c079-ea9b-4899-8069-e0e3048e911d.sketch_text.stroke-140"),sQuery(id+"FHMxAyK4CFUKdhS_1.wireOp",EDGE,"1cb9c079-ea9b-4899-8069-e0e3048e911d.sketch_text.stroke-141"),sQuery(id+"FHMxAyK4CFUKdhS_1.wireOp",EDGE,"1cb9c079-ea9b-4899-8069-e0e3048e911d.sketch_text.stroke-142"),sQuery(id+"FHMxAyK4CFUKdhS_1.wireOp",EDGE,"1cb9c079-ea9b-4899-8069-e0e3048e911d.sketch_text.stroke-143"),sQuery(id+"FHMxAyK4CFUKdhS_1.wireOp",EDGE,"1cb9c079-ea9b-4899-8069-e0e3048e911d.sketch_text.stroke-144"),sQuery(id+"FHMxAyK4CFUKdhS_1.wireOp",EDGE,"1cb9c079-ea9b-4899-8069-e0e3048e911d.sketch_text.stroke-145"),sQuery(id+"FHMxAyK4CFUKdhS_1.wireOp",EDGE,"1cb9c079-ea9b-4899-8069-e0e3048e911d.sketch_text.stroke-146"),sQuery(id+"FHMxAyK4CFUKdhS_1.wireOp",EDGE,"1cb9c079-ea9b-4899-8069-e0e3048e911d.sketch_text.stroke-147"),sQuery(id+"FHMxAyK4CFUKdhS_1.wireOp",EDGE,"1cb9c079-ea9b-4899-8069-e0e3048e911d.sketch_text.stroke-148"),sQuery(id+"FHMxAyK4CFUKdhS_1.wireOp",EDGE,"1cb9c079-ea9b-4899-8069-e0e3048e911d.sketch_text.stroke-149"),sQuery(id+"FHMxAyK4CFUKdhS_1.wireOp",EDGE,"1cb9c079-ea9b-4899-8069-e0e3048e911d.sketch_text.stroke-150"),sQuery(id+"FHMxAyK4CFUKdhS_1.wireOp",EDGE,"1cb9c079-ea9b-4899-8069-e0e3048e911d.sketch_text.stroke-151"),sQuery(id+"FHMxAyK4CFUKdhS_1.wireOp",EDGE,"1cb9c079-ea9b-4899-8069-e0e3048e911d.sketch_text.stroke-152"),sQuery(id+"FHMxAyK4CFUKdhS_1.wireOp",EDGE,"1cb9c079-ea9b-4899-8069-e0e3048e911d.sketch_text.stroke-153"),sQuery(id+"FHMxAyK4CFUKdhS_1.wireOp",EDGE,"1cb9c079-ea9b-4899-8069-e0e3048e911d.sketch_text.stroke-159"),sQuery(id+"FHMxAyK4CFUKdhS_1.wireOp",EDGE,"1cb9c079-ea9b-4899-8069-e0e3048e911d.sketch_text.stroke-160"),sQuery(id+"FHMxAyK4CFUKdhS_1.wireOp",EDGE,"1cb9c079-ea9b-4899-8069-e0e3048e911d.sketch_text.stroke-161"),sQuery(id+"FHMxAyK4CFUKdhS_1.wireOp",EDGE,"1cb9c079-ea9b-4899-8069-e0e3048e911d.sketch_text.stroke-162"),sQuery(id+"FHMxAyK4CFUKdhS_1.wireOp",EDGE,"1cb9c079-ea9b-4899-8069-e0e3048e911d.sketch_text.stroke-163"),sQuery(id+"FHMxAyK4CFUKdhS_1.wireOp",EDGE,"1cb9c079-ea9b-4899-8069-e0e3048e911d.sketch_text.stroke-164"),sQuery(id+"FHMxAyK4CFUKdhS_1.wireOp",EDGE,"1cb9c079-ea9b-4899-8069-e0e3048e911d.sketch_text.stroke-165"),sQuery(id+"FHMxAyK4CFUKdhS_1.wireOp",EDGE,"1cb9c079-ea9b-4899-8069-e0e3048e911d.sketch_text.stroke-166"),sQuery(id+"FHMxAyK4CFUKdhS_1.wireOp",EDGE,"1cb9c079-ea9b-4899-8069-e0e3048e911d.sketch_text.stroke-167"),sQuery(id+"FHMxAyK4CFUKdhS_1.wireOp",EDGE,"1cb9c079-ea9b-4899-8069-e0e3048e911d.sketch_text.stroke-168"),sQuery(id+"FHMxAyK4CFUKdhS_1.wireOp",EDGE,"1cb9c079-ea9b-4899-8069-e0e3048e911d.sketch_text.stroke-169"),sQuery(id+"FHMxAyK4CFUKdhS_1.wireOp",EDGE,"1cb9c079-ea9b-4899-8069-e0e3048e911d.sketch_text.stroke-170"),sQuery(id+"FHMxAyK4CFUKdhS_1.wireOp",EDGE,"1cb9c079-ea9b-4899-8069-e0e3048e911d.sketch_text.stroke-171"),sQuery(id+"FHMxAyK4CFUKdhS_1.wireOp",EDGE,"1cb9c079-ea9b-4899-8069-e0e3048e911d.sketch_text.stroke-172"),sQuery(id+"FHMxAyK4CFUKdhS_1.wireOp",EDGE,"1cb9c079-ea9b-4899-8069-e0e3048e911d.sketch_text.stroke-173"),sQuery(id+"FHMxAyK4CFUKdhS_1.wireOp",EDGE,"1cb9c079-ea9b-4899-8069-e0e3048e911d.sketch_text.stroke-174"),sQuery(id+"FHMxAyK4CFUKdhS_1.wireOp",EDGE,"1cb9c079-ea9b-4899-8069-e0e3048e911d.sketch_text.stroke-175"),sQuery(id+"FHMxAyK4CFUKdhS_1.wireOp",EDGE,"1cb9c079-ea9b-4899-8069-e0e3048e911d.sketch_text.stroke-176"),sQuery(id+"FHMxAyK4CFUKdhS_1.wireOp",EDGE,"1cb9c079-ea9b-4899-8069-e0e3048e911d.sketch_text.stroke-177"),sQuery(id+"FHMxAyK4CFUKdhS_1.wireOp",EDGE,"1cb9c079-ea9b-4899-8069-e0e3048e911d.sketch_text.stroke-178"),sQuery(id+"FHMxAyK4CFUKdhS_1.wireOp",EDGE,"1cb9c079-ea9b-4899-8069-e0e3048e911d.sketch_text.stroke-179"),sQuery(id+"FHMxAyK4CFUKdhS_1.wireOp",EDGE,"1cb9c079-ea9b-4899-8069-e0e3048e911d.sketch_text.stroke-180"),sQuery(id+"F3.wireOp",EDGE,"8007402e-1a4e-4a06-85a5-2af08e553504"),subQ2])],"isStart":true}),makeQuery(id+"F4.opExtrude","SWEPT_FACE",FACE,{"disambiguationData":[OSD([subQ2])]})])],"derivedFrom":makeQuery(id+"F4.opExtrude","CAP_EDGE",EDGE,{"disambiguationData":[OSD([subQ2])],"isStart":true})});}
            var Q14;
            {var subQ0=sQuery(id+"F0.wireOp",EDGE,"E0.top");var subQ1=sQuery(id+"F0.wireOp",EDGE,"E0.bottom");var subQ2=sQuery(id+"F3.wireOp",EDGE,"727ac2c1-f511-4829-95a7-a443ef16a4cd");Q14=makeQuery(id+"F4.boolean.opBoolean","SPLIT",EDGE,{"disambiguationData":[TD([makeQuery(id+"F1.opExtrude","CAP_FACE",FACE,{"disambiguationData":[OSD([subQ1,subQ0,sQuery(id+"F0.wireOp",EDGE,"E0.left"),sQuery(id+"F0.wireOp",EDGE,"E0.right")])],"isStart":false}),makeQuery(id+"F1.opExtrude","SWEPT_FACE",FACE,{"disambiguationData":[OSD([subQ0])]}),makeQuery(id+"F4.opExtrude","CAP_FACE",FACE,{"disambiguationData":[OSD([subQ1,sQuery(id+"F2.wireOp",EDGE,"fcba4419-a2ee-464f-be9d-58f11bf3418b.sketch_text.stroke-0"),sQuery(id+"F2.wireOp",EDGE,"fcba4419-a2ee-464f-be9d-58f11bf3418b.sketch_text.stroke-1"),sQuery(id+"F2.wireOp",EDGE,"fcba4419-a2ee-464f-be9d-58f11bf3418b.sketch_text.stroke-2"),sQuery(id+"F2.wireOp",EDGE,"fcba4419-a2ee-464f-be9d-58f11bf3418b.sketch_text.stroke-3"),sQuery(id+"F2.wireOp",EDGE,"fcba4419-a2ee-464f-be9d-58f11bf3418b.sketch_text.stroke-4"),sQuery(id+"F2.wireOp",EDGE,"fcba4419-a2ee-464f-be9d-58f11bf3418b.sketch_text.stroke-5"),sQuery(id+"F2.wireOp",EDGE,"fcba4419-a2ee-464f-be9d-58f11bf3418b.sketch_text.stroke-6"),sQuery(id+"F2.wireOp",EDGE,"fcba4419-a2ee-464f-be9d-58f11bf3418b.sketch_text.stroke-7"),sQuery(id+"F2.wireOp",EDGE,"fcba4419-a2ee-464f-be9d-58f11bf3418b.sketch_text.stroke-8"),sQuery(id+"F2.wireOp",EDGE,"fcba4419-a2ee-464f-be9d-58f11bf3418b.sketch_text.stroke-9"),sQuery(id+"F2.wireOp",EDGE,"fcba4419-a2ee-464f-be9d-58f11bf3418b.sketch_text.stroke-10"),sQuery(id+"F2.wireOp",EDGE,"fcba4419-a2ee-464f-be9d-58f11bf3418b.sketch_text.stroke-11"),sQuery(id+"F2.wireOp",EDGE,"fcba4419-a2ee-464f-be9d-58f11bf3418b.sketch_text.stroke-12"),sQuery(id+"F2.wireOp",EDGE,"fcba4419-a2ee-464f-be9d-58f11bf3418b.sketch_text.stroke-13"),sQuery(id+"F2.wireOp",EDGE,"fcba4419-a2ee-464f-be9d-58f11bf3418b.sketch_text.stroke-14"),sQuery(id+"F2.wireOp",EDGE,"fcba4419-a2ee-464f-be9d-58f11bf3418b.sketch_text.stroke-15"),sQuery(id+"F2.wireOp",EDGE,"fcba4419-a2ee-464f-be9d-58f11bf3418b.sketch_text.stroke-16"),sQuery(id+"F2.wireOp",EDGE,"fcba4419-a2ee-464f-be9d-58f11bf3418b.sketch_text.stroke-17"),sQuery(id+"F2.wireOp",EDGE,"fcba4419-a2ee-464f-be9d-58f11bf3418b.sketch_text.stroke-18"),sQuery(id+"F2.wireOp",EDGE,"fcba4419-a2ee-464f-be9d-58f11bf3418b.sketch_text.stroke-19"),sQuery(id+"F2.wireOp",EDGE,"fcba4419-a2ee-464f-be9d-58f11bf3418b.sketch_text.stroke-20"),sQuery(id+"F2.wireOp",EDGE,"fcba4419-a2ee-464f-be9d-58f11bf3418b.sketch_text.stroke-21"),sQuery(id+"F2.wireOp",EDGE,"fcba4419-a2ee-464f-be9d-58f11bf3418b.sketch_text.stroke-22"),sQuery(id+"F2.wireOp",EDGE,"fcba4419-a2ee-464f-be9d-58f11bf3418b.sketch_text.stroke-23"),sQuery(id+"F2.wireOp",EDGE,"fcba4419-a2ee-464f-be9d-58f11bf3418b.sketch_text.stroke-24"),sQuery(id+"F2.wireOp",EDGE,"fcba4419-a2ee-464f-be9d-58f11bf3418b.sketch_text.stroke-25"),sQuery(id+"F2.wireOp",EDGE,"fcba4419-a2ee-464f-be9d-58f11bf3418b.sketch_text.stroke-26"),sQuery(id+"F2.wireOp",EDGE,"fcba4419-a2ee-464f-be9d-58f11bf3418b.sketch_text.stroke-27"),sQuery(id+"F2.wireOp",EDGE,"fcba4419-a2ee-464f-be9d-58f11bf3418b.sketch_text.stroke-28"),sQuery(id+"F2.wireOp",EDGE,"fcba4419-a2ee-464f-be9d-58f11bf3418b.sketch_text.stroke-29"),sQuery(id+"F2.wireOp",EDGE,"fcba4419-a2ee-464f-be9d-58f11bf3418b.sketch_text.stroke-30"),sQuery(id+"F2.wireOp",EDGE,"fcba4419-a2ee-464f-be9d-58f11bf3418b.sketch_text.stroke-31"),sQuery(id+"F2.wireOp",EDGE,"fcba4419-a2ee-464f-be9d-58f11bf3418b.sketch_text.stroke-32"),sQuery(id+"F2.wireOp",EDGE,"fcba4419-a2ee-464f-be9d-58f11bf3418b.sketch_text.stroke-33"),sQuery(id+"F2.wireOp",EDGE,"fcba4419-a2ee-464f-be9d-58f11bf3418b.sketch_text.stroke-34"),sQuery(id+"F2.wireOp",EDGE,"fcba4419-a2ee-464f-be9d-58f11bf3418b.sketch_text.stroke-35"),sQuery(id+"F2.wireOp",EDGE,"fcba4419-a2ee-464f-be9d-58f11bf3418b.sketch_text.stroke-36"),sQuery(id+"F2.wireOp",EDGE,"fcba4419-a2ee-464f-be9d-58f11bf3418b.sketch_text.stroke-37"),sQuery(id+"F2.wireOp",EDGE,"fcba4419-a2ee-464f-be9d-58f11bf3418b.sketch_text.stroke-38"),sQuery(id+"F2.wireOp",EDGE,"fcba4419-a2ee-464f-be9d-58f11bf3418b.sketch_text.stroke-39"),sQuery(id+"F2.wireOp",EDGE,"fcba4419-a2ee-464f-be9d-58f11bf3418b.sketch_text.stroke-40"),sQuery(id+"F2.wireOp",EDGE,"fcba4419-a2ee-464f-be9d-58f11bf3418b.sketch_text.stroke-41"),sQuery(id+"F2.wireOp",EDGE,"fcba4419-a2ee-464f-be9d-58f11bf3418b.sketch_text.stroke-42"),sQuery(id+"F2.wireOp",EDGE,"fcba4419-a2ee-464f-be9d-58f11bf3418b.sketch_text.stroke-43"),sQuery(id+"F2.wireOp",EDGE,"fcba4419-a2ee-464f-be9d-58f11bf3418b.sketch_text.stroke-44"),sQuery(id+"F2.wireOp",EDGE,"fcba4419-a2ee-464f-be9d-58f11bf3418b.sketch_text.stroke-45"),sQuery(id+"F2.wireOp",EDGE,"fcba4419-a2ee-464f-be9d-58f11bf3418b.sketch_text.stroke-46"),sQuery(id+"F2.wireOp",EDGE,"fcba4419-a2ee-464f-be9d-58f11bf3418b.sketch_text.stroke-47"),sQuery(id+"F2.wireOp",EDGE,"fcba4419-a2ee-464f-be9d-58f11bf3418b.sketch_text.stroke-48"),sQuery(id+"F2.wireOp",EDGE,"fcba4419-a2ee-464f-be9d-58f11bf3418b.sketch_text.stroke-49"),sQuery(id+"F2.wireOp",EDGE,"fcba4419-a2ee-464f-be9d-58f11bf3418b.sketch_text.stroke-50"),sQuery(id+"F2.wireOp",EDGE,"fcba4419-a2ee-464f-be9d-58f11bf3418b.sketch_text.stroke-51"),sQuery(id+"F2.wireOp",EDGE,"fcba4419-a2ee-464f-be9d-58f11bf3418b.sketch_text.stroke-52"),sQuery(id+"F2.wireOp",EDGE,"fcba4419-a2ee-464f-be9d-58f11bf3418b.sketch_text.stroke-53"),sQuery(id+"F2.wireOp",EDGE,"fcba4419-a2ee-464f-be9d-58f11bf3418b.sketch_text.stroke-54"),sQuery(id+"F2.wireOp",EDGE,"fcba4419-a2ee-464f-be9d-58f11bf3418b.sketch_text.stroke-55"),sQuery(id+"F2.wireOp",EDGE,"fcba4419-a2ee-464f-be9d-58f11bf3418b.sketch_text.stroke-56"),sQuery(id+"F2.wireOp",EDGE,"fcba4419-a2ee-464f-be9d-58f11bf3418b.sketch_text.stroke-57"),sQuery(id+"F2.wireOp",EDGE,"fcba4419-a2ee-464f-be9d-58f11bf3418b.sketch_text.stroke-58"),sQuery(id+"F2.wireOp",EDGE,"fcba4419-a2ee-464f-be9d-58f11bf3418b.sketch_text.stroke-59"),sQuery(id+"F2.wireOp",EDGE,"fcba4419-a2ee-464f-be9d-58f11bf3418b.sketch_text.stroke-60"),sQuery(id+"F2.wireOp",EDGE,"fcba4419-a2ee-464f-be9d-58f11bf3418b.sketch_text.stroke-61"),sQuery(id+"F2.wireOp",EDGE,"fcba4419-a2ee-464f-be9d-58f11bf3418b.sketch_text.stroke-62"),sQuery(id+"F2.wireOp",EDGE,"fcba4419-a2ee-464f-be9d-58f11bf3418b.sketch_text.stroke-63"),sQuery(id+"F2.wireOp",EDGE,"fcba4419-a2ee-464f-be9d-58f11bf3418b.sketch_text.stroke-64"),sQuery(id+"F2.wireOp",EDGE,"fcba4419-a2ee-464f-be9d-58f11bf3418b.sketch_text.stroke-65"),sQuery(id+"F2.wireOp",EDGE,"fcba4419-a2ee-464f-be9d-58f11bf3418b.sketch_text.stroke-66"),sQuery(id+"F2.wireOp",EDGE,"fcba4419-a2ee-464f-be9d-58f11bf3418b.sketch_text.stroke-67"),sQuery(id+"F2.wireOp",EDGE,"fcba4419-a2ee-464f-be9d-58f11bf3418b.sketch_text.stroke-68"),sQuery(id+"F2.wireOp",EDGE,"fcba4419-a2ee-464f-be9d-58f11bf3418b.sketch_text.stroke-69"),sQuery(id+"F2.wireOp",EDGE,"fcba4419-a2ee-464f-be9d-58f11bf3418b.sketch_text.stroke-70"),sQuery(id+"F2.wireOp",EDGE,"fcba4419-a2ee-464f-be9d-58f11bf3418b.sketch_text.stroke-71"),sQuery(id+"F2.wireOp",EDGE,"fcba4419-a2ee-464f-be9d-58f11bf3418b.sketch_text.stroke-72"),sQuery(id+"F2.wireOp",EDGE,"fcba4419-a2ee-464f-be9d-58f11bf3418b.sketch_text.stroke-73"),sQuery(id+"F2.wireOp",EDGE,"fcba4419-a2ee-464f-be9d-58f11bf3418b.sketch_text.stroke-74"),sQuery(id+"F2.wireOp",EDGE,"fcba4419-a2ee-464f-be9d-58f11bf3418b.sketch_text.stroke-75"),sQuery(id+"F2.wireOp",EDGE,"fcba4419-a2ee-464f-be9d-58f11bf3418b.sketch_text.stroke-76"),sQuery(id+"F2.wireOp",EDGE,"fcba4419-a2ee-464f-be9d-58f11bf3418b.sketch_text.stroke-77"),sQuery(id+"F2.wireOp",EDGE,"fcba4419-a2ee-464f-be9d-58f11bf3418b.sketch_text.stroke-78"),sQuery(id+"F2.wireOp",EDGE,"fcba4419-a2ee-464f-be9d-58f11bf3418b.sketch_text.stroke-79"),sQuery(id+"F2.wireOp",EDGE,"fcba4419-a2ee-464f-be9d-58f11bf3418b.sketch_text.stroke-80"),sQuery(id+"F2.wireOp",EDGE,"fcba4419-a2ee-464f-be9d-58f11bf3418b.sketch_text.stroke-81"),sQuery(id+"F2.wireOp",EDGE,"fcba4419-a2ee-464f-be9d-58f11bf3418b.sketch_text.stroke-82"),sQuery(id+"F2.wireOp",EDGE,"fcba4419-a2ee-464f-be9d-58f11bf3418b.sketch_text.stroke-83"),sQuery(id+"F2.wireOp",EDGE,"fcba4419-a2ee-464f-be9d-58f11bf3418b.sketch_text.stroke-84"),sQuery(id+"F2.wireOp",EDGE,"fcba4419-a2ee-464f-be9d-58f11bf3418b.sketch_text.stroke-85"),sQuery(id+"F2.wireOp",EDGE,"fcba4419-a2ee-464f-be9d-58f11bf3418b.sketch_text.stroke-86"),sQuery(id+"F2.wireOp",EDGE,"fcba4419-a2ee-464f-be9d-58f11bf3418b.sketch_text.stroke-87"),sQuery(id+"F2.wireOp",EDGE,"fcba4419-a2ee-464f-be9d-58f11bf3418b.sketch_text.stroke-88"),sQuery(id+"F2.wireOp",EDGE,"fcba4419-a2ee-464f-be9d-58f11bf3418b.sketch_text.stroke-89"),sQuery(id+"F2.wireOp",EDGE,"fcba4419-a2ee-464f-be9d-58f11bf3418b.sketch_text.stroke-90"),sQuery(id+"F2.wireOp",EDGE,"fcba4419-a2ee-464f-be9d-58f11bf3418b.sketch_text.stroke-91"),sQuery(id+"F2.wireOp",EDGE,"fcba4419-a2ee-464f-be9d-58f11bf3418b.sketch_text.stroke-92"),sQuery(id+"F2.wireOp",EDGE,"fcba4419-a2ee-464f-be9d-58f11bf3418b.sketch_text.stroke-93"),sQuery(id+"F2.wireOp",EDGE,"fcba4419-a2ee-464f-be9d-58f11bf3418b.sketch_text.stroke-94"),sQuery(id+"F2.wireOp",EDGE,"fcba4419-a2ee-464f-be9d-58f11bf3418b.sketch_text.stroke-95"),sQuery(id+"F2.wireOp",EDGE,"fcba4419-a2ee-464f-be9d-58f11bf3418b.sketch_text.stroke-96"),sQuery(id+"F2.wireOp",EDGE,"fcba4419-a2ee-464f-be9d-58f11bf3418b.sketch_text.stroke-97"),sQuery(id+"F2.wireOp",EDGE,"fcba4419-a2ee-464f-be9d-58f11bf3418b.sketch_text.stroke-98"),sQuery(id+"F2.wireOp",EDGE,"fcba4419-a2ee-464f-be9d-58f11bf3418b.sketch_text.stroke-99"),sQuery(id+"F2.wireOp",EDGE,"fcba4419-a2ee-464f-be9d-58f11bf3418b.sketch_text.stroke-100"),sQuery(id+"F2.wireOp",EDGE,"fcba4419-a2ee-464f-be9d-58f11bf3418b.sketch_text.stroke-101"),sQuery(id+"F2.wireOp",EDGE,"fcba4419-a2ee-464f-be9d-58f11bf3418b.sketch_text.stroke-102"),sQuery(id+"F2.wireOp",EDGE,"fcba4419-a2ee-464f-be9d-58f11bf3418b.sketch_text.stroke-103"),sQuery(id+"F2.wireOp",EDGE,"fcba4419-a2ee-464f-be9d-58f11bf3418b.sketch_text.stroke-104"),sQuery(id+"F2.wireOp",EDGE,"fcba4419-a2ee-464f-be9d-58f11bf3418b.sketch_text.stroke-105"),sQuery(id+"F2.wireOp",EDGE,"fcba4419-a2ee-464f-be9d-58f11bf3418b.sketch_text.stroke-106"),sQuery(id+"F2.wireOp",EDGE,"fcba4419-a2ee-464f-be9d-58f11bf3418b.sketch_text.stroke-107"),sQuery(id+"F2.wireOp",EDGE,"fcba4419-a2ee-464f-be9d-58f11bf3418b.sketch_text.stroke-108"),sQuery(id+"F2.wireOp",EDGE,"fcba4419-a2ee-464f-be9d-58f11bf3418b.sketch_text.stroke-109"),sQuery(id+"F2.wireOp",EDGE,"fcba4419-a2ee-464f-be9d-58f11bf3418b.sketch_text.stroke-110"),sQuery(id+"F2.wireOp",EDGE,"fcba4419-a2ee-464f-be9d-58f11bf3418b.sketch_text.stroke-111"),sQuery(id+"F2.wireOp",EDGE,"fcba4419-a2ee-464f-be9d-58f11bf3418b.sketch_text.stroke-112"),sQuery(id+"F2.wireOp",EDGE,"fcba4419-a2ee-464f-be9d-58f11bf3418b.sketch_text.stroke-113"),sQuery(id+"F2.wireOp",EDGE,"fcba4419-a2ee-464f-be9d-58f11bf3418b.sketch_text.stroke-114"),sQuery(id+"F2.wireOp",EDGE,"fcba4419-a2ee-464f-be9d-58f11bf3418b.sketch_text.stroke-115"),sQuery(id+"F2.wireOp",EDGE,"fcba4419-a2ee-464f-be9d-58f11bf3418b.sketch_text.stroke-116"),sQuery(id+"F2.wireOp",EDGE,"fcba4419-a2ee-464f-be9d-58f11bf3418b.sketch_text.stroke-117"),sQuery(id+"F2.wireOp",EDGE,"fcba4419-a2ee-464f-be9d-58f11bf3418b.sketch_text.stroke-118"),sQuery(id+"F2.wireOp",EDGE,"fcba4419-a2ee-464f-be9d-58f11bf3418b.sketch_text.stroke-119"),sQuery(id+"F2.wireOp",EDGE,"fcba4419-a2ee-464f-be9d-58f11bf3418b.sketch_text.stroke-120"),sQuery(id+"F2.wireOp",EDGE,"fcba4419-a2ee-464f-be9d-58f11bf3418b.sketch_text.stroke-121"),sQuery(id+"F2.wireOp",EDGE,"fcba4419-a2ee-464f-be9d-58f11bf3418b.sketch_text.stroke-122"),sQuery(id+"F2.wireOp",EDGE,"fcba4419-a2ee-464f-be9d-58f11bf3418b.sketch_text.stroke-123"),sQuery(id+"F2.wireOp",EDGE,"fcba4419-a2ee-464f-be9d-58f11bf3418b.sketch_text.stroke-124"),sQuery(id+"F2.wireOp",EDGE,"fcba4419-a2ee-464f-be9d-58f11bf3418b.sketch_text.stroke-125"),sQuery(id+"F2.wireOp",EDGE,"fcba4419-a2ee-464f-be9d-58f11bf3418b.sketch_text.stroke-126"),sQuery(id+"F2.wireOp",EDGE,"fcba4419-a2ee-464f-be9d-58f11bf3418b.sketch_text.stroke-127"),sQuery(id+"F2.wireOp",EDGE,"fcba4419-a2ee-464f-be9d-58f11bf3418b.sketch_text.stroke-128"),sQuery(id+"F2.wireOp",EDGE,"fcba4419-a2ee-464f-be9d-58f11bf3418b.sketch_text.stroke-129"),sQuery(id+"F2.wireOp",EDGE,"fcba4419-a2ee-464f-be9d-58f11bf3418b.sketch_text.stroke-130"),sQuery(id+"F2.wireOp",EDGE,"fcba4419-a2ee-464f-be9d-58f11bf3418b.sketch_text.stroke-131"),sQuery(id+"F2.wireOp",EDGE,"fcba4419-a2ee-464f-be9d-58f11bf3418b.sketch_text.stroke-132"),sQuery(id+"F2.wireOp",EDGE,"fcba4419-a2ee-464f-be9d-58f11bf3418b.sketch_text.stroke-133"),sQuery(id+"F2.wireOp",EDGE,"fcba4419-a2ee-464f-be9d-58f11bf3418b.sketch_text.stroke-134"),sQuery(id+"F2.wireOp",EDGE,"fcba4419-a2ee-464f-be9d-58f11bf3418b.sketch_text.stroke-135"),sQuery(id+"F2.wireOp",EDGE,"fcba4419-a2ee-464f-be9d-58f11bf3418b.sketch_text.stroke-136"),sQuery(id+"F2.wireOp",EDGE,"fcba4419-a2ee-464f-be9d-58f11bf3418b.sketch_text.stroke-137"),sQuery(id+"F2.wireOp",EDGE,"fcba4419-a2ee-464f-be9d-58f11bf3418b.sketch_text.stroke-138"),sQuery(id+"F2.wireOp",EDGE,"fcba4419-a2ee-464f-be9d-58f11bf3418b.sketch_text.stroke-139"),sQuery(id+"F2.wireOp",EDGE,"fcba4419-a2ee-464f-be9d-58f11bf3418b.sketch_text.stroke-140"),sQuery(id+"F2.wireOp",EDGE,"fcba4419-a2ee-464f-be9d-58f11bf3418b.sketch_text.stroke-141"),sQuery(id+"F2.wireOp",EDGE,"fcba4419-a2ee-464f-be9d-58f11bf3418b.sketch_text.stroke-142"),sQuery(id+"F2.wireOp",EDGE,"fcba4419-a2ee-464f-be9d-58f11bf3418b.sketch_text.stroke-143"),sQuery(id+"F2.wireOp",EDGE,"fcba4419-a2ee-464f-be9d-58f11bf3418b.sketch_text.stroke-144"),sQuery(id+"F2.wireOp",EDGE,"fcba4419-a2ee-464f-be9d-58f11bf3418b.sketch_text.stroke-145"),sQuery(id+"F2.wireOp",EDGE,"fcba4419-a2ee-464f-be9d-58f11bf3418b.sketch_text.stroke-146"),sQuery(id+"F2.wireOp",EDGE,"fcba4419-a2ee-464f-be9d-58f11bf3418b.sketch_text.stroke-147"),sQuery(id+"F2.wireOp",EDGE,"fcba4419-a2ee-464f-be9d-58f11bf3418b.sketch_text.stroke-148"),sQuery(id+"F2.wireOp",EDGE,"fcba4419-a2ee-464f-be9d-58f11bf3418b.sketch_text.stroke-149"),sQuery(id+"F2.wireOp",EDGE,"fcba4419-a2ee-464f-be9d-58f11bf3418b.sketch_text.stroke-150"),sQuery(id+"F2.wireOp",EDGE,"fcba4419-a2ee-464f-be9d-58f11bf3418b.sketch_text.stroke-151"),sQuery(id+"F2.wireOp",EDGE,"fcba4419-a2ee-464f-be9d-58f11bf3418b.sketch_text.stroke-152"),sQuery(id+"F2.wireOp",EDGE,"fcba4419-a2ee-464f-be9d-58f11bf3418b.sketch_text.stroke-153"),sQuery(id+"F2.wireOp",EDGE,"fcba4419-a2ee-464f-be9d-58f11bf3418b.sketch_text.stroke-154"),sQuery(id+"F2.wireOp",EDGE,"fcba4419-a2ee-464f-be9d-58f11bf3418b.sketch_text.stroke-155"),sQuery(id+"F2.wireOp",EDGE,"fcba4419-a2ee-464f-be9d-58f11bf3418b.sketch_text.stroke-156"),sQuery(id+"F2.wireOp",EDGE,"fcba4419-a2ee-464f-be9d-58f11bf3418b.sketch_text.stroke-157"),sQuery(id+"F2.wireOp",EDGE,"fcba4419-a2ee-464f-be9d-58f11bf3418b.sketch_text.stroke-158"),sQuery(id+"F2.wireOp",EDGE,"fcba4419-a2ee-464f-be9d-58f11bf3418b.sketch_text.stroke-159"),sQuery(id+"F2.wireOp",EDGE,"fcba4419-a2ee-464f-be9d-58f11bf3418b.sketch_text.stroke-160"),sQuery(id+"F2.wireOp",EDGE,"fcba4419-a2ee-464f-be9d-58f11bf3418b.sketch_text.stroke-161"),sQuery(id+"F2.wireOp",EDGE,"fcba4419-a2ee-464f-be9d-58f11bf3418b.sketch_text.stroke-162"),sQuery(id+"F2.wireOp",EDGE,"fcba4419-a2ee-464f-be9d-58f11bf3418b.sketch_text.stroke-163"),sQuery(id+"F2.wireOp",EDGE,"fcba4419-a2ee-464f-be9d-58f11bf3418b.sketch_text.stroke-164"),sQuery(id+"F2.wireOp",EDGE,"fcba4419-a2ee-464f-be9d-58f11bf3418b.sketch_text.stroke-165"),sQuery(id+"F2.wireOp",EDGE,"fcba4419-a2ee-464f-be9d-58f11bf3418b.sketch_text.stroke-166"),sQuery(id+"F2.wireOp",EDGE,"fcba4419-a2ee-464f-be9d-58f11bf3418b.sketch_text.stroke-167"),sQuery(id+"F2.wireOp",EDGE,"fcba4419-a2ee-464f-be9d-58f11bf3418b.sketch_text.stroke-168"),sQuery(id+"F2.wireOp",EDGE,"fcba4419-a2ee-464f-be9d-58f11bf3418b.sketch_text.stroke-169"),sQuery(id+"F2.wireOp",EDGE,"fcba4419-a2ee-464f-be9d-58f11bf3418b.sketch_text.stroke-170"),sQuery(id+"F2.wireOp",EDGE,"fcba4419-a2ee-464f-be9d-58f11bf3418b.sketch_text.stroke-171"),sQuery(id+"F2.wireOp",EDGE,"fcba4419-a2ee-464f-be9d-58f11bf3418b.sketch_text.stroke-172"),sQuery(id+"F2.wireOp",EDGE,"fcba4419-a2ee-464f-be9d-58f11bf3418b.sketch_text.stroke-173"),sQuery(id+"FHMxAyK4CFUKdhS_1.wireOp",EDGE,"1cb9c079-ea9b-4899-8069-e0e3048e911d.sketch_text.stroke-0"),sQuery(id+"FHMxAyK4CFUKdhS_1.wireOp",EDGE,"1cb9c079-ea9b-4899-8069-e0e3048e911d.sketch_text.stroke-1"),sQuery(id+"FHMxAyK4CFUKdhS_1.wireOp",EDGE,"1cb9c079-ea9b-4899-8069-e0e3048e911d.sketch_text.stroke-2"),sQuery(id+"FHMxAyK4CFUKdhS_1.wireOp",EDGE,"1cb9c079-ea9b-4899-8069-e0e3048e911d.sketch_text.stroke-3"),sQuery(id+"FHMxAyK4CFUKdhS_1.wireOp",EDGE,"1cb9c079-ea9b-4899-8069-e0e3048e911d.sketch_text.stroke-4"),sQuery(id+"FHMxAyK4CFUKdhS_1.wireOp",EDGE,"1cb9c079-ea9b-4899-8069-e0e3048e911d.sketch_text.stroke-5"),sQuery(id+"FHMxAyK4CFUKdhS_1.wireOp",EDGE,"1cb9c079-ea9b-4899-8069-e0e3048e911d.sketch_text.stroke-6"),sQuery(id+"FHMxAyK4CFUKdhS_1.wireOp",EDGE,"1cb9c079-ea9b-4899-8069-e0e3048e911d.sketch_text.stroke-7"),sQuery(id+"FHMxAyK4CFUKdhS_1.wireOp",EDGE,"1cb9c079-ea9b-4899-8069-e0e3048e911d.sketch_text.stroke-8"),sQuery(id+"FHMxAyK4CFUKdhS_1.wireOp",EDGE,"1cb9c079-ea9b-4899-8069-e0e3048e911d.sketch_text.stroke-9"),sQuery(id+"FHMxAyK4CFUKdhS_1.wireOp",EDGE,"1cb9c079-ea9b-4899-8069-e0e3048e911d.sketch_text.stroke-10"),sQuery(id+"FHMxAyK4CFUKdhS_1.wireOp",EDGE,"1cb9c079-ea9b-4899-8069-e0e3048e911d.sketch_text.stroke-11"),sQuery(id+"FHMxAyK4CFUKdhS_1.wireOp",EDGE,"1cb9c079-ea9b-4899-8069-e0e3048e911d.sketch_text.stroke-12"),sQuery(id+"FHMxAyK4CFUKdhS_1.wireOp",EDGE,"1cb9c079-ea9b-4899-8069-e0e3048e911d.sketch_text.stroke-13"),sQuery(id+"FHMxAyK4CFUKdhS_1.wireOp",EDGE,"1cb9c079-ea9b-4899-8069-e0e3048e911d.sketch_text.stroke-14"),sQuery(id+"FHMxAyK4CFUKdhS_1.wireOp",EDGE,"1cb9c079-ea9b-4899-8069-e0e3048e911d.sketch_text.stroke-15"),sQuery(id+"FHMxAyK4CFUKdhS_1.wireOp",EDGE,"1cb9c079-ea9b-4899-8069-e0e3048e911d.sketch_text.stroke-16"),sQuery(id+"FHMxAyK4CFUKdhS_1.wireOp",EDGE,"1cb9c079-ea9b-4899-8069-e0e3048e911d.sketch_text.stroke-17"),sQuery(id+"FHMxAyK4CFUKdhS_1.wireOp",EDGE,"1cb9c079-ea9b-4899-8069-e0e3048e911d.sketch_text.stroke-18"),sQuery(id+"FHMxAyK4CFUKdhS_1.wireOp",EDGE,"1cb9c079-ea9b-4899-8069-e0e3048e911d.sketch_text.stroke-19"),sQuery(id+"FHMxAyK4CFUKdhS_1.wireOp",EDGE,"1cb9c079-ea9b-4899-8069-e0e3048e911d.sketch_text.stroke-20"),sQuery(id+"FHMxAyK4CFUKdhS_1.wireOp",EDGE,"1cb9c079-ea9b-4899-8069-e0e3048e911d.sketch_text.stroke-21"),sQuery(id+"FHMxAyK4CFUKdhS_1.wireOp",EDGE,"1cb9c079-ea9b-4899-8069-e0e3048e911d.sketch_text.stroke-22"),sQuery(id+"FHMxAyK4CFUKdhS_1.wireOp",EDGE,"1cb9c079-ea9b-4899-8069-e0e3048e911d.sketch_text.stroke-23"),sQuery(id+"FHMxAyK4CFUKdhS_1.wireOp",EDGE,"1cb9c079-ea9b-4899-8069-e0e3048e911d.sketch_text.stroke-24"),sQuery(id+"FHMxAyK4CFUKdhS_1.wireOp",EDGE,"1cb9c079-ea9b-4899-8069-e0e3048e911d.sketch_text.stroke-25"),sQuery(id+"FHMxAyK4CFUKdhS_1.wireOp",EDGE,"1cb9c079-ea9b-4899-8069-e0e3048e911d.sketch_text.stroke-26"),sQuery(id+"FHMxAyK4CFUKdhS_1.wireOp",EDGE,"1cb9c079-ea9b-4899-8069-e0e3048e911d.sketch_text.stroke-27"),sQuery(id+"FHMxAyK4CFUKdhS_1.wireOp",EDGE,"1cb9c079-ea9b-4899-8069-e0e3048e911d.sketch_text.stroke-28"),sQuery(id+"FHMxAyK4CFUKdhS_1.wireOp",EDGE,"1cb9c079-ea9b-4899-8069-e0e3048e911d.sketch_text.stroke-29"),sQuery(id+"FHMxAyK4CFUKdhS_1.wireOp",EDGE,"1cb9c079-ea9b-4899-8069-e0e3048e911d.sketch_text.stroke-30"),sQuery(id+"FHMxAyK4CFUKdhS_1.wireOp",EDGE,"1cb9c079-ea9b-4899-8069-e0e3048e911d.sketch_text.stroke-31"),sQuery(id+"FHMxAyK4CFUKdhS_1.wireOp",EDGE,"1cb9c079-ea9b-4899-8069-e0e3048e911d.sketch_text.stroke-32"),sQuery(id+"FHMxAyK4CFUKdhS_1.wireOp",EDGE,"1cb9c079-ea9b-4899-8069-e0e3048e911d.sketch_text.stroke-33"),sQuery(id+"FHMxAyK4CFUKdhS_1.wireOp",EDGE,"1cb9c079-ea9b-4899-8069-e0e3048e911d.sketch_text.stroke-34"),sQuery(id+"FHMxAyK4CFUKdhS_1.wireOp",EDGE,"1cb9c079-ea9b-4899-8069-e0e3048e911d.sketch_text.stroke-35"),sQuery(id+"FHMxAyK4CFUKdhS_1.wireOp",EDGE,"1cb9c079-ea9b-4899-8069-e0e3048e911d.sketch_text.stroke-36"),sQuery(id+"FHMxAyK4CFUKdhS_1.wireOp",EDGE,"1cb9c079-ea9b-4899-8069-e0e3048e911d.sketch_text.stroke-37"),sQuery(id+"FHMxAyK4CFUKdhS_1.wireOp",EDGE,"1cb9c079-ea9b-4899-8069-e0e3048e911d.sketch_text.stroke-38"),sQuery(id+"FHMxAyK4CFUKdhS_1.wireOp",EDGE,"1cb9c079-ea9b-4899-8069-e0e3048e911d.sketch_text.stroke-39"),sQuery(id+"FHMxAyK4CFUKdhS_1.wireOp",EDGE,"1cb9c079-ea9b-4899-8069-e0e3048e911d.sketch_text.stroke-40"),sQuery(id+"FHMxAyK4CFUKdhS_1.wireOp",EDGE,"1cb9c079-ea9b-4899-8069-e0e3048e911d.sketch_text.stroke-41"),sQuery(id+"FHMxAyK4CFUKdhS_1.wireOp",EDGE,"1cb9c079-ea9b-4899-8069-e0e3048e911d.sketch_text.stroke-42"),sQuery(id+"FHMxAyK4CFUKdhS_1.wireOp",EDGE,"1cb9c079-ea9b-4899-8069-e0e3048e911d.sketch_text.stroke-43"),sQuery(id+"FHMxAyK4CFUKdhS_1.wireOp",EDGE,"1cb9c079-ea9b-4899-8069-e0e3048e911d.sketch_text.stroke-44"),sQuery(id+"FHMxAyK4CFUKdhS_1.wireOp",EDGE,"1cb9c079-ea9b-4899-8069-e0e3048e911d.sketch_text.stroke-45"),sQuery(id+"FHMxAyK4CFUKdhS_1.wireOp",EDGE,"1cb9c079-ea9b-4899-8069-e0e3048e911d.sketch_text.stroke-46"),sQuery(id+"FHMxAyK4CFUKdhS_1.wireOp",EDGE,"1cb9c079-ea9b-4899-8069-e0e3048e911d.sketch_text.stroke-47"),sQuery(id+"FHMxAyK4CFUKdhS_1.wireOp",EDGE,"1cb9c079-ea9b-4899-8069-e0e3048e911d.sketch_text.stroke-48"),sQuery(id+"FHMxAyK4CFUKdhS_1.wireOp",EDGE,"1cb9c079-ea9b-4899-8069-e0e3048e911d.sketch_text.stroke-49"),sQuery(id+"FHMxAyK4CFUKdhS_1.wireOp",EDGE,"1cb9c079-ea9b-4899-8069-e0e3048e911d.sketch_text.stroke-50"),sQuery(id+"FHMxAyK4CFUKdhS_1.wireOp",EDGE,"1cb9c079-ea9b-4899-8069-e0e3048e911d.sketch_text.stroke-51"),sQuery(id+"FHMxAyK4CFUKdhS_1.wireOp",EDGE,"1cb9c079-ea9b-4899-8069-e0e3048e911d.sketch_text.stroke-52"),sQuery(id+"FHMxAyK4CFUKdhS_1.wireOp",EDGE,"1cb9c079-ea9b-4899-8069-e0e3048e911d.sketch_text.stroke-53"),sQuery(id+"FHMxAyK4CFUKdhS_1.wireOp",EDGE,"1cb9c079-ea9b-4899-8069-e0e3048e911d.sketch_text.stroke-54"),sQuery(id+"FHMxAyK4CFUKdhS_1.wireOp",EDGE,"1cb9c079-ea9b-4899-8069-e0e3048e911d.sketch_text.stroke-55"),sQuery(id+"FHMxAyK4CFUKdhS_1.wireOp",EDGE,"1cb9c079-ea9b-4899-8069-e0e3048e911d.sketch_text.stroke-56"),sQuery(id+"FHMxAyK4CFUKdhS_1.wireOp",EDGE,"1cb9c079-ea9b-4899-8069-e0e3048e911d.sketch_text.stroke-57"),sQuery(id+"FHMxAyK4CFUKdhS_1.wireOp",EDGE,"1cb9c079-ea9b-4899-8069-e0e3048e911d.sketch_text.stroke-58"),sQuery(id+"FHMxAyK4CFUKdhS_1.wireOp",EDGE,"1cb9c079-ea9b-4899-8069-e0e3048e911d.sketch_text.stroke-59"),sQuery(id+"FHMxAyK4CFUKdhS_1.wireOp",EDGE,"1cb9c079-ea9b-4899-8069-e0e3048e911d.sketch_text.stroke-60"),sQuery(id+"FHMxAyK4CFUKdhS_1.wireOp",EDGE,"1cb9c079-ea9b-4899-8069-e0e3048e911d.sketch_text.stroke-61"),sQuery(id+"FHMxAyK4CFUKdhS_1.wireOp",EDGE,"1cb9c079-ea9b-4899-8069-e0e3048e911d.sketch_text.stroke-62"),sQuery(id+"FHMxAyK4CFUKdhS_1.wireOp",EDGE,"1cb9c079-ea9b-4899-8069-e0e3048e911d.sketch_text.stroke-71"),sQuery(id+"FHMxAyK4CFUKdhS_1.wireOp",EDGE,"1cb9c079-ea9b-4899-8069-e0e3048e911d.sketch_text.stroke-72"),sQuery(id+"FHMxAyK4CFUKdhS_1.wireOp",EDGE,"1cb9c079-ea9b-4899-8069-e0e3048e911d.sketch_text.stroke-73"),sQuery(id+"FHMxAyK4CFUKdhS_1.wireOp",EDGE,"1cb9c079-ea9b-4899-8069-e0e3048e911d.sketch_text.stroke-74"),sQuery(id+"FHMxAyK4CFUKdhS_1.wireOp",EDGE,"1cb9c079-ea9b-4899-8069-e0e3048e911d.sketch_text.stroke-75"),sQuery(id+"FHMxAyK4CFUKdhS_1.wireOp",EDGE,"1cb9c079-ea9b-4899-8069-e0e3048e911d.sketch_text.stroke-76"),sQuery(id+"FHMxAyK4CFUKdhS_1.wireOp",EDGE,"1cb9c079-ea9b-4899-8069-e0e3048e911d.sketch_text.stroke-77"),sQuery(id+"FHMxAyK4CFUKdhS_1.wireOp",EDGE,"1cb9c079-ea9b-4899-8069-e0e3048e911d.sketch_text.stroke-78"),sQuery(id+"FHMxAyK4CFUKdhS_1.wireOp",EDGE,"1cb9c079-ea9b-4899-8069-e0e3048e911d.sketch_text.stroke-79"),sQuery(id+"FHMxAyK4CFUKdhS_1.wireOp",EDGE,"1cb9c079-ea9b-4899-8069-e0e3048e911d.sketch_text.stroke-80"),sQuery(id+"FHMxAyK4CFUKdhS_1.wireOp",EDGE,"1cb9c079-ea9b-4899-8069-e0e3048e911d.sketch_text.stroke-81"),sQuery(id+"FHMxAyK4CFUKdhS_1.wireOp",EDGE,"1cb9c079-ea9b-4899-8069-e0e3048e911d.sketch_text.stroke-82"),sQuery(id+"FHMxAyK4CFUKdhS_1.wireOp",EDGE,"1cb9c079-ea9b-4899-8069-e0e3048e911d.sketch_text.stroke-83"),sQuery(id+"FHMxAyK4CFUKdhS_1.wireOp",EDGE,"1cb9c079-ea9b-4899-8069-e0e3048e911d.sketch_text.stroke-84"),sQuery(id+"FHMxAyK4CFUKdhS_1.wireOp",EDGE,"1cb9c079-ea9b-4899-8069-e0e3048e911d.sketch_text.stroke-85"),sQuery(id+"FHMxAyK4CFUKdhS_1.wireOp",EDGE,"1cb9c079-ea9b-4899-8069-e0e3048e911d.sketch_text.stroke-86"),sQuery(id+"FHMxAyK4CFUKdhS_1.wireOp",EDGE,"1cb9c079-ea9b-4899-8069-e0e3048e911d.sketch_text.stroke-87"),sQuery(id+"FHMxAyK4CFUKdhS_1.wireOp",EDGE,"1cb9c079-ea9b-4899-8069-e0e3048e911d.sketch_text.stroke-88"),sQuery(id+"FHMxAyK4CFUKdhS_1.wireOp",EDGE,"1cb9c079-ea9b-4899-8069-e0e3048e911d.sketch_text.stroke-89"),sQuery(id+"FHMxAyK4CFUKdhS_1.wireOp",EDGE,"1cb9c079-ea9b-4899-8069-e0e3048e911d.sketch_text.stroke-90"),sQuery(id+"FHMxAyK4CFUKdhS_1.wireOp",EDGE,"1cb9c079-ea9b-4899-8069-e0e3048e911d.sketch_text.stroke-91"),sQuery(id+"FHMxAyK4CFUKdhS_1.wireOp",EDGE,"1cb9c079-ea9b-4899-8069-e0e3048e911d.sketch_text.stroke-92"),sQuery(id+"FHMxAyK4CFUKdhS_1.wireOp",EDGE,"1cb9c079-ea9b-4899-8069-e0e3048e911d.sketch_text.stroke-93"),sQuery(id+"FHMxAyK4CFUKdhS_1.wireOp",EDGE,"1cb9c079-ea9b-4899-8069-e0e3048e911d.sketch_text.stroke-94"),sQuery(id+"FHMxAyK4CFUKdhS_1.wireOp",EDGE,"1cb9c079-ea9b-4899-8069-e0e3048e911d.sketch_text.stroke-95"),sQuery(id+"FHMxAyK4CFUKdhS_1.wireOp",EDGE,"1cb9c079-ea9b-4899-8069-e0e3048e911d.sketch_text.stroke-96"),sQuery(id+"FHMxAyK4CFUKdhS_1.wireOp",EDGE,"1cb9c079-ea9b-4899-8069-e0e3048e911d.sketch_text.stroke-97"),sQuery(id+"FHMxAyK4CFUKdhS_1.wireOp",EDGE,"1cb9c079-ea9b-4899-8069-e0e3048e911d.sketch_text.stroke-103"),sQuery(id+"FHMxAyK4CFUKdhS_1.wireOp",EDGE,"1cb9c079-ea9b-4899-8069-e0e3048e911d.sketch_text.stroke-104"),sQuery(id+"FHMxAyK4CFUKdhS_1.wireOp",EDGE,"1cb9c079-ea9b-4899-8069-e0e3048e911d.sketch_text.stroke-105"),sQuery(id+"FHMxAyK4CFUKdhS_1.wireOp",EDGE,"1cb9c079-ea9b-4899-8069-e0e3048e911d.sketch_text.stroke-106"),sQuery(id+"FHMxAyK4CFUKdhS_1.wireOp",EDGE,"1cb9c079-ea9b-4899-8069-e0e3048e911d.sketch_text.stroke-107"),sQuery(id+"FHMxAyK4CFUKdhS_1.wireOp",EDGE,"1cb9c079-ea9b-4899-8069-e0e3048e911d.sketch_text.stroke-108"),sQuery(id+"FHMxAyK4CFUKdhS_1.wireOp",EDGE,"1cb9c079-ea9b-4899-8069-e0e3048e911d.sketch_text.stroke-109"),sQuery(id+"FHMxAyK4CFUKdhS_1.wireOp",EDGE,"1cb9c079-ea9b-4899-8069-e0e3048e911d.sketch_text.stroke-110"),sQuery(id+"FHMxAyK4CFUKdhS_1.wireOp",EDGE,"1cb9c079-ea9b-4899-8069-e0e3048e911d.sketch_text.stroke-111"),sQuery(id+"FHMxAyK4CFUKdhS_1.wireOp",EDGE,"1cb9c079-ea9b-4899-8069-e0e3048e911d.sketch_text.stroke-112"),sQuery(id+"FHMxAyK4CFUKdhS_1.wireOp",EDGE,"1cb9c079-ea9b-4899-8069-e0e3048e911d.sketch_text.stroke-113"),sQuery(id+"FHMxAyK4CFUKdhS_1.wireOp",EDGE,"1cb9c079-ea9b-4899-8069-e0e3048e911d.sketch_text.stroke-114"),sQuery(id+"FHMxAyK4CFUKdhS_1.wireOp",EDGE,"1cb9c079-ea9b-4899-8069-e0e3048e911d.sketch_text.stroke-115"),sQuery(id+"FHMxAyK4CFUKdhS_1.wireOp",EDGE,"1cb9c079-ea9b-4899-8069-e0e3048e911d.sketch_text.stroke-116"),sQuery(id+"FHMxAyK4CFUKdhS_1.wireOp",EDGE,"1cb9c079-ea9b-4899-8069-e0e3048e911d.sketch_text.stroke-117"),sQuery(id+"FHMxAyK4CFUKdhS_1.wireOp",EDGE,"1cb9c079-ea9b-4899-8069-e0e3048e911d.sketch_text.stroke-118"),sQuery(id+"FHMxAyK4CFUKdhS_1.wireOp",EDGE,"1cb9c079-ea9b-4899-8069-e0e3048e911d.sketch_text.stroke-119"),sQuery(id+"FHMxAyK4CFUKdhS_1.wireOp",EDGE,"1cb9c079-ea9b-4899-8069-e0e3048e911d.sketch_text.stroke-120"),sQuery(id+"FHMxAyK4CFUKdhS_1.wireOp",EDGE,"1cb9c079-ea9b-4899-8069-e0e3048e911d.sketch_text.stroke-121"),sQuery(id+"FHMxAyK4CFUKdhS_1.wireOp",EDGE,"1cb9c079-ea9b-4899-8069-e0e3048e911d.sketch_text.stroke-122"),sQuery(id+"FHMxAyK4CFUKdhS_1.wireOp",EDGE,"1cb9c079-ea9b-4899-8069-e0e3048e911d.sketch_text.stroke-123"),sQuery(id+"FHMxAyK4CFUKdhS_1.wireOp",EDGE,"1cb9c079-ea9b-4899-8069-e0e3048e911d.sketch_text.stroke-124"),sQuery(id+"FHMxAyK4CFUKdhS_1.wireOp",EDGE,"1cb9c079-ea9b-4899-8069-e0e3048e911d.sketch_text.stroke-125"),sQuery(id+"FHMxAyK4CFUKdhS_1.wireOp",EDGE,"1cb9c079-ea9b-4899-8069-e0e3048e911d.sketch_text.stroke-126"),sQuery(id+"FHMxAyK4CFUKdhS_1.wireOp",EDGE,"1cb9c079-ea9b-4899-8069-e0e3048e911d.sketch_text.stroke-127"),sQuery(id+"FHMxAyK4CFUKdhS_1.wireOp",EDGE,"1cb9c079-ea9b-4899-8069-e0e3048e911d.sketch_text.stroke-128"),sQuery(id+"FHMxAyK4CFUKdhS_1.wireOp",EDGE,"1cb9c079-ea9b-4899-8069-e0e3048e911d.sketch_text.stroke-129"),sQuery(id+"FHMxAyK4CFUKdhS_1.wireOp",EDGE,"1cb9c079-ea9b-4899-8069-e0e3048e911d.sketch_text.stroke-130"),sQuery(id+"FHMxAyK4CFUKdhS_1.wireOp",EDGE,"1cb9c079-ea9b-4899-8069-e0e3048e911d.sketch_text.stroke-131"),sQuery(id+"FHMxAyK4CFUKdhS_1.wireOp",EDGE,"1cb9c079-ea9b-4899-8069-e0e3048e911d.sketch_text.stroke-132"),sQuery(id+"FHMxAyK4CFUKdhS_1.wireOp",EDGE,"1cb9c079-ea9b-4899-8069-e0e3048e911d.sketch_text.stroke-133"),sQuery(id+"FHMxAyK4CFUKdhS_1.wireOp",EDGE,"1cb9c079-ea9b-4899-8069-e0e3048e911d.sketch_text.stroke-134"),sQuery(id+"FHMxAyK4CFUKdhS_1.wireOp",EDGE,"1cb9c079-ea9b-4899-8069-e0e3048e911d.sketch_text.stroke-135"),sQuery(id+"FHMxAyK4CFUKdhS_1.wireOp",EDGE,"1cb9c079-ea9b-4899-8069-e0e3048e911d.sketch_text.stroke-136"),sQuery(id+"FHMxAyK4CFUKdhS_1.wireOp",EDGE,"1cb9c079-ea9b-4899-8069-e0e3048e911d.sketch_text.stroke-137"),sQuery(id+"FHMxAyK4CFUKdhS_1.wireOp",EDGE,"1cb9c079-ea9b-4899-8069-e0e3048e911d.sketch_text.stroke-138"),sQuery(id+"FHMxAyK4CFUKdhS_1.wireOp",EDGE,"1cb9c079-ea9b-4899-8069-e0e3048e911d.sketch_text.stroke-139"),sQuery(id+"FHMxAyK4CFUKdhS_1.wireOp",EDGE,"1cb9c079-ea9b-4899-8069-e0e3048e911d.sketch_text.stroke-140"),sQuery(id+"FHMxAyK4CFUKdhS_1.wireOp",EDGE,"1cb9c079-ea9b-4899-8069-e0e3048e911d.sketch_text.stroke-141"),sQuery(id+"FHMxAyK4CFUKdhS_1.wireOp",EDGE,"1cb9c079-ea9b-4899-8069-e0e3048e911d.sketch_text.stroke-142"),sQuery(id+"FHMxAyK4CFUKdhS_1.wireOp",EDGE,"1cb9c079-ea9b-4899-8069-e0e3048e911d.sketch_text.stroke-143"),sQuery(id+"FHMxAyK4CFUKdhS_1.wireOp",EDGE,"1cb9c079-ea9b-4899-8069-e0e3048e911d.sketch_text.stroke-144"),sQuery(id+"FHMxAyK4CFUKdhS_1.wireOp",EDGE,"1cb9c079-ea9b-4899-8069-e0e3048e911d.sketch_text.stroke-145"),sQuery(id+"FHMxAyK4CFUKdhS_1.wireOp",EDGE,"1cb9c079-ea9b-4899-8069-e0e3048e911d.sketch_text.stroke-146"),sQuery(id+"FHMxAyK4CFUKdhS_1.wireOp",EDGE,"1cb9c079-ea9b-4899-8069-e0e3048e911d.sketch_text.stroke-147"),sQuery(id+"FHMxAyK4CFUKdhS_1.wireOp",EDGE,"1cb9c079-ea9b-4899-8069-e0e3048e911d.sketch_text.stroke-148"),sQuery(id+"FHMxAyK4CFUKdhS_1.wireOp",EDGE,"1cb9c079-ea9b-4899-8069-e0e3048e911d.sketch_text.stroke-149"),sQuery(id+"FHMxAyK4CFUKdhS_1.wireOp",EDGE,"1cb9c079-ea9b-4899-8069-e0e3048e911d.sketch_text.stroke-150"),sQuery(id+"FHMxAyK4CFUKdhS_1.wireOp",EDGE,"1cb9c079-ea9b-4899-8069-e0e3048e911d.sketch_text.stroke-151"),sQuery(id+"FHMxAyK4CFUKdhS_1.wireOp",EDGE,"1cb9c079-ea9b-4899-8069-e0e3048e911d.sketch_text.stroke-152"),sQuery(id+"FHMxAyK4CFUKdhS_1.wireOp",EDGE,"1cb9c079-ea9b-4899-8069-e0e3048e911d.sketch_text.stroke-153"),sQuery(id+"FHMxAyK4CFUKdhS_1.wireOp",EDGE,"1cb9c079-ea9b-4899-8069-e0e3048e911d.sketch_text.stroke-159"),sQuery(id+"FHMxAyK4CFUKdhS_1.wireOp",EDGE,"1cb9c079-ea9b-4899-8069-e0e3048e911d.sketch_text.stroke-160"),sQuery(id+"FHMxAyK4CFUKdhS_1.wireOp",EDGE,"1cb9c079-ea9b-4899-8069-e0e3048e911d.sketch_text.stroke-161"),sQuery(id+"FHMxAyK4CFUKdhS_1.wireOp",EDGE,"1cb9c079-ea9b-4899-8069-e0e3048e911d.sketch_text.stroke-162"),sQuery(id+"FHMxAyK4CFUKdhS_1.wireOp",EDGE,"1cb9c079-ea9b-4899-8069-e0e3048e911d.sketch_text.stroke-163"),sQuery(id+"FHMxAyK4CFUKdhS_1.wireOp",EDGE,"1cb9c079-ea9b-4899-8069-e0e3048e911d.sketch_text.stroke-164"),sQuery(id+"FHMxAyK4CFUKdhS_1.wireOp",EDGE,"1cb9c079-ea9b-4899-8069-e0e3048e911d.sketch_text.stroke-165"),sQuery(id+"FHMxAyK4CFUKdhS_1.wireOp",EDGE,"1cb9c079-ea9b-4899-8069-e0e3048e911d.sketch_text.stroke-166"),sQuery(id+"FHMxAyK4CFUKdhS_1.wireOp",EDGE,"1cb9c079-ea9b-4899-8069-e0e3048e911d.sketch_text.stroke-167"),sQuery(id+"FHMxAyK4CFUKdhS_1.wireOp",EDGE,"1cb9c079-ea9b-4899-8069-e0e3048e911d.sketch_text.stroke-168"),sQuery(id+"FHMxAyK4CFUKdhS_1.wireOp",EDGE,"1cb9c079-ea9b-4899-8069-e0e3048e911d.sketch_text.stroke-169"),sQuery(id+"FHMxAyK4CFUKdhS_1.wireOp",EDGE,"1cb9c079-ea9b-4899-8069-e0e3048e911d.sketch_text.stroke-170"),sQuery(id+"FHMxAyK4CFUKdhS_1.wireOp",EDGE,"1cb9c079-ea9b-4899-8069-e0e3048e911d.sketch_text.stroke-171"),sQuery(id+"FHMxAyK4CFUKdhS_1.wireOp",EDGE,"1cb9c079-ea9b-4899-8069-e0e3048e911d.sketch_text.stroke-172"),sQuery(id+"FHMxAyK4CFUKdhS_1.wireOp",EDGE,"1cb9c079-ea9b-4899-8069-e0e3048e911d.sketch_text.stroke-173"),sQuery(id+"FHMxAyK4CFUKdhS_1.wireOp",EDGE,"1cb9c079-ea9b-4899-8069-e0e3048e911d.sketch_text.stroke-174"),sQuery(id+"FHMxAyK4CFUKdhS_1.wireOp",EDGE,"1cb9c079-ea9b-4899-8069-e0e3048e911d.sketch_text.stroke-175"),sQuery(id+"FHMxAyK4CFUKdhS_1.wireOp",EDGE,"1cb9c079-ea9b-4899-8069-e0e3048e911d.sketch_text.stroke-176"),sQuery(id+"FHMxAyK4CFUKdhS_1.wireOp",EDGE,"1cb9c079-ea9b-4899-8069-e0e3048e911d.sketch_text.stroke-177"),sQuery(id+"FHMxAyK4CFUKdhS_1.wireOp",EDGE,"1cb9c079-ea9b-4899-8069-e0e3048e911d.sketch_text.stroke-178"),sQuery(id+"FHMxAyK4CFUKdhS_1.wireOp",EDGE,"1cb9c079-ea9b-4899-8069-e0e3048e911d.sketch_text.stroke-179"),sQuery(id+"FHMxAyK4CFUKdhS_1.wireOp",EDGE,"1cb9c079-ea9b-4899-8069-e0e3048e911d.sketch_text.stroke-180"),sQuery(id+"F3.wireOp",EDGE,"8007402e-1a4e-4a06-85a5-2af08e553504"),subQ2])],"isStart":true}),makeQuery(id+"F4.opExtrude","SWEPT_FACE",FACE,{"disambiguationData":[OSD([subQ2])]})]),OD(1.0)],"derivedFrom":makeQuery(id+"F1.opExtrude","CAP_EDGE",EDGE,{"disambiguationData":[OSD([subQ0])],"isStart":false})});}
            var Q15;
            {var subQ0=sQuery(id+"F3.wireOp",EDGE,"8007402e-1a4e-4a06-85a5-2af08e553504");var subQ1=sQuery(id+"F0.wireOp",EDGE,"E0.top");var subQ2=sQuery(id+"F3.wireOp",EDGE,"727ac2c1-f511-4829-95a7-a443ef16a4cd");var subQ3=sQuery(id+"F0.wireOp",EDGE,"E0.bottom");Q15=makeQuery(id+"F4.boolean.opBoolean","SPLIT",EDGE,{"disambiguationData":[TD([makeQuery(id+"F1.opExtrude","CAP_FACE",FACE,{"disambiguationData":[OSD([subQ3,subQ1,sQuery(id+"F0.wireOp",EDGE,"E0.left"),sQuery(id+"F0.wireOp",EDGE,"E0.right")])],"isStart":false}),makeQuery(id+"F1.opExtrude","SWEPT_FACE",FACE,{"disambiguationData":[OSD([subQ1])]}),makeQuery(id+"F4.opExtrude","SWEPT_FACE",FACE,{"disambiguationData":[OSD([subQ0])]}),makeQuery(id+"F4.opExtrude","CAP_FACE",FACE,{"disambiguationData":[OSD([subQ3,sQuery(id+"F2.wireOp",EDGE,"fcba4419-a2ee-464f-be9d-58f11bf3418b.sketch_text.stroke-0"),sQuery(id+"F2.wireOp",EDGE,"fcba4419-a2ee-464f-be9d-58f11bf3418b.sketch_text.stroke-1"),sQuery(id+"F2.wireOp",EDGE,"fcba4419-a2ee-464f-be9d-58f11bf3418b.sketch_text.stroke-2"),sQuery(id+"F2.wireOp",EDGE,"fcba4419-a2ee-464f-be9d-58f11bf3418b.sketch_text.stroke-3"),sQuery(id+"F2.wireOp",EDGE,"fcba4419-a2ee-464f-be9d-58f11bf3418b.sketch_text.stroke-4"),sQuery(id+"F2.wireOp",EDGE,"fcba4419-a2ee-464f-be9d-58f11bf3418b.sketch_text.stroke-5"),sQuery(id+"F2.wireOp",EDGE,"fcba4419-a2ee-464f-be9d-58f11bf3418b.sketch_text.stroke-6"),sQuery(id+"F2.wireOp",EDGE,"fcba4419-a2ee-464f-be9d-58f11bf3418b.sketch_text.stroke-7"),sQuery(id+"F2.wireOp",EDGE,"fcba4419-a2ee-464f-be9d-58f11bf3418b.sketch_text.stroke-8"),sQuery(id+"F2.wireOp",EDGE,"fcba4419-a2ee-464f-be9d-58f11bf3418b.sketch_text.stroke-9"),sQuery(id+"F2.wireOp",EDGE,"fcba4419-a2ee-464f-be9d-58f11bf3418b.sketch_text.stroke-10"),sQuery(id+"F2.wireOp",EDGE,"fcba4419-a2ee-464f-be9d-58f11bf3418b.sketch_text.stroke-11"),sQuery(id+"F2.wireOp",EDGE,"fcba4419-a2ee-464f-be9d-58f11bf3418b.sketch_text.stroke-12"),sQuery(id+"F2.wireOp",EDGE,"fcba4419-a2ee-464f-be9d-58f11bf3418b.sketch_text.stroke-13"),sQuery(id+"F2.wireOp",EDGE,"fcba4419-a2ee-464f-be9d-58f11bf3418b.sketch_text.stroke-14"),sQuery(id+"F2.wireOp",EDGE,"fcba4419-a2ee-464f-be9d-58f11bf3418b.sketch_text.stroke-15"),sQuery(id+"F2.wireOp",EDGE,"fcba4419-a2ee-464f-be9d-58f11bf3418b.sketch_text.stroke-16"),sQuery(id+"F2.wireOp",EDGE,"fcba4419-a2ee-464f-be9d-58f11bf3418b.sketch_text.stroke-17"),sQuery(id+"F2.wireOp",EDGE,"fcba4419-a2ee-464f-be9d-58f11bf3418b.sketch_text.stroke-18"),sQuery(id+"F2.wireOp",EDGE,"fcba4419-a2ee-464f-be9d-58f11bf3418b.sketch_text.stroke-19"),sQuery(id+"F2.wireOp",EDGE,"fcba4419-a2ee-464f-be9d-58f11bf3418b.sketch_text.stroke-20"),sQuery(id+"F2.wireOp",EDGE,"fcba4419-a2ee-464f-be9d-58f11bf3418b.sketch_text.stroke-21"),sQuery(id+"F2.wireOp",EDGE,"fcba4419-a2ee-464f-be9d-58f11bf3418b.sketch_text.stroke-22"),sQuery(id+"F2.wireOp",EDGE,"fcba4419-a2ee-464f-be9d-58f11bf3418b.sketch_text.stroke-23"),sQuery(id+"F2.wireOp",EDGE,"fcba4419-a2ee-464f-be9d-58f11bf3418b.sketch_text.stroke-24"),sQuery(id+"F2.wireOp",EDGE,"fcba4419-a2ee-464f-be9d-58f11bf3418b.sketch_text.stroke-25"),sQuery(id+"F2.wireOp",EDGE,"fcba4419-a2ee-464f-be9d-58f11bf3418b.sketch_text.stroke-26"),sQuery(id+"F2.wireOp",EDGE,"fcba4419-a2ee-464f-be9d-58f11bf3418b.sketch_text.stroke-27"),sQuery(id+"F2.wireOp",EDGE,"fcba4419-a2ee-464f-be9d-58f11bf3418b.sketch_text.stroke-28"),sQuery(id+"F2.wireOp",EDGE,"fcba4419-a2ee-464f-be9d-58f11bf3418b.sketch_text.stroke-29"),sQuery(id+"F2.wireOp",EDGE,"fcba4419-a2ee-464f-be9d-58f11bf3418b.sketch_text.stroke-30"),sQuery(id+"F2.wireOp",EDGE,"fcba4419-a2ee-464f-be9d-58f11bf3418b.sketch_text.stroke-31"),sQuery(id+"F2.wireOp",EDGE,"fcba4419-a2ee-464f-be9d-58f11bf3418b.sketch_text.stroke-32"),sQuery(id+"F2.wireOp",EDGE,"fcba4419-a2ee-464f-be9d-58f11bf3418b.sketch_text.stroke-33"),sQuery(id+"F2.wireOp",EDGE,"fcba4419-a2ee-464f-be9d-58f11bf3418b.sketch_text.stroke-34"),sQuery(id+"F2.wireOp",EDGE,"fcba4419-a2ee-464f-be9d-58f11bf3418b.sketch_text.stroke-35"),sQuery(id+"F2.wireOp",EDGE,"fcba4419-a2ee-464f-be9d-58f11bf3418b.sketch_text.stroke-36"),sQuery(id+"F2.wireOp",EDGE,"fcba4419-a2ee-464f-be9d-58f11bf3418b.sketch_text.stroke-37"),sQuery(id+"F2.wireOp",EDGE,"fcba4419-a2ee-464f-be9d-58f11bf3418b.sketch_text.stroke-38"),sQuery(id+"F2.wireOp",EDGE,"fcba4419-a2ee-464f-be9d-58f11bf3418b.sketch_text.stroke-39"),sQuery(id+"F2.wireOp",EDGE,"fcba4419-a2ee-464f-be9d-58f11bf3418b.sketch_text.stroke-40"),sQuery(id+"F2.wireOp",EDGE,"fcba4419-a2ee-464f-be9d-58f11bf3418b.sketch_text.stroke-41"),sQuery(id+"F2.wireOp",EDGE,"fcba4419-a2ee-464f-be9d-58f11bf3418b.sketch_text.stroke-42"),sQuery(id+"F2.wireOp",EDGE,"fcba4419-a2ee-464f-be9d-58f11bf3418b.sketch_text.stroke-43"),sQuery(id+"F2.wireOp",EDGE,"fcba4419-a2ee-464f-be9d-58f11bf3418b.sketch_text.stroke-44"),sQuery(id+"F2.wireOp",EDGE,"fcba4419-a2ee-464f-be9d-58f11bf3418b.sketch_text.stroke-45"),sQuery(id+"F2.wireOp",EDGE,"fcba4419-a2ee-464f-be9d-58f11bf3418b.sketch_text.stroke-46"),sQuery(id+"F2.wireOp",EDGE,"fcba4419-a2ee-464f-be9d-58f11bf3418b.sketch_text.stroke-47"),sQuery(id+"F2.wireOp",EDGE,"fcba4419-a2ee-464f-be9d-58f11bf3418b.sketch_text.stroke-48"),sQuery(id+"F2.wireOp",EDGE,"fcba4419-a2ee-464f-be9d-58f11bf3418b.sketch_text.stroke-49"),sQuery(id+"F2.wireOp",EDGE,"fcba4419-a2ee-464f-be9d-58f11bf3418b.sketch_text.stroke-50"),sQuery(id+"F2.wireOp",EDGE,"fcba4419-a2ee-464f-be9d-58f11bf3418b.sketch_text.stroke-51"),sQuery(id+"F2.wireOp",EDGE,"fcba4419-a2ee-464f-be9d-58f11bf3418b.sketch_text.stroke-52"),sQuery(id+"F2.wireOp",EDGE,"fcba4419-a2ee-464f-be9d-58f11bf3418b.sketch_text.stroke-53"),sQuery(id+"F2.wireOp",EDGE,"fcba4419-a2ee-464f-be9d-58f11bf3418b.sketch_text.stroke-54"),sQuery(id+"F2.wireOp",EDGE,"fcba4419-a2ee-464f-be9d-58f11bf3418b.sketch_text.stroke-55"),sQuery(id+"F2.wireOp",EDGE,"fcba4419-a2ee-464f-be9d-58f11bf3418b.sketch_text.stroke-56"),sQuery(id+"F2.wireOp",EDGE,"fcba4419-a2ee-464f-be9d-58f11bf3418b.sketch_text.stroke-57"),sQuery(id+"F2.wireOp",EDGE,"fcba4419-a2ee-464f-be9d-58f11bf3418b.sketch_text.stroke-58"),sQuery(id+"F2.wireOp",EDGE,"fcba4419-a2ee-464f-be9d-58f11bf3418b.sketch_text.stroke-59"),sQuery(id+"F2.wireOp",EDGE,"fcba4419-a2ee-464f-be9d-58f11bf3418b.sketch_text.stroke-60"),sQuery(id+"F2.wireOp",EDGE,"fcba4419-a2ee-464f-be9d-58f11bf3418b.sketch_text.stroke-61"),sQuery(id+"F2.wireOp",EDGE,"fcba4419-a2ee-464f-be9d-58f11bf3418b.sketch_text.stroke-62"),sQuery(id+"F2.wireOp",EDGE,"fcba4419-a2ee-464f-be9d-58f11bf3418b.sketch_text.stroke-63"),sQuery(id+"F2.wireOp",EDGE,"fcba4419-a2ee-464f-be9d-58f11bf3418b.sketch_text.stroke-64"),sQuery(id+"F2.wireOp",EDGE,"fcba4419-a2ee-464f-be9d-58f11bf3418b.sketch_text.stroke-65"),sQuery(id+"F2.wireOp",EDGE,"fcba4419-a2ee-464f-be9d-58f11bf3418b.sketch_text.stroke-66"),sQuery(id+"F2.wireOp",EDGE,"fcba4419-a2ee-464f-be9d-58f11bf3418b.sketch_text.stroke-67"),sQuery(id+"F2.wireOp",EDGE,"fcba4419-a2ee-464f-be9d-58f11bf3418b.sketch_text.stroke-68"),sQuery(id+"F2.wireOp",EDGE,"fcba4419-a2ee-464f-be9d-58f11bf3418b.sketch_text.stroke-69"),sQuery(id+"F2.wireOp",EDGE,"fcba4419-a2ee-464f-be9d-58f11bf3418b.sketch_text.stroke-70"),sQuery(id+"F2.wireOp",EDGE,"fcba4419-a2ee-464f-be9d-58f11bf3418b.sketch_text.stroke-71"),sQuery(id+"F2.wireOp",EDGE,"fcba4419-a2ee-464f-be9d-58f11bf3418b.sketch_text.stroke-72"),sQuery(id+"F2.wireOp",EDGE,"fcba4419-a2ee-464f-be9d-58f11bf3418b.sketch_text.stroke-73"),sQuery(id+"F2.wireOp",EDGE,"fcba4419-a2ee-464f-be9d-58f11bf3418b.sketch_text.stroke-74"),sQuery(id+"F2.wireOp",EDGE,"fcba4419-a2ee-464f-be9d-58f11bf3418b.sketch_text.stroke-75"),sQuery(id+"F2.wireOp",EDGE,"fcba4419-a2ee-464f-be9d-58f11bf3418b.sketch_text.stroke-76"),sQuery(id+"F2.wireOp",EDGE,"fcba4419-a2ee-464f-be9d-58f11bf3418b.sketch_text.stroke-77"),sQuery(id+"F2.wireOp",EDGE,"fcba4419-a2ee-464f-be9d-58f11bf3418b.sketch_text.stroke-78"),sQuery(id+"F2.wireOp",EDGE,"fcba4419-a2ee-464f-be9d-58f11bf3418b.sketch_text.stroke-79"),sQuery(id+"F2.wireOp",EDGE,"fcba4419-a2ee-464f-be9d-58f11bf3418b.sketch_text.stroke-80"),sQuery(id+"F2.wireOp",EDGE,"fcba4419-a2ee-464f-be9d-58f11bf3418b.sketch_text.stroke-81"),sQuery(id+"F2.wireOp",EDGE,"fcba4419-a2ee-464f-be9d-58f11bf3418b.sketch_text.stroke-82"),sQuery(id+"F2.wireOp",EDGE,"fcba4419-a2ee-464f-be9d-58f11bf3418b.sketch_text.stroke-83"),sQuery(id+"F2.wireOp",EDGE,"fcba4419-a2ee-464f-be9d-58f11bf3418b.sketch_text.stroke-84"),sQuery(id+"F2.wireOp",EDGE,"fcba4419-a2ee-464f-be9d-58f11bf3418b.sketch_text.stroke-85"),sQuery(id+"F2.wireOp",EDGE,"fcba4419-a2ee-464f-be9d-58f11bf3418b.sketch_text.stroke-86"),sQuery(id+"F2.wireOp",EDGE,"fcba4419-a2ee-464f-be9d-58f11bf3418b.sketch_text.stroke-87"),sQuery(id+"F2.wireOp",EDGE,"fcba4419-a2ee-464f-be9d-58f11bf3418b.sketch_text.stroke-88"),sQuery(id+"F2.wireOp",EDGE,"fcba4419-a2ee-464f-be9d-58f11bf3418b.sketch_text.stroke-89"),sQuery(id+"F2.wireOp",EDGE,"fcba4419-a2ee-464f-be9d-58f11bf3418b.sketch_text.stroke-90"),sQuery(id+"F2.wireOp",EDGE,"fcba4419-a2ee-464f-be9d-58f11bf3418b.sketch_text.stroke-91"),sQuery(id+"F2.wireOp",EDGE,"fcba4419-a2ee-464f-be9d-58f11bf3418b.sketch_text.stroke-92"),sQuery(id+"F2.wireOp",EDGE,"fcba4419-a2ee-464f-be9d-58f11bf3418b.sketch_text.stroke-93"),sQuery(id+"F2.wireOp",EDGE,"fcba4419-a2ee-464f-be9d-58f11bf3418b.sketch_text.stroke-94"),sQuery(id+"F2.wireOp",EDGE,"fcba4419-a2ee-464f-be9d-58f11bf3418b.sketch_text.stroke-95"),sQuery(id+"F2.wireOp",EDGE,"fcba4419-a2ee-464f-be9d-58f11bf3418b.sketch_text.stroke-96"),sQuery(id+"F2.wireOp",EDGE,"fcba4419-a2ee-464f-be9d-58f11bf3418b.sketch_text.stroke-97"),sQuery(id+"F2.wireOp",EDGE,"fcba4419-a2ee-464f-be9d-58f11bf3418b.sketch_text.stroke-98"),sQuery(id+"F2.wireOp",EDGE,"fcba4419-a2ee-464f-be9d-58f11bf3418b.sketch_text.stroke-99"),sQuery(id+"F2.wireOp",EDGE,"fcba4419-a2ee-464f-be9d-58f11bf3418b.sketch_text.stroke-100"),sQuery(id+"F2.wireOp",EDGE,"fcba4419-a2ee-464f-be9d-58f11bf3418b.sketch_text.stroke-101"),sQuery(id+"F2.wireOp",EDGE,"fcba4419-a2ee-464f-be9d-58f11bf3418b.sketch_text.stroke-102"),sQuery(id+"F2.wireOp",EDGE,"fcba4419-a2ee-464f-be9d-58f11bf3418b.sketch_text.stroke-103"),sQuery(id+"F2.wireOp",EDGE,"fcba4419-a2ee-464f-be9d-58f11bf3418b.sketch_text.stroke-104"),sQuery(id+"F2.wireOp",EDGE,"fcba4419-a2ee-464f-be9d-58f11bf3418b.sketch_text.stroke-105"),sQuery(id+"F2.wireOp",EDGE,"fcba4419-a2ee-464f-be9d-58f11bf3418b.sketch_text.stroke-106"),sQuery(id+"F2.wireOp",EDGE,"fcba4419-a2ee-464f-be9d-58f11bf3418b.sketch_text.stroke-107"),sQuery(id+"F2.wireOp",EDGE,"fcba4419-a2ee-464f-be9d-58f11bf3418b.sketch_text.stroke-108"),sQuery(id+"F2.wireOp",EDGE,"fcba4419-a2ee-464f-be9d-58f11bf3418b.sketch_text.stroke-109"),sQuery(id+"F2.wireOp",EDGE,"fcba4419-a2ee-464f-be9d-58f11bf3418b.sketch_text.stroke-110"),sQuery(id+"F2.wireOp",EDGE,"fcba4419-a2ee-464f-be9d-58f11bf3418b.sketch_text.stroke-111"),sQuery(id+"F2.wireOp",EDGE,"fcba4419-a2ee-464f-be9d-58f11bf3418b.sketch_text.stroke-112"),sQuery(id+"F2.wireOp",EDGE,"fcba4419-a2ee-464f-be9d-58f11bf3418b.sketch_text.stroke-113"),sQuery(id+"F2.wireOp",EDGE,"fcba4419-a2ee-464f-be9d-58f11bf3418b.sketch_text.stroke-114"),sQuery(id+"F2.wireOp",EDGE,"fcba4419-a2ee-464f-be9d-58f11bf3418b.sketch_text.stroke-115"),sQuery(id+"F2.wireOp",EDGE,"fcba4419-a2ee-464f-be9d-58f11bf3418b.sketch_text.stroke-116"),sQuery(id+"F2.wireOp",EDGE,"fcba4419-a2ee-464f-be9d-58f11bf3418b.sketch_text.stroke-117"),sQuery(id+"F2.wireOp",EDGE,"fcba4419-a2ee-464f-be9d-58f11bf3418b.sketch_text.stroke-118"),sQuery(id+"F2.wireOp",EDGE,"fcba4419-a2ee-464f-be9d-58f11bf3418b.sketch_text.stroke-119"),sQuery(id+"F2.wireOp",EDGE,"fcba4419-a2ee-464f-be9d-58f11bf3418b.sketch_text.stroke-120"),sQuery(id+"F2.wireOp",EDGE,"fcba4419-a2ee-464f-be9d-58f11bf3418b.sketch_text.stroke-121"),sQuery(id+"F2.wireOp",EDGE,"fcba4419-a2ee-464f-be9d-58f11bf3418b.sketch_text.stroke-122"),sQuery(id+"F2.wireOp",EDGE,"fcba4419-a2ee-464f-be9d-58f11bf3418b.sketch_text.stroke-123"),sQuery(id+"F2.wireOp",EDGE,"fcba4419-a2ee-464f-be9d-58f11bf3418b.sketch_text.stroke-124"),sQuery(id+"F2.wireOp",EDGE,"fcba4419-a2ee-464f-be9d-58f11bf3418b.sketch_text.stroke-125"),sQuery(id+"F2.wireOp",EDGE,"fcba4419-a2ee-464f-be9d-58f11bf3418b.sketch_text.stroke-126"),sQuery(id+"F2.wireOp",EDGE,"fcba4419-a2ee-464f-be9d-58f11bf3418b.sketch_text.stroke-127"),sQuery(id+"F2.wireOp",EDGE,"fcba4419-a2ee-464f-be9d-58f11bf3418b.sketch_text.stroke-128"),sQuery(id+"F2.wireOp",EDGE,"fcba4419-a2ee-464f-be9d-58f11bf3418b.sketch_text.stroke-129"),sQuery(id+"F2.wireOp",EDGE,"fcba4419-a2ee-464f-be9d-58f11bf3418b.sketch_text.stroke-130"),sQuery(id+"F2.wireOp",EDGE,"fcba4419-a2ee-464f-be9d-58f11bf3418b.sketch_text.stroke-131"),sQuery(id+"F2.wireOp",EDGE,"fcba4419-a2ee-464f-be9d-58f11bf3418b.sketch_text.stroke-132"),sQuery(id+"F2.wireOp",EDGE,"fcba4419-a2ee-464f-be9d-58f11bf3418b.sketch_text.stroke-133"),sQuery(id+"F2.wireOp",EDGE,"fcba4419-a2ee-464f-be9d-58f11bf3418b.sketch_text.stroke-134"),sQuery(id+"F2.wireOp",EDGE,"fcba4419-a2ee-464f-be9d-58f11bf3418b.sketch_text.stroke-135"),sQuery(id+"F2.wireOp",EDGE,"fcba4419-a2ee-464f-be9d-58f11bf3418b.sketch_text.stroke-136"),sQuery(id+"F2.wireOp",EDGE,"fcba4419-a2ee-464f-be9d-58f11bf3418b.sketch_text.stroke-137"),sQuery(id+"F2.wireOp",EDGE,"fcba4419-a2ee-464f-be9d-58f11bf3418b.sketch_text.stroke-138"),sQuery(id+"F2.wireOp",EDGE,"fcba4419-a2ee-464f-be9d-58f11bf3418b.sketch_text.stroke-139"),sQuery(id+"F2.wireOp",EDGE,"fcba4419-a2ee-464f-be9d-58f11bf3418b.sketch_text.stroke-140"),sQuery(id+"F2.wireOp",EDGE,"fcba4419-a2ee-464f-be9d-58f11bf3418b.sketch_text.stroke-141"),sQuery(id+"F2.wireOp",EDGE,"fcba4419-a2ee-464f-be9d-58f11bf3418b.sketch_text.stroke-142"),sQuery(id+"F2.wireOp",EDGE,"fcba4419-a2ee-464f-be9d-58f11bf3418b.sketch_text.stroke-143"),sQuery(id+"F2.wireOp",EDGE,"fcba4419-a2ee-464f-be9d-58f11bf3418b.sketch_text.stroke-144"),sQuery(id+"F2.wireOp",EDGE,"fcba4419-a2ee-464f-be9d-58f11bf3418b.sketch_text.stroke-145"),sQuery(id+"F2.wireOp",EDGE,"fcba4419-a2ee-464f-be9d-58f11bf3418b.sketch_text.stroke-146"),sQuery(id+"F2.wireOp",EDGE,"fcba4419-a2ee-464f-be9d-58f11bf3418b.sketch_text.stroke-147"),sQuery(id+"F2.wireOp",EDGE,"fcba4419-a2ee-464f-be9d-58f11bf3418b.sketch_text.stroke-148"),sQuery(id+"F2.wireOp",EDGE,"fcba4419-a2ee-464f-be9d-58f11bf3418b.sketch_text.stroke-149"),sQuery(id+"F2.wireOp",EDGE,"fcba4419-a2ee-464f-be9d-58f11bf3418b.sketch_text.stroke-150"),sQuery(id+"F2.wireOp",EDGE,"fcba4419-a2ee-464f-be9d-58f11bf3418b.sketch_text.stroke-151"),sQuery(id+"F2.wireOp",EDGE,"fcba4419-a2ee-464f-be9d-58f11bf3418b.sketch_text.stroke-152"),sQuery(id+"F2.wireOp",EDGE,"fcba4419-a2ee-464f-be9d-58f11bf3418b.sketch_text.stroke-153"),sQuery(id+"F2.wireOp",EDGE,"fcba4419-a2ee-464f-be9d-58f11bf3418b.sketch_text.stroke-154"),sQuery(id+"F2.wireOp",EDGE,"fcba4419-a2ee-464f-be9d-58f11bf3418b.sketch_text.stroke-155"),sQuery(id+"F2.wireOp",EDGE,"fcba4419-a2ee-464f-be9d-58f11bf3418b.sketch_text.stroke-156"),sQuery(id+"F2.wireOp",EDGE,"fcba4419-a2ee-464f-be9d-58f11bf3418b.sketch_text.stroke-157"),sQuery(id+"F2.wireOp",EDGE,"fcba4419-a2ee-464f-be9d-58f11bf3418b.sketch_text.stroke-158"),sQuery(id+"F2.wireOp",EDGE,"fcba4419-a2ee-464f-be9d-58f11bf3418b.sketch_text.stroke-159"),sQuery(id+"F2.wireOp",EDGE,"fcba4419-a2ee-464f-be9d-58f11bf3418b.sketch_text.stroke-160"),sQuery(id+"F2.wireOp",EDGE,"fcba4419-a2ee-464f-be9d-58f11bf3418b.sketch_text.stroke-161"),sQuery(id+"F2.wireOp",EDGE,"fcba4419-a2ee-464f-be9d-58f11bf3418b.sketch_text.stroke-162"),sQuery(id+"F2.wireOp",EDGE,"fcba4419-a2ee-464f-be9d-58f11bf3418b.sketch_text.stroke-163"),sQuery(id+"F2.wireOp",EDGE,"fcba4419-a2ee-464f-be9d-58f11bf3418b.sketch_text.stroke-164"),sQuery(id+"F2.wireOp",EDGE,"fcba4419-a2ee-464f-be9d-58f11bf3418b.sketch_text.stroke-165"),sQuery(id+"F2.wireOp",EDGE,"fcba4419-a2ee-464f-be9d-58f11bf3418b.sketch_text.stroke-166"),sQuery(id+"F2.wireOp",EDGE,"fcba4419-a2ee-464f-be9d-58f11bf3418b.sketch_text.stroke-167"),sQuery(id+"F2.wireOp",EDGE,"fcba4419-a2ee-464f-be9d-58f11bf3418b.sketch_text.stroke-168"),sQuery(id+"F2.wireOp",EDGE,"fcba4419-a2ee-464f-be9d-58f11bf3418b.sketch_text.stroke-169"),sQuery(id+"F2.wireOp",EDGE,"fcba4419-a2ee-464f-be9d-58f11bf3418b.sketch_text.stroke-170"),sQuery(id+"F2.wireOp",EDGE,"fcba4419-a2ee-464f-be9d-58f11bf3418b.sketch_text.stroke-171"),sQuery(id+"F2.wireOp",EDGE,"fcba4419-a2ee-464f-be9d-58f11bf3418b.sketch_text.stroke-172"),sQuery(id+"F2.wireOp",EDGE,"fcba4419-a2ee-464f-be9d-58f11bf3418b.sketch_text.stroke-173"),sQuery(id+"FHMxAyK4CFUKdhS_1.wireOp",EDGE,"1cb9c079-ea9b-4899-8069-e0e3048e911d.sketch_text.stroke-0"),sQuery(id+"FHMxAyK4CFUKdhS_1.wireOp",EDGE,"1cb9c079-ea9b-4899-8069-e0e3048e911d.sketch_text.stroke-1"),sQuery(id+"FHMxAyK4CFUKdhS_1.wireOp",EDGE,"1cb9c079-ea9b-4899-8069-e0e3048e911d.sketch_text.stroke-2"),sQuery(id+"FHMxAyK4CFUKdhS_1.wireOp",EDGE,"1cb9c079-ea9b-4899-8069-e0e3048e911d.sketch_text.stroke-3"),sQuery(id+"FHMxAyK4CFUKdhS_1.wireOp",EDGE,"1cb9c079-ea9b-4899-8069-e0e3048e911d.sketch_text.stroke-4"),sQuery(id+"FHMxAyK4CFUKdhS_1.wireOp",EDGE,"1cb9c079-ea9b-4899-8069-e0e3048e911d.sketch_text.stroke-5"),sQuery(id+"FHMxAyK4CFUKdhS_1.wireOp",EDGE,"1cb9c079-ea9b-4899-8069-e0e3048e911d.sketch_text.stroke-6"),sQuery(id+"FHMxAyK4CFUKdhS_1.wireOp",EDGE,"1cb9c079-ea9b-4899-8069-e0e3048e911d.sketch_text.stroke-7"),sQuery(id+"FHMxAyK4CFUKdhS_1.wireOp",EDGE,"1cb9c079-ea9b-4899-8069-e0e3048e911d.sketch_text.stroke-8"),sQuery(id+"FHMxAyK4CFUKdhS_1.wireOp",EDGE,"1cb9c079-ea9b-4899-8069-e0e3048e911d.sketch_text.stroke-9"),sQuery(id+"FHMxAyK4CFUKdhS_1.wireOp",EDGE,"1cb9c079-ea9b-4899-8069-e0e3048e911d.sketch_text.stroke-10"),sQuery(id+"FHMxAyK4CFUKdhS_1.wireOp",EDGE,"1cb9c079-ea9b-4899-8069-e0e3048e911d.sketch_text.stroke-11"),sQuery(id+"FHMxAyK4CFUKdhS_1.wireOp",EDGE,"1cb9c079-ea9b-4899-8069-e0e3048e911d.sketch_text.stroke-12"),sQuery(id+"FHMxAyK4CFUKdhS_1.wireOp",EDGE,"1cb9c079-ea9b-4899-8069-e0e3048e911d.sketch_text.stroke-13"),sQuery(id+"FHMxAyK4CFUKdhS_1.wireOp",EDGE,"1cb9c079-ea9b-4899-8069-e0e3048e911d.sketch_text.stroke-14"),sQuery(id+"FHMxAyK4CFUKdhS_1.wireOp",EDGE,"1cb9c079-ea9b-4899-8069-e0e3048e911d.sketch_text.stroke-15"),sQuery(id+"FHMxAyK4CFUKdhS_1.wireOp",EDGE,"1cb9c079-ea9b-4899-8069-e0e3048e911d.sketch_text.stroke-16"),sQuery(id+"FHMxAyK4CFUKdhS_1.wireOp",EDGE,"1cb9c079-ea9b-4899-8069-e0e3048e911d.sketch_text.stroke-17"),sQuery(id+"FHMxAyK4CFUKdhS_1.wireOp",EDGE,"1cb9c079-ea9b-4899-8069-e0e3048e911d.sketch_text.stroke-18"),sQuery(id+"FHMxAyK4CFUKdhS_1.wireOp",EDGE,"1cb9c079-ea9b-4899-8069-e0e3048e911d.sketch_text.stroke-19"),sQuery(id+"FHMxAyK4CFUKdhS_1.wireOp",EDGE,"1cb9c079-ea9b-4899-8069-e0e3048e911d.sketch_text.stroke-20"),sQuery(id+"FHMxAyK4CFUKdhS_1.wireOp",EDGE,"1cb9c079-ea9b-4899-8069-e0e3048e911d.sketch_text.stroke-21"),sQuery(id+"FHMxAyK4CFUKdhS_1.wireOp",EDGE,"1cb9c079-ea9b-4899-8069-e0e3048e911d.sketch_text.stroke-22"),sQuery(id+"FHMxAyK4CFUKdhS_1.wireOp",EDGE,"1cb9c079-ea9b-4899-8069-e0e3048e911d.sketch_text.stroke-23"),sQuery(id+"FHMxAyK4CFUKdhS_1.wireOp",EDGE,"1cb9c079-ea9b-4899-8069-e0e3048e911d.sketch_text.stroke-24"),sQuery(id+"FHMxAyK4CFUKdhS_1.wireOp",EDGE,"1cb9c079-ea9b-4899-8069-e0e3048e911d.sketch_text.stroke-25"),sQuery(id+"FHMxAyK4CFUKdhS_1.wireOp",EDGE,"1cb9c079-ea9b-4899-8069-e0e3048e911d.sketch_text.stroke-26"),sQuery(id+"FHMxAyK4CFUKdhS_1.wireOp",EDGE,"1cb9c079-ea9b-4899-8069-e0e3048e911d.sketch_text.stroke-27"),sQuery(id+"FHMxAyK4CFUKdhS_1.wireOp",EDGE,"1cb9c079-ea9b-4899-8069-e0e3048e911d.sketch_text.stroke-28"),sQuery(id+"FHMxAyK4CFUKdhS_1.wireOp",EDGE,"1cb9c079-ea9b-4899-8069-e0e3048e911d.sketch_text.stroke-29"),sQuery(id+"FHMxAyK4CFUKdhS_1.wireOp",EDGE,"1cb9c079-ea9b-4899-8069-e0e3048e911d.sketch_text.stroke-30"),sQuery(id+"FHMxAyK4CFUKdhS_1.wireOp",EDGE,"1cb9c079-ea9b-4899-8069-e0e3048e911d.sketch_text.stroke-31"),sQuery(id+"FHMxAyK4CFUKdhS_1.wireOp",EDGE,"1cb9c079-ea9b-4899-8069-e0e3048e911d.sketch_text.stroke-32"),sQuery(id+"FHMxAyK4CFUKdhS_1.wireOp",EDGE,"1cb9c079-ea9b-4899-8069-e0e3048e911d.sketch_text.stroke-33"),sQuery(id+"FHMxAyK4CFUKdhS_1.wireOp",EDGE,"1cb9c079-ea9b-4899-8069-e0e3048e911d.sketch_text.stroke-34"),sQuery(id+"FHMxAyK4CFUKdhS_1.wireOp",EDGE,"1cb9c079-ea9b-4899-8069-e0e3048e911d.sketch_text.stroke-35"),sQuery(id+"FHMxAyK4CFUKdhS_1.wireOp",EDGE,"1cb9c079-ea9b-4899-8069-e0e3048e911d.sketch_text.stroke-36"),sQuery(id+"FHMxAyK4CFUKdhS_1.wireOp",EDGE,"1cb9c079-ea9b-4899-8069-e0e3048e911d.sketch_text.stroke-37"),sQuery(id+"FHMxAyK4CFUKdhS_1.wireOp",EDGE,"1cb9c079-ea9b-4899-8069-e0e3048e911d.sketch_text.stroke-38"),sQuery(id+"FHMxAyK4CFUKdhS_1.wireOp",EDGE,"1cb9c079-ea9b-4899-8069-e0e3048e911d.sketch_text.stroke-39"),sQuery(id+"FHMxAyK4CFUKdhS_1.wireOp",EDGE,"1cb9c079-ea9b-4899-8069-e0e3048e911d.sketch_text.stroke-40"),sQuery(id+"FHMxAyK4CFUKdhS_1.wireOp",EDGE,"1cb9c079-ea9b-4899-8069-e0e3048e911d.sketch_text.stroke-41"),sQuery(id+"FHMxAyK4CFUKdhS_1.wireOp",EDGE,"1cb9c079-ea9b-4899-8069-e0e3048e911d.sketch_text.stroke-42"),sQuery(id+"FHMxAyK4CFUKdhS_1.wireOp",EDGE,"1cb9c079-ea9b-4899-8069-e0e3048e911d.sketch_text.stroke-43"),sQuery(id+"FHMxAyK4CFUKdhS_1.wireOp",EDGE,"1cb9c079-ea9b-4899-8069-e0e3048e911d.sketch_text.stroke-44"),sQuery(id+"FHMxAyK4CFUKdhS_1.wireOp",EDGE,"1cb9c079-ea9b-4899-8069-e0e3048e911d.sketch_text.stroke-45"),sQuery(id+"FHMxAyK4CFUKdhS_1.wireOp",EDGE,"1cb9c079-ea9b-4899-8069-e0e3048e911d.sketch_text.stroke-46"),sQuery(id+"FHMxAyK4CFUKdhS_1.wireOp",EDGE,"1cb9c079-ea9b-4899-8069-e0e3048e911d.sketch_text.stroke-47"),sQuery(id+"FHMxAyK4CFUKdhS_1.wireOp",EDGE,"1cb9c079-ea9b-4899-8069-e0e3048e911d.sketch_text.stroke-48"),sQuery(id+"FHMxAyK4CFUKdhS_1.wireOp",EDGE,"1cb9c079-ea9b-4899-8069-e0e3048e911d.sketch_text.stroke-49"),sQuery(id+"FHMxAyK4CFUKdhS_1.wireOp",EDGE,"1cb9c079-ea9b-4899-8069-e0e3048e911d.sketch_text.stroke-50"),sQuery(id+"FHMxAyK4CFUKdhS_1.wireOp",EDGE,"1cb9c079-ea9b-4899-8069-e0e3048e911d.sketch_text.stroke-51"),sQuery(id+"FHMxAyK4CFUKdhS_1.wireOp",EDGE,"1cb9c079-ea9b-4899-8069-e0e3048e911d.sketch_text.stroke-52"),sQuery(id+"FHMxAyK4CFUKdhS_1.wireOp",EDGE,"1cb9c079-ea9b-4899-8069-e0e3048e911d.sketch_text.stroke-53"),sQuery(id+"FHMxAyK4CFUKdhS_1.wireOp",EDGE,"1cb9c079-ea9b-4899-8069-e0e3048e911d.sketch_text.stroke-54"),sQuery(id+"FHMxAyK4CFUKdhS_1.wireOp",EDGE,"1cb9c079-ea9b-4899-8069-e0e3048e911d.sketch_text.stroke-55"),sQuery(id+"FHMxAyK4CFUKdhS_1.wireOp",EDGE,"1cb9c079-ea9b-4899-8069-e0e3048e911d.sketch_text.stroke-56"),sQuery(id+"FHMxAyK4CFUKdhS_1.wireOp",EDGE,"1cb9c079-ea9b-4899-8069-e0e3048e911d.sketch_text.stroke-57"),sQuery(id+"FHMxAyK4CFUKdhS_1.wireOp",EDGE,"1cb9c079-ea9b-4899-8069-e0e3048e911d.sketch_text.stroke-58"),sQuery(id+"FHMxAyK4CFUKdhS_1.wireOp",EDGE,"1cb9c079-ea9b-4899-8069-e0e3048e911d.sketch_text.stroke-59"),sQuery(id+"FHMxAyK4CFUKdhS_1.wireOp",EDGE,"1cb9c079-ea9b-4899-8069-e0e3048e911d.sketch_text.stroke-60"),sQuery(id+"FHMxAyK4CFUKdhS_1.wireOp",EDGE,"1cb9c079-ea9b-4899-8069-e0e3048e911d.sketch_text.stroke-61"),sQuery(id+"FHMxAyK4CFUKdhS_1.wireOp",EDGE,"1cb9c079-ea9b-4899-8069-e0e3048e911d.sketch_text.stroke-62"),sQuery(id+"FHMxAyK4CFUKdhS_1.wireOp",EDGE,"1cb9c079-ea9b-4899-8069-e0e3048e911d.sketch_text.stroke-71"),sQuery(id+"FHMxAyK4CFUKdhS_1.wireOp",EDGE,"1cb9c079-ea9b-4899-8069-e0e3048e911d.sketch_text.stroke-72"),sQuery(id+"FHMxAyK4CFUKdhS_1.wireOp",EDGE,"1cb9c079-ea9b-4899-8069-e0e3048e911d.sketch_text.stroke-73"),sQuery(id+"FHMxAyK4CFUKdhS_1.wireOp",EDGE,"1cb9c079-ea9b-4899-8069-e0e3048e911d.sketch_text.stroke-74"),sQuery(id+"FHMxAyK4CFUKdhS_1.wireOp",EDGE,"1cb9c079-ea9b-4899-8069-e0e3048e911d.sketch_text.stroke-75"),sQuery(id+"FHMxAyK4CFUKdhS_1.wireOp",EDGE,"1cb9c079-ea9b-4899-8069-e0e3048e911d.sketch_text.stroke-76"),sQuery(id+"FHMxAyK4CFUKdhS_1.wireOp",EDGE,"1cb9c079-ea9b-4899-8069-e0e3048e911d.sketch_text.stroke-77"),sQuery(id+"FHMxAyK4CFUKdhS_1.wireOp",EDGE,"1cb9c079-ea9b-4899-8069-e0e3048e911d.sketch_text.stroke-78"),sQuery(id+"FHMxAyK4CFUKdhS_1.wireOp",EDGE,"1cb9c079-ea9b-4899-8069-e0e3048e911d.sketch_text.stroke-79"),sQuery(id+"FHMxAyK4CFUKdhS_1.wireOp",EDGE,"1cb9c079-ea9b-4899-8069-e0e3048e911d.sketch_text.stroke-80"),sQuery(id+"FHMxAyK4CFUKdhS_1.wireOp",EDGE,"1cb9c079-ea9b-4899-8069-e0e3048e911d.sketch_text.stroke-81"),sQuery(id+"FHMxAyK4CFUKdhS_1.wireOp",EDGE,"1cb9c079-ea9b-4899-8069-e0e3048e911d.sketch_text.stroke-82"),sQuery(id+"FHMxAyK4CFUKdhS_1.wireOp",EDGE,"1cb9c079-ea9b-4899-8069-e0e3048e911d.sketch_text.stroke-83"),sQuery(id+"FHMxAyK4CFUKdhS_1.wireOp",EDGE,"1cb9c079-ea9b-4899-8069-e0e3048e911d.sketch_text.stroke-84"),sQuery(id+"FHMxAyK4CFUKdhS_1.wireOp",EDGE,"1cb9c079-ea9b-4899-8069-e0e3048e911d.sketch_text.stroke-85"),sQuery(id+"FHMxAyK4CFUKdhS_1.wireOp",EDGE,"1cb9c079-ea9b-4899-8069-e0e3048e911d.sketch_text.stroke-86"),sQuery(id+"FHMxAyK4CFUKdhS_1.wireOp",EDGE,"1cb9c079-ea9b-4899-8069-e0e3048e911d.sketch_text.stroke-87"),sQuery(id+"FHMxAyK4CFUKdhS_1.wireOp",EDGE,"1cb9c079-ea9b-4899-8069-e0e3048e911d.sketch_text.stroke-88"),sQuery(id+"FHMxAyK4CFUKdhS_1.wireOp",EDGE,"1cb9c079-ea9b-4899-8069-e0e3048e911d.sketch_text.stroke-89"),sQuery(id+"FHMxAyK4CFUKdhS_1.wireOp",EDGE,"1cb9c079-ea9b-4899-8069-e0e3048e911d.sketch_text.stroke-90"),sQuery(id+"FHMxAyK4CFUKdhS_1.wireOp",EDGE,"1cb9c079-ea9b-4899-8069-e0e3048e911d.sketch_text.stroke-91"),sQuery(id+"FHMxAyK4CFUKdhS_1.wireOp",EDGE,"1cb9c079-ea9b-4899-8069-e0e3048e911d.sketch_text.stroke-92"),sQuery(id+"FHMxAyK4CFUKdhS_1.wireOp",EDGE,"1cb9c079-ea9b-4899-8069-e0e3048e911d.sketch_text.stroke-93"),sQuery(id+"FHMxAyK4CFUKdhS_1.wireOp",EDGE,"1cb9c079-ea9b-4899-8069-e0e3048e911d.sketch_text.stroke-94"),sQuery(id+"FHMxAyK4CFUKdhS_1.wireOp",EDGE,"1cb9c079-ea9b-4899-8069-e0e3048e911d.sketch_text.stroke-95"),sQuery(id+"FHMxAyK4CFUKdhS_1.wireOp",EDGE,"1cb9c079-ea9b-4899-8069-e0e3048e911d.sketch_text.stroke-96"),sQuery(id+"FHMxAyK4CFUKdhS_1.wireOp",EDGE,"1cb9c079-ea9b-4899-8069-e0e3048e911d.sketch_text.stroke-97"),sQuery(id+"FHMxAyK4CFUKdhS_1.wireOp",EDGE,"1cb9c079-ea9b-4899-8069-e0e3048e911d.sketch_text.stroke-103"),sQuery(id+"FHMxAyK4CFUKdhS_1.wireOp",EDGE,"1cb9c079-ea9b-4899-8069-e0e3048e911d.sketch_text.stroke-104"),sQuery(id+"FHMxAyK4CFUKdhS_1.wireOp",EDGE,"1cb9c079-ea9b-4899-8069-e0e3048e911d.sketch_text.stroke-105"),sQuery(id+"FHMxAyK4CFUKdhS_1.wireOp",EDGE,"1cb9c079-ea9b-4899-8069-e0e3048e911d.sketch_text.stroke-106"),sQuery(id+"FHMxAyK4CFUKdhS_1.wireOp",EDGE,"1cb9c079-ea9b-4899-8069-e0e3048e911d.sketch_text.stroke-107"),sQuery(id+"FHMxAyK4CFUKdhS_1.wireOp",EDGE,"1cb9c079-ea9b-4899-8069-e0e3048e911d.sketch_text.stroke-108"),sQuery(id+"FHMxAyK4CFUKdhS_1.wireOp",EDGE,"1cb9c079-ea9b-4899-8069-e0e3048e911d.sketch_text.stroke-109"),sQuery(id+"FHMxAyK4CFUKdhS_1.wireOp",EDGE,"1cb9c079-ea9b-4899-8069-e0e3048e911d.sketch_text.stroke-110"),sQuery(id+"FHMxAyK4CFUKdhS_1.wireOp",EDGE,"1cb9c079-ea9b-4899-8069-e0e3048e911d.sketch_text.stroke-111"),sQuery(id+"FHMxAyK4CFUKdhS_1.wireOp",EDGE,"1cb9c079-ea9b-4899-8069-e0e3048e911d.sketch_text.stroke-112"),sQuery(id+"FHMxAyK4CFUKdhS_1.wireOp",EDGE,"1cb9c079-ea9b-4899-8069-e0e3048e911d.sketch_text.stroke-113"),sQuery(id+"FHMxAyK4CFUKdhS_1.wireOp",EDGE,"1cb9c079-ea9b-4899-8069-e0e3048e911d.sketch_text.stroke-114"),sQuery(id+"FHMxAyK4CFUKdhS_1.wireOp",EDGE,"1cb9c079-ea9b-4899-8069-e0e3048e911d.sketch_text.stroke-115"),sQuery(id+"FHMxAyK4CFUKdhS_1.wireOp",EDGE,"1cb9c079-ea9b-4899-8069-e0e3048e911d.sketch_text.stroke-116"),sQuery(id+"FHMxAyK4CFUKdhS_1.wireOp",EDGE,"1cb9c079-ea9b-4899-8069-e0e3048e911d.sketch_text.stroke-117"),sQuery(id+"FHMxAyK4CFUKdhS_1.wireOp",EDGE,"1cb9c079-ea9b-4899-8069-e0e3048e911d.sketch_text.stroke-118"),sQuery(id+"FHMxAyK4CFUKdhS_1.wireOp",EDGE,"1cb9c079-ea9b-4899-8069-e0e3048e911d.sketch_text.stroke-119"),sQuery(id+"FHMxAyK4CFUKdhS_1.wireOp",EDGE,"1cb9c079-ea9b-4899-8069-e0e3048e911d.sketch_text.stroke-120"),sQuery(id+"FHMxAyK4CFUKdhS_1.wireOp",EDGE,"1cb9c079-ea9b-4899-8069-e0e3048e911d.sketch_text.stroke-121"),sQuery(id+"FHMxAyK4CFUKdhS_1.wireOp",EDGE,"1cb9c079-ea9b-4899-8069-e0e3048e911d.sketch_text.stroke-122"),sQuery(id+"FHMxAyK4CFUKdhS_1.wireOp",EDGE,"1cb9c079-ea9b-4899-8069-e0e3048e911d.sketch_text.stroke-123"),sQuery(id+"FHMxAyK4CFUKdhS_1.wireOp",EDGE,"1cb9c079-ea9b-4899-8069-e0e3048e911d.sketch_text.stroke-124"),sQuery(id+"FHMxAyK4CFUKdhS_1.wireOp",EDGE,"1cb9c079-ea9b-4899-8069-e0e3048e911d.sketch_text.stroke-125"),sQuery(id+"FHMxAyK4CFUKdhS_1.wireOp",EDGE,"1cb9c079-ea9b-4899-8069-e0e3048e911d.sketch_text.stroke-126"),sQuery(id+"FHMxAyK4CFUKdhS_1.wireOp",EDGE,"1cb9c079-ea9b-4899-8069-e0e3048e911d.sketch_text.stroke-127"),sQuery(id+"FHMxAyK4CFUKdhS_1.wireOp",EDGE,"1cb9c079-ea9b-4899-8069-e0e3048e911d.sketch_text.stroke-128"),sQuery(id+"FHMxAyK4CFUKdhS_1.wireOp",EDGE,"1cb9c079-ea9b-4899-8069-e0e3048e911d.sketch_text.stroke-129"),sQuery(id+"FHMxAyK4CFUKdhS_1.wireOp",EDGE,"1cb9c079-ea9b-4899-8069-e0e3048e911d.sketch_text.stroke-130"),sQuery(id+"FHMxAyK4CFUKdhS_1.wireOp",EDGE,"1cb9c079-ea9b-4899-8069-e0e3048e911d.sketch_text.stroke-131"),sQuery(id+"FHMxAyK4CFUKdhS_1.wireOp",EDGE,"1cb9c079-ea9b-4899-8069-e0e3048e911d.sketch_text.stroke-132"),sQuery(id+"FHMxAyK4CFUKdhS_1.wireOp",EDGE,"1cb9c079-ea9b-4899-8069-e0e3048e911d.sketch_text.stroke-133"),sQuery(id+"FHMxAyK4CFUKdhS_1.wireOp",EDGE,"1cb9c079-ea9b-4899-8069-e0e3048e911d.sketch_text.stroke-134"),sQuery(id+"FHMxAyK4CFUKdhS_1.wireOp",EDGE,"1cb9c079-ea9b-4899-8069-e0e3048e911d.sketch_text.stroke-135"),sQuery(id+"FHMxAyK4CFUKdhS_1.wireOp",EDGE,"1cb9c079-ea9b-4899-8069-e0e3048e911d.sketch_text.stroke-136"),sQuery(id+"FHMxAyK4CFUKdhS_1.wireOp",EDGE,"1cb9c079-ea9b-4899-8069-e0e3048e911d.sketch_text.stroke-137"),sQuery(id+"FHMxAyK4CFUKdhS_1.wireOp",EDGE,"1cb9c079-ea9b-4899-8069-e0e3048e911d.sketch_text.stroke-138"),sQuery(id+"FHMxAyK4CFUKdhS_1.wireOp",EDGE,"1cb9c079-ea9b-4899-8069-e0e3048e911d.sketch_text.stroke-139"),sQuery(id+"FHMxAyK4CFUKdhS_1.wireOp",EDGE,"1cb9c079-ea9b-4899-8069-e0e3048e911d.sketch_text.stroke-140"),sQuery(id+"FHMxAyK4CFUKdhS_1.wireOp",EDGE,"1cb9c079-ea9b-4899-8069-e0e3048e911d.sketch_text.stroke-141"),sQuery(id+"FHMxAyK4CFUKdhS_1.wireOp",EDGE,"1cb9c079-ea9b-4899-8069-e0e3048e911d.sketch_text.stroke-142"),sQuery(id+"FHMxAyK4CFUKdhS_1.wireOp",EDGE,"1cb9c079-ea9b-4899-8069-e0e3048e911d.sketch_text.stroke-143"),sQuery(id+"FHMxAyK4CFUKdhS_1.wireOp",EDGE,"1cb9c079-ea9b-4899-8069-e0e3048e911d.sketch_text.stroke-144"),sQuery(id+"FHMxAyK4CFUKdhS_1.wireOp",EDGE,"1cb9c079-ea9b-4899-8069-e0e3048e911d.sketch_text.stroke-145"),sQuery(id+"FHMxAyK4CFUKdhS_1.wireOp",EDGE,"1cb9c079-ea9b-4899-8069-e0e3048e911d.sketch_text.stroke-146"),sQuery(id+"FHMxAyK4CFUKdhS_1.wireOp",EDGE,"1cb9c079-ea9b-4899-8069-e0e3048e911d.sketch_text.stroke-147"),sQuery(id+"FHMxAyK4CFUKdhS_1.wireOp",EDGE,"1cb9c079-ea9b-4899-8069-e0e3048e911d.sketch_text.stroke-148"),sQuery(id+"FHMxAyK4CFUKdhS_1.wireOp",EDGE,"1cb9c079-ea9b-4899-8069-e0e3048e911d.sketch_text.stroke-149"),sQuery(id+"FHMxAyK4CFUKdhS_1.wireOp",EDGE,"1cb9c079-ea9b-4899-8069-e0e3048e911d.sketch_text.stroke-150"),sQuery(id+"FHMxAyK4CFUKdhS_1.wireOp",EDGE,"1cb9c079-ea9b-4899-8069-e0e3048e911d.sketch_text.stroke-151"),sQuery(id+"FHMxAyK4CFUKdhS_1.wireOp",EDGE,"1cb9c079-ea9b-4899-8069-e0e3048e911d.sketch_text.stroke-152"),sQuery(id+"FHMxAyK4CFUKdhS_1.wireOp",EDGE,"1cb9c079-ea9b-4899-8069-e0e3048e911d.sketch_text.stroke-153"),sQuery(id+"FHMxAyK4CFUKdhS_1.wireOp",EDGE,"1cb9c079-ea9b-4899-8069-e0e3048e911d.sketch_text.stroke-159"),sQuery(id+"FHMxAyK4CFUKdhS_1.wireOp",EDGE,"1cb9c079-ea9b-4899-8069-e0e3048e911d.sketch_text.stroke-160"),sQuery(id+"FHMxAyK4CFUKdhS_1.wireOp",EDGE,"1cb9c079-ea9b-4899-8069-e0e3048e911d.sketch_text.stroke-161"),sQuery(id+"FHMxAyK4CFUKdhS_1.wireOp",EDGE,"1cb9c079-ea9b-4899-8069-e0e3048e911d.sketch_text.stroke-162"),sQuery(id+"FHMxAyK4CFUKdhS_1.wireOp",EDGE,"1cb9c079-ea9b-4899-8069-e0e3048e911d.sketch_text.stroke-163"),sQuery(id+"FHMxAyK4CFUKdhS_1.wireOp",EDGE,"1cb9c079-ea9b-4899-8069-e0e3048e911d.sketch_text.stroke-164"),sQuery(id+"FHMxAyK4CFUKdhS_1.wireOp",EDGE,"1cb9c079-ea9b-4899-8069-e0e3048e911d.sketch_text.stroke-165"),sQuery(id+"FHMxAyK4CFUKdhS_1.wireOp",EDGE,"1cb9c079-ea9b-4899-8069-e0e3048e911d.sketch_text.stroke-166"),sQuery(id+"FHMxAyK4CFUKdhS_1.wireOp",EDGE,"1cb9c079-ea9b-4899-8069-e0e3048e911d.sketch_text.stroke-167"),sQuery(id+"FHMxAyK4CFUKdhS_1.wireOp",EDGE,"1cb9c079-ea9b-4899-8069-e0e3048e911d.sketch_text.stroke-168"),sQuery(id+"FHMxAyK4CFUKdhS_1.wireOp",EDGE,"1cb9c079-ea9b-4899-8069-e0e3048e911d.sketch_text.stroke-169"),sQuery(id+"FHMxAyK4CFUKdhS_1.wireOp",EDGE,"1cb9c079-ea9b-4899-8069-e0e3048e911d.sketch_text.stroke-170"),sQuery(id+"FHMxAyK4CFUKdhS_1.wireOp",EDGE,"1cb9c079-ea9b-4899-8069-e0e3048e911d.sketch_text.stroke-171"),sQuery(id+"FHMxAyK4CFUKdhS_1.wireOp",EDGE,"1cb9c079-ea9b-4899-8069-e0e3048e911d.sketch_text.stroke-172"),sQuery(id+"FHMxAyK4CFUKdhS_1.wireOp",EDGE,"1cb9c079-ea9b-4899-8069-e0e3048e911d.sketch_text.stroke-173"),sQuery(id+"FHMxAyK4CFUKdhS_1.wireOp",EDGE,"1cb9c079-ea9b-4899-8069-e0e3048e911d.sketch_text.stroke-174"),sQuery(id+"FHMxAyK4CFUKdhS_1.wireOp",EDGE,"1cb9c079-ea9b-4899-8069-e0e3048e911d.sketch_text.stroke-175"),sQuery(id+"FHMxAyK4CFUKdhS_1.wireOp",EDGE,"1cb9c079-ea9b-4899-8069-e0e3048e911d.sketch_text.stroke-176"),sQuery(id+"FHMxAyK4CFUKdhS_1.wireOp",EDGE,"1cb9c079-ea9b-4899-8069-e0e3048e911d.sketch_text.stroke-177"),sQuery(id+"FHMxAyK4CFUKdhS_1.wireOp",EDGE,"1cb9c079-ea9b-4899-8069-e0e3048e911d.sketch_text.stroke-178"),sQuery(id+"FHMxAyK4CFUKdhS_1.wireOp",EDGE,"1cb9c079-ea9b-4899-8069-e0e3048e911d.sketch_text.stroke-179"),sQuery(id+"FHMxAyK4CFUKdhS_1.wireOp",EDGE,"1cb9c079-ea9b-4899-8069-e0e3048e911d.sketch_text.stroke-180"),subQ0,subQ2])],"isStart":true}),makeQuery(id+"F4.opExtrude","SWEPT_FACE",FACE,{"disambiguationData":[OSD([subQ2])]})])],"derivedFrom":makeQuery(id+"F4.opExtrude","CAP_EDGE",EDGE,{"disambiguationData":[OSD([subQ2])],"isStart":true})});}
            var Q16;
            {var subQ0=sQuery(id+"F0.wireOp",EDGE,"E0.top");var subQ1=sQuery(id+"F0.wireOp",EDGE,"E0.bottom");var subQ2=sQuery(id+"F3.wireOp",EDGE,"727ac2c1-f511-4829-95a7-a443ef16a4cd");Q16=makeQuery(id+"F4.boolean.opBoolean","SPLIT",EDGE,{"disambiguationData":[TD([makeQuery(id+"F1.opExtrude","CAP_FACE",FACE,{"disambiguationData":[OSD([subQ1,subQ0,sQuery(id+"F0.wireOp",EDGE,"E0.left"),sQuery(id+"F0.wireOp",EDGE,"E0.right")])],"isStart":false}),makeQuery(id+"F1.opExtrude","SWEPT_FACE",FACE,{"disambiguationData":[OSD([subQ0])]}),makeQuery(id+"F4.opExtrude","CAP_FACE",FACE,{"disambiguationData":[OSD([subQ1,sQuery(id+"F2.wireOp",EDGE,"fcba4419-a2ee-464f-be9d-58f11bf3418b.sketch_text.stroke-0"),sQuery(id+"F2.wireOp",EDGE,"fcba4419-a2ee-464f-be9d-58f11bf3418b.sketch_text.stroke-1"),sQuery(id+"F2.wireOp",EDGE,"fcba4419-a2ee-464f-be9d-58f11bf3418b.sketch_text.stroke-2"),sQuery(id+"F2.wireOp",EDGE,"fcba4419-a2ee-464f-be9d-58f11bf3418b.sketch_text.stroke-3"),sQuery(id+"F2.wireOp",EDGE,"fcba4419-a2ee-464f-be9d-58f11bf3418b.sketch_text.stroke-4"),sQuery(id+"F2.wireOp",EDGE,"fcba4419-a2ee-464f-be9d-58f11bf3418b.sketch_text.stroke-5"),sQuery(id+"F2.wireOp",EDGE,"fcba4419-a2ee-464f-be9d-58f11bf3418b.sketch_text.stroke-6"),sQuery(id+"F2.wireOp",EDGE,"fcba4419-a2ee-464f-be9d-58f11bf3418b.sketch_text.stroke-7"),sQuery(id+"F2.wireOp",EDGE,"fcba4419-a2ee-464f-be9d-58f11bf3418b.sketch_text.stroke-8"),sQuery(id+"F2.wireOp",EDGE,"fcba4419-a2ee-464f-be9d-58f11bf3418b.sketch_text.stroke-9"),sQuery(id+"F2.wireOp",EDGE,"fcba4419-a2ee-464f-be9d-58f11bf3418b.sketch_text.stroke-10"),sQuery(id+"F2.wireOp",EDGE,"fcba4419-a2ee-464f-be9d-58f11bf3418b.sketch_text.stroke-11"),sQuery(id+"F2.wireOp",EDGE,"fcba4419-a2ee-464f-be9d-58f11bf3418b.sketch_text.stroke-12"),sQuery(id+"F2.wireOp",EDGE,"fcba4419-a2ee-464f-be9d-58f11bf3418b.sketch_text.stroke-13"),sQuery(id+"F2.wireOp",EDGE,"fcba4419-a2ee-464f-be9d-58f11bf3418b.sketch_text.stroke-14"),sQuery(id+"F2.wireOp",EDGE,"fcba4419-a2ee-464f-be9d-58f11bf3418b.sketch_text.stroke-15"),sQuery(id+"F2.wireOp",EDGE,"fcba4419-a2ee-464f-be9d-58f11bf3418b.sketch_text.stroke-16"),sQuery(id+"F2.wireOp",EDGE,"fcba4419-a2ee-464f-be9d-58f11bf3418b.sketch_text.stroke-17"),sQuery(id+"F2.wireOp",EDGE,"fcba4419-a2ee-464f-be9d-58f11bf3418b.sketch_text.stroke-18"),sQuery(id+"F2.wireOp",EDGE,"fcba4419-a2ee-464f-be9d-58f11bf3418b.sketch_text.stroke-19"),sQuery(id+"F2.wireOp",EDGE,"fcba4419-a2ee-464f-be9d-58f11bf3418b.sketch_text.stroke-20"),sQuery(id+"F2.wireOp",EDGE,"fcba4419-a2ee-464f-be9d-58f11bf3418b.sketch_text.stroke-21"),sQuery(id+"F2.wireOp",EDGE,"fcba4419-a2ee-464f-be9d-58f11bf3418b.sketch_text.stroke-22"),sQuery(id+"F2.wireOp",EDGE,"fcba4419-a2ee-464f-be9d-58f11bf3418b.sketch_text.stroke-23"),sQuery(id+"F2.wireOp",EDGE,"fcba4419-a2ee-464f-be9d-58f11bf3418b.sketch_text.stroke-24"),sQuery(id+"F2.wireOp",EDGE,"fcba4419-a2ee-464f-be9d-58f11bf3418b.sketch_text.stroke-25"),sQuery(id+"F2.wireOp",EDGE,"fcba4419-a2ee-464f-be9d-58f11bf3418b.sketch_text.stroke-26"),sQuery(id+"F2.wireOp",EDGE,"fcba4419-a2ee-464f-be9d-58f11bf3418b.sketch_text.stroke-27"),sQuery(id+"F2.wireOp",EDGE,"fcba4419-a2ee-464f-be9d-58f11bf3418b.sketch_text.stroke-28"),sQuery(id+"F2.wireOp",EDGE,"fcba4419-a2ee-464f-be9d-58f11bf3418b.sketch_text.stroke-29"),sQuery(id+"F2.wireOp",EDGE,"fcba4419-a2ee-464f-be9d-58f11bf3418b.sketch_text.stroke-30"),sQuery(id+"F2.wireOp",EDGE,"fcba4419-a2ee-464f-be9d-58f11bf3418b.sketch_text.stroke-31"),sQuery(id+"F2.wireOp",EDGE,"fcba4419-a2ee-464f-be9d-58f11bf3418b.sketch_text.stroke-32"),sQuery(id+"F2.wireOp",EDGE,"fcba4419-a2ee-464f-be9d-58f11bf3418b.sketch_text.stroke-33"),sQuery(id+"F2.wireOp",EDGE,"fcba4419-a2ee-464f-be9d-58f11bf3418b.sketch_text.stroke-34"),sQuery(id+"F2.wireOp",EDGE,"fcba4419-a2ee-464f-be9d-58f11bf3418b.sketch_text.stroke-35"),sQuery(id+"F2.wireOp",EDGE,"fcba4419-a2ee-464f-be9d-58f11bf3418b.sketch_text.stroke-36"),sQuery(id+"F2.wireOp",EDGE,"fcba4419-a2ee-464f-be9d-58f11bf3418b.sketch_text.stroke-37"),sQuery(id+"F2.wireOp",EDGE,"fcba4419-a2ee-464f-be9d-58f11bf3418b.sketch_text.stroke-38"),sQuery(id+"F2.wireOp",EDGE,"fcba4419-a2ee-464f-be9d-58f11bf3418b.sketch_text.stroke-39"),sQuery(id+"F2.wireOp",EDGE,"fcba4419-a2ee-464f-be9d-58f11bf3418b.sketch_text.stroke-40"),sQuery(id+"F2.wireOp",EDGE,"fcba4419-a2ee-464f-be9d-58f11bf3418b.sketch_text.stroke-41"),sQuery(id+"F2.wireOp",EDGE,"fcba4419-a2ee-464f-be9d-58f11bf3418b.sketch_text.stroke-42"),sQuery(id+"F2.wireOp",EDGE,"fcba4419-a2ee-464f-be9d-58f11bf3418b.sketch_text.stroke-43"),sQuery(id+"F2.wireOp",EDGE,"fcba4419-a2ee-464f-be9d-58f11bf3418b.sketch_text.stroke-44"),sQuery(id+"F2.wireOp",EDGE,"fcba4419-a2ee-464f-be9d-58f11bf3418b.sketch_text.stroke-45"),sQuery(id+"F2.wireOp",EDGE,"fcba4419-a2ee-464f-be9d-58f11bf3418b.sketch_text.stroke-46"),sQuery(id+"F2.wireOp",EDGE,"fcba4419-a2ee-464f-be9d-58f11bf3418b.sketch_text.stroke-47"),sQuery(id+"F2.wireOp",EDGE,"fcba4419-a2ee-464f-be9d-58f11bf3418b.sketch_text.stroke-48"),sQuery(id+"F2.wireOp",EDGE,"fcba4419-a2ee-464f-be9d-58f11bf3418b.sketch_text.stroke-49"),sQuery(id+"F2.wireOp",EDGE,"fcba4419-a2ee-464f-be9d-58f11bf3418b.sketch_text.stroke-50"),sQuery(id+"F2.wireOp",EDGE,"fcba4419-a2ee-464f-be9d-58f11bf3418b.sketch_text.stroke-51"),sQuery(id+"F2.wireOp",EDGE,"fcba4419-a2ee-464f-be9d-58f11bf3418b.sketch_text.stroke-52"),sQuery(id+"F2.wireOp",EDGE,"fcba4419-a2ee-464f-be9d-58f11bf3418b.sketch_text.stroke-53"),sQuery(id+"F2.wireOp",EDGE,"fcba4419-a2ee-464f-be9d-58f11bf3418b.sketch_text.stroke-54"),sQuery(id+"F2.wireOp",EDGE,"fcba4419-a2ee-464f-be9d-58f11bf3418b.sketch_text.stroke-55"),sQuery(id+"F2.wireOp",EDGE,"fcba4419-a2ee-464f-be9d-58f11bf3418b.sketch_text.stroke-56"),sQuery(id+"F2.wireOp",EDGE,"fcba4419-a2ee-464f-be9d-58f11bf3418b.sketch_text.stroke-57"),sQuery(id+"F2.wireOp",EDGE,"fcba4419-a2ee-464f-be9d-58f11bf3418b.sketch_text.stroke-58"),sQuery(id+"F2.wireOp",EDGE,"fcba4419-a2ee-464f-be9d-58f11bf3418b.sketch_text.stroke-59"),sQuery(id+"F2.wireOp",EDGE,"fcba4419-a2ee-464f-be9d-58f11bf3418b.sketch_text.stroke-60"),sQuery(id+"F2.wireOp",EDGE,"fcba4419-a2ee-464f-be9d-58f11bf3418b.sketch_text.stroke-61"),sQuery(id+"F2.wireOp",EDGE,"fcba4419-a2ee-464f-be9d-58f11bf3418b.sketch_text.stroke-62"),sQuery(id+"F2.wireOp",EDGE,"fcba4419-a2ee-464f-be9d-58f11bf3418b.sketch_text.stroke-63"),sQuery(id+"F2.wireOp",EDGE,"fcba4419-a2ee-464f-be9d-58f11bf3418b.sketch_text.stroke-64"),sQuery(id+"F2.wireOp",EDGE,"fcba4419-a2ee-464f-be9d-58f11bf3418b.sketch_text.stroke-65"),sQuery(id+"F2.wireOp",EDGE,"fcba4419-a2ee-464f-be9d-58f11bf3418b.sketch_text.stroke-66"),sQuery(id+"F2.wireOp",EDGE,"fcba4419-a2ee-464f-be9d-58f11bf3418b.sketch_text.stroke-67"),sQuery(id+"F2.wireOp",EDGE,"fcba4419-a2ee-464f-be9d-58f11bf3418b.sketch_text.stroke-68"),sQuery(id+"F2.wireOp",EDGE,"fcba4419-a2ee-464f-be9d-58f11bf3418b.sketch_text.stroke-69"),sQuery(id+"F2.wireOp",EDGE,"fcba4419-a2ee-464f-be9d-58f11bf3418b.sketch_text.stroke-70"),sQuery(id+"F2.wireOp",EDGE,"fcba4419-a2ee-464f-be9d-58f11bf3418b.sketch_text.stroke-71"),sQuery(id+"F2.wireOp",EDGE,"fcba4419-a2ee-464f-be9d-58f11bf3418b.sketch_text.stroke-72"),sQuery(id+"F2.wireOp",EDGE,"fcba4419-a2ee-464f-be9d-58f11bf3418b.sketch_text.stroke-73"),sQuery(id+"F2.wireOp",EDGE,"fcba4419-a2ee-464f-be9d-58f11bf3418b.sketch_text.stroke-74"),sQuery(id+"F2.wireOp",EDGE,"fcba4419-a2ee-464f-be9d-58f11bf3418b.sketch_text.stroke-75"),sQuery(id+"F2.wireOp",EDGE,"fcba4419-a2ee-464f-be9d-58f11bf3418b.sketch_text.stroke-76"),sQuery(id+"F2.wireOp",EDGE,"fcba4419-a2ee-464f-be9d-58f11bf3418b.sketch_text.stroke-77"),sQuery(id+"F2.wireOp",EDGE,"fcba4419-a2ee-464f-be9d-58f11bf3418b.sketch_text.stroke-78"),sQuery(id+"F2.wireOp",EDGE,"fcba4419-a2ee-464f-be9d-58f11bf3418b.sketch_text.stroke-79"),sQuery(id+"F2.wireOp",EDGE,"fcba4419-a2ee-464f-be9d-58f11bf3418b.sketch_text.stroke-80"),sQuery(id+"F2.wireOp",EDGE,"fcba4419-a2ee-464f-be9d-58f11bf3418b.sketch_text.stroke-81"),sQuery(id+"F2.wireOp",EDGE,"fcba4419-a2ee-464f-be9d-58f11bf3418b.sketch_text.stroke-82"),sQuery(id+"F2.wireOp",EDGE,"fcba4419-a2ee-464f-be9d-58f11bf3418b.sketch_text.stroke-83"),sQuery(id+"F2.wireOp",EDGE,"fcba4419-a2ee-464f-be9d-58f11bf3418b.sketch_text.stroke-84"),sQuery(id+"F2.wireOp",EDGE,"fcba4419-a2ee-464f-be9d-58f11bf3418b.sketch_text.stroke-85"),sQuery(id+"F2.wireOp",EDGE,"fcba4419-a2ee-464f-be9d-58f11bf3418b.sketch_text.stroke-86"),sQuery(id+"F2.wireOp",EDGE,"fcba4419-a2ee-464f-be9d-58f11bf3418b.sketch_text.stroke-87"),sQuery(id+"F2.wireOp",EDGE,"fcba4419-a2ee-464f-be9d-58f11bf3418b.sketch_text.stroke-88"),sQuery(id+"F2.wireOp",EDGE,"fcba4419-a2ee-464f-be9d-58f11bf3418b.sketch_text.stroke-89"),sQuery(id+"F2.wireOp",EDGE,"fcba4419-a2ee-464f-be9d-58f11bf3418b.sketch_text.stroke-90"),sQuery(id+"F2.wireOp",EDGE,"fcba4419-a2ee-464f-be9d-58f11bf3418b.sketch_text.stroke-91"),sQuery(id+"F2.wireOp",EDGE,"fcba4419-a2ee-464f-be9d-58f11bf3418b.sketch_text.stroke-92"),sQuery(id+"F2.wireOp",EDGE,"fcba4419-a2ee-464f-be9d-58f11bf3418b.sketch_text.stroke-93"),sQuery(id+"F2.wireOp",EDGE,"fcba4419-a2ee-464f-be9d-58f11bf3418b.sketch_text.stroke-94"),sQuery(id+"F2.wireOp",EDGE,"fcba4419-a2ee-464f-be9d-58f11bf3418b.sketch_text.stroke-95"),sQuery(id+"F2.wireOp",EDGE,"fcba4419-a2ee-464f-be9d-58f11bf3418b.sketch_text.stroke-96"),sQuery(id+"F2.wireOp",EDGE,"fcba4419-a2ee-464f-be9d-58f11bf3418b.sketch_text.stroke-97"),sQuery(id+"F2.wireOp",EDGE,"fcba4419-a2ee-464f-be9d-58f11bf3418b.sketch_text.stroke-98"),sQuery(id+"F2.wireOp",EDGE,"fcba4419-a2ee-464f-be9d-58f11bf3418b.sketch_text.stroke-99"),sQuery(id+"F2.wireOp",EDGE,"fcba4419-a2ee-464f-be9d-58f11bf3418b.sketch_text.stroke-100"),sQuery(id+"F2.wireOp",EDGE,"fcba4419-a2ee-464f-be9d-58f11bf3418b.sketch_text.stroke-101"),sQuery(id+"F2.wireOp",EDGE,"fcba4419-a2ee-464f-be9d-58f11bf3418b.sketch_text.stroke-102"),sQuery(id+"F2.wireOp",EDGE,"fcba4419-a2ee-464f-be9d-58f11bf3418b.sketch_text.stroke-103"),sQuery(id+"F2.wireOp",EDGE,"fcba4419-a2ee-464f-be9d-58f11bf3418b.sketch_text.stroke-104"),sQuery(id+"F2.wireOp",EDGE,"fcba4419-a2ee-464f-be9d-58f11bf3418b.sketch_text.stroke-105"),sQuery(id+"F2.wireOp",EDGE,"fcba4419-a2ee-464f-be9d-58f11bf3418b.sketch_text.stroke-106"),sQuery(id+"F2.wireOp",EDGE,"fcba4419-a2ee-464f-be9d-58f11bf3418b.sketch_text.stroke-107"),sQuery(id+"F2.wireOp",EDGE,"fcba4419-a2ee-464f-be9d-58f11bf3418b.sketch_text.stroke-108"),sQuery(id+"F2.wireOp",EDGE,"fcba4419-a2ee-464f-be9d-58f11bf3418b.sketch_text.stroke-109"),sQuery(id+"F2.wireOp",EDGE,"fcba4419-a2ee-464f-be9d-58f11bf3418b.sketch_text.stroke-110"),sQuery(id+"F2.wireOp",EDGE,"fcba4419-a2ee-464f-be9d-58f11bf3418b.sketch_text.stroke-111"),sQuery(id+"F2.wireOp",EDGE,"fcba4419-a2ee-464f-be9d-58f11bf3418b.sketch_text.stroke-112"),sQuery(id+"F2.wireOp",EDGE,"fcba4419-a2ee-464f-be9d-58f11bf3418b.sketch_text.stroke-113"),sQuery(id+"F2.wireOp",EDGE,"fcba4419-a2ee-464f-be9d-58f11bf3418b.sketch_text.stroke-114"),sQuery(id+"F2.wireOp",EDGE,"fcba4419-a2ee-464f-be9d-58f11bf3418b.sketch_text.stroke-115"),sQuery(id+"F2.wireOp",EDGE,"fcba4419-a2ee-464f-be9d-58f11bf3418b.sketch_text.stroke-116"),sQuery(id+"F2.wireOp",EDGE,"fcba4419-a2ee-464f-be9d-58f11bf3418b.sketch_text.stroke-117"),sQuery(id+"F2.wireOp",EDGE,"fcba4419-a2ee-464f-be9d-58f11bf3418b.sketch_text.stroke-118"),sQuery(id+"F2.wireOp",EDGE,"fcba4419-a2ee-464f-be9d-58f11bf3418b.sketch_text.stroke-119"),sQuery(id+"F2.wireOp",EDGE,"fcba4419-a2ee-464f-be9d-58f11bf3418b.sketch_text.stroke-120"),sQuery(id+"F2.wireOp",EDGE,"fcba4419-a2ee-464f-be9d-58f11bf3418b.sketch_text.stroke-121"),sQuery(id+"F2.wireOp",EDGE,"fcba4419-a2ee-464f-be9d-58f11bf3418b.sketch_text.stroke-122"),sQuery(id+"F2.wireOp",EDGE,"fcba4419-a2ee-464f-be9d-58f11bf3418b.sketch_text.stroke-123"),sQuery(id+"F2.wireOp",EDGE,"fcba4419-a2ee-464f-be9d-58f11bf3418b.sketch_text.stroke-124"),sQuery(id+"F2.wireOp",EDGE,"fcba4419-a2ee-464f-be9d-58f11bf3418b.sketch_text.stroke-125"),sQuery(id+"F2.wireOp",EDGE,"fcba4419-a2ee-464f-be9d-58f11bf3418b.sketch_text.stroke-126"),sQuery(id+"F2.wireOp",EDGE,"fcba4419-a2ee-464f-be9d-58f11bf3418b.sketch_text.stroke-127"),sQuery(id+"F2.wireOp",EDGE,"fcba4419-a2ee-464f-be9d-58f11bf3418b.sketch_text.stroke-128"),sQuery(id+"F2.wireOp",EDGE,"fcba4419-a2ee-464f-be9d-58f11bf3418b.sketch_text.stroke-129"),sQuery(id+"F2.wireOp",EDGE,"fcba4419-a2ee-464f-be9d-58f11bf3418b.sketch_text.stroke-130"),sQuery(id+"F2.wireOp",EDGE,"fcba4419-a2ee-464f-be9d-58f11bf3418b.sketch_text.stroke-131"),sQuery(id+"F2.wireOp",EDGE,"fcba4419-a2ee-464f-be9d-58f11bf3418b.sketch_text.stroke-132"),sQuery(id+"F2.wireOp",EDGE,"fcba4419-a2ee-464f-be9d-58f11bf3418b.sketch_text.stroke-133"),sQuery(id+"F2.wireOp",EDGE,"fcba4419-a2ee-464f-be9d-58f11bf3418b.sketch_text.stroke-134"),sQuery(id+"F2.wireOp",EDGE,"fcba4419-a2ee-464f-be9d-58f11bf3418b.sketch_text.stroke-135"),sQuery(id+"F2.wireOp",EDGE,"fcba4419-a2ee-464f-be9d-58f11bf3418b.sketch_text.stroke-136"),sQuery(id+"F2.wireOp",EDGE,"fcba4419-a2ee-464f-be9d-58f11bf3418b.sketch_text.stroke-137"),sQuery(id+"F2.wireOp",EDGE,"fcba4419-a2ee-464f-be9d-58f11bf3418b.sketch_text.stroke-138"),sQuery(id+"F2.wireOp",EDGE,"fcba4419-a2ee-464f-be9d-58f11bf3418b.sketch_text.stroke-139"),sQuery(id+"F2.wireOp",EDGE,"fcba4419-a2ee-464f-be9d-58f11bf3418b.sketch_text.stroke-140"),sQuery(id+"F2.wireOp",EDGE,"fcba4419-a2ee-464f-be9d-58f11bf3418b.sketch_text.stroke-141"),sQuery(id+"F2.wireOp",EDGE,"fcba4419-a2ee-464f-be9d-58f11bf3418b.sketch_text.stroke-142"),sQuery(id+"F2.wireOp",EDGE,"fcba4419-a2ee-464f-be9d-58f11bf3418b.sketch_text.stroke-143"),sQuery(id+"F2.wireOp",EDGE,"fcba4419-a2ee-464f-be9d-58f11bf3418b.sketch_text.stroke-144"),sQuery(id+"F2.wireOp",EDGE,"fcba4419-a2ee-464f-be9d-58f11bf3418b.sketch_text.stroke-145"),sQuery(id+"F2.wireOp",EDGE,"fcba4419-a2ee-464f-be9d-58f11bf3418b.sketch_text.stroke-146"),sQuery(id+"F2.wireOp",EDGE,"fcba4419-a2ee-464f-be9d-58f11bf3418b.sketch_text.stroke-147"),sQuery(id+"F2.wireOp",EDGE,"fcba4419-a2ee-464f-be9d-58f11bf3418b.sketch_text.stroke-148"),sQuery(id+"F2.wireOp",EDGE,"fcba4419-a2ee-464f-be9d-58f11bf3418b.sketch_text.stroke-149"),sQuery(id+"F2.wireOp",EDGE,"fcba4419-a2ee-464f-be9d-58f11bf3418b.sketch_text.stroke-150"),sQuery(id+"F2.wireOp",EDGE,"fcba4419-a2ee-464f-be9d-58f11bf3418b.sketch_text.stroke-151"),sQuery(id+"F2.wireOp",EDGE,"fcba4419-a2ee-464f-be9d-58f11bf3418b.sketch_text.stroke-152"),sQuery(id+"F2.wireOp",EDGE,"fcba4419-a2ee-464f-be9d-58f11bf3418b.sketch_text.stroke-153"),sQuery(id+"F2.wireOp",EDGE,"fcba4419-a2ee-464f-be9d-58f11bf3418b.sketch_text.stroke-154"),sQuery(id+"F2.wireOp",EDGE,"fcba4419-a2ee-464f-be9d-58f11bf3418b.sketch_text.stroke-155"),sQuery(id+"F2.wireOp",EDGE,"fcba4419-a2ee-464f-be9d-58f11bf3418b.sketch_text.stroke-156"),sQuery(id+"F2.wireOp",EDGE,"fcba4419-a2ee-464f-be9d-58f11bf3418b.sketch_text.stroke-157"),sQuery(id+"F2.wireOp",EDGE,"fcba4419-a2ee-464f-be9d-58f11bf3418b.sketch_text.stroke-158"),sQuery(id+"F2.wireOp",EDGE,"fcba4419-a2ee-464f-be9d-58f11bf3418b.sketch_text.stroke-159"),sQuery(id+"F2.wireOp",EDGE,"fcba4419-a2ee-464f-be9d-58f11bf3418b.sketch_text.stroke-160"),sQuery(id+"F2.wireOp",EDGE,"fcba4419-a2ee-464f-be9d-58f11bf3418b.sketch_text.stroke-161"),sQuery(id+"F2.wireOp",EDGE,"fcba4419-a2ee-464f-be9d-58f11bf3418b.sketch_text.stroke-162"),sQuery(id+"F2.wireOp",EDGE,"fcba4419-a2ee-464f-be9d-58f11bf3418b.sketch_text.stroke-163"),sQuery(id+"F2.wireOp",EDGE,"fcba4419-a2ee-464f-be9d-58f11bf3418b.sketch_text.stroke-164"),sQuery(id+"F2.wireOp",EDGE,"fcba4419-a2ee-464f-be9d-58f11bf3418b.sketch_text.stroke-165"),sQuery(id+"F2.wireOp",EDGE,"fcba4419-a2ee-464f-be9d-58f11bf3418b.sketch_text.stroke-166"),sQuery(id+"F2.wireOp",EDGE,"fcba4419-a2ee-464f-be9d-58f11bf3418b.sketch_text.stroke-167"),sQuery(id+"F2.wireOp",EDGE,"fcba4419-a2ee-464f-be9d-58f11bf3418b.sketch_text.stroke-168"),sQuery(id+"F2.wireOp",EDGE,"fcba4419-a2ee-464f-be9d-58f11bf3418b.sketch_text.stroke-169"),sQuery(id+"F2.wireOp",EDGE,"fcba4419-a2ee-464f-be9d-58f11bf3418b.sketch_text.stroke-170"),sQuery(id+"F2.wireOp",EDGE,"fcba4419-a2ee-464f-be9d-58f11bf3418b.sketch_text.stroke-171"),sQuery(id+"F2.wireOp",EDGE,"fcba4419-a2ee-464f-be9d-58f11bf3418b.sketch_text.stroke-172"),sQuery(id+"F2.wireOp",EDGE,"fcba4419-a2ee-464f-be9d-58f11bf3418b.sketch_text.stroke-173"),sQuery(id+"FHMxAyK4CFUKdhS_1.wireOp",EDGE,"1cb9c079-ea9b-4899-8069-e0e3048e911d.sketch_text.stroke-0"),sQuery(id+"FHMxAyK4CFUKdhS_1.wireOp",EDGE,"1cb9c079-ea9b-4899-8069-e0e3048e911d.sketch_text.stroke-1"),sQuery(id+"FHMxAyK4CFUKdhS_1.wireOp",EDGE,"1cb9c079-ea9b-4899-8069-e0e3048e911d.sketch_text.stroke-2"),sQuery(id+"FHMxAyK4CFUKdhS_1.wireOp",EDGE,"1cb9c079-ea9b-4899-8069-e0e3048e911d.sketch_text.stroke-3"),sQuery(id+"FHMxAyK4CFUKdhS_1.wireOp",EDGE,"1cb9c079-ea9b-4899-8069-e0e3048e911d.sketch_text.stroke-4"),sQuery(id+"FHMxAyK4CFUKdhS_1.wireOp",EDGE,"1cb9c079-ea9b-4899-8069-e0e3048e911d.sketch_text.stroke-5"),sQuery(id+"FHMxAyK4CFUKdhS_1.wireOp",EDGE,"1cb9c079-ea9b-4899-8069-e0e3048e911d.sketch_text.stroke-6"),sQuery(id+"FHMxAyK4CFUKdhS_1.wireOp",EDGE,"1cb9c079-ea9b-4899-8069-e0e3048e911d.sketch_text.stroke-7"),sQuery(id+"FHMxAyK4CFUKdhS_1.wireOp",EDGE,"1cb9c079-ea9b-4899-8069-e0e3048e911d.sketch_text.stroke-8"),sQuery(id+"FHMxAyK4CFUKdhS_1.wireOp",EDGE,"1cb9c079-ea9b-4899-8069-e0e3048e911d.sketch_text.stroke-9"),sQuery(id+"FHMxAyK4CFUKdhS_1.wireOp",EDGE,"1cb9c079-ea9b-4899-8069-e0e3048e911d.sketch_text.stroke-10"),sQuery(id+"FHMxAyK4CFUKdhS_1.wireOp",EDGE,"1cb9c079-ea9b-4899-8069-e0e3048e911d.sketch_text.stroke-11"),sQuery(id+"FHMxAyK4CFUKdhS_1.wireOp",EDGE,"1cb9c079-ea9b-4899-8069-e0e3048e911d.sketch_text.stroke-12"),sQuery(id+"FHMxAyK4CFUKdhS_1.wireOp",EDGE,"1cb9c079-ea9b-4899-8069-e0e3048e911d.sketch_text.stroke-13"),sQuery(id+"FHMxAyK4CFUKdhS_1.wireOp",EDGE,"1cb9c079-ea9b-4899-8069-e0e3048e911d.sketch_text.stroke-14"),sQuery(id+"FHMxAyK4CFUKdhS_1.wireOp",EDGE,"1cb9c079-ea9b-4899-8069-e0e3048e911d.sketch_text.stroke-15"),sQuery(id+"FHMxAyK4CFUKdhS_1.wireOp",EDGE,"1cb9c079-ea9b-4899-8069-e0e3048e911d.sketch_text.stroke-16"),sQuery(id+"FHMxAyK4CFUKdhS_1.wireOp",EDGE,"1cb9c079-ea9b-4899-8069-e0e3048e911d.sketch_text.stroke-17"),sQuery(id+"FHMxAyK4CFUKdhS_1.wireOp",EDGE,"1cb9c079-ea9b-4899-8069-e0e3048e911d.sketch_text.stroke-18"),sQuery(id+"FHMxAyK4CFUKdhS_1.wireOp",EDGE,"1cb9c079-ea9b-4899-8069-e0e3048e911d.sketch_text.stroke-19"),sQuery(id+"FHMxAyK4CFUKdhS_1.wireOp",EDGE,"1cb9c079-ea9b-4899-8069-e0e3048e911d.sketch_text.stroke-20"),sQuery(id+"FHMxAyK4CFUKdhS_1.wireOp",EDGE,"1cb9c079-ea9b-4899-8069-e0e3048e911d.sketch_text.stroke-21"),sQuery(id+"FHMxAyK4CFUKdhS_1.wireOp",EDGE,"1cb9c079-ea9b-4899-8069-e0e3048e911d.sketch_text.stroke-22"),sQuery(id+"FHMxAyK4CFUKdhS_1.wireOp",EDGE,"1cb9c079-ea9b-4899-8069-e0e3048e911d.sketch_text.stroke-23"),sQuery(id+"FHMxAyK4CFUKdhS_1.wireOp",EDGE,"1cb9c079-ea9b-4899-8069-e0e3048e911d.sketch_text.stroke-24"),sQuery(id+"FHMxAyK4CFUKdhS_1.wireOp",EDGE,"1cb9c079-ea9b-4899-8069-e0e3048e911d.sketch_text.stroke-25"),sQuery(id+"FHMxAyK4CFUKdhS_1.wireOp",EDGE,"1cb9c079-ea9b-4899-8069-e0e3048e911d.sketch_text.stroke-26"),sQuery(id+"FHMxAyK4CFUKdhS_1.wireOp",EDGE,"1cb9c079-ea9b-4899-8069-e0e3048e911d.sketch_text.stroke-27"),sQuery(id+"FHMxAyK4CFUKdhS_1.wireOp",EDGE,"1cb9c079-ea9b-4899-8069-e0e3048e911d.sketch_text.stroke-28"),sQuery(id+"FHMxAyK4CFUKdhS_1.wireOp",EDGE,"1cb9c079-ea9b-4899-8069-e0e3048e911d.sketch_text.stroke-29"),sQuery(id+"FHMxAyK4CFUKdhS_1.wireOp",EDGE,"1cb9c079-ea9b-4899-8069-e0e3048e911d.sketch_text.stroke-30"),sQuery(id+"FHMxAyK4CFUKdhS_1.wireOp",EDGE,"1cb9c079-ea9b-4899-8069-e0e3048e911d.sketch_text.stroke-31"),sQuery(id+"FHMxAyK4CFUKdhS_1.wireOp",EDGE,"1cb9c079-ea9b-4899-8069-e0e3048e911d.sketch_text.stroke-32"),sQuery(id+"FHMxAyK4CFUKdhS_1.wireOp",EDGE,"1cb9c079-ea9b-4899-8069-e0e3048e911d.sketch_text.stroke-33"),sQuery(id+"FHMxAyK4CFUKdhS_1.wireOp",EDGE,"1cb9c079-ea9b-4899-8069-e0e3048e911d.sketch_text.stroke-34"),sQuery(id+"FHMxAyK4CFUKdhS_1.wireOp",EDGE,"1cb9c079-ea9b-4899-8069-e0e3048e911d.sketch_text.stroke-35"),sQuery(id+"FHMxAyK4CFUKdhS_1.wireOp",EDGE,"1cb9c079-ea9b-4899-8069-e0e3048e911d.sketch_text.stroke-36"),sQuery(id+"FHMxAyK4CFUKdhS_1.wireOp",EDGE,"1cb9c079-ea9b-4899-8069-e0e3048e911d.sketch_text.stroke-37"),sQuery(id+"FHMxAyK4CFUKdhS_1.wireOp",EDGE,"1cb9c079-ea9b-4899-8069-e0e3048e911d.sketch_text.stroke-38"),sQuery(id+"FHMxAyK4CFUKdhS_1.wireOp",EDGE,"1cb9c079-ea9b-4899-8069-e0e3048e911d.sketch_text.stroke-39"),sQuery(id+"FHMxAyK4CFUKdhS_1.wireOp",EDGE,"1cb9c079-ea9b-4899-8069-e0e3048e911d.sketch_text.stroke-40"),sQuery(id+"FHMxAyK4CFUKdhS_1.wireOp",EDGE,"1cb9c079-ea9b-4899-8069-e0e3048e911d.sketch_text.stroke-41"),sQuery(id+"FHMxAyK4CFUKdhS_1.wireOp",EDGE,"1cb9c079-ea9b-4899-8069-e0e3048e911d.sketch_text.stroke-42"),sQuery(id+"FHMxAyK4CFUKdhS_1.wireOp",EDGE,"1cb9c079-ea9b-4899-8069-e0e3048e911d.sketch_text.stroke-43"),sQuery(id+"FHMxAyK4CFUKdhS_1.wireOp",EDGE,"1cb9c079-ea9b-4899-8069-e0e3048e911d.sketch_text.stroke-44"),sQuery(id+"FHMxAyK4CFUKdhS_1.wireOp",EDGE,"1cb9c079-ea9b-4899-8069-e0e3048e911d.sketch_text.stroke-45"),sQuery(id+"FHMxAyK4CFUKdhS_1.wireOp",EDGE,"1cb9c079-ea9b-4899-8069-e0e3048e911d.sketch_text.stroke-46"),sQuery(id+"FHMxAyK4CFUKdhS_1.wireOp",EDGE,"1cb9c079-ea9b-4899-8069-e0e3048e911d.sketch_text.stroke-47"),sQuery(id+"FHMxAyK4CFUKdhS_1.wireOp",EDGE,"1cb9c079-ea9b-4899-8069-e0e3048e911d.sketch_text.stroke-48"),sQuery(id+"FHMxAyK4CFUKdhS_1.wireOp",EDGE,"1cb9c079-ea9b-4899-8069-e0e3048e911d.sketch_text.stroke-49"),sQuery(id+"FHMxAyK4CFUKdhS_1.wireOp",EDGE,"1cb9c079-ea9b-4899-8069-e0e3048e911d.sketch_text.stroke-50"),sQuery(id+"FHMxAyK4CFUKdhS_1.wireOp",EDGE,"1cb9c079-ea9b-4899-8069-e0e3048e911d.sketch_text.stroke-51"),sQuery(id+"FHMxAyK4CFUKdhS_1.wireOp",EDGE,"1cb9c079-ea9b-4899-8069-e0e3048e911d.sketch_text.stroke-52"),sQuery(id+"FHMxAyK4CFUKdhS_1.wireOp",EDGE,"1cb9c079-ea9b-4899-8069-e0e3048e911d.sketch_text.stroke-53"),sQuery(id+"FHMxAyK4CFUKdhS_1.wireOp",EDGE,"1cb9c079-ea9b-4899-8069-e0e3048e911d.sketch_text.stroke-54"),sQuery(id+"FHMxAyK4CFUKdhS_1.wireOp",EDGE,"1cb9c079-ea9b-4899-8069-e0e3048e911d.sketch_text.stroke-55"),sQuery(id+"FHMxAyK4CFUKdhS_1.wireOp",EDGE,"1cb9c079-ea9b-4899-8069-e0e3048e911d.sketch_text.stroke-56"),sQuery(id+"FHMxAyK4CFUKdhS_1.wireOp",EDGE,"1cb9c079-ea9b-4899-8069-e0e3048e911d.sketch_text.stroke-57"),sQuery(id+"FHMxAyK4CFUKdhS_1.wireOp",EDGE,"1cb9c079-ea9b-4899-8069-e0e3048e911d.sketch_text.stroke-58"),sQuery(id+"FHMxAyK4CFUKdhS_1.wireOp",EDGE,"1cb9c079-ea9b-4899-8069-e0e3048e911d.sketch_text.stroke-59"),sQuery(id+"FHMxAyK4CFUKdhS_1.wireOp",EDGE,"1cb9c079-ea9b-4899-8069-e0e3048e911d.sketch_text.stroke-60"),sQuery(id+"FHMxAyK4CFUKdhS_1.wireOp",EDGE,"1cb9c079-ea9b-4899-8069-e0e3048e911d.sketch_text.stroke-61"),sQuery(id+"FHMxAyK4CFUKdhS_1.wireOp",EDGE,"1cb9c079-ea9b-4899-8069-e0e3048e911d.sketch_text.stroke-62"),sQuery(id+"FHMxAyK4CFUKdhS_1.wireOp",EDGE,"1cb9c079-ea9b-4899-8069-e0e3048e911d.sketch_text.stroke-71"),sQuery(id+"FHMxAyK4CFUKdhS_1.wireOp",EDGE,"1cb9c079-ea9b-4899-8069-e0e3048e911d.sketch_text.stroke-72"),sQuery(id+"FHMxAyK4CFUKdhS_1.wireOp",EDGE,"1cb9c079-ea9b-4899-8069-e0e3048e911d.sketch_text.stroke-73"),sQuery(id+"FHMxAyK4CFUKdhS_1.wireOp",EDGE,"1cb9c079-ea9b-4899-8069-e0e3048e911d.sketch_text.stroke-74"),sQuery(id+"FHMxAyK4CFUKdhS_1.wireOp",EDGE,"1cb9c079-ea9b-4899-8069-e0e3048e911d.sketch_text.stroke-75"),sQuery(id+"FHMxAyK4CFUKdhS_1.wireOp",EDGE,"1cb9c079-ea9b-4899-8069-e0e3048e911d.sketch_text.stroke-76"),sQuery(id+"FHMxAyK4CFUKdhS_1.wireOp",EDGE,"1cb9c079-ea9b-4899-8069-e0e3048e911d.sketch_text.stroke-77"),sQuery(id+"FHMxAyK4CFUKdhS_1.wireOp",EDGE,"1cb9c079-ea9b-4899-8069-e0e3048e911d.sketch_text.stroke-78"),sQuery(id+"FHMxAyK4CFUKdhS_1.wireOp",EDGE,"1cb9c079-ea9b-4899-8069-e0e3048e911d.sketch_text.stroke-79"),sQuery(id+"FHMxAyK4CFUKdhS_1.wireOp",EDGE,"1cb9c079-ea9b-4899-8069-e0e3048e911d.sketch_text.stroke-80"),sQuery(id+"FHMxAyK4CFUKdhS_1.wireOp",EDGE,"1cb9c079-ea9b-4899-8069-e0e3048e911d.sketch_text.stroke-81"),sQuery(id+"FHMxAyK4CFUKdhS_1.wireOp",EDGE,"1cb9c079-ea9b-4899-8069-e0e3048e911d.sketch_text.stroke-82"),sQuery(id+"FHMxAyK4CFUKdhS_1.wireOp",EDGE,"1cb9c079-ea9b-4899-8069-e0e3048e911d.sketch_text.stroke-83"),sQuery(id+"FHMxAyK4CFUKdhS_1.wireOp",EDGE,"1cb9c079-ea9b-4899-8069-e0e3048e911d.sketch_text.stroke-84"),sQuery(id+"FHMxAyK4CFUKdhS_1.wireOp",EDGE,"1cb9c079-ea9b-4899-8069-e0e3048e911d.sketch_text.stroke-85"),sQuery(id+"FHMxAyK4CFUKdhS_1.wireOp",EDGE,"1cb9c079-ea9b-4899-8069-e0e3048e911d.sketch_text.stroke-86"),sQuery(id+"FHMxAyK4CFUKdhS_1.wireOp",EDGE,"1cb9c079-ea9b-4899-8069-e0e3048e911d.sketch_text.stroke-87"),sQuery(id+"FHMxAyK4CFUKdhS_1.wireOp",EDGE,"1cb9c079-ea9b-4899-8069-e0e3048e911d.sketch_text.stroke-88"),sQuery(id+"FHMxAyK4CFUKdhS_1.wireOp",EDGE,"1cb9c079-ea9b-4899-8069-e0e3048e911d.sketch_text.stroke-89"),sQuery(id+"FHMxAyK4CFUKdhS_1.wireOp",EDGE,"1cb9c079-ea9b-4899-8069-e0e3048e911d.sketch_text.stroke-90"),sQuery(id+"FHMxAyK4CFUKdhS_1.wireOp",EDGE,"1cb9c079-ea9b-4899-8069-e0e3048e911d.sketch_text.stroke-91"),sQuery(id+"FHMxAyK4CFUKdhS_1.wireOp",EDGE,"1cb9c079-ea9b-4899-8069-e0e3048e911d.sketch_text.stroke-92"),sQuery(id+"FHMxAyK4CFUKdhS_1.wireOp",EDGE,"1cb9c079-ea9b-4899-8069-e0e3048e911d.sketch_text.stroke-93"),sQuery(id+"FHMxAyK4CFUKdhS_1.wireOp",EDGE,"1cb9c079-ea9b-4899-8069-e0e3048e911d.sketch_text.stroke-94"),sQuery(id+"FHMxAyK4CFUKdhS_1.wireOp",EDGE,"1cb9c079-ea9b-4899-8069-e0e3048e911d.sketch_text.stroke-95"),sQuery(id+"FHMxAyK4CFUKdhS_1.wireOp",EDGE,"1cb9c079-ea9b-4899-8069-e0e3048e911d.sketch_text.stroke-96"),sQuery(id+"FHMxAyK4CFUKdhS_1.wireOp",EDGE,"1cb9c079-ea9b-4899-8069-e0e3048e911d.sketch_text.stroke-97"),sQuery(id+"FHMxAyK4CFUKdhS_1.wireOp",EDGE,"1cb9c079-ea9b-4899-8069-e0e3048e911d.sketch_text.stroke-103"),sQuery(id+"FHMxAyK4CFUKdhS_1.wireOp",EDGE,"1cb9c079-ea9b-4899-8069-e0e3048e911d.sketch_text.stroke-104"),sQuery(id+"FHMxAyK4CFUKdhS_1.wireOp",EDGE,"1cb9c079-ea9b-4899-8069-e0e3048e911d.sketch_text.stroke-105"),sQuery(id+"FHMxAyK4CFUKdhS_1.wireOp",EDGE,"1cb9c079-ea9b-4899-8069-e0e3048e911d.sketch_text.stroke-106"),sQuery(id+"FHMxAyK4CFUKdhS_1.wireOp",EDGE,"1cb9c079-ea9b-4899-8069-e0e3048e911d.sketch_text.stroke-107"),sQuery(id+"FHMxAyK4CFUKdhS_1.wireOp",EDGE,"1cb9c079-ea9b-4899-8069-e0e3048e911d.sketch_text.stroke-108"),sQuery(id+"FHMxAyK4CFUKdhS_1.wireOp",EDGE,"1cb9c079-ea9b-4899-8069-e0e3048e911d.sketch_text.stroke-109"),sQuery(id+"FHMxAyK4CFUKdhS_1.wireOp",EDGE,"1cb9c079-ea9b-4899-8069-e0e3048e911d.sketch_text.stroke-110"),sQuery(id+"FHMxAyK4CFUKdhS_1.wireOp",EDGE,"1cb9c079-ea9b-4899-8069-e0e3048e911d.sketch_text.stroke-111"),sQuery(id+"FHMxAyK4CFUKdhS_1.wireOp",EDGE,"1cb9c079-ea9b-4899-8069-e0e3048e911d.sketch_text.stroke-112"),sQuery(id+"FHMxAyK4CFUKdhS_1.wireOp",EDGE,"1cb9c079-ea9b-4899-8069-e0e3048e911d.sketch_text.stroke-113"),sQuery(id+"FHMxAyK4CFUKdhS_1.wireOp",EDGE,"1cb9c079-ea9b-4899-8069-e0e3048e911d.sketch_text.stroke-114"),sQuery(id+"FHMxAyK4CFUKdhS_1.wireOp",EDGE,"1cb9c079-ea9b-4899-8069-e0e3048e911d.sketch_text.stroke-115"),sQuery(id+"FHMxAyK4CFUKdhS_1.wireOp",EDGE,"1cb9c079-ea9b-4899-8069-e0e3048e911d.sketch_text.stroke-116"),sQuery(id+"FHMxAyK4CFUKdhS_1.wireOp",EDGE,"1cb9c079-ea9b-4899-8069-e0e3048e911d.sketch_text.stroke-117"),sQuery(id+"FHMxAyK4CFUKdhS_1.wireOp",EDGE,"1cb9c079-ea9b-4899-8069-e0e3048e911d.sketch_text.stroke-118"),sQuery(id+"FHMxAyK4CFUKdhS_1.wireOp",EDGE,"1cb9c079-ea9b-4899-8069-e0e3048e911d.sketch_text.stroke-119"),sQuery(id+"FHMxAyK4CFUKdhS_1.wireOp",EDGE,"1cb9c079-ea9b-4899-8069-e0e3048e911d.sketch_text.stroke-120"),sQuery(id+"FHMxAyK4CFUKdhS_1.wireOp",EDGE,"1cb9c079-ea9b-4899-8069-e0e3048e911d.sketch_text.stroke-121"),sQuery(id+"FHMxAyK4CFUKdhS_1.wireOp",EDGE,"1cb9c079-ea9b-4899-8069-e0e3048e911d.sketch_text.stroke-122"),sQuery(id+"FHMxAyK4CFUKdhS_1.wireOp",EDGE,"1cb9c079-ea9b-4899-8069-e0e3048e911d.sketch_text.stroke-123"),sQuery(id+"FHMxAyK4CFUKdhS_1.wireOp",EDGE,"1cb9c079-ea9b-4899-8069-e0e3048e911d.sketch_text.stroke-124"),sQuery(id+"FHMxAyK4CFUKdhS_1.wireOp",EDGE,"1cb9c079-ea9b-4899-8069-e0e3048e911d.sketch_text.stroke-125"),sQuery(id+"FHMxAyK4CFUKdhS_1.wireOp",EDGE,"1cb9c079-ea9b-4899-8069-e0e3048e911d.sketch_text.stroke-126"),sQuery(id+"FHMxAyK4CFUKdhS_1.wireOp",EDGE,"1cb9c079-ea9b-4899-8069-e0e3048e911d.sketch_text.stroke-127"),sQuery(id+"FHMxAyK4CFUKdhS_1.wireOp",EDGE,"1cb9c079-ea9b-4899-8069-e0e3048e911d.sketch_text.stroke-128"),sQuery(id+"FHMxAyK4CFUKdhS_1.wireOp",EDGE,"1cb9c079-ea9b-4899-8069-e0e3048e911d.sketch_text.stroke-129"),sQuery(id+"FHMxAyK4CFUKdhS_1.wireOp",EDGE,"1cb9c079-ea9b-4899-8069-e0e3048e911d.sketch_text.stroke-130"),sQuery(id+"FHMxAyK4CFUKdhS_1.wireOp",EDGE,"1cb9c079-ea9b-4899-8069-e0e3048e911d.sketch_text.stroke-131"),sQuery(id+"FHMxAyK4CFUKdhS_1.wireOp",EDGE,"1cb9c079-ea9b-4899-8069-e0e3048e911d.sketch_text.stroke-132"),sQuery(id+"FHMxAyK4CFUKdhS_1.wireOp",EDGE,"1cb9c079-ea9b-4899-8069-e0e3048e911d.sketch_text.stroke-133"),sQuery(id+"FHMxAyK4CFUKdhS_1.wireOp",EDGE,"1cb9c079-ea9b-4899-8069-e0e3048e911d.sketch_text.stroke-134"),sQuery(id+"FHMxAyK4CFUKdhS_1.wireOp",EDGE,"1cb9c079-ea9b-4899-8069-e0e3048e911d.sketch_text.stroke-135"),sQuery(id+"FHMxAyK4CFUKdhS_1.wireOp",EDGE,"1cb9c079-ea9b-4899-8069-e0e3048e911d.sketch_text.stroke-136"),sQuery(id+"FHMxAyK4CFUKdhS_1.wireOp",EDGE,"1cb9c079-ea9b-4899-8069-e0e3048e911d.sketch_text.stroke-137"),sQuery(id+"FHMxAyK4CFUKdhS_1.wireOp",EDGE,"1cb9c079-ea9b-4899-8069-e0e3048e911d.sketch_text.stroke-138"),sQuery(id+"FHMxAyK4CFUKdhS_1.wireOp",EDGE,"1cb9c079-ea9b-4899-8069-e0e3048e911d.sketch_text.stroke-139"),sQuery(id+"FHMxAyK4CFUKdhS_1.wireOp",EDGE,"1cb9c079-ea9b-4899-8069-e0e3048e911d.sketch_text.stroke-140"),sQuery(id+"FHMxAyK4CFUKdhS_1.wireOp",EDGE,"1cb9c079-ea9b-4899-8069-e0e3048e911d.sketch_text.stroke-141"),sQuery(id+"FHMxAyK4CFUKdhS_1.wireOp",EDGE,"1cb9c079-ea9b-4899-8069-e0e3048e911d.sketch_text.stroke-142"),sQuery(id+"FHMxAyK4CFUKdhS_1.wireOp",EDGE,"1cb9c079-ea9b-4899-8069-e0e3048e911d.sketch_text.stroke-143"),sQuery(id+"FHMxAyK4CFUKdhS_1.wireOp",EDGE,"1cb9c079-ea9b-4899-8069-e0e3048e911d.sketch_text.stroke-144"),sQuery(id+"FHMxAyK4CFUKdhS_1.wireOp",EDGE,"1cb9c079-ea9b-4899-8069-e0e3048e911d.sketch_text.stroke-145"),sQuery(id+"FHMxAyK4CFUKdhS_1.wireOp",EDGE,"1cb9c079-ea9b-4899-8069-e0e3048e911d.sketch_text.stroke-146"),sQuery(id+"FHMxAyK4CFUKdhS_1.wireOp",EDGE,"1cb9c079-ea9b-4899-8069-e0e3048e911d.sketch_text.stroke-147"),sQuery(id+"FHMxAyK4CFUKdhS_1.wireOp",EDGE,"1cb9c079-ea9b-4899-8069-e0e3048e911d.sketch_text.stroke-148"),sQuery(id+"FHMxAyK4CFUKdhS_1.wireOp",EDGE,"1cb9c079-ea9b-4899-8069-e0e3048e911d.sketch_text.stroke-149"),sQuery(id+"FHMxAyK4CFUKdhS_1.wireOp",EDGE,"1cb9c079-ea9b-4899-8069-e0e3048e911d.sketch_text.stroke-150"),sQuery(id+"FHMxAyK4CFUKdhS_1.wireOp",EDGE,"1cb9c079-ea9b-4899-8069-e0e3048e911d.sketch_text.stroke-151"),sQuery(id+"FHMxAyK4CFUKdhS_1.wireOp",EDGE,"1cb9c079-ea9b-4899-8069-e0e3048e911d.sketch_text.stroke-152"),sQuery(id+"FHMxAyK4CFUKdhS_1.wireOp",EDGE,"1cb9c079-ea9b-4899-8069-e0e3048e911d.sketch_text.stroke-153"),sQuery(id+"FHMxAyK4CFUKdhS_1.wireOp",EDGE,"1cb9c079-ea9b-4899-8069-e0e3048e911d.sketch_text.stroke-159"),sQuery(id+"FHMxAyK4CFUKdhS_1.wireOp",EDGE,"1cb9c079-ea9b-4899-8069-e0e3048e911d.sketch_text.stroke-160"),sQuery(id+"FHMxAyK4CFUKdhS_1.wireOp",EDGE,"1cb9c079-ea9b-4899-8069-e0e3048e911d.sketch_text.stroke-161"),sQuery(id+"FHMxAyK4CFUKdhS_1.wireOp",EDGE,"1cb9c079-ea9b-4899-8069-e0e3048e911d.sketch_text.stroke-162"),sQuery(id+"FHMxAyK4CFUKdhS_1.wireOp",EDGE,"1cb9c079-ea9b-4899-8069-e0e3048e911d.sketch_text.stroke-163"),sQuery(id+"FHMxAyK4CFUKdhS_1.wireOp",EDGE,"1cb9c079-ea9b-4899-8069-e0e3048e911d.sketch_text.stroke-164"),sQuery(id+"FHMxAyK4CFUKdhS_1.wireOp",EDGE,"1cb9c079-ea9b-4899-8069-e0e3048e911d.sketch_text.stroke-165"),sQuery(id+"FHMxAyK4CFUKdhS_1.wireOp",EDGE,"1cb9c079-ea9b-4899-8069-e0e3048e911d.sketch_text.stroke-166"),sQuery(id+"FHMxAyK4CFUKdhS_1.wireOp",EDGE,"1cb9c079-ea9b-4899-8069-e0e3048e911d.sketch_text.stroke-167"),sQuery(id+"FHMxAyK4CFUKdhS_1.wireOp",EDGE,"1cb9c079-ea9b-4899-8069-e0e3048e911d.sketch_text.stroke-168"),sQuery(id+"FHMxAyK4CFUKdhS_1.wireOp",EDGE,"1cb9c079-ea9b-4899-8069-e0e3048e911d.sketch_text.stroke-169"),sQuery(id+"FHMxAyK4CFUKdhS_1.wireOp",EDGE,"1cb9c079-ea9b-4899-8069-e0e3048e911d.sketch_text.stroke-170"),sQuery(id+"FHMxAyK4CFUKdhS_1.wireOp",EDGE,"1cb9c079-ea9b-4899-8069-e0e3048e911d.sketch_text.stroke-171"),sQuery(id+"FHMxAyK4CFUKdhS_1.wireOp",EDGE,"1cb9c079-ea9b-4899-8069-e0e3048e911d.sketch_text.stroke-172"),sQuery(id+"FHMxAyK4CFUKdhS_1.wireOp",EDGE,"1cb9c079-ea9b-4899-8069-e0e3048e911d.sketch_text.stroke-173"),sQuery(id+"FHMxAyK4CFUKdhS_1.wireOp",EDGE,"1cb9c079-ea9b-4899-8069-e0e3048e911d.sketch_text.stroke-174"),sQuery(id+"FHMxAyK4CFUKdhS_1.wireOp",EDGE,"1cb9c079-ea9b-4899-8069-e0e3048e911d.sketch_text.stroke-175"),sQuery(id+"FHMxAyK4CFUKdhS_1.wireOp",EDGE,"1cb9c079-ea9b-4899-8069-e0e3048e911d.sketch_text.stroke-176"),sQuery(id+"FHMxAyK4CFUKdhS_1.wireOp",EDGE,"1cb9c079-ea9b-4899-8069-e0e3048e911d.sketch_text.stroke-177"),sQuery(id+"FHMxAyK4CFUKdhS_1.wireOp",EDGE,"1cb9c079-ea9b-4899-8069-e0e3048e911d.sketch_text.stroke-178"),sQuery(id+"FHMxAyK4CFUKdhS_1.wireOp",EDGE,"1cb9c079-ea9b-4899-8069-e0e3048e911d.sketch_text.stroke-179"),sQuery(id+"FHMxAyK4CFUKdhS_1.wireOp",EDGE,"1cb9c079-ea9b-4899-8069-e0e3048e911d.sketch_text.stroke-180"),sQuery(id+"F3.wireOp",EDGE,"8007402e-1a4e-4a06-85a5-2af08e553504"),subQ2])],"isStart":true}),makeQuery(id+"F4.opExtrude","SWEPT_FACE",FACE,{"disambiguationData":[OSD([subQ2])]})]),OD(0.0)],"derivedFrom":makeQuery(id+"F1.opExtrude","CAP_EDGE",EDGE,{"disambiguationData":[OSD([subQ0])],"isStart":false})});}
            var Q17;
            {var subQ0=sQuery(id+"F0.wireOp",EDGE,"E0.top");var subQ1=sQuery(id+"F0.wireOp",EDGE,"E0.bottom");var subQ2=sQuery(id+"F3.wireOp",EDGE,"1a034e28-a7c2-419d-97de-c33d70a47301");Q17=makeQuery(id+"F4.boolean.opBoolean","SPLIT",EDGE,{"disambiguationData":[TD([makeQuery(id+"F1.opExtrude","CAP_FACE",FACE,{"disambiguationData":[OSD([subQ1,subQ0,sQuery(id+"F0.wireOp",EDGE,"E0.left"),sQuery(id+"F0.wireOp",EDGE,"E0.right")])],"isStart":false}),makeQuery(id+"F1.opExtrude","SWEPT_FACE",FACE,{"disambiguationData":[OSD([subQ0])]}),makeQuery(id+"F4.opExtrude","CAP_FACE",FACE,{"disambiguationData":[OSD([subQ1,sQuery(id+"F2.wireOp",EDGE,"fcba4419-a2ee-464f-be9d-58f11bf3418b.sketch_text.stroke-0"),sQuery(id+"F2.wireOp",EDGE,"fcba4419-a2ee-464f-be9d-58f11bf3418b.sketch_text.stroke-1"),sQuery(id+"F2.wireOp",EDGE,"fcba4419-a2ee-464f-be9d-58f11bf3418b.sketch_text.stroke-2"),sQuery(id+"F2.wireOp",EDGE,"fcba4419-a2ee-464f-be9d-58f11bf3418b.sketch_text.stroke-3"),sQuery(id+"F2.wireOp",EDGE,"fcba4419-a2ee-464f-be9d-58f11bf3418b.sketch_text.stroke-4"),sQuery(id+"F2.wireOp",EDGE,"fcba4419-a2ee-464f-be9d-58f11bf3418b.sketch_text.stroke-5"),sQuery(id+"F2.wireOp",EDGE,"fcba4419-a2ee-464f-be9d-58f11bf3418b.sketch_text.stroke-6"),sQuery(id+"F2.wireOp",EDGE,"fcba4419-a2ee-464f-be9d-58f11bf3418b.sketch_text.stroke-7"),sQuery(id+"F2.wireOp",EDGE,"fcba4419-a2ee-464f-be9d-58f11bf3418b.sketch_text.stroke-8"),sQuery(id+"F2.wireOp",EDGE,"fcba4419-a2ee-464f-be9d-58f11bf3418b.sketch_text.stroke-9"),sQuery(id+"F2.wireOp",EDGE,"fcba4419-a2ee-464f-be9d-58f11bf3418b.sketch_text.stroke-10"),sQuery(id+"F2.wireOp",EDGE,"fcba4419-a2ee-464f-be9d-58f11bf3418b.sketch_text.stroke-11"),sQuery(id+"F2.wireOp",EDGE,"fcba4419-a2ee-464f-be9d-58f11bf3418b.sketch_text.stroke-12"),sQuery(id+"F2.wireOp",EDGE,"fcba4419-a2ee-464f-be9d-58f11bf3418b.sketch_text.stroke-13"),sQuery(id+"F2.wireOp",EDGE,"fcba4419-a2ee-464f-be9d-58f11bf3418b.sketch_text.stroke-14"),sQuery(id+"F2.wireOp",EDGE,"fcba4419-a2ee-464f-be9d-58f11bf3418b.sketch_text.stroke-15"),sQuery(id+"F2.wireOp",EDGE,"fcba4419-a2ee-464f-be9d-58f11bf3418b.sketch_text.stroke-16"),sQuery(id+"F2.wireOp",EDGE,"fcba4419-a2ee-464f-be9d-58f11bf3418b.sketch_text.stroke-17"),sQuery(id+"F2.wireOp",EDGE,"fcba4419-a2ee-464f-be9d-58f11bf3418b.sketch_text.stroke-18"),sQuery(id+"F2.wireOp",EDGE,"fcba4419-a2ee-464f-be9d-58f11bf3418b.sketch_text.stroke-19"),sQuery(id+"F2.wireOp",EDGE,"fcba4419-a2ee-464f-be9d-58f11bf3418b.sketch_text.stroke-20"),sQuery(id+"F2.wireOp",EDGE,"fcba4419-a2ee-464f-be9d-58f11bf3418b.sketch_text.stroke-21"),sQuery(id+"F2.wireOp",EDGE,"fcba4419-a2ee-464f-be9d-58f11bf3418b.sketch_text.stroke-22"),sQuery(id+"F2.wireOp",EDGE,"fcba4419-a2ee-464f-be9d-58f11bf3418b.sketch_text.stroke-23"),sQuery(id+"F2.wireOp",EDGE,"fcba4419-a2ee-464f-be9d-58f11bf3418b.sketch_text.stroke-24"),sQuery(id+"F2.wireOp",EDGE,"fcba4419-a2ee-464f-be9d-58f11bf3418b.sketch_text.stroke-25"),sQuery(id+"F2.wireOp",EDGE,"fcba4419-a2ee-464f-be9d-58f11bf3418b.sketch_text.stroke-26"),sQuery(id+"F2.wireOp",EDGE,"fcba4419-a2ee-464f-be9d-58f11bf3418b.sketch_text.stroke-27"),sQuery(id+"F2.wireOp",EDGE,"fcba4419-a2ee-464f-be9d-58f11bf3418b.sketch_text.stroke-28"),sQuery(id+"F2.wireOp",EDGE,"fcba4419-a2ee-464f-be9d-58f11bf3418b.sketch_text.stroke-29"),sQuery(id+"F2.wireOp",EDGE,"fcba4419-a2ee-464f-be9d-58f11bf3418b.sketch_text.stroke-30"),sQuery(id+"F2.wireOp",EDGE,"fcba4419-a2ee-464f-be9d-58f11bf3418b.sketch_text.stroke-31"),sQuery(id+"F2.wireOp",EDGE,"fcba4419-a2ee-464f-be9d-58f11bf3418b.sketch_text.stroke-32"),sQuery(id+"F2.wireOp",EDGE,"fcba4419-a2ee-464f-be9d-58f11bf3418b.sketch_text.stroke-33"),sQuery(id+"F2.wireOp",EDGE,"fcba4419-a2ee-464f-be9d-58f11bf3418b.sketch_text.stroke-34"),sQuery(id+"F2.wireOp",EDGE,"fcba4419-a2ee-464f-be9d-58f11bf3418b.sketch_text.stroke-35"),sQuery(id+"F2.wireOp",EDGE,"fcba4419-a2ee-464f-be9d-58f11bf3418b.sketch_text.stroke-36"),sQuery(id+"F2.wireOp",EDGE,"fcba4419-a2ee-464f-be9d-58f11bf3418b.sketch_text.stroke-37"),sQuery(id+"F2.wireOp",EDGE,"fcba4419-a2ee-464f-be9d-58f11bf3418b.sketch_text.stroke-38"),sQuery(id+"F2.wireOp",EDGE,"fcba4419-a2ee-464f-be9d-58f11bf3418b.sketch_text.stroke-39"),sQuery(id+"F2.wireOp",EDGE,"fcba4419-a2ee-464f-be9d-58f11bf3418b.sketch_text.stroke-40"),sQuery(id+"F2.wireOp",EDGE,"fcba4419-a2ee-464f-be9d-58f11bf3418b.sketch_text.stroke-41"),sQuery(id+"F2.wireOp",EDGE,"fcba4419-a2ee-464f-be9d-58f11bf3418b.sketch_text.stroke-42"),sQuery(id+"F2.wireOp",EDGE,"fcba4419-a2ee-464f-be9d-58f11bf3418b.sketch_text.stroke-43"),sQuery(id+"F2.wireOp",EDGE,"fcba4419-a2ee-464f-be9d-58f11bf3418b.sketch_text.stroke-44"),sQuery(id+"F2.wireOp",EDGE,"fcba4419-a2ee-464f-be9d-58f11bf3418b.sketch_text.stroke-45"),sQuery(id+"F2.wireOp",EDGE,"fcba4419-a2ee-464f-be9d-58f11bf3418b.sketch_text.stroke-46"),sQuery(id+"F2.wireOp",EDGE,"fcba4419-a2ee-464f-be9d-58f11bf3418b.sketch_text.stroke-47"),sQuery(id+"F2.wireOp",EDGE,"fcba4419-a2ee-464f-be9d-58f11bf3418b.sketch_text.stroke-48"),sQuery(id+"F2.wireOp",EDGE,"fcba4419-a2ee-464f-be9d-58f11bf3418b.sketch_text.stroke-49"),sQuery(id+"F2.wireOp",EDGE,"fcba4419-a2ee-464f-be9d-58f11bf3418b.sketch_text.stroke-50"),sQuery(id+"F2.wireOp",EDGE,"fcba4419-a2ee-464f-be9d-58f11bf3418b.sketch_text.stroke-51"),sQuery(id+"F2.wireOp",EDGE,"fcba4419-a2ee-464f-be9d-58f11bf3418b.sketch_text.stroke-52"),sQuery(id+"F2.wireOp",EDGE,"fcba4419-a2ee-464f-be9d-58f11bf3418b.sketch_text.stroke-53"),sQuery(id+"F2.wireOp",EDGE,"fcba4419-a2ee-464f-be9d-58f11bf3418b.sketch_text.stroke-54"),sQuery(id+"F2.wireOp",EDGE,"fcba4419-a2ee-464f-be9d-58f11bf3418b.sketch_text.stroke-55"),sQuery(id+"F2.wireOp",EDGE,"fcba4419-a2ee-464f-be9d-58f11bf3418b.sketch_text.stroke-56"),sQuery(id+"F2.wireOp",EDGE,"fcba4419-a2ee-464f-be9d-58f11bf3418b.sketch_text.stroke-57"),sQuery(id+"F2.wireOp",EDGE,"fcba4419-a2ee-464f-be9d-58f11bf3418b.sketch_text.stroke-58"),sQuery(id+"F2.wireOp",EDGE,"fcba4419-a2ee-464f-be9d-58f11bf3418b.sketch_text.stroke-59"),sQuery(id+"F2.wireOp",EDGE,"fcba4419-a2ee-464f-be9d-58f11bf3418b.sketch_text.stroke-60"),sQuery(id+"F2.wireOp",EDGE,"fcba4419-a2ee-464f-be9d-58f11bf3418b.sketch_text.stroke-61"),sQuery(id+"F2.wireOp",EDGE,"fcba4419-a2ee-464f-be9d-58f11bf3418b.sketch_text.stroke-62"),sQuery(id+"F2.wireOp",EDGE,"fcba4419-a2ee-464f-be9d-58f11bf3418b.sketch_text.stroke-63"),sQuery(id+"F2.wireOp",EDGE,"fcba4419-a2ee-464f-be9d-58f11bf3418b.sketch_text.stroke-64"),sQuery(id+"F2.wireOp",EDGE,"fcba4419-a2ee-464f-be9d-58f11bf3418b.sketch_text.stroke-65"),sQuery(id+"F2.wireOp",EDGE,"fcba4419-a2ee-464f-be9d-58f11bf3418b.sketch_text.stroke-66"),sQuery(id+"F2.wireOp",EDGE,"fcba4419-a2ee-464f-be9d-58f11bf3418b.sketch_text.stroke-67"),sQuery(id+"F2.wireOp",EDGE,"fcba4419-a2ee-464f-be9d-58f11bf3418b.sketch_text.stroke-68"),sQuery(id+"F2.wireOp",EDGE,"fcba4419-a2ee-464f-be9d-58f11bf3418b.sketch_text.stroke-69"),sQuery(id+"F2.wireOp",EDGE,"fcba4419-a2ee-464f-be9d-58f11bf3418b.sketch_text.stroke-70"),sQuery(id+"F2.wireOp",EDGE,"fcba4419-a2ee-464f-be9d-58f11bf3418b.sketch_text.stroke-71"),sQuery(id+"F2.wireOp",EDGE,"fcba4419-a2ee-464f-be9d-58f11bf3418b.sketch_text.stroke-72"),sQuery(id+"F2.wireOp",EDGE,"fcba4419-a2ee-464f-be9d-58f11bf3418b.sketch_text.stroke-73"),sQuery(id+"F2.wireOp",EDGE,"fcba4419-a2ee-464f-be9d-58f11bf3418b.sketch_text.stroke-74"),sQuery(id+"F2.wireOp",EDGE,"fcba4419-a2ee-464f-be9d-58f11bf3418b.sketch_text.stroke-75"),sQuery(id+"F2.wireOp",EDGE,"fcba4419-a2ee-464f-be9d-58f11bf3418b.sketch_text.stroke-76"),sQuery(id+"F2.wireOp",EDGE,"fcba4419-a2ee-464f-be9d-58f11bf3418b.sketch_text.stroke-77"),sQuery(id+"F2.wireOp",EDGE,"fcba4419-a2ee-464f-be9d-58f11bf3418b.sketch_text.stroke-78"),sQuery(id+"F2.wireOp",EDGE,"fcba4419-a2ee-464f-be9d-58f11bf3418b.sketch_text.stroke-79"),sQuery(id+"F2.wireOp",EDGE,"fcba4419-a2ee-464f-be9d-58f11bf3418b.sketch_text.stroke-80"),sQuery(id+"F2.wireOp",EDGE,"fcba4419-a2ee-464f-be9d-58f11bf3418b.sketch_text.stroke-81"),sQuery(id+"F2.wireOp",EDGE,"fcba4419-a2ee-464f-be9d-58f11bf3418b.sketch_text.stroke-82"),sQuery(id+"F2.wireOp",EDGE,"fcba4419-a2ee-464f-be9d-58f11bf3418b.sketch_text.stroke-83"),sQuery(id+"F2.wireOp",EDGE,"fcba4419-a2ee-464f-be9d-58f11bf3418b.sketch_text.stroke-84"),sQuery(id+"F2.wireOp",EDGE,"fcba4419-a2ee-464f-be9d-58f11bf3418b.sketch_text.stroke-85"),sQuery(id+"F2.wireOp",EDGE,"fcba4419-a2ee-464f-be9d-58f11bf3418b.sketch_text.stroke-86"),sQuery(id+"F2.wireOp",EDGE,"fcba4419-a2ee-464f-be9d-58f11bf3418b.sketch_text.stroke-87"),sQuery(id+"F2.wireOp",EDGE,"fcba4419-a2ee-464f-be9d-58f11bf3418b.sketch_text.stroke-88"),sQuery(id+"F2.wireOp",EDGE,"fcba4419-a2ee-464f-be9d-58f11bf3418b.sketch_text.stroke-89"),sQuery(id+"F2.wireOp",EDGE,"fcba4419-a2ee-464f-be9d-58f11bf3418b.sketch_text.stroke-90"),sQuery(id+"F2.wireOp",EDGE,"fcba4419-a2ee-464f-be9d-58f11bf3418b.sketch_text.stroke-91"),sQuery(id+"F2.wireOp",EDGE,"fcba4419-a2ee-464f-be9d-58f11bf3418b.sketch_text.stroke-92"),sQuery(id+"F2.wireOp",EDGE,"fcba4419-a2ee-464f-be9d-58f11bf3418b.sketch_text.stroke-93"),sQuery(id+"F2.wireOp",EDGE,"fcba4419-a2ee-464f-be9d-58f11bf3418b.sketch_text.stroke-94"),sQuery(id+"F2.wireOp",EDGE,"fcba4419-a2ee-464f-be9d-58f11bf3418b.sketch_text.stroke-95"),sQuery(id+"F2.wireOp",EDGE,"fcba4419-a2ee-464f-be9d-58f11bf3418b.sketch_text.stroke-96"),sQuery(id+"F2.wireOp",EDGE,"fcba4419-a2ee-464f-be9d-58f11bf3418b.sketch_text.stroke-97"),sQuery(id+"F2.wireOp",EDGE,"fcba4419-a2ee-464f-be9d-58f11bf3418b.sketch_text.stroke-98"),sQuery(id+"F2.wireOp",EDGE,"fcba4419-a2ee-464f-be9d-58f11bf3418b.sketch_text.stroke-99"),sQuery(id+"F2.wireOp",EDGE,"fcba4419-a2ee-464f-be9d-58f11bf3418b.sketch_text.stroke-100"),sQuery(id+"F2.wireOp",EDGE,"fcba4419-a2ee-464f-be9d-58f11bf3418b.sketch_text.stroke-101"),sQuery(id+"F2.wireOp",EDGE,"fcba4419-a2ee-464f-be9d-58f11bf3418b.sketch_text.stroke-102"),sQuery(id+"F2.wireOp",EDGE,"fcba4419-a2ee-464f-be9d-58f11bf3418b.sketch_text.stroke-103"),sQuery(id+"F2.wireOp",EDGE,"fcba4419-a2ee-464f-be9d-58f11bf3418b.sketch_text.stroke-104"),sQuery(id+"F2.wireOp",EDGE,"fcba4419-a2ee-464f-be9d-58f11bf3418b.sketch_text.stroke-105"),sQuery(id+"F2.wireOp",EDGE,"fcba4419-a2ee-464f-be9d-58f11bf3418b.sketch_text.stroke-106"),sQuery(id+"F2.wireOp",EDGE,"fcba4419-a2ee-464f-be9d-58f11bf3418b.sketch_text.stroke-107"),sQuery(id+"F2.wireOp",EDGE,"fcba4419-a2ee-464f-be9d-58f11bf3418b.sketch_text.stroke-108"),sQuery(id+"F2.wireOp",EDGE,"fcba4419-a2ee-464f-be9d-58f11bf3418b.sketch_text.stroke-109"),sQuery(id+"F2.wireOp",EDGE,"fcba4419-a2ee-464f-be9d-58f11bf3418b.sketch_text.stroke-110"),sQuery(id+"F2.wireOp",EDGE,"fcba4419-a2ee-464f-be9d-58f11bf3418b.sketch_text.stroke-111"),sQuery(id+"F2.wireOp",EDGE,"fcba4419-a2ee-464f-be9d-58f11bf3418b.sketch_text.stroke-112"),sQuery(id+"F2.wireOp",EDGE,"fcba4419-a2ee-464f-be9d-58f11bf3418b.sketch_text.stroke-113"),sQuery(id+"F2.wireOp",EDGE,"fcba4419-a2ee-464f-be9d-58f11bf3418b.sketch_text.stroke-114"),sQuery(id+"F2.wireOp",EDGE,"fcba4419-a2ee-464f-be9d-58f11bf3418b.sketch_text.stroke-115"),sQuery(id+"F2.wireOp",EDGE,"fcba4419-a2ee-464f-be9d-58f11bf3418b.sketch_text.stroke-116"),sQuery(id+"F2.wireOp",EDGE,"fcba4419-a2ee-464f-be9d-58f11bf3418b.sketch_text.stroke-117"),sQuery(id+"F2.wireOp",EDGE,"fcba4419-a2ee-464f-be9d-58f11bf3418b.sketch_text.stroke-118"),sQuery(id+"F2.wireOp",EDGE,"fcba4419-a2ee-464f-be9d-58f11bf3418b.sketch_text.stroke-119"),sQuery(id+"F2.wireOp",EDGE,"fcba4419-a2ee-464f-be9d-58f11bf3418b.sketch_text.stroke-120"),sQuery(id+"F2.wireOp",EDGE,"fcba4419-a2ee-464f-be9d-58f11bf3418b.sketch_text.stroke-121"),sQuery(id+"F2.wireOp",EDGE,"fcba4419-a2ee-464f-be9d-58f11bf3418b.sketch_text.stroke-122"),sQuery(id+"F2.wireOp",EDGE,"fcba4419-a2ee-464f-be9d-58f11bf3418b.sketch_text.stroke-123"),sQuery(id+"F2.wireOp",EDGE,"fcba4419-a2ee-464f-be9d-58f11bf3418b.sketch_text.stroke-124"),sQuery(id+"F2.wireOp",EDGE,"fcba4419-a2ee-464f-be9d-58f11bf3418b.sketch_text.stroke-125"),sQuery(id+"F2.wireOp",EDGE,"fcba4419-a2ee-464f-be9d-58f11bf3418b.sketch_text.stroke-126"),sQuery(id+"F2.wireOp",EDGE,"fcba4419-a2ee-464f-be9d-58f11bf3418b.sketch_text.stroke-127"),sQuery(id+"F2.wireOp",EDGE,"fcba4419-a2ee-464f-be9d-58f11bf3418b.sketch_text.stroke-128"),sQuery(id+"F2.wireOp",EDGE,"fcba4419-a2ee-464f-be9d-58f11bf3418b.sketch_text.stroke-129"),sQuery(id+"F2.wireOp",EDGE,"fcba4419-a2ee-464f-be9d-58f11bf3418b.sketch_text.stroke-130"),sQuery(id+"F2.wireOp",EDGE,"fcba4419-a2ee-464f-be9d-58f11bf3418b.sketch_text.stroke-131"),sQuery(id+"F2.wireOp",EDGE,"fcba4419-a2ee-464f-be9d-58f11bf3418b.sketch_text.stroke-132"),sQuery(id+"F2.wireOp",EDGE,"fcba4419-a2ee-464f-be9d-58f11bf3418b.sketch_text.stroke-133"),sQuery(id+"F2.wireOp",EDGE,"fcba4419-a2ee-464f-be9d-58f11bf3418b.sketch_text.stroke-134"),sQuery(id+"F2.wireOp",EDGE,"fcba4419-a2ee-464f-be9d-58f11bf3418b.sketch_text.stroke-135"),sQuery(id+"F2.wireOp",EDGE,"fcba4419-a2ee-464f-be9d-58f11bf3418b.sketch_text.stroke-136"),sQuery(id+"F2.wireOp",EDGE,"fcba4419-a2ee-464f-be9d-58f11bf3418b.sketch_text.stroke-137"),sQuery(id+"F2.wireOp",EDGE,"fcba4419-a2ee-464f-be9d-58f11bf3418b.sketch_text.stroke-138"),sQuery(id+"F2.wireOp",EDGE,"fcba4419-a2ee-464f-be9d-58f11bf3418b.sketch_text.stroke-139"),sQuery(id+"F2.wireOp",EDGE,"fcba4419-a2ee-464f-be9d-58f11bf3418b.sketch_text.stroke-140"),sQuery(id+"F2.wireOp",EDGE,"fcba4419-a2ee-464f-be9d-58f11bf3418b.sketch_text.stroke-141"),sQuery(id+"F2.wireOp",EDGE,"fcba4419-a2ee-464f-be9d-58f11bf3418b.sketch_text.stroke-142"),sQuery(id+"F2.wireOp",EDGE,"fcba4419-a2ee-464f-be9d-58f11bf3418b.sketch_text.stroke-143"),sQuery(id+"F2.wireOp",EDGE,"fcba4419-a2ee-464f-be9d-58f11bf3418b.sketch_text.stroke-144"),sQuery(id+"F2.wireOp",EDGE,"fcba4419-a2ee-464f-be9d-58f11bf3418b.sketch_text.stroke-145"),sQuery(id+"F2.wireOp",EDGE,"fcba4419-a2ee-464f-be9d-58f11bf3418b.sketch_text.stroke-146"),sQuery(id+"F2.wireOp",EDGE,"fcba4419-a2ee-464f-be9d-58f11bf3418b.sketch_text.stroke-147"),sQuery(id+"F2.wireOp",EDGE,"fcba4419-a2ee-464f-be9d-58f11bf3418b.sketch_text.stroke-148"),sQuery(id+"F2.wireOp",EDGE,"fcba4419-a2ee-464f-be9d-58f11bf3418b.sketch_text.stroke-149"),sQuery(id+"F2.wireOp",EDGE,"fcba4419-a2ee-464f-be9d-58f11bf3418b.sketch_text.stroke-150"),sQuery(id+"F2.wireOp",EDGE,"fcba4419-a2ee-464f-be9d-58f11bf3418b.sketch_text.stroke-151"),sQuery(id+"F2.wireOp",EDGE,"fcba4419-a2ee-464f-be9d-58f11bf3418b.sketch_text.stroke-152"),sQuery(id+"F2.wireOp",EDGE,"fcba4419-a2ee-464f-be9d-58f11bf3418b.sketch_text.stroke-153"),sQuery(id+"F2.wireOp",EDGE,"fcba4419-a2ee-464f-be9d-58f11bf3418b.sketch_text.stroke-154"),sQuery(id+"F2.wireOp",EDGE,"fcba4419-a2ee-464f-be9d-58f11bf3418b.sketch_text.stroke-155"),sQuery(id+"F2.wireOp",EDGE,"fcba4419-a2ee-464f-be9d-58f11bf3418b.sketch_text.stroke-156"),sQuery(id+"F2.wireOp",EDGE,"fcba4419-a2ee-464f-be9d-58f11bf3418b.sketch_text.stroke-157"),sQuery(id+"F2.wireOp",EDGE,"fcba4419-a2ee-464f-be9d-58f11bf3418b.sketch_text.stroke-158"),sQuery(id+"F2.wireOp",EDGE,"fcba4419-a2ee-464f-be9d-58f11bf3418b.sketch_text.stroke-159"),sQuery(id+"F2.wireOp",EDGE,"fcba4419-a2ee-464f-be9d-58f11bf3418b.sketch_text.stroke-160"),sQuery(id+"F2.wireOp",EDGE,"fcba4419-a2ee-464f-be9d-58f11bf3418b.sketch_text.stroke-161"),sQuery(id+"F2.wireOp",EDGE,"fcba4419-a2ee-464f-be9d-58f11bf3418b.sketch_text.stroke-162"),sQuery(id+"F2.wireOp",EDGE,"fcba4419-a2ee-464f-be9d-58f11bf3418b.sketch_text.stroke-163"),sQuery(id+"F2.wireOp",EDGE,"fcba4419-a2ee-464f-be9d-58f11bf3418b.sketch_text.stroke-164"),sQuery(id+"F2.wireOp",EDGE,"fcba4419-a2ee-464f-be9d-58f11bf3418b.sketch_text.stroke-165"),sQuery(id+"F2.wireOp",EDGE,"fcba4419-a2ee-464f-be9d-58f11bf3418b.sketch_text.stroke-166"),sQuery(id+"F2.wireOp",EDGE,"fcba4419-a2ee-464f-be9d-58f11bf3418b.sketch_text.stroke-167"),sQuery(id+"F2.wireOp",EDGE,"fcba4419-a2ee-464f-be9d-58f11bf3418b.sketch_text.stroke-168"),sQuery(id+"F2.wireOp",EDGE,"fcba4419-a2ee-464f-be9d-58f11bf3418b.sketch_text.stroke-169"),sQuery(id+"F2.wireOp",EDGE,"fcba4419-a2ee-464f-be9d-58f11bf3418b.sketch_text.stroke-170"),sQuery(id+"F2.wireOp",EDGE,"fcba4419-a2ee-464f-be9d-58f11bf3418b.sketch_text.stroke-171"),sQuery(id+"F2.wireOp",EDGE,"fcba4419-a2ee-464f-be9d-58f11bf3418b.sketch_text.stroke-172"),sQuery(id+"F2.wireOp",EDGE,"fcba4419-a2ee-464f-be9d-58f11bf3418b.sketch_text.stroke-173"),sQuery(id+"FHMxAyK4CFUKdhS_1.wireOp",EDGE,"1cb9c079-ea9b-4899-8069-e0e3048e911d.sketch_text.stroke-0"),sQuery(id+"FHMxAyK4CFUKdhS_1.wireOp",EDGE,"1cb9c079-ea9b-4899-8069-e0e3048e911d.sketch_text.stroke-1"),sQuery(id+"FHMxAyK4CFUKdhS_1.wireOp",EDGE,"1cb9c079-ea9b-4899-8069-e0e3048e911d.sketch_text.stroke-2"),sQuery(id+"FHMxAyK4CFUKdhS_1.wireOp",EDGE,"1cb9c079-ea9b-4899-8069-e0e3048e911d.sketch_text.stroke-3"),sQuery(id+"FHMxAyK4CFUKdhS_1.wireOp",EDGE,"1cb9c079-ea9b-4899-8069-e0e3048e911d.sketch_text.stroke-4"),sQuery(id+"FHMxAyK4CFUKdhS_1.wireOp",EDGE,"1cb9c079-ea9b-4899-8069-e0e3048e911d.sketch_text.stroke-5"),sQuery(id+"FHMxAyK4CFUKdhS_1.wireOp",EDGE,"1cb9c079-ea9b-4899-8069-e0e3048e911d.sketch_text.stroke-6"),sQuery(id+"FHMxAyK4CFUKdhS_1.wireOp",EDGE,"1cb9c079-ea9b-4899-8069-e0e3048e911d.sketch_text.stroke-7"),sQuery(id+"FHMxAyK4CFUKdhS_1.wireOp",EDGE,"1cb9c079-ea9b-4899-8069-e0e3048e911d.sketch_text.stroke-8"),sQuery(id+"FHMxAyK4CFUKdhS_1.wireOp",EDGE,"1cb9c079-ea9b-4899-8069-e0e3048e911d.sketch_text.stroke-9"),sQuery(id+"FHMxAyK4CFUKdhS_1.wireOp",EDGE,"1cb9c079-ea9b-4899-8069-e0e3048e911d.sketch_text.stroke-10"),sQuery(id+"FHMxAyK4CFUKdhS_1.wireOp",EDGE,"1cb9c079-ea9b-4899-8069-e0e3048e911d.sketch_text.stroke-11"),sQuery(id+"FHMxAyK4CFUKdhS_1.wireOp",EDGE,"1cb9c079-ea9b-4899-8069-e0e3048e911d.sketch_text.stroke-12"),sQuery(id+"FHMxAyK4CFUKdhS_1.wireOp",EDGE,"1cb9c079-ea9b-4899-8069-e0e3048e911d.sketch_text.stroke-13"),sQuery(id+"FHMxAyK4CFUKdhS_1.wireOp",EDGE,"1cb9c079-ea9b-4899-8069-e0e3048e911d.sketch_text.stroke-14"),sQuery(id+"FHMxAyK4CFUKdhS_1.wireOp",EDGE,"1cb9c079-ea9b-4899-8069-e0e3048e911d.sketch_text.stroke-15"),sQuery(id+"FHMxAyK4CFUKdhS_1.wireOp",EDGE,"1cb9c079-ea9b-4899-8069-e0e3048e911d.sketch_text.stroke-16"),sQuery(id+"FHMxAyK4CFUKdhS_1.wireOp",EDGE,"1cb9c079-ea9b-4899-8069-e0e3048e911d.sketch_text.stroke-17"),sQuery(id+"FHMxAyK4CFUKdhS_1.wireOp",EDGE,"1cb9c079-ea9b-4899-8069-e0e3048e911d.sketch_text.stroke-18"),sQuery(id+"FHMxAyK4CFUKdhS_1.wireOp",EDGE,"1cb9c079-ea9b-4899-8069-e0e3048e911d.sketch_text.stroke-19"),sQuery(id+"FHMxAyK4CFUKdhS_1.wireOp",EDGE,"1cb9c079-ea9b-4899-8069-e0e3048e911d.sketch_text.stroke-20"),sQuery(id+"FHMxAyK4CFUKdhS_1.wireOp",EDGE,"1cb9c079-ea9b-4899-8069-e0e3048e911d.sketch_text.stroke-21"),sQuery(id+"FHMxAyK4CFUKdhS_1.wireOp",EDGE,"1cb9c079-ea9b-4899-8069-e0e3048e911d.sketch_text.stroke-22"),sQuery(id+"FHMxAyK4CFUKdhS_1.wireOp",EDGE,"1cb9c079-ea9b-4899-8069-e0e3048e911d.sketch_text.stroke-23"),sQuery(id+"FHMxAyK4CFUKdhS_1.wireOp",EDGE,"1cb9c079-ea9b-4899-8069-e0e3048e911d.sketch_text.stroke-24"),sQuery(id+"FHMxAyK4CFUKdhS_1.wireOp",EDGE,"1cb9c079-ea9b-4899-8069-e0e3048e911d.sketch_text.stroke-25"),sQuery(id+"FHMxAyK4CFUKdhS_1.wireOp",EDGE,"1cb9c079-ea9b-4899-8069-e0e3048e911d.sketch_text.stroke-26"),sQuery(id+"FHMxAyK4CFUKdhS_1.wireOp",EDGE,"1cb9c079-ea9b-4899-8069-e0e3048e911d.sketch_text.stroke-27"),sQuery(id+"FHMxAyK4CFUKdhS_1.wireOp",EDGE,"1cb9c079-ea9b-4899-8069-e0e3048e911d.sketch_text.stroke-28"),sQuery(id+"FHMxAyK4CFUKdhS_1.wireOp",EDGE,"1cb9c079-ea9b-4899-8069-e0e3048e911d.sketch_text.stroke-29"),sQuery(id+"FHMxAyK4CFUKdhS_1.wireOp",EDGE,"1cb9c079-ea9b-4899-8069-e0e3048e911d.sketch_text.stroke-30"),sQuery(id+"FHMxAyK4CFUKdhS_1.wireOp",EDGE,"1cb9c079-ea9b-4899-8069-e0e3048e911d.sketch_text.stroke-31"),sQuery(id+"FHMxAyK4CFUKdhS_1.wireOp",EDGE,"1cb9c079-ea9b-4899-8069-e0e3048e911d.sketch_text.stroke-32"),sQuery(id+"FHMxAyK4CFUKdhS_1.wireOp",EDGE,"1cb9c079-ea9b-4899-8069-e0e3048e911d.sketch_text.stroke-33"),sQuery(id+"FHMxAyK4CFUKdhS_1.wireOp",EDGE,"1cb9c079-ea9b-4899-8069-e0e3048e911d.sketch_text.stroke-34"),sQuery(id+"FHMxAyK4CFUKdhS_1.wireOp",EDGE,"1cb9c079-ea9b-4899-8069-e0e3048e911d.sketch_text.stroke-35"),sQuery(id+"FHMxAyK4CFUKdhS_1.wireOp",EDGE,"1cb9c079-ea9b-4899-8069-e0e3048e911d.sketch_text.stroke-36"),sQuery(id+"FHMxAyK4CFUKdhS_1.wireOp",EDGE,"1cb9c079-ea9b-4899-8069-e0e3048e911d.sketch_text.stroke-37"),sQuery(id+"FHMxAyK4CFUKdhS_1.wireOp",EDGE,"1cb9c079-ea9b-4899-8069-e0e3048e911d.sketch_text.stroke-38"),sQuery(id+"FHMxAyK4CFUKdhS_1.wireOp",EDGE,"1cb9c079-ea9b-4899-8069-e0e3048e911d.sketch_text.stroke-39"),sQuery(id+"FHMxAyK4CFUKdhS_1.wireOp",EDGE,"1cb9c079-ea9b-4899-8069-e0e3048e911d.sketch_text.stroke-40"),sQuery(id+"FHMxAyK4CFUKdhS_1.wireOp",EDGE,"1cb9c079-ea9b-4899-8069-e0e3048e911d.sketch_text.stroke-41"),sQuery(id+"FHMxAyK4CFUKdhS_1.wireOp",EDGE,"1cb9c079-ea9b-4899-8069-e0e3048e911d.sketch_text.stroke-42"),sQuery(id+"FHMxAyK4CFUKdhS_1.wireOp",EDGE,"1cb9c079-ea9b-4899-8069-e0e3048e911d.sketch_text.stroke-43"),sQuery(id+"FHMxAyK4CFUKdhS_1.wireOp",EDGE,"1cb9c079-ea9b-4899-8069-e0e3048e911d.sketch_text.stroke-44"),sQuery(id+"FHMxAyK4CFUKdhS_1.wireOp",EDGE,"1cb9c079-ea9b-4899-8069-e0e3048e911d.sketch_text.stroke-45"),sQuery(id+"FHMxAyK4CFUKdhS_1.wireOp",EDGE,"1cb9c079-ea9b-4899-8069-e0e3048e911d.sketch_text.stroke-46"),sQuery(id+"FHMxAyK4CFUKdhS_1.wireOp",EDGE,"1cb9c079-ea9b-4899-8069-e0e3048e911d.sketch_text.stroke-47"),sQuery(id+"FHMxAyK4CFUKdhS_1.wireOp",EDGE,"1cb9c079-ea9b-4899-8069-e0e3048e911d.sketch_text.stroke-48"),sQuery(id+"FHMxAyK4CFUKdhS_1.wireOp",EDGE,"1cb9c079-ea9b-4899-8069-e0e3048e911d.sketch_text.stroke-49"),sQuery(id+"FHMxAyK4CFUKdhS_1.wireOp",EDGE,"1cb9c079-ea9b-4899-8069-e0e3048e911d.sketch_text.stroke-50"),sQuery(id+"FHMxAyK4CFUKdhS_1.wireOp",EDGE,"1cb9c079-ea9b-4899-8069-e0e3048e911d.sketch_text.stroke-51"),sQuery(id+"FHMxAyK4CFUKdhS_1.wireOp",EDGE,"1cb9c079-ea9b-4899-8069-e0e3048e911d.sketch_text.stroke-52"),sQuery(id+"FHMxAyK4CFUKdhS_1.wireOp",EDGE,"1cb9c079-ea9b-4899-8069-e0e3048e911d.sketch_text.stroke-53"),sQuery(id+"FHMxAyK4CFUKdhS_1.wireOp",EDGE,"1cb9c079-ea9b-4899-8069-e0e3048e911d.sketch_text.stroke-54"),sQuery(id+"FHMxAyK4CFUKdhS_1.wireOp",EDGE,"1cb9c079-ea9b-4899-8069-e0e3048e911d.sketch_text.stroke-55"),sQuery(id+"FHMxAyK4CFUKdhS_1.wireOp",EDGE,"1cb9c079-ea9b-4899-8069-e0e3048e911d.sketch_text.stroke-56"),sQuery(id+"FHMxAyK4CFUKdhS_1.wireOp",EDGE,"1cb9c079-ea9b-4899-8069-e0e3048e911d.sketch_text.stroke-57"),sQuery(id+"FHMxAyK4CFUKdhS_1.wireOp",EDGE,"1cb9c079-ea9b-4899-8069-e0e3048e911d.sketch_text.stroke-58"),sQuery(id+"FHMxAyK4CFUKdhS_1.wireOp",EDGE,"1cb9c079-ea9b-4899-8069-e0e3048e911d.sketch_text.stroke-59"),sQuery(id+"FHMxAyK4CFUKdhS_1.wireOp",EDGE,"1cb9c079-ea9b-4899-8069-e0e3048e911d.sketch_text.stroke-60"),sQuery(id+"FHMxAyK4CFUKdhS_1.wireOp",EDGE,"1cb9c079-ea9b-4899-8069-e0e3048e911d.sketch_text.stroke-61"),sQuery(id+"FHMxAyK4CFUKdhS_1.wireOp",EDGE,"1cb9c079-ea9b-4899-8069-e0e3048e911d.sketch_text.stroke-62"),sQuery(id+"FHMxAyK4CFUKdhS_1.wireOp",EDGE,"1cb9c079-ea9b-4899-8069-e0e3048e911d.sketch_text.stroke-71"),sQuery(id+"FHMxAyK4CFUKdhS_1.wireOp",EDGE,"1cb9c079-ea9b-4899-8069-e0e3048e911d.sketch_text.stroke-72"),sQuery(id+"FHMxAyK4CFUKdhS_1.wireOp",EDGE,"1cb9c079-ea9b-4899-8069-e0e3048e911d.sketch_text.stroke-73"),sQuery(id+"FHMxAyK4CFUKdhS_1.wireOp",EDGE,"1cb9c079-ea9b-4899-8069-e0e3048e911d.sketch_text.stroke-74"),sQuery(id+"FHMxAyK4CFUKdhS_1.wireOp",EDGE,"1cb9c079-ea9b-4899-8069-e0e3048e911d.sketch_text.stroke-75"),sQuery(id+"FHMxAyK4CFUKdhS_1.wireOp",EDGE,"1cb9c079-ea9b-4899-8069-e0e3048e911d.sketch_text.stroke-76"),sQuery(id+"FHMxAyK4CFUKdhS_1.wireOp",EDGE,"1cb9c079-ea9b-4899-8069-e0e3048e911d.sketch_text.stroke-77"),sQuery(id+"FHMxAyK4CFUKdhS_1.wireOp",EDGE,"1cb9c079-ea9b-4899-8069-e0e3048e911d.sketch_text.stroke-78"),sQuery(id+"FHMxAyK4CFUKdhS_1.wireOp",EDGE,"1cb9c079-ea9b-4899-8069-e0e3048e911d.sketch_text.stroke-79"),sQuery(id+"FHMxAyK4CFUKdhS_1.wireOp",EDGE,"1cb9c079-ea9b-4899-8069-e0e3048e911d.sketch_text.stroke-80"),sQuery(id+"FHMxAyK4CFUKdhS_1.wireOp",EDGE,"1cb9c079-ea9b-4899-8069-e0e3048e911d.sketch_text.stroke-81"),sQuery(id+"FHMxAyK4CFUKdhS_1.wireOp",EDGE,"1cb9c079-ea9b-4899-8069-e0e3048e911d.sketch_text.stroke-82"),sQuery(id+"FHMxAyK4CFUKdhS_1.wireOp",EDGE,"1cb9c079-ea9b-4899-8069-e0e3048e911d.sketch_text.stroke-83"),sQuery(id+"FHMxAyK4CFUKdhS_1.wireOp",EDGE,"1cb9c079-ea9b-4899-8069-e0e3048e911d.sketch_text.stroke-84"),sQuery(id+"FHMxAyK4CFUKdhS_1.wireOp",EDGE,"1cb9c079-ea9b-4899-8069-e0e3048e911d.sketch_text.stroke-85"),sQuery(id+"FHMxAyK4CFUKdhS_1.wireOp",EDGE,"1cb9c079-ea9b-4899-8069-e0e3048e911d.sketch_text.stroke-86"),sQuery(id+"FHMxAyK4CFUKdhS_1.wireOp",EDGE,"1cb9c079-ea9b-4899-8069-e0e3048e911d.sketch_text.stroke-87"),sQuery(id+"FHMxAyK4CFUKdhS_1.wireOp",EDGE,"1cb9c079-ea9b-4899-8069-e0e3048e911d.sketch_text.stroke-88"),sQuery(id+"FHMxAyK4CFUKdhS_1.wireOp",EDGE,"1cb9c079-ea9b-4899-8069-e0e3048e911d.sketch_text.stroke-89"),sQuery(id+"FHMxAyK4CFUKdhS_1.wireOp",EDGE,"1cb9c079-ea9b-4899-8069-e0e3048e911d.sketch_text.stroke-90"),sQuery(id+"FHMxAyK4CFUKdhS_1.wireOp",EDGE,"1cb9c079-ea9b-4899-8069-e0e3048e911d.sketch_text.stroke-91"),sQuery(id+"FHMxAyK4CFUKdhS_1.wireOp",EDGE,"1cb9c079-ea9b-4899-8069-e0e3048e911d.sketch_text.stroke-92"),sQuery(id+"FHMxAyK4CFUKdhS_1.wireOp",EDGE,"1cb9c079-ea9b-4899-8069-e0e3048e911d.sketch_text.stroke-93"),sQuery(id+"FHMxAyK4CFUKdhS_1.wireOp",EDGE,"1cb9c079-ea9b-4899-8069-e0e3048e911d.sketch_text.stroke-94"),sQuery(id+"FHMxAyK4CFUKdhS_1.wireOp",EDGE,"1cb9c079-ea9b-4899-8069-e0e3048e911d.sketch_text.stroke-95"),sQuery(id+"FHMxAyK4CFUKdhS_1.wireOp",EDGE,"1cb9c079-ea9b-4899-8069-e0e3048e911d.sketch_text.stroke-96"),sQuery(id+"FHMxAyK4CFUKdhS_1.wireOp",EDGE,"1cb9c079-ea9b-4899-8069-e0e3048e911d.sketch_text.stroke-97"),sQuery(id+"FHMxAyK4CFUKdhS_1.wireOp",EDGE,"1cb9c079-ea9b-4899-8069-e0e3048e911d.sketch_text.stroke-103"),sQuery(id+"FHMxAyK4CFUKdhS_1.wireOp",EDGE,"1cb9c079-ea9b-4899-8069-e0e3048e911d.sketch_text.stroke-104"),sQuery(id+"FHMxAyK4CFUKdhS_1.wireOp",EDGE,"1cb9c079-ea9b-4899-8069-e0e3048e911d.sketch_text.stroke-105"),sQuery(id+"FHMxAyK4CFUKdhS_1.wireOp",EDGE,"1cb9c079-ea9b-4899-8069-e0e3048e911d.sketch_text.stroke-106"),sQuery(id+"FHMxAyK4CFUKdhS_1.wireOp",EDGE,"1cb9c079-ea9b-4899-8069-e0e3048e911d.sketch_text.stroke-107"),sQuery(id+"FHMxAyK4CFUKdhS_1.wireOp",EDGE,"1cb9c079-ea9b-4899-8069-e0e3048e911d.sketch_text.stroke-108"),sQuery(id+"FHMxAyK4CFUKdhS_1.wireOp",EDGE,"1cb9c079-ea9b-4899-8069-e0e3048e911d.sketch_text.stroke-109"),sQuery(id+"FHMxAyK4CFUKdhS_1.wireOp",EDGE,"1cb9c079-ea9b-4899-8069-e0e3048e911d.sketch_text.stroke-110"),sQuery(id+"FHMxAyK4CFUKdhS_1.wireOp",EDGE,"1cb9c079-ea9b-4899-8069-e0e3048e911d.sketch_text.stroke-111"),sQuery(id+"FHMxAyK4CFUKdhS_1.wireOp",EDGE,"1cb9c079-ea9b-4899-8069-e0e3048e911d.sketch_text.stroke-112"),sQuery(id+"FHMxAyK4CFUKdhS_1.wireOp",EDGE,"1cb9c079-ea9b-4899-8069-e0e3048e911d.sketch_text.stroke-113"),sQuery(id+"FHMxAyK4CFUKdhS_1.wireOp",EDGE,"1cb9c079-ea9b-4899-8069-e0e3048e911d.sketch_text.stroke-114"),sQuery(id+"FHMxAyK4CFUKdhS_1.wireOp",EDGE,"1cb9c079-ea9b-4899-8069-e0e3048e911d.sketch_text.stroke-115"),sQuery(id+"FHMxAyK4CFUKdhS_1.wireOp",EDGE,"1cb9c079-ea9b-4899-8069-e0e3048e911d.sketch_text.stroke-116"),sQuery(id+"FHMxAyK4CFUKdhS_1.wireOp",EDGE,"1cb9c079-ea9b-4899-8069-e0e3048e911d.sketch_text.stroke-117"),sQuery(id+"FHMxAyK4CFUKdhS_1.wireOp",EDGE,"1cb9c079-ea9b-4899-8069-e0e3048e911d.sketch_text.stroke-118"),sQuery(id+"FHMxAyK4CFUKdhS_1.wireOp",EDGE,"1cb9c079-ea9b-4899-8069-e0e3048e911d.sketch_text.stroke-119"),sQuery(id+"FHMxAyK4CFUKdhS_1.wireOp",EDGE,"1cb9c079-ea9b-4899-8069-e0e3048e911d.sketch_text.stroke-120"),sQuery(id+"FHMxAyK4CFUKdhS_1.wireOp",EDGE,"1cb9c079-ea9b-4899-8069-e0e3048e911d.sketch_text.stroke-121"),sQuery(id+"FHMxAyK4CFUKdhS_1.wireOp",EDGE,"1cb9c079-ea9b-4899-8069-e0e3048e911d.sketch_text.stroke-122"),sQuery(id+"FHMxAyK4CFUKdhS_1.wireOp",EDGE,"1cb9c079-ea9b-4899-8069-e0e3048e911d.sketch_text.stroke-123"),sQuery(id+"FHMxAyK4CFUKdhS_1.wireOp",EDGE,"1cb9c079-ea9b-4899-8069-e0e3048e911d.sketch_text.stroke-124"),sQuery(id+"FHMxAyK4CFUKdhS_1.wireOp",EDGE,"1cb9c079-ea9b-4899-8069-e0e3048e911d.sketch_text.stroke-125"),sQuery(id+"FHMxAyK4CFUKdhS_1.wireOp",EDGE,"1cb9c079-ea9b-4899-8069-e0e3048e911d.sketch_text.stroke-126"),sQuery(id+"FHMxAyK4CFUKdhS_1.wireOp",EDGE,"1cb9c079-ea9b-4899-8069-e0e3048e911d.sketch_text.stroke-127"),sQuery(id+"FHMxAyK4CFUKdhS_1.wireOp",EDGE,"1cb9c079-ea9b-4899-8069-e0e3048e911d.sketch_text.stroke-128"),sQuery(id+"FHMxAyK4CFUKdhS_1.wireOp",EDGE,"1cb9c079-ea9b-4899-8069-e0e3048e911d.sketch_text.stroke-129"),sQuery(id+"FHMxAyK4CFUKdhS_1.wireOp",EDGE,"1cb9c079-ea9b-4899-8069-e0e3048e911d.sketch_text.stroke-130"),sQuery(id+"FHMxAyK4CFUKdhS_1.wireOp",EDGE,"1cb9c079-ea9b-4899-8069-e0e3048e911d.sketch_text.stroke-131"),sQuery(id+"FHMxAyK4CFUKdhS_1.wireOp",EDGE,"1cb9c079-ea9b-4899-8069-e0e3048e911d.sketch_text.stroke-132"),sQuery(id+"FHMxAyK4CFUKdhS_1.wireOp",EDGE,"1cb9c079-ea9b-4899-8069-e0e3048e911d.sketch_text.stroke-133"),sQuery(id+"FHMxAyK4CFUKdhS_1.wireOp",EDGE,"1cb9c079-ea9b-4899-8069-e0e3048e911d.sketch_text.stroke-134"),sQuery(id+"FHMxAyK4CFUKdhS_1.wireOp",EDGE,"1cb9c079-ea9b-4899-8069-e0e3048e911d.sketch_text.stroke-135"),sQuery(id+"FHMxAyK4CFUKdhS_1.wireOp",EDGE,"1cb9c079-ea9b-4899-8069-e0e3048e911d.sketch_text.stroke-136"),sQuery(id+"FHMxAyK4CFUKdhS_1.wireOp",EDGE,"1cb9c079-ea9b-4899-8069-e0e3048e911d.sketch_text.stroke-137"),sQuery(id+"FHMxAyK4CFUKdhS_1.wireOp",EDGE,"1cb9c079-ea9b-4899-8069-e0e3048e911d.sketch_text.stroke-138"),sQuery(id+"FHMxAyK4CFUKdhS_1.wireOp",EDGE,"1cb9c079-ea9b-4899-8069-e0e3048e911d.sketch_text.stroke-139"),sQuery(id+"FHMxAyK4CFUKdhS_1.wireOp",EDGE,"1cb9c079-ea9b-4899-8069-e0e3048e911d.sketch_text.stroke-140"),sQuery(id+"FHMxAyK4CFUKdhS_1.wireOp",EDGE,"1cb9c079-ea9b-4899-8069-e0e3048e911d.sketch_text.stroke-141"),sQuery(id+"FHMxAyK4CFUKdhS_1.wireOp",EDGE,"1cb9c079-ea9b-4899-8069-e0e3048e911d.sketch_text.stroke-142"),sQuery(id+"FHMxAyK4CFUKdhS_1.wireOp",EDGE,"1cb9c079-ea9b-4899-8069-e0e3048e911d.sketch_text.stroke-143"),sQuery(id+"FHMxAyK4CFUKdhS_1.wireOp",EDGE,"1cb9c079-ea9b-4899-8069-e0e3048e911d.sketch_text.stroke-144"),sQuery(id+"FHMxAyK4CFUKdhS_1.wireOp",EDGE,"1cb9c079-ea9b-4899-8069-e0e3048e911d.sketch_text.stroke-145"),sQuery(id+"FHMxAyK4CFUKdhS_1.wireOp",EDGE,"1cb9c079-ea9b-4899-8069-e0e3048e911d.sketch_text.stroke-146"),sQuery(id+"FHMxAyK4CFUKdhS_1.wireOp",EDGE,"1cb9c079-ea9b-4899-8069-e0e3048e911d.sketch_text.stroke-147"),sQuery(id+"FHMxAyK4CFUKdhS_1.wireOp",EDGE,"1cb9c079-ea9b-4899-8069-e0e3048e911d.sketch_text.stroke-148"),sQuery(id+"FHMxAyK4CFUKdhS_1.wireOp",EDGE,"1cb9c079-ea9b-4899-8069-e0e3048e911d.sketch_text.stroke-149"),sQuery(id+"FHMxAyK4CFUKdhS_1.wireOp",EDGE,"1cb9c079-ea9b-4899-8069-e0e3048e911d.sketch_text.stroke-150"),sQuery(id+"FHMxAyK4CFUKdhS_1.wireOp",EDGE,"1cb9c079-ea9b-4899-8069-e0e3048e911d.sketch_text.stroke-151"),sQuery(id+"FHMxAyK4CFUKdhS_1.wireOp",EDGE,"1cb9c079-ea9b-4899-8069-e0e3048e911d.sketch_text.stroke-152"),sQuery(id+"FHMxAyK4CFUKdhS_1.wireOp",EDGE,"1cb9c079-ea9b-4899-8069-e0e3048e911d.sketch_text.stroke-153"),sQuery(id+"FHMxAyK4CFUKdhS_1.wireOp",EDGE,"1cb9c079-ea9b-4899-8069-e0e3048e911d.sketch_text.stroke-159"),sQuery(id+"FHMxAyK4CFUKdhS_1.wireOp",EDGE,"1cb9c079-ea9b-4899-8069-e0e3048e911d.sketch_text.stroke-160"),sQuery(id+"FHMxAyK4CFUKdhS_1.wireOp",EDGE,"1cb9c079-ea9b-4899-8069-e0e3048e911d.sketch_text.stroke-161"),sQuery(id+"FHMxAyK4CFUKdhS_1.wireOp",EDGE,"1cb9c079-ea9b-4899-8069-e0e3048e911d.sketch_text.stroke-162"),sQuery(id+"FHMxAyK4CFUKdhS_1.wireOp",EDGE,"1cb9c079-ea9b-4899-8069-e0e3048e911d.sketch_text.stroke-163"),sQuery(id+"FHMxAyK4CFUKdhS_1.wireOp",EDGE,"1cb9c079-ea9b-4899-8069-e0e3048e911d.sketch_text.stroke-164"),sQuery(id+"FHMxAyK4CFUKdhS_1.wireOp",EDGE,"1cb9c079-ea9b-4899-8069-e0e3048e911d.sketch_text.stroke-165"),sQuery(id+"FHMxAyK4CFUKdhS_1.wireOp",EDGE,"1cb9c079-ea9b-4899-8069-e0e3048e911d.sketch_text.stroke-166"),sQuery(id+"FHMxAyK4CFUKdhS_1.wireOp",EDGE,"1cb9c079-ea9b-4899-8069-e0e3048e911d.sketch_text.stroke-167"),sQuery(id+"FHMxAyK4CFUKdhS_1.wireOp",EDGE,"1cb9c079-ea9b-4899-8069-e0e3048e911d.sketch_text.stroke-168"),sQuery(id+"FHMxAyK4CFUKdhS_1.wireOp",EDGE,"1cb9c079-ea9b-4899-8069-e0e3048e911d.sketch_text.stroke-169"),sQuery(id+"FHMxAyK4CFUKdhS_1.wireOp",EDGE,"1cb9c079-ea9b-4899-8069-e0e3048e911d.sketch_text.stroke-170"),sQuery(id+"FHMxAyK4CFUKdhS_1.wireOp",EDGE,"1cb9c079-ea9b-4899-8069-e0e3048e911d.sketch_text.stroke-171"),sQuery(id+"FHMxAyK4CFUKdhS_1.wireOp",EDGE,"1cb9c079-ea9b-4899-8069-e0e3048e911d.sketch_text.stroke-172"),sQuery(id+"FHMxAyK4CFUKdhS_1.wireOp",EDGE,"1cb9c079-ea9b-4899-8069-e0e3048e911d.sketch_text.stroke-173"),sQuery(id+"FHMxAyK4CFUKdhS_1.wireOp",EDGE,"1cb9c079-ea9b-4899-8069-e0e3048e911d.sketch_text.stroke-174"),sQuery(id+"FHMxAyK4CFUKdhS_1.wireOp",EDGE,"1cb9c079-ea9b-4899-8069-e0e3048e911d.sketch_text.stroke-175"),sQuery(id+"FHMxAyK4CFUKdhS_1.wireOp",EDGE,"1cb9c079-ea9b-4899-8069-e0e3048e911d.sketch_text.stroke-176"),sQuery(id+"FHMxAyK4CFUKdhS_1.wireOp",EDGE,"1cb9c079-ea9b-4899-8069-e0e3048e911d.sketch_text.stroke-177"),sQuery(id+"FHMxAyK4CFUKdhS_1.wireOp",EDGE,"1cb9c079-ea9b-4899-8069-e0e3048e911d.sketch_text.stroke-178"),sQuery(id+"FHMxAyK4CFUKdhS_1.wireOp",EDGE,"1cb9c079-ea9b-4899-8069-e0e3048e911d.sketch_text.stroke-179"),sQuery(id+"FHMxAyK4CFUKdhS_1.wireOp",EDGE,"1cb9c079-ea9b-4899-8069-e0e3048e911d.sketch_text.stroke-180"),sQuery(id+"F3.wireOp",EDGE,"727ac2c1-f511-4829-95a7-a443ef16a4cd"),subQ2])],"isStart":true}),makeQuery(id+"F4.opExtrude","SWEPT_FACE",FACE,{"disambiguationData":[OSD([subQ2])]})])],"derivedFrom":makeQuery(id+"F4.opExtrude","CAP_EDGE",EDGE,{"disambiguationData":[OSD([subQ2])],"isStart":true})});}
            var Q18;
            {var subQ0=sQuery(id+"F0.wireOp",EDGE,"E0.top");var subQ1=sQuery(id+"F0.wireOp",EDGE,"E0.bottom");var subQ2=sQuery(id+"F3.wireOp",EDGE,"1a034e28-a7c2-419d-97de-c33d70a47301");Q18=makeQuery(id+"F4.boolean.opBoolean","SPLIT",EDGE,{"disambiguationData":[TD([makeQuery(id+"F1.opExtrude","CAP_FACE",FACE,{"disambiguationData":[OSD([subQ1,subQ0,sQuery(id+"F0.wireOp",EDGE,"E0.left"),sQuery(id+"F0.wireOp",EDGE,"E0.right")])],"isStart":false}),makeQuery(id+"F1.opExtrude","SWEPT_FACE",FACE,{"disambiguationData":[OSD([subQ0])]}),makeQuery(id+"F4.opExtrude","CAP_FACE",FACE,{"disambiguationData":[OSD([subQ1,sQuery(id+"F2.wireOp",EDGE,"fcba4419-a2ee-464f-be9d-58f11bf3418b.sketch_text.stroke-0"),sQuery(id+"F2.wireOp",EDGE,"fcba4419-a2ee-464f-be9d-58f11bf3418b.sketch_text.stroke-1"),sQuery(id+"F2.wireOp",EDGE,"fcba4419-a2ee-464f-be9d-58f11bf3418b.sketch_text.stroke-2"),sQuery(id+"F2.wireOp",EDGE,"fcba4419-a2ee-464f-be9d-58f11bf3418b.sketch_text.stroke-3"),sQuery(id+"F2.wireOp",EDGE,"fcba4419-a2ee-464f-be9d-58f11bf3418b.sketch_text.stroke-4"),sQuery(id+"F2.wireOp",EDGE,"fcba4419-a2ee-464f-be9d-58f11bf3418b.sketch_text.stroke-5"),sQuery(id+"F2.wireOp",EDGE,"fcba4419-a2ee-464f-be9d-58f11bf3418b.sketch_text.stroke-6"),sQuery(id+"F2.wireOp",EDGE,"fcba4419-a2ee-464f-be9d-58f11bf3418b.sketch_text.stroke-7"),sQuery(id+"F2.wireOp",EDGE,"fcba4419-a2ee-464f-be9d-58f11bf3418b.sketch_text.stroke-8"),sQuery(id+"F2.wireOp",EDGE,"fcba4419-a2ee-464f-be9d-58f11bf3418b.sketch_text.stroke-9"),sQuery(id+"F2.wireOp",EDGE,"fcba4419-a2ee-464f-be9d-58f11bf3418b.sketch_text.stroke-10"),sQuery(id+"F2.wireOp",EDGE,"fcba4419-a2ee-464f-be9d-58f11bf3418b.sketch_text.stroke-11"),sQuery(id+"F2.wireOp",EDGE,"fcba4419-a2ee-464f-be9d-58f11bf3418b.sketch_text.stroke-12"),sQuery(id+"F2.wireOp",EDGE,"fcba4419-a2ee-464f-be9d-58f11bf3418b.sketch_text.stroke-13"),sQuery(id+"F2.wireOp",EDGE,"fcba4419-a2ee-464f-be9d-58f11bf3418b.sketch_text.stroke-14"),sQuery(id+"F2.wireOp",EDGE,"fcba4419-a2ee-464f-be9d-58f11bf3418b.sketch_text.stroke-15"),sQuery(id+"F2.wireOp",EDGE,"fcba4419-a2ee-464f-be9d-58f11bf3418b.sketch_text.stroke-16"),sQuery(id+"F2.wireOp",EDGE,"fcba4419-a2ee-464f-be9d-58f11bf3418b.sketch_text.stroke-17"),sQuery(id+"F2.wireOp",EDGE,"fcba4419-a2ee-464f-be9d-58f11bf3418b.sketch_text.stroke-18"),sQuery(id+"F2.wireOp",EDGE,"fcba4419-a2ee-464f-be9d-58f11bf3418b.sketch_text.stroke-19"),sQuery(id+"F2.wireOp",EDGE,"fcba4419-a2ee-464f-be9d-58f11bf3418b.sketch_text.stroke-20"),sQuery(id+"F2.wireOp",EDGE,"fcba4419-a2ee-464f-be9d-58f11bf3418b.sketch_text.stroke-21"),sQuery(id+"F2.wireOp",EDGE,"fcba4419-a2ee-464f-be9d-58f11bf3418b.sketch_text.stroke-22"),sQuery(id+"F2.wireOp",EDGE,"fcba4419-a2ee-464f-be9d-58f11bf3418b.sketch_text.stroke-23"),sQuery(id+"F2.wireOp",EDGE,"fcba4419-a2ee-464f-be9d-58f11bf3418b.sketch_text.stroke-24"),sQuery(id+"F2.wireOp",EDGE,"fcba4419-a2ee-464f-be9d-58f11bf3418b.sketch_text.stroke-25"),sQuery(id+"F2.wireOp",EDGE,"fcba4419-a2ee-464f-be9d-58f11bf3418b.sketch_text.stroke-26"),sQuery(id+"F2.wireOp",EDGE,"fcba4419-a2ee-464f-be9d-58f11bf3418b.sketch_text.stroke-27"),sQuery(id+"F2.wireOp",EDGE,"fcba4419-a2ee-464f-be9d-58f11bf3418b.sketch_text.stroke-28"),sQuery(id+"F2.wireOp",EDGE,"fcba4419-a2ee-464f-be9d-58f11bf3418b.sketch_text.stroke-29"),sQuery(id+"F2.wireOp",EDGE,"fcba4419-a2ee-464f-be9d-58f11bf3418b.sketch_text.stroke-30"),sQuery(id+"F2.wireOp",EDGE,"fcba4419-a2ee-464f-be9d-58f11bf3418b.sketch_text.stroke-31"),sQuery(id+"F2.wireOp",EDGE,"fcba4419-a2ee-464f-be9d-58f11bf3418b.sketch_text.stroke-32"),sQuery(id+"F2.wireOp",EDGE,"fcba4419-a2ee-464f-be9d-58f11bf3418b.sketch_text.stroke-33"),sQuery(id+"F2.wireOp",EDGE,"fcba4419-a2ee-464f-be9d-58f11bf3418b.sketch_text.stroke-34"),sQuery(id+"F2.wireOp",EDGE,"fcba4419-a2ee-464f-be9d-58f11bf3418b.sketch_text.stroke-35"),sQuery(id+"F2.wireOp",EDGE,"fcba4419-a2ee-464f-be9d-58f11bf3418b.sketch_text.stroke-36"),sQuery(id+"F2.wireOp",EDGE,"fcba4419-a2ee-464f-be9d-58f11bf3418b.sketch_text.stroke-37"),sQuery(id+"F2.wireOp",EDGE,"fcba4419-a2ee-464f-be9d-58f11bf3418b.sketch_text.stroke-38"),sQuery(id+"F2.wireOp",EDGE,"fcba4419-a2ee-464f-be9d-58f11bf3418b.sketch_text.stroke-39"),sQuery(id+"F2.wireOp",EDGE,"fcba4419-a2ee-464f-be9d-58f11bf3418b.sketch_text.stroke-40"),sQuery(id+"F2.wireOp",EDGE,"fcba4419-a2ee-464f-be9d-58f11bf3418b.sketch_text.stroke-41"),sQuery(id+"F2.wireOp",EDGE,"fcba4419-a2ee-464f-be9d-58f11bf3418b.sketch_text.stroke-42"),sQuery(id+"F2.wireOp",EDGE,"fcba4419-a2ee-464f-be9d-58f11bf3418b.sketch_text.stroke-43"),sQuery(id+"F2.wireOp",EDGE,"fcba4419-a2ee-464f-be9d-58f11bf3418b.sketch_text.stroke-44"),sQuery(id+"F2.wireOp",EDGE,"fcba4419-a2ee-464f-be9d-58f11bf3418b.sketch_text.stroke-45"),sQuery(id+"F2.wireOp",EDGE,"fcba4419-a2ee-464f-be9d-58f11bf3418b.sketch_text.stroke-46"),sQuery(id+"F2.wireOp",EDGE,"fcba4419-a2ee-464f-be9d-58f11bf3418b.sketch_text.stroke-47"),sQuery(id+"F2.wireOp",EDGE,"fcba4419-a2ee-464f-be9d-58f11bf3418b.sketch_text.stroke-48"),sQuery(id+"F2.wireOp",EDGE,"fcba4419-a2ee-464f-be9d-58f11bf3418b.sketch_text.stroke-49"),sQuery(id+"F2.wireOp",EDGE,"fcba4419-a2ee-464f-be9d-58f11bf3418b.sketch_text.stroke-50"),sQuery(id+"F2.wireOp",EDGE,"fcba4419-a2ee-464f-be9d-58f11bf3418b.sketch_text.stroke-51"),sQuery(id+"F2.wireOp",EDGE,"fcba4419-a2ee-464f-be9d-58f11bf3418b.sketch_text.stroke-52"),sQuery(id+"F2.wireOp",EDGE,"fcba4419-a2ee-464f-be9d-58f11bf3418b.sketch_text.stroke-53"),sQuery(id+"F2.wireOp",EDGE,"fcba4419-a2ee-464f-be9d-58f11bf3418b.sketch_text.stroke-54"),sQuery(id+"F2.wireOp",EDGE,"fcba4419-a2ee-464f-be9d-58f11bf3418b.sketch_text.stroke-55"),sQuery(id+"F2.wireOp",EDGE,"fcba4419-a2ee-464f-be9d-58f11bf3418b.sketch_text.stroke-56"),sQuery(id+"F2.wireOp",EDGE,"fcba4419-a2ee-464f-be9d-58f11bf3418b.sketch_text.stroke-57"),sQuery(id+"F2.wireOp",EDGE,"fcba4419-a2ee-464f-be9d-58f11bf3418b.sketch_text.stroke-58"),sQuery(id+"F2.wireOp",EDGE,"fcba4419-a2ee-464f-be9d-58f11bf3418b.sketch_text.stroke-59"),sQuery(id+"F2.wireOp",EDGE,"fcba4419-a2ee-464f-be9d-58f11bf3418b.sketch_text.stroke-60"),sQuery(id+"F2.wireOp",EDGE,"fcba4419-a2ee-464f-be9d-58f11bf3418b.sketch_text.stroke-61"),sQuery(id+"F2.wireOp",EDGE,"fcba4419-a2ee-464f-be9d-58f11bf3418b.sketch_text.stroke-62"),sQuery(id+"F2.wireOp",EDGE,"fcba4419-a2ee-464f-be9d-58f11bf3418b.sketch_text.stroke-63"),sQuery(id+"F2.wireOp",EDGE,"fcba4419-a2ee-464f-be9d-58f11bf3418b.sketch_text.stroke-64"),sQuery(id+"F2.wireOp",EDGE,"fcba4419-a2ee-464f-be9d-58f11bf3418b.sketch_text.stroke-65"),sQuery(id+"F2.wireOp",EDGE,"fcba4419-a2ee-464f-be9d-58f11bf3418b.sketch_text.stroke-66"),sQuery(id+"F2.wireOp",EDGE,"fcba4419-a2ee-464f-be9d-58f11bf3418b.sketch_text.stroke-67"),sQuery(id+"F2.wireOp",EDGE,"fcba4419-a2ee-464f-be9d-58f11bf3418b.sketch_text.stroke-68"),sQuery(id+"F2.wireOp",EDGE,"fcba4419-a2ee-464f-be9d-58f11bf3418b.sketch_text.stroke-69"),sQuery(id+"F2.wireOp",EDGE,"fcba4419-a2ee-464f-be9d-58f11bf3418b.sketch_text.stroke-70"),sQuery(id+"F2.wireOp",EDGE,"fcba4419-a2ee-464f-be9d-58f11bf3418b.sketch_text.stroke-71"),sQuery(id+"F2.wireOp",EDGE,"fcba4419-a2ee-464f-be9d-58f11bf3418b.sketch_text.stroke-72"),sQuery(id+"F2.wireOp",EDGE,"fcba4419-a2ee-464f-be9d-58f11bf3418b.sketch_text.stroke-73"),sQuery(id+"F2.wireOp",EDGE,"fcba4419-a2ee-464f-be9d-58f11bf3418b.sketch_text.stroke-74"),sQuery(id+"F2.wireOp",EDGE,"fcba4419-a2ee-464f-be9d-58f11bf3418b.sketch_text.stroke-75"),sQuery(id+"F2.wireOp",EDGE,"fcba4419-a2ee-464f-be9d-58f11bf3418b.sketch_text.stroke-76"),sQuery(id+"F2.wireOp",EDGE,"fcba4419-a2ee-464f-be9d-58f11bf3418b.sketch_text.stroke-77"),sQuery(id+"F2.wireOp",EDGE,"fcba4419-a2ee-464f-be9d-58f11bf3418b.sketch_text.stroke-78"),sQuery(id+"F2.wireOp",EDGE,"fcba4419-a2ee-464f-be9d-58f11bf3418b.sketch_text.stroke-79"),sQuery(id+"F2.wireOp",EDGE,"fcba4419-a2ee-464f-be9d-58f11bf3418b.sketch_text.stroke-80"),sQuery(id+"F2.wireOp",EDGE,"fcba4419-a2ee-464f-be9d-58f11bf3418b.sketch_text.stroke-81"),sQuery(id+"F2.wireOp",EDGE,"fcba4419-a2ee-464f-be9d-58f11bf3418b.sketch_text.stroke-82"),sQuery(id+"F2.wireOp",EDGE,"fcba4419-a2ee-464f-be9d-58f11bf3418b.sketch_text.stroke-83"),sQuery(id+"F2.wireOp",EDGE,"fcba4419-a2ee-464f-be9d-58f11bf3418b.sketch_text.stroke-84"),sQuery(id+"F2.wireOp",EDGE,"fcba4419-a2ee-464f-be9d-58f11bf3418b.sketch_text.stroke-85"),sQuery(id+"F2.wireOp",EDGE,"fcba4419-a2ee-464f-be9d-58f11bf3418b.sketch_text.stroke-86"),sQuery(id+"F2.wireOp",EDGE,"fcba4419-a2ee-464f-be9d-58f11bf3418b.sketch_text.stroke-87"),sQuery(id+"F2.wireOp",EDGE,"fcba4419-a2ee-464f-be9d-58f11bf3418b.sketch_text.stroke-88"),sQuery(id+"F2.wireOp",EDGE,"fcba4419-a2ee-464f-be9d-58f11bf3418b.sketch_text.stroke-89"),sQuery(id+"F2.wireOp",EDGE,"fcba4419-a2ee-464f-be9d-58f11bf3418b.sketch_text.stroke-90"),sQuery(id+"F2.wireOp",EDGE,"fcba4419-a2ee-464f-be9d-58f11bf3418b.sketch_text.stroke-91"),sQuery(id+"F2.wireOp",EDGE,"fcba4419-a2ee-464f-be9d-58f11bf3418b.sketch_text.stroke-92"),sQuery(id+"F2.wireOp",EDGE,"fcba4419-a2ee-464f-be9d-58f11bf3418b.sketch_text.stroke-93"),sQuery(id+"F2.wireOp",EDGE,"fcba4419-a2ee-464f-be9d-58f11bf3418b.sketch_text.stroke-94"),sQuery(id+"F2.wireOp",EDGE,"fcba4419-a2ee-464f-be9d-58f11bf3418b.sketch_text.stroke-95"),sQuery(id+"F2.wireOp",EDGE,"fcba4419-a2ee-464f-be9d-58f11bf3418b.sketch_text.stroke-96"),sQuery(id+"F2.wireOp",EDGE,"fcba4419-a2ee-464f-be9d-58f11bf3418b.sketch_text.stroke-97"),sQuery(id+"F2.wireOp",EDGE,"fcba4419-a2ee-464f-be9d-58f11bf3418b.sketch_text.stroke-98"),sQuery(id+"F2.wireOp",EDGE,"fcba4419-a2ee-464f-be9d-58f11bf3418b.sketch_text.stroke-99"),sQuery(id+"F2.wireOp",EDGE,"fcba4419-a2ee-464f-be9d-58f11bf3418b.sketch_text.stroke-100"),sQuery(id+"F2.wireOp",EDGE,"fcba4419-a2ee-464f-be9d-58f11bf3418b.sketch_text.stroke-101"),sQuery(id+"F2.wireOp",EDGE,"fcba4419-a2ee-464f-be9d-58f11bf3418b.sketch_text.stroke-102"),sQuery(id+"F2.wireOp",EDGE,"fcba4419-a2ee-464f-be9d-58f11bf3418b.sketch_text.stroke-103"),sQuery(id+"F2.wireOp",EDGE,"fcba4419-a2ee-464f-be9d-58f11bf3418b.sketch_text.stroke-104"),sQuery(id+"F2.wireOp",EDGE,"fcba4419-a2ee-464f-be9d-58f11bf3418b.sketch_text.stroke-105"),sQuery(id+"F2.wireOp",EDGE,"fcba4419-a2ee-464f-be9d-58f11bf3418b.sketch_text.stroke-106"),sQuery(id+"F2.wireOp",EDGE,"fcba4419-a2ee-464f-be9d-58f11bf3418b.sketch_text.stroke-107"),sQuery(id+"F2.wireOp",EDGE,"fcba4419-a2ee-464f-be9d-58f11bf3418b.sketch_text.stroke-108"),sQuery(id+"F2.wireOp",EDGE,"fcba4419-a2ee-464f-be9d-58f11bf3418b.sketch_text.stroke-109"),sQuery(id+"F2.wireOp",EDGE,"fcba4419-a2ee-464f-be9d-58f11bf3418b.sketch_text.stroke-110"),sQuery(id+"F2.wireOp",EDGE,"fcba4419-a2ee-464f-be9d-58f11bf3418b.sketch_text.stroke-111"),sQuery(id+"F2.wireOp",EDGE,"fcba4419-a2ee-464f-be9d-58f11bf3418b.sketch_text.stroke-112"),sQuery(id+"F2.wireOp",EDGE,"fcba4419-a2ee-464f-be9d-58f11bf3418b.sketch_text.stroke-113"),sQuery(id+"F2.wireOp",EDGE,"fcba4419-a2ee-464f-be9d-58f11bf3418b.sketch_text.stroke-114"),sQuery(id+"F2.wireOp",EDGE,"fcba4419-a2ee-464f-be9d-58f11bf3418b.sketch_text.stroke-115"),sQuery(id+"F2.wireOp",EDGE,"fcba4419-a2ee-464f-be9d-58f11bf3418b.sketch_text.stroke-116"),sQuery(id+"F2.wireOp",EDGE,"fcba4419-a2ee-464f-be9d-58f11bf3418b.sketch_text.stroke-117"),sQuery(id+"F2.wireOp",EDGE,"fcba4419-a2ee-464f-be9d-58f11bf3418b.sketch_text.stroke-118"),sQuery(id+"F2.wireOp",EDGE,"fcba4419-a2ee-464f-be9d-58f11bf3418b.sketch_text.stroke-119"),sQuery(id+"F2.wireOp",EDGE,"fcba4419-a2ee-464f-be9d-58f11bf3418b.sketch_text.stroke-120"),sQuery(id+"F2.wireOp",EDGE,"fcba4419-a2ee-464f-be9d-58f11bf3418b.sketch_text.stroke-121"),sQuery(id+"F2.wireOp",EDGE,"fcba4419-a2ee-464f-be9d-58f11bf3418b.sketch_text.stroke-122"),sQuery(id+"F2.wireOp",EDGE,"fcba4419-a2ee-464f-be9d-58f11bf3418b.sketch_text.stroke-123"),sQuery(id+"F2.wireOp",EDGE,"fcba4419-a2ee-464f-be9d-58f11bf3418b.sketch_text.stroke-124"),sQuery(id+"F2.wireOp",EDGE,"fcba4419-a2ee-464f-be9d-58f11bf3418b.sketch_text.stroke-125"),sQuery(id+"F2.wireOp",EDGE,"fcba4419-a2ee-464f-be9d-58f11bf3418b.sketch_text.stroke-126"),sQuery(id+"F2.wireOp",EDGE,"fcba4419-a2ee-464f-be9d-58f11bf3418b.sketch_text.stroke-127"),sQuery(id+"F2.wireOp",EDGE,"fcba4419-a2ee-464f-be9d-58f11bf3418b.sketch_text.stroke-128"),sQuery(id+"F2.wireOp",EDGE,"fcba4419-a2ee-464f-be9d-58f11bf3418b.sketch_text.stroke-129"),sQuery(id+"F2.wireOp",EDGE,"fcba4419-a2ee-464f-be9d-58f11bf3418b.sketch_text.stroke-130"),sQuery(id+"F2.wireOp",EDGE,"fcba4419-a2ee-464f-be9d-58f11bf3418b.sketch_text.stroke-131"),sQuery(id+"F2.wireOp",EDGE,"fcba4419-a2ee-464f-be9d-58f11bf3418b.sketch_text.stroke-132"),sQuery(id+"F2.wireOp",EDGE,"fcba4419-a2ee-464f-be9d-58f11bf3418b.sketch_text.stroke-133"),sQuery(id+"F2.wireOp",EDGE,"fcba4419-a2ee-464f-be9d-58f11bf3418b.sketch_text.stroke-134"),sQuery(id+"F2.wireOp",EDGE,"fcba4419-a2ee-464f-be9d-58f11bf3418b.sketch_text.stroke-135"),sQuery(id+"F2.wireOp",EDGE,"fcba4419-a2ee-464f-be9d-58f11bf3418b.sketch_text.stroke-136"),sQuery(id+"F2.wireOp",EDGE,"fcba4419-a2ee-464f-be9d-58f11bf3418b.sketch_text.stroke-137"),sQuery(id+"F2.wireOp",EDGE,"fcba4419-a2ee-464f-be9d-58f11bf3418b.sketch_text.stroke-138"),sQuery(id+"F2.wireOp",EDGE,"fcba4419-a2ee-464f-be9d-58f11bf3418b.sketch_text.stroke-139"),sQuery(id+"F2.wireOp",EDGE,"fcba4419-a2ee-464f-be9d-58f11bf3418b.sketch_text.stroke-140"),sQuery(id+"F2.wireOp",EDGE,"fcba4419-a2ee-464f-be9d-58f11bf3418b.sketch_text.stroke-141"),sQuery(id+"F2.wireOp",EDGE,"fcba4419-a2ee-464f-be9d-58f11bf3418b.sketch_text.stroke-142"),sQuery(id+"F2.wireOp",EDGE,"fcba4419-a2ee-464f-be9d-58f11bf3418b.sketch_text.stroke-143"),sQuery(id+"F2.wireOp",EDGE,"fcba4419-a2ee-464f-be9d-58f11bf3418b.sketch_text.stroke-144"),sQuery(id+"F2.wireOp",EDGE,"fcba4419-a2ee-464f-be9d-58f11bf3418b.sketch_text.stroke-145"),sQuery(id+"F2.wireOp",EDGE,"fcba4419-a2ee-464f-be9d-58f11bf3418b.sketch_text.stroke-146"),sQuery(id+"F2.wireOp",EDGE,"fcba4419-a2ee-464f-be9d-58f11bf3418b.sketch_text.stroke-147"),sQuery(id+"F2.wireOp",EDGE,"fcba4419-a2ee-464f-be9d-58f11bf3418b.sketch_text.stroke-148"),sQuery(id+"F2.wireOp",EDGE,"fcba4419-a2ee-464f-be9d-58f11bf3418b.sketch_text.stroke-149"),sQuery(id+"F2.wireOp",EDGE,"fcba4419-a2ee-464f-be9d-58f11bf3418b.sketch_text.stroke-150"),sQuery(id+"F2.wireOp",EDGE,"fcba4419-a2ee-464f-be9d-58f11bf3418b.sketch_text.stroke-151"),sQuery(id+"F2.wireOp",EDGE,"fcba4419-a2ee-464f-be9d-58f11bf3418b.sketch_text.stroke-152"),sQuery(id+"F2.wireOp",EDGE,"fcba4419-a2ee-464f-be9d-58f11bf3418b.sketch_text.stroke-153"),sQuery(id+"F2.wireOp",EDGE,"fcba4419-a2ee-464f-be9d-58f11bf3418b.sketch_text.stroke-154"),sQuery(id+"F2.wireOp",EDGE,"fcba4419-a2ee-464f-be9d-58f11bf3418b.sketch_text.stroke-155"),sQuery(id+"F2.wireOp",EDGE,"fcba4419-a2ee-464f-be9d-58f11bf3418b.sketch_text.stroke-156"),sQuery(id+"F2.wireOp",EDGE,"fcba4419-a2ee-464f-be9d-58f11bf3418b.sketch_text.stroke-157"),sQuery(id+"F2.wireOp",EDGE,"fcba4419-a2ee-464f-be9d-58f11bf3418b.sketch_text.stroke-158"),sQuery(id+"F2.wireOp",EDGE,"fcba4419-a2ee-464f-be9d-58f11bf3418b.sketch_text.stroke-159"),sQuery(id+"F2.wireOp",EDGE,"fcba4419-a2ee-464f-be9d-58f11bf3418b.sketch_text.stroke-160"),sQuery(id+"F2.wireOp",EDGE,"fcba4419-a2ee-464f-be9d-58f11bf3418b.sketch_text.stroke-161"),sQuery(id+"F2.wireOp",EDGE,"fcba4419-a2ee-464f-be9d-58f11bf3418b.sketch_text.stroke-162"),sQuery(id+"F2.wireOp",EDGE,"fcba4419-a2ee-464f-be9d-58f11bf3418b.sketch_text.stroke-163"),sQuery(id+"F2.wireOp",EDGE,"fcba4419-a2ee-464f-be9d-58f11bf3418b.sketch_text.stroke-164"),sQuery(id+"F2.wireOp",EDGE,"fcba4419-a2ee-464f-be9d-58f11bf3418b.sketch_text.stroke-165"),sQuery(id+"F2.wireOp",EDGE,"fcba4419-a2ee-464f-be9d-58f11bf3418b.sketch_text.stroke-166"),sQuery(id+"F2.wireOp",EDGE,"fcba4419-a2ee-464f-be9d-58f11bf3418b.sketch_text.stroke-167"),sQuery(id+"F2.wireOp",EDGE,"fcba4419-a2ee-464f-be9d-58f11bf3418b.sketch_text.stroke-168"),sQuery(id+"F2.wireOp",EDGE,"fcba4419-a2ee-464f-be9d-58f11bf3418b.sketch_text.stroke-169"),sQuery(id+"F2.wireOp",EDGE,"fcba4419-a2ee-464f-be9d-58f11bf3418b.sketch_text.stroke-170"),sQuery(id+"F2.wireOp",EDGE,"fcba4419-a2ee-464f-be9d-58f11bf3418b.sketch_text.stroke-171"),sQuery(id+"F2.wireOp",EDGE,"fcba4419-a2ee-464f-be9d-58f11bf3418b.sketch_text.stroke-172"),sQuery(id+"F2.wireOp",EDGE,"fcba4419-a2ee-464f-be9d-58f11bf3418b.sketch_text.stroke-173"),sQuery(id+"FHMxAyK4CFUKdhS_1.wireOp",EDGE,"1cb9c079-ea9b-4899-8069-e0e3048e911d.sketch_text.stroke-0"),sQuery(id+"FHMxAyK4CFUKdhS_1.wireOp",EDGE,"1cb9c079-ea9b-4899-8069-e0e3048e911d.sketch_text.stroke-1"),sQuery(id+"FHMxAyK4CFUKdhS_1.wireOp",EDGE,"1cb9c079-ea9b-4899-8069-e0e3048e911d.sketch_text.stroke-2"),sQuery(id+"FHMxAyK4CFUKdhS_1.wireOp",EDGE,"1cb9c079-ea9b-4899-8069-e0e3048e911d.sketch_text.stroke-3"),sQuery(id+"FHMxAyK4CFUKdhS_1.wireOp",EDGE,"1cb9c079-ea9b-4899-8069-e0e3048e911d.sketch_text.stroke-4"),sQuery(id+"FHMxAyK4CFUKdhS_1.wireOp",EDGE,"1cb9c079-ea9b-4899-8069-e0e3048e911d.sketch_text.stroke-5"),sQuery(id+"FHMxAyK4CFUKdhS_1.wireOp",EDGE,"1cb9c079-ea9b-4899-8069-e0e3048e911d.sketch_text.stroke-6"),sQuery(id+"FHMxAyK4CFUKdhS_1.wireOp",EDGE,"1cb9c079-ea9b-4899-8069-e0e3048e911d.sketch_text.stroke-7"),sQuery(id+"FHMxAyK4CFUKdhS_1.wireOp",EDGE,"1cb9c079-ea9b-4899-8069-e0e3048e911d.sketch_text.stroke-8"),sQuery(id+"FHMxAyK4CFUKdhS_1.wireOp",EDGE,"1cb9c079-ea9b-4899-8069-e0e3048e911d.sketch_text.stroke-9"),sQuery(id+"FHMxAyK4CFUKdhS_1.wireOp",EDGE,"1cb9c079-ea9b-4899-8069-e0e3048e911d.sketch_text.stroke-10"),sQuery(id+"FHMxAyK4CFUKdhS_1.wireOp",EDGE,"1cb9c079-ea9b-4899-8069-e0e3048e911d.sketch_text.stroke-11"),sQuery(id+"FHMxAyK4CFUKdhS_1.wireOp",EDGE,"1cb9c079-ea9b-4899-8069-e0e3048e911d.sketch_text.stroke-12"),sQuery(id+"FHMxAyK4CFUKdhS_1.wireOp",EDGE,"1cb9c079-ea9b-4899-8069-e0e3048e911d.sketch_text.stroke-13"),sQuery(id+"FHMxAyK4CFUKdhS_1.wireOp",EDGE,"1cb9c079-ea9b-4899-8069-e0e3048e911d.sketch_text.stroke-14"),sQuery(id+"FHMxAyK4CFUKdhS_1.wireOp",EDGE,"1cb9c079-ea9b-4899-8069-e0e3048e911d.sketch_text.stroke-15"),sQuery(id+"FHMxAyK4CFUKdhS_1.wireOp",EDGE,"1cb9c079-ea9b-4899-8069-e0e3048e911d.sketch_text.stroke-16"),sQuery(id+"FHMxAyK4CFUKdhS_1.wireOp",EDGE,"1cb9c079-ea9b-4899-8069-e0e3048e911d.sketch_text.stroke-17"),sQuery(id+"FHMxAyK4CFUKdhS_1.wireOp",EDGE,"1cb9c079-ea9b-4899-8069-e0e3048e911d.sketch_text.stroke-18"),sQuery(id+"FHMxAyK4CFUKdhS_1.wireOp",EDGE,"1cb9c079-ea9b-4899-8069-e0e3048e911d.sketch_text.stroke-19"),sQuery(id+"FHMxAyK4CFUKdhS_1.wireOp",EDGE,"1cb9c079-ea9b-4899-8069-e0e3048e911d.sketch_text.stroke-20"),sQuery(id+"FHMxAyK4CFUKdhS_1.wireOp",EDGE,"1cb9c079-ea9b-4899-8069-e0e3048e911d.sketch_text.stroke-21"),sQuery(id+"FHMxAyK4CFUKdhS_1.wireOp",EDGE,"1cb9c079-ea9b-4899-8069-e0e3048e911d.sketch_text.stroke-22"),sQuery(id+"FHMxAyK4CFUKdhS_1.wireOp",EDGE,"1cb9c079-ea9b-4899-8069-e0e3048e911d.sketch_text.stroke-23"),sQuery(id+"FHMxAyK4CFUKdhS_1.wireOp",EDGE,"1cb9c079-ea9b-4899-8069-e0e3048e911d.sketch_text.stroke-24"),sQuery(id+"FHMxAyK4CFUKdhS_1.wireOp",EDGE,"1cb9c079-ea9b-4899-8069-e0e3048e911d.sketch_text.stroke-25"),sQuery(id+"FHMxAyK4CFUKdhS_1.wireOp",EDGE,"1cb9c079-ea9b-4899-8069-e0e3048e911d.sketch_text.stroke-26"),sQuery(id+"FHMxAyK4CFUKdhS_1.wireOp",EDGE,"1cb9c079-ea9b-4899-8069-e0e3048e911d.sketch_text.stroke-27"),sQuery(id+"FHMxAyK4CFUKdhS_1.wireOp",EDGE,"1cb9c079-ea9b-4899-8069-e0e3048e911d.sketch_text.stroke-28"),sQuery(id+"FHMxAyK4CFUKdhS_1.wireOp",EDGE,"1cb9c079-ea9b-4899-8069-e0e3048e911d.sketch_text.stroke-29"),sQuery(id+"FHMxAyK4CFUKdhS_1.wireOp",EDGE,"1cb9c079-ea9b-4899-8069-e0e3048e911d.sketch_text.stroke-30"),sQuery(id+"FHMxAyK4CFUKdhS_1.wireOp",EDGE,"1cb9c079-ea9b-4899-8069-e0e3048e911d.sketch_text.stroke-31"),sQuery(id+"FHMxAyK4CFUKdhS_1.wireOp",EDGE,"1cb9c079-ea9b-4899-8069-e0e3048e911d.sketch_text.stroke-32"),sQuery(id+"FHMxAyK4CFUKdhS_1.wireOp",EDGE,"1cb9c079-ea9b-4899-8069-e0e3048e911d.sketch_text.stroke-33"),sQuery(id+"FHMxAyK4CFUKdhS_1.wireOp",EDGE,"1cb9c079-ea9b-4899-8069-e0e3048e911d.sketch_text.stroke-34"),sQuery(id+"FHMxAyK4CFUKdhS_1.wireOp",EDGE,"1cb9c079-ea9b-4899-8069-e0e3048e911d.sketch_text.stroke-35"),sQuery(id+"FHMxAyK4CFUKdhS_1.wireOp",EDGE,"1cb9c079-ea9b-4899-8069-e0e3048e911d.sketch_text.stroke-36"),sQuery(id+"FHMxAyK4CFUKdhS_1.wireOp",EDGE,"1cb9c079-ea9b-4899-8069-e0e3048e911d.sketch_text.stroke-37"),sQuery(id+"FHMxAyK4CFUKdhS_1.wireOp",EDGE,"1cb9c079-ea9b-4899-8069-e0e3048e911d.sketch_text.stroke-38"),sQuery(id+"FHMxAyK4CFUKdhS_1.wireOp",EDGE,"1cb9c079-ea9b-4899-8069-e0e3048e911d.sketch_text.stroke-39"),sQuery(id+"FHMxAyK4CFUKdhS_1.wireOp",EDGE,"1cb9c079-ea9b-4899-8069-e0e3048e911d.sketch_text.stroke-40"),sQuery(id+"FHMxAyK4CFUKdhS_1.wireOp",EDGE,"1cb9c079-ea9b-4899-8069-e0e3048e911d.sketch_text.stroke-41"),sQuery(id+"FHMxAyK4CFUKdhS_1.wireOp",EDGE,"1cb9c079-ea9b-4899-8069-e0e3048e911d.sketch_text.stroke-42"),sQuery(id+"FHMxAyK4CFUKdhS_1.wireOp",EDGE,"1cb9c079-ea9b-4899-8069-e0e3048e911d.sketch_text.stroke-43"),sQuery(id+"FHMxAyK4CFUKdhS_1.wireOp",EDGE,"1cb9c079-ea9b-4899-8069-e0e3048e911d.sketch_text.stroke-44"),sQuery(id+"FHMxAyK4CFUKdhS_1.wireOp",EDGE,"1cb9c079-ea9b-4899-8069-e0e3048e911d.sketch_text.stroke-45"),sQuery(id+"FHMxAyK4CFUKdhS_1.wireOp",EDGE,"1cb9c079-ea9b-4899-8069-e0e3048e911d.sketch_text.stroke-46"),sQuery(id+"FHMxAyK4CFUKdhS_1.wireOp",EDGE,"1cb9c079-ea9b-4899-8069-e0e3048e911d.sketch_text.stroke-47"),sQuery(id+"FHMxAyK4CFUKdhS_1.wireOp",EDGE,"1cb9c079-ea9b-4899-8069-e0e3048e911d.sketch_text.stroke-48"),sQuery(id+"FHMxAyK4CFUKdhS_1.wireOp",EDGE,"1cb9c079-ea9b-4899-8069-e0e3048e911d.sketch_text.stroke-49"),sQuery(id+"FHMxAyK4CFUKdhS_1.wireOp",EDGE,"1cb9c079-ea9b-4899-8069-e0e3048e911d.sketch_text.stroke-50"),sQuery(id+"FHMxAyK4CFUKdhS_1.wireOp",EDGE,"1cb9c079-ea9b-4899-8069-e0e3048e911d.sketch_text.stroke-51"),sQuery(id+"FHMxAyK4CFUKdhS_1.wireOp",EDGE,"1cb9c079-ea9b-4899-8069-e0e3048e911d.sketch_text.stroke-52"),sQuery(id+"FHMxAyK4CFUKdhS_1.wireOp",EDGE,"1cb9c079-ea9b-4899-8069-e0e3048e911d.sketch_text.stroke-53"),sQuery(id+"FHMxAyK4CFUKdhS_1.wireOp",EDGE,"1cb9c079-ea9b-4899-8069-e0e3048e911d.sketch_text.stroke-54"),sQuery(id+"FHMxAyK4CFUKdhS_1.wireOp",EDGE,"1cb9c079-ea9b-4899-8069-e0e3048e911d.sketch_text.stroke-55"),sQuery(id+"FHMxAyK4CFUKdhS_1.wireOp",EDGE,"1cb9c079-ea9b-4899-8069-e0e3048e911d.sketch_text.stroke-56"),sQuery(id+"FHMxAyK4CFUKdhS_1.wireOp",EDGE,"1cb9c079-ea9b-4899-8069-e0e3048e911d.sketch_text.stroke-57"),sQuery(id+"FHMxAyK4CFUKdhS_1.wireOp",EDGE,"1cb9c079-ea9b-4899-8069-e0e3048e911d.sketch_text.stroke-58"),sQuery(id+"FHMxAyK4CFUKdhS_1.wireOp",EDGE,"1cb9c079-ea9b-4899-8069-e0e3048e911d.sketch_text.stroke-59"),sQuery(id+"FHMxAyK4CFUKdhS_1.wireOp",EDGE,"1cb9c079-ea9b-4899-8069-e0e3048e911d.sketch_text.stroke-60"),sQuery(id+"FHMxAyK4CFUKdhS_1.wireOp",EDGE,"1cb9c079-ea9b-4899-8069-e0e3048e911d.sketch_text.stroke-61"),sQuery(id+"FHMxAyK4CFUKdhS_1.wireOp",EDGE,"1cb9c079-ea9b-4899-8069-e0e3048e911d.sketch_text.stroke-62"),sQuery(id+"FHMxAyK4CFUKdhS_1.wireOp",EDGE,"1cb9c079-ea9b-4899-8069-e0e3048e911d.sketch_text.stroke-71"),sQuery(id+"FHMxAyK4CFUKdhS_1.wireOp",EDGE,"1cb9c079-ea9b-4899-8069-e0e3048e911d.sketch_text.stroke-72"),sQuery(id+"FHMxAyK4CFUKdhS_1.wireOp",EDGE,"1cb9c079-ea9b-4899-8069-e0e3048e911d.sketch_text.stroke-73"),sQuery(id+"FHMxAyK4CFUKdhS_1.wireOp",EDGE,"1cb9c079-ea9b-4899-8069-e0e3048e911d.sketch_text.stroke-74"),sQuery(id+"FHMxAyK4CFUKdhS_1.wireOp",EDGE,"1cb9c079-ea9b-4899-8069-e0e3048e911d.sketch_text.stroke-75"),sQuery(id+"FHMxAyK4CFUKdhS_1.wireOp",EDGE,"1cb9c079-ea9b-4899-8069-e0e3048e911d.sketch_text.stroke-76"),sQuery(id+"FHMxAyK4CFUKdhS_1.wireOp",EDGE,"1cb9c079-ea9b-4899-8069-e0e3048e911d.sketch_text.stroke-77"),sQuery(id+"FHMxAyK4CFUKdhS_1.wireOp",EDGE,"1cb9c079-ea9b-4899-8069-e0e3048e911d.sketch_text.stroke-78"),sQuery(id+"FHMxAyK4CFUKdhS_1.wireOp",EDGE,"1cb9c079-ea9b-4899-8069-e0e3048e911d.sketch_text.stroke-79"),sQuery(id+"FHMxAyK4CFUKdhS_1.wireOp",EDGE,"1cb9c079-ea9b-4899-8069-e0e3048e911d.sketch_text.stroke-80"),sQuery(id+"FHMxAyK4CFUKdhS_1.wireOp",EDGE,"1cb9c079-ea9b-4899-8069-e0e3048e911d.sketch_text.stroke-81"),sQuery(id+"FHMxAyK4CFUKdhS_1.wireOp",EDGE,"1cb9c079-ea9b-4899-8069-e0e3048e911d.sketch_text.stroke-82"),sQuery(id+"FHMxAyK4CFUKdhS_1.wireOp",EDGE,"1cb9c079-ea9b-4899-8069-e0e3048e911d.sketch_text.stroke-83"),sQuery(id+"FHMxAyK4CFUKdhS_1.wireOp",EDGE,"1cb9c079-ea9b-4899-8069-e0e3048e911d.sketch_text.stroke-84"),sQuery(id+"FHMxAyK4CFUKdhS_1.wireOp",EDGE,"1cb9c079-ea9b-4899-8069-e0e3048e911d.sketch_text.stroke-85"),sQuery(id+"FHMxAyK4CFUKdhS_1.wireOp",EDGE,"1cb9c079-ea9b-4899-8069-e0e3048e911d.sketch_text.stroke-86"),sQuery(id+"FHMxAyK4CFUKdhS_1.wireOp",EDGE,"1cb9c079-ea9b-4899-8069-e0e3048e911d.sketch_text.stroke-87"),sQuery(id+"FHMxAyK4CFUKdhS_1.wireOp",EDGE,"1cb9c079-ea9b-4899-8069-e0e3048e911d.sketch_text.stroke-88"),sQuery(id+"FHMxAyK4CFUKdhS_1.wireOp",EDGE,"1cb9c079-ea9b-4899-8069-e0e3048e911d.sketch_text.stroke-89"),sQuery(id+"FHMxAyK4CFUKdhS_1.wireOp",EDGE,"1cb9c079-ea9b-4899-8069-e0e3048e911d.sketch_text.stroke-90"),sQuery(id+"FHMxAyK4CFUKdhS_1.wireOp",EDGE,"1cb9c079-ea9b-4899-8069-e0e3048e911d.sketch_text.stroke-91"),sQuery(id+"FHMxAyK4CFUKdhS_1.wireOp",EDGE,"1cb9c079-ea9b-4899-8069-e0e3048e911d.sketch_text.stroke-92"),sQuery(id+"FHMxAyK4CFUKdhS_1.wireOp",EDGE,"1cb9c079-ea9b-4899-8069-e0e3048e911d.sketch_text.stroke-93"),sQuery(id+"FHMxAyK4CFUKdhS_1.wireOp",EDGE,"1cb9c079-ea9b-4899-8069-e0e3048e911d.sketch_text.stroke-94"),sQuery(id+"FHMxAyK4CFUKdhS_1.wireOp",EDGE,"1cb9c079-ea9b-4899-8069-e0e3048e911d.sketch_text.stroke-95"),sQuery(id+"FHMxAyK4CFUKdhS_1.wireOp",EDGE,"1cb9c079-ea9b-4899-8069-e0e3048e911d.sketch_text.stroke-96"),sQuery(id+"FHMxAyK4CFUKdhS_1.wireOp",EDGE,"1cb9c079-ea9b-4899-8069-e0e3048e911d.sketch_text.stroke-97"),sQuery(id+"FHMxAyK4CFUKdhS_1.wireOp",EDGE,"1cb9c079-ea9b-4899-8069-e0e3048e911d.sketch_text.stroke-103"),sQuery(id+"FHMxAyK4CFUKdhS_1.wireOp",EDGE,"1cb9c079-ea9b-4899-8069-e0e3048e911d.sketch_text.stroke-104"),sQuery(id+"FHMxAyK4CFUKdhS_1.wireOp",EDGE,"1cb9c079-ea9b-4899-8069-e0e3048e911d.sketch_text.stroke-105"),sQuery(id+"FHMxAyK4CFUKdhS_1.wireOp",EDGE,"1cb9c079-ea9b-4899-8069-e0e3048e911d.sketch_text.stroke-106"),sQuery(id+"FHMxAyK4CFUKdhS_1.wireOp",EDGE,"1cb9c079-ea9b-4899-8069-e0e3048e911d.sketch_text.stroke-107"),sQuery(id+"FHMxAyK4CFUKdhS_1.wireOp",EDGE,"1cb9c079-ea9b-4899-8069-e0e3048e911d.sketch_text.stroke-108"),sQuery(id+"FHMxAyK4CFUKdhS_1.wireOp",EDGE,"1cb9c079-ea9b-4899-8069-e0e3048e911d.sketch_text.stroke-109"),sQuery(id+"FHMxAyK4CFUKdhS_1.wireOp",EDGE,"1cb9c079-ea9b-4899-8069-e0e3048e911d.sketch_text.stroke-110"),sQuery(id+"FHMxAyK4CFUKdhS_1.wireOp",EDGE,"1cb9c079-ea9b-4899-8069-e0e3048e911d.sketch_text.stroke-111"),sQuery(id+"FHMxAyK4CFUKdhS_1.wireOp",EDGE,"1cb9c079-ea9b-4899-8069-e0e3048e911d.sketch_text.stroke-112"),sQuery(id+"FHMxAyK4CFUKdhS_1.wireOp",EDGE,"1cb9c079-ea9b-4899-8069-e0e3048e911d.sketch_text.stroke-113"),sQuery(id+"FHMxAyK4CFUKdhS_1.wireOp",EDGE,"1cb9c079-ea9b-4899-8069-e0e3048e911d.sketch_text.stroke-114"),sQuery(id+"FHMxAyK4CFUKdhS_1.wireOp",EDGE,"1cb9c079-ea9b-4899-8069-e0e3048e911d.sketch_text.stroke-115"),sQuery(id+"FHMxAyK4CFUKdhS_1.wireOp",EDGE,"1cb9c079-ea9b-4899-8069-e0e3048e911d.sketch_text.stroke-116"),sQuery(id+"FHMxAyK4CFUKdhS_1.wireOp",EDGE,"1cb9c079-ea9b-4899-8069-e0e3048e911d.sketch_text.stroke-117"),sQuery(id+"FHMxAyK4CFUKdhS_1.wireOp",EDGE,"1cb9c079-ea9b-4899-8069-e0e3048e911d.sketch_text.stroke-118"),sQuery(id+"FHMxAyK4CFUKdhS_1.wireOp",EDGE,"1cb9c079-ea9b-4899-8069-e0e3048e911d.sketch_text.stroke-119"),sQuery(id+"FHMxAyK4CFUKdhS_1.wireOp",EDGE,"1cb9c079-ea9b-4899-8069-e0e3048e911d.sketch_text.stroke-120"),sQuery(id+"FHMxAyK4CFUKdhS_1.wireOp",EDGE,"1cb9c079-ea9b-4899-8069-e0e3048e911d.sketch_text.stroke-121"),sQuery(id+"FHMxAyK4CFUKdhS_1.wireOp",EDGE,"1cb9c079-ea9b-4899-8069-e0e3048e911d.sketch_text.stroke-122"),sQuery(id+"FHMxAyK4CFUKdhS_1.wireOp",EDGE,"1cb9c079-ea9b-4899-8069-e0e3048e911d.sketch_text.stroke-123"),sQuery(id+"FHMxAyK4CFUKdhS_1.wireOp",EDGE,"1cb9c079-ea9b-4899-8069-e0e3048e911d.sketch_text.stroke-124"),sQuery(id+"FHMxAyK4CFUKdhS_1.wireOp",EDGE,"1cb9c079-ea9b-4899-8069-e0e3048e911d.sketch_text.stroke-125"),sQuery(id+"FHMxAyK4CFUKdhS_1.wireOp",EDGE,"1cb9c079-ea9b-4899-8069-e0e3048e911d.sketch_text.stroke-126"),sQuery(id+"FHMxAyK4CFUKdhS_1.wireOp",EDGE,"1cb9c079-ea9b-4899-8069-e0e3048e911d.sketch_text.stroke-127"),sQuery(id+"FHMxAyK4CFUKdhS_1.wireOp",EDGE,"1cb9c079-ea9b-4899-8069-e0e3048e911d.sketch_text.stroke-128"),sQuery(id+"FHMxAyK4CFUKdhS_1.wireOp",EDGE,"1cb9c079-ea9b-4899-8069-e0e3048e911d.sketch_text.stroke-129"),sQuery(id+"FHMxAyK4CFUKdhS_1.wireOp",EDGE,"1cb9c079-ea9b-4899-8069-e0e3048e911d.sketch_text.stroke-130"),sQuery(id+"FHMxAyK4CFUKdhS_1.wireOp",EDGE,"1cb9c079-ea9b-4899-8069-e0e3048e911d.sketch_text.stroke-131"),sQuery(id+"FHMxAyK4CFUKdhS_1.wireOp",EDGE,"1cb9c079-ea9b-4899-8069-e0e3048e911d.sketch_text.stroke-132"),sQuery(id+"FHMxAyK4CFUKdhS_1.wireOp",EDGE,"1cb9c079-ea9b-4899-8069-e0e3048e911d.sketch_text.stroke-133"),sQuery(id+"FHMxAyK4CFUKdhS_1.wireOp",EDGE,"1cb9c079-ea9b-4899-8069-e0e3048e911d.sketch_text.stroke-134"),sQuery(id+"FHMxAyK4CFUKdhS_1.wireOp",EDGE,"1cb9c079-ea9b-4899-8069-e0e3048e911d.sketch_text.stroke-135"),sQuery(id+"FHMxAyK4CFUKdhS_1.wireOp",EDGE,"1cb9c079-ea9b-4899-8069-e0e3048e911d.sketch_text.stroke-136"),sQuery(id+"FHMxAyK4CFUKdhS_1.wireOp",EDGE,"1cb9c079-ea9b-4899-8069-e0e3048e911d.sketch_text.stroke-137"),sQuery(id+"FHMxAyK4CFUKdhS_1.wireOp",EDGE,"1cb9c079-ea9b-4899-8069-e0e3048e911d.sketch_text.stroke-138"),sQuery(id+"FHMxAyK4CFUKdhS_1.wireOp",EDGE,"1cb9c079-ea9b-4899-8069-e0e3048e911d.sketch_text.stroke-139"),sQuery(id+"FHMxAyK4CFUKdhS_1.wireOp",EDGE,"1cb9c079-ea9b-4899-8069-e0e3048e911d.sketch_text.stroke-140"),sQuery(id+"FHMxAyK4CFUKdhS_1.wireOp",EDGE,"1cb9c079-ea9b-4899-8069-e0e3048e911d.sketch_text.stroke-141"),sQuery(id+"FHMxAyK4CFUKdhS_1.wireOp",EDGE,"1cb9c079-ea9b-4899-8069-e0e3048e911d.sketch_text.stroke-142"),sQuery(id+"FHMxAyK4CFUKdhS_1.wireOp",EDGE,"1cb9c079-ea9b-4899-8069-e0e3048e911d.sketch_text.stroke-143"),sQuery(id+"FHMxAyK4CFUKdhS_1.wireOp",EDGE,"1cb9c079-ea9b-4899-8069-e0e3048e911d.sketch_text.stroke-144"),sQuery(id+"FHMxAyK4CFUKdhS_1.wireOp",EDGE,"1cb9c079-ea9b-4899-8069-e0e3048e911d.sketch_text.stroke-145"),sQuery(id+"FHMxAyK4CFUKdhS_1.wireOp",EDGE,"1cb9c079-ea9b-4899-8069-e0e3048e911d.sketch_text.stroke-146"),sQuery(id+"FHMxAyK4CFUKdhS_1.wireOp",EDGE,"1cb9c079-ea9b-4899-8069-e0e3048e911d.sketch_text.stroke-147"),sQuery(id+"FHMxAyK4CFUKdhS_1.wireOp",EDGE,"1cb9c079-ea9b-4899-8069-e0e3048e911d.sketch_text.stroke-148"),sQuery(id+"FHMxAyK4CFUKdhS_1.wireOp",EDGE,"1cb9c079-ea9b-4899-8069-e0e3048e911d.sketch_text.stroke-149"),sQuery(id+"FHMxAyK4CFUKdhS_1.wireOp",EDGE,"1cb9c079-ea9b-4899-8069-e0e3048e911d.sketch_text.stroke-150"),sQuery(id+"FHMxAyK4CFUKdhS_1.wireOp",EDGE,"1cb9c079-ea9b-4899-8069-e0e3048e911d.sketch_text.stroke-151"),sQuery(id+"FHMxAyK4CFUKdhS_1.wireOp",EDGE,"1cb9c079-ea9b-4899-8069-e0e3048e911d.sketch_text.stroke-152"),sQuery(id+"FHMxAyK4CFUKdhS_1.wireOp",EDGE,"1cb9c079-ea9b-4899-8069-e0e3048e911d.sketch_text.stroke-153"),sQuery(id+"FHMxAyK4CFUKdhS_1.wireOp",EDGE,"1cb9c079-ea9b-4899-8069-e0e3048e911d.sketch_text.stroke-159"),sQuery(id+"FHMxAyK4CFUKdhS_1.wireOp",EDGE,"1cb9c079-ea9b-4899-8069-e0e3048e911d.sketch_text.stroke-160"),sQuery(id+"FHMxAyK4CFUKdhS_1.wireOp",EDGE,"1cb9c079-ea9b-4899-8069-e0e3048e911d.sketch_text.stroke-161"),sQuery(id+"FHMxAyK4CFUKdhS_1.wireOp",EDGE,"1cb9c079-ea9b-4899-8069-e0e3048e911d.sketch_text.stroke-162"),sQuery(id+"FHMxAyK4CFUKdhS_1.wireOp",EDGE,"1cb9c079-ea9b-4899-8069-e0e3048e911d.sketch_text.stroke-163"),sQuery(id+"FHMxAyK4CFUKdhS_1.wireOp",EDGE,"1cb9c079-ea9b-4899-8069-e0e3048e911d.sketch_text.stroke-164"),sQuery(id+"FHMxAyK4CFUKdhS_1.wireOp",EDGE,"1cb9c079-ea9b-4899-8069-e0e3048e911d.sketch_text.stroke-165"),sQuery(id+"FHMxAyK4CFUKdhS_1.wireOp",EDGE,"1cb9c079-ea9b-4899-8069-e0e3048e911d.sketch_text.stroke-166"),sQuery(id+"FHMxAyK4CFUKdhS_1.wireOp",EDGE,"1cb9c079-ea9b-4899-8069-e0e3048e911d.sketch_text.stroke-167"),sQuery(id+"FHMxAyK4CFUKdhS_1.wireOp",EDGE,"1cb9c079-ea9b-4899-8069-e0e3048e911d.sketch_text.stroke-168"),sQuery(id+"FHMxAyK4CFUKdhS_1.wireOp",EDGE,"1cb9c079-ea9b-4899-8069-e0e3048e911d.sketch_text.stroke-169"),sQuery(id+"FHMxAyK4CFUKdhS_1.wireOp",EDGE,"1cb9c079-ea9b-4899-8069-e0e3048e911d.sketch_text.stroke-170"),sQuery(id+"FHMxAyK4CFUKdhS_1.wireOp",EDGE,"1cb9c079-ea9b-4899-8069-e0e3048e911d.sketch_text.stroke-171"),sQuery(id+"FHMxAyK4CFUKdhS_1.wireOp",EDGE,"1cb9c079-ea9b-4899-8069-e0e3048e911d.sketch_text.stroke-172"),sQuery(id+"FHMxAyK4CFUKdhS_1.wireOp",EDGE,"1cb9c079-ea9b-4899-8069-e0e3048e911d.sketch_text.stroke-173"),sQuery(id+"FHMxAyK4CFUKdhS_1.wireOp",EDGE,"1cb9c079-ea9b-4899-8069-e0e3048e911d.sketch_text.stroke-174"),sQuery(id+"FHMxAyK4CFUKdhS_1.wireOp",EDGE,"1cb9c079-ea9b-4899-8069-e0e3048e911d.sketch_text.stroke-175"),sQuery(id+"FHMxAyK4CFUKdhS_1.wireOp",EDGE,"1cb9c079-ea9b-4899-8069-e0e3048e911d.sketch_text.stroke-176"),sQuery(id+"FHMxAyK4CFUKdhS_1.wireOp",EDGE,"1cb9c079-ea9b-4899-8069-e0e3048e911d.sketch_text.stroke-177"),sQuery(id+"FHMxAyK4CFUKdhS_1.wireOp",EDGE,"1cb9c079-ea9b-4899-8069-e0e3048e911d.sketch_text.stroke-178"),sQuery(id+"FHMxAyK4CFUKdhS_1.wireOp",EDGE,"1cb9c079-ea9b-4899-8069-e0e3048e911d.sketch_text.stroke-179"),sQuery(id+"FHMxAyK4CFUKdhS_1.wireOp",EDGE,"1cb9c079-ea9b-4899-8069-e0e3048e911d.sketch_text.stroke-180"),sQuery(id+"F3.wireOp",EDGE,"727ac2c1-f511-4829-95a7-a443ef16a4cd"),subQ2])],"isStart":true}),makeQuery(id+"F4.opExtrude","SWEPT_FACE",FACE,{"disambiguationData":[OSD([subQ2])]})]),OD(0.0)],"derivedFrom":makeQuery(id+"F1.opExtrude","CAP_EDGE",EDGE,{"disambiguationData":[OSD([subQ0])],"isStart":false})});}
            var Q19;
            {var subQ0=sQuery(id+"F0.wireOp",EDGE,"E0.top");var subQ1=sQuery(id+"F0.wireOp",EDGE,"E0.bottom");var subQ2=sQuery(id+"F3.wireOp",EDGE,"1a034e28-a7c2-419d-97de-c33d70a47301");Q19=makeQuery(id+"F4.boolean.opBoolean","SPLIT",EDGE,{"disambiguationData":[TD([makeQuery(id+"F1.opExtrude","CAP_FACE",FACE,{"disambiguationData":[OSD([subQ1,subQ0,sQuery(id+"F0.wireOp",EDGE,"E0.left"),sQuery(id+"F0.wireOp",EDGE,"E0.right")])],"isStart":false}),makeQuery(id+"F1.opExtrude","SWEPT_FACE",FACE,{"disambiguationData":[OSD([subQ0])]}),makeQuery(id+"F4.opExtrude","CAP_FACE",FACE,{"disambiguationData":[OSD([subQ1,sQuery(id+"F2.wireOp",EDGE,"fcba4419-a2ee-464f-be9d-58f11bf3418b.sketch_text.stroke-0"),sQuery(id+"F2.wireOp",EDGE,"fcba4419-a2ee-464f-be9d-58f11bf3418b.sketch_text.stroke-1"),sQuery(id+"F2.wireOp",EDGE,"fcba4419-a2ee-464f-be9d-58f11bf3418b.sketch_text.stroke-2"),sQuery(id+"F2.wireOp",EDGE,"fcba4419-a2ee-464f-be9d-58f11bf3418b.sketch_text.stroke-3"),sQuery(id+"F2.wireOp",EDGE,"fcba4419-a2ee-464f-be9d-58f11bf3418b.sketch_text.stroke-4"),sQuery(id+"F2.wireOp",EDGE,"fcba4419-a2ee-464f-be9d-58f11bf3418b.sketch_text.stroke-5"),sQuery(id+"F2.wireOp",EDGE,"fcba4419-a2ee-464f-be9d-58f11bf3418b.sketch_text.stroke-6"),sQuery(id+"F2.wireOp",EDGE,"fcba4419-a2ee-464f-be9d-58f11bf3418b.sketch_text.stroke-7"),sQuery(id+"F2.wireOp",EDGE,"fcba4419-a2ee-464f-be9d-58f11bf3418b.sketch_text.stroke-8"),sQuery(id+"F2.wireOp",EDGE,"fcba4419-a2ee-464f-be9d-58f11bf3418b.sketch_text.stroke-9"),sQuery(id+"F2.wireOp",EDGE,"fcba4419-a2ee-464f-be9d-58f11bf3418b.sketch_text.stroke-10"),sQuery(id+"F2.wireOp",EDGE,"fcba4419-a2ee-464f-be9d-58f11bf3418b.sketch_text.stroke-11"),sQuery(id+"F2.wireOp",EDGE,"fcba4419-a2ee-464f-be9d-58f11bf3418b.sketch_text.stroke-12"),sQuery(id+"F2.wireOp",EDGE,"fcba4419-a2ee-464f-be9d-58f11bf3418b.sketch_text.stroke-13"),sQuery(id+"F2.wireOp",EDGE,"fcba4419-a2ee-464f-be9d-58f11bf3418b.sketch_text.stroke-14"),sQuery(id+"F2.wireOp",EDGE,"fcba4419-a2ee-464f-be9d-58f11bf3418b.sketch_text.stroke-15"),sQuery(id+"F2.wireOp",EDGE,"fcba4419-a2ee-464f-be9d-58f11bf3418b.sketch_text.stroke-16"),sQuery(id+"F2.wireOp",EDGE,"fcba4419-a2ee-464f-be9d-58f11bf3418b.sketch_text.stroke-17"),sQuery(id+"F2.wireOp",EDGE,"fcba4419-a2ee-464f-be9d-58f11bf3418b.sketch_text.stroke-18"),sQuery(id+"F2.wireOp",EDGE,"fcba4419-a2ee-464f-be9d-58f11bf3418b.sketch_text.stroke-19"),sQuery(id+"F2.wireOp",EDGE,"fcba4419-a2ee-464f-be9d-58f11bf3418b.sketch_text.stroke-20"),sQuery(id+"F2.wireOp",EDGE,"fcba4419-a2ee-464f-be9d-58f11bf3418b.sketch_text.stroke-21"),sQuery(id+"F2.wireOp",EDGE,"fcba4419-a2ee-464f-be9d-58f11bf3418b.sketch_text.stroke-22"),sQuery(id+"F2.wireOp",EDGE,"fcba4419-a2ee-464f-be9d-58f11bf3418b.sketch_text.stroke-23"),sQuery(id+"F2.wireOp",EDGE,"fcba4419-a2ee-464f-be9d-58f11bf3418b.sketch_text.stroke-24"),sQuery(id+"F2.wireOp",EDGE,"fcba4419-a2ee-464f-be9d-58f11bf3418b.sketch_text.stroke-25"),sQuery(id+"F2.wireOp",EDGE,"fcba4419-a2ee-464f-be9d-58f11bf3418b.sketch_text.stroke-26"),sQuery(id+"F2.wireOp",EDGE,"fcba4419-a2ee-464f-be9d-58f11bf3418b.sketch_text.stroke-27"),sQuery(id+"F2.wireOp",EDGE,"fcba4419-a2ee-464f-be9d-58f11bf3418b.sketch_text.stroke-28"),sQuery(id+"F2.wireOp",EDGE,"fcba4419-a2ee-464f-be9d-58f11bf3418b.sketch_text.stroke-29"),sQuery(id+"F2.wireOp",EDGE,"fcba4419-a2ee-464f-be9d-58f11bf3418b.sketch_text.stroke-30"),sQuery(id+"F2.wireOp",EDGE,"fcba4419-a2ee-464f-be9d-58f11bf3418b.sketch_text.stroke-31"),sQuery(id+"F2.wireOp",EDGE,"fcba4419-a2ee-464f-be9d-58f11bf3418b.sketch_text.stroke-32"),sQuery(id+"F2.wireOp",EDGE,"fcba4419-a2ee-464f-be9d-58f11bf3418b.sketch_text.stroke-33"),sQuery(id+"F2.wireOp",EDGE,"fcba4419-a2ee-464f-be9d-58f11bf3418b.sketch_text.stroke-34"),sQuery(id+"F2.wireOp",EDGE,"fcba4419-a2ee-464f-be9d-58f11bf3418b.sketch_text.stroke-35"),sQuery(id+"F2.wireOp",EDGE,"fcba4419-a2ee-464f-be9d-58f11bf3418b.sketch_text.stroke-36"),sQuery(id+"F2.wireOp",EDGE,"fcba4419-a2ee-464f-be9d-58f11bf3418b.sketch_text.stroke-37"),sQuery(id+"F2.wireOp",EDGE,"fcba4419-a2ee-464f-be9d-58f11bf3418b.sketch_text.stroke-38"),sQuery(id+"F2.wireOp",EDGE,"fcba4419-a2ee-464f-be9d-58f11bf3418b.sketch_text.stroke-39"),sQuery(id+"F2.wireOp",EDGE,"fcba4419-a2ee-464f-be9d-58f11bf3418b.sketch_text.stroke-40"),sQuery(id+"F2.wireOp",EDGE,"fcba4419-a2ee-464f-be9d-58f11bf3418b.sketch_text.stroke-41"),sQuery(id+"F2.wireOp",EDGE,"fcba4419-a2ee-464f-be9d-58f11bf3418b.sketch_text.stroke-42"),sQuery(id+"F2.wireOp",EDGE,"fcba4419-a2ee-464f-be9d-58f11bf3418b.sketch_text.stroke-43"),sQuery(id+"F2.wireOp",EDGE,"fcba4419-a2ee-464f-be9d-58f11bf3418b.sketch_text.stroke-44"),sQuery(id+"F2.wireOp",EDGE,"fcba4419-a2ee-464f-be9d-58f11bf3418b.sketch_text.stroke-45"),sQuery(id+"F2.wireOp",EDGE,"fcba4419-a2ee-464f-be9d-58f11bf3418b.sketch_text.stroke-46"),sQuery(id+"F2.wireOp",EDGE,"fcba4419-a2ee-464f-be9d-58f11bf3418b.sketch_text.stroke-47"),sQuery(id+"F2.wireOp",EDGE,"fcba4419-a2ee-464f-be9d-58f11bf3418b.sketch_text.stroke-48"),sQuery(id+"F2.wireOp",EDGE,"fcba4419-a2ee-464f-be9d-58f11bf3418b.sketch_text.stroke-49"),sQuery(id+"F2.wireOp",EDGE,"fcba4419-a2ee-464f-be9d-58f11bf3418b.sketch_text.stroke-50"),sQuery(id+"F2.wireOp",EDGE,"fcba4419-a2ee-464f-be9d-58f11bf3418b.sketch_text.stroke-51"),sQuery(id+"F2.wireOp",EDGE,"fcba4419-a2ee-464f-be9d-58f11bf3418b.sketch_text.stroke-52"),sQuery(id+"F2.wireOp",EDGE,"fcba4419-a2ee-464f-be9d-58f11bf3418b.sketch_text.stroke-53"),sQuery(id+"F2.wireOp",EDGE,"fcba4419-a2ee-464f-be9d-58f11bf3418b.sketch_text.stroke-54"),sQuery(id+"F2.wireOp",EDGE,"fcba4419-a2ee-464f-be9d-58f11bf3418b.sketch_text.stroke-55"),sQuery(id+"F2.wireOp",EDGE,"fcba4419-a2ee-464f-be9d-58f11bf3418b.sketch_text.stroke-56"),sQuery(id+"F2.wireOp",EDGE,"fcba4419-a2ee-464f-be9d-58f11bf3418b.sketch_text.stroke-57"),sQuery(id+"F2.wireOp",EDGE,"fcba4419-a2ee-464f-be9d-58f11bf3418b.sketch_text.stroke-58"),sQuery(id+"F2.wireOp",EDGE,"fcba4419-a2ee-464f-be9d-58f11bf3418b.sketch_text.stroke-59"),sQuery(id+"F2.wireOp",EDGE,"fcba4419-a2ee-464f-be9d-58f11bf3418b.sketch_text.stroke-60"),sQuery(id+"F2.wireOp",EDGE,"fcba4419-a2ee-464f-be9d-58f11bf3418b.sketch_text.stroke-61"),sQuery(id+"F2.wireOp",EDGE,"fcba4419-a2ee-464f-be9d-58f11bf3418b.sketch_text.stroke-62"),sQuery(id+"F2.wireOp",EDGE,"fcba4419-a2ee-464f-be9d-58f11bf3418b.sketch_text.stroke-63"),sQuery(id+"F2.wireOp",EDGE,"fcba4419-a2ee-464f-be9d-58f11bf3418b.sketch_text.stroke-64"),sQuery(id+"F2.wireOp",EDGE,"fcba4419-a2ee-464f-be9d-58f11bf3418b.sketch_text.stroke-65"),sQuery(id+"F2.wireOp",EDGE,"fcba4419-a2ee-464f-be9d-58f11bf3418b.sketch_text.stroke-66"),sQuery(id+"F2.wireOp",EDGE,"fcba4419-a2ee-464f-be9d-58f11bf3418b.sketch_text.stroke-67"),sQuery(id+"F2.wireOp",EDGE,"fcba4419-a2ee-464f-be9d-58f11bf3418b.sketch_text.stroke-68"),sQuery(id+"F2.wireOp",EDGE,"fcba4419-a2ee-464f-be9d-58f11bf3418b.sketch_text.stroke-69"),sQuery(id+"F2.wireOp",EDGE,"fcba4419-a2ee-464f-be9d-58f11bf3418b.sketch_text.stroke-70"),sQuery(id+"F2.wireOp",EDGE,"fcba4419-a2ee-464f-be9d-58f11bf3418b.sketch_text.stroke-71"),sQuery(id+"F2.wireOp",EDGE,"fcba4419-a2ee-464f-be9d-58f11bf3418b.sketch_text.stroke-72"),sQuery(id+"F2.wireOp",EDGE,"fcba4419-a2ee-464f-be9d-58f11bf3418b.sketch_text.stroke-73"),sQuery(id+"F2.wireOp",EDGE,"fcba4419-a2ee-464f-be9d-58f11bf3418b.sketch_text.stroke-74"),sQuery(id+"F2.wireOp",EDGE,"fcba4419-a2ee-464f-be9d-58f11bf3418b.sketch_text.stroke-75"),sQuery(id+"F2.wireOp",EDGE,"fcba4419-a2ee-464f-be9d-58f11bf3418b.sketch_text.stroke-76"),sQuery(id+"F2.wireOp",EDGE,"fcba4419-a2ee-464f-be9d-58f11bf3418b.sketch_text.stroke-77"),sQuery(id+"F2.wireOp",EDGE,"fcba4419-a2ee-464f-be9d-58f11bf3418b.sketch_text.stroke-78"),sQuery(id+"F2.wireOp",EDGE,"fcba4419-a2ee-464f-be9d-58f11bf3418b.sketch_text.stroke-79"),sQuery(id+"F2.wireOp",EDGE,"fcba4419-a2ee-464f-be9d-58f11bf3418b.sketch_text.stroke-80"),sQuery(id+"F2.wireOp",EDGE,"fcba4419-a2ee-464f-be9d-58f11bf3418b.sketch_text.stroke-81"),sQuery(id+"F2.wireOp",EDGE,"fcba4419-a2ee-464f-be9d-58f11bf3418b.sketch_text.stroke-82"),sQuery(id+"F2.wireOp",EDGE,"fcba4419-a2ee-464f-be9d-58f11bf3418b.sketch_text.stroke-83"),sQuery(id+"F2.wireOp",EDGE,"fcba4419-a2ee-464f-be9d-58f11bf3418b.sketch_text.stroke-84"),sQuery(id+"F2.wireOp",EDGE,"fcba4419-a2ee-464f-be9d-58f11bf3418b.sketch_text.stroke-85"),sQuery(id+"F2.wireOp",EDGE,"fcba4419-a2ee-464f-be9d-58f11bf3418b.sketch_text.stroke-86"),sQuery(id+"F2.wireOp",EDGE,"fcba4419-a2ee-464f-be9d-58f11bf3418b.sketch_text.stroke-87"),sQuery(id+"F2.wireOp",EDGE,"fcba4419-a2ee-464f-be9d-58f11bf3418b.sketch_text.stroke-88"),sQuery(id+"F2.wireOp",EDGE,"fcba4419-a2ee-464f-be9d-58f11bf3418b.sketch_text.stroke-89"),sQuery(id+"F2.wireOp",EDGE,"fcba4419-a2ee-464f-be9d-58f11bf3418b.sketch_text.stroke-90"),sQuery(id+"F2.wireOp",EDGE,"fcba4419-a2ee-464f-be9d-58f11bf3418b.sketch_text.stroke-91"),sQuery(id+"F2.wireOp",EDGE,"fcba4419-a2ee-464f-be9d-58f11bf3418b.sketch_text.stroke-92"),sQuery(id+"F2.wireOp",EDGE,"fcba4419-a2ee-464f-be9d-58f11bf3418b.sketch_text.stroke-93"),sQuery(id+"F2.wireOp",EDGE,"fcba4419-a2ee-464f-be9d-58f11bf3418b.sketch_text.stroke-94"),sQuery(id+"F2.wireOp",EDGE,"fcba4419-a2ee-464f-be9d-58f11bf3418b.sketch_text.stroke-95"),sQuery(id+"F2.wireOp",EDGE,"fcba4419-a2ee-464f-be9d-58f11bf3418b.sketch_text.stroke-96"),sQuery(id+"F2.wireOp",EDGE,"fcba4419-a2ee-464f-be9d-58f11bf3418b.sketch_text.stroke-97"),sQuery(id+"F2.wireOp",EDGE,"fcba4419-a2ee-464f-be9d-58f11bf3418b.sketch_text.stroke-98"),sQuery(id+"F2.wireOp",EDGE,"fcba4419-a2ee-464f-be9d-58f11bf3418b.sketch_text.stroke-99"),sQuery(id+"F2.wireOp",EDGE,"fcba4419-a2ee-464f-be9d-58f11bf3418b.sketch_text.stroke-100"),sQuery(id+"F2.wireOp",EDGE,"fcba4419-a2ee-464f-be9d-58f11bf3418b.sketch_text.stroke-101"),sQuery(id+"F2.wireOp",EDGE,"fcba4419-a2ee-464f-be9d-58f11bf3418b.sketch_text.stroke-102"),sQuery(id+"F2.wireOp",EDGE,"fcba4419-a2ee-464f-be9d-58f11bf3418b.sketch_text.stroke-103"),sQuery(id+"F2.wireOp",EDGE,"fcba4419-a2ee-464f-be9d-58f11bf3418b.sketch_text.stroke-104"),sQuery(id+"F2.wireOp",EDGE,"fcba4419-a2ee-464f-be9d-58f11bf3418b.sketch_text.stroke-105"),sQuery(id+"F2.wireOp",EDGE,"fcba4419-a2ee-464f-be9d-58f11bf3418b.sketch_text.stroke-106"),sQuery(id+"F2.wireOp",EDGE,"fcba4419-a2ee-464f-be9d-58f11bf3418b.sketch_text.stroke-107"),sQuery(id+"F2.wireOp",EDGE,"fcba4419-a2ee-464f-be9d-58f11bf3418b.sketch_text.stroke-108"),sQuery(id+"F2.wireOp",EDGE,"fcba4419-a2ee-464f-be9d-58f11bf3418b.sketch_text.stroke-109"),sQuery(id+"F2.wireOp",EDGE,"fcba4419-a2ee-464f-be9d-58f11bf3418b.sketch_text.stroke-110"),sQuery(id+"F2.wireOp",EDGE,"fcba4419-a2ee-464f-be9d-58f11bf3418b.sketch_text.stroke-111"),sQuery(id+"F2.wireOp",EDGE,"fcba4419-a2ee-464f-be9d-58f11bf3418b.sketch_text.stroke-112"),sQuery(id+"F2.wireOp",EDGE,"fcba4419-a2ee-464f-be9d-58f11bf3418b.sketch_text.stroke-113"),sQuery(id+"F2.wireOp",EDGE,"fcba4419-a2ee-464f-be9d-58f11bf3418b.sketch_text.stroke-114"),sQuery(id+"F2.wireOp",EDGE,"fcba4419-a2ee-464f-be9d-58f11bf3418b.sketch_text.stroke-115"),sQuery(id+"F2.wireOp",EDGE,"fcba4419-a2ee-464f-be9d-58f11bf3418b.sketch_text.stroke-116"),sQuery(id+"F2.wireOp",EDGE,"fcba4419-a2ee-464f-be9d-58f11bf3418b.sketch_text.stroke-117"),sQuery(id+"F2.wireOp",EDGE,"fcba4419-a2ee-464f-be9d-58f11bf3418b.sketch_text.stroke-118"),sQuery(id+"F2.wireOp",EDGE,"fcba4419-a2ee-464f-be9d-58f11bf3418b.sketch_text.stroke-119"),sQuery(id+"F2.wireOp",EDGE,"fcba4419-a2ee-464f-be9d-58f11bf3418b.sketch_text.stroke-120"),sQuery(id+"F2.wireOp",EDGE,"fcba4419-a2ee-464f-be9d-58f11bf3418b.sketch_text.stroke-121"),sQuery(id+"F2.wireOp",EDGE,"fcba4419-a2ee-464f-be9d-58f11bf3418b.sketch_text.stroke-122"),sQuery(id+"F2.wireOp",EDGE,"fcba4419-a2ee-464f-be9d-58f11bf3418b.sketch_text.stroke-123"),sQuery(id+"F2.wireOp",EDGE,"fcba4419-a2ee-464f-be9d-58f11bf3418b.sketch_text.stroke-124"),sQuery(id+"F2.wireOp",EDGE,"fcba4419-a2ee-464f-be9d-58f11bf3418b.sketch_text.stroke-125"),sQuery(id+"F2.wireOp",EDGE,"fcba4419-a2ee-464f-be9d-58f11bf3418b.sketch_text.stroke-126"),sQuery(id+"F2.wireOp",EDGE,"fcba4419-a2ee-464f-be9d-58f11bf3418b.sketch_text.stroke-127"),sQuery(id+"F2.wireOp",EDGE,"fcba4419-a2ee-464f-be9d-58f11bf3418b.sketch_text.stroke-128"),sQuery(id+"F2.wireOp",EDGE,"fcba4419-a2ee-464f-be9d-58f11bf3418b.sketch_text.stroke-129"),sQuery(id+"F2.wireOp",EDGE,"fcba4419-a2ee-464f-be9d-58f11bf3418b.sketch_text.stroke-130"),sQuery(id+"F2.wireOp",EDGE,"fcba4419-a2ee-464f-be9d-58f11bf3418b.sketch_text.stroke-131"),sQuery(id+"F2.wireOp",EDGE,"fcba4419-a2ee-464f-be9d-58f11bf3418b.sketch_text.stroke-132"),sQuery(id+"F2.wireOp",EDGE,"fcba4419-a2ee-464f-be9d-58f11bf3418b.sketch_text.stroke-133"),sQuery(id+"F2.wireOp",EDGE,"fcba4419-a2ee-464f-be9d-58f11bf3418b.sketch_text.stroke-134"),sQuery(id+"F2.wireOp",EDGE,"fcba4419-a2ee-464f-be9d-58f11bf3418b.sketch_text.stroke-135"),sQuery(id+"F2.wireOp",EDGE,"fcba4419-a2ee-464f-be9d-58f11bf3418b.sketch_text.stroke-136"),sQuery(id+"F2.wireOp",EDGE,"fcba4419-a2ee-464f-be9d-58f11bf3418b.sketch_text.stroke-137"),sQuery(id+"F2.wireOp",EDGE,"fcba4419-a2ee-464f-be9d-58f11bf3418b.sketch_text.stroke-138"),sQuery(id+"F2.wireOp",EDGE,"fcba4419-a2ee-464f-be9d-58f11bf3418b.sketch_text.stroke-139"),sQuery(id+"F2.wireOp",EDGE,"fcba4419-a2ee-464f-be9d-58f11bf3418b.sketch_text.stroke-140"),sQuery(id+"F2.wireOp",EDGE,"fcba4419-a2ee-464f-be9d-58f11bf3418b.sketch_text.stroke-141"),sQuery(id+"F2.wireOp",EDGE,"fcba4419-a2ee-464f-be9d-58f11bf3418b.sketch_text.stroke-142"),sQuery(id+"F2.wireOp",EDGE,"fcba4419-a2ee-464f-be9d-58f11bf3418b.sketch_text.stroke-143"),sQuery(id+"F2.wireOp",EDGE,"fcba4419-a2ee-464f-be9d-58f11bf3418b.sketch_text.stroke-144"),sQuery(id+"F2.wireOp",EDGE,"fcba4419-a2ee-464f-be9d-58f11bf3418b.sketch_text.stroke-145"),sQuery(id+"F2.wireOp",EDGE,"fcba4419-a2ee-464f-be9d-58f11bf3418b.sketch_text.stroke-146"),sQuery(id+"F2.wireOp",EDGE,"fcba4419-a2ee-464f-be9d-58f11bf3418b.sketch_text.stroke-147"),sQuery(id+"F2.wireOp",EDGE,"fcba4419-a2ee-464f-be9d-58f11bf3418b.sketch_text.stroke-148"),sQuery(id+"F2.wireOp",EDGE,"fcba4419-a2ee-464f-be9d-58f11bf3418b.sketch_text.stroke-149"),sQuery(id+"F2.wireOp",EDGE,"fcba4419-a2ee-464f-be9d-58f11bf3418b.sketch_text.stroke-150"),sQuery(id+"F2.wireOp",EDGE,"fcba4419-a2ee-464f-be9d-58f11bf3418b.sketch_text.stroke-151"),sQuery(id+"F2.wireOp",EDGE,"fcba4419-a2ee-464f-be9d-58f11bf3418b.sketch_text.stroke-152"),sQuery(id+"F2.wireOp",EDGE,"fcba4419-a2ee-464f-be9d-58f11bf3418b.sketch_text.stroke-153"),sQuery(id+"F2.wireOp",EDGE,"fcba4419-a2ee-464f-be9d-58f11bf3418b.sketch_text.stroke-154"),sQuery(id+"F2.wireOp",EDGE,"fcba4419-a2ee-464f-be9d-58f11bf3418b.sketch_text.stroke-155"),sQuery(id+"F2.wireOp",EDGE,"fcba4419-a2ee-464f-be9d-58f11bf3418b.sketch_text.stroke-156"),sQuery(id+"F2.wireOp",EDGE,"fcba4419-a2ee-464f-be9d-58f11bf3418b.sketch_text.stroke-157"),sQuery(id+"F2.wireOp",EDGE,"fcba4419-a2ee-464f-be9d-58f11bf3418b.sketch_text.stroke-158"),sQuery(id+"F2.wireOp",EDGE,"fcba4419-a2ee-464f-be9d-58f11bf3418b.sketch_text.stroke-159"),sQuery(id+"F2.wireOp",EDGE,"fcba4419-a2ee-464f-be9d-58f11bf3418b.sketch_text.stroke-160"),sQuery(id+"F2.wireOp",EDGE,"fcba4419-a2ee-464f-be9d-58f11bf3418b.sketch_text.stroke-161"),sQuery(id+"F2.wireOp",EDGE,"fcba4419-a2ee-464f-be9d-58f11bf3418b.sketch_text.stroke-162"),sQuery(id+"F2.wireOp",EDGE,"fcba4419-a2ee-464f-be9d-58f11bf3418b.sketch_text.stroke-163"),sQuery(id+"F2.wireOp",EDGE,"fcba4419-a2ee-464f-be9d-58f11bf3418b.sketch_text.stroke-164"),sQuery(id+"F2.wireOp",EDGE,"fcba4419-a2ee-464f-be9d-58f11bf3418b.sketch_text.stroke-165"),sQuery(id+"F2.wireOp",EDGE,"fcba4419-a2ee-464f-be9d-58f11bf3418b.sketch_text.stroke-166"),sQuery(id+"F2.wireOp",EDGE,"fcba4419-a2ee-464f-be9d-58f11bf3418b.sketch_text.stroke-167"),sQuery(id+"F2.wireOp",EDGE,"fcba4419-a2ee-464f-be9d-58f11bf3418b.sketch_text.stroke-168"),sQuery(id+"F2.wireOp",EDGE,"fcba4419-a2ee-464f-be9d-58f11bf3418b.sketch_text.stroke-169"),sQuery(id+"F2.wireOp",EDGE,"fcba4419-a2ee-464f-be9d-58f11bf3418b.sketch_text.stroke-170"),sQuery(id+"F2.wireOp",EDGE,"fcba4419-a2ee-464f-be9d-58f11bf3418b.sketch_text.stroke-171"),sQuery(id+"F2.wireOp",EDGE,"fcba4419-a2ee-464f-be9d-58f11bf3418b.sketch_text.stroke-172"),sQuery(id+"F2.wireOp",EDGE,"fcba4419-a2ee-464f-be9d-58f11bf3418b.sketch_text.stroke-173"),sQuery(id+"FHMxAyK4CFUKdhS_1.wireOp",EDGE,"1cb9c079-ea9b-4899-8069-e0e3048e911d.sketch_text.stroke-0"),sQuery(id+"FHMxAyK4CFUKdhS_1.wireOp",EDGE,"1cb9c079-ea9b-4899-8069-e0e3048e911d.sketch_text.stroke-1"),sQuery(id+"FHMxAyK4CFUKdhS_1.wireOp",EDGE,"1cb9c079-ea9b-4899-8069-e0e3048e911d.sketch_text.stroke-2"),sQuery(id+"FHMxAyK4CFUKdhS_1.wireOp",EDGE,"1cb9c079-ea9b-4899-8069-e0e3048e911d.sketch_text.stroke-3"),sQuery(id+"FHMxAyK4CFUKdhS_1.wireOp",EDGE,"1cb9c079-ea9b-4899-8069-e0e3048e911d.sketch_text.stroke-4"),sQuery(id+"FHMxAyK4CFUKdhS_1.wireOp",EDGE,"1cb9c079-ea9b-4899-8069-e0e3048e911d.sketch_text.stroke-5"),sQuery(id+"FHMxAyK4CFUKdhS_1.wireOp",EDGE,"1cb9c079-ea9b-4899-8069-e0e3048e911d.sketch_text.stroke-6"),sQuery(id+"FHMxAyK4CFUKdhS_1.wireOp",EDGE,"1cb9c079-ea9b-4899-8069-e0e3048e911d.sketch_text.stroke-7"),sQuery(id+"FHMxAyK4CFUKdhS_1.wireOp",EDGE,"1cb9c079-ea9b-4899-8069-e0e3048e911d.sketch_text.stroke-8"),sQuery(id+"FHMxAyK4CFUKdhS_1.wireOp",EDGE,"1cb9c079-ea9b-4899-8069-e0e3048e911d.sketch_text.stroke-9"),sQuery(id+"FHMxAyK4CFUKdhS_1.wireOp",EDGE,"1cb9c079-ea9b-4899-8069-e0e3048e911d.sketch_text.stroke-10"),sQuery(id+"FHMxAyK4CFUKdhS_1.wireOp",EDGE,"1cb9c079-ea9b-4899-8069-e0e3048e911d.sketch_text.stroke-11"),sQuery(id+"FHMxAyK4CFUKdhS_1.wireOp",EDGE,"1cb9c079-ea9b-4899-8069-e0e3048e911d.sketch_text.stroke-12"),sQuery(id+"FHMxAyK4CFUKdhS_1.wireOp",EDGE,"1cb9c079-ea9b-4899-8069-e0e3048e911d.sketch_text.stroke-13"),sQuery(id+"FHMxAyK4CFUKdhS_1.wireOp",EDGE,"1cb9c079-ea9b-4899-8069-e0e3048e911d.sketch_text.stroke-14"),sQuery(id+"FHMxAyK4CFUKdhS_1.wireOp",EDGE,"1cb9c079-ea9b-4899-8069-e0e3048e911d.sketch_text.stroke-15"),sQuery(id+"FHMxAyK4CFUKdhS_1.wireOp",EDGE,"1cb9c079-ea9b-4899-8069-e0e3048e911d.sketch_text.stroke-16"),sQuery(id+"FHMxAyK4CFUKdhS_1.wireOp",EDGE,"1cb9c079-ea9b-4899-8069-e0e3048e911d.sketch_text.stroke-17"),sQuery(id+"FHMxAyK4CFUKdhS_1.wireOp",EDGE,"1cb9c079-ea9b-4899-8069-e0e3048e911d.sketch_text.stroke-18"),sQuery(id+"FHMxAyK4CFUKdhS_1.wireOp",EDGE,"1cb9c079-ea9b-4899-8069-e0e3048e911d.sketch_text.stroke-19"),sQuery(id+"FHMxAyK4CFUKdhS_1.wireOp",EDGE,"1cb9c079-ea9b-4899-8069-e0e3048e911d.sketch_text.stroke-20"),sQuery(id+"FHMxAyK4CFUKdhS_1.wireOp",EDGE,"1cb9c079-ea9b-4899-8069-e0e3048e911d.sketch_text.stroke-21"),sQuery(id+"FHMxAyK4CFUKdhS_1.wireOp",EDGE,"1cb9c079-ea9b-4899-8069-e0e3048e911d.sketch_text.stroke-22"),sQuery(id+"FHMxAyK4CFUKdhS_1.wireOp",EDGE,"1cb9c079-ea9b-4899-8069-e0e3048e911d.sketch_text.stroke-23"),sQuery(id+"FHMxAyK4CFUKdhS_1.wireOp",EDGE,"1cb9c079-ea9b-4899-8069-e0e3048e911d.sketch_text.stroke-24"),sQuery(id+"FHMxAyK4CFUKdhS_1.wireOp",EDGE,"1cb9c079-ea9b-4899-8069-e0e3048e911d.sketch_text.stroke-25"),sQuery(id+"FHMxAyK4CFUKdhS_1.wireOp",EDGE,"1cb9c079-ea9b-4899-8069-e0e3048e911d.sketch_text.stroke-26"),sQuery(id+"FHMxAyK4CFUKdhS_1.wireOp",EDGE,"1cb9c079-ea9b-4899-8069-e0e3048e911d.sketch_text.stroke-27"),sQuery(id+"FHMxAyK4CFUKdhS_1.wireOp",EDGE,"1cb9c079-ea9b-4899-8069-e0e3048e911d.sketch_text.stroke-28"),sQuery(id+"FHMxAyK4CFUKdhS_1.wireOp",EDGE,"1cb9c079-ea9b-4899-8069-e0e3048e911d.sketch_text.stroke-29"),sQuery(id+"FHMxAyK4CFUKdhS_1.wireOp",EDGE,"1cb9c079-ea9b-4899-8069-e0e3048e911d.sketch_text.stroke-30"),sQuery(id+"FHMxAyK4CFUKdhS_1.wireOp",EDGE,"1cb9c079-ea9b-4899-8069-e0e3048e911d.sketch_text.stroke-31"),sQuery(id+"FHMxAyK4CFUKdhS_1.wireOp",EDGE,"1cb9c079-ea9b-4899-8069-e0e3048e911d.sketch_text.stroke-32"),sQuery(id+"FHMxAyK4CFUKdhS_1.wireOp",EDGE,"1cb9c079-ea9b-4899-8069-e0e3048e911d.sketch_text.stroke-33"),sQuery(id+"FHMxAyK4CFUKdhS_1.wireOp",EDGE,"1cb9c079-ea9b-4899-8069-e0e3048e911d.sketch_text.stroke-34"),sQuery(id+"FHMxAyK4CFUKdhS_1.wireOp",EDGE,"1cb9c079-ea9b-4899-8069-e0e3048e911d.sketch_text.stroke-35"),sQuery(id+"FHMxAyK4CFUKdhS_1.wireOp",EDGE,"1cb9c079-ea9b-4899-8069-e0e3048e911d.sketch_text.stroke-36"),sQuery(id+"FHMxAyK4CFUKdhS_1.wireOp",EDGE,"1cb9c079-ea9b-4899-8069-e0e3048e911d.sketch_text.stroke-37"),sQuery(id+"FHMxAyK4CFUKdhS_1.wireOp",EDGE,"1cb9c079-ea9b-4899-8069-e0e3048e911d.sketch_text.stroke-38"),sQuery(id+"FHMxAyK4CFUKdhS_1.wireOp",EDGE,"1cb9c079-ea9b-4899-8069-e0e3048e911d.sketch_text.stroke-39"),sQuery(id+"FHMxAyK4CFUKdhS_1.wireOp",EDGE,"1cb9c079-ea9b-4899-8069-e0e3048e911d.sketch_text.stroke-40"),sQuery(id+"FHMxAyK4CFUKdhS_1.wireOp",EDGE,"1cb9c079-ea9b-4899-8069-e0e3048e911d.sketch_text.stroke-41"),sQuery(id+"FHMxAyK4CFUKdhS_1.wireOp",EDGE,"1cb9c079-ea9b-4899-8069-e0e3048e911d.sketch_text.stroke-42"),sQuery(id+"FHMxAyK4CFUKdhS_1.wireOp",EDGE,"1cb9c079-ea9b-4899-8069-e0e3048e911d.sketch_text.stroke-43"),sQuery(id+"FHMxAyK4CFUKdhS_1.wireOp",EDGE,"1cb9c079-ea9b-4899-8069-e0e3048e911d.sketch_text.stroke-44"),sQuery(id+"FHMxAyK4CFUKdhS_1.wireOp",EDGE,"1cb9c079-ea9b-4899-8069-e0e3048e911d.sketch_text.stroke-45"),sQuery(id+"FHMxAyK4CFUKdhS_1.wireOp",EDGE,"1cb9c079-ea9b-4899-8069-e0e3048e911d.sketch_text.stroke-46"),sQuery(id+"FHMxAyK4CFUKdhS_1.wireOp",EDGE,"1cb9c079-ea9b-4899-8069-e0e3048e911d.sketch_text.stroke-47"),sQuery(id+"FHMxAyK4CFUKdhS_1.wireOp",EDGE,"1cb9c079-ea9b-4899-8069-e0e3048e911d.sketch_text.stroke-48"),sQuery(id+"FHMxAyK4CFUKdhS_1.wireOp",EDGE,"1cb9c079-ea9b-4899-8069-e0e3048e911d.sketch_text.stroke-49"),sQuery(id+"FHMxAyK4CFUKdhS_1.wireOp",EDGE,"1cb9c079-ea9b-4899-8069-e0e3048e911d.sketch_text.stroke-50"),sQuery(id+"FHMxAyK4CFUKdhS_1.wireOp",EDGE,"1cb9c079-ea9b-4899-8069-e0e3048e911d.sketch_text.stroke-51"),sQuery(id+"FHMxAyK4CFUKdhS_1.wireOp",EDGE,"1cb9c079-ea9b-4899-8069-e0e3048e911d.sketch_text.stroke-52"),sQuery(id+"FHMxAyK4CFUKdhS_1.wireOp",EDGE,"1cb9c079-ea9b-4899-8069-e0e3048e911d.sketch_text.stroke-53"),sQuery(id+"FHMxAyK4CFUKdhS_1.wireOp",EDGE,"1cb9c079-ea9b-4899-8069-e0e3048e911d.sketch_text.stroke-54"),sQuery(id+"FHMxAyK4CFUKdhS_1.wireOp",EDGE,"1cb9c079-ea9b-4899-8069-e0e3048e911d.sketch_text.stroke-55"),sQuery(id+"FHMxAyK4CFUKdhS_1.wireOp",EDGE,"1cb9c079-ea9b-4899-8069-e0e3048e911d.sketch_text.stroke-56"),sQuery(id+"FHMxAyK4CFUKdhS_1.wireOp",EDGE,"1cb9c079-ea9b-4899-8069-e0e3048e911d.sketch_text.stroke-57"),sQuery(id+"FHMxAyK4CFUKdhS_1.wireOp",EDGE,"1cb9c079-ea9b-4899-8069-e0e3048e911d.sketch_text.stroke-58"),sQuery(id+"FHMxAyK4CFUKdhS_1.wireOp",EDGE,"1cb9c079-ea9b-4899-8069-e0e3048e911d.sketch_text.stroke-59"),sQuery(id+"FHMxAyK4CFUKdhS_1.wireOp",EDGE,"1cb9c079-ea9b-4899-8069-e0e3048e911d.sketch_text.stroke-60"),sQuery(id+"FHMxAyK4CFUKdhS_1.wireOp",EDGE,"1cb9c079-ea9b-4899-8069-e0e3048e911d.sketch_text.stroke-61"),sQuery(id+"FHMxAyK4CFUKdhS_1.wireOp",EDGE,"1cb9c079-ea9b-4899-8069-e0e3048e911d.sketch_text.stroke-62"),sQuery(id+"FHMxAyK4CFUKdhS_1.wireOp",EDGE,"1cb9c079-ea9b-4899-8069-e0e3048e911d.sketch_text.stroke-71"),sQuery(id+"FHMxAyK4CFUKdhS_1.wireOp",EDGE,"1cb9c079-ea9b-4899-8069-e0e3048e911d.sketch_text.stroke-72"),sQuery(id+"FHMxAyK4CFUKdhS_1.wireOp",EDGE,"1cb9c079-ea9b-4899-8069-e0e3048e911d.sketch_text.stroke-73"),sQuery(id+"FHMxAyK4CFUKdhS_1.wireOp",EDGE,"1cb9c079-ea9b-4899-8069-e0e3048e911d.sketch_text.stroke-74"),sQuery(id+"FHMxAyK4CFUKdhS_1.wireOp",EDGE,"1cb9c079-ea9b-4899-8069-e0e3048e911d.sketch_text.stroke-75"),sQuery(id+"FHMxAyK4CFUKdhS_1.wireOp",EDGE,"1cb9c079-ea9b-4899-8069-e0e3048e911d.sketch_text.stroke-76"),sQuery(id+"FHMxAyK4CFUKdhS_1.wireOp",EDGE,"1cb9c079-ea9b-4899-8069-e0e3048e911d.sketch_text.stroke-77"),sQuery(id+"FHMxAyK4CFUKdhS_1.wireOp",EDGE,"1cb9c079-ea9b-4899-8069-e0e3048e911d.sketch_text.stroke-78"),sQuery(id+"FHMxAyK4CFUKdhS_1.wireOp",EDGE,"1cb9c079-ea9b-4899-8069-e0e3048e911d.sketch_text.stroke-79"),sQuery(id+"FHMxAyK4CFUKdhS_1.wireOp",EDGE,"1cb9c079-ea9b-4899-8069-e0e3048e911d.sketch_text.stroke-80"),sQuery(id+"FHMxAyK4CFUKdhS_1.wireOp",EDGE,"1cb9c079-ea9b-4899-8069-e0e3048e911d.sketch_text.stroke-81"),sQuery(id+"FHMxAyK4CFUKdhS_1.wireOp",EDGE,"1cb9c079-ea9b-4899-8069-e0e3048e911d.sketch_text.stroke-82"),sQuery(id+"FHMxAyK4CFUKdhS_1.wireOp",EDGE,"1cb9c079-ea9b-4899-8069-e0e3048e911d.sketch_text.stroke-83"),sQuery(id+"FHMxAyK4CFUKdhS_1.wireOp",EDGE,"1cb9c079-ea9b-4899-8069-e0e3048e911d.sketch_text.stroke-84"),sQuery(id+"FHMxAyK4CFUKdhS_1.wireOp",EDGE,"1cb9c079-ea9b-4899-8069-e0e3048e911d.sketch_text.stroke-85"),sQuery(id+"FHMxAyK4CFUKdhS_1.wireOp",EDGE,"1cb9c079-ea9b-4899-8069-e0e3048e911d.sketch_text.stroke-86"),sQuery(id+"FHMxAyK4CFUKdhS_1.wireOp",EDGE,"1cb9c079-ea9b-4899-8069-e0e3048e911d.sketch_text.stroke-87"),sQuery(id+"FHMxAyK4CFUKdhS_1.wireOp",EDGE,"1cb9c079-ea9b-4899-8069-e0e3048e911d.sketch_text.stroke-88"),sQuery(id+"FHMxAyK4CFUKdhS_1.wireOp",EDGE,"1cb9c079-ea9b-4899-8069-e0e3048e911d.sketch_text.stroke-89"),sQuery(id+"FHMxAyK4CFUKdhS_1.wireOp",EDGE,"1cb9c079-ea9b-4899-8069-e0e3048e911d.sketch_text.stroke-90"),sQuery(id+"FHMxAyK4CFUKdhS_1.wireOp",EDGE,"1cb9c079-ea9b-4899-8069-e0e3048e911d.sketch_text.stroke-91"),sQuery(id+"FHMxAyK4CFUKdhS_1.wireOp",EDGE,"1cb9c079-ea9b-4899-8069-e0e3048e911d.sketch_text.stroke-92"),sQuery(id+"FHMxAyK4CFUKdhS_1.wireOp",EDGE,"1cb9c079-ea9b-4899-8069-e0e3048e911d.sketch_text.stroke-93"),sQuery(id+"FHMxAyK4CFUKdhS_1.wireOp",EDGE,"1cb9c079-ea9b-4899-8069-e0e3048e911d.sketch_text.stroke-94"),sQuery(id+"FHMxAyK4CFUKdhS_1.wireOp",EDGE,"1cb9c079-ea9b-4899-8069-e0e3048e911d.sketch_text.stroke-95"),sQuery(id+"FHMxAyK4CFUKdhS_1.wireOp",EDGE,"1cb9c079-ea9b-4899-8069-e0e3048e911d.sketch_text.stroke-96"),sQuery(id+"FHMxAyK4CFUKdhS_1.wireOp",EDGE,"1cb9c079-ea9b-4899-8069-e0e3048e911d.sketch_text.stroke-97"),sQuery(id+"FHMxAyK4CFUKdhS_1.wireOp",EDGE,"1cb9c079-ea9b-4899-8069-e0e3048e911d.sketch_text.stroke-103"),sQuery(id+"FHMxAyK4CFUKdhS_1.wireOp",EDGE,"1cb9c079-ea9b-4899-8069-e0e3048e911d.sketch_text.stroke-104"),sQuery(id+"FHMxAyK4CFUKdhS_1.wireOp",EDGE,"1cb9c079-ea9b-4899-8069-e0e3048e911d.sketch_text.stroke-105"),sQuery(id+"FHMxAyK4CFUKdhS_1.wireOp",EDGE,"1cb9c079-ea9b-4899-8069-e0e3048e911d.sketch_text.stroke-106"),sQuery(id+"FHMxAyK4CFUKdhS_1.wireOp",EDGE,"1cb9c079-ea9b-4899-8069-e0e3048e911d.sketch_text.stroke-107"),sQuery(id+"FHMxAyK4CFUKdhS_1.wireOp",EDGE,"1cb9c079-ea9b-4899-8069-e0e3048e911d.sketch_text.stroke-108"),sQuery(id+"FHMxAyK4CFUKdhS_1.wireOp",EDGE,"1cb9c079-ea9b-4899-8069-e0e3048e911d.sketch_text.stroke-109"),sQuery(id+"FHMxAyK4CFUKdhS_1.wireOp",EDGE,"1cb9c079-ea9b-4899-8069-e0e3048e911d.sketch_text.stroke-110"),sQuery(id+"FHMxAyK4CFUKdhS_1.wireOp",EDGE,"1cb9c079-ea9b-4899-8069-e0e3048e911d.sketch_text.stroke-111"),sQuery(id+"FHMxAyK4CFUKdhS_1.wireOp",EDGE,"1cb9c079-ea9b-4899-8069-e0e3048e911d.sketch_text.stroke-112"),sQuery(id+"FHMxAyK4CFUKdhS_1.wireOp",EDGE,"1cb9c079-ea9b-4899-8069-e0e3048e911d.sketch_text.stroke-113"),sQuery(id+"FHMxAyK4CFUKdhS_1.wireOp",EDGE,"1cb9c079-ea9b-4899-8069-e0e3048e911d.sketch_text.stroke-114"),sQuery(id+"FHMxAyK4CFUKdhS_1.wireOp",EDGE,"1cb9c079-ea9b-4899-8069-e0e3048e911d.sketch_text.stroke-115"),sQuery(id+"FHMxAyK4CFUKdhS_1.wireOp",EDGE,"1cb9c079-ea9b-4899-8069-e0e3048e911d.sketch_text.stroke-116"),sQuery(id+"FHMxAyK4CFUKdhS_1.wireOp",EDGE,"1cb9c079-ea9b-4899-8069-e0e3048e911d.sketch_text.stroke-117"),sQuery(id+"FHMxAyK4CFUKdhS_1.wireOp",EDGE,"1cb9c079-ea9b-4899-8069-e0e3048e911d.sketch_text.stroke-118"),sQuery(id+"FHMxAyK4CFUKdhS_1.wireOp",EDGE,"1cb9c079-ea9b-4899-8069-e0e3048e911d.sketch_text.stroke-119"),sQuery(id+"FHMxAyK4CFUKdhS_1.wireOp",EDGE,"1cb9c079-ea9b-4899-8069-e0e3048e911d.sketch_text.stroke-120"),sQuery(id+"FHMxAyK4CFUKdhS_1.wireOp",EDGE,"1cb9c079-ea9b-4899-8069-e0e3048e911d.sketch_text.stroke-121"),sQuery(id+"FHMxAyK4CFUKdhS_1.wireOp",EDGE,"1cb9c079-ea9b-4899-8069-e0e3048e911d.sketch_text.stroke-122"),sQuery(id+"FHMxAyK4CFUKdhS_1.wireOp",EDGE,"1cb9c079-ea9b-4899-8069-e0e3048e911d.sketch_text.stroke-123"),sQuery(id+"FHMxAyK4CFUKdhS_1.wireOp",EDGE,"1cb9c079-ea9b-4899-8069-e0e3048e911d.sketch_text.stroke-124"),sQuery(id+"FHMxAyK4CFUKdhS_1.wireOp",EDGE,"1cb9c079-ea9b-4899-8069-e0e3048e911d.sketch_text.stroke-125"),sQuery(id+"FHMxAyK4CFUKdhS_1.wireOp",EDGE,"1cb9c079-ea9b-4899-8069-e0e3048e911d.sketch_text.stroke-126"),sQuery(id+"FHMxAyK4CFUKdhS_1.wireOp",EDGE,"1cb9c079-ea9b-4899-8069-e0e3048e911d.sketch_text.stroke-127"),sQuery(id+"FHMxAyK4CFUKdhS_1.wireOp",EDGE,"1cb9c079-ea9b-4899-8069-e0e3048e911d.sketch_text.stroke-128"),sQuery(id+"FHMxAyK4CFUKdhS_1.wireOp",EDGE,"1cb9c079-ea9b-4899-8069-e0e3048e911d.sketch_text.stroke-129"),sQuery(id+"FHMxAyK4CFUKdhS_1.wireOp",EDGE,"1cb9c079-ea9b-4899-8069-e0e3048e911d.sketch_text.stroke-130"),sQuery(id+"FHMxAyK4CFUKdhS_1.wireOp",EDGE,"1cb9c079-ea9b-4899-8069-e0e3048e911d.sketch_text.stroke-131"),sQuery(id+"FHMxAyK4CFUKdhS_1.wireOp",EDGE,"1cb9c079-ea9b-4899-8069-e0e3048e911d.sketch_text.stroke-132"),sQuery(id+"FHMxAyK4CFUKdhS_1.wireOp",EDGE,"1cb9c079-ea9b-4899-8069-e0e3048e911d.sketch_text.stroke-133"),sQuery(id+"FHMxAyK4CFUKdhS_1.wireOp",EDGE,"1cb9c079-ea9b-4899-8069-e0e3048e911d.sketch_text.stroke-134"),sQuery(id+"FHMxAyK4CFUKdhS_1.wireOp",EDGE,"1cb9c079-ea9b-4899-8069-e0e3048e911d.sketch_text.stroke-135"),sQuery(id+"FHMxAyK4CFUKdhS_1.wireOp",EDGE,"1cb9c079-ea9b-4899-8069-e0e3048e911d.sketch_text.stroke-136"),sQuery(id+"FHMxAyK4CFUKdhS_1.wireOp",EDGE,"1cb9c079-ea9b-4899-8069-e0e3048e911d.sketch_text.stroke-137"),sQuery(id+"FHMxAyK4CFUKdhS_1.wireOp",EDGE,"1cb9c079-ea9b-4899-8069-e0e3048e911d.sketch_text.stroke-138"),sQuery(id+"FHMxAyK4CFUKdhS_1.wireOp",EDGE,"1cb9c079-ea9b-4899-8069-e0e3048e911d.sketch_text.stroke-139"),sQuery(id+"FHMxAyK4CFUKdhS_1.wireOp",EDGE,"1cb9c079-ea9b-4899-8069-e0e3048e911d.sketch_text.stroke-140"),sQuery(id+"FHMxAyK4CFUKdhS_1.wireOp",EDGE,"1cb9c079-ea9b-4899-8069-e0e3048e911d.sketch_text.stroke-141"),sQuery(id+"FHMxAyK4CFUKdhS_1.wireOp",EDGE,"1cb9c079-ea9b-4899-8069-e0e3048e911d.sketch_text.stroke-142"),sQuery(id+"FHMxAyK4CFUKdhS_1.wireOp",EDGE,"1cb9c079-ea9b-4899-8069-e0e3048e911d.sketch_text.stroke-143"),sQuery(id+"FHMxAyK4CFUKdhS_1.wireOp",EDGE,"1cb9c079-ea9b-4899-8069-e0e3048e911d.sketch_text.stroke-144"),sQuery(id+"FHMxAyK4CFUKdhS_1.wireOp",EDGE,"1cb9c079-ea9b-4899-8069-e0e3048e911d.sketch_text.stroke-145"),sQuery(id+"FHMxAyK4CFUKdhS_1.wireOp",EDGE,"1cb9c079-ea9b-4899-8069-e0e3048e911d.sketch_text.stroke-146"),sQuery(id+"FHMxAyK4CFUKdhS_1.wireOp",EDGE,"1cb9c079-ea9b-4899-8069-e0e3048e911d.sketch_text.stroke-147"),sQuery(id+"FHMxAyK4CFUKdhS_1.wireOp",EDGE,"1cb9c079-ea9b-4899-8069-e0e3048e911d.sketch_text.stroke-148"),sQuery(id+"FHMxAyK4CFUKdhS_1.wireOp",EDGE,"1cb9c079-ea9b-4899-8069-e0e3048e911d.sketch_text.stroke-149"),sQuery(id+"FHMxAyK4CFUKdhS_1.wireOp",EDGE,"1cb9c079-ea9b-4899-8069-e0e3048e911d.sketch_text.stroke-150"),sQuery(id+"FHMxAyK4CFUKdhS_1.wireOp",EDGE,"1cb9c079-ea9b-4899-8069-e0e3048e911d.sketch_text.stroke-151"),sQuery(id+"FHMxAyK4CFUKdhS_1.wireOp",EDGE,"1cb9c079-ea9b-4899-8069-e0e3048e911d.sketch_text.stroke-152"),sQuery(id+"FHMxAyK4CFUKdhS_1.wireOp",EDGE,"1cb9c079-ea9b-4899-8069-e0e3048e911d.sketch_text.stroke-153"),sQuery(id+"FHMxAyK4CFUKdhS_1.wireOp",EDGE,"1cb9c079-ea9b-4899-8069-e0e3048e911d.sketch_text.stroke-159"),sQuery(id+"FHMxAyK4CFUKdhS_1.wireOp",EDGE,"1cb9c079-ea9b-4899-8069-e0e3048e911d.sketch_text.stroke-160"),sQuery(id+"FHMxAyK4CFUKdhS_1.wireOp",EDGE,"1cb9c079-ea9b-4899-8069-e0e3048e911d.sketch_text.stroke-161"),sQuery(id+"FHMxAyK4CFUKdhS_1.wireOp",EDGE,"1cb9c079-ea9b-4899-8069-e0e3048e911d.sketch_text.stroke-162"),sQuery(id+"FHMxAyK4CFUKdhS_1.wireOp",EDGE,"1cb9c079-ea9b-4899-8069-e0e3048e911d.sketch_text.stroke-163"),sQuery(id+"FHMxAyK4CFUKdhS_1.wireOp",EDGE,"1cb9c079-ea9b-4899-8069-e0e3048e911d.sketch_text.stroke-164"),sQuery(id+"FHMxAyK4CFUKdhS_1.wireOp",EDGE,"1cb9c079-ea9b-4899-8069-e0e3048e911d.sketch_text.stroke-165"),sQuery(id+"FHMxAyK4CFUKdhS_1.wireOp",EDGE,"1cb9c079-ea9b-4899-8069-e0e3048e911d.sketch_text.stroke-166"),sQuery(id+"FHMxAyK4CFUKdhS_1.wireOp",EDGE,"1cb9c079-ea9b-4899-8069-e0e3048e911d.sketch_text.stroke-167"),sQuery(id+"FHMxAyK4CFUKdhS_1.wireOp",EDGE,"1cb9c079-ea9b-4899-8069-e0e3048e911d.sketch_text.stroke-168"),sQuery(id+"FHMxAyK4CFUKdhS_1.wireOp",EDGE,"1cb9c079-ea9b-4899-8069-e0e3048e911d.sketch_text.stroke-169"),sQuery(id+"FHMxAyK4CFUKdhS_1.wireOp",EDGE,"1cb9c079-ea9b-4899-8069-e0e3048e911d.sketch_text.stroke-170"),sQuery(id+"FHMxAyK4CFUKdhS_1.wireOp",EDGE,"1cb9c079-ea9b-4899-8069-e0e3048e911d.sketch_text.stroke-171"),sQuery(id+"FHMxAyK4CFUKdhS_1.wireOp",EDGE,"1cb9c079-ea9b-4899-8069-e0e3048e911d.sketch_text.stroke-172"),sQuery(id+"FHMxAyK4CFUKdhS_1.wireOp",EDGE,"1cb9c079-ea9b-4899-8069-e0e3048e911d.sketch_text.stroke-173"),sQuery(id+"FHMxAyK4CFUKdhS_1.wireOp",EDGE,"1cb9c079-ea9b-4899-8069-e0e3048e911d.sketch_text.stroke-174"),sQuery(id+"FHMxAyK4CFUKdhS_1.wireOp",EDGE,"1cb9c079-ea9b-4899-8069-e0e3048e911d.sketch_text.stroke-175"),sQuery(id+"FHMxAyK4CFUKdhS_1.wireOp",EDGE,"1cb9c079-ea9b-4899-8069-e0e3048e911d.sketch_text.stroke-176"),sQuery(id+"FHMxAyK4CFUKdhS_1.wireOp",EDGE,"1cb9c079-ea9b-4899-8069-e0e3048e911d.sketch_text.stroke-177"),sQuery(id+"FHMxAyK4CFUKdhS_1.wireOp",EDGE,"1cb9c079-ea9b-4899-8069-e0e3048e911d.sketch_text.stroke-178"),sQuery(id+"FHMxAyK4CFUKdhS_1.wireOp",EDGE,"1cb9c079-ea9b-4899-8069-e0e3048e911d.sketch_text.stroke-179"),sQuery(id+"FHMxAyK4CFUKdhS_1.wireOp",EDGE,"1cb9c079-ea9b-4899-8069-e0e3048e911d.sketch_text.stroke-180"),sQuery(id+"F3.wireOp",EDGE,"727ac2c1-f511-4829-95a7-a443ef16a4cd"),subQ2])],"isStart":true}),makeQuery(id+"F4.opExtrude","SWEPT_FACE",FACE,{"disambiguationData":[OSD([subQ2])]})]),OD(1.0)],"derivedFrom":makeQuery(id+"F1.opExtrude","CAP_EDGE",EDGE,{"disambiguationData":[OSD([subQ0])],"isStart":false})});}
            var Q20;
            {var subQ0=sQuery(id+"F0.wireOp",EDGE,"E0.top");var subQ1=sQuery(id+"F0.wireOp",EDGE,"E0.bottom");var subQ2=sQuery(id+"F3.wireOp",EDGE,"E28");Q20=makeQuery(id+"F4.boolean.opBoolean","SPLIT",EDGE,{"disambiguationData":[TD([makeQuery(id+"F1.opExtrude","CAP_FACE",FACE,{"disambiguationData":[OSD([subQ1,subQ0,sQuery(id+"F0.wireOp",EDGE,"E0.left"),sQuery(id+"F0.wireOp",EDGE,"E0.right")])],"isStart":false}),makeQuery(id+"F1.opExtrude","SWEPT_FACE",FACE,{"disambiguationData":[OSD([subQ0])]}),makeQuery(id+"F4.opExtrude","SWEPT_FACE",FACE,{"disambiguationData":[OSD([subQ2])]}),makeQuery(id+"F4.opExtrude","CAP_FACE",FACE,{"disambiguationData":[OSD([subQ1,sQuery(id+"F2.wireOp",EDGE,"fcba4419-a2ee-464f-be9d-58f11bf3418b.sketch_text.stroke-0"),sQuery(id+"F2.wireOp",EDGE,"fcba4419-a2ee-464f-be9d-58f11bf3418b.sketch_text.stroke-1"),sQuery(id+"F2.wireOp",EDGE,"fcba4419-a2ee-464f-be9d-58f11bf3418b.sketch_text.stroke-2"),sQuery(id+"F2.wireOp",EDGE,"fcba4419-a2ee-464f-be9d-58f11bf3418b.sketch_text.stroke-3"),sQuery(id+"F2.wireOp",EDGE,"fcba4419-a2ee-464f-be9d-58f11bf3418b.sketch_text.stroke-4"),sQuery(id+"F2.wireOp",EDGE,"fcba4419-a2ee-464f-be9d-58f11bf3418b.sketch_text.stroke-5"),sQuery(id+"F2.wireOp",EDGE,"fcba4419-a2ee-464f-be9d-58f11bf3418b.sketch_text.stroke-6"),sQuery(id+"F2.wireOp",EDGE,"fcba4419-a2ee-464f-be9d-58f11bf3418b.sketch_text.stroke-7"),sQuery(id+"F2.wireOp",EDGE,"fcba4419-a2ee-464f-be9d-58f11bf3418b.sketch_text.stroke-8"),sQuery(id+"F2.wireOp",EDGE,"fcba4419-a2ee-464f-be9d-58f11bf3418b.sketch_text.stroke-9"),sQuery(id+"F2.wireOp",EDGE,"fcba4419-a2ee-464f-be9d-58f11bf3418b.sketch_text.stroke-10"),sQuery(id+"F2.wireOp",EDGE,"fcba4419-a2ee-464f-be9d-58f11bf3418b.sketch_text.stroke-11"),sQuery(id+"F2.wireOp",EDGE,"fcba4419-a2ee-464f-be9d-58f11bf3418b.sketch_text.stroke-12"),sQuery(id+"F2.wireOp",EDGE,"fcba4419-a2ee-464f-be9d-58f11bf3418b.sketch_text.stroke-13"),sQuery(id+"F2.wireOp",EDGE,"fcba4419-a2ee-464f-be9d-58f11bf3418b.sketch_text.stroke-14"),sQuery(id+"F2.wireOp",EDGE,"fcba4419-a2ee-464f-be9d-58f11bf3418b.sketch_text.stroke-15"),sQuery(id+"F2.wireOp",EDGE,"fcba4419-a2ee-464f-be9d-58f11bf3418b.sketch_text.stroke-16"),sQuery(id+"F2.wireOp",EDGE,"fcba4419-a2ee-464f-be9d-58f11bf3418b.sketch_text.stroke-17"),sQuery(id+"F2.wireOp",EDGE,"fcba4419-a2ee-464f-be9d-58f11bf3418b.sketch_text.stroke-18"),sQuery(id+"F2.wireOp",EDGE,"fcba4419-a2ee-464f-be9d-58f11bf3418b.sketch_text.stroke-19"),sQuery(id+"F2.wireOp",EDGE,"fcba4419-a2ee-464f-be9d-58f11bf3418b.sketch_text.stroke-20"),sQuery(id+"F2.wireOp",EDGE,"fcba4419-a2ee-464f-be9d-58f11bf3418b.sketch_text.stroke-21"),sQuery(id+"F2.wireOp",EDGE,"fcba4419-a2ee-464f-be9d-58f11bf3418b.sketch_text.stroke-22"),sQuery(id+"F2.wireOp",EDGE,"fcba4419-a2ee-464f-be9d-58f11bf3418b.sketch_text.stroke-23"),sQuery(id+"F2.wireOp",EDGE,"fcba4419-a2ee-464f-be9d-58f11bf3418b.sketch_text.stroke-24"),sQuery(id+"F2.wireOp",EDGE,"fcba4419-a2ee-464f-be9d-58f11bf3418b.sketch_text.stroke-25"),sQuery(id+"F2.wireOp",EDGE,"fcba4419-a2ee-464f-be9d-58f11bf3418b.sketch_text.stroke-26"),sQuery(id+"F2.wireOp",EDGE,"fcba4419-a2ee-464f-be9d-58f11bf3418b.sketch_text.stroke-27"),sQuery(id+"F2.wireOp",EDGE,"fcba4419-a2ee-464f-be9d-58f11bf3418b.sketch_text.stroke-28"),sQuery(id+"F2.wireOp",EDGE,"fcba4419-a2ee-464f-be9d-58f11bf3418b.sketch_text.stroke-29"),sQuery(id+"F2.wireOp",EDGE,"fcba4419-a2ee-464f-be9d-58f11bf3418b.sketch_text.stroke-30"),sQuery(id+"F2.wireOp",EDGE,"fcba4419-a2ee-464f-be9d-58f11bf3418b.sketch_text.stroke-31"),sQuery(id+"F2.wireOp",EDGE,"fcba4419-a2ee-464f-be9d-58f11bf3418b.sketch_text.stroke-32"),sQuery(id+"F2.wireOp",EDGE,"fcba4419-a2ee-464f-be9d-58f11bf3418b.sketch_text.stroke-33"),sQuery(id+"F2.wireOp",EDGE,"fcba4419-a2ee-464f-be9d-58f11bf3418b.sketch_text.stroke-34"),sQuery(id+"F2.wireOp",EDGE,"fcba4419-a2ee-464f-be9d-58f11bf3418b.sketch_text.stroke-35"),sQuery(id+"F2.wireOp",EDGE,"fcba4419-a2ee-464f-be9d-58f11bf3418b.sketch_text.stroke-36"),sQuery(id+"F2.wireOp",EDGE,"fcba4419-a2ee-464f-be9d-58f11bf3418b.sketch_text.stroke-37"),sQuery(id+"F2.wireOp",EDGE,"fcba4419-a2ee-464f-be9d-58f11bf3418b.sketch_text.stroke-38"),sQuery(id+"F2.wireOp",EDGE,"fcba4419-a2ee-464f-be9d-58f11bf3418b.sketch_text.stroke-39"),sQuery(id+"F2.wireOp",EDGE,"fcba4419-a2ee-464f-be9d-58f11bf3418b.sketch_text.stroke-40"),sQuery(id+"F2.wireOp",EDGE,"fcba4419-a2ee-464f-be9d-58f11bf3418b.sketch_text.stroke-41"),sQuery(id+"F2.wireOp",EDGE,"fcba4419-a2ee-464f-be9d-58f11bf3418b.sketch_text.stroke-42"),sQuery(id+"F2.wireOp",EDGE,"fcba4419-a2ee-464f-be9d-58f11bf3418b.sketch_text.stroke-43"),sQuery(id+"F2.wireOp",EDGE,"fcba4419-a2ee-464f-be9d-58f11bf3418b.sketch_text.stroke-44"),sQuery(id+"F2.wireOp",EDGE,"fcba4419-a2ee-464f-be9d-58f11bf3418b.sketch_text.stroke-45"),sQuery(id+"F2.wireOp",EDGE,"fcba4419-a2ee-464f-be9d-58f11bf3418b.sketch_text.stroke-46"),sQuery(id+"F2.wireOp",EDGE,"fcba4419-a2ee-464f-be9d-58f11bf3418b.sketch_text.stroke-47"),sQuery(id+"F2.wireOp",EDGE,"fcba4419-a2ee-464f-be9d-58f11bf3418b.sketch_text.stroke-48"),sQuery(id+"F2.wireOp",EDGE,"fcba4419-a2ee-464f-be9d-58f11bf3418b.sketch_text.stroke-49"),sQuery(id+"F2.wireOp",EDGE,"fcba4419-a2ee-464f-be9d-58f11bf3418b.sketch_text.stroke-50"),sQuery(id+"F2.wireOp",EDGE,"fcba4419-a2ee-464f-be9d-58f11bf3418b.sketch_text.stroke-51"),sQuery(id+"F2.wireOp",EDGE,"fcba4419-a2ee-464f-be9d-58f11bf3418b.sketch_text.stroke-52"),sQuery(id+"F2.wireOp",EDGE,"fcba4419-a2ee-464f-be9d-58f11bf3418b.sketch_text.stroke-53"),sQuery(id+"F2.wireOp",EDGE,"fcba4419-a2ee-464f-be9d-58f11bf3418b.sketch_text.stroke-54"),sQuery(id+"F2.wireOp",EDGE,"fcba4419-a2ee-464f-be9d-58f11bf3418b.sketch_text.stroke-55"),sQuery(id+"F2.wireOp",EDGE,"fcba4419-a2ee-464f-be9d-58f11bf3418b.sketch_text.stroke-56"),sQuery(id+"F2.wireOp",EDGE,"fcba4419-a2ee-464f-be9d-58f11bf3418b.sketch_text.stroke-57"),sQuery(id+"F2.wireOp",EDGE,"fcba4419-a2ee-464f-be9d-58f11bf3418b.sketch_text.stroke-58"),sQuery(id+"F2.wireOp",EDGE,"fcba4419-a2ee-464f-be9d-58f11bf3418b.sketch_text.stroke-59"),sQuery(id+"F2.wireOp",EDGE,"fcba4419-a2ee-464f-be9d-58f11bf3418b.sketch_text.stroke-60"),sQuery(id+"F2.wireOp",EDGE,"fcba4419-a2ee-464f-be9d-58f11bf3418b.sketch_text.stroke-61"),sQuery(id+"F2.wireOp",EDGE,"fcba4419-a2ee-464f-be9d-58f11bf3418b.sketch_text.stroke-62"),sQuery(id+"F2.wireOp",EDGE,"fcba4419-a2ee-464f-be9d-58f11bf3418b.sketch_text.stroke-63"),sQuery(id+"F2.wireOp",EDGE,"fcba4419-a2ee-464f-be9d-58f11bf3418b.sketch_text.stroke-64"),sQuery(id+"F2.wireOp",EDGE,"fcba4419-a2ee-464f-be9d-58f11bf3418b.sketch_text.stroke-65"),sQuery(id+"F2.wireOp",EDGE,"fcba4419-a2ee-464f-be9d-58f11bf3418b.sketch_text.stroke-66"),sQuery(id+"F2.wireOp",EDGE,"fcba4419-a2ee-464f-be9d-58f11bf3418b.sketch_text.stroke-67"),sQuery(id+"F2.wireOp",EDGE,"fcba4419-a2ee-464f-be9d-58f11bf3418b.sketch_text.stroke-68"),sQuery(id+"F2.wireOp",EDGE,"fcba4419-a2ee-464f-be9d-58f11bf3418b.sketch_text.stroke-69"),sQuery(id+"F2.wireOp",EDGE,"fcba4419-a2ee-464f-be9d-58f11bf3418b.sketch_text.stroke-70"),sQuery(id+"F2.wireOp",EDGE,"fcba4419-a2ee-464f-be9d-58f11bf3418b.sketch_text.stroke-71"),sQuery(id+"F2.wireOp",EDGE,"fcba4419-a2ee-464f-be9d-58f11bf3418b.sketch_text.stroke-72"),sQuery(id+"F2.wireOp",EDGE,"fcba4419-a2ee-464f-be9d-58f11bf3418b.sketch_text.stroke-73"),sQuery(id+"F2.wireOp",EDGE,"fcba4419-a2ee-464f-be9d-58f11bf3418b.sketch_text.stroke-74"),sQuery(id+"F2.wireOp",EDGE,"fcba4419-a2ee-464f-be9d-58f11bf3418b.sketch_text.stroke-75"),sQuery(id+"F2.wireOp",EDGE,"fcba4419-a2ee-464f-be9d-58f11bf3418b.sketch_text.stroke-76"),sQuery(id+"F2.wireOp",EDGE,"fcba4419-a2ee-464f-be9d-58f11bf3418b.sketch_text.stroke-77"),sQuery(id+"F2.wireOp",EDGE,"fcba4419-a2ee-464f-be9d-58f11bf3418b.sketch_text.stroke-78"),sQuery(id+"F2.wireOp",EDGE,"fcba4419-a2ee-464f-be9d-58f11bf3418b.sketch_text.stroke-79"),sQuery(id+"F2.wireOp",EDGE,"fcba4419-a2ee-464f-be9d-58f11bf3418b.sketch_text.stroke-80"),sQuery(id+"F2.wireOp",EDGE,"fcba4419-a2ee-464f-be9d-58f11bf3418b.sketch_text.stroke-81"),sQuery(id+"F2.wireOp",EDGE,"fcba4419-a2ee-464f-be9d-58f11bf3418b.sketch_text.stroke-82"),sQuery(id+"F2.wireOp",EDGE,"fcba4419-a2ee-464f-be9d-58f11bf3418b.sketch_text.stroke-83"),sQuery(id+"F2.wireOp",EDGE,"fcba4419-a2ee-464f-be9d-58f11bf3418b.sketch_text.stroke-84"),sQuery(id+"F2.wireOp",EDGE,"fcba4419-a2ee-464f-be9d-58f11bf3418b.sketch_text.stroke-85"),sQuery(id+"F2.wireOp",EDGE,"fcba4419-a2ee-464f-be9d-58f11bf3418b.sketch_text.stroke-86"),sQuery(id+"F2.wireOp",EDGE,"fcba4419-a2ee-464f-be9d-58f11bf3418b.sketch_text.stroke-87"),sQuery(id+"F2.wireOp",EDGE,"fcba4419-a2ee-464f-be9d-58f11bf3418b.sketch_text.stroke-88"),sQuery(id+"F2.wireOp",EDGE,"fcba4419-a2ee-464f-be9d-58f11bf3418b.sketch_text.stroke-89"),sQuery(id+"F2.wireOp",EDGE,"fcba4419-a2ee-464f-be9d-58f11bf3418b.sketch_text.stroke-90"),sQuery(id+"F2.wireOp",EDGE,"fcba4419-a2ee-464f-be9d-58f11bf3418b.sketch_text.stroke-91"),sQuery(id+"F2.wireOp",EDGE,"fcba4419-a2ee-464f-be9d-58f11bf3418b.sketch_text.stroke-92"),sQuery(id+"F2.wireOp",EDGE,"fcba4419-a2ee-464f-be9d-58f11bf3418b.sketch_text.stroke-93"),sQuery(id+"F2.wireOp",EDGE,"fcba4419-a2ee-464f-be9d-58f11bf3418b.sketch_text.stroke-94"),sQuery(id+"F2.wireOp",EDGE,"fcba4419-a2ee-464f-be9d-58f11bf3418b.sketch_text.stroke-95"),sQuery(id+"F2.wireOp",EDGE,"fcba4419-a2ee-464f-be9d-58f11bf3418b.sketch_text.stroke-96"),sQuery(id+"F2.wireOp",EDGE,"fcba4419-a2ee-464f-be9d-58f11bf3418b.sketch_text.stroke-97"),sQuery(id+"F2.wireOp",EDGE,"fcba4419-a2ee-464f-be9d-58f11bf3418b.sketch_text.stroke-98"),sQuery(id+"F2.wireOp",EDGE,"fcba4419-a2ee-464f-be9d-58f11bf3418b.sketch_text.stroke-99"),sQuery(id+"F2.wireOp",EDGE,"fcba4419-a2ee-464f-be9d-58f11bf3418b.sketch_text.stroke-100"),sQuery(id+"F2.wireOp",EDGE,"fcba4419-a2ee-464f-be9d-58f11bf3418b.sketch_text.stroke-101"),sQuery(id+"F2.wireOp",EDGE,"fcba4419-a2ee-464f-be9d-58f11bf3418b.sketch_text.stroke-102"),sQuery(id+"F2.wireOp",EDGE,"fcba4419-a2ee-464f-be9d-58f11bf3418b.sketch_text.stroke-103"),sQuery(id+"F2.wireOp",EDGE,"fcba4419-a2ee-464f-be9d-58f11bf3418b.sketch_text.stroke-104"),sQuery(id+"F2.wireOp",EDGE,"fcba4419-a2ee-464f-be9d-58f11bf3418b.sketch_text.stroke-105"),sQuery(id+"F2.wireOp",EDGE,"fcba4419-a2ee-464f-be9d-58f11bf3418b.sketch_text.stroke-106"),sQuery(id+"F2.wireOp",EDGE,"fcba4419-a2ee-464f-be9d-58f11bf3418b.sketch_text.stroke-107"),sQuery(id+"F2.wireOp",EDGE,"fcba4419-a2ee-464f-be9d-58f11bf3418b.sketch_text.stroke-108"),sQuery(id+"F2.wireOp",EDGE,"fcba4419-a2ee-464f-be9d-58f11bf3418b.sketch_text.stroke-109"),sQuery(id+"F2.wireOp",EDGE,"fcba4419-a2ee-464f-be9d-58f11bf3418b.sketch_text.stroke-110"),sQuery(id+"F2.wireOp",EDGE,"fcba4419-a2ee-464f-be9d-58f11bf3418b.sketch_text.stroke-111"),sQuery(id+"F2.wireOp",EDGE,"fcba4419-a2ee-464f-be9d-58f11bf3418b.sketch_text.stroke-112"),sQuery(id+"F2.wireOp",EDGE,"fcba4419-a2ee-464f-be9d-58f11bf3418b.sketch_text.stroke-113"),sQuery(id+"F2.wireOp",EDGE,"fcba4419-a2ee-464f-be9d-58f11bf3418b.sketch_text.stroke-114"),sQuery(id+"F2.wireOp",EDGE,"fcba4419-a2ee-464f-be9d-58f11bf3418b.sketch_text.stroke-115"),sQuery(id+"F2.wireOp",EDGE,"fcba4419-a2ee-464f-be9d-58f11bf3418b.sketch_text.stroke-116"),sQuery(id+"F2.wireOp",EDGE,"fcba4419-a2ee-464f-be9d-58f11bf3418b.sketch_text.stroke-117"),sQuery(id+"F2.wireOp",EDGE,"fcba4419-a2ee-464f-be9d-58f11bf3418b.sketch_text.stroke-118"),sQuery(id+"F2.wireOp",EDGE,"fcba4419-a2ee-464f-be9d-58f11bf3418b.sketch_text.stroke-119"),sQuery(id+"F2.wireOp",EDGE,"fcba4419-a2ee-464f-be9d-58f11bf3418b.sketch_text.stroke-120"),sQuery(id+"F2.wireOp",EDGE,"fcba4419-a2ee-464f-be9d-58f11bf3418b.sketch_text.stroke-121"),sQuery(id+"F2.wireOp",EDGE,"fcba4419-a2ee-464f-be9d-58f11bf3418b.sketch_text.stroke-122"),sQuery(id+"F2.wireOp",EDGE,"fcba4419-a2ee-464f-be9d-58f11bf3418b.sketch_text.stroke-123"),sQuery(id+"F2.wireOp",EDGE,"fcba4419-a2ee-464f-be9d-58f11bf3418b.sketch_text.stroke-124"),sQuery(id+"F2.wireOp",EDGE,"fcba4419-a2ee-464f-be9d-58f11bf3418b.sketch_text.stroke-125"),sQuery(id+"F2.wireOp",EDGE,"fcba4419-a2ee-464f-be9d-58f11bf3418b.sketch_text.stroke-126"),sQuery(id+"F2.wireOp",EDGE,"fcba4419-a2ee-464f-be9d-58f11bf3418b.sketch_text.stroke-127"),sQuery(id+"F2.wireOp",EDGE,"fcba4419-a2ee-464f-be9d-58f11bf3418b.sketch_text.stroke-128"),sQuery(id+"F2.wireOp",EDGE,"fcba4419-a2ee-464f-be9d-58f11bf3418b.sketch_text.stroke-129"),sQuery(id+"F2.wireOp",EDGE,"fcba4419-a2ee-464f-be9d-58f11bf3418b.sketch_text.stroke-130"),sQuery(id+"F2.wireOp",EDGE,"fcba4419-a2ee-464f-be9d-58f11bf3418b.sketch_text.stroke-131"),sQuery(id+"F2.wireOp",EDGE,"fcba4419-a2ee-464f-be9d-58f11bf3418b.sketch_text.stroke-132"),sQuery(id+"F2.wireOp",EDGE,"fcba4419-a2ee-464f-be9d-58f11bf3418b.sketch_text.stroke-133"),sQuery(id+"F2.wireOp",EDGE,"fcba4419-a2ee-464f-be9d-58f11bf3418b.sketch_text.stroke-134"),sQuery(id+"F2.wireOp",EDGE,"fcba4419-a2ee-464f-be9d-58f11bf3418b.sketch_text.stroke-135"),sQuery(id+"F2.wireOp",EDGE,"fcba4419-a2ee-464f-be9d-58f11bf3418b.sketch_text.stroke-136"),sQuery(id+"F2.wireOp",EDGE,"fcba4419-a2ee-464f-be9d-58f11bf3418b.sketch_text.stroke-137"),sQuery(id+"F2.wireOp",EDGE,"fcba4419-a2ee-464f-be9d-58f11bf3418b.sketch_text.stroke-138"),sQuery(id+"F2.wireOp",EDGE,"fcba4419-a2ee-464f-be9d-58f11bf3418b.sketch_text.stroke-139"),sQuery(id+"F2.wireOp",EDGE,"fcba4419-a2ee-464f-be9d-58f11bf3418b.sketch_text.stroke-140"),sQuery(id+"F2.wireOp",EDGE,"fcba4419-a2ee-464f-be9d-58f11bf3418b.sketch_text.stroke-141"),sQuery(id+"F2.wireOp",EDGE,"fcba4419-a2ee-464f-be9d-58f11bf3418b.sketch_text.stroke-142"),sQuery(id+"F2.wireOp",EDGE,"fcba4419-a2ee-464f-be9d-58f11bf3418b.sketch_text.stroke-143"),sQuery(id+"F2.wireOp",EDGE,"fcba4419-a2ee-464f-be9d-58f11bf3418b.sketch_text.stroke-144"),sQuery(id+"F2.wireOp",EDGE,"fcba4419-a2ee-464f-be9d-58f11bf3418b.sketch_text.stroke-145"),sQuery(id+"F2.wireOp",EDGE,"fcba4419-a2ee-464f-be9d-58f11bf3418b.sketch_text.stroke-146"),sQuery(id+"F2.wireOp",EDGE,"fcba4419-a2ee-464f-be9d-58f11bf3418b.sketch_text.stroke-147"),sQuery(id+"F2.wireOp",EDGE,"fcba4419-a2ee-464f-be9d-58f11bf3418b.sketch_text.stroke-148"),sQuery(id+"F2.wireOp",EDGE,"fcba4419-a2ee-464f-be9d-58f11bf3418b.sketch_text.stroke-149"),sQuery(id+"F2.wireOp",EDGE,"fcba4419-a2ee-464f-be9d-58f11bf3418b.sketch_text.stroke-150"),sQuery(id+"F2.wireOp",EDGE,"fcba4419-a2ee-464f-be9d-58f11bf3418b.sketch_text.stroke-151"),sQuery(id+"F2.wireOp",EDGE,"fcba4419-a2ee-464f-be9d-58f11bf3418b.sketch_text.stroke-152"),sQuery(id+"F2.wireOp",EDGE,"fcba4419-a2ee-464f-be9d-58f11bf3418b.sketch_text.stroke-153"),sQuery(id+"F2.wireOp",EDGE,"fcba4419-a2ee-464f-be9d-58f11bf3418b.sketch_text.stroke-154"),sQuery(id+"F2.wireOp",EDGE,"fcba4419-a2ee-464f-be9d-58f11bf3418b.sketch_text.stroke-155"),sQuery(id+"F2.wireOp",EDGE,"fcba4419-a2ee-464f-be9d-58f11bf3418b.sketch_text.stroke-156"),sQuery(id+"F2.wireOp",EDGE,"fcba4419-a2ee-464f-be9d-58f11bf3418b.sketch_text.stroke-157"),sQuery(id+"F2.wireOp",EDGE,"fcba4419-a2ee-464f-be9d-58f11bf3418b.sketch_text.stroke-158"),sQuery(id+"F2.wireOp",EDGE,"fcba4419-a2ee-464f-be9d-58f11bf3418b.sketch_text.stroke-159"),sQuery(id+"F2.wireOp",EDGE,"fcba4419-a2ee-464f-be9d-58f11bf3418b.sketch_text.stroke-160"),sQuery(id+"F2.wireOp",EDGE,"fcba4419-a2ee-464f-be9d-58f11bf3418b.sketch_text.stroke-161"),sQuery(id+"F2.wireOp",EDGE,"fcba4419-a2ee-464f-be9d-58f11bf3418b.sketch_text.stroke-162"),sQuery(id+"F2.wireOp",EDGE,"fcba4419-a2ee-464f-be9d-58f11bf3418b.sketch_text.stroke-163"),sQuery(id+"F2.wireOp",EDGE,"fcba4419-a2ee-464f-be9d-58f11bf3418b.sketch_text.stroke-164"),sQuery(id+"F2.wireOp",EDGE,"fcba4419-a2ee-464f-be9d-58f11bf3418b.sketch_text.stroke-165"),sQuery(id+"F2.wireOp",EDGE,"fcba4419-a2ee-464f-be9d-58f11bf3418b.sketch_text.stroke-166"),sQuery(id+"F2.wireOp",EDGE,"fcba4419-a2ee-464f-be9d-58f11bf3418b.sketch_text.stroke-167"),sQuery(id+"F2.wireOp",EDGE,"fcba4419-a2ee-464f-be9d-58f11bf3418b.sketch_text.stroke-168"),sQuery(id+"F2.wireOp",EDGE,"fcba4419-a2ee-464f-be9d-58f11bf3418b.sketch_text.stroke-169"),sQuery(id+"F2.wireOp",EDGE,"fcba4419-a2ee-464f-be9d-58f11bf3418b.sketch_text.stroke-170"),sQuery(id+"F2.wireOp",EDGE,"fcba4419-a2ee-464f-be9d-58f11bf3418b.sketch_text.stroke-171"),sQuery(id+"F2.wireOp",EDGE,"fcba4419-a2ee-464f-be9d-58f11bf3418b.sketch_text.stroke-172"),sQuery(id+"F2.wireOp",EDGE,"fcba4419-a2ee-464f-be9d-58f11bf3418b.sketch_text.stroke-173"),sQuery(id+"FHMxAyK4CFUKdhS_1.wireOp",EDGE,"1cb9c079-ea9b-4899-8069-e0e3048e911d.sketch_text.stroke-0"),sQuery(id+"FHMxAyK4CFUKdhS_1.wireOp",EDGE,"1cb9c079-ea9b-4899-8069-e0e3048e911d.sketch_text.stroke-1"),sQuery(id+"FHMxAyK4CFUKdhS_1.wireOp",EDGE,"1cb9c079-ea9b-4899-8069-e0e3048e911d.sketch_text.stroke-2"),sQuery(id+"FHMxAyK4CFUKdhS_1.wireOp",EDGE,"1cb9c079-ea9b-4899-8069-e0e3048e911d.sketch_text.stroke-3"),sQuery(id+"FHMxAyK4CFUKdhS_1.wireOp",EDGE,"1cb9c079-ea9b-4899-8069-e0e3048e911d.sketch_text.stroke-4"),sQuery(id+"FHMxAyK4CFUKdhS_1.wireOp",EDGE,"1cb9c079-ea9b-4899-8069-e0e3048e911d.sketch_text.stroke-5"),sQuery(id+"FHMxAyK4CFUKdhS_1.wireOp",EDGE,"1cb9c079-ea9b-4899-8069-e0e3048e911d.sketch_text.stroke-6"),sQuery(id+"FHMxAyK4CFUKdhS_1.wireOp",EDGE,"1cb9c079-ea9b-4899-8069-e0e3048e911d.sketch_text.stroke-7"),sQuery(id+"FHMxAyK4CFUKdhS_1.wireOp",EDGE,"1cb9c079-ea9b-4899-8069-e0e3048e911d.sketch_text.stroke-8"),sQuery(id+"FHMxAyK4CFUKdhS_1.wireOp",EDGE,"1cb9c079-ea9b-4899-8069-e0e3048e911d.sketch_text.stroke-9"),sQuery(id+"FHMxAyK4CFUKdhS_1.wireOp",EDGE,"1cb9c079-ea9b-4899-8069-e0e3048e911d.sketch_text.stroke-10"),sQuery(id+"FHMxAyK4CFUKdhS_1.wireOp",EDGE,"1cb9c079-ea9b-4899-8069-e0e3048e911d.sketch_text.stroke-11"),sQuery(id+"FHMxAyK4CFUKdhS_1.wireOp",EDGE,"1cb9c079-ea9b-4899-8069-e0e3048e911d.sketch_text.stroke-12"),sQuery(id+"FHMxAyK4CFUKdhS_1.wireOp",EDGE,"1cb9c079-ea9b-4899-8069-e0e3048e911d.sketch_text.stroke-13"),sQuery(id+"FHMxAyK4CFUKdhS_1.wireOp",EDGE,"1cb9c079-ea9b-4899-8069-e0e3048e911d.sketch_text.stroke-14"),sQuery(id+"FHMxAyK4CFUKdhS_1.wireOp",EDGE,"1cb9c079-ea9b-4899-8069-e0e3048e911d.sketch_text.stroke-15"),sQuery(id+"FHMxAyK4CFUKdhS_1.wireOp",EDGE,"1cb9c079-ea9b-4899-8069-e0e3048e911d.sketch_text.stroke-16"),sQuery(id+"FHMxAyK4CFUKdhS_1.wireOp",EDGE,"1cb9c079-ea9b-4899-8069-e0e3048e911d.sketch_text.stroke-17"),sQuery(id+"FHMxAyK4CFUKdhS_1.wireOp",EDGE,"1cb9c079-ea9b-4899-8069-e0e3048e911d.sketch_text.stroke-18"),sQuery(id+"FHMxAyK4CFUKdhS_1.wireOp",EDGE,"1cb9c079-ea9b-4899-8069-e0e3048e911d.sketch_text.stroke-19"),sQuery(id+"FHMxAyK4CFUKdhS_1.wireOp",EDGE,"1cb9c079-ea9b-4899-8069-e0e3048e911d.sketch_text.stroke-20"),sQuery(id+"FHMxAyK4CFUKdhS_1.wireOp",EDGE,"1cb9c079-ea9b-4899-8069-e0e3048e911d.sketch_text.stroke-21"),sQuery(id+"FHMxAyK4CFUKdhS_1.wireOp",EDGE,"1cb9c079-ea9b-4899-8069-e0e3048e911d.sketch_text.stroke-22"),sQuery(id+"FHMxAyK4CFUKdhS_1.wireOp",EDGE,"1cb9c079-ea9b-4899-8069-e0e3048e911d.sketch_text.stroke-23"),sQuery(id+"FHMxAyK4CFUKdhS_1.wireOp",EDGE,"1cb9c079-ea9b-4899-8069-e0e3048e911d.sketch_text.stroke-24"),sQuery(id+"FHMxAyK4CFUKdhS_1.wireOp",EDGE,"1cb9c079-ea9b-4899-8069-e0e3048e911d.sketch_text.stroke-25"),sQuery(id+"FHMxAyK4CFUKdhS_1.wireOp",EDGE,"1cb9c079-ea9b-4899-8069-e0e3048e911d.sketch_text.stroke-26"),sQuery(id+"FHMxAyK4CFUKdhS_1.wireOp",EDGE,"1cb9c079-ea9b-4899-8069-e0e3048e911d.sketch_text.stroke-27"),sQuery(id+"FHMxAyK4CFUKdhS_1.wireOp",EDGE,"1cb9c079-ea9b-4899-8069-e0e3048e911d.sketch_text.stroke-28"),sQuery(id+"FHMxAyK4CFUKdhS_1.wireOp",EDGE,"1cb9c079-ea9b-4899-8069-e0e3048e911d.sketch_text.stroke-29"),sQuery(id+"FHMxAyK4CFUKdhS_1.wireOp",EDGE,"1cb9c079-ea9b-4899-8069-e0e3048e911d.sketch_text.stroke-30"),sQuery(id+"FHMxAyK4CFUKdhS_1.wireOp",EDGE,"1cb9c079-ea9b-4899-8069-e0e3048e911d.sketch_text.stroke-31"),sQuery(id+"FHMxAyK4CFUKdhS_1.wireOp",EDGE,"1cb9c079-ea9b-4899-8069-e0e3048e911d.sketch_text.stroke-32"),sQuery(id+"FHMxAyK4CFUKdhS_1.wireOp",EDGE,"1cb9c079-ea9b-4899-8069-e0e3048e911d.sketch_text.stroke-33"),sQuery(id+"FHMxAyK4CFUKdhS_1.wireOp",EDGE,"1cb9c079-ea9b-4899-8069-e0e3048e911d.sketch_text.stroke-34"),sQuery(id+"FHMxAyK4CFUKdhS_1.wireOp",EDGE,"1cb9c079-ea9b-4899-8069-e0e3048e911d.sketch_text.stroke-35"),sQuery(id+"FHMxAyK4CFUKdhS_1.wireOp",EDGE,"1cb9c079-ea9b-4899-8069-e0e3048e911d.sketch_text.stroke-36"),sQuery(id+"FHMxAyK4CFUKdhS_1.wireOp",EDGE,"1cb9c079-ea9b-4899-8069-e0e3048e911d.sketch_text.stroke-37"),sQuery(id+"FHMxAyK4CFUKdhS_1.wireOp",EDGE,"1cb9c079-ea9b-4899-8069-e0e3048e911d.sketch_text.stroke-38"),sQuery(id+"FHMxAyK4CFUKdhS_1.wireOp",EDGE,"1cb9c079-ea9b-4899-8069-e0e3048e911d.sketch_text.stroke-39"),sQuery(id+"FHMxAyK4CFUKdhS_1.wireOp",EDGE,"1cb9c079-ea9b-4899-8069-e0e3048e911d.sketch_text.stroke-40"),sQuery(id+"FHMxAyK4CFUKdhS_1.wireOp",EDGE,"1cb9c079-ea9b-4899-8069-e0e3048e911d.sketch_text.stroke-41"),sQuery(id+"FHMxAyK4CFUKdhS_1.wireOp",EDGE,"1cb9c079-ea9b-4899-8069-e0e3048e911d.sketch_text.stroke-42"),sQuery(id+"FHMxAyK4CFUKdhS_1.wireOp",EDGE,"1cb9c079-ea9b-4899-8069-e0e3048e911d.sketch_text.stroke-43"),sQuery(id+"FHMxAyK4CFUKdhS_1.wireOp",EDGE,"1cb9c079-ea9b-4899-8069-e0e3048e911d.sketch_text.stroke-44"),sQuery(id+"FHMxAyK4CFUKdhS_1.wireOp",EDGE,"1cb9c079-ea9b-4899-8069-e0e3048e911d.sketch_text.stroke-45"),sQuery(id+"FHMxAyK4CFUKdhS_1.wireOp",EDGE,"1cb9c079-ea9b-4899-8069-e0e3048e911d.sketch_text.stroke-46"),sQuery(id+"FHMxAyK4CFUKdhS_1.wireOp",EDGE,"1cb9c079-ea9b-4899-8069-e0e3048e911d.sketch_text.stroke-47"),sQuery(id+"FHMxAyK4CFUKdhS_1.wireOp",EDGE,"1cb9c079-ea9b-4899-8069-e0e3048e911d.sketch_text.stroke-48"),sQuery(id+"FHMxAyK4CFUKdhS_1.wireOp",EDGE,"1cb9c079-ea9b-4899-8069-e0e3048e911d.sketch_text.stroke-49"),sQuery(id+"FHMxAyK4CFUKdhS_1.wireOp",EDGE,"1cb9c079-ea9b-4899-8069-e0e3048e911d.sketch_text.stroke-50"),sQuery(id+"FHMxAyK4CFUKdhS_1.wireOp",EDGE,"1cb9c079-ea9b-4899-8069-e0e3048e911d.sketch_text.stroke-51"),sQuery(id+"FHMxAyK4CFUKdhS_1.wireOp",EDGE,"1cb9c079-ea9b-4899-8069-e0e3048e911d.sketch_text.stroke-52"),sQuery(id+"FHMxAyK4CFUKdhS_1.wireOp",EDGE,"1cb9c079-ea9b-4899-8069-e0e3048e911d.sketch_text.stroke-53"),sQuery(id+"FHMxAyK4CFUKdhS_1.wireOp",EDGE,"1cb9c079-ea9b-4899-8069-e0e3048e911d.sketch_text.stroke-54"),sQuery(id+"FHMxAyK4CFUKdhS_1.wireOp",EDGE,"1cb9c079-ea9b-4899-8069-e0e3048e911d.sketch_text.stroke-55"),sQuery(id+"FHMxAyK4CFUKdhS_1.wireOp",EDGE,"1cb9c079-ea9b-4899-8069-e0e3048e911d.sketch_text.stroke-56"),sQuery(id+"FHMxAyK4CFUKdhS_1.wireOp",EDGE,"1cb9c079-ea9b-4899-8069-e0e3048e911d.sketch_text.stroke-57"),sQuery(id+"FHMxAyK4CFUKdhS_1.wireOp",EDGE,"1cb9c079-ea9b-4899-8069-e0e3048e911d.sketch_text.stroke-58"),sQuery(id+"FHMxAyK4CFUKdhS_1.wireOp",EDGE,"1cb9c079-ea9b-4899-8069-e0e3048e911d.sketch_text.stroke-59"),sQuery(id+"FHMxAyK4CFUKdhS_1.wireOp",EDGE,"1cb9c079-ea9b-4899-8069-e0e3048e911d.sketch_text.stroke-60"),sQuery(id+"FHMxAyK4CFUKdhS_1.wireOp",EDGE,"1cb9c079-ea9b-4899-8069-e0e3048e911d.sketch_text.stroke-61"),sQuery(id+"FHMxAyK4CFUKdhS_1.wireOp",EDGE,"1cb9c079-ea9b-4899-8069-e0e3048e911d.sketch_text.stroke-62"),sQuery(id+"FHMxAyK4CFUKdhS_1.wireOp",EDGE,"1cb9c079-ea9b-4899-8069-e0e3048e911d.sketch_text.stroke-71"),sQuery(id+"FHMxAyK4CFUKdhS_1.wireOp",EDGE,"1cb9c079-ea9b-4899-8069-e0e3048e911d.sketch_text.stroke-72"),sQuery(id+"FHMxAyK4CFUKdhS_1.wireOp",EDGE,"1cb9c079-ea9b-4899-8069-e0e3048e911d.sketch_text.stroke-73"),sQuery(id+"FHMxAyK4CFUKdhS_1.wireOp",EDGE,"1cb9c079-ea9b-4899-8069-e0e3048e911d.sketch_text.stroke-74"),sQuery(id+"FHMxAyK4CFUKdhS_1.wireOp",EDGE,"1cb9c079-ea9b-4899-8069-e0e3048e911d.sketch_text.stroke-75"),sQuery(id+"FHMxAyK4CFUKdhS_1.wireOp",EDGE,"1cb9c079-ea9b-4899-8069-e0e3048e911d.sketch_text.stroke-76"),sQuery(id+"FHMxAyK4CFUKdhS_1.wireOp",EDGE,"1cb9c079-ea9b-4899-8069-e0e3048e911d.sketch_text.stroke-77"),sQuery(id+"FHMxAyK4CFUKdhS_1.wireOp",EDGE,"1cb9c079-ea9b-4899-8069-e0e3048e911d.sketch_text.stroke-78"),sQuery(id+"FHMxAyK4CFUKdhS_1.wireOp",EDGE,"1cb9c079-ea9b-4899-8069-e0e3048e911d.sketch_text.stroke-79"),sQuery(id+"FHMxAyK4CFUKdhS_1.wireOp",EDGE,"1cb9c079-ea9b-4899-8069-e0e3048e911d.sketch_text.stroke-80"),sQuery(id+"FHMxAyK4CFUKdhS_1.wireOp",EDGE,"1cb9c079-ea9b-4899-8069-e0e3048e911d.sketch_text.stroke-81"),sQuery(id+"FHMxAyK4CFUKdhS_1.wireOp",EDGE,"1cb9c079-ea9b-4899-8069-e0e3048e911d.sketch_text.stroke-82"),sQuery(id+"FHMxAyK4CFUKdhS_1.wireOp",EDGE,"1cb9c079-ea9b-4899-8069-e0e3048e911d.sketch_text.stroke-83"),sQuery(id+"FHMxAyK4CFUKdhS_1.wireOp",EDGE,"1cb9c079-ea9b-4899-8069-e0e3048e911d.sketch_text.stroke-84"),sQuery(id+"FHMxAyK4CFUKdhS_1.wireOp",EDGE,"1cb9c079-ea9b-4899-8069-e0e3048e911d.sketch_text.stroke-85"),sQuery(id+"FHMxAyK4CFUKdhS_1.wireOp",EDGE,"1cb9c079-ea9b-4899-8069-e0e3048e911d.sketch_text.stroke-86"),sQuery(id+"FHMxAyK4CFUKdhS_1.wireOp",EDGE,"1cb9c079-ea9b-4899-8069-e0e3048e911d.sketch_text.stroke-87"),sQuery(id+"FHMxAyK4CFUKdhS_1.wireOp",EDGE,"1cb9c079-ea9b-4899-8069-e0e3048e911d.sketch_text.stroke-88"),sQuery(id+"FHMxAyK4CFUKdhS_1.wireOp",EDGE,"1cb9c079-ea9b-4899-8069-e0e3048e911d.sketch_text.stroke-89"),sQuery(id+"FHMxAyK4CFUKdhS_1.wireOp",EDGE,"1cb9c079-ea9b-4899-8069-e0e3048e911d.sketch_text.stroke-90"),sQuery(id+"FHMxAyK4CFUKdhS_1.wireOp",EDGE,"1cb9c079-ea9b-4899-8069-e0e3048e911d.sketch_text.stroke-91"),sQuery(id+"FHMxAyK4CFUKdhS_1.wireOp",EDGE,"1cb9c079-ea9b-4899-8069-e0e3048e911d.sketch_text.stroke-92"),sQuery(id+"FHMxAyK4CFUKdhS_1.wireOp",EDGE,"1cb9c079-ea9b-4899-8069-e0e3048e911d.sketch_text.stroke-93"),sQuery(id+"FHMxAyK4CFUKdhS_1.wireOp",EDGE,"1cb9c079-ea9b-4899-8069-e0e3048e911d.sketch_text.stroke-94"),sQuery(id+"FHMxAyK4CFUKdhS_1.wireOp",EDGE,"1cb9c079-ea9b-4899-8069-e0e3048e911d.sketch_text.stroke-95"),sQuery(id+"FHMxAyK4CFUKdhS_1.wireOp",EDGE,"1cb9c079-ea9b-4899-8069-e0e3048e911d.sketch_text.stroke-96"),sQuery(id+"FHMxAyK4CFUKdhS_1.wireOp",EDGE,"1cb9c079-ea9b-4899-8069-e0e3048e911d.sketch_text.stroke-97"),sQuery(id+"FHMxAyK4CFUKdhS_1.wireOp",EDGE,"1cb9c079-ea9b-4899-8069-e0e3048e911d.sketch_text.stroke-103"),sQuery(id+"FHMxAyK4CFUKdhS_1.wireOp",EDGE,"1cb9c079-ea9b-4899-8069-e0e3048e911d.sketch_text.stroke-104"),sQuery(id+"FHMxAyK4CFUKdhS_1.wireOp",EDGE,"1cb9c079-ea9b-4899-8069-e0e3048e911d.sketch_text.stroke-105"),sQuery(id+"FHMxAyK4CFUKdhS_1.wireOp",EDGE,"1cb9c079-ea9b-4899-8069-e0e3048e911d.sketch_text.stroke-106"),sQuery(id+"FHMxAyK4CFUKdhS_1.wireOp",EDGE,"1cb9c079-ea9b-4899-8069-e0e3048e911d.sketch_text.stroke-107"),sQuery(id+"FHMxAyK4CFUKdhS_1.wireOp",EDGE,"1cb9c079-ea9b-4899-8069-e0e3048e911d.sketch_text.stroke-108"),sQuery(id+"FHMxAyK4CFUKdhS_1.wireOp",EDGE,"1cb9c079-ea9b-4899-8069-e0e3048e911d.sketch_text.stroke-109"),sQuery(id+"FHMxAyK4CFUKdhS_1.wireOp",EDGE,"1cb9c079-ea9b-4899-8069-e0e3048e911d.sketch_text.stroke-110"),sQuery(id+"FHMxAyK4CFUKdhS_1.wireOp",EDGE,"1cb9c079-ea9b-4899-8069-e0e3048e911d.sketch_text.stroke-111"),sQuery(id+"FHMxAyK4CFUKdhS_1.wireOp",EDGE,"1cb9c079-ea9b-4899-8069-e0e3048e911d.sketch_text.stroke-112"),sQuery(id+"FHMxAyK4CFUKdhS_1.wireOp",EDGE,"1cb9c079-ea9b-4899-8069-e0e3048e911d.sketch_text.stroke-113"),sQuery(id+"FHMxAyK4CFUKdhS_1.wireOp",EDGE,"1cb9c079-ea9b-4899-8069-e0e3048e911d.sketch_text.stroke-114"),sQuery(id+"FHMxAyK4CFUKdhS_1.wireOp",EDGE,"1cb9c079-ea9b-4899-8069-e0e3048e911d.sketch_text.stroke-115"),sQuery(id+"FHMxAyK4CFUKdhS_1.wireOp",EDGE,"1cb9c079-ea9b-4899-8069-e0e3048e911d.sketch_text.stroke-116"),sQuery(id+"FHMxAyK4CFUKdhS_1.wireOp",EDGE,"1cb9c079-ea9b-4899-8069-e0e3048e911d.sketch_text.stroke-117"),sQuery(id+"FHMxAyK4CFUKdhS_1.wireOp",EDGE,"1cb9c079-ea9b-4899-8069-e0e3048e911d.sketch_text.stroke-118"),sQuery(id+"FHMxAyK4CFUKdhS_1.wireOp",EDGE,"1cb9c079-ea9b-4899-8069-e0e3048e911d.sketch_text.stroke-119"),sQuery(id+"FHMxAyK4CFUKdhS_1.wireOp",EDGE,"1cb9c079-ea9b-4899-8069-e0e3048e911d.sketch_text.stroke-120"),sQuery(id+"FHMxAyK4CFUKdhS_1.wireOp",EDGE,"1cb9c079-ea9b-4899-8069-e0e3048e911d.sketch_text.stroke-121"),sQuery(id+"FHMxAyK4CFUKdhS_1.wireOp",EDGE,"1cb9c079-ea9b-4899-8069-e0e3048e911d.sketch_text.stroke-122"),sQuery(id+"FHMxAyK4CFUKdhS_1.wireOp",EDGE,"1cb9c079-ea9b-4899-8069-e0e3048e911d.sketch_text.stroke-123"),sQuery(id+"FHMxAyK4CFUKdhS_1.wireOp",EDGE,"1cb9c079-ea9b-4899-8069-e0e3048e911d.sketch_text.stroke-124"),sQuery(id+"FHMxAyK4CFUKdhS_1.wireOp",EDGE,"1cb9c079-ea9b-4899-8069-e0e3048e911d.sketch_text.stroke-125"),sQuery(id+"FHMxAyK4CFUKdhS_1.wireOp",EDGE,"1cb9c079-ea9b-4899-8069-e0e3048e911d.sketch_text.stroke-126"),sQuery(id+"FHMxAyK4CFUKdhS_1.wireOp",EDGE,"1cb9c079-ea9b-4899-8069-e0e3048e911d.sketch_text.stroke-127"),sQuery(id+"FHMxAyK4CFUKdhS_1.wireOp",EDGE,"1cb9c079-ea9b-4899-8069-e0e3048e911d.sketch_text.stroke-128"),sQuery(id+"FHMxAyK4CFUKdhS_1.wireOp",EDGE,"1cb9c079-ea9b-4899-8069-e0e3048e911d.sketch_text.stroke-129"),sQuery(id+"FHMxAyK4CFUKdhS_1.wireOp",EDGE,"1cb9c079-ea9b-4899-8069-e0e3048e911d.sketch_text.stroke-130"),sQuery(id+"FHMxAyK4CFUKdhS_1.wireOp",EDGE,"1cb9c079-ea9b-4899-8069-e0e3048e911d.sketch_text.stroke-131"),sQuery(id+"FHMxAyK4CFUKdhS_1.wireOp",EDGE,"1cb9c079-ea9b-4899-8069-e0e3048e911d.sketch_text.stroke-132"),sQuery(id+"FHMxAyK4CFUKdhS_1.wireOp",EDGE,"1cb9c079-ea9b-4899-8069-e0e3048e911d.sketch_text.stroke-133"),sQuery(id+"FHMxAyK4CFUKdhS_1.wireOp",EDGE,"1cb9c079-ea9b-4899-8069-e0e3048e911d.sketch_text.stroke-134"),sQuery(id+"FHMxAyK4CFUKdhS_1.wireOp",EDGE,"1cb9c079-ea9b-4899-8069-e0e3048e911d.sketch_text.stroke-135"),sQuery(id+"FHMxAyK4CFUKdhS_1.wireOp",EDGE,"1cb9c079-ea9b-4899-8069-e0e3048e911d.sketch_text.stroke-136"),sQuery(id+"FHMxAyK4CFUKdhS_1.wireOp",EDGE,"1cb9c079-ea9b-4899-8069-e0e3048e911d.sketch_text.stroke-137"),sQuery(id+"FHMxAyK4CFUKdhS_1.wireOp",EDGE,"1cb9c079-ea9b-4899-8069-e0e3048e911d.sketch_text.stroke-138"),sQuery(id+"FHMxAyK4CFUKdhS_1.wireOp",EDGE,"1cb9c079-ea9b-4899-8069-e0e3048e911d.sketch_text.stroke-139"),sQuery(id+"FHMxAyK4CFUKdhS_1.wireOp",EDGE,"1cb9c079-ea9b-4899-8069-e0e3048e911d.sketch_text.stroke-140"),sQuery(id+"FHMxAyK4CFUKdhS_1.wireOp",EDGE,"1cb9c079-ea9b-4899-8069-e0e3048e911d.sketch_text.stroke-141"),sQuery(id+"FHMxAyK4CFUKdhS_1.wireOp",EDGE,"1cb9c079-ea9b-4899-8069-e0e3048e911d.sketch_text.stroke-142"),sQuery(id+"FHMxAyK4CFUKdhS_1.wireOp",EDGE,"1cb9c079-ea9b-4899-8069-e0e3048e911d.sketch_text.stroke-143"),sQuery(id+"FHMxAyK4CFUKdhS_1.wireOp",EDGE,"1cb9c079-ea9b-4899-8069-e0e3048e911d.sketch_text.stroke-144"),sQuery(id+"FHMxAyK4CFUKdhS_1.wireOp",EDGE,"1cb9c079-ea9b-4899-8069-e0e3048e911d.sketch_text.stroke-145"),sQuery(id+"FHMxAyK4CFUKdhS_1.wireOp",EDGE,"1cb9c079-ea9b-4899-8069-e0e3048e911d.sketch_text.stroke-146"),sQuery(id+"FHMxAyK4CFUKdhS_1.wireOp",EDGE,"1cb9c079-ea9b-4899-8069-e0e3048e911d.sketch_text.stroke-147"),sQuery(id+"FHMxAyK4CFUKdhS_1.wireOp",EDGE,"1cb9c079-ea9b-4899-8069-e0e3048e911d.sketch_text.stroke-148"),sQuery(id+"FHMxAyK4CFUKdhS_1.wireOp",EDGE,"1cb9c079-ea9b-4899-8069-e0e3048e911d.sketch_text.stroke-149"),sQuery(id+"FHMxAyK4CFUKdhS_1.wireOp",EDGE,"1cb9c079-ea9b-4899-8069-e0e3048e911d.sketch_text.stroke-150"),sQuery(id+"FHMxAyK4CFUKdhS_1.wireOp",EDGE,"1cb9c079-ea9b-4899-8069-e0e3048e911d.sketch_text.stroke-151"),sQuery(id+"FHMxAyK4CFUKdhS_1.wireOp",EDGE,"1cb9c079-ea9b-4899-8069-e0e3048e911d.sketch_text.stroke-152"),sQuery(id+"FHMxAyK4CFUKdhS_1.wireOp",EDGE,"1cb9c079-ea9b-4899-8069-e0e3048e911d.sketch_text.stroke-153"),sQuery(id+"FHMxAyK4CFUKdhS_1.wireOp",EDGE,"1cb9c079-ea9b-4899-8069-e0e3048e911d.sketch_text.stroke-159"),sQuery(id+"FHMxAyK4CFUKdhS_1.wireOp",EDGE,"1cb9c079-ea9b-4899-8069-e0e3048e911d.sketch_text.stroke-160"),sQuery(id+"FHMxAyK4CFUKdhS_1.wireOp",EDGE,"1cb9c079-ea9b-4899-8069-e0e3048e911d.sketch_text.stroke-161"),sQuery(id+"FHMxAyK4CFUKdhS_1.wireOp",EDGE,"1cb9c079-ea9b-4899-8069-e0e3048e911d.sketch_text.stroke-162"),sQuery(id+"FHMxAyK4CFUKdhS_1.wireOp",EDGE,"1cb9c079-ea9b-4899-8069-e0e3048e911d.sketch_text.stroke-163"),sQuery(id+"FHMxAyK4CFUKdhS_1.wireOp",EDGE,"1cb9c079-ea9b-4899-8069-e0e3048e911d.sketch_text.stroke-164"),sQuery(id+"FHMxAyK4CFUKdhS_1.wireOp",EDGE,"1cb9c079-ea9b-4899-8069-e0e3048e911d.sketch_text.stroke-165"),sQuery(id+"FHMxAyK4CFUKdhS_1.wireOp",EDGE,"1cb9c079-ea9b-4899-8069-e0e3048e911d.sketch_text.stroke-166"),sQuery(id+"FHMxAyK4CFUKdhS_1.wireOp",EDGE,"1cb9c079-ea9b-4899-8069-e0e3048e911d.sketch_text.stroke-167"),sQuery(id+"FHMxAyK4CFUKdhS_1.wireOp",EDGE,"1cb9c079-ea9b-4899-8069-e0e3048e911d.sketch_text.stroke-168"),sQuery(id+"FHMxAyK4CFUKdhS_1.wireOp",EDGE,"1cb9c079-ea9b-4899-8069-e0e3048e911d.sketch_text.stroke-169"),sQuery(id+"FHMxAyK4CFUKdhS_1.wireOp",EDGE,"1cb9c079-ea9b-4899-8069-e0e3048e911d.sketch_text.stroke-170"),sQuery(id+"FHMxAyK4CFUKdhS_1.wireOp",EDGE,"1cb9c079-ea9b-4899-8069-e0e3048e911d.sketch_text.stroke-171"),sQuery(id+"FHMxAyK4CFUKdhS_1.wireOp",EDGE,"1cb9c079-ea9b-4899-8069-e0e3048e911d.sketch_text.stroke-172"),sQuery(id+"FHMxAyK4CFUKdhS_1.wireOp",EDGE,"1cb9c079-ea9b-4899-8069-e0e3048e911d.sketch_text.stroke-173"),sQuery(id+"FHMxAyK4CFUKdhS_1.wireOp",EDGE,"1cb9c079-ea9b-4899-8069-e0e3048e911d.sketch_text.stroke-174"),sQuery(id+"FHMxAyK4CFUKdhS_1.wireOp",EDGE,"1cb9c079-ea9b-4899-8069-e0e3048e911d.sketch_text.stroke-175"),sQuery(id+"FHMxAyK4CFUKdhS_1.wireOp",EDGE,"1cb9c079-ea9b-4899-8069-e0e3048e911d.sketch_text.stroke-176"),sQuery(id+"FHMxAyK4CFUKdhS_1.wireOp",EDGE,"1cb9c079-ea9b-4899-8069-e0e3048e911d.sketch_text.stroke-177"),sQuery(id+"FHMxAyK4CFUKdhS_1.wireOp",EDGE,"1cb9c079-ea9b-4899-8069-e0e3048e911d.sketch_text.stroke-178"),sQuery(id+"FHMxAyK4CFUKdhS_1.wireOp",EDGE,"1cb9c079-ea9b-4899-8069-e0e3048e911d.sketch_text.stroke-179"),sQuery(id+"FHMxAyK4CFUKdhS_1.wireOp",EDGE,"1cb9c079-ea9b-4899-8069-e0e3048e911d.sketch_text.stroke-180"),subQ2,sQuery(id+"F3.wireOp",EDGE,"E29")])],"isStart":true})])],"derivedFrom":makeQuery(id+"F4.opExtrude","CAP_EDGE",EDGE,{"disambiguationData":[OSD([subQ2])],"isStart":true})});}
            var Q21;
            {var subQ0=sQuery(id+"F3.wireOp",EDGE,"E28");var subQ1=sQuery(id+"F0.wireOp",EDGE,"E0.top");var subQ2=sQuery(id+"F3.wireOp",EDGE,"E29");var subQ3=sQuery(id+"F0.wireOp",EDGE,"E0.bottom");Q21=makeQuery(id+"F4.boolean.opBoolean","SPLIT",EDGE,{"disambiguationData":[TD([makeQuery(id+"F1.opExtrude","CAP_FACE",FACE,{"disambiguationData":[OSD([subQ3,subQ1,sQuery(id+"F0.wireOp",EDGE,"E0.left"),sQuery(id+"F0.wireOp",EDGE,"E0.right")])],"isStart":false}),makeQuery(id+"F1.opExtrude","SWEPT_FACE",FACE,{"disambiguationData":[OSD([subQ1])]}),makeQuery(id+"F4.opExtrude","SWEPT_FACE",FACE,{"disambiguationData":[OSD([subQ0])]}),makeQuery(id+"F4.opExtrude","CAP_FACE",FACE,{"disambiguationData":[OSD([subQ3,sQuery(id+"F2.wireOp",EDGE,"fcba4419-a2ee-464f-be9d-58f11bf3418b.sketch_text.stroke-0"),sQuery(id+"F2.wireOp",EDGE,"fcba4419-a2ee-464f-be9d-58f11bf3418b.sketch_text.stroke-1"),sQuery(id+"F2.wireOp",EDGE,"fcba4419-a2ee-464f-be9d-58f11bf3418b.sketch_text.stroke-2"),sQuery(id+"F2.wireOp",EDGE,"fcba4419-a2ee-464f-be9d-58f11bf3418b.sketch_text.stroke-3"),sQuery(id+"F2.wireOp",EDGE,"fcba4419-a2ee-464f-be9d-58f11bf3418b.sketch_text.stroke-4"),sQuery(id+"F2.wireOp",EDGE,"fcba4419-a2ee-464f-be9d-58f11bf3418b.sketch_text.stroke-5"),sQuery(id+"F2.wireOp",EDGE,"fcba4419-a2ee-464f-be9d-58f11bf3418b.sketch_text.stroke-6"),sQuery(id+"F2.wireOp",EDGE,"fcba4419-a2ee-464f-be9d-58f11bf3418b.sketch_text.stroke-7"),sQuery(id+"F2.wireOp",EDGE,"fcba4419-a2ee-464f-be9d-58f11bf3418b.sketch_text.stroke-8"),sQuery(id+"F2.wireOp",EDGE,"fcba4419-a2ee-464f-be9d-58f11bf3418b.sketch_text.stroke-9"),sQuery(id+"F2.wireOp",EDGE,"fcba4419-a2ee-464f-be9d-58f11bf3418b.sketch_text.stroke-10"),sQuery(id+"F2.wireOp",EDGE,"fcba4419-a2ee-464f-be9d-58f11bf3418b.sketch_text.stroke-11"),sQuery(id+"F2.wireOp",EDGE,"fcba4419-a2ee-464f-be9d-58f11bf3418b.sketch_text.stroke-12"),sQuery(id+"F2.wireOp",EDGE,"fcba4419-a2ee-464f-be9d-58f11bf3418b.sketch_text.stroke-13"),sQuery(id+"F2.wireOp",EDGE,"fcba4419-a2ee-464f-be9d-58f11bf3418b.sketch_text.stroke-14"),sQuery(id+"F2.wireOp",EDGE,"fcba4419-a2ee-464f-be9d-58f11bf3418b.sketch_text.stroke-15"),sQuery(id+"F2.wireOp",EDGE,"fcba4419-a2ee-464f-be9d-58f11bf3418b.sketch_text.stroke-16"),sQuery(id+"F2.wireOp",EDGE,"fcba4419-a2ee-464f-be9d-58f11bf3418b.sketch_text.stroke-17"),sQuery(id+"F2.wireOp",EDGE,"fcba4419-a2ee-464f-be9d-58f11bf3418b.sketch_text.stroke-18"),sQuery(id+"F2.wireOp",EDGE,"fcba4419-a2ee-464f-be9d-58f11bf3418b.sketch_text.stroke-19"),sQuery(id+"F2.wireOp",EDGE,"fcba4419-a2ee-464f-be9d-58f11bf3418b.sketch_text.stroke-20"),sQuery(id+"F2.wireOp",EDGE,"fcba4419-a2ee-464f-be9d-58f11bf3418b.sketch_text.stroke-21"),sQuery(id+"F2.wireOp",EDGE,"fcba4419-a2ee-464f-be9d-58f11bf3418b.sketch_text.stroke-22"),sQuery(id+"F2.wireOp",EDGE,"fcba4419-a2ee-464f-be9d-58f11bf3418b.sketch_text.stroke-23"),sQuery(id+"F2.wireOp",EDGE,"fcba4419-a2ee-464f-be9d-58f11bf3418b.sketch_text.stroke-24"),sQuery(id+"F2.wireOp",EDGE,"fcba4419-a2ee-464f-be9d-58f11bf3418b.sketch_text.stroke-25"),sQuery(id+"F2.wireOp",EDGE,"fcba4419-a2ee-464f-be9d-58f11bf3418b.sketch_text.stroke-26"),sQuery(id+"F2.wireOp",EDGE,"fcba4419-a2ee-464f-be9d-58f11bf3418b.sketch_text.stroke-27"),sQuery(id+"F2.wireOp",EDGE,"fcba4419-a2ee-464f-be9d-58f11bf3418b.sketch_text.stroke-28"),sQuery(id+"F2.wireOp",EDGE,"fcba4419-a2ee-464f-be9d-58f11bf3418b.sketch_text.stroke-29"),sQuery(id+"F2.wireOp",EDGE,"fcba4419-a2ee-464f-be9d-58f11bf3418b.sketch_text.stroke-30"),sQuery(id+"F2.wireOp",EDGE,"fcba4419-a2ee-464f-be9d-58f11bf3418b.sketch_text.stroke-31"),sQuery(id+"F2.wireOp",EDGE,"fcba4419-a2ee-464f-be9d-58f11bf3418b.sketch_text.stroke-32"),sQuery(id+"F2.wireOp",EDGE,"fcba4419-a2ee-464f-be9d-58f11bf3418b.sketch_text.stroke-33"),sQuery(id+"F2.wireOp",EDGE,"fcba4419-a2ee-464f-be9d-58f11bf3418b.sketch_text.stroke-34"),sQuery(id+"F2.wireOp",EDGE,"fcba4419-a2ee-464f-be9d-58f11bf3418b.sketch_text.stroke-35"),sQuery(id+"F2.wireOp",EDGE,"fcba4419-a2ee-464f-be9d-58f11bf3418b.sketch_text.stroke-36"),sQuery(id+"F2.wireOp",EDGE,"fcba4419-a2ee-464f-be9d-58f11bf3418b.sketch_text.stroke-37"),sQuery(id+"F2.wireOp",EDGE,"fcba4419-a2ee-464f-be9d-58f11bf3418b.sketch_text.stroke-38"),sQuery(id+"F2.wireOp",EDGE,"fcba4419-a2ee-464f-be9d-58f11bf3418b.sketch_text.stroke-39"),sQuery(id+"F2.wireOp",EDGE,"fcba4419-a2ee-464f-be9d-58f11bf3418b.sketch_text.stroke-40"),sQuery(id+"F2.wireOp",EDGE,"fcba4419-a2ee-464f-be9d-58f11bf3418b.sketch_text.stroke-41"),sQuery(id+"F2.wireOp",EDGE,"fcba4419-a2ee-464f-be9d-58f11bf3418b.sketch_text.stroke-42"),sQuery(id+"F2.wireOp",EDGE,"fcba4419-a2ee-464f-be9d-58f11bf3418b.sketch_text.stroke-43"),sQuery(id+"F2.wireOp",EDGE,"fcba4419-a2ee-464f-be9d-58f11bf3418b.sketch_text.stroke-44"),sQuery(id+"F2.wireOp",EDGE,"fcba4419-a2ee-464f-be9d-58f11bf3418b.sketch_text.stroke-45"),sQuery(id+"F2.wireOp",EDGE,"fcba4419-a2ee-464f-be9d-58f11bf3418b.sketch_text.stroke-46"),sQuery(id+"F2.wireOp",EDGE,"fcba4419-a2ee-464f-be9d-58f11bf3418b.sketch_text.stroke-47"),sQuery(id+"F2.wireOp",EDGE,"fcba4419-a2ee-464f-be9d-58f11bf3418b.sketch_text.stroke-48"),sQuery(id+"F2.wireOp",EDGE,"fcba4419-a2ee-464f-be9d-58f11bf3418b.sketch_text.stroke-49"),sQuery(id+"F2.wireOp",EDGE,"fcba4419-a2ee-464f-be9d-58f11bf3418b.sketch_text.stroke-50"),sQuery(id+"F2.wireOp",EDGE,"fcba4419-a2ee-464f-be9d-58f11bf3418b.sketch_text.stroke-51"),sQuery(id+"F2.wireOp",EDGE,"fcba4419-a2ee-464f-be9d-58f11bf3418b.sketch_text.stroke-52"),sQuery(id+"F2.wireOp",EDGE,"fcba4419-a2ee-464f-be9d-58f11bf3418b.sketch_text.stroke-53"),sQuery(id+"F2.wireOp",EDGE,"fcba4419-a2ee-464f-be9d-58f11bf3418b.sketch_text.stroke-54"),sQuery(id+"F2.wireOp",EDGE,"fcba4419-a2ee-464f-be9d-58f11bf3418b.sketch_text.stroke-55"),sQuery(id+"F2.wireOp",EDGE,"fcba4419-a2ee-464f-be9d-58f11bf3418b.sketch_text.stroke-56"),sQuery(id+"F2.wireOp",EDGE,"fcba4419-a2ee-464f-be9d-58f11bf3418b.sketch_text.stroke-57"),sQuery(id+"F2.wireOp",EDGE,"fcba4419-a2ee-464f-be9d-58f11bf3418b.sketch_text.stroke-58"),sQuery(id+"F2.wireOp",EDGE,"fcba4419-a2ee-464f-be9d-58f11bf3418b.sketch_text.stroke-59"),sQuery(id+"F2.wireOp",EDGE,"fcba4419-a2ee-464f-be9d-58f11bf3418b.sketch_text.stroke-60"),sQuery(id+"F2.wireOp",EDGE,"fcba4419-a2ee-464f-be9d-58f11bf3418b.sketch_text.stroke-61"),sQuery(id+"F2.wireOp",EDGE,"fcba4419-a2ee-464f-be9d-58f11bf3418b.sketch_text.stroke-62"),sQuery(id+"F2.wireOp",EDGE,"fcba4419-a2ee-464f-be9d-58f11bf3418b.sketch_text.stroke-63"),sQuery(id+"F2.wireOp",EDGE,"fcba4419-a2ee-464f-be9d-58f11bf3418b.sketch_text.stroke-64"),sQuery(id+"F2.wireOp",EDGE,"fcba4419-a2ee-464f-be9d-58f11bf3418b.sketch_text.stroke-65"),sQuery(id+"F2.wireOp",EDGE,"fcba4419-a2ee-464f-be9d-58f11bf3418b.sketch_text.stroke-66"),sQuery(id+"F2.wireOp",EDGE,"fcba4419-a2ee-464f-be9d-58f11bf3418b.sketch_text.stroke-67"),sQuery(id+"F2.wireOp",EDGE,"fcba4419-a2ee-464f-be9d-58f11bf3418b.sketch_text.stroke-68"),sQuery(id+"F2.wireOp",EDGE,"fcba4419-a2ee-464f-be9d-58f11bf3418b.sketch_text.stroke-69"),sQuery(id+"F2.wireOp",EDGE,"fcba4419-a2ee-464f-be9d-58f11bf3418b.sketch_text.stroke-70"),sQuery(id+"F2.wireOp",EDGE,"fcba4419-a2ee-464f-be9d-58f11bf3418b.sketch_text.stroke-71"),sQuery(id+"F2.wireOp",EDGE,"fcba4419-a2ee-464f-be9d-58f11bf3418b.sketch_text.stroke-72"),sQuery(id+"F2.wireOp",EDGE,"fcba4419-a2ee-464f-be9d-58f11bf3418b.sketch_text.stroke-73"),sQuery(id+"F2.wireOp",EDGE,"fcba4419-a2ee-464f-be9d-58f11bf3418b.sketch_text.stroke-74"),sQuery(id+"F2.wireOp",EDGE,"fcba4419-a2ee-464f-be9d-58f11bf3418b.sketch_text.stroke-75"),sQuery(id+"F2.wireOp",EDGE,"fcba4419-a2ee-464f-be9d-58f11bf3418b.sketch_text.stroke-76"),sQuery(id+"F2.wireOp",EDGE,"fcba4419-a2ee-464f-be9d-58f11bf3418b.sketch_text.stroke-77"),sQuery(id+"F2.wireOp",EDGE,"fcba4419-a2ee-464f-be9d-58f11bf3418b.sketch_text.stroke-78"),sQuery(id+"F2.wireOp",EDGE,"fcba4419-a2ee-464f-be9d-58f11bf3418b.sketch_text.stroke-79"),sQuery(id+"F2.wireOp",EDGE,"fcba4419-a2ee-464f-be9d-58f11bf3418b.sketch_text.stroke-80"),sQuery(id+"F2.wireOp",EDGE,"fcba4419-a2ee-464f-be9d-58f11bf3418b.sketch_text.stroke-81"),sQuery(id+"F2.wireOp",EDGE,"fcba4419-a2ee-464f-be9d-58f11bf3418b.sketch_text.stroke-82"),sQuery(id+"F2.wireOp",EDGE,"fcba4419-a2ee-464f-be9d-58f11bf3418b.sketch_text.stroke-83"),sQuery(id+"F2.wireOp",EDGE,"fcba4419-a2ee-464f-be9d-58f11bf3418b.sketch_text.stroke-84"),sQuery(id+"F2.wireOp",EDGE,"fcba4419-a2ee-464f-be9d-58f11bf3418b.sketch_text.stroke-85"),sQuery(id+"F2.wireOp",EDGE,"fcba4419-a2ee-464f-be9d-58f11bf3418b.sketch_text.stroke-86"),sQuery(id+"F2.wireOp",EDGE,"fcba4419-a2ee-464f-be9d-58f11bf3418b.sketch_text.stroke-87"),sQuery(id+"F2.wireOp",EDGE,"fcba4419-a2ee-464f-be9d-58f11bf3418b.sketch_text.stroke-88"),sQuery(id+"F2.wireOp",EDGE,"fcba4419-a2ee-464f-be9d-58f11bf3418b.sketch_text.stroke-89"),sQuery(id+"F2.wireOp",EDGE,"fcba4419-a2ee-464f-be9d-58f11bf3418b.sketch_text.stroke-90"),sQuery(id+"F2.wireOp",EDGE,"fcba4419-a2ee-464f-be9d-58f11bf3418b.sketch_text.stroke-91"),sQuery(id+"F2.wireOp",EDGE,"fcba4419-a2ee-464f-be9d-58f11bf3418b.sketch_text.stroke-92"),sQuery(id+"F2.wireOp",EDGE,"fcba4419-a2ee-464f-be9d-58f11bf3418b.sketch_text.stroke-93"),sQuery(id+"F2.wireOp",EDGE,"fcba4419-a2ee-464f-be9d-58f11bf3418b.sketch_text.stroke-94"),sQuery(id+"F2.wireOp",EDGE,"fcba4419-a2ee-464f-be9d-58f11bf3418b.sketch_text.stroke-95"),sQuery(id+"F2.wireOp",EDGE,"fcba4419-a2ee-464f-be9d-58f11bf3418b.sketch_text.stroke-96"),sQuery(id+"F2.wireOp",EDGE,"fcba4419-a2ee-464f-be9d-58f11bf3418b.sketch_text.stroke-97"),sQuery(id+"F2.wireOp",EDGE,"fcba4419-a2ee-464f-be9d-58f11bf3418b.sketch_text.stroke-98"),sQuery(id+"F2.wireOp",EDGE,"fcba4419-a2ee-464f-be9d-58f11bf3418b.sketch_text.stroke-99"),sQuery(id+"F2.wireOp",EDGE,"fcba4419-a2ee-464f-be9d-58f11bf3418b.sketch_text.stroke-100"),sQuery(id+"F2.wireOp",EDGE,"fcba4419-a2ee-464f-be9d-58f11bf3418b.sketch_text.stroke-101"),sQuery(id+"F2.wireOp",EDGE,"fcba4419-a2ee-464f-be9d-58f11bf3418b.sketch_text.stroke-102"),sQuery(id+"F2.wireOp",EDGE,"fcba4419-a2ee-464f-be9d-58f11bf3418b.sketch_text.stroke-103"),sQuery(id+"F2.wireOp",EDGE,"fcba4419-a2ee-464f-be9d-58f11bf3418b.sketch_text.stroke-104"),sQuery(id+"F2.wireOp",EDGE,"fcba4419-a2ee-464f-be9d-58f11bf3418b.sketch_text.stroke-105"),sQuery(id+"F2.wireOp",EDGE,"fcba4419-a2ee-464f-be9d-58f11bf3418b.sketch_text.stroke-106"),sQuery(id+"F2.wireOp",EDGE,"fcba4419-a2ee-464f-be9d-58f11bf3418b.sketch_text.stroke-107"),sQuery(id+"F2.wireOp",EDGE,"fcba4419-a2ee-464f-be9d-58f11bf3418b.sketch_text.stroke-108"),sQuery(id+"F2.wireOp",EDGE,"fcba4419-a2ee-464f-be9d-58f11bf3418b.sketch_text.stroke-109"),sQuery(id+"F2.wireOp",EDGE,"fcba4419-a2ee-464f-be9d-58f11bf3418b.sketch_text.stroke-110"),sQuery(id+"F2.wireOp",EDGE,"fcba4419-a2ee-464f-be9d-58f11bf3418b.sketch_text.stroke-111"),sQuery(id+"F2.wireOp",EDGE,"fcba4419-a2ee-464f-be9d-58f11bf3418b.sketch_text.stroke-112"),sQuery(id+"F2.wireOp",EDGE,"fcba4419-a2ee-464f-be9d-58f11bf3418b.sketch_text.stroke-113"),sQuery(id+"F2.wireOp",EDGE,"fcba4419-a2ee-464f-be9d-58f11bf3418b.sketch_text.stroke-114"),sQuery(id+"F2.wireOp",EDGE,"fcba4419-a2ee-464f-be9d-58f11bf3418b.sketch_text.stroke-115"),sQuery(id+"F2.wireOp",EDGE,"fcba4419-a2ee-464f-be9d-58f11bf3418b.sketch_text.stroke-116"),sQuery(id+"F2.wireOp",EDGE,"fcba4419-a2ee-464f-be9d-58f11bf3418b.sketch_text.stroke-117"),sQuery(id+"F2.wireOp",EDGE,"fcba4419-a2ee-464f-be9d-58f11bf3418b.sketch_text.stroke-118"),sQuery(id+"F2.wireOp",EDGE,"fcba4419-a2ee-464f-be9d-58f11bf3418b.sketch_text.stroke-119"),sQuery(id+"F2.wireOp",EDGE,"fcba4419-a2ee-464f-be9d-58f11bf3418b.sketch_text.stroke-120"),sQuery(id+"F2.wireOp",EDGE,"fcba4419-a2ee-464f-be9d-58f11bf3418b.sketch_text.stroke-121"),sQuery(id+"F2.wireOp",EDGE,"fcba4419-a2ee-464f-be9d-58f11bf3418b.sketch_text.stroke-122"),sQuery(id+"F2.wireOp",EDGE,"fcba4419-a2ee-464f-be9d-58f11bf3418b.sketch_text.stroke-123"),sQuery(id+"F2.wireOp",EDGE,"fcba4419-a2ee-464f-be9d-58f11bf3418b.sketch_text.stroke-124"),sQuery(id+"F2.wireOp",EDGE,"fcba4419-a2ee-464f-be9d-58f11bf3418b.sketch_text.stroke-125"),sQuery(id+"F2.wireOp",EDGE,"fcba4419-a2ee-464f-be9d-58f11bf3418b.sketch_text.stroke-126"),sQuery(id+"F2.wireOp",EDGE,"fcba4419-a2ee-464f-be9d-58f11bf3418b.sketch_text.stroke-127"),sQuery(id+"F2.wireOp",EDGE,"fcba4419-a2ee-464f-be9d-58f11bf3418b.sketch_text.stroke-128"),sQuery(id+"F2.wireOp",EDGE,"fcba4419-a2ee-464f-be9d-58f11bf3418b.sketch_text.stroke-129"),sQuery(id+"F2.wireOp",EDGE,"fcba4419-a2ee-464f-be9d-58f11bf3418b.sketch_text.stroke-130"),sQuery(id+"F2.wireOp",EDGE,"fcba4419-a2ee-464f-be9d-58f11bf3418b.sketch_text.stroke-131"),sQuery(id+"F2.wireOp",EDGE,"fcba4419-a2ee-464f-be9d-58f11bf3418b.sketch_text.stroke-132"),sQuery(id+"F2.wireOp",EDGE,"fcba4419-a2ee-464f-be9d-58f11bf3418b.sketch_text.stroke-133"),sQuery(id+"F2.wireOp",EDGE,"fcba4419-a2ee-464f-be9d-58f11bf3418b.sketch_text.stroke-134"),sQuery(id+"F2.wireOp",EDGE,"fcba4419-a2ee-464f-be9d-58f11bf3418b.sketch_text.stroke-135"),sQuery(id+"F2.wireOp",EDGE,"fcba4419-a2ee-464f-be9d-58f11bf3418b.sketch_text.stroke-136"),sQuery(id+"F2.wireOp",EDGE,"fcba4419-a2ee-464f-be9d-58f11bf3418b.sketch_text.stroke-137"),sQuery(id+"F2.wireOp",EDGE,"fcba4419-a2ee-464f-be9d-58f11bf3418b.sketch_text.stroke-138"),sQuery(id+"F2.wireOp",EDGE,"fcba4419-a2ee-464f-be9d-58f11bf3418b.sketch_text.stroke-139"),sQuery(id+"F2.wireOp",EDGE,"fcba4419-a2ee-464f-be9d-58f11bf3418b.sketch_text.stroke-140"),sQuery(id+"F2.wireOp",EDGE,"fcba4419-a2ee-464f-be9d-58f11bf3418b.sketch_text.stroke-141"),sQuery(id+"F2.wireOp",EDGE,"fcba4419-a2ee-464f-be9d-58f11bf3418b.sketch_text.stroke-142"),sQuery(id+"F2.wireOp",EDGE,"fcba4419-a2ee-464f-be9d-58f11bf3418b.sketch_text.stroke-143"),sQuery(id+"F2.wireOp",EDGE,"fcba4419-a2ee-464f-be9d-58f11bf3418b.sketch_text.stroke-144"),sQuery(id+"F2.wireOp",EDGE,"fcba4419-a2ee-464f-be9d-58f11bf3418b.sketch_text.stroke-145"),sQuery(id+"F2.wireOp",EDGE,"fcba4419-a2ee-464f-be9d-58f11bf3418b.sketch_text.stroke-146"),sQuery(id+"F2.wireOp",EDGE,"fcba4419-a2ee-464f-be9d-58f11bf3418b.sketch_text.stroke-147"),sQuery(id+"F2.wireOp",EDGE,"fcba4419-a2ee-464f-be9d-58f11bf3418b.sketch_text.stroke-148"),sQuery(id+"F2.wireOp",EDGE,"fcba4419-a2ee-464f-be9d-58f11bf3418b.sketch_text.stroke-149"),sQuery(id+"F2.wireOp",EDGE,"fcba4419-a2ee-464f-be9d-58f11bf3418b.sketch_text.stroke-150"),sQuery(id+"F2.wireOp",EDGE,"fcba4419-a2ee-464f-be9d-58f11bf3418b.sketch_text.stroke-151"),sQuery(id+"F2.wireOp",EDGE,"fcba4419-a2ee-464f-be9d-58f11bf3418b.sketch_text.stroke-152"),sQuery(id+"F2.wireOp",EDGE,"fcba4419-a2ee-464f-be9d-58f11bf3418b.sketch_text.stroke-153"),sQuery(id+"F2.wireOp",EDGE,"fcba4419-a2ee-464f-be9d-58f11bf3418b.sketch_text.stroke-154"),sQuery(id+"F2.wireOp",EDGE,"fcba4419-a2ee-464f-be9d-58f11bf3418b.sketch_text.stroke-155"),sQuery(id+"F2.wireOp",EDGE,"fcba4419-a2ee-464f-be9d-58f11bf3418b.sketch_text.stroke-156"),sQuery(id+"F2.wireOp",EDGE,"fcba4419-a2ee-464f-be9d-58f11bf3418b.sketch_text.stroke-157"),sQuery(id+"F2.wireOp",EDGE,"fcba4419-a2ee-464f-be9d-58f11bf3418b.sketch_text.stroke-158"),sQuery(id+"F2.wireOp",EDGE,"fcba4419-a2ee-464f-be9d-58f11bf3418b.sketch_text.stroke-159"),sQuery(id+"F2.wireOp",EDGE,"fcba4419-a2ee-464f-be9d-58f11bf3418b.sketch_text.stroke-160"),sQuery(id+"F2.wireOp",EDGE,"fcba4419-a2ee-464f-be9d-58f11bf3418b.sketch_text.stroke-161"),sQuery(id+"F2.wireOp",EDGE,"fcba4419-a2ee-464f-be9d-58f11bf3418b.sketch_text.stroke-162"),sQuery(id+"F2.wireOp",EDGE,"fcba4419-a2ee-464f-be9d-58f11bf3418b.sketch_text.stroke-163"),sQuery(id+"F2.wireOp",EDGE,"fcba4419-a2ee-464f-be9d-58f11bf3418b.sketch_text.stroke-164"),sQuery(id+"F2.wireOp",EDGE,"fcba4419-a2ee-464f-be9d-58f11bf3418b.sketch_text.stroke-165"),sQuery(id+"F2.wireOp",EDGE,"fcba4419-a2ee-464f-be9d-58f11bf3418b.sketch_text.stroke-166"),sQuery(id+"F2.wireOp",EDGE,"fcba4419-a2ee-464f-be9d-58f11bf3418b.sketch_text.stroke-167"),sQuery(id+"F2.wireOp",EDGE,"fcba4419-a2ee-464f-be9d-58f11bf3418b.sketch_text.stroke-168"),sQuery(id+"F2.wireOp",EDGE,"fcba4419-a2ee-464f-be9d-58f11bf3418b.sketch_text.stroke-169"),sQuery(id+"F2.wireOp",EDGE,"fcba4419-a2ee-464f-be9d-58f11bf3418b.sketch_text.stroke-170"),sQuery(id+"F2.wireOp",EDGE,"fcba4419-a2ee-464f-be9d-58f11bf3418b.sketch_text.stroke-171"),sQuery(id+"F2.wireOp",EDGE,"fcba4419-a2ee-464f-be9d-58f11bf3418b.sketch_text.stroke-172"),sQuery(id+"F2.wireOp",EDGE,"fcba4419-a2ee-464f-be9d-58f11bf3418b.sketch_text.stroke-173"),sQuery(id+"FHMxAyK4CFUKdhS_1.wireOp",EDGE,"1cb9c079-ea9b-4899-8069-e0e3048e911d.sketch_text.stroke-0"),sQuery(id+"FHMxAyK4CFUKdhS_1.wireOp",EDGE,"1cb9c079-ea9b-4899-8069-e0e3048e911d.sketch_text.stroke-1"),sQuery(id+"FHMxAyK4CFUKdhS_1.wireOp",EDGE,"1cb9c079-ea9b-4899-8069-e0e3048e911d.sketch_text.stroke-2"),sQuery(id+"FHMxAyK4CFUKdhS_1.wireOp",EDGE,"1cb9c079-ea9b-4899-8069-e0e3048e911d.sketch_text.stroke-3"),sQuery(id+"FHMxAyK4CFUKdhS_1.wireOp",EDGE,"1cb9c079-ea9b-4899-8069-e0e3048e911d.sketch_text.stroke-4"),sQuery(id+"FHMxAyK4CFUKdhS_1.wireOp",EDGE,"1cb9c079-ea9b-4899-8069-e0e3048e911d.sketch_text.stroke-5"),sQuery(id+"FHMxAyK4CFUKdhS_1.wireOp",EDGE,"1cb9c079-ea9b-4899-8069-e0e3048e911d.sketch_text.stroke-6"),sQuery(id+"FHMxAyK4CFUKdhS_1.wireOp",EDGE,"1cb9c079-ea9b-4899-8069-e0e3048e911d.sketch_text.stroke-7"),sQuery(id+"FHMxAyK4CFUKdhS_1.wireOp",EDGE,"1cb9c079-ea9b-4899-8069-e0e3048e911d.sketch_text.stroke-8"),sQuery(id+"FHMxAyK4CFUKdhS_1.wireOp",EDGE,"1cb9c079-ea9b-4899-8069-e0e3048e911d.sketch_text.stroke-9"),sQuery(id+"FHMxAyK4CFUKdhS_1.wireOp",EDGE,"1cb9c079-ea9b-4899-8069-e0e3048e911d.sketch_text.stroke-10"),sQuery(id+"FHMxAyK4CFUKdhS_1.wireOp",EDGE,"1cb9c079-ea9b-4899-8069-e0e3048e911d.sketch_text.stroke-11"),sQuery(id+"FHMxAyK4CFUKdhS_1.wireOp",EDGE,"1cb9c079-ea9b-4899-8069-e0e3048e911d.sketch_text.stroke-12"),sQuery(id+"FHMxAyK4CFUKdhS_1.wireOp",EDGE,"1cb9c079-ea9b-4899-8069-e0e3048e911d.sketch_text.stroke-13"),sQuery(id+"FHMxAyK4CFUKdhS_1.wireOp",EDGE,"1cb9c079-ea9b-4899-8069-e0e3048e911d.sketch_text.stroke-14"),sQuery(id+"FHMxAyK4CFUKdhS_1.wireOp",EDGE,"1cb9c079-ea9b-4899-8069-e0e3048e911d.sketch_text.stroke-15"),sQuery(id+"FHMxAyK4CFUKdhS_1.wireOp",EDGE,"1cb9c079-ea9b-4899-8069-e0e3048e911d.sketch_text.stroke-16"),sQuery(id+"FHMxAyK4CFUKdhS_1.wireOp",EDGE,"1cb9c079-ea9b-4899-8069-e0e3048e911d.sketch_text.stroke-17"),sQuery(id+"FHMxAyK4CFUKdhS_1.wireOp",EDGE,"1cb9c079-ea9b-4899-8069-e0e3048e911d.sketch_text.stroke-18"),sQuery(id+"FHMxAyK4CFUKdhS_1.wireOp",EDGE,"1cb9c079-ea9b-4899-8069-e0e3048e911d.sketch_text.stroke-19"),sQuery(id+"FHMxAyK4CFUKdhS_1.wireOp",EDGE,"1cb9c079-ea9b-4899-8069-e0e3048e911d.sketch_text.stroke-20"),sQuery(id+"FHMxAyK4CFUKdhS_1.wireOp",EDGE,"1cb9c079-ea9b-4899-8069-e0e3048e911d.sketch_text.stroke-21"),sQuery(id+"FHMxAyK4CFUKdhS_1.wireOp",EDGE,"1cb9c079-ea9b-4899-8069-e0e3048e911d.sketch_text.stroke-22"),sQuery(id+"FHMxAyK4CFUKdhS_1.wireOp",EDGE,"1cb9c079-ea9b-4899-8069-e0e3048e911d.sketch_text.stroke-23"),sQuery(id+"FHMxAyK4CFUKdhS_1.wireOp",EDGE,"1cb9c079-ea9b-4899-8069-e0e3048e911d.sketch_text.stroke-24"),sQuery(id+"FHMxAyK4CFUKdhS_1.wireOp",EDGE,"1cb9c079-ea9b-4899-8069-e0e3048e911d.sketch_text.stroke-25"),sQuery(id+"FHMxAyK4CFUKdhS_1.wireOp",EDGE,"1cb9c079-ea9b-4899-8069-e0e3048e911d.sketch_text.stroke-26"),sQuery(id+"FHMxAyK4CFUKdhS_1.wireOp",EDGE,"1cb9c079-ea9b-4899-8069-e0e3048e911d.sketch_text.stroke-27"),sQuery(id+"FHMxAyK4CFUKdhS_1.wireOp",EDGE,"1cb9c079-ea9b-4899-8069-e0e3048e911d.sketch_text.stroke-28"),sQuery(id+"FHMxAyK4CFUKdhS_1.wireOp",EDGE,"1cb9c079-ea9b-4899-8069-e0e3048e911d.sketch_text.stroke-29"),sQuery(id+"FHMxAyK4CFUKdhS_1.wireOp",EDGE,"1cb9c079-ea9b-4899-8069-e0e3048e911d.sketch_text.stroke-30"),sQuery(id+"FHMxAyK4CFUKdhS_1.wireOp",EDGE,"1cb9c079-ea9b-4899-8069-e0e3048e911d.sketch_text.stroke-31"),sQuery(id+"FHMxAyK4CFUKdhS_1.wireOp",EDGE,"1cb9c079-ea9b-4899-8069-e0e3048e911d.sketch_text.stroke-32"),sQuery(id+"FHMxAyK4CFUKdhS_1.wireOp",EDGE,"1cb9c079-ea9b-4899-8069-e0e3048e911d.sketch_text.stroke-33"),sQuery(id+"FHMxAyK4CFUKdhS_1.wireOp",EDGE,"1cb9c079-ea9b-4899-8069-e0e3048e911d.sketch_text.stroke-34"),sQuery(id+"FHMxAyK4CFUKdhS_1.wireOp",EDGE,"1cb9c079-ea9b-4899-8069-e0e3048e911d.sketch_text.stroke-35"),sQuery(id+"FHMxAyK4CFUKdhS_1.wireOp",EDGE,"1cb9c079-ea9b-4899-8069-e0e3048e911d.sketch_text.stroke-36"),sQuery(id+"FHMxAyK4CFUKdhS_1.wireOp",EDGE,"1cb9c079-ea9b-4899-8069-e0e3048e911d.sketch_text.stroke-37"),sQuery(id+"FHMxAyK4CFUKdhS_1.wireOp",EDGE,"1cb9c079-ea9b-4899-8069-e0e3048e911d.sketch_text.stroke-38"),sQuery(id+"FHMxAyK4CFUKdhS_1.wireOp",EDGE,"1cb9c079-ea9b-4899-8069-e0e3048e911d.sketch_text.stroke-39"),sQuery(id+"FHMxAyK4CFUKdhS_1.wireOp",EDGE,"1cb9c079-ea9b-4899-8069-e0e3048e911d.sketch_text.stroke-40"),sQuery(id+"FHMxAyK4CFUKdhS_1.wireOp",EDGE,"1cb9c079-ea9b-4899-8069-e0e3048e911d.sketch_text.stroke-41"),sQuery(id+"FHMxAyK4CFUKdhS_1.wireOp",EDGE,"1cb9c079-ea9b-4899-8069-e0e3048e911d.sketch_text.stroke-42"),sQuery(id+"FHMxAyK4CFUKdhS_1.wireOp",EDGE,"1cb9c079-ea9b-4899-8069-e0e3048e911d.sketch_text.stroke-43"),sQuery(id+"FHMxAyK4CFUKdhS_1.wireOp",EDGE,"1cb9c079-ea9b-4899-8069-e0e3048e911d.sketch_text.stroke-44"),sQuery(id+"FHMxAyK4CFUKdhS_1.wireOp",EDGE,"1cb9c079-ea9b-4899-8069-e0e3048e911d.sketch_text.stroke-45"),sQuery(id+"FHMxAyK4CFUKdhS_1.wireOp",EDGE,"1cb9c079-ea9b-4899-8069-e0e3048e911d.sketch_text.stroke-46"),sQuery(id+"FHMxAyK4CFUKdhS_1.wireOp",EDGE,"1cb9c079-ea9b-4899-8069-e0e3048e911d.sketch_text.stroke-47"),sQuery(id+"FHMxAyK4CFUKdhS_1.wireOp",EDGE,"1cb9c079-ea9b-4899-8069-e0e3048e911d.sketch_text.stroke-48"),sQuery(id+"FHMxAyK4CFUKdhS_1.wireOp",EDGE,"1cb9c079-ea9b-4899-8069-e0e3048e911d.sketch_text.stroke-49"),sQuery(id+"FHMxAyK4CFUKdhS_1.wireOp",EDGE,"1cb9c079-ea9b-4899-8069-e0e3048e911d.sketch_text.stroke-50"),sQuery(id+"FHMxAyK4CFUKdhS_1.wireOp",EDGE,"1cb9c079-ea9b-4899-8069-e0e3048e911d.sketch_text.stroke-51"),sQuery(id+"FHMxAyK4CFUKdhS_1.wireOp",EDGE,"1cb9c079-ea9b-4899-8069-e0e3048e911d.sketch_text.stroke-52"),sQuery(id+"FHMxAyK4CFUKdhS_1.wireOp",EDGE,"1cb9c079-ea9b-4899-8069-e0e3048e911d.sketch_text.stroke-53"),sQuery(id+"FHMxAyK4CFUKdhS_1.wireOp",EDGE,"1cb9c079-ea9b-4899-8069-e0e3048e911d.sketch_text.stroke-54"),sQuery(id+"FHMxAyK4CFUKdhS_1.wireOp",EDGE,"1cb9c079-ea9b-4899-8069-e0e3048e911d.sketch_text.stroke-55"),sQuery(id+"FHMxAyK4CFUKdhS_1.wireOp",EDGE,"1cb9c079-ea9b-4899-8069-e0e3048e911d.sketch_text.stroke-56"),sQuery(id+"FHMxAyK4CFUKdhS_1.wireOp",EDGE,"1cb9c079-ea9b-4899-8069-e0e3048e911d.sketch_text.stroke-57"),sQuery(id+"FHMxAyK4CFUKdhS_1.wireOp",EDGE,"1cb9c079-ea9b-4899-8069-e0e3048e911d.sketch_text.stroke-58"),sQuery(id+"FHMxAyK4CFUKdhS_1.wireOp",EDGE,"1cb9c079-ea9b-4899-8069-e0e3048e911d.sketch_text.stroke-59"),sQuery(id+"FHMxAyK4CFUKdhS_1.wireOp",EDGE,"1cb9c079-ea9b-4899-8069-e0e3048e911d.sketch_text.stroke-60"),sQuery(id+"FHMxAyK4CFUKdhS_1.wireOp",EDGE,"1cb9c079-ea9b-4899-8069-e0e3048e911d.sketch_text.stroke-61"),sQuery(id+"FHMxAyK4CFUKdhS_1.wireOp",EDGE,"1cb9c079-ea9b-4899-8069-e0e3048e911d.sketch_text.stroke-62"),sQuery(id+"FHMxAyK4CFUKdhS_1.wireOp",EDGE,"1cb9c079-ea9b-4899-8069-e0e3048e911d.sketch_text.stroke-71"),sQuery(id+"FHMxAyK4CFUKdhS_1.wireOp",EDGE,"1cb9c079-ea9b-4899-8069-e0e3048e911d.sketch_text.stroke-72"),sQuery(id+"FHMxAyK4CFUKdhS_1.wireOp",EDGE,"1cb9c079-ea9b-4899-8069-e0e3048e911d.sketch_text.stroke-73"),sQuery(id+"FHMxAyK4CFUKdhS_1.wireOp",EDGE,"1cb9c079-ea9b-4899-8069-e0e3048e911d.sketch_text.stroke-74"),sQuery(id+"FHMxAyK4CFUKdhS_1.wireOp",EDGE,"1cb9c079-ea9b-4899-8069-e0e3048e911d.sketch_text.stroke-75"),sQuery(id+"FHMxAyK4CFUKdhS_1.wireOp",EDGE,"1cb9c079-ea9b-4899-8069-e0e3048e911d.sketch_text.stroke-76"),sQuery(id+"FHMxAyK4CFUKdhS_1.wireOp",EDGE,"1cb9c079-ea9b-4899-8069-e0e3048e911d.sketch_text.stroke-77"),sQuery(id+"FHMxAyK4CFUKdhS_1.wireOp",EDGE,"1cb9c079-ea9b-4899-8069-e0e3048e911d.sketch_text.stroke-78"),sQuery(id+"FHMxAyK4CFUKdhS_1.wireOp",EDGE,"1cb9c079-ea9b-4899-8069-e0e3048e911d.sketch_text.stroke-79"),sQuery(id+"FHMxAyK4CFUKdhS_1.wireOp",EDGE,"1cb9c079-ea9b-4899-8069-e0e3048e911d.sketch_text.stroke-80"),sQuery(id+"FHMxAyK4CFUKdhS_1.wireOp",EDGE,"1cb9c079-ea9b-4899-8069-e0e3048e911d.sketch_text.stroke-81"),sQuery(id+"FHMxAyK4CFUKdhS_1.wireOp",EDGE,"1cb9c079-ea9b-4899-8069-e0e3048e911d.sketch_text.stroke-82"),sQuery(id+"FHMxAyK4CFUKdhS_1.wireOp",EDGE,"1cb9c079-ea9b-4899-8069-e0e3048e911d.sketch_text.stroke-83"),sQuery(id+"FHMxAyK4CFUKdhS_1.wireOp",EDGE,"1cb9c079-ea9b-4899-8069-e0e3048e911d.sketch_text.stroke-84"),sQuery(id+"FHMxAyK4CFUKdhS_1.wireOp",EDGE,"1cb9c079-ea9b-4899-8069-e0e3048e911d.sketch_text.stroke-85"),sQuery(id+"FHMxAyK4CFUKdhS_1.wireOp",EDGE,"1cb9c079-ea9b-4899-8069-e0e3048e911d.sketch_text.stroke-86"),sQuery(id+"FHMxAyK4CFUKdhS_1.wireOp",EDGE,"1cb9c079-ea9b-4899-8069-e0e3048e911d.sketch_text.stroke-87"),sQuery(id+"FHMxAyK4CFUKdhS_1.wireOp",EDGE,"1cb9c079-ea9b-4899-8069-e0e3048e911d.sketch_text.stroke-88"),sQuery(id+"FHMxAyK4CFUKdhS_1.wireOp",EDGE,"1cb9c079-ea9b-4899-8069-e0e3048e911d.sketch_text.stroke-89"),sQuery(id+"FHMxAyK4CFUKdhS_1.wireOp",EDGE,"1cb9c079-ea9b-4899-8069-e0e3048e911d.sketch_text.stroke-90"),sQuery(id+"FHMxAyK4CFUKdhS_1.wireOp",EDGE,"1cb9c079-ea9b-4899-8069-e0e3048e911d.sketch_text.stroke-91"),sQuery(id+"FHMxAyK4CFUKdhS_1.wireOp",EDGE,"1cb9c079-ea9b-4899-8069-e0e3048e911d.sketch_text.stroke-92"),sQuery(id+"FHMxAyK4CFUKdhS_1.wireOp",EDGE,"1cb9c079-ea9b-4899-8069-e0e3048e911d.sketch_text.stroke-93"),sQuery(id+"FHMxAyK4CFUKdhS_1.wireOp",EDGE,"1cb9c079-ea9b-4899-8069-e0e3048e911d.sketch_text.stroke-94"),sQuery(id+"FHMxAyK4CFUKdhS_1.wireOp",EDGE,"1cb9c079-ea9b-4899-8069-e0e3048e911d.sketch_text.stroke-95"),sQuery(id+"FHMxAyK4CFUKdhS_1.wireOp",EDGE,"1cb9c079-ea9b-4899-8069-e0e3048e911d.sketch_text.stroke-96"),sQuery(id+"FHMxAyK4CFUKdhS_1.wireOp",EDGE,"1cb9c079-ea9b-4899-8069-e0e3048e911d.sketch_text.stroke-97"),sQuery(id+"FHMxAyK4CFUKdhS_1.wireOp",EDGE,"1cb9c079-ea9b-4899-8069-e0e3048e911d.sketch_text.stroke-103"),sQuery(id+"FHMxAyK4CFUKdhS_1.wireOp",EDGE,"1cb9c079-ea9b-4899-8069-e0e3048e911d.sketch_text.stroke-104"),sQuery(id+"FHMxAyK4CFUKdhS_1.wireOp",EDGE,"1cb9c079-ea9b-4899-8069-e0e3048e911d.sketch_text.stroke-105"),sQuery(id+"FHMxAyK4CFUKdhS_1.wireOp",EDGE,"1cb9c079-ea9b-4899-8069-e0e3048e911d.sketch_text.stroke-106"),sQuery(id+"FHMxAyK4CFUKdhS_1.wireOp",EDGE,"1cb9c079-ea9b-4899-8069-e0e3048e911d.sketch_text.stroke-107"),sQuery(id+"FHMxAyK4CFUKdhS_1.wireOp",EDGE,"1cb9c079-ea9b-4899-8069-e0e3048e911d.sketch_text.stroke-108"),sQuery(id+"FHMxAyK4CFUKdhS_1.wireOp",EDGE,"1cb9c079-ea9b-4899-8069-e0e3048e911d.sketch_text.stroke-109"),sQuery(id+"FHMxAyK4CFUKdhS_1.wireOp",EDGE,"1cb9c079-ea9b-4899-8069-e0e3048e911d.sketch_text.stroke-110"),sQuery(id+"FHMxAyK4CFUKdhS_1.wireOp",EDGE,"1cb9c079-ea9b-4899-8069-e0e3048e911d.sketch_text.stroke-111"),sQuery(id+"FHMxAyK4CFUKdhS_1.wireOp",EDGE,"1cb9c079-ea9b-4899-8069-e0e3048e911d.sketch_text.stroke-112"),sQuery(id+"FHMxAyK4CFUKdhS_1.wireOp",EDGE,"1cb9c079-ea9b-4899-8069-e0e3048e911d.sketch_text.stroke-113"),sQuery(id+"FHMxAyK4CFUKdhS_1.wireOp",EDGE,"1cb9c079-ea9b-4899-8069-e0e3048e911d.sketch_text.stroke-114"),sQuery(id+"FHMxAyK4CFUKdhS_1.wireOp",EDGE,"1cb9c079-ea9b-4899-8069-e0e3048e911d.sketch_text.stroke-115"),sQuery(id+"FHMxAyK4CFUKdhS_1.wireOp",EDGE,"1cb9c079-ea9b-4899-8069-e0e3048e911d.sketch_text.stroke-116"),sQuery(id+"FHMxAyK4CFUKdhS_1.wireOp",EDGE,"1cb9c079-ea9b-4899-8069-e0e3048e911d.sketch_text.stroke-117"),sQuery(id+"FHMxAyK4CFUKdhS_1.wireOp",EDGE,"1cb9c079-ea9b-4899-8069-e0e3048e911d.sketch_text.stroke-118"),sQuery(id+"FHMxAyK4CFUKdhS_1.wireOp",EDGE,"1cb9c079-ea9b-4899-8069-e0e3048e911d.sketch_text.stroke-119"),sQuery(id+"FHMxAyK4CFUKdhS_1.wireOp",EDGE,"1cb9c079-ea9b-4899-8069-e0e3048e911d.sketch_text.stroke-120"),sQuery(id+"FHMxAyK4CFUKdhS_1.wireOp",EDGE,"1cb9c079-ea9b-4899-8069-e0e3048e911d.sketch_text.stroke-121"),sQuery(id+"FHMxAyK4CFUKdhS_1.wireOp",EDGE,"1cb9c079-ea9b-4899-8069-e0e3048e911d.sketch_text.stroke-122"),sQuery(id+"FHMxAyK4CFUKdhS_1.wireOp",EDGE,"1cb9c079-ea9b-4899-8069-e0e3048e911d.sketch_text.stroke-123"),sQuery(id+"FHMxAyK4CFUKdhS_1.wireOp",EDGE,"1cb9c079-ea9b-4899-8069-e0e3048e911d.sketch_text.stroke-124"),sQuery(id+"FHMxAyK4CFUKdhS_1.wireOp",EDGE,"1cb9c079-ea9b-4899-8069-e0e3048e911d.sketch_text.stroke-125"),sQuery(id+"FHMxAyK4CFUKdhS_1.wireOp",EDGE,"1cb9c079-ea9b-4899-8069-e0e3048e911d.sketch_text.stroke-126"),sQuery(id+"FHMxAyK4CFUKdhS_1.wireOp",EDGE,"1cb9c079-ea9b-4899-8069-e0e3048e911d.sketch_text.stroke-127"),sQuery(id+"FHMxAyK4CFUKdhS_1.wireOp",EDGE,"1cb9c079-ea9b-4899-8069-e0e3048e911d.sketch_text.stroke-128"),sQuery(id+"FHMxAyK4CFUKdhS_1.wireOp",EDGE,"1cb9c079-ea9b-4899-8069-e0e3048e911d.sketch_text.stroke-129"),sQuery(id+"FHMxAyK4CFUKdhS_1.wireOp",EDGE,"1cb9c079-ea9b-4899-8069-e0e3048e911d.sketch_text.stroke-130"),sQuery(id+"FHMxAyK4CFUKdhS_1.wireOp",EDGE,"1cb9c079-ea9b-4899-8069-e0e3048e911d.sketch_text.stroke-131"),sQuery(id+"FHMxAyK4CFUKdhS_1.wireOp",EDGE,"1cb9c079-ea9b-4899-8069-e0e3048e911d.sketch_text.stroke-132"),sQuery(id+"FHMxAyK4CFUKdhS_1.wireOp",EDGE,"1cb9c079-ea9b-4899-8069-e0e3048e911d.sketch_text.stroke-133"),sQuery(id+"FHMxAyK4CFUKdhS_1.wireOp",EDGE,"1cb9c079-ea9b-4899-8069-e0e3048e911d.sketch_text.stroke-134"),sQuery(id+"FHMxAyK4CFUKdhS_1.wireOp",EDGE,"1cb9c079-ea9b-4899-8069-e0e3048e911d.sketch_text.stroke-135"),sQuery(id+"FHMxAyK4CFUKdhS_1.wireOp",EDGE,"1cb9c079-ea9b-4899-8069-e0e3048e911d.sketch_text.stroke-136"),sQuery(id+"FHMxAyK4CFUKdhS_1.wireOp",EDGE,"1cb9c079-ea9b-4899-8069-e0e3048e911d.sketch_text.stroke-137"),sQuery(id+"FHMxAyK4CFUKdhS_1.wireOp",EDGE,"1cb9c079-ea9b-4899-8069-e0e3048e911d.sketch_text.stroke-138"),sQuery(id+"FHMxAyK4CFUKdhS_1.wireOp",EDGE,"1cb9c079-ea9b-4899-8069-e0e3048e911d.sketch_text.stroke-139"),sQuery(id+"FHMxAyK4CFUKdhS_1.wireOp",EDGE,"1cb9c079-ea9b-4899-8069-e0e3048e911d.sketch_text.stroke-140"),sQuery(id+"FHMxAyK4CFUKdhS_1.wireOp",EDGE,"1cb9c079-ea9b-4899-8069-e0e3048e911d.sketch_text.stroke-141"),sQuery(id+"FHMxAyK4CFUKdhS_1.wireOp",EDGE,"1cb9c079-ea9b-4899-8069-e0e3048e911d.sketch_text.stroke-142"),sQuery(id+"FHMxAyK4CFUKdhS_1.wireOp",EDGE,"1cb9c079-ea9b-4899-8069-e0e3048e911d.sketch_text.stroke-143"),sQuery(id+"FHMxAyK4CFUKdhS_1.wireOp",EDGE,"1cb9c079-ea9b-4899-8069-e0e3048e911d.sketch_text.stroke-144"),sQuery(id+"FHMxAyK4CFUKdhS_1.wireOp",EDGE,"1cb9c079-ea9b-4899-8069-e0e3048e911d.sketch_text.stroke-145"),sQuery(id+"FHMxAyK4CFUKdhS_1.wireOp",EDGE,"1cb9c079-ea9b-4899-8069-e0e3048e911d.sketch_text.stroke-146"),sQuery(id+"FHMxAyK4CFUKdhS_1.wireOp",EDGE,"1cb9c079-ea9b-4899-8069-e0e3048e911d.sketch_text.stroke-147"),sQuery(id+"FHMxAyK4CFUKdhS_1.wireOp",EDGE,"1cb9c079-ea9b-4899-8069-e0e3048e911d.sketch_text.stroke-148"),sQuery(id+"FHMxAyK4CFUKdhS_1.wireOp",EDGE,"1cb9c079-ea9b-4899-8069-e0e3048e911d.sketch_text.stroke-149"),sQuery(id+"FHMxAyK4CFUKdhS_1.wireOp",EDGE,"1cb9c079-ea9b-4899-8069-e0e3048e911d.sketch_text.stroke-150"),sQuery(id+"FHMxAyK4CFUKdhS_1.wireOp",EDGE,"1cb9c079-ea9b-4899-8069-e0e3048e911d.sketch_text.stroke-151"),sQuery(id+"FHMxAyK4CFUKdhS_1.wireOp",EDGE,"1cb9c079-ea9b-4899-8069-e0e3048e911d.sketch_text.stroke-152"),sQuery(id+"FHMxAyK4CFUKdhS_1.wireOp",EDGE,"1cb9c079-ea9b-4899-8069-e0e3048e911d.sketch_text.stroke-153"),sQuery(id+"FHMxAyK4CFUKdhS_1.wireOp",EDGE,"1cb9c079-ea9b-4899-8069-e0e3048e911d.sketch_text.stroke-159"),sQuery(id+"FHMxAyK4CFUKdhS_1.wireOp",EDGE,"1cb9c079-ea9b-4899-8069-e0e3048e911d.sketch_text.stroke-160"),sQuery(id+"FHMxAyK4CFUKdhS_1.wireOp",EDGE,"1cb9c079-ea9b-4899-8069-e0e3048e911d.sketch_text.stroke-161"),sQuery(id+"FHMxAyK4CFUKdhS_1.wireOp",EDGE,"1cb9c079-ea9b-4899-8069-e0e3048e911d.sketch_text.stroke-162"),sQuery(id+"FHMxAyK4CFUKdhS_1.wireOp",EDGE,"1cb9c079-ea9b-4899-8069-e0e3048e911d.sketch_text.stroke-163"),sQuery(id+"FHMxAyK4CFUKdhS_1.wireOp",EDGE,"1cb9c079-ea9b-4899-8069-e0e3048e911d.sketch_text.stroke-164"),sQuery(id+"FHMxAyK4CFUKdhS_1.wireOp",EDGE,"1cb9c079-ea9b-4899-8069-e0e3048e911d.sketch_text.stroke-165"),sQuery(id+"FHMxAyK4CFUKdhS_1.wireOp",EDGE,"1cb9c079-ea9b-4899-8069-e0e3048e911d.sketch_text.stroke-166"),sQuery(id+"FHMxAyK4CFUKdhS_1.wireOp",EDGE,"1cb9c079-ea9b-4899-8069-e0e3048e911d.sketch_text.stroke-167"),sQuery(id+"FHMxAyK4CFUKdhS_1.wireOp",EDGE,"1cb9c079-ea9b-4899-8069-e0e3048e911d.sketch_text.stroke-168"),sQuery(id+"FHMxAyK4CFUKdhS_1.wireOp",EDGE,"1cb9c079-ea9b-4899-8069-e0e3048e911d.sketch_text.stroke-169"),sQuery(id+"FHMxAyK4CFUKdhS_1.wireOp",EDGE,"1cb9c079-ea9b-4899-8069-e0e3048e911d.sketch_text.stroke-170"),sQuery(id+"FHMxAyK4CFUKdhS_1.wireOp",EDGE,"1cb9c079-ea9b-4899-8069-e0e3048e911d.sketch_text.stroke-171"),sQuery(id+"FHMxAyK4CFUKdhS_1.wireOp",EDGE,"1cb9c079-ea9b-4899-8069-e0e3048e911d.sketch_text.stroke-172"),sQuery(id+"FHMxAyK4CFUKdhS_1.wireOp",EDGE,"1cb9c079-ea9b-4899-8069-e0e3048e911d.sketch_text.stroke-173"),sQuery(id+"FHMxAyK4CFUKdhS_1.wireOp",EDGE,"1cb9c079-ea9b-4899-8069-e0e3048e911d.sketch_text.stroke-174"),sQuery(id+"FHMxAyK4CFUKdhS_1.wireOp",EDGE,"1cb9c079-ea9b-4899-8069-e0e3048e911d.sketch_text.stroke-175"),sQuery(id+"FHMxAyK4CFUKdhS_1.wireOp",EDGE,"1cb9c079-ea9b-4899-8069-e0e3048e911d.sketch_text.stroke-176"),sQuery(id+"FHMxAyK4CFUKdhS_1.wireOp",EDGE,"1cb9c079-ea9b-4899-8069-e0e3048e911d.sketch_text.stroke-177"),sQuery(id+"FHMxAyK4CFUKdhS_1.wireOp",EDGE,"1cb9c079-ea9b-4899-8069-e0e3048e911d.sketch_text.stroke-178"),sQuery(id+"FHMxAyK4CFUKdhS_1.wireOp",EDGE,"1cb9c079-ea9b-4899-8069-e0e3048e911d.sketch_text.stroke-179"),sQuery(id+"FHMxAyK4CFUKdhS_1.wireOp",EDGE,"1cb9c079-ea9b-4899-8069-e0e3048e911d.sketch_text.stroke-180"),subQ0,subQ2])],"isStart":true}),makeQuery(id+"F4.opExtrude","SWEPT_FACE",FACE,{"disambiguationData":[OSD([subQ2])]})])],"derivedFrom":makeQuery(id+"F4.opExtrude","CAP_EDGE",EDGE,{"disambiguationData":[OSD([subQ0])],"isStart":true})});}
            var Q22;
            {var subQ0=sQuery(id+"F3.wireOp",EDGE,"E28");var subQ1=sQuery(id+"F0.wireOp",EDGE,"E0.top");var subQ2=sQuery(id+"F3.wireOp",EDGE,"E29");var subQ3=sQuery(id+"F0.wireOp",EDGE,"E0.bottom");Q22=makeQuery(id+"F4.boolean.opBoolean","SPLIT",EDGE,{"disambiguationData":[TD([makeQuery(id+"F1.opExtrude","CAP_FACE",FACE,{"disambiguationData":[OSD([subQ3,subQ1,sQuery(id+"F0.wireOp",EDGE,"E0.left"),sQuery(id+"F0.wireOp",EDGE,"E0.right")])],"isStart":false}),makeQuery(id+"F1.opExtrude","SWEPT_FACE",FACE,{"disambiguationData":[OSD([subQ1])]}),makeQuery(id+"F4.opExtrude","SWEPT_FACE",FACE,{"disambiguationData":[OSD([subQ0])]}),makeQuery(id+"F4.opExtrude","CAP_FACE",FACE,{"disambiguationData":[OSD([subQ3,sQuery(id+"F2.wireOp",EDGE,"fcba4419-a2ee-464f-be9d-58f11bf3418b.sketch_text.stroke-0"),sQuery(id+"F2.wireOp",EDGE,"fcba4419-a2ee-464f-be9d-58f11bf3418b.sketch_text.stroke-1"),sQuery(id+"F2.wireOp",EDGE,"fcba4419-a2ee-464f-be9d-58f11bf3418b.sketch_text.stroke-2"),sQuery(id+"F2.wireOp",EDGE,"fcba4419-a2ee-464f-be9d-58f11bf3418b.sketch_text.stroke-3"),sQuery(id+"F2.wireOp",EDGE,"fcba4419-a2ee-464f-be9d-58f11bf3418b.sketch_text.stroke-4"),sQuery(id+"F2.wireOp",EDGE,"fcba4419-a2ee-464f-be9d-58f11bf3418b.sketch_text.stroke-5"),sQuery(id+"F2.wireOp",EDGE,"fcba4419-a2ee-464f-be9d-58f11bf3418b.sketch_text.stroke-6"),sQuery(id+"F2.wireOp",EDGE,"fcba4419-a2ee-464f-be9d-58f11bf3418b.sketch_text.stroke-7"),sQuery(id+"F2.wireOp",EDGE,"fcba4419-a2ee-464f-be9d-58f11bf3418b.sketch_text.stroke-8"),sQuery(id+"F2.wireOp",EDGE,"fcba4419-a2ee-464f-be9d-58f11bf3418b.sketch_text.stroke-9"),sQuery(id+"F2.wireOp",EDGE,"fcba4419-a2ee-464f-be9d-58f11bf3418b.sketch_text.stroke-10"),sQuery(id+"F2.wireOp",EDGE,"fcba4419-a2ee-464f-be9d-58f11bf3418b.sketch_text.stroke-11"),sQuery(id+"F2.wireOp",EDGE,"fcba4419-a2ee-464f-be9d-58f11bf3418b.sketch_text.stroke-12"),sQuery(id+"F2.wireOp",EDGE,"fcba4419-a2ee-464f-be9d-58f11bf3418b.sketch_text.stroke-13"),sQuery(id+"F2.wireOp",EDGE,"fcba4419-a2ee-464f-be9d-58f11bf3418b.sketch_text.stroke-14"),sQuery(id+"F2.wireOp",EDGE,"fcba4419-a2ee-464f-be9d-58f11bf3418b.sketch_text.stroke-15"),sQuery(id+"F2.wireOp",EDGE,"fcba4419-a2ee-464f-be9d-58f11bf3418b.sketch_text.stroke-16"),sQuery(id+"F2.wireOp",EDGE,"fcba4419-a2ee-464f-be9d-58f11bf3418b.sketch_text.stroke-17"),sQuery(id+"F2.wireOp",EDGE,"fcba4419-a2ee-464f-be9d-58f11bf3418b.sketch_text.stroke-18"),sQuery(id+"F2.wireOp",EDGE,"fcba4419-a2ee-464f-be9d-58f11bf3418b.sketch_text.stroke-19"),sQuery(id+"F2.wireOp",EDGE,"fcba4419-a2ee-464f-be9d-58f11bf3418b.sketch_text.stroke-20"),sQuery(id+"F2.wireOp",EDGE,"fcba4419-a2ee-464f-be9d-58f11bf3418b.sketch_text.stroke-21"),sQuery(id+"F2.wireOp",EDGE,"fcba4419-a2ee-464f-be9d-58f11bf3418b.sketch_text.stroke-22"),sQuery(id+"F2.wireOp",EDGE,"fcba4419-a2ee-464f-be9d-58f11bf3418b.sketch_text.stroke-23"),sQuery(id+"F2.wireOp",EDGE,"fcba4419-a2ee-464f-be9d-58f11bf3418b.sketch_text.stroke-24"),sQuery(id+"F2.wireOp",EDGE,"fcba4419-a2ee-464f-be9d-58f11bf3418b.sketch_text.stroke-25"),sQuery(id+"F2.wireOp",EDGE,"fcba4419-a2ee-464f-be9d-58f11bf3418b.sketch_text.stroke-26"),sQuery(id+"F2.wireOp",EDGE,"fcba4419-a2ee-464f-be9d-58f11bf3418b.sketch_text.stroke-27"),sQuery(id+"F2.wireOp",EDGE,"fcba4419-a2ee-464f-be9d-58f11bf3418b.sketch_text.stroke-28"),sQuery(id+"F2.wireOp",EDGE,"fcba4419-a2ee-464f-be9d-58f11bf3418b.sketch_text.stroke-29"),sQuery(id+"F2.wireOp",EDGE,"fcba4419-a2ee-464f-be9d-58f11bf3418b.sketch_text.stroke-30"),sQuery(id+"F2.wireOp",EDGE,"fcba4419-a2ee-464f-be9d-58f11bf3418b.sketch_text.stroke-31"),sQuery(id+"F2.wireOp",EDGE,"fcba4419-a2ee-464f-be9d-58f11bf3418b.sketch_text.stroke-32"),sQuery(id+"F2.wireOp",EDGE,"fcba4419-a2ee-464f-be9d-58f11bf3418b.sketch_text.stroke-33"),sQuery(id+"F2.wireOp",EDGE,"fcba4419-a2ee-464f-be9d-58f11bf3418b.sketch_text.stroke-34"),sQuery(id+"F2.wireOp",EDGE,"fcba4419-a2ee-464f-be9d-58f11bf3418b.sketch_text.stroke-35"),sQuery(id+"F2.wireOp",EDGE,"fcba4419-a2ee-464f-be9d-58f11bf3418b.sketch_text.stroke-36"),sQuery(id+"F2.wireOp",EDGE,"fcba4419-a2ee-464f-be9d-58f11bf3418b.sketch_text.stroke-37"),sQuery(id+"F2.wireOp",EDGE,"fcba4419-a2ee-464f-be9d-58f11bf3418b.sketch_text.stroke-38"),sQuery(id+"F2.wireOp",EDGE,"fcba4419-a2ee-464f-be9d-58f11bf3418b.sketch_text.stroke-39"),sQuery(id+"F2.wireOp",EDGE,"fcba4419-a2ee-464f-be9d-58f11bf3418b.sketch_text.stroke-40"),sQuery(id+"F2.wireOp",EDGE,"fcba4419-a2ee-464f-be9d-58f11bf3418b.sketch_text.stroke-41"),sQuery(id+"F2.wireOp",EDGE,"fcba4419-a2ee-464f-be9d-58f11bf3418b.sketch_text.stroke-42"),sQuery(id+"F2.wireOp",EDGE,"fcba4419-a2ee-464f-be9d-58f11bf3418b.sketch_text.stroke-43"),sQuery(id+"F2.wireOp",EDGE,"fcba4419-a2ee-464f-be9d-58f11bf3418b.sketch_text.stroke-44"),sQuery(id+"F2.wireOp",EDGE,"fcba4419-a2ee-464f-be9d-58f11bf3418b.sketch_text.stroke-45"),sQuery(id+"F2.wireOp",EDGE,"fcba4419-a2ee-464f-be9d-58f11bf3418b.sketch_text.stroke-46"),sQuery(id+"F2.wireOp",EDGE,"fcba4419-a2ee-464f-be9d-58f11bf3418b.sketch_text.stroke-47"),sQuery(id+"F2.wireOp",EDGE,"fcba4419-a2ee-464f-be9d-58f11bf3418b.sketch_text.stroke-48"),sQuery(id+"F2.wireOp",EDGE,"fcba4419-a2ee-464f-be9d-58f11bf3418b.sketch_text.stroke-49"),sQuery(id+"F2.wireOp",EDGE,"fcba4419-a2ee-464f-be9d-58f11bf3418b.sketch_text.stroke-50"),sQuery(id+"F2.wireOp",EDGE,"fcba4419-a2ee-464f-be9d-58f11bf3418b.sketch_text.stroke-51"),sQuery(id+"F2.wireOp",EDGE,"fcba4419-a2ee-464f-be9d-58f11bf3418b.sketch_text.stroke-52"),sQuery(id+"F2.wireOp",EDGE,"fcba4419-a2ee-464f-be9d-58f11bf3418b.sketch_text.stroke-53"),sQuery(id+"F2.wireOp",EDGE,"fcba4419-a2ee-464f-be9d-58f11bf3418b.sketch_text.stroke-54"),sQuery(id+"F2.wireOp",EDGE,"fcba4419-a2ee-464f-be9d-58f11bf3418b.sketch_text.stroke-55"),sQuery(id+"F2.wireOp",EDGE,"fcba4419-a2ee-464f-be9d-58f11bf3418b.sketch_text.stroke-56"),sQuery(id+"F2.wireOp",EDGE,"fcba4419-a2ee-464f-be9d-58f11bf3418b.sketch_text.stroke-57"),sQuery(id+"F2.wireOp",EDGE,"fcba4419-a2ee-464f-be9d-58f11bf3418b.sketch_text.stroke-58"),sQuery(id+"F2.wireOp",EDGE,"fcba4419-a2ee-464f-be9d-58f11bf3418b.sketch_text.stroke-59"),sQuery(id+"F2.wireOp",EDGE,"fcba4419-a2ee-464f-be9d-58f11bf3418b.sketch_text.stroke-60"),sQuery(id+"F2.wireOp",EDGE,"fcba4419-a2ee-464f-be9d-58f11bf3418b.sketch_text.stroke-61"),sQuery(id+"F2.wireOp",EDGE,"fcba4419-a2ee-464f-be9d-58f11bf3418b.sketch_text.stroke-62"),sQuery(id+"F2.wireOp",EDGE,"fcba4419-a2ee-464f-be9d-58f11bf3418b.sketch_text.stroke-63"),sQuery(id+"F2.wireOp",EDGE,"fcba4419-a2ee-464f-be9d-58f11bf3418b.sketch_text.stroke-64"),sQuery(id+"F2.wireOp",EDGE,"fcba4419-a2ee-464f-be9d-58f11bf3418b.sketch_text.stroke-65"),sQuery(id+"F2.wireOp",EDGE,"fcba4419-a2ee-464f-be9d-58f11bf3418b.sketch_text.stroke-66"),sQuery(id+"F2.wireOp",EDGE,"fcba4419-a2ee-464f-be9d-58f11bf3418b.sketch_text.stroke-67"),sQuery(id+"F2.wireOp",EDGE,"fcba4419-a2ee-464f-be9d-58f11bf3418b.sketch_text.stroke-68"),sQuery(id+"F2.wireOp",EDGE,"fcba4419-a2ee-464f-be9d-58f11bf3418b.sketch_text.stroke-69"),sQuery(id+"F2.wireOp",EDGE,"fcba4419-a2ee-464f-be9d-58f11bf3418b.sketch_text.stroke-70"),sQuery(id+"F2.wireOp",EDGE,"fcba4419-a2ee-464f-be9d-58f11bf3418b.sketch_text.stroke-71"),sQuery(id+"F2.wireOp",EDGE,"fcba4419-a2ee-464f-be9d-58f11bf3418b.sketch_text.stroke-72"),sQuery(id+"F2.wireOp",EDGE,"fcba4419-a2ee-464f-be9d-58f11bf3418b.sketch_text.stroke-73"),sQuery(id+"F2.wireOp",EDGE,"fcba4419-a2ee-464f-be9d-58f11bf3418b.sketch_text.stroke-74"),sQuery(id+"F2.wireOp",EDGE,"fcba4419-a2ee-464f-be9d-58f11bf3418b.sketch_text.stroke-75"),sQuery(id+"F2.wireOp",EDGE,"fcba4419-a2ee-464f-be9d-58f11bf3418b.sketch_text.stroke-76"),sQuery(id+"F2.wireOp",EDGE,"fcba4419-a2ee-464f-be9d-58f11bf3418b.sketch_text.stroke-77"),sQuery(id+"F2.wireOp",EDGE,"fcba4419-a2ee-464f-be9d-58f11bf3418b.sketch_text.stroke-78"),sQuery(id+"F2.wireOp",EDGE,"fcba4419-a2ee-464f-be9d-58f11bf3418b.sketch_text.stroke-79"),sQuery(id+"F2.wireOp",EDGE,"fcba4419-a2ee-464f-be9d-58f11bf3418b.sketch_text.stroke-80"),sQuery(id+"F2.wireOp",EDGE,"fcba4419-a2ee-464f-be9d-58f11bf3418b.sketch_text.stroke-81"),sQuery(id+"F2.wireOp",EDGE,"fcba4419-a2ee-464f-be9d-58f11bf3418b.sketch_text.stroke-82"),sQuery(id+"F2.wireOp",EDGE,"fcba4419-a2ee-464f-be9d-58f11bf3418b.sketch_text.stroke-83"),sQuery(id+"F2.wireOp",EDGE,"fcba4419-a2ee-464f-be9d-58f11bf3418b.sketch_text.stroke-84"),sQuery(id+"F2.wireOp",EDGE,"fcba4419-a2ee-464f-be9d-58f11bf3418b.sketch_text.stroke-85"),sQuery(id+"F2.wireOp",EDGE,"fcba4419-a2ee-464f-be9d-58f11bf3418b.sketch_text.stroke-86"),sQuery(id+"F2.wireOp",EDGE,"fcba4419-a2ee-464f-be9d-58f11bf3418b.sketch_text.stroke-87"),sQuery(id+"F2.wireOp",EDGE,"fcba4419-a2ee-464f-be9d-58f11bf3418b.sketch_text.stroke-88"),sQuery(id+"F2.wireOp",EDGE,"fcba4419-a2ee-464f-be9d-58f11bf3418b.sketch_text.stroke-89"),sQuery(id+"F2.wireOp",EDGE,"fcba4419-a2ee-464f-be9d-58f11bf3418b.sketch_text.stroke-90"),sQuery(id+"F2.wireOp",EDGE,"fcba4419-a2ee-464f-be9d-58f11bf3418b.sketch_text.stroke-91"),sQuery(id+"F2.wireOp",EDGE,"fcba4419-a2ee-464f-be9d-58f11bf3418b.sketch_text.stroke-92"),sQuery(id+"F2.wireOp",EDGE,"fcba4419-a2ee-464f-be9d-58f11bf3418b.sketch_text.stroke-93"),sQuery(id+"F2.wireOp",EDGE,"fcba4419-a2ee-464f-be9d-58f11bf3418b.sketch_text.stroke-94"),sQuery(id+"F2.wireOp",EDGE,"fcba4419-a2ee-464f-be9d-58f11bf3418b.sketch_text.stroke-95"),sQuery(id+"F2.wireOp",EDGE,"fcba4419-a2ee-464f-be9d-58f11bf3418b.sketch_text.stroke-96"),sQuery(id+"F2.wireOp",EDGE,"fcba4419-a2ee-464f-be9d-58f11bf3418b.sketch_text.stroke-97"),sQuery(id+"F2.wireOp",EDGE,"fcba4419-a2ee-464f-be9d-58f11bf3418b.sketch_text.stroke-98"),sQuery(id+"F2.wireOp",EDGE,"fcba4419-a2ee-464f-be9d-58f11bf3418b.sketch_text.stroke-99"),sQuery(id+"F2.wireOp",EDGE,"fcba4419-a2ee-464f-be9d-58f11bf3418b.sketch_text.stroke-100"),sQuery(id+"F2.wireOp",EDGE,"fcba4419-a2ee-464f-be9d-58f11bf3418b.sketch_text.stroke-101"),sQuery(id+"F2.wireOp",EDGE,"fcba4419-a2ee-464f-be9d-58f11bf3418b.sketch_text.stroke-102"),sQuery(id+"F2.wireOp",EDGE,"fcba4419-a2ee-464f-be9d-58f11bf3418b.sketch_text.stroke-103"),sQuery(id+"F2.wireOp",EDGE,"fcba4419-a2ee-464f-be9d-58f11bf3418b.sketch_text.stroke-104"),sQuery(id+"F2.wireOp",EDGE,"fcba4419-a2ee-464f-be9d-58f11bf3418b.sketch_text.stroke-105"),sQuery(id+"F2.wireOp",EDGE,"fcba4419-a2ee-464f-be9d-58f11bf3418b.sketch_text.stroke-106"),sQuery(id+"F2.wireOp",EDGE,"fcba4419-a2ee-464f-be9d-58f11bf3418b.sketch_text.stroke-107"),sQuery(id+"F2.wireOp",EDGE,"fcba4419-a2ee-464f-be9d-58f11bf3418b.sketch_text.stroke-108"),sQuery(id+"F2.wireOp",EDGE,"fcba4419-a2ee-464f-be9d-58f11bf3418b.sketch_text.stroke-109"),sQuery(id+"F2.wireOp",EDGE,"fcba4419-a2ee-464f-be9d-58f11bf3418b.sketch_text.stroke-110"),sQuery(id+"F2.wireOp",EDGE,"fcba4419-a2ee-464f-be9d-58f11bf3418b.sketch_text.stroke-111"),sQuery(id+"F2.wireOp",EDGE,"fcba4419-a2ee-464f-be9d-58f11bf3418b.sketch_text.stroke-112"),sQuery(id+"F2.wireOp",EDGE,"fcba4419-a2ee-464f-be9d-58f11bf3418b.sketch_text.stroke-113"),sQuery(id+"F2.wireOp",EDGE,"fcba4419-a2ee-464f-be9d-58f11bf3418b.sketch_text.stroke-114"),sQuery(id+"F2.wireOp",EDGE,"fcba4419-a2ee-464f-be9d-58f11bf3418b.sketch_text.stroke-115"),sQuery(id+"F2.wireOp",EDGE,"fcba4419-a2ee-464f-be9d-58f11bf3418b.sketch_text.stroke-116"),sQuery(id+"F2.wireOp",EDGE,"fcba4419-a2ee-464f-be9d-58f11bf3418b.sketch_text.stroke-117"),sQuery(id+"F2.wireOp",EDGE,"fcba4419-a2ee-464f-be9d-58f11bf3418b.sketch_text.stroke-118"),sQuery(id+"F2.wireOp",EDGE,"fcba4419-a2ee-464f-be9d-58f11bf3418b.sketch_text.stroke-119"),sQuery(id+"F2.wireOp",EDGE,"fcba4419-a2ee-464f-be9d-58f11bf3418b.sketch_text.stroke-120"),sQuery(id+"F2.wireOp",EDGE,"fcba4419-a2ee-464f-be9d-58f11bf3418b.sketch_text.stroke-121"),sQuery(id+"F2.wireOp",EDGE,"fcba4419-a2ee-464f-be9d-58f11bf3418b.sketch_text.stroke-122"),sQuery(id+"F2.wireOp",EDGE,"fcba4419-a2ee-464f-be9d-58f11bf3418b.sketch_text.stroke-123"),sQuery(id+"F2.wireOp",EDGE,"fcba4419-a2ee-464f-be9d-58f11bf3418b.sketch_text.stroke-124"),sQuery(id+"F2.wireOp",EDGE,"fcba4419-a2ee-464f-be9d-58f11bf3418b.sketch_text.stroke-125"),sQuery(id+"F2.wireOp",EDGE,"fcba4419-a2ee-464f-be9d-58f11bf3418b.sketch_text.stroke-126"),sQuery(id+"F2.wireOp",EDGE,"fcba4419-a2ee-464f-be9d-58f11bf3418b.sketch_text.stroke-127"),sQuery(id+"F2.wireOp",EDGE,"fcba4419-a2ee-464f-be9d-58f11bf3418b.sketch_text.stroke-128"),sQuery(id+"F2.wireOp",EDGE,"fcba4419-a2ee-464f-be9d-58f11bf3418b.sketch_text.stroke-129"),sQuery(id+"F2.wireOp",EDGE,"fcba4419-a2ee-464f-be9d-58f11bf3418b.sketch_text.stroke-130"),sQuery(id+"F2.wireOp",EDGE,"fcba4419-a2ee-464f-be9d-58f11bf3418b.sketch_text.stroke-131"),sQuery(id+"F2.wireOp",EDGE,"fcba4419-a2ee-464f-be9d-58f11bf3418b.sketch_text.stroke-132"),sQuery(id+"F2.wireOp",EDGE,"fcba4419-a2ee-464f-be9d-58f11bf3418b.sketch_text.stroke-133"),sQuery(id+"F2.wireOp",EDGE,"fcba4419-a2ee-464f-be9d-58f11bf3418b.sketch_text.stroke-134"),sQuery(id+"F2.wireOp",EDGE,"fcba4419-a2ee-464f-be9d-58f11bf3418b.sketch_text.stroke-135"),sQuery(id+"F2.wireOp",EDGE,"fcba4419-a2ee-464f-be9d-58f11bf3418b.sketch_text.stroke-136"),sQuery(id+"F2.wireOp",EDGE,"fcba4419-a2ee-464f-be9d-58f11bf3418b.sketch_text.stroke-137"),sQuery(id+"F2.wireOp",EDGE,"fcba4419-a2ee-464f-be9d-58f11bf3418b.sketch_text.stroke-138"),sQuery(id+"F2.wireOp",EDGE,"fcba4419-a2ee-464f-be9d-58f11bf3418b.sketch_text.stroke-139"),sQuery(id+"F2.wireOp",EDGE,"fcba4419-a2ee-464f-be9d-58f11bf3418b.sketch_text.stroke-140"),sQuery(id+"F2.wireOp",EDGE,"fcba4419-a2ee-464f-be9d-58f11bf3418b.sketch_text.stroke-141"),sQuery(id+"F2.wireOp",EDGE,"fcba4419-a2ee-464f-be9d-58f11bf3418b.sketch_text.stroke-142"),sQuery(id+"F2.wireOp",EDGE,"fcba4419-a2ee-464f-be9d-58f11bf3418b.sketch_text.stroke-143"),sQuery(id+"F2.wireOp",EDGE,"fcba4419-a2ee-464f-be9d-58f11bf3418b.sketch_text.stroke-144"),sQuery(id+"F2.wireOp",EDGE,"fcba4419-a2ee-464f-be9d-58f11bf3418b.sketch_text.stroke-145"),sQuery(id+"F2.wireOp",EDGE,"fcba4419-a2ee-464f-be9d-58f11bf3418b.sketch_text.stroke-146"),sQuery(id+"F2.wireOp",EDGE,"fcba4419-a2ee-464f-be9d-58f11bf3418b.sketch_text.stroke-147"),sQuery(id+"F2.wireOp",EDGE,"fcba4419-a2ee-464f-be9d-58f11bf3418b.sketch_text.stroke-148"),sQuery(id+"F2.wireOp",EDGE,"fcba4419-a2ee-464f-be9d-58f11bf3418b.sketch_text.stroke-149"),sQuery(id+"F2.wireOp",EDGE,"fcba4419-a2ee-464f-be9d-58f11bf3418b.sketch_text.stroke-150"),sQuery(id+"F2.wireOp",EDGE,"fcba4419-a2ee-464f-be9d-58f11bf3418b.sketch_text.stroke-151"),sQuery(id+"F2.wireOp",EDGE,"fcba4419-a2ee-464f-be9d-58f11bf3418b.sketch_text.stroke-152"),sQuery(id+"F2.wireOp",EDGE,"fcba4419-a2ee-464f-be9d-58f11bf3418b.sketch_text.stroke-153"),sQuery(id+"F2.wireOp",EDGE,"fcba4419-a2ee-464f-be9d-58f11bf3418b.sketch_text.stroke-154"),sQuery(id+"F2.wireOp",EDGE,"fcba4419-a2ee-464f-be9d-58f11bf3418b.sketch_text.stroke-155"),sQuery(id+"F2.wireOp",EDGE,"fcba4419-a2ee-464f-be9d-58f11bf3418b.sketch_text.stroke-156"),sQuery(id+"F2.wireOp",EDGE,"fcba4419-a2ee-464f-be9d-58f11bf3418b.sketch_text.stroke-157"),sQuery(id+"F2.wireOp",EDGE,"fcba4419-a2ee-464f-be9d-58f11bf3418b.sketch_text.stroke-158"),sQuery(id+"F2.wireOp",EDGE,"fcba4419-a2ee-464f-be9d-58f11bf3418b.sketch_text.stroke-159"),sQuery(id+"F2.wireOp",EDGE,"fcba4419-a2ee-464f-be9d-58f11bf3418b.sketch_text.stroke-160"),sQuery(id+"F2.wireOp",EDGE,"fcba4419-a2ee-464f-be9d-58f11bf3418b.sketch_text.stroke-161"),sQuery(id+"F2.wireOp",EDGE,"fcba4419-a2ee-464f-be9d-58f11bf3418b.sketch_text.stroke-162"),sQuery(id+"F2.wireOp",EDGE,"fcba4419-a2ee-464f-be9d-58f11bf3418b.sketch_text.stroke-163"),sQuery(id+"F2.wireOp",EDGE,"fcba4419-a2ee-464f-be9d-58f11bf3418b.sketch_text.stroke-164"),sQuery(id+"F2.wireOp",EDGE,"fcba4419-a2ee-464f-be9d-58f11bf3418b.sketch_text.stroke-165"),sQuery(id+"F2.wireOp",EDGE,"fcba4419-a2ee-464f-be9d-58f11bf3418b.sketch_text.stroke-166"),sQuery(id+"F2.wireOp",EDGE,"fcba4419-a2ee-464f-be9d-58f11bf3418b.sketch_text.stroke-167"),sQuery(id+"F2.wireOp",EDGE,"fcba4419-a2ee-464f-be9d-58f11bf3418b.sketch_text.stroke-168"),sQuery(id+"F2.wireOp",EDGE,"fcba4419-a2ee-464f-be9d-58f11bf3418b.sketch_text.stroke-169"),sQuery(id+"F2.wireOp",EDGE,"fcba4419-a2ee-464f-be9d-58f11bf3418b.sketch_text.stroke-170"),sQuery(id+"F2.wireOp",EDGE,"fcba4419-a2ee-464f-be9d-58f11bf3418b.sketch_text.stroke-171"),sQuery(id+"F2.wireOp",EDGE,"fcba4419-a2ee-464f-be9d-58f11bf3418b.sketch_text.stroke-172"),sQuery(id+"F2.wireOp",EDGE,"fcba4419-a2ee-464f-be9d-58f11bf3418b.sketch_text.stroke-173"),sQuery(id+"FHMxAyK4CFUKdhS_1.wireOp",EDGE,"1cb9c079-ea9b-4899-8069-e0e3048e911d.sketch_text.stroke-0"),sQuery(id+"FHMxAyK4CFUKdhS_1.wireOp",EDGE,"1cb9c079-ea9b-4899-8069-e0e3048e911d.sketch_text.stroke-1"),sQuery(id+"FHMxAyK4CFUKdhS_1.wireOp",EDGE,"1cb9c079-ea9b-4899-8069-e0e3048e911d.sketch_text.stroke-2"),sQuery(id+"FHMxAyK4CFUKdhS_1.wireOp",EDGE,"1cb9c079-ea9b-4899-8069-e0e3048e911d.sketch_text.stroke-3"),sQuery(id+"FHMxAyK4CFUKdhS_1.wireOp",EDGE,"1cb9c079-ea9b-4899-8069-e0e3048e911d.sketch_text.stroke-4"),sQuery(id+"FHMxAyK4CFUKdhS_1.wireOp",EDGE,"1cb9c079-ea9b-4899-8069-e0e3048e911d.sketch_text.stroke-5"),sQuery(id+"FHMxAyK4CFUKdhS_1.wireOp",EDGE,"1cb9c079-ea9b-4899-8069-e0e3048e911d.sketch_text.stroke-6"),sQuery(id+"FHMxAyK4CFUKdhS_1.wireOp",EDGE,"1cb9c079-ea9b-4899-8069-e0e3048e911d.sketch_text.stroke-7"),sQuery(id+"FHMxAyK4CFUKdhS_1.wireOp",EDGE,"1cb9c079-ea9b-4899-8069-e0e3048e911d.sketch_text.stroke-8"),sQuery(id+"FHMxAyK4CFUKdhS_1.wireOp",EDGE,"1cb9c079-ea9b-4899-8069-e0e3048e911d.sketch_text.stroke-9"),sQuery(id+"FHMxAyK4CFUKdhS_1.wireOp",EDGE,"1cb9c079-ea9b-4899-8069-e0e3048e911d.sketch_text.stroke-10"),sQuery(id+"FHMxAyK4CFUKdhS_1.wireOp",EDGE,"1cb9c079-ea9b-4899-8069-e0e3048e911d.sketch_text.stroke-11"),sQuery(id+"FHMxAyK4CFUKdhS_1.wireOp",EDGE,"1cb9c079-ea9b-4899-8069-e0e3048e911d.sketch_text.stroke-12"),sQuery(id+"FHMxAyK4CFUKdhS_1.wireOp",EDGE,"1cb9c079-ea9b-4899-8069-e0e3048e911d.sketch_text.stroke-13"),sQuery(id+"FHMxAyK4CFUKdhS_1.wireOp",EDGE,"1cb9c079-ea9b-4899-8069-e0e3048e911d.sketch_text.stroke-14"),sQuery(id+"FHMxAyK4CFUKdhS_1.wireOp",EDGE,"1cb9c079-ea9b-4899-8069-e0e3048e911d.sketch_text.stroke-15"),sQuery(id+"FHMxAyK4CFUKdhS_1.wireOp",EDGE,"1cb9c079-ea9b-4899-8069-e0e3048e911d.sketch_text.stroke-16"),sQuery(id+"FHMxAyK4CFUKdhS_1.wireOp",EDGE,"1cb9c079-ea9b-4899-8069-e0e3048e911d.sketch_text.stroke-17"),sQuery(id+"FHMxAyK4CFUKdhS_1.wireOp",EDGE,"1cb9c079-ea9b-4899-8069-e0e3048e911d.sketch_text.stroke-18"),sQuery(id+"FHMxAyK4CFUKdhS_1.wireOp",EDGE,"1cb9c079-ea9b-4899-8069-e0e3048e911d.sketch_text.stroke-19"),sQuery(id+"FHMxAyK4CFUKdhS_1.wireOp",EDGE,"1cb9c079-ea9b-4899-8069-e0e3048e911d.sketch_text.stroke-20"),sQuery(id+"FHMxAyK4CFUKdhS_1.wireOp",EDGE,"1cb9c079-ea9b-4899-8069-e0e3048e911d.sketch_text.stroke-21"),sQuery(id+"FHMxAyK4CFUKdhS_1.wireOp",EDGE,"1cb9c079-ea9b-4899-8069-e0e3048e911d.sketch_text.stroke-22"),sQuery(id+"FHMxAyK4CFUKdhS_1.wireOp",EDGE,"1cb9c079-ea9b-4899-8069-e0e3048e911d.sketch_text.stroke-23"),sQuery(id+"FHMxAyK4CFUKdhS_1.wireOp",EDGE,"1cb9c079-ea9b-4899-8069-e0e3048e911d.sketch_text.stroke-24"),sQuery(id+"FHMxAyK4CFUKdhS_1.wireOp",EDGE,"1cb9c079-ea9b-4899-8069-e0e3048e911d.sketch_text.stroke-25"),sQuery(id+"FHMxAyK4CFUKdhS_1.wireOp",EDGE,"1cb9c079-ea9b-4899-8069-e0e3048e911d.sketch_text.stroke-26"),sQuery(id+"FHMxAyK4CFUKdhS_1.wireOp",EDGE,"1cb9c079-ea9b-4899-8069-e0e3048e911d.sketch_text.stroke-27"),sQuery(id+"FHMxAyK4CFUKdhS_1.wireOp",EDGE,"1cb9c079-ea9b-4899-8069-e0e3048e911d.sketch_text.stroke-28"),sQuery(id+"FHMxAyK4CFUKdhS_1.wireOp",EDGE,"1cb9c079-ea9b-4899-8069-e0e3048e911d.sketch_text.stroke-29"),sQuery(id+"FHMxAyK4CFUKdhS_1.wireOp",EDGE,"1cb9c079-ea9b-4899-8069-e0e3048e911d.sketch_text.stroke-30"),sQuery(id+"FHMxAyK4CFUKdhS_1.wireOp",EDGE,"1cb9c079-ea9b-4899-8069-e0e3048e911d.sketch_text.stroke-31"),sQuery(id+"FHMxAyK4CFUKdhS_1.wireOp",EDGE,"1cb9c079-ea9b-4899-8069-e0e3048e911d.sketch_text.stroke-32"),sQuery(id+"FHMxAyK4CFUKdhS_1.wireOp",EDGE,"1cb9c079-ea9b-4899-8069-e0e3048e911d.sketch_text.stroke-33"),sQuery(id+"FHMxAyK4CFUKdhS_1.wireOp",EDGE,"1cb9c079-ea9b-4899-8069-e0e3048e911d.sketch_text.stroke-34"),sQuery(id+"FHMxAyK4CFUKdhS_1.wireOp",EDGE,"1cb9c079-ea9b-4899-8069-e0e3048e911d.sketch_text.stroke-35"),sQuery(id+"FHMxAyK4CFUKdhS_1.wireOp",EDGE,"1cb9c079-ea9b-4899-8069-e0e3048e911d.sketch_text.stroke-36"),sQuery(id+"FHMxAyK4CFUKdhS_1.wireOp",EDGE,"1cb9c079-ea9b-4899-8069-e0e3048e911d.sketch_text.stroke-37"),sQuery(id+"FHMxAyK4CFUKdhS_1.wireOp",EDGE,"1cb9c079-ea9b-4899-8069-e0e3048e911d.sketch_text.stroke-38"),sQuery(id+"FHMxAyK4CFUKdhS_1.wireOp",EDGE,"1cb9c079-ea9b-4899-8069-e0e3048e911d.sketch_text.stroke-39"),sQuery(id+"FHMxAyK4CFUKdhS_1.wireOp",EDGE,"1cb9c079-ea9b-4899-8069-e0e3048e911d.sketch_text.stroke-40"),sQuery(id+"FHMxAyK4CFUKdhS_1.wireOp",EDGE,"1cb9c079-ea9b-4899-8069-e0e3048e911d.sketch_text.stroke-41"),sQuery(id+"FHMxAyK4CFUKdhS_1.wireOp",EDGE,"1cb9c079-ea9b-4899-8069-e0e3048e911d.sketch_text.stroke-42"),sQuery(id+"FHMxAyK4CFUKdhS_1.wireOp",EDGE,"1cb9c079-ea9b-4899-8069-e0e3048e911d.sketch_text.stroke-43"),sQuery(id+"FHMxAyK4CFUKdhS_1.wireOp",EDGE,"1cb9c079-ea9b-4899-8069-e0e3048e911d.sketch_text.stroke-44"),sQuery(id+"FHMxAyK4CFUKdhS_1.wireOp",EDGE,"1cb9c079-ea9b-4899-8069-e0e3048e911d.sketch_text.stroke-45"),sQuery(id+"FHMxAyK4CFUKdhS_1.wireOp",EDGE,"1cb9c079-ea9b-4899-8069-e0e3048e911d.sketch_text.stroke-46"),sQuery(id+"FHMxAyK4CFUKdhS_1.wireOp",EDGE,"1cb9c079-ea9b-4899-8069-e0e3048e911d.sketch_text.stroke-47"),sQuery(id+"FHMxAyK4CFUKdhS_1.wireOp",EDGE,"1cb9c079-ea9b-4899-8069-e0e3048e911d.sketch_text.stroke-48"),sQuery(id+"FHMxAyK4CFUKdhS_1.wireOp",EDGE,"1cb9c079-ea9b-4899-8069-e0e3048e911d.sketch_text.stroke-49"),sQuery(id+"FHMxAyK4CFUKdhS_1.wireOp",EDGE,"1cb9c079-ea9b-4899-8069-e0e3048e911d.sketch_text.stroke-50"),sQuery(id+"FHMxAyK4CFUKdhS_1.wireOp",EDGE,"1cb9c079-ea9b-4899-8069-e0e3048e911d.sketch_text.stroke-51"),sQuery(id+"FHMxAyK4CFUKdhS_1.wireOp",EDGE,"1cb9c079-ea9b-4899-8069-e0e3048e911d.sketch_text.stroke-52"),sQuery(id+"FHMxAyK4CFUKdhS_1.wireOp",EDGE,"1cb9c079-ea9b-4899-8069-e0e3048e911d.sketch_text.stroke-53"),sQuery(id+"FHMxAyK4CFUKdhS_1.wireOp",EDGE,"1cb9c079-ea9b-4899-8069-e0e3048e911d.sketch_text.stroke-54"),sQuery(id+"FHMxAyK4CFUKdhS_1.wireOp",EDGE,"1cb9c079-ea9b-4899-8069-e0e3048e911d.sketch_text.stroke-55"),sQuery(id+"FHMxAyK4CFUKdhS_1.wireOp",EDGE,"1cb9c079-ea9b-4899-8069-e0e3048e911d.sketch_text.stroke-56"),sQuery(id+"FHMxAyK4CFUKdhS_1.wireOp",EDGE,"1cb9c079-ea9b-4899-8069-e0e3048e911d.sketch_text.stroke-57"),sQuery(id+"FHMxAyK4CFUKdhS_1.wireOp",EDGE,"1cb9c079-ea9b-4899-8069-e0e3048e911d.sketch_text.stroke-58"),sQuery(id+"FHMxAyK4CFUKdhS_1.wireOp",EDGE,"1cb9c079-ea9b-4899-8069-e0e3048e911d.sketch_text.stroke-59"),sQuery(id+"FHMxAyK4CFUKdhS_1.wireOp",EDGE,"1cb9c079-ea9b-4899-8069-e0e3048e911d.sketch_text.stroke-60"),sQuery(id+"FHMxAyK4CFUKdhS_1.wireOp",EDGE,"1cb9c079-ea9b-4899-8069-e0e3048e911d.sketch_text.stroke-61"),sQuery(id+"FHMxAyK4CFUKdhS_1.wireOp",EDGE,"1cb9c079-ea9b-4899-8069-e0e3048e911d.sketch_text.stroke-62"),sQuery(id+"FHMxAyK4CFUKdhS_1.wireOp",EDGE,"1cb9c079-ea9b-4899-8069-e0e3048e911d.sketch_text.stroke-71"),sQuery(id+"FHMxAyK4CFUKdhS_1.wireOp",EDGE,"1cb9c079-ea9b-4899-8069-e0e3048e911d.sketch_text.stroke-72"),sQuery(id+"FHMxAyK4CFUKdhS_1.wireOp",EDGE,"1cb9c079-ea9b-4899-8069-e0e3048e911d.sketch_text.stroke-73"),sQuery(id+"FHMxAyK4CFUKdhS_1.wireOp",EDGE,"1cb9c079-ea9b-4899-8069-e0e3048e911d.sketch_text.stroke-74"),sQuery(id+"FHMxAyK4CFUKdhS_1.wireOp",EDGE,"1cb9c079-ea9b-4899-8069-e0e3048e911d.sketch_text.stroke-75"),sQuery(id+"FHMxAyK4CFUKdhS_1.wireOp",EDGE,"1cb9c079-ea9b-4899-8069-e0e3048e911d.sketch_text.stroke-76"),sQuery(id+"FHMxAyK4CFUKdhS_1.wireOp",EDGE,"1cb9c079-ea9b-4899-8069-e0e3048e911d.sketch_text.stroke-77"),sQuery(id+"FHMxAyK4CFUKdhS_1.wireOp",EDGE,"1cb9c079-ea9b-4899-8069-e0e3048e911d.sketch_text.stroke-78"),sQuery(id+"FHMxAyK4CFUKdhS_1.wireOp",EDGE,"1cb9c079-ea9b-4899-8069-e0e3048e911d.sketch_text.stroke-79"),sQuery(id+"FHMxAyK4CFUKdhS_1.wireOp",EDGE,"1cb9c079-ea9b-4899-8069-e0e3048e911d.sketch_text.stroke-80"),sQuery(id+"FHMxAyK4CFUKdhS_1.wireOp",EDGE,"1cb9c079-ea9b-4899-8069-e0e3048e911d.sketch_text.stroke-81"),sQuery(id+"FHMxAyK4CFUKdhS_1.wireOp",EDGE,"1cb9c079-ea9b-4899-8069-e0e3048e911d.sketch_text.stroke-82"),sQuery(id+"FHMxAyK4CFUKdhS_1.wireOp",EDGE,"1cb9c079-ea9b-4899-8069-e0e3048e911d.sketch_text.stroke-83"),sQuery(id+"FHMxAyK4CFUKdhS_1.wireOp",EDGE,"1cb9c079-ea9b-4899-8069-e0e3048e911d.sketch_text.stroke-84"),sQuery(id+"FHMxAyK4CFUKdhS_1.wireOp",EDGE,"1cb9c079-ea9b-4899-8069-e0e3048e911d.sketch_text.stroke-85"),sQuery(id+"FHMxAyK4CFUKdhS_1.wireOp",EDGE,"1cb9c079-ea9b-4899-8069-e0e3048e911d.sketch_text.stroke-86"),sQuery(id+"FHMxAyK4CFUKdhS_1.wireOp",EDGE,"1cb9c079-ea9b-4899-8069-e0e3048e911d.sketch_text.stroke-87"),sQuery(id+"FHMxAyK4CFUKdhS_1.wireOp",EDGE,"1cb9c079-ea9b-4899-8069-e0e3048e911d.sketch_text.stroke-88"),sQuery(id+"FHMxAyK4CFUKdhS_1.wireOp",EDGE,"1cb9c079-ea9b-4899-8069-e0e3048e911d.sketch_text.stroke-89"),sQuery(id+"FHMxAyK4CFUKdhS_1.wireOp",EDGE,"1cb9c079-ea9b-4899-8069-e0e3048e911d.sketch_text.stroke-90"),sQuery(id+"FHMxAyK4CFUKdhS_1.wireOp",EDGE,"1cb9c079-ea9b-4899-8069-e0e3048e911d.sketch_text.stroke-91"),sQuery(id+"FHMxAyK4CFUKdhS_1.wireOp",EDGE,"1cb9c079-ea9b-4899-8069-e0e3048e911d.sketch_text.stroke-92"),sQuery(id+"FHMxAyK4CFUKdhS_1.wireOp",EDGE,"1cb9c079-ea9b-4899-8069-e0e3048e911d.sketch_text.stroke-93"),sQuery(id+"FHMxAyK4CFUKdhS_1.wireOp",EDGE,"1cb9c079-ea9b-4899-8069-e0e3048e911d.sketch_text.stroke-94"),sQuery(id+"FHMxAyK4CFUKdhS_1.wireOp",EDGE,"1cb9c079-ea9b-4899-8069-e0e3048e911d.sketch_text.stroke-95"),sQuery(id+"FHMxAyK4CFUKdhS_1.wireOp",EDGE,"1cb9c079-ea9b-4899-8069-e0e3048e911d.sketch_text.stroke-96"),sQuery(id+"FHMxAyK4CFUKdhS_1.wireOp",EDGE,"1cb9c079-ea9b-4899-8069-e0e3048e911d.sketch_text.stroke-97"),sQuery(id+"FHMxAyK4CFUKdhS_1.wireOp",EDGE,"1cb9c079-ea9b-4899-8069-e0e3048e911d.sketch_text.stroke-103"),sQuery(id+"FHMxAyK4CFUKdhS_1.wireOp",EDGE,"1cb9c079-ea9b-4899-8069-e0e3048e911d.sketch_text.stroke-104"),sQuery(id+"FHMxAyK4CFUKdhS_1.wireOp",EDGE,"1cb9c079-ea9b-4899-8069-e0e3048e911d.sketch_text.stroke-105"),sQuery(id+"FHMxAyK4CFUKdhS_1.wireOp",EDGE,"1cb9c079-ea9b-4899-8069-e0e3048e911d.sketch_text.stroke-106"),sQuery(id+"FHMxAyK4CFUKdhS_1.wireOp",EDGE,"1cb9c079-ea9b-4899-8069-e0e3048e911d.sketch_text.stroke-107"),sQuery(id+"FHMxAyK4CFUKdhS_1.wireOp",EDGE,"1cb9c079-ea9b-4899-8069-e0e3048e911d.sketch_text.stroke-108"),sQuery(id+"FHMxAyK4CFUKdhS_1.wireOp",EDGE,"1cb9c079-ea9b-4899-8069-e0e3048e911d.sketch_text.stroke-109"),sQuery(id+"FHMxAyK4CFUKdhS_1.wireOp",EDGE,"1cb9c079-ea9b-4899-8069-e0e3048e911d.sketch_text.stroke-110"),sQuery(id+"FHMxAyK4CFUKdhS_1.wireOp",EDGE,"1cb9c079-ea9b-4899-8069-e0e3048e911d.sketch_text.stroke-111"),sQuery(id+"FHMxAyK4CFUKdhS_1.wireOp",EDGE,"1cb9c079-ea9b-4899-8069-e0e3048e911d.sketch_text.stroke-112"),sQuery(id+"FHMxAyK4CFUKdhS_1.wireOp",EDGE,"1cb9c079-ea9b-4899-8069-e0e3048e911d.sketch_text.stroke-113"),sQuery(id+"FHMxAyK4CFUKdhS_1.wireOp",EDGE,"1cb9c079-ea9b-4899-8069-e0e3048e911d.sketch_text.stroke-114"),sQuery(id+"FHMxAyK4CFUKdhS_1.wireOp",EDGE,"1cb9c079-ea9b-4899-8069-e0e3048e911d.sketch_text.stroke-115"),sQuery(id+"FHMxAyK4CFUKdhS_1.wireOp",EDGE,"1cb9c079-ea9b-4899-8069-e0e3048e911d.sketch_text.stroke-116"),sQuery(id+"FHMxAyK4CFUKdhS_1.wireOp",EDGE,"1cb9c079-ea9b-4899-8069-e0e3048e911d.sketch_text.stroke-117"),sQuery(id+"FHMxAyK4CFUKdhS_1.wireOp",EDGE,"1cb9c079-ea9b-4899-8069-e0e3048e911d.sketch_text.stroke-118"),sQuery(id+"FHMxAyK4CFUKdhS_1.wireOp",EDGE,"1cb9c079-ea9b-4899-8069-e0e3048e911d.sketch_text.stroke-119"),sQuery(id+"FHMxAyK4CFUKdhS_1.wireOp",EDGE,"1cb9c079-ea9b-4899-8069-e0e3048e911d.sketch_text.stroke-120"),sQuery(id+"FHMxAyK4CFUKdhS_1.wireOp",EDGE,"1cb9c079-ea9b-4899-8069-e0e3048e911d.sketch_text.stroke-121"),sQuery(id+"FHMxAyK4CFUKdhS_1.wireOp",EDGE,"1cb9c079-ea9b-4899-8069-e0e3048e911d.sketch_text.stroke-122"),sQuery(id+"FHMxAyK4CFUKdhS_1.wireOp",EDGE,"1cb9c079-ea9b-4899-8069-e0e3048e911d.sketch_text.stroke-123"),sQuery(id+"FHMxAyK4CFUKdhS_1.wireOp",EDGE,"1cb9c079-ea9b-4899-8069-e0e3048e911d.sketch_text.stroke-124"),sQuery(id+"FHMxAyK4CFUKdhS_1.wireOp",EDGE,"1cb9c079-ea9b-4899-8069-e0e3048e911d.sketch_text.stroke-125"),sQuery(id+"FHMxAyK4CFUKdhS_1.wireOp",EDGE,"1cb9c079-ea9b-4899-8069-e0e3048e911d.sketch_text.stroke-126"),sQuery(id+"FHMxAyK4CFUKdhS_1.wireOp",EDGE,"1cb9c079-ea9b-4899-8069-e0e3048e911d.sketch_text.stroke-127"),sQuery(id+"FHMxAyK4CFUKdhS_1.wireOp",EDGE,"1cb9c079-ea9b-4899-8069-e0e3048e911d.sketch_text.stroke-128"),sQuery(id+"FHMxAyK4CFUKdhS_1.wireOp",EDGE,"1cb9c079-ea9b-4899-8069-e0e3048e911d.sketch_text.stroke-129"),sQuery(id+"FHMxAyK4CFUKdhS_1.wireOp",EDGE,"1cb9c079-ea9b-4899-8069-e0e3048e911d.sketch_text.stroke-130"),sQuery(id+"FHMxAyK4CFUKdhS_1.wireOp",EDGE,"1cb9c079-ea9b-4899-8069-e0e3048e911d.sketch_text.stroke-131"),sQuery(id+"FHMxAyK4CFUKdhS_1.wireOp",EDGE,"1cb9c079-ea9b-4899-8069-e0e3048e911d.sketch_text.stroke-132"),sQuery(id+"FHMxAyK4CFUKdhS_1.wireOp",EDGE,"1cb9c079-ea9b-4899-8069-e0e3048e911d.sketch_text.stroke-133"),sQuery(id+"FHMxAyK4CFUKdhS_1.wireOp",EDGE,"1cb9c079-ea9b-4899-8069-e0e3048e911d.sketch_text.stroke-134"),sQuery(id+"FHMxAyK4CFUKdhS_1.wireOp",EDGE,"1cb9c079-ea9b-4899-8069-e0e3048e911d.sketch_text.stroke-135"),sQuery(id+"FHMxAyK4CFUKdhS_1.wireOp",EDGE,"1cb9c079-ea9b-4899-8069-e0e3048e911d.sketch_text.stroke-136"),sQuery(id+"FHMxAyK4CFUKdhS_1.wireOp",EDGE,"1cb9c079-ea9b-4899-8069-e0e3048e911d.sketch_text.stroke-137"),sQuery(id+"FHMxAyK4CFUKdhS_1.wireOp",EDGE,"1cb9c079-ea9b-4899-8069-e0e3048e911d.sketch_text.stroke-138"),sQuery(id+"FHMxAyK4CFUKdhS_1.wireOp",EDGE,"1cb9c079-ea9b-4899-8069-e0e3048e911d.sketch_text.stroke-139"),sQuery(id+"FHMxAyK4CFUKdhS_1.wireOp",EDGE,"1cb9c079-ea9b-4899-8069-e0e3048e911d.sketch_text.stroke-140"),sQuery(id+"FHMxAyK4CFUKdhS_1.wireOp",EDGE,"1cb9c079-ea9b-4899-8069-e0e3048e911d.sketch_text.stroke-141"),sQuery(id+"FHMxAyK4CFUKdhS_1.wireOp",EDGE,"1cb9c079-ea9b-4899-8069-e0e3048e911d.sketch_text.stroke-142"),sQuery(id+"FHMxAyK4CFUKdhS_1.wireOp",EDGE,"1cb9c079-ea9b-4899-8069-e0e3048e911d.sketch_text.stroke-143"),sQuery(id+"FHMxAyK4CFUKdhS_1.wireOp",EDGE,"1cb9c079-ea9b-4899-8069-e0e3048e911d.sketch_text.stroke-144"),sQuery(id+"FHMxAyK4CFUKdhS_1.wireOp",EDGE,"1cb9c079-ea9b-4899-8069-e0e3048e911d.sketch_text.stroke-145"),sQuery(id+"FHMxAyK4CFUKdhS_1.wireOp",EDGE,"1cb9c079-ea9b-4899-8069-e0e3048e911d.sketch_text.stroke-146"),sQuery(id+"FHMxAyK4CFUKdhS_1.wireOp",EDGE,"1cb9c079-ea9b-4899-8069-e0e3048e911d.sketch_text.stroke-147"),sQuery(id+"FHMxAyK4CFUKdhS_1.wireOp",EDGE,"1cb9c079-ea9b-4899-8069-e0e3048e911d.sketch_text.stroke-148"),sQuery(id+"FHMxAyK4CFUKdhS_1.wireOp",EDGE,"1cb9c079-ea9b-4899-8069-e0e3048e911d.sketch_text.stroke-149"),sQuery(id+"FHMxAyK4CFUKdhS_1.wireOp",EDGE,"1cb9c079-ea9b-4899-8069-e0e3048e911d.sketch_text.stroke-150"),sQuery(id+"FHMxAyK4CFUKdhS_1.wireOp",EDGE,"1cb9c079-ea9b-4899-8069-e0e3048e911d.sketch_text.stroke-151"),sQuery(id+"FHMxAyK4CFUKdhS_1.wireOp",EDGE,"1cb9c079-ea9b-4899-8069-e0e3048e911d.sketch_text.stroke-152"),sQuery(id+"FHMxAyK4CFUKdhS_1.wireOp",EDGE,"1cb9c079-ea9b-4899-8069-e0e3048e911d.sketch_text.stroke-153"),sQuery(id+"FHMxAyK4CFUKdhS_1.wireOp",EDGE,"1cb9c079-ea9b-4899-8069-e0e3048e911d.sketch_text.stroke-159"),sQuery(id+"FHMxAyK4CFUKdhS_1.wireOp",EDGE,"1cb9c079-ea9b-4899-8069-e0e3048e911d.sketch_text.stroke-160"),sQuery(id+"FHMxAyK4CFUKdhS_1.wireOp",EDGE,"1cb9c079-ea9b-4899-8069-e0e3048e911d.sketch_text.stroke-161"),sQuery(id+"FHMxAyK4CFUKdhS_1.wireOp",EDGE,"1cb9c079-ea9b-4899-8069-e0e3048e911d.sketch_text.stroke-162"),sQuery(id+"FHMxAyK4CFUKdhS_1.wireOp",EDGE,"1cb9c079-ea9b-4899-8069-e0e3048e911d.sketch_text.stroke-163"),sQuery(id+"FHMxAyK4CFUKdhS_1.wireOp",EDGE,"1cb9c079-ea9b-4899-8069-e0e3048e911d.sketch_text.stroke-164"),sQuery(id+"FHMxAyK4CFUKdhS_1.wireOp",EDGE,"1cb9c079-ea9b-4899-8069-e0e3048e911d.sketch_text.stroke-165"),sQuery(id+"FHMxAyK4CFUKdhS_1.wireOp",EDGE,"1cb9c079-ea9b-4899-8069-e0e3048e911d.sketch_text.stroke-166"),sQuery(id+"FHMxAyK4CFUKdhS_1.wireOp",EDGE,"1cb9c079-ea9b-4899-8069-e0e3048e911d.sketch_text.stroke-167"),sQuery(id+"FHMxAyK4CFUKdhS_1.wireOp",EDGE,"1cb9c079-ea9b-4899-8069-e0e3048e911d.sketch_text.stroke-168"),sQuery(id+"FHMxAyK4CFUKdhS_1.wireOp",EDGE,"1cb9c079-ea9b-4899-8069-e0e3048e911d.sketch_text.stroke-169"),sQuery(id+"FHMxAyK4CFUKdhS_1.wireOp",EDGE,"1cb9c079-ea9b-4899-8069-e0e3048e911d.sketch_text.stroke-170"),sQuery(id+"FHMxAyK4CFUKdhS_1.wireOp",EDGE,"1cb9c079-ea9b-4899-8069-e0e3048e911d.sketch_text.stroke-171"),sQuery(id+"FHMxAyK4CFUKdhS_1.wireOp",EDGE,"1cb9c079-ea9b-4899-8069-e0e3048e911d.sketch_text.stroke-172"),sQuery(id+"FHMxAyK4CFUKdhS_1.wireOp",EDGE,"1cb9c079-ea9b-4899-8069-e0e3048e911d.sketch_text.stroke-173"),sQuery(id+"FHMxAyK4CFUKdhS_1.wireOp",EDGE,"1cb9c079-ea9b-4899-8069-e0e3048e911d.sketch_text.stroke-174"),sQuery(id+"FHMxAyK4CFUKdhS_1.wireOp",EDGE,"1cb9c079-ea9b-4899-8069-e0e3048e911d.sketch_text.stroke-175"),sQuery(id+"FHMxAyK4CFUKdhS_1.wireOp",EDGE,"1cb9c079-ea9b-4899-8069-e0e3048e911d.sketch_text.stroke-176"),sQuery(id+"FHMxAyK4CFUKdhS_1.wireOp",EDGE,"1cb9c079-ea9b-4899-8069-e0e3048e911d.sketch_text.stroke-177"),sQuery(id+"FHMxAyK4CFUKdhS_1.wireOp",EDGE,"1cb9c079-ea9b-4899-8069-e0e3048e911d.sketch_text.stroke-178"),sQuery(id+"FHMxAyK4CFUKdhS_1.wireOp",EDGE,"1cb9c079-ea9b-4899-8069-e0e3048e911d.sketch_text.stroke-179"),sQuery(id+"FHMxAyK4CFUKdhS_1.wireOp",EDGE,"1cb9c079-ea9b-4899-8069-e0e3048e911d.sketch_text.stroke-180"),subQ0,subQ2])],"isStart":true}),makeQuery(id+"F4.opExtrude","SWEPT_FACE",FACE,{"disambiguationData":[OSD([subQ2])]})])],"derivedFrom":makeQuery(id+"F4.opExtrude","CAP_EDGE",EDGE,{"disambiguationData":[OSD([subQ2])],"isStart":true})});}
            var Q23;
            {var subQ0=sQuery(id+"F0.wireOp",EDGE,"E0.top");var subQ1=sQuery(id+"F0.wireOp",EDGE,"E0.bottom");var subQ2=sQuery(id+"F3.wireOp",EDGE,"E29");Q23=makeQuery(id+"F4.boolean.opBoolean","SPLIT",EDGE,{"disambiguationData":[TD([makeQuery(id+"F1.opExtrude","CAP_FACE",FACE,{"disambiguationData":[OSD([subQ1,subQ0,sQuery(id+"F0.wireOp",EDGE,"E0.left"),sQuery(id+"F0.wireOp",EDGE,"E0.right")])],"isStart":false}),makeQuery(id+"F1.opExtrude","SWEPT_FACE",FACE,{"disambiguationData":[OSD([subQ0])]}),makeQuery(id+"F4.opExtrude","CAP_FACE",FACE,{"disambiguationData":[OSD([subQ1,sQuery(id+"F2.wireOp",EDGE,"fcba4419-a2ee-464f-be9d-58f11bf3418b.sketch_text.stroke-0"),sQuery(id+"F2.wireOp",EDGE,"fcba4419-a2ee-464f-be9d-58f11bf3418b.sketch_text.stroke-1"),sQuery(id+"F2.wireOp",EDGE,"fcba4419-a2ee-464f-be9d-58f11bf3418b.sketch_text.stroke-2"),sQuery(id+"F2.wireOp",EDGE,"fcba4419-a2ee-464f-be9d-58f11bf3418b.sketch_text.stroke-3"),sQuery(id+"F2.wireOp",EDGE,"fcba4419-a2ee-464f-be9d-58f11bf3418b.sketch_text.stroke-4"),sQuery(id+"F2.wireOp",EDGE,"fcba4419-a2ee-464f-be9d-58f11bf3418b.sketch_text.stroke-5"),sQuery(id+"F2.wireOp",EDGE,"fcba4419-a2ee-464f-be9d-58f11bf3418b.sketch_text.stroke-6"),sQuery(id+"F2.wireOp",EDGE,"fcba4419-a2ee-464f-be9d-58f11bf3418b.sketch_text.stroke-7"),sQuery(id+"F2.wireOp",EDGE,"fcba4419-a2ee-464f-be9d-58f11bf3418b.sketch_text.stroke-8"),sQuery(id+"F2.wireOp",EDGE,"fcba4419-a2ee-464f-be9d-58f11bf3418b.sketch_text.stroke-9"),sQuery(id+"F2.wireOp",EDGE,"fcba4419-a2ee-464f-be9d-58f11bf3418b.sketch_text.stroke-10"),sQuery(id+"F2.wireOp",EDGE,"fcba4419-a2ee-464f-be9d-58f11bf3418b.sketch_text.stroke-11"),sQuery(id+"F2.wireOp",EDGE,"fcba4419-a2ee-464f-be9d-58f11bf3418b.sketch_text.stroke-12"),sQuery(id+"F2.wireOp",EDGE,"fcba4419-a2ee-464f-be9d-58f11bf3418b.sketch_text.stroke-13"),sQuery(id+"F2.wireOp",EDGE,"fcba4419-a2ee-464f-be9d-58f11bf3418b.sketch_text.stroke-14"),sQuery(id+"F2.wireOp",EDGE,"fcba4419-a2ee-464f-be9d-58f11bf3418b.sketch_text.stroke-15"),sQuery(id+"F2.wireOp",EDGE,"fcba4419-a2ee-464f-be9d-58f11bf3418b.sketch_text.stroke-16"),sQuery(id+"F2.wireOp",EDGE,"fcba4419-a2ee-464f-be9d-58f11bf3418b.sketch_text.stroke-17"),sQuery(id+"F2.wireOp",EDGE,"fcba4419-a2ee-464f-be9d-58f11bf3418b.sketch_text.stroke-18"),sQuery(id+"F2.wireOp",EDGE,"fcba4419-a2ee-464f-be9d-58f11bf3418b.sketch_text.stroke-19"),sQuery(id+"F2.wireOp",EDGE,"fcba4419-a2ee-464f-be9d-58f11bf3418b.sketch_text.stroke-20"),sQuery(id+"F2.wireOp",EDGE,"fcba4419-a2ee-464f-be9d-58f11bf3418b.sketch_text.stroke-21"),sQuery(id+"F2.wireOp",EDGE,"fcba4419-a2ee-464f-be9d-58f11bf3418b.sketch_text.stroke-22"),sQuery(id+"F2.wireOp",EDGE,"fcba4419-a2ee-464f-be9d-58f11bf3418b.sketch_text.stroke-23"),sQuery(id+"F2.wireOp",EDGE,"fcba4419-a2ee-464f-be9d-58f11bf3418b.sketch_text.stroke-24"),sQuery(id+"F2.wireOp",EDGE,"fcba4419-a2ee-464f-be9d-58f11bf3418b.sketch_text.stroke-25"),sQuery(id+"F2.wireOp",EDGE,"fcba4419-a2ee-464f-be9d-58f11bf3418b.sketch_text.stroke-26"),sQuery(id+"F2.wireOp",EDGE,"fcba4419-a2ee-464f-be9d-58f11bf3418b.sketch_text.stroke-27"),sQuery(id+"F2.wireOp",EDGE,"fcba4419-a2ee-464f-be9d-58f11bf3418b.sketch_text.stroke-28"),sQuery(id+"F2.wireOp",EDGE,"fcba4419-a2ee-464f-be9d-58f11bf3418b.sketch_text.stroke-29"),sQuery(id+"F2.wireOp",EDGE,"fcba4419-a2ee-464f-be9d-58f11bf3418b.sketch_text.stroke-30"),sQuery(id+"F2.wireOp",EDGE,"fcba4419-a2ee-464f-be9d-58f11bf3418b.sketch_text.stroke-31"),sQuery(id+"F2.wireOp",EDGE,"fcba4419-a2ee-464f-be9d-58f11bf3418b.sketch_text.stroke-32"),sQuery(id+"F2.wireOp",EDGE,"fcba4419-a2ee-464f-be9d-58f11bf3418b.sketch_text.stroke-33"),sQuery(id+"F2.wireOp",EDGE,"fcba4419-a2ee-464f-be9d-58f11bf3418b.sketch_text.stroke-34"),sQuery(id+"F2.wireOp",EDGE,"fcba4419-a2ee-464f-be9d-58f11bf3418b.sketch_text.stroke-35"),sQuery(id+"F2.wireOp",EDGE,"fcba4419-a2ee-464f-be9d-58f11bf3418b.sketch_text.stroke-36"),sQuery(id+"F2.wireOp",EDGE,"fcba4419-a2ee-464f-be9d-58f11bf3418b.sketch_text.stroke-37"),sQuery(id+"F2.wireOp",EDGE,"fcba4419-a2ee-464f-be9d-58f11bf3418b.sketch_text.stroke-38"),sQuery(id+"F2.wireOp",EDGE,"fcba4419-a2ee-464f-be9d-58f11bf3418b.sketch_text.stroke-39"),sQuery(id+"F2.wireOp",EDGE,"fcba4419-a2ee-464f-be9d-58f11bf3418b.sketch_text.stroke-40"),sQuery(id+"F2.wireOp",EDGE,"fcba4419-a2ee-464f-be9d-58f11bf3418b.sketch_text.stroke-41"),sQuery(id+"F2.wireOp",EDGE,"fcba4419-a2ee-464f-be9d-58f11bf3418b.sketch_text.stroke-42"),sQuery(id+"F2.wireOp",EDGE,"fcba4419-a2ee-464f-be9d-58f11bf3418b.sketch_text.stroke-43"),sQuery(id+"F2.wireOp",EDGE,"fcba4419-a2ee-464f-be9d-58f11bf3418b.sketch_text.stroke-44"),sQuery(id+"F2.wireOp",EDGE,"fcba4419-a2ee-464f-be9d-58f11bf3418b.sketch_text.stroke-45"),sQuery(id+"F2.wireOp",EDGE,"fcba4419-a2ee-464f-be9d-58f11bf3418b.sketch_text.stroke-46"),sQuery(id+"F2.wireOp",EDGE,"fcba4419-a2ee-464f-be9d-58f11bf3418b.sketch_text.stroke-47"),sQuery(id+"F2.wireOp",EDGE,"fcba4419-a2ee-464f-be9d-58f11bf3418b.sketch_text.stroke-48"),sQuery(id+"F2.wireOp",EDGE,"fcba4419-a2ee-464f-be9d-58f11bf3418b.sketch_text.stroke-49"),sQuery(id+"F2.wireOp",EDGE,"fcba4419-a2ee-464f-be9d-58f11bf3418b.sketch_text.stroke-50"),sQuery(id+"F2.wireOp",EDGE,"fcba4419-a2ee-464f-be9d-58f11bf3418b.sketch_text.stroke-51"),sQuery(id+"F2.wireOp",EDGE,"fcba4419-a2ee-464f-be9d-58f11bf3418b.sketch_text.stroke-52"),sQuery(id+"F2.wireOp",EDGE,"fcba4419-a2ee-464f-be9d-58f11bf3418b.sketch_text.stroke-53"),sQuery(id+"F2.wireOp",EDGE,"fcba4419-a2ee-464f-be9d-58f11bf3418b.sketch_text.stroke-54"),sQuery(id+"F2.wireOp",EDGE,"fcba4419-a2ee-464f-be9d-58f11bf3418b.sketch_text.stroke-55"),sQuery(id+"F2.wireOp",EDGE,"fcba4419-a2ee-464f-be9d-58f11bf3418b.sketch_text.stroke-56"),sQuery(id+"F2.wireOp",EDGE,"fcba4419-a2ee-464f-be9d-58f11bf3418b.sketch_text.stroke-57"),sQuery(id+"F2.wireOp",EDGE,"fcba4419-a2ee-464f-be9d-58f11bf3418b.sketch_text.stroke-58"),sQuery(id+"F2.wireOp",EDGE,"fcba4419-a2ee-464f-be9d-58f11bf3418b.sketch_text.stroke-59"),sQuery(id+"F2.wireOp",EDGE,"fcba4419-a2ee-464f-be9d-58f11bf3418b.sketch_text.stroke-60"),sQuery(id+"F2.wireOp",EDGE,"fcba4419-a2ee-464f-be9d-58f11bf3418b.sketch_text.stroke-61"),sQuery(id+"F2.wireOp",EDGE,"fcba4419-a2ee-464f-be9d-58f11bf3418b.sketch_text.stroke-62"),sQuery(id+"F2.wireOp",EDGE,"fcba4419-a2ee-464f-be9d-58f11bf3418b.sketch_text.stroke-63"),sQuery(id+"F2.wireOp",EDGE,"fcba4419-a2ee-464f-be9d-58f11bf3418b.sketch_text.stroke-64"),sQuery(id+"F2.wireOp",EDGE,"fcba4419-a2ee-464f-be9d-58f11bf3418b.sketch_text.stroke-65"),sQuery(id+"F2.wireOp",EDGE,"fcba4419-a2ee-464f-be9d-58f11bf3418b.sketch_text.stroke-66"),sQuery(id+"F2.wireOp",EDGE,"fcba4419-a2ee-464f-be9d-58f11bf3418b.sketch_text.stroke-67"),sQuery(id+"F2.wireOp",EDGE,"fcba4419-a2ee-464f-be9d-58f11bf3418b.sketch_text.stroke-68"),sQuery(id+"F2.wireOp",EDGE,"fcba4419-a2ee-464f-be9d-58f11bf3418b.sketch_text.stroke-69"),sQuery(id+"F2.wireOp",EDGE,"fcba4419-a2ee-464f-be9d-58f11bf3418b.sketch_text.stroke-70"),sQuery(id+"F2.wireOp",EDGE,"fcba4419-a2ee-464f-be9d-58f11bf3418b.sketch_text.stroke-71"),sQuery(id+"F2.wireOp",EDGE,"fcba4419-a2ee-464f-be9d-58f11bf3418b.sketch_text.stroke-72"),sQuery(id+"F2.wireOp",EDGE,"fcba4419-a2ee-464f-be9d-58f11bf3418b.sketch_text.stroke-73"),sQuery(id+"F2.wireOp",EDGE,"fcba4419-a2ee-464f-be9d-58f11bf3418b.sketch_text.stroke-74"),sQuery(id+"F2.wireOp",EDGE,"fcba4419-a2ee-464f-be9d-58f11bf3418b.sketch_text.stroke-75"),sQuery(id+"F2.wireOp",EDGE,"fcba4419-a2ee-464f-be9d-58f11bf3418b.sketch_text.stroke-76"),sQuery(id+"F2.wireOp",EDGE,"fcba4419-a2ee-464f-be9d-58f11bf3418b.sketch_text.stroke-77"),sQuery(id+"F2.wireOp",EDGE,"fcba4419-a2ee-464f-be9d-58f11bf3418b.sketch_text.stroke-78"),sQuery(id+"F2.wireOp",EDGE,"fcba4419-a2ee-464f-be9d-58f11bf3418b.sketch_text.stroke-79"),sQuery(id+"F2.wireOp",EDGE,"fcba4419-a2ee-464f-be9d-58f11bf3418b.sketch_text.stroke-80"),sQuery(id+"F2.wireOp",EDGE,"fcba4419-a2ee-464f-be9d-58f11bf3418b.sketch_text.stroke-81"),sQuery(id+"F2.wireOp",EDGE,"fcba4419-a2ee-464f-be9d-58f11bf3418b.sketch_text.stroke-82"),sQuery(id+"F2.wireOp",EDGE,"fcba4419-a2ee-464f-be9d-58f11bf3418b.sketch_text.stroke-83"),sQuery(id+"F2.wireOp",EDGE,"fcba4419-a2ee-464f-be9d-58f11bf3418b.sketch_text.stroke-84"),sQuery(id+"F2.wireOp",EDGE,"fcba4419-a2ee-464f-be9d-58f11bf3418b.sketch_text.stroke-85"),sQuery(id+"F2.wireOp",EDGE,"fcba4419-a2ee-464f-be9d-58f11bf3418b.sketch_text.stroke-86"),sQuery(id+"F2.wireOp",EDGE,"fcba4419-a2ee-464f-be9d-58f11bf3418b.sketch_text.stroke-87"),sQuery(id+"F2.wireOp",EDGE,"fcba4419-a2ee-464f-be9d-58f11bf3418b.sketch_text.stroke-88"),sQuery(id+"F2.wireOp",EDGE,"fcba4419-a2ee-464f-be9d-58f11bf3418b.sketch_text.stroke-89"),sQuery(id+"F2.wireOp",EDGE,"fcba4419-a2ee-464f-be9d-58f11bf3418b.sketch_text.stroke-90"),sQuery(id+"F2.wireOp",EDGE,"fcba4419-a2ee-464f-be9d-58f11bf3418b.sketch_text.stroke-91"),sQuery(id+"F2.wireOp",EDGE,"fcba4419-a2ee-464f-be9d-58f11bf3418b.sketch_text.stroke-92"),sQuery(id+"F2.wireOp",EDGE,"fcba4419-a2ee-464f-be9d-58f11bf3418b.sketch_text.stroke-93"),sQuery(id+"F2.wireOp",EDGE,"fcba4419-a2ee-464f-be9d-58f11bf3418b.sketch_text.stroke-94"),sQuery(id+"F2.wireOp",EDGE,"fcba4419-a2ee-464f-be9d-58f11bf3418b.sketch_text.stroke-95"),sQuery(id+"F2.wireOp",EDGE,"fcba4419-a2ee-464f-be9d-58f11bf3418b.sketch_text.stroke-96"),sQuery(id+"F2.wireOp",EDGE,"fcba4419-a2ee-464f-be9d-58f11bf3418b.sketch_text.stroke-97"),sQuery(id+"F2.wireOp",EDGE,"fcba4419-a2ee-464f-be9d-58f11bf3418b.sketch_text.stroke-98"),sQuery(id+"F2.wireOp",EDGE,"fcba4419-a2ee-464f-be9d-58f11bf3418b.sketch_text.stroke-99"),sQuery(id+"F2.wireOp",EDGE,"fcba4419-a2ee-464f-be9d-58f11bf3418b.sketch_text.stroke-100"),sQuery(id+"F2.wireOp",EDGE,"fcba4419-a2ee-464f-be9d-58f11bf3418b.sketch_text.stroke-101"),sQuery(id+"F2.wireOp",EDGE,"fcba4419-a2ee-464f-be9d-58f11bf3418b.sketch_text.stroke-102"),sQuery(id+"F2.wireOp",EDGE,"fcba4419-a2ee-464f-be9d-58f11bf3418b.sketch_text.stroke-103"),sQuery(id+"F2.wireOp",EDGE,"fcba4419-a2ee-464f-be9d-58f11bf3418b.sketch_text.stroke-104"),sQuery(id+"F2.wireOp",EDGE,"fcba4419-a2ee-464f-be9d-58f11bf3418b.sketch_text.stroke-105"),sQuery(id+"F2.wireOp",EDGE,"fcba4419-a2ee-464f-be9d-58f11bf3418b.sketch_text.stroke-106"),sQuery(id+"F2.wireOp",EDGE,"fcba4419-a2ee-464f-be9d-58f11bf3418b.sketch_text.stroke-107"),sQuery(id+"F2.wireOp",EDGE,"fcba4419-a2ee-464f-be9d-58f11bf3418b.sketch_text.stroke-108"),sQuery(id+"F2.wireOp",EDGE,"fcba4419-a2ee-464f-be9d-58f11bf3418b.sketch_text.stroke-109"),sQuery(id+"F2.wireOp",EDGE,"fcba4419-a2ee-464f-be9d-58f11bf3418b.sketch_text.stroke-110"),sQuery(id+"F2.wireOp",EDGE,"fcba4419-a2ee-464f-be9d-58f11bf3418b.sketch_text.stroke-111"),sQuery(id+"F2.wireOp",EDGE,"fcba4419-a2ee-464f-be9d-58f11bf3418b.sketch_text.stroke-112"),sQuery(id+"F2.wireOp",EDGE,"fcba4419-a2ee-464f-be9d-58f11bf3418b.sketch_text.stroke-113"),sQuery(id+"F2.wireOp",EDGE,"fcba4419-a2ee-464f-be9d-58f11bf3418b.sketch_text.stroke-114"),sQuery(id+"F2.wireOp",EDGE,"fcba4419-a2ee-464f-be9d-58f11bf3418b.sketch_text.stroke-115"),sQuery(id+"F2.wireOp",EDGE,"fcba4419-a2ee-464f-be9d-58f11bf3418b.sketch_text.stroke-116"),sQuery(id+"F2.wireOp",EDGE,"fcba4419-a2ee-464f-be9d-58f11bf3418b.sketch_text.stroke-117"),sQuery(id+"F2.wireOp",EDGE,"fcba4419-a2ee-464f-be9d-58f11bf3418b.sketch_text.stroke-118"),sQuery(id+"F2.wireOp",EDGE,"fcba4419-a2ee-464f-be9d-58f11bf3418b.sketch_text.stroke-119"),sQuery(id+"F2.wireOp",EDGE,"fcba4419-a2ee-464f-be9d-58f11bf3418b.sketch_text.stroke-120"),sQuery(id+"F2.wireOp",EDGE,"fcba4419-a2ee-464f-be9d-58f11bf3418b.sketch_text.stroke-121"),sQuery(id+"F2.wireOp",EDGE,"fcba4419-a2ee-464f-be9d-58f11bf3418b.sketch_text.stroke-122"),sQuery(id+"F2.wireOp",EDGE,"fcba4419-a2ee-464f-be9d-58f11bf3418b.sketch_text.stroke-123"),sQuery(id+"F2.wireOp",EDGE,"fcba4419-a2ee-464f-be9d-58f11bf3418b.sketch_text.stroke-124"),sQuery(id+"F2.wireOp",EDGE,"fcba4419-a2ee-464f-be9d-58f11bf3418b.sketch_text.stroke-125"),sQuery(id+"F2.wireOp",EDGE,"fcba4419-a2ee-464f-be9d-58f11bf3418b.sketch_text.stroke-126"),sQuery(id+"F2.wireOp",EDGE,"fcba4419-a2ee-464f-be9d-58f11bf3418b.sketch_text.stroke-127"),sQuery(id+"F2.wireOp",EDGE,"fcba4419-a2ee-464f-be9d-58f11bf3418b.sketch_text.stroke-128"),sQuery(id+"F2.wireOp",EDGE,"fcba4419-a2ee-464f-be9d-58f11bf3418b.sketch_text.stroke-129"),sQuery(id+"F2.wireOp",EDGE,"fcba4419-a2ee-464f-be9d-58f11bf3418b.sketch_text.stroke-130"),sQuery(id+"F2.wireOp",EDGE,"fcba4419-a2ee-464f-be9d-58f11bf3418b.sketch_text.stroke-131"),sQuery(id+"F2.wireOp",EDGE,"fcba4419-a2ee-464f-be9d-58f11bf3418b.sketch_text.stroke-132"),sQuery(id+"F2.wireOp",EDGE,"fcba4419-a2ee-464f-be9d-58f11bf3418b.sketch_text.stroke-133"),sQuery(id+"F2.wireOp",EDGE,"fcba4419-a2ee-464f-be9d-58f11bf3418b.sketch_text.stroke-134"),sQuery(id+"F2.wireOp",EDGE,"fcba4419-a2ee-464f-be9d-58f11bf3418b.sketch_text.stroke-135"),sQuery(id+"F2.wireOp",EDGE,"fcba4419-a2ee-464f-be9d-58f11bf3418b.sketch_text.stroke-136"),sQuery(id+"F2.wireOp",EDGE,"fcba4419-a2ee-464f-be9d-58f11bf3418b.sketch_text.stroke-137"),sQuery(id+"F2.wireOp",EDGE,"fcba4419-a2ee-464f-be9d-58f11bf3418b.sketch_text.stroke-138"),sQuery(id+"F2.wireOp",EDGE,"fcba4419-a2ee-464f-be9d-58f11bf3418b.sketch_text.stroke-139"),sQuery(id+"F2.wireOp",EDGE,"fcba4419-a2ee-464f-be9d-58f11bf3418b.sketch_text.stroke-140"),sQuery(id+"F2.wireOp",EDGE,"fcba4419-a2ee-464f-be9d-58f11bf3418b.sketch_text.stroke-141"),sQuery(id+"F2.wireOp",EDGE,"fcba4419-a2ee-464f-be9d-58f11bf3418b.sketch_text.stroke-142"),sQuery(id+"F2.wireOp",EDGE,"fcba4419-a2ee-464f-be9d-58f11bf3418b.sketch_text.stroke-143"),sQuery(id+"F2.wireOp",EDGE,"fcba4419-a2ee-464f-be9d-58f11bf3418b.sketch_text.stroke-144"),sQuery(id+"F2.wireOp",EDGE,"fcba4419-a2ee-464f-be9d-58f11bf3418b.sketch_text.stroke-145"),sQuery(id+"F2.wireOp",EDGE,"fcba4419-a2ee-464f-be9d-58f11bf3418b.sketch_text.stroke-146"),sQuery(id+"F2.wireOp",EDGE,"fcba4419-a2ee-464f-be9d-58f11bf3418b.sketch_text.stroke-147"),sQuery(id+"F2.wireOp",EDGE,"fcba4419-a2ee-464f-be9d-58f11bf3418b.sketch_text.stroke-148"),sQuery(id+"F2.wireOp",EDGE,"fcba4419-a2ee-464f-be9d-58f11bf3418b.sketch_text.stroke-149"),sQuery(id+"F2.wireOp",EDGE,"fcba4419-a2ee-464f-be9d-58f11bf3418b.sketch_text.stroke-150"),sQuery(id+"F2.wireOp",EDGE,"fcba4419-a2ee-464f-be9d-58f11bf3418b.sketch_text.stroke-151"),sQuery(id+"F2.wireOp",EDGE,"fcba4419-a2ee-464f-be9d-58f11bf3418b.sketch_text.stroke-152"),sQuery(id+"F2.wireOp",EDGE,"fcba4419-a2ee-464f-be9d-58f11bf3418b.sketch_text.stroke-153"),sQuery(id+"F2.wireOp",EDGE,"fcba4419-a2ee-464f-be9d-58f11bf3418b.sketch_text.stroke-154"),sQuery(id+"F2.wireOp",EDGE,"fcba4419-a2ee-464f-be9d-58f11bf3418b.sketch_text.stroke-155"),sQuery(id+"F2.wireOp",EDGE,"fcba4419-a2ee-464f-be9d-58f11bf3418b.sketch_text.stroke-156"),sQuery(id+"F2.wireOp",EDGE,"fcba4419-a2ee-464f-be9d-58f11bf3418b.sketch_text.stroke-157"),sQuery(id+"F2.wireOp",EDGE,"fcba4419-a2ee-464f-be9d-58f11bf3418b.sketch_text.stroke-158"),sQuery(id+"F2.wireOp",EDGE,"fcba4419-a2ee-464f-be9d-58f11bf3418b.sketch_text.stroke-159"),sQuery(id+"F2.wireOp",EDGE,"fcba4419-a2ee-464f-be9d-58f11bf3418b.sketch_text.stroke-160"),sQuery(id+"F2.wireOp",EDGE,"fcba4419-a2ee-464f-be9d-58f11bf3418b.sketch_text.stroke-161"),sQuery(id+"F2.wireOp",EDGE,"fcba4419-a2ee-464f-be9d-58f11bf3418b.sketch_text.stroke-162"),sQuery(id+"F2.wireOp",EDGE,"fcba4419-a2ee-464f-be9d-58f11bf3418b.sketch_text.stroke-163"),sQuery(id+"F2.wireOp",EDGE,"fcba4419-a2ee-464f-be9d-58f11bf3418b.sketch_text.stroke-164"),sQuery(id+"F2.wireOp",EDGE,"fcba4419-a2ee-464f-be9d-58f11bf3418b.sketch_text.stroke-165"),sQuery(id+"F2.wireOp",EDGE,"fcba4419-a2ee-464f-be9d-58f11bf3418b.sketch_text.stroke-166"),sQuery(id+"F2.wireOp",EDGE,"fcba4419-a2ee-464f-be9d-58f11bf3418b.sketch_text.stroke-167"),sQuery(id+"F2.wireOp",EDGE,"fcba4419-a2ee-464f-be9d-58f11bf3418b.sketch_text.stroke-168"),sQuery(id+"F2.wireOp",EDGE,"fcba4419-a2ee-464f-be9d-58f11bf3418b.sketch_text.stroke-169"),sQuery(id+"F2.wireOp",EDGE,"fcba4419-a2ee-464f-be9d-58f11bf3418b.sketch_text.stroke-170"),sQuery(id+"F2.wireOp",EDGE,"fcba4419-a2ee-464f-be9d-58f11bf3418b.sketch_text.stroke-171"),sQuery(id+"F2.wireOp",EDGE,"fcba4419-a2ee-464f-be9d-58f11bf3418b.sketch_text.stroke-172"),sQuery(id+"F2.wireOp",EDGE,"fcba4419-a2ee-464f-be9d-58f11bf3418b.sketch_text.stroke-173"),sQuery(id+"FHMxAyK4CFUKdhS_1.wireOp",EDGE,"1cb9c079-ea9b-4899-8069-e0e3048e911d.sketch_text.stroke-0"),sQuery(id+"FHMxAyK4CFUKdhS_1.wireOp",EDGE,"1cb9c079-ea9b-4899-8069-e0e3048e911d.sketch_text.stroke-1"),sQuery(id+"FHMxAyK4CFUKdhS_1.wireOp",EDGE,"1cb9c079-ea9b-4899-8069-e0e3048e911d.sketch_text.stroke-2"),sQuery(id+"FHMxAyK4CFUKdhS_1.wireOp",EDGE,"1cb9c079-ea9b-4899-8069-e0e3048e911d.sketch_text.stroke-3"),sQuery(id+"FHMxAyK4CFUKdhS_1.wireOp",EDGE,"1cb9c079-ea9b-4899-8069-e0e3048e911d.sketch_text.stroke-4"),sQuery(id+"FHMxAyK4CFUKdhS_1.wireOp",EDGE,"1cb9c079-ea9b-4899-8069-e0e3048e911d.sketch_text.stroke-5"),sQuery(id+"FHMxAyK4CFUKdhS_1.wireOp",EDGE,"1cb9c079-ea9b-4899-8069-e0e3048e911d.sketch_text.stroke-6"),sQuery(id+"FHMxAyK4CFUKdhS_1.wireOp",EDGE,"1cb9c079-ea9b-4899-8069-e0e3048e911d.sketch_text.stroke-7"),sQuery(id+"FHMxAyK4CFUKdhS_1.wireOp",EDGE,"1cb9c079-ea9b-4899-8069-e0e3048e911d.sketch_text.stroke-8"),sQuery(id+"FHMxAyK4CFUKdhS_1.wireOp",EDGE,"1cb9c079-ea9b-4899-8069-e0e3048e911d.sketch_text.stroke-9"),sQuery(id+"FHMxAyK4CFUKdhS_1.wireOp",EDGE,"1cb9c079-ea9b-4899-8069-e0e3048e911d.sketch_text.stroke-10"),sQuery(id+"FHMxAyK4CFUKdhS_1.wireOp",EDGE,"1cb9c079-ea9b-4899-8069-e0e3048e911d.sketch_text.stroke-11"),sQuery(id+"FHMxAyK4CFUKdhS_1.wireOp",EDGE,"1cb9c079-ea9b-4899-8069-e0e3048e911d.sketch_text.stroke-12"),sQuery(id+"FHMxAyK4CFUKdhS_1.wireOp",EDGE,"1cb9c079-ea9b-4899-8069-e0e3048e911d.sketch_text.stroke-13"),sQuery(id+"FHMxAyK4CFUKdhS_1.wireOp",EDGE,"1cb9c079-ea9b-4899-8069-e0e3048e911d.sketch_text.stroke-14"),sQuery(id+"FHMxAyK4CFUKdhS_1.wireOp",EDGE,"1cb9c079-ea9b-4899-8069-e0e3048e911d.sketch_text.stroke-15"),sQuery(id+"FHMxAyK4CFUKdhS_1.wireOp",EDGE,"1cb9c079-ea9b-4899-8069-e0e3048e911d.sketch_text.stroke-16"),sQuery(id+"FHMxAyK4CFUKdhS_1.wireOp",EDGE,"1cb9c079-ea9b-4899-8069-e0e3048e911d.sketch_text.stroke-17"),sQuery(id+"FHMxAyK4CFUKdhS_1.wireOp",EDGE,"1cb9c079-ea9b-4899-8069-e0e3048e911d.sketch_text.stroke-18"),sQuery(id+"FHMxAyK4CFUKdhS_1.wireOp",EDGE,"1cb9c079-ea9b-4899-8069-e0e3048e911d.sketch_text.stroke-19"),sQuery(id+"FHMxAyK4CFUKdhS_1.wireOp",EDGE,"1cb9c079-ea9b-4899-8069-e0e3048e911d.sketch_text.stroke-20"),sQuery(id+"FHMxAyK4CFUKdhS_1.wireOp",EDGE,"1cb9c079-ea9b-4899-8069-e0e3048e911d.sketch_text.stroke-21"),sQuery(id+"FHMxAyK4CFUKdhS_1.wireOp",EDGE,"1cb9c079-ea9b-4899-8069-e0e3048e911d.sketch_text.stroke-22"),sQuery(id+"FHMxAyK4CFUKdhS_1.wireOp",EDGE,"1cb9c079-ea9b-4899-8069-e0e3048e911d.sketch_text.stroke-23"),sQuery(id+"FHMxAyK4CFUKdhS_1.wireOp",EDGE,"1cb9c079-ea9b-4899-8069-e0e3048e911d.sketch_text.stroke-24"),sQuery(id+"FHMxAyK4CFUKdhS_1.wireOp",EDGE,"1cb9c079-ea9b-4899-8069-e0e3048e911d.sketch_text.stroke-25"),sQuery(id+"FHMxAyK4CFUKdhS_1.wireOp",EDGE,"1cb9c079-ea9b-4899-8069-e0e3048e911d.sketch_text.stroke-26"),sQuery(id+"FHMxAyK4CFUKdhS_1.wireOp",EDGE,"1cb9c079-ea9b-4899-8069-e0e3048e911d.sketch_text.stroke-27"),sQuery(id+"FHMxAyK4CFUKdhS_1.wireOp",EDGE,"1cb9c079-ea9b-4899-8069-e0e3048e911d.sketch_text.stroke-28"),sQuery(id+"FHMxAyK4CFUKdhS_1.wireOp",EDGE,"1cb9c079-ea9b-4899-8069-e0e3048e911d.sketch_text.stroke-29"),sQuery(id+"FHMxAyK4CFUKdhS_1.wireOp",EDGE,"1cb9c079-ea9b-4899-8069-e0e3048e911d.sketch_text.stroke-30"),sQuery(id+"FHMxAyK4CFUKdhS_1.wireOp",EDGE,"1cb9c079-ea9b-4899-8069-e0e3048e911d.sketch_text.stroke-31"),sQuery(id+"FHMxAyK4CFUKdhS_1.wireOp",EDGE,"1cb9c079-ea9b-4899-8069-e0e3048e911d.sketch_text.stroke-32"),sQuery(id+"FHMxAyK4CFUKdhS_1.wireOp",EDGE,"1cb9c079-ea9b-4899-8069-e0e3048e911d.sketch_text.stroke-33"),sQuery(id+"FHMxAyK4CFUKdhS_1.wireOp",EDGE,"1cb9c079-ea9b-4899-8069-e0e3048e911d.sketch_text.stroke-34"),sQuery(id+"FHMxAyK4CFUKdhS_1.wireOp",EDGE,"1cb9c079-ea9b-4899-8069-e0e3048e911d.sketch_text.stroke-35"),sQuery(id+"FHMxAyK4CFUKdhS_1.wireOp",EDGE,"1cb9c079-ea9b-4899-8069-e0e3048e911d.sketch_text.stroke-36"),sQuery(id+"FHMxAyK4CFUKdhS_1.wireOp",EDGE,"1cb9c079-ea9b-4899-8069-e0e3048e911d.sketch_text.stroke-37"),sQuery(id+"FHMxAyK4CFUKdhS_1.wireOp",EDGE,"1cb9c079-ea9b-4899-8069-e0e3048e911d.sketch_text.stroke-38"),sQuery(id+"FHMxAyK4CFUKdhS_1.wireOp",EDGE,"1cb9c079-ea9b-4899-8069-e0e3048e911d.sketch_text.stroke-39"),sQuery(id+"FHMxAyK4CFUKdhS_1.wireOp",EDGE,"1cb9c079-ea9b-4899-8069-e0e3048e911d.sketch_text.stroke-40"),sQuery(id+"FHMxAyK4CFUKdhS_1.wireOp",EDGE,"1cb9c079-ea9b-4899-8069-e0e3048e911d.sketch_text.stroke-41"),sQuery(id+"FHMxAyK4CFUKdhS_1.wireOp",EDGE,"1cb9c079-ea9b-4899-8069-e0e3048e911d.sketch_text.stroke-42"),sQuery(id+"FHMxAyK4CFUKdhS_1.wireOp",EDGE,"1cb9c079-ea9b-4899-8069-e0e3048e911d.sketch_text.stroke-43"),sQuery(id+"FHMxAyK4CFUKdhS_1.wireOp",EDGE,"1cb9c079-ea9b-4899-8069-e0e3048e911d.sketch_text.stroke-44"),sQuery(id+"FHMxAyK4CFUKdhS_1.wireOp",EDGE,"1cb9c079-ea9b-4899-8069-e0e3048e911d.sketch_text.stroke-45"),sQuery(id+"FHMxAyK4CFUKdhS_1.wireOp",EDGE,"1cb9c079-ea9b-4899-8069-e0e3048e911d.sketch_text.stroke-46"),sQuery(id+"FHMxAyK4CFUKdhS_1.wireOp",EDGE,"1cb9c079-ea9b-4899-8069-e0e3048e911d.sketch_text.stroke-47"),sQuery(id+"FHMxAyK4CFUKdhS_1.wireOp",EDGE,"1cb9c079-ea9b-4899-8069-e0e3048e911d.sketch_text.stroke-48"),sQuery(id+"FHMxAyK4CFUKdhS_1.wireOp",EDGE,"1cb9c079-ea9b-4899-8069-e0e3048e911d.sketch_text.stroke-49"),sQuery(id+"FHMxAyK4CFUKdhS_1.wireOp",EDGE,"1cb9c079-ea9b-4899-8069-e0e3048e911d.sketch_text.stroke-50"),sQuery(id+"FHMxAyK4CFUKdhS_1.wireOp",EDGE,"1cb9c079-ea9b-4899-8069-e0e3048e911d.sketch_text.stroke-51"),sQuery(id+"FHMxAyK4CFUKdhS_1.wireOp",EDGE,"1cb9c079-ea9b-4899-8069-e0e3048e911d.sketch_text.stroke-52"),sQuery(id+"FHMxAyK4CFUKdhS_1.wireOp",EDGE,"1cb9c079-ea9b-4899-8069-e0e3048e911d.sketch_text.stroke-53"),sQuery(id+"FHMxAyK4CFUKdhS_1.wireOp",EDGE,"1cb9c079-ea9b-4899-8069-e0e3048e911d.sketch_text.stroke-54"),sQuery(id+"FHMxAyK4CFUKdhS_1.wireOp",EDGE,"1cb9c079-ea9b-4899-8069-e0e3048e911d.sketch_text.stroke-55"),sQuery(id+"FHMxAyK4CFUKdhS_1.wireOp",EDGE,"1cb9c079-ea9b-4899-8069-e0e3048e911d.sketch_text.stroke-56"),sQuery(id+"FHMxAyK4CFUKdhS_1.wireOp",EDGE,"1cb9c079-ea9b-4899-8069-e0e3048e911d.sketch_text.stroke-57"),sQuery(id+"FHMxAyK4CFUKdhS_1.wireOp",EDGE,"1cb9c079-ea9b-4899-8069-e0e3048e911d.sketch_text.stroke-58"),sQuery(id+"FHMxAyK4CFUKdhS_1.wireOp",EDGE,"1cb9c079-ea9b-4899-8069-e0e3048e911d.sketch_text.stroke-59"),sQuery(id+"FHMxAyK4CFUKdhS_1.wireOp",EDGE,"1cb9c079-ea9b-4899-8069-e0e3048e911d.sketch_text.stroke-60"),sQuery(id+"FHMxAyK4CFUKdhS_1.wireOp",EDGE,"1cb9c079-ea9b-4899-8069-e0e3048e911d.sketch_text.stroke-61"),sQuery(id+"FHMxAyK4CFUKdhS_1.wireOp",EDGE,"1cb9c079-ea9b-4899-8069-e0e3048e911d.sketch_text.stroke-62"),sQuery(id+"FHMxAyK4CFUKdhS_1.wireOp",EDGE,"1cb9c079-ea9b-4899-8069-e0e3048e911d.sketch_text.stroke-71"),sQuery(id+"FHMxAyK4CFUKdhS_1.wireOp",EDGE,"1cb9c079-ea9b-4899-8069-e0e3048e911d.sketch_text.stroke-72"),sQuery(id+"FHMxAyK4CFUKdhS_1.wireOp",EDGE,"1cb9c079-ea9b-4899-8069-e0e3048e911d.sketch_text.stroke-73"),sQuery(id+"FHMxAyK4CFUKdhS_1.wireOp",EDGE,"1cb9c079-ea9b-4899-8069-e0e3048e911d.sketch_text.stroke-74"),sQuery(id+"FHMxAyK4CFUKdhS_1.wireOp",EDGE,"1cb9c079-ea9b-4899-8069-e0e3048e911d.sketch_text.stroke-75"),sQuery(id+"FHMxAyK4CFUKdhS_1.wireOp",EDGE,"1cb9c079-ea9b-4899-8069-e0e3048e911d.sketch_text.stroke-76"),sQuery(id+"FHMxAyK4CFUKdhS_1.wireOp",EDGE,"1cb9c079-ea9b-4899-8069-e0e3048e911d.sketch_text.stroke-77"),sQuery(id+"FHMxAyK4CFUKdhS_1.wireOp",EDGE,"1cb9c079-ea9b-4899-8069-e0e3048e911d.sketch_text.stroke-78"),sQuery(id+"FHMxAyK4CFUKdhS_1.wireOp",EDGE,"1cb9c079-ea9b-4899-8069-e0e3048e911d.sketch_text.stroke-79"),sQuery(id+"FHMxAyK4CFUKdhS_1.wireOp",EDGE,"1cb9c079-ea9b-4899-8069-e0e3048e911d.sketch_text.stroke-80"),sQuery(id+"FHMxAyK4CFUKdhS_1.wireOp",EDGE,"1cb9c079-ea9b-4899-8069-e0e3048e911d.sketch_text.stroke-81"),sQuery(id+"FHMxAyK4CFUKdhS_1.wireOp",EDGE,"1cb9c079-ea9b-4899-8069-e0e3048e911d.sketch_text.stroke-82"),sQuery(id+"FHMxAyK4CFUKdhS_1.wireOp",EDGE,"1cb9c079-ea9b-4899-8069-e0e3048e911d.sketch_text.stroke-83"),sQuery(id+"FHMxAyK4CFUKdhS_1.wireOp",EDGE,"1cb9c079-ea9b-4899-8069-e0e3048e911d.sketch_text.stroke-84"),sQuery(id+"FHMxAyK4CFUKdhS_1.wireOp",EDGE,"1cb9c079-ea9b-4899-8069-e0e3048e911d.sketch_text.stroke-85"),sQuery(id+"FHMxAyK4CFUKdhS_1.wireOp",EDGE,"1cb9c079-ea9b-4899-8069-e0e3048e911d.sketch_text.stroke-86"),sQuery(id+"FHMxAyK4CFUKdhS_1.wireOp",EDGE,"1cb9c079-ea9b-4899-8069-e0e3048e911d.sketch_text.stroke-87"),sQuery(id+"FHMxAyK4CFUKdhS_1.wireOp",EDGE,"1cb9c079-ea9b-4899-8069-e0e3048e911d.sketch_text.stroke-88"),sQuery(id+"FHMxAyK4CFUKdhS_1.wireOp",EDGE,"1cb9c079-ea9b-4899-8069-e0e3048e911d.sketch_text.stroke-89"),sQuery(id+"FHMxAyK4CFUKdhS_1.wireOp",EDGE,"1cb9c079-ea9b-4899-8069-e0e3048e911d.sketch_text.stroke-90"),sQuery(id+"FHMxAyK4CFUKdhS_1.wireOp",EDGE,"1cb9c079-ea9b-4899-8069-e0e3048e911d.sketch_text.stroke-91"),sQuery(id+"FHMxAyK4CFUKdhS_1.wireOp",EDGE,"1cb9c079-ea9b-4899-8069-e0e3048e911d.sketch_text.stroke-92"),sQuery(id+"FHMxAyK4CFUKdhS_1.wireOp",EDGE,"1cb9c079-ea9b-4899-8069-e0e3048e911d.sketch_text.stroke-93"),sQuery(id+"FHMxAyK4CFUKdhS_1.wireOp",EDGE,"1cb9c079-ea9b-4899-8069-e0e3048e911d.sketch_text.stroke-94"),sQuery(id+"FHMxAyK4CFUKdhS_1.wireOp",EDGE,"1cb9c079-ea9b-4899-8069-e0e3048e911d.sketch_text.stroke-95"),sQuery(id+"FHMxAyK4CFUKdhS_1.wireOp",EDGE,"1cb9c079-ea9b-4899-8069-e0e3048e911d.sketch_text.stroke-96"),sQuery(id+"FHMxAyK4CFUKdhS_1.wireOp",EDGE,"1cb9c079-ea9b-4899-8069-e0e3048e911d.sketch_text.stroke-97"),sQuery(id+"FHMxAyK4CFUKdhS_1.wireOp",EDGE,"1cb9c079-ea9b-4899-8069-e0e3048e911d.sketch_text.stroke-103"),sQuery(id+"FHMxAyK4CFUKdhS_1.wireOp",EDGE,"1cb9c079-ea9b-4899-8069-e0e3048e911d.sketch_text.stroke-104"),sQuery(id+"FHMxAyK4CFUKdhS_1.wireOp",EDGE,"1cb9c079-ea9b-4899-8069-e0e3048e911d.sketch_text.stroke-105"),sQuery(id+"FHMxAyK4CFUKdhS_1.wireOp",EDGE,"1cb9c079-ea9b-4899-8069-e0e3048e911d.sketch_text.stroke-106"),sQuery(id+"FHMxAyK4CFUKdhS_1.wireOp",EDGE,"1cb9c079-ea9b-4899-8069-e0e3048e911d.sketch_text.stroke-107"),sQuery(id+"FHMxAyK4CFUKdhS_1.wireOp",EDGE,"1cb9c079-ea9b-4899-8069-e0e3048e911d.sketch_text.stroke-108"),sQuery(id+"FHMxAyK4CFUKdhS_1.wireOp",EDGE,"1cb9c079-ea9b-4899-8069-e0e3048e911d.sketch_text.stroke-109"),sQuery(id+"FHMxAyK4CFUKdhS_1.wireOp",EDGE,"1cb9c079-ea9b-4899-8069-e0e3048e911d.sketch_text.stroke-110"),sQuery(id+"FHMxAyK4CFUKdhS_1.wireOp",EDGE,"1cb9c079-ea9b-4899-8069-e0e3048e911d.sketch_text.stroke-111"),sQuery(id+"FHMxAyK4CFUKdhS_1.wireOp",EDGE,"1cb9c079-ea9b-4899-8069-e0e3048e911d.sketch_text.stroke-112"),sQuery(id+"FHMxAyK4CFUKdhS_1.wireOp",EDGE,"1cb9c079-ea9b-4899-8069-e0e3048e911d.sketch_text.stroke-113"),sQuery(id+"FHMxAyK4CFUKdhS_1.wireOp",EDGE,"1cb9c079-ea9b-4899-8069-e0e3048e911d.sketch_text.stroke-114"),sQuery(id+"FHMxAyK4CFUKdhS_1.wireOp",EDGE,"1cb9c079-ea9b-4899-8069-e0e3048e911d.sketch_text.stroke-115"),sQuery(id+"FHMxAyK4CFUKdhS_1.wireOp",EDGE,"1cb9c079-ea9b-4899-8069-e0e3048e911d.sketch_text.stroke-116"),sQuery(id+"FHMxAyK4CFUKdhS_1.wireOp",EDGE,"1cb9c079-ea9b-4899-8069-e0e3048e911d.sketch_text.stroke-117"),sQuery(id+"FHMxAyK4CFUKdhS_1.wireOp",EDGE,"1cb9c079-ea9b-4899-8069-e0e3048e911d.sketch_text.stroke-118"),sQuery(id+"FHMxAyK4CFUKdhS_1.wireOp",EDGE,"1cb9c079-ea9b-4899-8069-e0e3048e911d.sketch_text.stroke-119"),sQuery(id+"FHMxAyK4CFUKdhS_1.wireOp",EDGE,"1cb9c079-ea9b-4899-8069-e0e3048e911d.sketch_text.stroke-120"),sQuery(id+"FHMxAyK4CFUKdhS_1.wireOp",EDGE,"1cb9c079-ea9b-4899-8069-e0e3048e911d.sketch_text.stroke-121"),sQuery(id+"FHMxAyK4CFUKdhS_1.wireOp",EDGE,"1cb9c079-ea9b-4899-8069-e0e3048e911d.sketch_text.stroke-122"),sQuery(id+"FHMxAyK4CFUKdhS_1.wireOp",EDGE,"1cb9c079-ea9b-4899-8069-e0e3048e911d.sketch_text.stroke-123"),sQuery(id+"FHMxAyK4CFUKdhS_1.wireOp",EDGE,"1cb9c079-ea9b-4899-8069-e0e3048e911d.sketch_text.stroke-124"),sQuery(id+"FHMxAyK4CFUKdhS_1.wireOp",EDGE,"1cb9c079-ea9b-4899-8069-e0e3048e911d.sketch_text.stroke-125"),sQuery(id+"FHMxAyK4CFUKdhS_1.wireOp",EDGE,"1cb9c079-ea9b-4899-8069-e0e3048e911d.sketch_text.stroke-126"),sQuery(id+"FHMxAyK4CFUKdhS_1.wireOp",EDGE,"1cb9c079-ea9b-4899-8069-e0e3048e911d.sketch_text.stroke-127"),sQuery(id+"FHMxAyK4CFUKdhS_1.wireOp",EDGE,"1cb9c079-ea9b-4899-8069-e0e3048e911d.sketch_text.stroke-128"),sQuery(id+"FHMxAyK4CFUKdhS_1.wireOp",EDGE,"1cb9c079-ea9b-4899-8069-e0e3048e911d.sketch_text.stroke-129"),sQuery(id+"FHMxAyK4CFUKdhS_1.wireOp",EDGE,"1cb9c079-ea9b-4899-8069-e0e3048e911d.sketch_text.stroke-130"),sQuery(id+"FHMxAyK4CFUKdhS_1.wireOp",EDGE,"1cb9c079-ea9b-4899-8069-e0e3048e911d.sketch_text.stroke-131"),sQuery(id+"FHMxAyK4CFUKdhS_1.wireOp",EDGE,"1cb9c079-ea9b-4899-8069-e0e3048e911d.sketch_text.stroke-132"),sQuery(id+"FHMxAyK4CFUKdhS_1.wireOp",EDGE,"1cb9c079-ea9b-4899-8069-e0e3048e911d.sketch_text.stroke-133"),sQuery(id+"FHMxAyK4CFUKdhS_1.wireOp",EDGE,"1cb9c079-ea9b-4899-8069-e0e3048e911d.sketch_text.stroke-134"),sQuery(id+"FHMxAyK4CFUKdhS_1.wireOp",EDGE,"1cb9c079-ea9b-4899-8069-e0e3048e911d.sketch_text.stroke-135"),sQuery(id+"FHMxAyK4CFUKdhS_1.wireOp",EDGE,"1cb9c079-ea9b-4899-8069-e0e3048e911d.sketch_text.stroke-136"),sQuery(id+"FHMxAyK4CFUKdhS_1.wireOp",EDGE,"1cb9c079-ea9b-4899-8069-e0e3048e911d.sketch_text.stroke-137"),sQuery(id+"FHMxAyK4CFUKdhS_1.wireOp",EDGE,"1cb9c079-ea9b-4899-8069-e0e3048e911d.sketch_text.stroke-138"),sQuery(id+"FHMxAyK4CFUKdhS_1.wireOp",EDGE,"1cb9c079-ea9b-4899-8069-e0e3048e911d.sketch_text.stroke-139"),sQuery(id+"FHMxAyK4CFUKdhS_1.wireOp",EDGE,"1cb9c079-ea9b-4899-8069-e0e3048e911d.sketch_text.stroke-140"),sQuery(id+"FHMxAyK4CFUKdhS_1.wireOp",EDGE,"1cb9c079-ea9b-4899-8069-e0e3048e911d.sketch_text.stroke-141"),sQuery(id+"FHMxAyK4CFUKdhS_1.wireOp",EDGE,"1cb9c079-ea9b-4899-8069-e0e3048e911d.sketch_text.stroke-142"),sQuery(id+"FHMxAyK4CFUKdhS_1.wireOp",EDGE,"1cb9c079-ea9b-4899-8069-e0e3048e911d.sketch_text.stroke-143"),sQuery(id+"FHMxAyK4CFUKdhS_1.wireOp",EDGE,"1cb9c079-ea9b-4899-8069-e0e3048e911d.sketch_text.stroke-144"),sQuery(id+"FHMxAyK4CFUKdhS_1.wireOp",EDGE,"1cb9c079-ea9b-4899-8069-e0e3048e911d.sketch_text.stroke-145"),sQuery(id+"FHMxAyK4CFUKdhS_1.wireOp",EDGE,"1cb9c079-ea9b-4899-8069-e0e3048e911d.sketch_text.stroke-146"),sQuery(id+"FHMxAyK4CFUKdhS_1.wireOp",EDGE,"1cb9c079-ea9b-4899-8069-e0e3048e911d.sketch_text.stroke-147"),sQuery(id+"FHMxAyK4CFUKdhS_1.wireOp",EDGE,"1cb9c079-ea9b-4899-8069-e0e3048e911d.sketch_text.stroke-148"),sQuery(id+"FHMxAyK4CFUKdhS_1.wireOp",EDGE,"1cb9c079-ea9b-4899-8069-e0e3048e911d.sketch_text.stroke-149"),sQuery(id+"FHMxAyK4CFUKdhS_1.wireOp",EDGE,"1cb9c079-ea9b-4899-8069-e0e3048e911d.sketch_text.stroke-150"),sQuery(id+"FHMxAyK4CFUKdhS_1.wireOp",EDGE,"1cb9c079-ea9b-4899-8069-e0e3048e911d.sketch_text.stroke-151"),sQuery(id+"FHMxAyK4CFUKdhS_1.wireOp",EDGE,"1cb9c079-ea9b-4899-8069-e0e3048e911d.sketch_text.stroke-152"),sQuery(id+"FHMxAyK4CFUKdhS_1.wireOp",EDGE,"1cb9c079-ea9b-4899-8069-e0e3048e911d.sketch_text.stroke-153"),sQuery(id+"FHMxAyK4CFUKdhS_1.wireOp",EDGE,"1cb9c079-ea9b-4899-8069-e0e3048e911d.sketch_text.stroke-159"),sQuery(id+"FHMxAyK4CFUKdhS_1.wireOp",EDGE,"1cb9c079-ea9b-4899-8069-e0e3048e911d.sketch_text.stroke-160"),sQuery(id+"FHMxAyK4CFUKdhS_1.wireOp",EDGE,"1cb9c079-ea9b-4899-8069-e0e3048e911d.sketch_text.stroke-161"),sQuery(id+"FHMxAyK4CFUKdhS_1.wireOp",EDGE,"1cb9c079-ea9b-4899-8069-e0e3048e911d.sketch_text.stroke-162"),sQuery(id+"FHMxAyK4CFUKdhS_1.wireOp",EDGE,"1cb9c079-ea9b-4899-8069-e0e3048e911d.sketch_text.stroke-163"),sQuery(id+"FHMxAyK4CFUKdhS_1.wireOp",EDGE,"1cb9c079-ea9b-4899-8069-e0e3048e911d.sketch_text.stroke-164"),sQuery(id+"FHMxAyK4CFUKdhS_1.wireOp",EDGE,"1cb9c079-ea9b-4899-8069-e0e3048e911d.sketch_text.stroke-165"),sQuery(id+"FHMxAyK4CFUKdhS_1.wireOp",EDGE,"1cb9c079-ea9b-4899-8069-e0e3048e911d.sketch_text.stroke-166"),sQuery(id+"FHMxAyK4CFUKdhS_1.wireOp",EDGE,"1cb9c079-ea9b-4899-8069-e0e3048e911d.sketch_text.stroke-167"),sQuery(id+"FHMxAyK4CFUKdhS_1.wireOp",EDGE,"1cb9c079-ea9b-4899-8069-e0e3048e911d.sketch_text.stroke-168"),sQuery(id+"FHMxAyK4CFUKdhS_1.wireOp",EDGE,"1cb9c079-ea9b-4899-8069-e0e3048e911d.sketch_text.stroke-169"),sQuery(id+"FHMxAyK4CFUKdhS_1.wireOp",EDGE,"1cb9c079-ea9b-4899-8069-e0e3048e911d.sketch_text.stroke-170"),sQuery(id+"FHMxAyK4CFUKdhS_1.wireOp",EDGE,"1cb9c079-ea9b-4899-8069-e0e3048e911d.sketch_text.stroke-171"),sQuery(id+"FHMxAyK4CFUKdhS_1.wireOp",EDGE,"1cb9c079-ea9b-4899-8069-e0e3048e911d.sketch_text.stroke-172"),sQuery(id+"FHMxAyK4CFUKdhS_1.wireOp",EDGE,"1cb9c079-ea9b-4899-8069-e0e3048e911d.sketch_text.stroke-173"),sQuery(id+"FHMxAyK4CFUKdhS_1.wireOp",EDGE,"1cb9c079-ea9b-4899-8069-e0e3048e911d.sketch_text.stroke-174"),sQuery(id+"FHMxAyK4CFUKdhS_1.wireOp",EDGE,"1cb9c079-ea9b-4899-8069-e0e3048e911d.sketch_text.stroke-175"),sQuery(id+"FHMxAyK4CFUKdhS_1.wireOp",EDGE,"1cb9c079-ea9b-4899-8069-e0e3048e911d.sketch_text.stroke-176"),sQuery(id+"FHMxAyK4CFUKdhS_1.wireOp",EDGE,"1cb9c079-ea9b-4899-8069-e0e3048e911d.sketch_text.stroke-177"),sQuery(id+"FHMxAyK4CFUKdhS_1.wireOp",EDGE,"1cb9c079-ea9b-4899-8069-e0e3048e911d.sketch_text.stroke-178"),sQuery(id+"FHMxAyK4CFUKdhS_1.wireOp",EDGE,"1cb9c079-ea9b-4899-8069-e0e3048e911d.sketch_text.stroke-179"),sQuery(id+"FHMxAyK4CFUKdhS_1.wireOp",EDGE,"1cb9c079-ea9b-4899-8069-e0e3048e911d.sketch_text.stroke-180"),sQuery(id+"F3.wireOp",EDGE,"E28"),subQ2])],"isStart":true}),makeQuery(id+"F4.opExtrude","SWEPT_FACE",FACE,{"disambiguationData":[OSD([subQ2])]})])],"derivedFrom":makeQuery(id+"F4.opExtrude","CAP_EDGE",EDGE,{"disambiguationData":[OSD([subQ2])],"isStart":true})});}
            var Q24;
            {var subQ0=sQuery(id+"F0.wireOp",EDGE,"E0.top");var subQ1=sQuery(id+"F0.wireOp",EDGE,"E0.bottom");var subQ2=sQuery(id+"F3.wireOp",EDGE,"E28");Q24=makeQuery(id+"F4.boolean.opBoolean","SPLIT",EDGE,{"disambiguationData":[TD([makeQuery(id+"F1.opExtrude","CAP_FACE",FACE,{"disambiguationData":[OSD([subQ1,subQ0,sQuery(id+"F0.wireOp",EDGE,"E0.left"),sQuery(id+"F0.wireOp",EDGE,"E0.right")])],"isStart":false}),makeQuery(id+"F1.opExtrude","SWEPT_FACE",FACE,{"disambiguationData":[OSD([subQ0])]}),makeQuery(id+"F4.opExtrude","SWEPT_FACE",FACE,{"disambiguationData":[OSD([subQ2])]}),makeQuery(id+"F4.opExtrude","CAP_FACE",FACE,{"disambiguationData":[OSD([subQ1,sQuery(id+"F2.wireOp",EDGE,"fcba4419-a2ee-464f-be9d-58f11bf3418b.sketch_text.stroke-0"),sQuery(id+"F2.wireOp",EDGE,"fcba4419-a2ee-464f-be9d-58f11bf3418b.sketch_text.stroke-1"),sQuery(id+"F2.wireOp",EDGE,"fcba4419-a2ee-464f-be9d-58f11bf3418b.sketch_text.stroke-2"),sQuery(id+"F2.wireOp",EDGE,"fcba4419-a2ee-464f-be9d-58f11bf3418b.sketch_text.stroke-3"),sQuery(id+"F2.wireOp",EDGE,"fcba4419-a2ee-464f-be9d-58f11bf3418b.sketch_text.stroke-4"),sQuery(id+"F2.wireOp",EDGE,"fcba4419-a2ee-464f-be9d-58f11bf3418b.sketch_text.stroke-5"),sQuery(id+"F2.wireOp",EDGE,"fcba4419-a2ee-464f-be9d-58f11bf3418b.sketch_text.stroke-6"),sQuery(id+"F2.wireOp",EDGE,"fcba4419-a2ee-464f-be9d-58f11bf3418b.sketch_text.stroke-7"),sQuery(id+"F2.wireOp",EDGE,"fcba4419-a2ee-464f-be9d-58f11bf3418b.sketch_text.stroke-8"),sQuery(id+"F2.wireOp",EDGE,"fcba4419-a2ee-464f-be9d-58f11bf3418b.sketch_text.stroke-9"),sQuery(id+"F2.wireOp",EDGE,"fcba4419-a2ee-464f-be9d-58f11bf3418b.sketch_text.stroke-10"),sQuery(id+"F2.wireOp",EDGE,"fcba4419-a2ee-464f-be9d-58f11bf3418b.sketch_text.stroke-11"),sQuery(id+"F2.wireOp",EDGE,"fcba4419-a2ee-464f-be9d-58f11bf3418b.sketch_text.stroke-12"),sQuery(id+"F2.wireOp",EDGE,"fcba4419-a2ee-464f-be9d-58f11bf3418b.sketch_text.stroke-13"),sQuery(id+"F2.wireOp",EDGE,"fcba4419-a2ee-464f-be9d-58f11bf3418b.sketch_text.stroke-14"),sQuery(id+"F2.wireOp",EDGE,"fcba4419-a2ee-464f-be9d-58f11bf3418b.sketch_text.stroke-15"),sQuery(id+"F2.wireOp",EDGE,"fcba4419-a2ee-464f-be9d-58f11bf3418b.sketch_text.stroke-16"),sQuery(id+"F2.wireOp",EDGE,"fcba4419-a2ee-464f-be9d-58f11bf3418b.sketch_text.stroke-17"),sQuery(id+"F2.wireOp",EDGE,"fcba4419-a2ee-464f-be9d-58f11bf3418b.sketch_text.stroke-18"),sQuery(id+"F2.wireOp",EDGE,"fcba4419-a2ee-464f-be9d-58f11bf3418b.sketch_text.stroke-19"),sQuery(id+"F2.wireOp",EDGE,"fcba4419-a2ee-464f-be9d-58f11bf3418b.sketch_text.stroke-20"),sQuery(id+"F2.wireOp",EDGE,"fcba4419-a2ee-464f-be9d-58f11bf3418b.sketch_text.stroke-21"),sQuery(id+"F2.wireOp",EDGE,"fcba4419-a2ee-464f-be9d-58f11bf3418b.sketch_text.stroke-22"),sQuery(id+"F2.wireOp",EDGE,"fcba4419-a2ee-464f-be9d-58f11bf3418b.sketch_text.stroke-23"),sQuery(id+"F2.wireOp",EDGE,"fcba4419-a2ee-464f-be9d-58f11bf3418b.sketch_text.stroke-24"),sQuery(id+"F2.wireOp",EDGE,"fcba4419-a2ee-464f-be9d-58f11bf3418b.sketch_text.stroke-25"),sQuery(id+"F2.wireOp",EDGE,"fcba4419-a2ee-464f-be9d-58f11bf3418b.sketch_text.stroke-26"),sQuery(id+"F2.wireOp",EDGE,"fcba4419-a2ee-464f-be9d-58f11bf3418b.sketch_text.stroke-27"),sQuery(id+"F2.wireOp",EDGE,"fcba4419-a2ee-464f-be9d-58f11bf3418b.sketch_text.stroke-28"),sQuery(id+"F2.wireOp",EDGE,"fcba4419-a2ee-464f-be9d-58f11bf3418b.sketch_text.stroke-29"),sQuery(id+"F2.wireOp",EDGE,"fcba4419-a2ee-464f-be9d-58f11bf3418b.sketch_text.stroke-30"),sQuery(id+"F2.wireOp",EDGE,"fcba4419-a2ee-464f-be9d-58f11bf3418b.sketch_text.stroke-31"),sQuery(id+"F2.wireOp",EDGE,"fcba4419-a2ee-464f-be9d-58f11bf3418b.sketch_text.stroke-32"),sQuery(id+"F2.wireOp",EDGE,"fcba4419-a2ee-464f-be9d-58f11bf3418b.sketch_text.stroke-33"),sQuery(id+"F2.wireOp",EDGE,"fcba4419-a2ee-464f-be9d-58f11bf3418b.sketch_text.stroke-34"),sQuery(id+"F2.wireOp",EDGE,"fcba4419-a2ee-464f-be9d-58f11bf3418b.sketch_text.stroke-35"),sQuery(id+"F2.wireOp",EDGE,"fcba4419-a2ee-464f-be9d-58f11bf3418b.sketch_text.stroke-36"),sQuery(id+"F2.wireOp",EDGE,"fcba4419-a2ee-464f-be9d-58f11bf3418b.sketch_text.stroke-37"),sQuery(id+"F2.wireOp",EDGE,"fcba4419-a2ee-464f-be9d-58f11bf3418b.sketch_text.stroke-38"),sQuery(id+"F2.wireOp",EDGE,"fcba4419-a2ee-464f-be9d-58f11bf3418b.sketch_text.stroke-39"),sQuery(id+"F2.wireOp",EDGE,"fcba4419-a2ee-464f-be9d-58f11bf3418b.sketch_text.stroke-40"),sQuery(id+"F2.wireOp",EDGE,"fcba4419-a2ee-464f-be9d-58f11bf3418b.sketch_text.stroke-41"),sQuery(id+"F2.wireOp",EDGE,"fcba4419-a2ee-464f-be9d-58f11bf3418b.sketch_text.stroke-42"),sQuery(id+"F2.wireOp",EDGE,"fcba4419-a2ee-464f-be9d-58f11bf3418b.sketch_text.stroke-43"),sQuery(id+"F2.wireOp",EDGE,"fcba4419-a2ee-464f-be9d-58f11bf3418b.sketch_text.stroke-44"),sQuery(id+"F2.wireOp",EDGE,"fcba4419-a2ee-464f-be9d-58f11bf3418b.sketch_text.stroke-45"),sQuery(id+"F2.wireOp",EDGE,"fcba4419-a2ee-464f-be9d-58f11bf3418b.sketch_text.stroke-46"),sQuery(id+"F2.wireOp",EDGE,"fcba4419-a2ee-464f-be9d-58f11bf3418b.sketch_text.stroke-47"),sQuery(id+"F2.wireOp",EDGE,"fcba4419-a2ee-464f-be9d-58f11bf3418b.sketch_text.stroke-48"),sQuery(id+"F2.wireOp",EDGE,"fcba4419-a2ee-464f-be9d-58f11bf3418b.sketch_text.stroke-49"),sQuery(id+"F2.wireOp",EDGE,"fcba4419-a2ee-464f-be9d-58f11bf3418b.sketch_text.stroke-50"),sQuery(id+"F2.wireOp",EDGE,"fcba4419-a2ee-464f-be9d-58f11bf3418b.sketch_text.stroke-51"),sQuery(id+"F2.wireOp",EDGE,"fcba4419-a2ee-464f-be9d-58f11bf3418b.sketch_text.stroke-52"),sQuery(id+"F2.wireOp",EDGE,"fcba4419-a2ee-464f-be9d-58f11bf3418b.sketch_text.stroke-53"),sQuery(id+"F2.wireOp",EDGE,"fcba4419-a2ee-464f-be9d-58f11bf3418b.sketch_text.stroke-54"),sQuery(id+"F2.wireOp",EDGE,"fcba4419-a2ee-464f-be9d-58f11bf3418b.sketch_text.stroke-55"),sQuery(id+"F2.wireOp",EDGE,"fcba4419-a2ee-464f-be9d-58f11bf3418b.sketch_text.stroke-56"),sQuery(id+"F2.wireOp",EDGE,"fcba4419-a2ee-464f-be9d-58f11bf3418b.sketch_text.stroke-57"),sQuery(id+"F2.wireOp",EDGE,"fcba4419-a2ee-464f-be9d-58f11bf3418b.sketch_text.stroke-58"),sQuery(id+"F2.wireOp",EDGE,"fcba4419-a2ee-464f-be9d-58f11bf3418b.sketch_text.stroke-59"),sQuery(id+"F2.wireOp",EDGE,"fcba4419-a2ee-464f-be9d-58f11bf3418b.sketch_text.stroke-60"),sQuery(id+"F2.wireOp",EDGE,"fcba4419-a2ee-464f-be9d-58f11bf3418b.sketch_text.stroke-61"),sQuery(id+"F2.wireOp",EDGE,"fcba4419-a2ee-464f-be9d-58f11bf3418b.sketch_text.stroke-62"),sQuery(id+"F2.wireOp",EDGE,"fcba4419-a2ee-464f-be9d-58f11bf3418b.sketch_text.stroke-63"),sQuery(id+"F2.wireOp",EDGE,"fcba4419-a2ee-464f-be9d-58f11bf3418b.sketch_text.stroke-64"),sQuery(id+"F2.wireOp",EDGE,"fcba4419-a2ee-464f-be9d-58f11bf3418b.sketch_text.stroke-65"),sQuery(id+"F2.wireOp",EDGE,"fcba4419-a2ee-464f-be9d-58f11bf3418b.sketch_text.stroke-66"),sQuery(id+"F2.wireOp",EDGE,"fcba4419-a2ee-464f-be9d-58f11bf3418b.sketch_text.stroke-67"),sQuery(id+"F2.wireOp",EDGE,"fcba4419-a2ee-464f-be9d-58f11bf3418b.sketch_text.stroke-68"),sQuery(id+"F2.wireOp",EDGE,"fcba4419-a2ee-464f-be9d-58f11bf3418b.sketch_text.stroke-69"),sQuery(id+"F2.wireOp",EDGE,"fcba4419-a2ee-464f-be9d-58f11bf3418b.sketch_text.stroke-70"),sQuery(id+"F2.wireOp",EDGE,"fcba4419-a2ee-464f-be9d-58f11bf3418b.sketch_text.stroke-71"),sQuery(id+"F2.wireOp",EDGE,"fcba4419-a2ee-464f-be9d-58f11bf3418b.sketch_text.stroke-72"),sQuery(id+"F2.wireOp",EDGE,"fcba4419-a2ee-464f-be9d-58f11bf3418b.sketch_text.stroke-73"),sQuery(id+"F2.wireOp",EDGE,"fcba4419-a2ee-464f-be9d-58f11bf3418b.sketch_text.stroke-74"),sQuery(id+"F2.wireOp",EDGE,"fcba4419-a2ee-464f-be9d-58f11bf3418b.sketch_text.stroke-75"),sQuery(id+"F2.wireOp",EDGE,"fcba4419-a2ee-464f-be9d-58f11bf3418b.sketch_text.stroke-76"),sQuery(id+"F2.wireOp",EDGE,"fcba4419-a2ee-464f-be9d-58f11bf3418b.sketch_text.stroke-77"),sQuery(id+"F2.wireOp",EDGE,"fcba4419-a2ee-464f-be9d-58f11bf3418b.sketch_text.stroke-78"),sQuery(id+"F2.wireOp",EDGE,"fcba4419-a2ee-464f-be9d-58f11bf3418b.sketch_text.stroke-79"),sQuery(id+"F2.wireOp",EDGE,"fcba4419-a2ee-464f-be9d-58f11bf3418b.sketch_text.stroke-80"),sQuery(id+"F2.wireOp",EDGE,"fcba4419-a2ee-464f-be9d-58f11bf3418b.sketch_text.stroke-81"),sQuery(id+"F2.wireOp",EDGE,"fcba4419-a2ee-464f-be9d-58f11bf3418b.sketch_text.stroke-82"),sQuery(id+"F2.wireOp",EDGE,"fcba4419-a2ee-464f-be9d-58f11bf3418b.sketch_text.stroke-83"),sQuery(id+"F2.wireOp",EDGE,"fcba4419-a2ee-464f-be9d-58f11bf3418b.sketch_text.stroke-84"),sQuery(id+"F2.wireOp",EDGE,"fcba4419-a2ee-464f-be9d-58f11bf3418b.sketch_text.stroke-85"),sQuery(id+"F2.wireOp",EDGE,"fcba4419-a2ee-464f-be9d-58f11bf3418b.sketch_text.stroke-86"),sQuery(id+"F2.wireOp",EDGE,"fcba4419-a2ee-464f-be9d-58f11bf3418b.sketch_text.stroke-87"),sQuery(id+"F2.wireOp",EDGE,"fcba4419-a2ee-464f-be9d-58f11bf3418b.sketch_text.stroke-88"),sQuery(id+"F2.wireOp",EDGE,"fcba4419-a2ee-464f-be9d-58f11bf3418b.sketch_text.stroke-89"),sQuery(id+"F2.wireOp",EDGE,"fcba4419-a2ee-464f-be9d-58f11bf3418b.sketch_text.stroke-90"),sQuery(id+"F2.wireOp",EDGE,"fcba4419-a2ee-464f-be9d-58f11bf3418b.sketch_text.stroke-91"),sQuery(id+"F2.wireOp",EDGE,"fcba4419-a2ee-464f-be9d-58f11bf3418b.sketch_text.stroke-92"),sQuery(id+"F2.wireOp",EDGE,"fcba4419-a2ee-464f-be9d-58f11bf3418b.sketch_text.stroke-93"),sQuery(id+"F2.wireOp",EDGE,"fcba4419-a2ee-464f-be9d-58f11bf3418b.sketch_text.stroke-94"),sQuery(id+"F2.wireOp",EDGE,"fcba4419-a2ee-464f-be9d-58f11bf3418b.sketch_text.stroke-95"),sQuery(id+"F2.wireOp",EDGE,"fcba4419-a2ee-464f-be9d-58f11bf3418b.sketch_text.stroke-96"),sQuery(id+"F2.wireOp",EDGE,"fcba4419-a2ee-464f-be9d-58f11bf3418b.sketch_text.stroke-97"),sQuery(id+"F2.wireOp",EDGE,"fcba4419-a2ee-464f-be9d-58f11bf3418b.sketch_text.stroke-98"),sQuery(id+"F2.wireOp",EDGE,"fcba4419-a2ee-464f-be9d-58f11bf3418b.sketch_text.stroke-99"),sQuery(id+"F2.wireOp",EDGE,"fcba4419-a2ee-464f-be9d-58f11bf3418b.sketch_text.stroke-100"),sQuery(id+"F2.wireOp",EDGE,"fcba4419-a2ee-464f-be9d-58f11bf3418b.sketch_text.stroke-101"),sQuery(id+"F2.wireOp",EDGE,"fcba4419-a2ee-464f-be9d-58f11bf3418b.sketch_text.stroke-102"),sQuery(id+"F2.wireOp",EDGE,"fcba4419-a2ee-464f-be9d-58f11bf3418b.sketch_text.stroke-103"),sQuery(id+"F2.wireOp",EDGE,"fcba4419-a2ee-464f-be9d-58f11bf3418b.sketch_text.stroke-104"),sQuery(id+"F2.wireOp",EDGE,"fcba4419-a2ee-464f-be9d-58f11bf3418b.sketch_text.stroke-105"),sQuery(id+"F2.wireOp",EDGE,"fcba4419-a2ee-464f-be9d-58f11bf3418b.sketch_text.stroke-106"),sQuery(id+"F2.wireOp",EDGE,"fcba4419-a2ee-464f-be9d-58f11bf3418b.sketch_text.stroke-107"),sQuery(id+"F2.wireOp",EDGE,"fcba4419-a2ee-464f-be9d-58f11bf3418b.sketch_text.stroke-108"),sQuery(id+"F2.wireOp",EDGE,"fcba4419-a2ee-464f-be9d-58f11bf3418b.sketch_text.stroke-109"),sQuery(id+"F2.wireOp",EDGE,"fcba4419-a2ee-464f-be9d-58f11bf3418b.sketch_text.stroke-110"),sQuery(id+"F2.wireOp",EDGE,"fcba4419-a2ee-464f-be9d-58f11bf3418b.sketch_text.stroke-111"),sQuery(id+"F2.wireOp",EDGE,"fcba4419-a2ee-464f-be9d-58f11bf3418b.sketch_text.stroke-112"),sQuery(id+"F2.wireOp",EDGE,"fcba4419-a2ee-464f-be9d-58f11bf3418b.sketch_text.stroke-113"),sQuery(id+"F2.wireOp",EDGE,"fcba4419-a2ee-464f-be9d-58f11bf3418b.sketch_text.stroke-114"),sQuery(id+"F2.wireOp",EDGE,"fcba4419-a2ee-464f-be9d-58f11bf3418b.sketch_text.stroke-115"),sQuery(id+"F2.wireOp",EDGE,"fcba4419-a2ee-464f-be9d-58f11bf3418b.sketch_text.stroke-116"),sQuery(id+"F2.wireOp",EDGE,"fcba4419-a2ee-464f-be9d-58f11bf3418b.sketch_text.stroke-117"),sQuery(id+"F2.wireOp",EDGE,"fcba4419-a2ee-464f-be9d-58f11bf3418b.sketch_text.stroke-118"),sQuery(id+"F2.wireOp",EDGE,"fcba4419-a2ee-464f-be9d-58f11bf3418b.sketch_text.stroke-119"),sQuery(id+"F2.wireOp",EDGE,"fcba4419-a2ee-464f-be9d-58f11bf3418b.sketch_text.stroke-120"),sQuery(id+"F2.wireOp",EDGE,"fcba4419-a2ee-464f-be9d-58f11bf3418b.sketch_text.stroke-121"),sQuery(id+"F2.wireOp",EDGE,"fcba4419-a2ee-464f-be9d-58f11bf3418b.sketch_text.stroke-122"),sQuery(id+"F2.wireOp",EDGE,"fcba4419-a2ee-464f-be9d-58f11bf3418b.sketch_text.stroke-123"),sQuery(id+"F2.wireOp",EDGE,"fcba4419-a2ee-464f-be9d-58f11bf3418b.sketch_text.stroke-124"),sQuery(id+"F2.wireOp",EDGE,"fcba4419-a2ee-464f-be9d-58f11bf3418b.sketch_text.stroke-125"),sQuery(id+"F2.wireOp",EDGE,"fcba4419-a2ee-464f-be9d-58f11bf3418b.sketch_text.stroke-126"),sQuery(id+"F2.wireOp",EDGE,"fcba4419-a2ee-464f-be9d-58f11bf3418b.sketch_text.stroke-127"),sQuery(id+"F2.wireOp",EDGE,"fcba4419-a2ee-464f-be9d-58f11bf3418b.sketch_text.stroke-128"),sQuery(id+"F2.wireOp",EDGE,"fcba4419-a2ee-464f-be9d-58f11bf3418b.sketch_text.stroke-129"),sQuery(id+"F2.wireOp",EDGE,"fcba4419-a2ee-464f-be9d-58f11bf3418b.sketch_text.stroke-130"),sQuery(id+"F2.wireOp",EDGE,"fcba4419-a2ee-464f-be9d-58f11bf3418b.sketch_text.stroke-131"),sQuery(id+"F2.wireOp",EDGE,"fcba4419-a2ee-464f-be9d-58f11bf3418b.sketch_text.stroke-132"),sQuery(id+"F2.wireOp",EDGE,"fcba4419-a2ee-464f-be9d-58f11bf3418b.sketch_text.stroke-133"),sQuery(id+"F2.wireOp",EDGE,"fcba4419-a2ee-464f-be9d-58f11bf3418b.sketch_text.stroke-134"),sQuery(id+"F2.wireOp",EDGE,"fcba4419-a2ee-464f-be9d-58f11bf3418b.sketch_text.stroke-135"),sQuery(id+"F2.wireOp",EDGE,"fcba4419-a2ee-464f-be9d-58f11bf3418b.sketch_text.stroke-136"),sQuery(id+"F2.wireOp",EDGE,"fcba4419-a2ee-464f-be9d-58f11bf3418b.sketch_text.stroke-137"),sQuery(id+"F2.wireOp",EDGE,"fcba4419-a2ee-464f-be9d-58f11bf3418b.sketch_text.stroke-138"),sQuery(id+"F2.wireOp",EDGE,"fcba4419-a2ee-464f-be9d-58f11bf3418b.sketch_text.stroke-139"),sQuery(id+"F2.wireOp",EDGE,"fcba4419-a2ee-464f-be9d-58f11bf3418b.sketch_text.stroke-140"),sQuery(id+"F2.wireOp",EDGE,"fcba4419-a2ee-464f-be9d-58f11bf3418b.sketch_text.stroke-141"),sQuery(id+"F2.wireOp",EDGE,"fcba4419-a2ee-464f-be9d-58f11bf3418b.sketch_text.stroke-142"),sQuery(id+"F2.wireOp",EDGE,"fcba4419-a2ee-464f-be9d-58f11bf3418b.sketch_text.stroke-143"),sQuery(id+"F2.wireOp",EDGE,"fcba4419-a2ee-464f-be9d-58f11bf3418b.sketch_text.stroke-144"),sQuery(id+"F2.wireOp",EDGE,"fcba4419-a2ee-464f-be9d-58f11bf3418b.sketch_text.stroke-145"),sQuery(id+"F2.wireOp",EDGE,"fcba4419-a2ee-464f-be9d-58f11bf3418b.sketch_text.stroke-146"),sQuery(id+"F2.wireOp",EDGE,"fcba4419-a2ee-464f-be9d-58f11bf3418b.sketch_text.stroke-147"),sQuery(id+"F2.wireOp",EDGE,"fcba4419-a2ee-464f-be9d-58f11bf3418b.sketch_text.stroke-148"),sQuery(id+"F2.wireOp",EDGE,"fcba4419-a2ee-464f-be9d-58f11bf3418b.sketch_text.stroke-149"),sQuery(id+"F2.wireOp",EDGE,"fcba4419-a2ee-464f-be9d-58f11bf3418b.sketch_text.stroke-150"),sQuery(id+"F2.wireOp",EDGE,"fcba4419-a2ee-464f-be9d-58f11bf3418b.sketch_text.stroke-151"),sQuery(id+"F2.wireOp",EDGE,"fcba4419-a2ee-464f-be9d-58f11bf3418b.sketch_text.stroke-152"),sQuery(id+"F2.wireOp",EDGE,"fcba4419-a2ee-464f-be9d-58f11bf3418b.sketch_text.stroke-153"),sQuery(id+"F2.wireOp",EDGE,"fcba4419-a2ee-464f-be9d-58f11bf3418b.sketch_text.stroke-154"),sQuery(id+"F2.wireOp",EDGE,"fcba4419-a2ee-464f-be9d-58f11bf3418b.sketch_text.stroke-155"),sQuery(id+"F2.wireOp",EDGE,"fcba4419-a2ee-464f-be9d-58f11bf3418b.sketch_text.stroke-156"),sQuery(id+"F2.wireOp",EDGE,"fcba4419-a2ee-464f-be9d-58f11bf3418b.sketch_text.stroke-157"),sQuery(id+"F2.wireOp",EDGE,"fcba4419-a2ee-464f-be9d-58f11bf3418b.sketch_text.stroke-158"),sQuery(id+"F2.wireOp",EDGE,"fcba4419-a2ee-464f-be9d-58f11bf3418b.sketch_text.stroke-159"),sQuery(id+"F2.wireOp",EDGE,"fcba4419-a2ee-464f-be9d-58f11bf3418b.sketch_text.stroke-160"),sQuery(id+"F2.wireOp",EDGE,"fcba4419-a2ee-464f-be9d-58f11bf3418b.sketch_text.stroke-161"),sQuery(id+"F2.wireOp",EDGE,"fcba4419-a2ee-464f-be9d-58f11bf3418b.sketch_text.stroke-162"),sQuery(id+"F2.wireOp",EDGE,"fcba4419-a2ee-464f-be9d-58f11bf3418b.sketch_text.stroke-163"),sQuery(id+"F2.wireOp",EDGE,"fcba4419-a2ee-464f-be9d-58f11bf3418b.sketch_text.stroke-164"),sQuery(id+"F2.wireOp",EDGE,"fcba4419-a2ee-464f-be9d-58f11bf3418b.sketch_text.stroke-165"),sQuery(id+"F2.wireOp",EDGE,"fcba4419-a2ee-464f-be9d-58f11bf3418b.sketch_text.stroke-166"),sQuery(id+"F2.wireOp",EDGE,"fcba4419-a2ee-464f-be9d-58f11bf3418b.sketch_text.stroke-167"),sQuery(id+"F2.wireOp",EDGE,"fcba4419-a2ee-464f-be9d-58f11bf3418b.sketch_text.stroke-168"),sQuery(id+"F2.wireOp",EDGE,"fcba4419-a2ee-464f-be9d-58f11bf3418b.sketch_text.stroke-169"),sQuery(id+"F2.wireOp",EDGE,"fcba4419-a2ee-464f-be9d-58f11bf3418b.sketch_text.stroke-170"),sQuery(id+"F2.wireOp",EDGE,"fcba4419-a2ee-464f-be9d-58f11bf3418b.sketch_text.stroke-171"),sQuery(id+"F2.wireOp",EDGE,"fcba4419-a2ee-464f-be9d-58f11bf3418b.sketch_text.stroke-172"),sQuery(id+"F2.wireOp",EDGE,"fcba4419-a2ee-464f-be9d-58f11bf3418b.sketch_text.stroke-173"),sQuery(id+"FHMxAyK4CFUKdhS_1.wireOp",EDGE,"1cb9c079-ea9b-4899-8069-e0e3048e911d.sketch_text.stroke-0"),sQuery(id+"FHMxAyK4CFUKdhS_1.wireOp",EDGE,"1cb9c079-ea9b-4899-8069-e0e3048e911d.sketch_text.stroke-1"),sQuery(id+"FHMxAyK4CFUKdhS_1.wireOp",EDGE,"1cb9c079-ea9b-4899-8069-e0e3048e911d.sketch_text.stroke-2"),sQuery(id+"FHMxAyK4CFUKdhS_1.wireOp",EDGE,"1cb9c079-ea9b-4899-8069-e0e3048e911d.sketch_text.stroke-3"),sQuery(id+"FHMxAyK4CFUKdhS_1.wireOp",EDGE,"1cb9c079-ea9b-4899-8069-e0e3048e911d.sketch_text.stroke-4"),sQuery(id+"FHMxAyK4CFUKdhS_1.wireOp",EDGE,"1cb9c079-ea9b-4899-8069-e0e3048e911d.sketch_text.stroke-5"),sQuery(id+"FHMxAyK4CFUKdhS_1.wireOp",EDGE,"1cb9c079-ea9b-4899-8069-e0e3048e911d.sketch_text.stroke-6"),sQuery(id+"FHMxAyK4CFUKdhS_1.wireOp",EDGE,"1cb9c079-ea9b-4899-8069-e0e3048e911d.sketch_text.stroke-7"),sQuery(id+"FHMxAyK4CFUKdhS_1.wireOp",EDGE,"1cb9c079-ea9b-4899-8069-e0e3048e911d.sketch_text.stroke-8"),sQuery(id+"FHMxAyK4CFUKdhS_1.wireOp",EDGE,"1cb9c079-ea9b-4899-8069-e0e3048e911d.sketch_text.stroke-9"),sQuery(id+"FHMxAyK4CFUKdhS_1.wireOp",EDGE,"1cb9c079-ea9b-4899-8069-e0e3048e911d.sketch_text.stroke-10"),sQuery(id+"FHMxAyK4CFUKdhS_1.wireOp",EDGE,"1cb9c079-ea9b-4899-8069-e0e3048e911d.sketch_text.stroke-11"),sQuery(id+"FHMxAyK4CFUKdhS_1.wireOp",EDGE,"1cb9c079-ea9b-4899-8069-e0e3048e911d.sketch_text.stroke-12"),sQuery(id+"FHMxAyK4CFUKdhS_1.wireOp",EDGE,"1cb9c079-ea9b-4899-8069-e0e3048e911d.sketch_text.stroke-13"),sQuery(id+"FHMxAyK4CFUKdhS_1.wireOp",EDGE,"1cb9c079-ea9b-4899-8069-e0e3048e911d.sketch_text.stroke-14"),sQuery(id+"FHMxAyK4CFUKdhS_1.wireOp",EDGE,"1cb9c079-ea9b-4899-8069-e0e3048e911d.sketch_text.stroke-15"),sQuery(id+"FHMxAyK4CFUKdhS_1.wireOp",EDGE,"1cb9c079-ea9b-4899-8069-e0e3048e911d.sketch_text.stroke-16"),sQuery(id+"FHMxAyK4CFUKdhS_1.wireOp",EDGE,"1cb9c079-ea9b-4899-8069-e0e3048e911d.sketch_text.stroke-17"),sQuery(id+"FHMxAyK4CFUKdhS_1.wireOp",EDGE,"1cb9c079-ea9b-4899-8069-e0e3048e911d.sketch_text.stroke-18"),sQuery(id+"FHMxAyK4CFUKdhS_1.wireOp",EDGE,"1cb9c079-ea9b-4899-8069-e0e3048e911d.sketch_text.stroke-19"),sQuery(id+"FHMxAyK4CFUKdhS_1.wireOp",EDGE,"1cb9c079-ea9b-4899-8069-e0e3048e911d.sketch_text.stroke-20"),sQuery(id+"FHMxAyK4CFUKdhS_1.wireOp",EDGE,"1cb9c079-ea9b-4899-8069-e0e3048e911d.sketch_text.stroke-21"),sQuery(id+"FHMxAyK4CFUKdhS_1.wireOp",EDGE,"1cb9c079-ea9b-4899-8069-e0e3048e911d.sketch_text.stroke-22"),sQuery(id+"FHMxAyK4CFUKdhS_1.wireOp",EDGE,"1cb9c079-ea9b-4899-8069-e0e3048e911d.sketch_text.stroke-23"),sQuery(id+"FHMxAyK4CFUKdhS_1.wireOp",EDGE,"1cb9c079-ea9b-4899-8069-e0e3048e911d.sketch_text.stroke-24"),sQuery(id+"FHMxAyK4CFUKdhS_1.wireOp",EDGE,"1cb9c079-ea9b-4899-8069-e0e3048e911d.sketch_text.stroke-25"),sQuery(id+"FHMxAyK4CFUKdhS_1.wireOp",EDGE,"1cb9c079-ea9b-4899-8069-e0e3048e911d.sketch_text.stroke-26"),sQuery(id+"FHMxAyK4CFUKdhS_1.wireOp",EDGE,"1cb9c079-ea9b-4899-8069-e0e3048e911d.sketch_text.stroke-27"),sQuery(id+"FHMxAyK4CFUKdhS_1.wireOp",EDGE,"1cb9c079-ea9b-4899-8069-e0e3048e911d.sketch_text.stroke-28"),sQuery(id+"FHMxAyK4CFUKdhS_1.wireOp",EDGE,"1cb9c079-ea9b-4899-8069-e0e3048e911d.sketch_text.stroke-29"),sQuery(id+"FHMxAyK4CFUKdhS_1.wireOp",EDGE,"1cb9c079-ea9b-4899-8069-e0e3048e911d.sketch_text.stroke-30"),sQuery(id+"FHMxAyK4CFUKdhS_1.wireOp",EDGE,"1cb9c079-ea9b-4899-8069-e0e3048e911d.sketch_text.stroke-31"),sQuery(id+"FHMxAyK4CFUKdhS_1.wireOp",EDGE,"1cb9c079-ea9b-4899-8069-e0e3048e911d.sketch_text.stroke-32"),sQuery(id+"FHMxAyK4CFUKdhS_1.wireOp",EDGE,"1cb9c079-ea9b-4899-8069-e0e3048e911d.sketch_text.stroke-33"),sQuery(id+"FHMxAyK4CFUKdhS_1.wireOp",EDGE,"1cb9c079-ea9b-4899-8069-e0e3048e911d.sketch_text.stroke-34"),sQuery(id+"FHMxAyK4CFUKdhS_1.wireOp",EDGE,"1cb9c079-ea9b-4899-8069-e0e3048e911d.sketch_text.stroke-35"),sQuery(id+"FHMxAyK4CFUKdhS_1.wireOp",EDGE,"1cb9c079-ea9b-4899-8069-e0e3048e911d.sketch_text.stroke-36"),sQuery(id+"FHMxAyK4CFUKdhS_1.wireOp",EDGE,"1cb9c079-ea9b-4899-8069-e0e3048e911d.sketch_text.stroke-37"),sQuery(id+"FHMxAyK4CFUKdhS_1.wireOp",EDGE,"1cb9c079-ea9b-4899-8069-e0e3048e911d.sketch_text.stroke-38"),sQuery(id+"FHMxAyK4CFUKdhS_1.wireOp",EDGE,"1cb9c079-ea9b-4899-8069-e0e3048e911d.sketch_text.stroke-39"),sQuery(id+"FHMxAyK4CFUKdhS_1.wireOp",EDGE,"1cb9c079-ea9b-4899-8069-e0e3048e911d.sketch_text.stroke-40"),sQuery(id+"FHMxAyK4CFUKdhS_1.wireOp",EDGE,"1cb9c079-ea9b-4899-8069-e0e3048e911d.sketch_text.stroke-41"),sQuery(id+"FHMxAyK4CFUKdhS_1.wireOp",EDGE,"1cb9c079-ea9b-4899-8069-e0e3048e911d.sketch_text.stroke-42"),sQuery(id+"FHMxAyK4CFUKdhS_1.wireOp",EDGE,"1cb9c079-ea9b-4899-8069-e0e3048e911d.sketch_text.stroke-43"),sQuery(id+"FHMxAyK4CFUKdhS_1.wireOp",EDGE,"1cb9c079-ea9b-4899-8069-e0e3048e911d.sketch_text.stroke-44"),sQuery(id+"FHMxAyK4CFUKdhS_1.wireOp",EDGE,"1cb9c079-ea9b-4899-8069-e0e3048e911d.sketch_text.stroke-45"),sQuery(id+"FHMxAyK4CFUKdhS_1.wireOp",EDGE,"1cb9c079-ea9b-4899-8069-e0e3048e911d.sketch_text.stroke-46"),sQuery(id+"FHMxAyK4CFUKdhS_1.wireOp",EDGE,"1cb9c079-ea9b-4899-8069-e0e3048e911d.sketch_text.stroke-47"),sQuery(id+"FHMxAyK4CFUKdhS_1.wireOp",EDGE,"1cb9c079-ea9b-4899-8069-e0e3048e911d.sketch_text.stroke-48"),sQuery(id+"FHMxAyK4CFUKdhS_1.wireOp",EDGE,"1cb9c079-ea9b-4899-8069-e0e3048e911d.sketch_text.stroke-49"),sQuery(id+"FHMxAyK4CFUKdhS_1.wireOp",EDGE,"1cb9c079-ea9b-4899-8069-e0e3048e911d.sketch_text.stroke-50"),sQuery(id+"FHMxAyK4CFUKdhS_1.wireOp",EDGE,"1cb9c079-ea9b-4899-8069-e0e3048e911d.sketch_text.stroke-51"),sQuery(id+"FHMxAyK4CFUKdhS_1.wireOp",EDGE,"1cb9c079-ea9b-4899-8069-e0e3048e911d.sketch_text.stroke-52"),sQuery(id+"FHMxAyK4CFUKdhS_1.wireOp",EDGE,"1cb9c079-ea9b-4899-8069-e0e3048e911d.sketch_text.stroke-53"),sQuery(id+"FHMxAyK4CFUKdhS_1.wireOp",EDGE,"1cb9c079-ea9b-4899-8069-e0e3048e911d.sketch_text.stroke-54"),sQuery(id+"FHMxAyK4CFUKdhS_1.wireOp",EDGE,"1cb9c079-ea9b-4899-8069-e0e3048e911d.sketch_text.stroke-55"),sQuery(id+"FHMxAyK4CFUKdhS_1.wireOp",EDGE,"1cb9c079-ea9b-4899-8069-e0e3048e911d.sketch_text.stroke-56"),sQuery(id+"FHMxAyK4CFUKdhS_1.wireOp",EDGE,"1cb9c079-ea9b-4899-8069-e0e3048e911d.sketch_text.stroke-57"),sQuery(id+"FHMxAyK4CFUKdhS_1.wireOp",EDGE,"1cb9c079-ea9b-4899-8069-e0e3048e911d.sketch_text.stroke-58"),sQuery(id+"FHMxAyK4CFUKdhS_1.wireOp",EDGE,"1cb9c079-ea9b-4899-8069-e0e3048e911d.sketch_text.stroke-59"),sQuery(id+"FHMxAyK4CFUKdhS_1.wireOp",EDGE,"1cb9c079-ea9b-4899-8069-e0e3048e911d.sketch_text.stroke-60"),sQuery(id+"FHMxAyK4CFUKdhS_1.wireOp",EDGE,"1cb9c079-ea9b-4899-8069-e0e3048e911d.sketch_text.stroke-61"),sQuery(id+"FHMxAyK4CFUKdhS_1.wireOp",EDGE,"1cb9c079-ea9b-4899-8069-e0e3048e911d.sketch_text.stroke-62"),sQuery(id+"FHMxAyK4CFUKdhS_1.wireOp",EDGE,"1cb9c079-ea9b-4899-8069-e0e3048e911d.sketch_text.stroke-71"),sQuery(id+"FHMxAyK4CFUKdhS_1.wireOp",EDGE,"1cb9c079-ea9b-4899-8069-e0e3048e911d.sketch_text.stroke-72"),sQuery(id+"FHMxAyK4CFUKdhS_1.wireOp",EDGE,"1cb9c079-ea9b-4899-8069-e0e3048e911d.sketch_text.stroke-73"),sQuery(id+"FHMxAyK4CFUKdhS_1.wireOp",EDGE,"1cb9c079-ea9b-4899-8069-e0e3048e911d.sketch_text.stroke-74"),sQuery(id+"FHMxAyK4CFUKdhS_1.wireOp",EDGE,"1cb9c079-ea9b-4899-8069-e0e3048e911d.sketch_text.stroke-75"),sQuery(id+"FHMxAyK4CFUKdhS_1.wireOp",EDGE,"1cb9c079-ea9b-4899-8069-e0e3048e911d.sketch_text.stroke-76"),sQuery(id+"FHMxAyK4CFUKdhS_1.wireOp",EDGE,"1cb9c079-ea9b-4899-8069-e0e3048e911d.sketch_text.stroke-77"),sQuery(id+"FHMxAyK4CFUKdhS_1.wireOp",EDGE,"1cb9c079-ea9b-4899-8069-e0e3048e911d.sketch_text.stroke-78"),sQuery(id+"FHMxAyK4CFUKdhS_1.wireOp",EDGE,"1cb9c079-ea9b-4899-8069-e0e3048e911d.sketch_text.stroke-79"),sQuery(id+"FHMxAyK4CFUKdhS_1.wireOp",EDGE,"1cb9c079-ea9b-4899-8069-e0e3048e911d.sketch_text.stroke-80"),sQuery(id+"FHMxAyK4CFUKdhS_1.wireOp",EDGE,"1cb9c079-ea9b-4899-8069-e0e3048e911d.sketch_text.stroke-81"),sQuery(id+"FHMxAyK4CFUKdhS_1.wireOp",EDGE,"1cb9c079-ea9b-4899-8069-e0e3048e911d.sketch_text.stroke-82"),sQuery(id+"FHMxAyK4CFUKdhS_1.wireOp",EDGE,"1cb9c079-ea9b-4899-8069-e0e3048e911d.sketch_text.stroke-83"),sQuery(id+"FHMxAyK4CFUKdhS_1.wireOp",EDGE,"1cb9c079-ea9b-4899-8069-e0e3048e911d.sketch_text.stroke-84"),sQuery(id+"FHMxAyK4CFUKdhS_1.wireOp",EDGE,"1cb9c079-ea9b-4899-8069-e0e3048e911d.sketch_text.stroke-85"),sQuery(id+"FHMxAyK4CFUKdhS_1.wireOp",EDGE,"1cb9c079-ea9b-4899-8069-e0e3048e911d.sketch_text.stroke-86"),sQuery(id+"FHMxAyK4CFUKdhS_1.wireOp",EDGE,"1cb9c079-ea9b-4899-8069-e0e3048e911d.sketch_text.stroke-87"),sQuery(id+"FHMxAyK4CFUKdhS_1.wireOp",EDGE,"1cb9c079-ea9b-4899-8069-e0e3048e911d.sketch_text.stroke-88"),sQuery(id+"FHMxAyK4CFUKdhS_1.wireOp",EDGE,"1cb9c079-ea9b-4899-8069-e0e3048e911d.sketch_text.stroke-89"),sQuery(id+"FHMxAyK4CFUKdhS_1.wireOp",EDGE,"1cb9c079-ea9b-4899-8069-e0e3048e911d.sketch_text.stroke-90"),sQuery(id+"FHMxAyK4CFUKdhS_1.wireOp",EDGE,"1cb9c079-ea9b-4899-8069-e0e3048e911d.sketch_text.stroke-91"),sQuery(id+"FHMxAyK4CFUKdhS_1.wireOp",EDGE,"1cb9c079-ea9b-4899-8069-e0e3048e911d.sketch_text.stroke-92"),sQuery(id+"FHMxAyK4CFUKdhS_1.wireOp",EDGE,"1cb9c079-ea9b-4899-8069-e0e3048e911d.sketch_text.stroke-93"),sQuery(id+"FHMxAyK4CFUKdhS_1.wireOp",EDGE,"1cb9c079-ea9b-4899-8069-e0e3048e911d.sketch_text.stroke-94"),sQuery(id+"FHMxAyK4CFUKdhS_1.wireOp",EDGE,"1cb9c079-ea9b-4899-8069-e0e3048e911d.sketch_text.stroke-95"),sQuery(id+"FHMxAyK4CFUKdhS_1.wireOp",EDGE,"1cb9c079-ea9b-4899-8069-e0e3048e911d.sketch_text.stroke-96"),sQuery(id+"FHMxAyK4CFUKdhS_1.wireOp",EDGE,"1cb9c079-ea9b-4899-8069-e0e3048e911d.sketch_text.stroke-97"),sQuery(id+"FHMxAyK4CFUKdhS_1.wireOp",EDGE,"1cb9c079-ea9b-4899-8069-e0e3048e911d.sketch_text.stroke-103"),sQuery(id+"FHMxAyK4CFUKdhS_1.wireOp",EDGE,"1cb9c079-ea9b-4899-8069-e0e3048e911d.sketch_text.stroke-104"),sQuery(id+"FHMxAyK4CFUKdhS_1.wireOp",EDGE,"1cb9c079-ea9b-4899-8069-e0e3048e911d.sketch_text.stroke-105"),sQuery(id+"FHMxAyK4CFUKdhS_1.wireOp",EDGE,"1cb9c079-ea9b-4899-8069-e0e3048e911d.sketch_text.stroke-106"),sQuery(id+"FHMxAyK4CFUKdhS_1.wireOp",EDGE,"1cb9c079-ea9b-4899-8069-e0e3048e911d.sketch_text.stroke-107"),sQuery(id+"FHMxAyK4CFUKdhS_1.wireOp",EDGE,"1cb9c079-ea9b-4899-8069-e0e3048e911d.sketch_text.stroke-108"),sQuery(id+"FHMxAyK4CFUKdhS_1.wireOp",EDGE,"1cb9c079-ea9b-4899-8069-e0e3048e911d.sketch_text.stroke-109"),sQuery(id+"FHMxAyK4CFUKdhS_1.wireOp",EDGE,"1cb9c079-ea9b-4899-8069-e0e3048e911d.sketch_text.stroke-110"),sQuery(id+"FHMxAyK4CFUKdhS_1.wireOp",EDGE,"1cb9c079-ea9b-4899-8069-e0e3048e911d.sketch_text.stroke-111"),sQuery(id+"FHMxAyK4CFUKdhS_1.wireOp",EDGE,"1cb9c079-ea9b-4899-8069-e0e3048e911d.sketch_text.stroke-112"),sQuery(id+"FHMxAyK4CFUKdhS_1.wireOp",EDGE,"1cb9c079-ea9b-4899-8069-e0e3048e911d.sketch_text.stroke-113"),sQuery(id+"FHMxAyK4CFUKdhS_1.wireOp",EDGE,"1cb9c079-ea9b-4899-8069-e0e3048e911d.sketch_text.stroke-114"),sQuery(id+"FHMxAyK4CFUKdhS_1.wireOp",EDGE,"1cb9c079-ea9b-4899-8069-e0e3048e911d.sketch_text.stroke-115"),sQuery(id+"FHMxAyK4CFUKdhS_1.wireOp",EDGE,"1cb9c079-ea9b-4899-8069-e0e3048e911d.sketch_text.stroke-116"),sQuery(id+"FHMxAyK4CFUKdhS_1.wireOp",EDGE,"1cb9c079-ea9b-4899-8069-e0e3048e911d.sketch_text.stroke-117"),sQuery(id+"FHMxAyK4CFUKdhS_1.wireOp",EDGE,"1cb9c079-ea9b-4899-8069-e0e3048e911d.sketch_text.stroke-118"),sQuery(id+"FHMxAyK4CFUKdhS_1.wireOp",EDGE,"1cb9c079-ea9b-4899-8069-e0e3048e911d.sketch_text.stroke-119"),sQuery(id+"FHMxAyK4CFUKdhS_1.wireOp",EDGE,"1cb9c079-ea9b-4899-8069-e0e3048e911d.sketch_text.stroke-120"),sQuery(id+"FHMxAyK4CFUKdhS_1.wireOp",EDGE,"1cb9c079-ea9b-4899-8069-e0e3048e911d.sketch_text.stroke-121"),sQuery(id+"FHMxAyK4CFUKdhS_1.wireOp",EDGE,"1cb9c079-ea9b-4899-8069-e0e3048e911d.sketch_text.stroke-122"),sQuery(id+"FHMxAyK4CFUKdhS_1.wireOp",EDGE,"1cb9c079-ea9b-4899-8069-e0e3048e911d.sketch_text.stroke-123"),sQuery(id+"FHMxAyK4CFUKdhS_1.wireOp",EDGE,"1cb9c079-ea9b-4899-8069-e0e3048e911d.sketch_text.stroke-124"),sQuery(id+"FHMxAyK4CFUKdhS_1.wireOp",EDGE,"1cb9c079-ea9b-4899-8069-e0e3048e911d.sketch_text.stroke-125"),sQuery(id+"FHMxAyK4CFUKdhS_1.wireOp",EDGE,"1cb9c079-ea9b-4899-8069-e0e3048e911d.sketch_text.stroke-126"),sQuery(id+"FHMxAyK4CFUKdhS_1.wireOp",EDGE,"1cb9c079-ea9b-4899-8069-e0e3048e911d.sketch_text.stroke-127"),sQuery(id+"FHMxAyK4CFUKdhS_1.wireOp",EDGE,"1cb9c079-ea9b-4899-8069-e0e3048e911d.sketch_text.stroke-128"),sQuery(id+"FHMxAyK4CFUKdhS_1.wireOp",EDGE,"1cb9c079-ea9b-4899-8069-e0e3048e911d.sketch_text.stroke-129"),sQuery(id+"FHMxAyK4CFUKdhS_1.wireOp",EDGE,"1cb9c079-ea9b-4899-8069-e0e3048e911d.sketch_text.stroke-130"),sQuery(id+"FHMxAyK4CFUKdhS_1.wireOp",EDGE,"1cb9c079-ea9b-4899-8069-e0e3048e911d.sketch_text.stroke-131"),sQuery(id+"FHMxAyK4CFUKdhS_1.wireOp",EDGE,"1cb9c079-ea9b-4899-8069-e0e3048e911d.sketch_text.stroke-132"),sQuery(id+"FHMxAyK4CFUKdhS_1.wireOp",EDGE,"1cb9c079-ea9b-4899-8069-e0e3048e911d.sketch_text.stroke-133"),sQuery(id+"FHMxAyK4CFUKdhS_1.wireOp",EDGE,"1cb9c079-ea9b-4899-8069-e0e3048e911d.sketch_text.stroke-134"),sQuery(id+"FHMxAyK4CFUKdhS_1.wireOp",EDGE,"1cb9c079-ea9b-4899-8069-e0e3048e911d.sketch_text.stroke-135"),sQuery(id+"FHMxAyK4CFUKdhS_1.wireOp",EDGE,"1cb9c079-ea9b-4899-8069-e0e3048e911d.sketch_text.stroke-136"),sQuery(id+"FHMxAyK4CFUKdhS_1.wireOp",EDGE,"1cb9c079-ea9b-4899-8069-e0e3048e911d.sketch_text.stroke-137"),sQuery(id+"FHMxAyK4CFUKdhS_1.wireOp",EDGE,"1cb9c079-ea9b-4899-8069-e0e3048e911d.sketch_text.stroke-138"),sQuery(id+"FHMxAyK4CFUKdhS_1.wireOp",EDGE,"1cb9c079-ea9b-4899-8069-e0e3048e911d.sketch_text.stroke-139"),sQuery(id+"FHMxAyK4CFUKdhS_1.wireOp",EDGE,"1cb9c079-ea9b-4899-8069-e0e3048e911d.sketch_text.stroke-140"),sQuery(id+"FHMxAyK4CFUKdhS_1.wireOp",EDGE,"1cb9c079-ea9b-4899-8069-e0e3048e911d.sketch_text.stroke-141"),sQuery(id+"FHMxAyK4CFUKdhS_1.wireOp",EDGE,"1cb9c079-ea9b-4899-8069-e0e3048e911d.sketch_text.stroke-142"),sQuery(id+"FHMxAyK4CFUKdhS_1.wireOp",EDGE,"1cb9c079-ea9b-4899-8069-e0e3048e911d.sketch_text.stroke-143"),sQuery(id+"FHMxAyK4CFUKdhS_1.wireOp",EDGE,"1cb9c079-ea9b-4899-8069-e0e3048e911d.sketch_text.stroke-144"),sQuery(id+"FHMxAyK4CFUKdhS_1.wireOp",EDGE,"1cb9c079-ea9b-4899-8069-e0e3048e911d.sketch_text.stroke-145"),sQuery(id+"FHMxAyK4CFUKdhS_1.wireOp",EDGE,"1cb9c079-ea9b-4899-8069-e0e3048e911d.sketch_text.stroke-146"),sQuery(id+"FHMxAyK4CFUKdhS_1.wireOp",EDGE,"1cb9c079-ea9b-4899-8069-e0e3048e911d.sketch_text.stroke-147"),sQuery(id+"FHMxAyK4CFUKdhS_1.wireOp",EDGE,"1cb9c079-ea9b-4899-8069-e0e3048e911d.sketch_text.stroke-148"),sQuery(id+"FHMxAyK4CFUKdhS_1.wireOp",EDGE,"1cb9c079-ea9b-4899-8069-e0e3048e911d.sketch_text.stroke-149"),sQuery(id+"FHMxAyK4CFUKdhS_1.wireOp",EDGE,"1cb9c079-ea9b-4899-8069-e0e3048e911d.sketch_text.stroke-150"),sQuery(id+"FHMxAyK4CFUKdhS_1.wireOp",EDGE,"1cb9c079-ea9b-4899-8069-e0e3048e911d.sketch_text.stroke-151"),sQuery(id+"FHMxAyK4CFUKdhS_1.wireOp",EDGE,"1cb9c079-ea9b-4899-8069-e0e3048e911d.sketch_text.stroke-152"),sQuery(id+"FHMxAyK4CFUKdhS_1.wireOp",EDGE,"1cb9c079-ea9b-4899-8069-e0e3048e911d.sketch_text.stroke-153"),sQuery(id+"FHMxAyK4CFUKdhS_1.wireOp",EDGE,"1cb9c079-ea9b-4899-8069-e0e3048e911d.sketch_text.stroke-159"),sQuery(id+"FHMxAyK4CFUKdhS_1.wireOp",EDGE,"1cb9c079-ea9b-4899-8069-e0e3048e911d.sketch_text.stroke-160"),sQuery(id+"FHMxAyK4CFUKdhS_1.wireOp",EDGE,"1cb9c079-ea9b-4899-8069-e0e3048e911d.sketch_text.stroke-161"),sQuery(id+"FHMxAyK4CFUKdhS_1.wireOp",EDGE,"1cb9c079-ea9b-4899-8069-e0e3048e911d.sketch_text.stroke-162"),sQuery(id+"FHMxAyK4CFUKdhS_1.wireOp",EDGE,"1cb9c079-ea9b-4899-8069-e0e3048e911d.sketch_text.stroke-163"),sQuery(id+"FHMxAyK4CFUKdhS_1.wireOp",EDGE,"1cb9c079-ea9b-4899-8069-e0e3048e911d.sketch_text.stroke-164"),sQuery(id+"FHMxAyK4CFUKdhS_1.wireOp",EDGE,"1cb9c079-ea9b-4899-8069-e0e3048e911d.sketch_text.stroke-165"),sQuery(id+"FHMxAyK4CFUKdhS_1.wireOp",EDGE,"1cb9c079-ea9b-4899-8069-e0e3048e911d.sketch_text.stroke-166"),sQuery(id+"FHMxAyK4CFUKdhS_1.wireOp",EDGE,"1cb9c079-ea9b-4899-8069-e0e3048e911d.sketch_text.stroke-167"),sQuery(id+"FHMxAyK4CFUKdhS_1.wireOp",EDGE,"1cb9c079-ea9b-4899-8069-e0e3048e911d.sketch_text.stroke-168"),sQuery(id+"FHMxAyK4CFUKdhS_1.wireOp",EDGE,"1cb9c079-ea9b-4899-8069-e0e3048e911d.sketch_text.stroke-169"),sQuery(id+"FHMxAyK4CFUKdhS_1.wireOp",EDGE,"1cb9c079-ea9b-4899-8069-e0e3048e911d.sketch_text.stroke-170"),sQuery(id+"FHMxAyK4CFUKdhS_1.wireOp",EDGE,"1cb9c079-ea9b-4899-8069-e0e3048e911d.sketch_text.stroke-171"),sQuery(id+"FHMxAyK4CFUKdhS_1.wireOp",EDGE,"1cb9c079-ea9b-4899-8069-e0e3048e911d.sketch_text.stroke-172"),sQuery(id+"FHMxAyK4CFUKdhS_1.wireOp",EDGE,"1cb9c079-ea9b-4899-8069-e0e3048e911d.sketch_text.stroke-173"),sQuery(id+"FHMxAyK4CFUKdhS_1.wireOp",EDGE,"1cb9c079-ea9b-4899-8069-e0e3048e911d.sketch_text.stroke-174"),sQuery(id+"FHMxAyK4CFUKdhS_1.wireOp",EDGE,"1cb9c079-ea9b-4899-8069-e0e3048e911d.sketch_text.stroke-175"),sQuery(id+"FHMxAyK4CFUKdhS_1.wireOp",EDGE,"1cb9c079-ea9b-4899-8069-e0e3048e911d.sketch_text.stroke-176"),sQuery(id+"FHMxAyK4CFUKdhS_1.wireOp",EDGE,"1cb9c079-ea9b-4899-8069-e0e3048e911d.sketch_text.stroke-177"),sQuery(id+"FHMxAyK4CFUKdhS_1.wireOp",EDGE,"1cb9c079-ea9b-4899-8069-e0e3048e911d.sketch_text.stroke-178"),sQuery(id+"FHMxAyK4CFUKdhS_1.wireOp",EDGE,"1cb9c079-ea9b-4899-8069-e0e3048e911d.sketch_text.stroke-179"),sQuery(id+"FHMxAyK4CFUKdhS_1.wireOp",EDGE,"1cb9c079-ea9b-4899-8069-e0e3048e911d.sketch_text.stroke-180"),subQ2,sQuery(id+"F3.wireOp",EDGE,"E29")])],"isStart":true})]),OD(1.0)],"derivedFrom":makeQuery(id+"F1.opExtrude","CAP_EDGE",EDGE,{"disambiguationData":[OSD([subQ0])],"isStart":false})});}
            var Q25;
            {var subQ0=sQuery(id+"F0.wireOp",EDGE,"E0.top");var subQ1=sQuery(id+"F0.wireOp",EDGE,"E0.bottom");var subQ2=sQuery(id+"F3.wireOp",EDGE,"E28");Q25=makeQuery(id+"F4.boolean.opBoolean","SPLIT",EDGE,{"disambiguationData":[TD([makeQuery(id+"F1.opExtrude","CAP_FACE",FACE,{"disambiguationData":[OSD([subQ1,subQ0,sQuery(id+"F0.wireOp",EDGE,"E0.left"),sQuery(id+"F0.wireOp",EDGE,"E0.right")])],"isStart":false}),makeQuery(id+"F1.opExtrude","SWEPT_FACE",FACE,{"disambiguationData":[OSD([subQ0])]}),makeQuery(id+"F4.opExtrude","SWEPT_FACE",FACE,{"disambiguationData":[OSD([subQ2])]}),makeQuery(id+"F4.opExtrude","CAP_FACE",FACE,{"disambiguationData":[OSD([subQ1,sQuery(id+"F2.wireOp",EDGE,"fcba4419-a2ee-464f-be9d-58f11bf3418b.sketch_text.stroke-0"),sQuery(id+"F2.wireOp",EDGE,"fcba4419-a2ee-464f-be9d-58f11bf3418b.sketch_text.stroke-1"),sQuery(id+"F2.wireOp",EDGE,"fcba4419-a2ee-464f-be9d-58f11bf3418b.sketch_text.stroke-2"),sQuery(id+"F2.wireOp",EDGE,"fcba4419-a2ee-464f-be9d-58f11bf3418b.sketch_text.stroke-3"),sQuery(id+"F2.wireOp",EDGE,"fcba4419-a2ee-464f-be9d-58f11bf3418b.sketch_text.stroke-4"),sQuery(id+"F2.wireOp",EDGE,"fcba4419-a2ee-464f-be9d-58f11bf3418b.sketch_text.stroke-5"),sQuery(id+"F2.wireOp",EDGE,"fcba4419-a2ee-464f-be9d-58f11bf3418b.sketch_text.stroke-6"),sQuery(id+"F2.wireOp",EDGE,"fcba4419-a2ee-464f-be9d-58f11bf3418b.sketch_text.stroke-7"),sQuery(id+"F2.wireOp",EDGE,"fcba4419-a2ee-464f-be9d-58f11bf3418b.sketch_text.stroke-8"),sQuery(id+"F2.wireOp",EDGE,"fcba4419-a2ee-464f-be9d-58f11bf3418b.sketch_text.stroke-9"),sQuery(id+"F2.wireOp",EDGE,"fcba4419-a2ee-464f-be9d-58f11bf3418b.sketch_text.stroke-10"),sQuery(id+"F2.wireOp",EDGE,"fcba4419-a2ee-464f-be9d-58f11bf3418b.sketch_text.stroke-11"),sQuery(id+"F2.wireOp",EDGE,"fcba4419-a2ee-464f-be9d-58f11bf3418b.sketch_text.stroke-12"),sQuery(id+"F2.wireOp",EDGE,"fcba4419-a2ee-464f-be9d-58f11bf3418b.sketch_text.stroke-13"),sQuery(id+"F2.wireOp",EDGE,"fcba4419-a2ee-464f-be9d-58f11bf3418b.sketch_text.stroke-14"),sQuery(id+"F2.wireOp",EDGE,"fcba4419-a2ee-464f-be9d-58f11bf3418b.sketch_text.stroke-15"),sQuery(id+"F2.wireOp",EDGE,"fcba4419-a2ee-464f-be9d-58f11bf3418b.sketch_text.stroke-16"),sQuery(id+"F2.wireOp",EDGE,"fcba4419-a2ee-464f-be9d-58f11bf3418b.sketch_text.stroke-17"),sQuery(id+"F2.wireOp",EDGE,"fcba4419-a2ee-464f-be9d-58f11bf3418b.sketch_text.stroke-18"),sQuery(id+"F2.wireOp",EDGE,"fcba4419-a2ee-464f-be9d-58f11bf3418b.sketch_text.stroke-19"),sQuery(id+"F2.wireOp",EDGE,"fcba4419-a2ee-464f-be9d-58f11bf3418b.sketch_text.stroke-20"),sQuery(id+"F2.wireOp",EDGE,"fcba4419-a2ee-464f-be9d-58f11bf3418b.sketch_text.stroke-21"),sQuery(id+"F2.wireOp",EDGE,"fcba4419-a2ee-464f-be9d-58f11bf3418b.sketch_text.stroke-22"),sQuery(id+"F2.wireOp",EDGE,"fcba4419-a2ee-464f-be9d-58f11bf3418b.sketch_text.stroke-23"),sQuery(id+"F2.wireOp",EDGE,"fcba4419-a2ee-464f-be9d-58f11bf3418b.sketch_text.stroke-24"),sQuery(id+"F2.wireOp",EDGE,"fcba4419-a2ee-464f-be9d-58f11bf3418b.sketch_text.stroke-25"),sQuery(id+"F2.wireOp",EDGE,"fcba4419-a2ee-464f-be9d-58f11bf3418b.sketch_text.stroke-26"),sQuery(id+"F2.wireOp",EDGE,"fcba4419-a2ee-464f-be9d-58f11bf3418b.sketch_text.stroke-27"),sQuery(id+"F2.wireOp",EDGE,"fcba4419-a2ee-464f-be9d-58f11bf3418b.sketch_text.stroke-28"),sQuery(id+"F2.wireOp",EDGE,"fcba4419-a2ee-464f-be9d-58f11bf3418b.sketch_text.stroke-29"),sQuery(id+"F2.wireOp",EDGE,"fcba4419-a2ee-464f-be9d-58f11bf3418b.sketch_text.stroke-30"),sQuery(id+"F2.wireOp",EDGE,"fcba4419-a2ee-464f-be9d-58f11bf3418b.sketch_text.stroke-31"),sQuery(id+"F2.wireOp",EDGE,"fcba4419-a2ee-464f-be9d-58f11bf3418b.sketch_text.stroke-32"),sQuery(id+"F2.wireOp",EDGE,"fcba4419-a2ee-464f-be9d-58f11bf3418b.sketch_text.stroke-33"),sQuery(id+"F2.wireOp",EDGE,"fcba4419-a2ee-464f-be9d-58f11bf3418b.sketch_text.stroke-34"),sQuery(id+"F2.wireOp",EDGE,"fcba4419-a2ee-464f-be9d-58f11bf3418b.sketch_text.stroke-35"),sQuery(id+"F2.wireOp",EDGE,"fcba4419-a2ee-464f-be9d-58f11bf3418b.sketch_text.stroke-36"),sQuery(id+"F2.wireOp",EDGE,"fcba4419-a2ee-464f-be9d-58f11bf3418b.sketch_text.stroke-37"),sQuery(id+"F2.wireOp",EDGE,"fcba4419-a2ee-464f-be9d-58f11bf3418b.sketch_text.stroke-38"),sQuery(id+"F2.wireOp",EDGE,"fcba4419-a2ee-464f-be9d-58f11bf3418b.sketch_text.stroke-39"),sQuery(id+"F2.wireOp",EDGE,"fcba4419-a2ee-464f-be9d-58f11bf3418b.sketch_text.stroke-40"),sQuery(id+"F2.wireOp",EDGE,"fcba4419-a2ee-464f-be9d-58f11bf3418b.sketch_text.stroke-41"),sQuery(id+"F2.wireOp",EDGE,"fcba4419-a2ee-464f-be9d-58f11bf3418b.sketch_text.stroke-42"),sQuery(id+"F2.wireOp",EDGE,"fcba4419-a2ee-464f-be9d-58f11bf3418b.sketch_text.stroke-43"),sQuery(id+"F2.wireOp",EDGE,"fcba4419-a2ee-464f-be9d-58f11bf3418b.sketch_text.stroke-44"),sQuery(id+"F2.wireOp",EDGE,"fcba4419-a2ee-464f-be9d-58f11bf3418b.sketch_text.stroke-45"),sQuery(id+"F2.wireOp",EDGE,"fcba4419-a2ee-464f-be9d-58f11bf3418b.sketch_text.stroke-46"),sQuery(id+"F2.wireOp",EDGE,"fcba4419-a2ee-464f-be9d-58f11bf3418b.sketch_text.stroke-47"),sQuery(id+"F2.wireOp",EDGE,"fcba4419-a2ee-464f-be9d-58f11bf3418b.sketch_text.stroke-48"),sQuery(id+"F2.wireOp",EDGE,"fcba4419-a2ee-464f-be9d-58f11bf3418b.sketch_text.stroke-49"),sQuery(id+"F2.wireOp",EDGE,"fcba4419-a2ee-464f-be9d-58f11bf3418b.sketch_text.stroke-50"),sQuery(id+"F2.wireOp",EDGE,"fcba4419-a2ee-464f-be9d-58f11bf3418b.sketch_text.stroke-51"),sQuery(id+"F2.wireOp",EDGE,"fcba4419-a2ee-464f-be9d-58f11bf3418b.sketch_text.stroke-52"),sQuery(id+"F2.wireOp",EDGE,"fcba4419-a2ee-464f-be9d-58f11bf3418b.sketch_text.stroke-53"),sQuery(id+"F2.wireOp",EDGE,"fcba4419-a2ee-464f-be9d-58f11bf3418b.sketch_text.stroke-54"),sQuery(id+"F2.wireOp",EDGE,"fcba4419-a2ee-464f-be9d-58f11bf3418b.sketch_text.stroke-55"),sQuery(id+"F2.wireOp",EDGE,"fcba4419-a2ee-464f-be9d-58f11bf3418b.sketch_text.stroke-56"),sQuery(id+"F2.wireOp",EDGE,"fcba4419-a2ee-464f-be9d-58f11bf3418b.sketch_text.stroke-57"),sQuery(id+"F2.wireOp",EDGE,"fcba4419-a2ee-464f-be9d-58f11bf3418b.sketch_text.stroke-58"),sQuery(id+"F2.wireOp",EDGE,"fcba4419-a2ee-464f-be9d-58f11bf3418b.sketch_text.stroke-59"),sQuery(id+"F2.wireOp",EDGE,"fcba4419-a2ee-464f-be9d-58f11bf3418b.sketch_text.stroke-60"),sQuery(id+"F2.wireOp",EDGE,"fcba4419-a2ee-464f-be9d-58f11bf3418b.sketch_text.stroke-61"),sQuery(id+"F2.wireOp",EDGE,"fcba4419-a2ee-464f-be9d-58f11bf3418b.sketch_text.stroke-62"),sQuery(id+"F2.wireOp",EDGE,"fcba4419-a2ee-464f-be9d-58f11bf3418b.sketch_text.stroke-63"),sQuery(id+"F2.wireOp",EDGE,"fcba4419-a2ee-464f-be9d-58f11bf3418b.sketch_text.stroke-64"),sQuery(id+"F2.wireOp",EDGE,"fcba4419-a2ee-464f-be9d-58f11bf3418b.sketch_text.stroke-65"),sQuery(id+"F2.wireOp",EDGE,"fcba4419-a2ee-464f-be9d-58f11bf3418b.sketch_text.stroke-66"),sQuery(id+"F2.wireOp",EDGE,"fcba4419-a2ee-464f-be9d-58f11bf3418b.sketch_text.stroke-67"),sQuery(id+"F2.wireOp",EDGE,"fcba4419-a2ee-464f-be9d-58f11bf3418b.sketch_text.stroke-68"),sQuery(id+"F2.wireOp",EDGE,"fcba4419-a2ee-464f-be9d-58f11bf3418b.sketch_text.stroke-69"),sQuery(id+"F2.wireOp",EDGE,"fcba4419-a2ee-464f-be9d-58f11bf3418b.sketch_text.stroke-70"),sQuery(id+"F2.wireOp",EDGE,"fcba4419-a2ee-464f-be9d-58f11bf3418b.sketch_text.stroke-71"),sQuery(id+"F2.wireOp",EDGE,"fcba4419-a2ee-464f-be9d-58f11bf3418b.sketch_text.stroke-72"),sQuery(id+"F2.wireOp",EDGE,"fcba4419-a2ee-464f-be9d-58f11bf3418b.sketch_text.stroke-73"),sQuery(id+"F2.wireOp",EDGE,"fcba4419-a2ee-464f-be9d-58f11bf3418b.sketch_text.stroke-74"),sQuery(id+"F2.wireOp",EDGE,"fcba4419-a2ee-464f-be9d-58f11bf3418b.sketch_text.stroke-75"),sQuery(id+"F2.wireOp",EDGE,"fcba4419-a2ee-464f-be9d-58f11bf3418b.sketch_text.stroke-76"),sQuery(id+"F2.wireOp",EDGE,"fcba4419-a2ee-464f-be9d-58f11bf3418b.sketch_text.stroke-77"),sQuery(id+"F2.wireOp",EDGE,"fcba4419-a2ee-464f-be9d-58f11bf3418b.sketch_text.stroke-78"),sQuery(id+"F2.wireOp",EDGE,"fcba4419-a2ee-464f-be9d-58f11bf3418b.sketch_text.stroke-79"),sQuery(id+"F2.wireOp",EDGE,"fcba4419-a2ee-464f-be9d-58f11bf3418b.sketch_text.stroke-80"),sQuery(id+"F2.wireOp",EDGE,"fcba4419-a2ee-464f-be9d-58f11bf3418b.sketch_text.stroke-81"),sQuery(id+"F2.wireOp",EDGE,"fcba4419-a2ee-464f-be9d-58f11bf3418b.sketch_text.stroke-82"),sQuery(id+"F2.wireOp",EDGE,"fcba4419-a2ee-464f-be9d-58f11bf3418b.sketch_text.stroke-83"),sQuery(id+"F2.wireOp",EDGE,"fcba4419-a2ee-464f-be9d-58f11bf3418b.sketch_text.stroke-84"),sQuery(id+"F2.wireOp",EDGE,"fcba4419-a2ee-464f-be9d-58f11bf3418b.sketch_text.stroke-85"),sQuery(id+"F2.wireOp",EDGE,"fcba4419-a2ee-464f-be9d-58f11bf3418b.sketch_text.stroke-86"),sQuery(id+"F2.wireOp",EDGE,"fcba4419-a2ee-464f-be9d-58f11bf3418b.sketch_text.stroke-87"),sQuery(id+"F2.wireOp",EDGE,"fcba4419-a2ee-464f-be9d-58f11bf3418b.sketch_text.stroke-88"),sQuery(id+"F2.wireOp",EDGE,"fcba4419-a2ee-464f-be9d-58f11bf3418b.sketch_text.stroke-89"),sQuery(id+"F2.wireOp",EDGE,"fcba4419-a2ee-464f-be9d-58f11bf3418b.sketch_text.stroke-90"),sQuery(id+"F2.wireOp",EDGE,"fcba4419-a2ee-464f-be9d-58f11bf3418b.sketch_text.stroke-91"),sQuery(id+"F2.wireOp",EDGE,"fcba4419-a2ee-464f-be9d-58f11bf3418b.sketch_text.stroke-92"),sQuery(id+"F2.wireOp",EDGE,"fcba4419-a2ee-464f-be9d-58f11bf3418b.sketch_text.stroke-93"),sQuery(id+"F2.wireOp",EDGE,"fcba4419-a2ee-464f-be9d-58f11bf3418b.sketch_text.stroke-94"),sQuery(id+"F2.wireOp",EDGE,"fcba4419-a2ee-464f-be9d-58f11bf3418b.sketch_text.stroke-95"),sQuery(id+"F2.wireOp",EDGE,"fcba4419-a2ee-464f-be9d-58f11bf3418b.sketch_text.stroke-96"),sQuery(id+"F2.wireOp",EDGE,"fcba4419-a2ee-464f-be9d-58f11bf3418b.sketch_text.stroke-97"),sQuery(id+"F2.wireOp",EDGE,"fcba4419-a2ee-464f-be9d-58f11bf3418b.sketch_text.stroke-98"),sQuery(id+"F2.wireOp",EDGE,"fcba4419-a2ee-464f-be9d-58f11bf3418b.sketch_text.stroke-99"),sQuery(id+"F2.wireOp",EDGE,"fcba4419-a2ee-464f-be9d-58f11bf3418b.sketch_text.stroke-100"),sQuery(id+"F2.wireOp",EDGE,"fcba4419-a2ee-464f-be9d-58f11bf3418b.sketch_text.stroke-101"),sQuery(id+"F2.wireOp",EDGE,"fcba4419-a2ee-464f-be9d-58f11bf3418b.sketch_text.stroke-102"),sQuery(id+"F2.wireOp",EDGE,"fcba4419-a2ee-464f-be9d-58f11bf3418b.sketch_text.stroke-103"),sQuery(id+"F2.wireOp",EDGE,"fcba4419-a2ee-464f-be9d-58f11bf3418b.sketch_text.stroke-104"),sQuery(id+"F2.wireOp",EDGE,"fcba4419-a2ee-464f-be9d-58f11bf3418b.sketch_text.stroke-105"),sQuery(id+"F2.wireOp",EDGE,"fcba4419-a2ee-464f-be9d-58f11bf3418b.sketch_text.stroke-106"),sQuery(id+"F2.wireOp",EDGE,"fcba4419-a2ee-464f-be9d-58f11bf3418b.sketch_text.stroke-107"),sQuery(id+"F2.wireOp",EDGE,"fcba4419-a2ee-464f-be9d-58f11bf3418b.sketch_text.stroke-108"),sQuery(id+"F2.wireOp",EDGE,"fcba4419-a2ee-464f-be9d-58f11bf3418b.sketch_text.stroke-109"),sQuery(id+"F2.wireOp",EDGE,"fcba4419-a2ee-464f-be9d-58f11bf3418b.sketch_text.stroke-110"),sQuery(id+"F2.wireOp",EDGE,"fcba4419-a2ee-464f-be9d-58f11bf3418b.sketch_text.stroke-111"),sQuery(id+"F2.wireOp",EDGE,"fcba4419-a2ee-464f-be9d-58f11bf3418b.sketch_text.stroke-112"),sQuery(id+"F2.wireOp",EDGE,"fcba4419-a2ee-464f-be9d-58f11bf3418b.sketch_text.stroke-113"),sQuery(id+"F2.wireOp",EDGE,"fcba4419-a2ee-464f-be9d-58f11bf3418b.sketch_text.stroke-114"),sQuery(id+"F2.wireOp",EDGE,"fcba4419-a2ee-464f-be9d-58f11bf3418b.sketch_text.stroke-115"),sQuery(id+"F2.wireOp",EDGE,"fcba4419-a2ee-464f-be9d-58f11bf3418b.sketch_text.stroke-116"),sQuery(id+"F2.wireOp",EDGE,"fcba4419-a2ee-464f-be9d-58f11bf3418b.sketch_text.stroke-117"),sQuery(id+"F2.wireOp",EDGE,"fcba4419-a2ee-464f-be9d-58f11bf3418b.sketch_text.stroke-118"),sQuery(id+"F2.wireOp",EDGE,"fcba4419-a2ee-464f-be9d-58f11bf3418b.sketch_text.stroke-119"),sQuery(id+"F2.wireOp",EDGE,"fcba4419-a2ee-464f-be9d-58f11bf3418b.sketch_text.stroke-120"),sQuery(id+"F2.wireOp",EDGE,"fcba4419-a2ee-464f-be9d-58f11bf3418b.sketch_text.stroke-121"),sQuery(id+"F2.wireOp",EDGE,"fcba4419-a2ee-464f-be9d-58f11bf3418b.sketch_text.stroke-122"),sQuery(id+"F2.wireOp",EDGE,"fcba4419-a2ee-464f-be9d-58f11bf3418b.sketch_text.stroke-123"),sQuery(id+"F2.wireOp",EDGE,"fcba4419-a2ee-464f-be9d-58f11bf3418b.sketch_text.stroke-124"),sQuery(id+"F2.wireOp",EDGE,"fcba4419-a2ee-464f-be9d-58f11bf3418b.sketch_text.stroke-125"),sQuery(id+"F2.wireOp",EDGE,"fcba4419-a2ee-464f-be9d-58f11bf3418b.sketch_text.stroke-126"),sQuery(id+"F2.wireOp",EDGE,"fcba4419-a2ee-464f-be9d-58f11bf3418b.sketch_text.stroke-127"),sQuery(id+"F2.wireOp",EDGE,"fcba4419-a2ee-464f-be9d-58f11bf3418b.sketch_text.stroke-128"),sQuery(id+"F2.wireOp",EDGE,"fcba4419-a2ee-464f-be9d-58f11bf3418b.sketch_text.stroke-129"),sQuery(id+"F2.wireOp",EDGE,"fcba4419-a2ee-464f-be9d-58f11bf3418b.sketch_text.stroke-130"),sQuery(id+"F2.wireOp",EDGE,"fcba4419-a2ee-464f-be9d-58f11bf3418b.sketch_text.stroke-131"),sQuery(id+"F2.wireOp",EDGE,"fcba4419-a2ee-464f-be9d-58f11bf3418b.sketch_text.stroke-132"),sQuery(id+"F2.wireOp",EDGE,"fcba4419-a2ee-464f-be9d-58f11bf3418b.sketch_text.stroke-133"),sQuery(id+"F2.wireOp",EDGE,"fcba4419-a2ee-464f-be9d-58f11bf3418b.sketch_text.stroke-134"),sQuery(id+"F2.wireOp",EDGE,"fcba4419-a2ee-464f-be9d-58f11bf3418b.sketch_text.stroke-135"),sQuery(id+"F2.wireOp",EDGE,"fcba4419-a2ee-464f-be9d-58f11bf3418b.sketch_text.stroke-136"),sQuery(id+"F2.wireOp",EDGE,"fcba4419-a2ee-464f-be9d-58f11bf3418b.sketch_text.stroke-137"),sQuery(id+"F2.wireOp",EDGE,"fcba4419-a2ee-464f-be9d-58f11bf3418b.sketch_text.stroke-138"),sQuery(id+"F2.wireOp",EDGE,"fcba4419-a2ee-464f-be9d-58f11bf3418b.sketch_text.stroke-139"),sQuery(id+"F2.wireOp",EDGE,"fcba4419-a2ee-464f-be9d-58f11bf3418b.sketch_text.stroke-140"),sQuery(id+"F2.wireOp",EDGE,"fcba4419-a2ee-464f-be9d-58f11bf3418b.sketch_text.stroke-141"),sQuery(id+"F2.wireOp",EDGE,"fcba4419-a2ee-464f-be9d-58f11bf3418b.sketch_text.stroke-142"),sQuery(id+"F2.wireOp",EDGE,"fcba4419-a2ee-464f-be9d-58f11bf3418b.sketch_text.stroke-143"),sQuery(id+"F2.wireOp",EDGE,"fcba4419-a2ee-464f-be9d-58f11bf3418b.sketch_text.stroke-144"),sQuery(id+"F2.wireOp",EDGE,"fcba4419-a2ee-464f-be9d-58f11bf3418b.sketch_text.stroke-145"),sQuery(id+"F2.wireOp",EDGE,"fcba4419-a2ee-464f-be9d-58f11bf3418b.sketch_text.stroke-146"),sQuery(id+"F2.wireOp",EDGE,"fcba4419-a2ee-464f-be9d-58f11bf3418b.sketch_text.stroke-147"),sQuery(id+"F2.wireOp",EDGE,"fcba4419-a2ee-464f-be9d-58f11bf3418b.sketch_text.stroke-148"),sQuery(id+"F2.wireOp",EDGE,"fcba4419-a2ee-464f-be9d-58f11bf3418b.sketch_text.stroke-149"),sQuery(id+"F2.wireOp",EDGE,"fcba4419-a2ee-464f-be9d-58f11bf3418b.sketch_text.stroke-150"),sQuery(id+"F2.wireOp",EDGE,"fcba4419-a2ee-464f-be9d-58f11bf3418b.sketch_text.stroke-151"),sQuery(id+"F2.wireOp",EDGE,"fcba4419-a2ee-464f-be9d-58f11bf3418b.sketch_text.stroke-152"),sQuery(id+"F2.wireOp",EDGE,"fcba4419-a2ee-464f-be9d-58f11bf3418b.sketch_text.stroke-153"),sQuery(id+"F2.wireOp",EDGE,"fcba4419-a2ee-464f-be9d-58f11bf3418b.sketch_text.stroke-154"),sQuery(id+"F2.wireOp",EDGE,"fcba4419-a2ee-464f-be9d-58f11bf3418b.sketch_text.stroke-155"),sQuery(id+"F2.wireOp",EDGE,"fcba4419-a2ee-464f-be9d-58f11bf3418b.sketch_text.stroke-156"),sQuery(id+"F2.wireOp",EDGE,"fcba4419-a2ee-464f-be9d-58f11bf3418b.sketch_text.stroke-157"),sQuery(id+"F2.wireOp",EDGE,"fcba4419-a2ee-464f-be9d-58f11bf3418b.sketch_text.stroke-158"),sQuery(id+"F2.wireOp",EDGE,"fcba4419-a2ee-464f-be9d-58f11bf3418b.sketch_text.stroke-159"),sQuery(id+"F2.wireOp",EDGE,"fcba4419-a2ee-464f-be9d-58f11bf3418b.sketch_text.stroke-160"),sQuery(id+"F2.wireOp",EDGE,"fcba4419-a2ee-464f-be9d-58f11bf3418b.sketch_text.stroke-161"),sQuery(id+"F2.wireOp",EDGE,"fcba4419-a2ee-464f-be9d-58f11bf3418b.sketch_text.stroke-162"),sQuery(id+"F2.wireOp",EDGE,"fcba4419-a2ee-464f-be9d-58f11bf3418b.sketch_text.stroke-163"),sQuery(id+"F2.wireOp",EDGE,"fcba4419-a2ee-464f-be9d-58f11bf3418b.sketch_text.stroke-164"),sQuery(id+"F2.wireOp",EDGE,"fcba4419-a2ee-464f-be9d-58f11bf3418b.sketch_text.stroke-165"),sQuery(id+"F2.wireOp",EDGE,"fcba4419-a2ee-464f-be9d-58f11bf3418b.sketch_text.stroke-166"),sQuery(id+"F2.wireOp",EDGE,"fcba4419-a2ee-464f-be9d-58f11bf3418b.sketch_text.stroke-167"),sQuery(id+"F2.wireOp",EDGE,"fcba4419-a2ee-464f-be9d-58f11bf3418b.sketch_text.stroke-168"),sQuery(id+"F2.wireOp",EDGE,"fcba4419-a2ee-464f-be9d-58f11bf3418b.sketch_text.stroke-169"),sQuery(id+"F2.wireOp",EDGE,"fcba4419-a2ee-464f-be9d-58f11bf3418b.sketch_text.stroke-170"),sQuery(id+"F2.wireOp",EDGE,"fcba4419-a2ee-464f-be9d-58f11bf3418b.sketch_text.stroke-171"),sQuery(id+"F2.wireOp",EDGE,"fcba4419-a2ee-464f-be9d-58f11bf3418b.sketch_text.stroke-172"),sQuery(id+"F2.wireOp",EDGE,"fcba4419-a2ee-464f-be9d-58f11bf3418b.sketch_text.stroke-173"),sQuery(id+"FHMxAyK4CFUKdhS_1.wireOp",EDGE,"1cb9c079-ea9b-4899-8069-e0e3048e911d.sketch_text.stroke-0"),sQuery(id+"FHMxAyK4CFUKdhS_1.wireOp",EDGE,"1cb9c079-ea9b-4899-8069-e0e3048e911d.sketch_text.stroke-1"),sQuery(id+"FHMxAyK4CFUKdhS_1.wireOp",EDGE,"1cb9c079-ea9b-4899-8069-e0e3048e911d.sketch_text.stroke-2"),sQuery(id+"FHMxAyK4CFUKdhS_1.wireOp",EDGE,"1cb9c079-ea9b-4899-8069-e0e3048e911d.sketch_text.stroke-3"),sQuery(id+"FHMxAyK4CFUKdhS_1.wireOp",EDGE,"1cb9c079-ea9b-4899-8069-e0e3048e911d.sketch_text.stroke-4"),sQuery(id+"FHMxAyK4CFUKdhS_1.wireOp",EDGE,"1cb9c079-ea9b-4899-8069-e0e3048e911d.sketch_text.stroke-5"),sQuery(id+"FHMxAyK4CFUKdhS_1.wireOp",EDGE,"1cb9c079-ea9b-4899-8069-e0e3048e911d.sketch_text.stroke-6"),sQuery(id+"FHMxAyK4CFUKdhS_1.wireOp",EDGE,"1cb9c079-ea9b-4899-8069-e0e3048e911d.sketch_text.stroke-7"),sQuery(id+"FHMxAyK4CFUKdhS_1.wireOp",EDGE,"1cb9c079-ea9b-4899-8069-e0e3048e911d.sketch_text.stroke-8"),sQuery(id+"FHMxAyK4CFUKdhS_1.wireOp",EDGE,"1cb9c079-ea9b-4899-8069-e0e3048e911d.sketch_text.stroke-9"),sQuery(id+"FHMxAyK4CFUKdhS_1.wireOp",EDGE,"1cb9c079-ea9b-4899-8069-e0e3048e911d.sketch_text.stroke-10"),sQuery(id+"FHMxAyK4CFUKdhS_1.wireOp",EDGE,"1cb9c079-ea9b-4899-8069-e0e3048e911d.sketch_text.stroke-11"),sQuery(id+"FHMxAyK4CFUKdhS_1.wireOp",EDGE,"1cb9c079-ea9b-4899-8069-e0e3048e911d.sketch_text.stroke-12"),sQuery(id+"FHMxAyK4CFUKdhS_1.wireOp",EDGE,"1cb9c079-ea9b-4899-8069-e0e3048e911d.sketch_text.stroke-13"),sQuery(id+"FHMxAyK4CFUKdhS_1.wireOp",EDGE,"1cb9c079-ea9b-4899-8069-e0e3048e911d.sketch_text.stroke-14"),sQuery(id+"FHMxAyK4CFUKdhS_1.wireOp",EDGE,"1cb9c079-ea9b-4899-8069-e0e3048e911d.sketch_text.stroke-15"),sQuery(id+"FHMxAyK4CFUKdhS_1.wireOp",EDGE,"1cb9c079-ea9b-4899-8069-e0e3048e911d.sketch_text.stroke-16"),sQuery(id+"FHMxAyK4CFUKdhS_1.wireOp",EDGE,"1cb9c079-ea9b-4899-8069-e0e3048e911d.sketch_text.stroke-17"),sQuery(id+"FHMxAyK4CFUKdhS_1.wireOp",EDGE,"1cb9c079-ea9b-4899-8069-e0e3048e911d.sketch_text.stroke-18"),sQuery(id+"FHMxAyK4CFUKdhS_1.wireOp",EDGE,"1cb9c079-ea9b-4899-8069-e0e3048e911d.sketch_text.stroke-19"),sQuery(id+"FHMxAyK4CFUKdhS_1.wireOp",EDGE,"1cb9c079-ea9b-4899-8069-e0e3048e911d.sketch_text.stroke-20"),sQuery(id+"FHMxAyK4CFUKdhS_1.wireOp",EDGE,"1cb9c079-ea9b-4899-8069-e0e3048e911d.sketch_text.stroke-21"),sQuery(id+"FHMxAyK4CFUKdhS_1.wireOp",EDGE,"1cb9c079-ea9b-4899-8069-e0e3048e911d.sketch_text.stroke-22"),sQuery(id+"FHMxAyK4CFUKdhS_1.wireOp",EDGE,"1cb9c079-ea9b-4899-8069-e0e3048e911d.sketch_text.stroke-23"),sQuery(id+"FHMxAyK4CFUKdhS_1.wireOp",EDGE,"1cb9c079-ea9b-4899-8069-e0e3048e911d.sketch_text.stroke-24"),sQuery(id+"FHMxAyK4CFUKdhS_1.wireOp",EDGE,"1cb9c079-ea9b-4899-8069-e0e3048e911d.sketch_text.stroke-25"),sQuery(id+"FHMxAyK4CFUKdhS_1.wireOp",EDGE,"1cb9c079-ea9b-4899-8069-e0e3048e911d.sketch_text.stroke-26"),sQuery(id+"FHMxAyK4CFUKdhS_1.wireOp",EDGE,"1cb9c079-ea9b-4899-8069-e0e3048e911d.sketch_text.stroke-27"),sQuery(id+"FHMxAyK4CFUKdhS_1.wireOp",EDGE,"1cb9c079-ea9b-4899-8069-e0e3048e911d.sketch_text.stroke-28"),sQuery(id+"FHMxAyK4CFUKdhS_1.wireOp",EDGE,"1cb9c079-ea9b-4899-8069-e0e3048e911d.sketch_text.stroke-29"),sQuery(id+"FHMxAyK4CFUKdhS_1.wireOp",EDGE,"1cb9c079-ea9b-4899-8069-e0e3048e911d.sketch_text.stroke-30"),sQuery(id+"FHMxAyK4CFUKdhS_1.wireOp",EDGE,"1cb9c079-ea9b-4899-8069-e0e3048e911d.sketch_text.stroke-31"),sQuery(id+"FHMxAyK4CFUKdhS_1.wireOp",EDGE,"1cb9c079-ea9b-4899-8069-e0e3048e911d.sketch_text.stroke-32"),sQuery(id+"FHMxAyK4CFUKdhS_1.wireOp",EDGE,"1cb9c079-ea9b-4899-8069-e0e3048e911d.sketch_text.stroke-33"),sQuery(id+"FHMxAyK4CFUKdhS_1.wireOp",EDGE,"1cb9c079-ea9b-4899-8069-e0e3048e911d.sketch_text.stroke-34"),sQuery(id+"FHMxAyK4CFUKdhS_1.wireOp",EDGE,"1cb9c079-ea9b-4899-8069-e0e3048e911d.sketch_text.stroke-35"),sQuery(id+"FHMxAyK4CFUKdhS_1.wireOp",EDGE,"1cb9c079-ea9b-4899-8069-e0e3048e911d.sketch_text.stroke-36"),sQuery(id+"FHMxAyK4CFUKdhS_1.wireOp",EDGE,"1cb9c079-ea9b-4899-8069-e0e3048e911d.sketch_text.stroke-37"),sQuery(id+"FHMxAyK4CFUKdhS_1.wireOp",EDGE,"1cb9c079-ea9b-4899-8069-e0e3048e911d.sketch_text.stroke-38"),sQuery(id+"FHMxAyK4CFUKdhS_1.wireOp",EDGE,"1cb9c079-ea9b-4899-8069-e0e3048e911d.sketch_text.stroke-39"),sQuery(id+"FHMxAyK4CFUKdhS_1.wireOp",EDGE,"1cb9c079-ea9b-4899-8069-e0e3048e911d.sketch_text.stroke-40"),sQuery(id+"FHMxAyK4CFUKdhS_1.wireOp",EDGE,"1cb9c079-ea9b-4899-8069-e0e3048e911d.sketch_text.stroke-41"),sQuery(id+"FHMxAyK4CFUKdhS_1.wireOp",EDGE,"1cb9c079-ea9b-4899-8069-e0e3048e911d.sketch_text.stroke-42"),sQuery(id+"FHMxAyK4CFUKdhS_1.wireOp",EDGE,"1cb9c079-ea9b-4899-8069-e0e3048e911d.sketch_text.stroke-43"),sQuery(id+"FHMxAyK4CFUKdhS_1.wireOp",EDGE,"1cb9c079-ea9b-4899-8069-e0e3048e911d.sketch_text.stroke-44"),sQuery(id+"FHMxAyK4CFUKdhS_1.wireOp",EDGE,"1cb9c079-ea9b-4899-8069-e0e3048e911d.sketch_text.stroke-45"),sQuery(id+"FHMxAyK4CFUKdhS_1.wireOp",EDGE,"1cb9c079-ea9b-4899-8069-e0e3048e911d.sketch_text.stroke-46"),sQuery(id+"FHMxAyK4CFUKdhS_1.wireOp",EDGE,"1cb9c079-ea9b-4899-8069-e0e3048e911d.sketch_text.stroke-47"),sQuery(id+"FHMxAyK4CFUKdhS_1.wireOp",EDGE,"1cb9c079-ea9b-4899-8069-e0e3048e911d.sketch_text.stroke-48"),sQuery(id+"FHMxAyK4CFUKdhS_1.wireOp",EDGE,"1cb9c079-ea9b-4899-8069-e0e3048e911d.sketch_text.stroke-49"),sQuery(id+"FHMxAyK4CFUKdhS_1.wireOp",EDGE,"1cb9c079-ea9b-4899-8069-e0e3048e911d.sketch_text.stroke-50"),sQuery(id+"FHMxAyK4CFUKdhS_1.wireOp",EDGE,"1cb9c079-ea9b-4899-8069-e0e3048e911d.sketch_text.stroke-51"),sQuery(id+"FHMxAyK4CFUKdhS_1.wireOp",EDGE,"1cb9c079-ea9b-4899-8069-e0e3048e911d.sketch_text.stroke-52"),sQuery(id+"FHMxAyK4CFUKdhS_1.wireOp",EDGE,"1cb9c079-ea9b-4899-8069-e0e3048e911d.sketch_text.stroke-53"),sQuery(id+"FHMxAyK4CFUKdhS_1.wireOp",EDGE,"1cb9c079-ea9b-4899-8069-e0e3048e911d.sketch_text.stroke-54"),sQuery(id+"FHMxAyK4CFUKdhS_1.wireOp",EDGE,"1cb9c079-ea9b-4899-8069-e0e3048e911d.sketch_text.stroke-55"),sQuery(id+"FHMxAyK4CFUKdhS_1.wireOp",EDGE,"1cb9c079-ea9b-4899-8069-e0e3048e911d.sketch_text.stroke-56"),sQuery(id+"FHMxAyK4CFUKdhS_1.wireOp",EDGE,"1cb9c079-ea9b-4899-8069-e0e3048e911d.sketch_text.stroke-57"),sQuery(id+"FHMxAyK4CFUKdhS_1.wireOp",EDGE,"1cb9c079-ea9b-4899-8069-e0e3048e911d.sketch_text.stroke-58"),sQuery(id+"FHMxAyK4CFUKdhS_1.wireOp",EDGE,"1cb9c079-ea9b-4899-8069-e0e3048e911d.sketch_text.stroke-59"),sQuery(id+"FHMxAyK4CFUKdhS_1.wireOp",EDGE,"1cb9c079-ea9b-4899-8069-e0e3048e911d.sketch_text.stroke-60"),sQuery(id+"FHMxAyK4CFUKdhS_1.wireOp",EDGE,"1cb9c079-ea9b-4899-8069-e0e3048e911d.sketch_text.stroke-61"),sQuery(id+"FHMxAyK4CFUKdhS_1.wireOp",EDGE,"1cb9c079-ea9b-4899-8069-e0e3048e911d.sketch_text.stroke-62"),sQuery(id+"FHMxAyK4CFUKdhS_1.wireOp",EDGE,"1cb9c079-ea9b-4899-8069-e0e3048e911d.sketch_text.stroke-71"),sQuery(id+"FHMxAyK4CFUKdhS_1.wireOp",EDGE,"1cb9c079-ea9b-4899-8069-e0e3048e911d.sketch_text.stroke-72"),sQuery(id+"FHMxAyK4CFUKdhS_1.wireOp",EDGE,"1cb9c079-ea9b-4899-8069-e0e3048e911d.sketch_text.stroke-73"),sQuery(id+"FHMxAyK4CFUKdhS_1.wireOp",EDGE,"1cb9c079-ea9b-4899-8069-e0e3048e911d.sketch_text.stroke-74"),sQuery(id+"FHMxAyK4CFUKdhS_1.wireOp",EDGE,"1cb9c079-ea9b-4899-8069-e0e3048e911d.sketch_text.stroke-75"),sQuery(id+"FHMxAyK4CFUKdhS_1.wireOp",EDGE,"1cb9c079-ea9b-4899-8069-e0e3048e911d.sketch_text.stroke-76"),sQuery(id+"FHMxAyK4CFUKdhS_1.wireOp",EDGE,"1cb9c079-ea9b-4899-8069-e0e3048e911d.sketch_text.stroke-77"),sQuery(id+"FHMxAyK4CFUKdhS_1.wireOp",EDGE,"1cb9c079-ea9b-4899-8069-e0e3048e911d.sketch_text.stroke-78"),sQuery(id+"FHMxAyK4CFUKdhS_1.wireOp",EDGE,"1cb9c079-ea9b-4899-8069-e0e3048e911d.sketch_text.stroke-79"),sQuery(id+"FHMxAyK4CFUKdhS_1.wireOp",EDGE,"1cb9c079-ea9b-4899-8069-e0e3048e911d.sketch_text.stroke-80"),sQuery(id+"FHMxAyK4CFUKdhS_1.wireOp",EDGE,"1cb9c079-ea9b-4899-8069-e0e3048e911d.sketch_text.stroke-81"),sQuery(id+"FHMxAyK4CFUKdhS_1.wireOp",EDGE,"1cb9c079-ea9b-4899-8069-e0e3048e911d.sketch_text.stroke-82"),sQuery(id+"FHMxAyK4CFUKdhS_1.wireOp",EDGE,"1cb9c079-ea9b-4899-8069-e0e3048e911d.sketch_text.stroke-83"),sQuery(id+"FHMxAyK4CFUKdhS_1.wireOp",EDGE,"1cb9c079-ea9b-4899-8069-e0e3048e911d.sketch_text.stroke-84"),sQuery(id+"FHMxAyK4CFUKdhS_1.wireOp",EDGE,"1cb9c079-ea9b-4899-8069-e0e3048e911d.sketch_text.stroke-85"),sQuery(id+"FHMxAyK4CFUKdhS_1.wireOp",EDGE,"1cb9c079-ea9b-4899-8069-e0e3048e911d.sketch_text.stroke-86"),sQuery(id+"FHMxAyK4CFUKdhS_1.wireOp",EDGE,"1cb9c079-ea9b-4899-8069-e0e3048e911d.sketch_text.stroke-87"),sQuery(id+"FHMxAyK4CFUKdhS_1.wireOp",EDGE,"1cb9c079-ea9b-4899-8069-e0e3048e911d.sketch_text.stroke-88"),sQuery(id+"FHMxAyK4CFUKdhS_1.wireOp",EDGE,"1cb9c079-ea9b-4899-8069-e0e3048e911d.sketch_text.stroke-89"),sQuery(id+"FHMxAyK4CFUKdhS_1.wireOp",EDGE,"1cb9c079-ea9b-4899-8069-e0e3048e911d.sketch_text.stroke-90"),sQuery(id+"FHMxAyK4CFUKdhS_1.wireOp",EDGE,"1cb9c079-ea9b-4899-8069-e0e3048e911d.sketch_text.stroke-91"),sQuery(id+"FHMxAyK4CFUKdhS_1.wireOp",EDGE,"1cb9c079-ea9b-4899-8069-e0e3048e911d.sketch_text.stroke-92"),sQuery(id+"FHMxAyK4CFUKdhS_1.wireOp",EDGE,"1cb9c079-ea9b-4899-8069-e0e3048e911d.sketch_text.stroke-93"),sQuery(id+"FHMxAyK4CFUKdhS_1.wireOp",EDGE,"1cb9c079-ea9b-4899-8069-e0e3048e911d.sketch_text.stroke-94"),sQuery(id+"FHMxAyK4CFUKdhS_1.wireOp",EDGE,"1cb9c079-ea9b-4899-8069-e0e3048e911d.sketch_text.stroke-95"),sQuery(id+"FHMxAyK4CFUKdhS_1.wireOp",EDGE,"1cb9c079-ea9b-4899-8069-e0e3048e911d.sketch_text.stroke-96"),sQuery(id+"FHMxAyK4CFUKdhS_1.wireOp",EDGE,"1cb9c079-ea9b-4899-8069-e0e3048e911d.sketch_text.stroke-97"),sQuery(id+"FHMxAyK4CFUKdhS_1.wireOp",EDGE,"1cb9c079-ea9b-4899-8069-e0e3048e911d.sketch_text.stroke-103"),sQuery(id+"FHMxAyK4CFUKdhS_1.wireOp",EDGE,"1cb9c079-ea9b-4899-8069-e0e3048e911d.sketch_text.stroke-104"),sQuery(id+"FHMxAyK4CFUKdhS_1.wireOp",EDGE,"1cb9c079-ea9b-4899-8069-e0e3048e911d.sketch_text.stroke-105"),sQuery(id+"FHMxAyK4CFUKdhS_1.wireOp",EDGE,"1cb9c079-ea9b-4899-8069-e0e3048e911d.sketch_text.stroke-106"),sQuery(id+"FHMxAyK4CFUKdhS_1.wireOp",EDGE,"1cb9c079-ea9b-4899-8069-e0e3048e911d.sketch_text.stroke-107"),sQuery(id+"FHMxAyK4CFUKdhS_1.wireOp",EDGE,"1cb9c079-ea9b-4899-8069-e0e3048e911d.sketch_text.stroke-108"),sQuery(id+"FHMxAyK4CFUKdhS_1.wireOp",EDGE,"1cb9c079-ea9b-4899-8069-e0e3048e911d.sketch_text.stroke-109"),sQuery(id+"FHMxAyK4CFUKdhS_1.wireOp",EDGE,"1cb9c079-ea9b-4899-8069-e0e3048e911d.sketch_text.stroke-110"),sQuery(id+"FHMxAyK4CFUKdhS_1.wireOp",EDGE,"1cb9c079-ea9b-4899-8069-e0e3048e911d.sketch_text.stroke-111"),sQuery(id+"FHMxAyK4CFUKdhS_1.wireOp",EDGE,"1cb9c079-ea9b-4899-8069-e0e3048e911d.sketch_text.stroke-112"),sQuery(id+"FHMxAyK4CFUKdhS_1.wireOp",EDGE,"1cb9c079-ea9b-4899-8069-e0e3048e911d.sketch_text.stroke-113"),sQuery(id+"FHMxAyK4CFUKdhS_1.wireOp",EDGE,"1cb9c079-ea9b-4899-8069-e0e3048e911d.sketch_text.stroke-114"),sQuery(id+"FHMxAyK4CFUKdhS_1.wireOp",EDGE,"1cb9c079-ea9b-4899-8069-e0e3048e911d.sketch_text.stroke-115"),sQuery(id+"FHMxAyK4CFUKdhS_1.wireOp",EDGE,"1cb9c079-ea9b-4899-8069-e0e3048e911d.sketch_text.stroke-116"),sQuery(id+"FHMxAyK4CFUKdhS_1.wireOp",EDGE,"1cb9c079-ea9b-4899-8069-e0e3048e911d.sketch_text.stroke-117"),sQuery(id+"FHMxAyK4CFUKdhS_1.wireOp",EDGE,"1cb9c079-ea9b-4899-8069-e0e3048e911d.sketch_text.stroke-118"),sQuery(id+"FHMxAyK4CFUKdhS_1.wireOp",EDGE,"1cb9c079-ea9b-4899-8069-e0e3048e911d.sketch_text.stroke-119"),sQuery(id+"FHMxAyK4CFUKdhS_1.wireOp",EDGE,"1cb9c079-ea9b-4899-8069-e0e3048e911d.sketch_text.stroke-120"),sQuery(id+"FHMxAyK4CFUKdhS_1.wireOp",EDGE,"1cb9c079-ea9b-4899-8069-e0e3048e911d.sketch_text.stroke-121"),sQuery(id+"FHMxAyK4CFUKdhS_1.wireOp",EDGE,"1cb9c079-ea9b-4899-8069-e0e3048e911d.sketch_text.stroke-122"),sQuery(id+"FHMxAyK4CFUKdhS_1.wireOp",EDGE,"1cb9c079-ea9b-4899-8069-e0e3048e911d.sketch_text.stroke-123"),sQuery(id+"FHMxAyK4CFUKdhS_1.wireOp",EDGE,"1cb9c079-ea9b-4899-8069-e0e3048e911d.sketch_text.stroke-124"),sQuery(id+"FHMxAyK4CFUKdhS_1.wireOp",EDGE,"1cb9c079-ea9b-4899-8069-e0e3048e911d.sketch_text.stroke-125"),sQuery(id+"FHMxAyK4CFUKdhS_1.wireOp",EDGE,"1cb9c079-ea9b-4899-8069-e0e3048e911d.sketch_text.stroke-126"),sQuery(id+"FHMxAyK4CFUKdhS_1.wireOp",EDGE,"1cb9c079-ea9b-4899-8069-e0e3048e911d.sketch_text.stroke-127"),sQuery(id+"FHMxAyK4CFUKdhS_1.wireOp",EDGE,"1cb9c079-ea9b-4899-8069-e0e3048e911d.sketch_text.stroke-128"),sQuery(id+"FHMxAyK4CFUKdhS_1.wireOp",EDGE,"1cb9c079-ea9b-4899-8069-e0e3048e911d.sketch_text.stroke-129"),sQuery(id+"FHMxAyK4CFUKdhS_1.wireOp",EDGE,"1cb9c079-ea9b-4899-8069-e0e3048e911d.sketch_text.stroke-130"),sQuery(id+"FHMxAyK4CFUKdhS_1.wireOp",EDGE,"1cb9c079-ea9b-4899-8069-e0e3048e911d.sketch_text.stroke-131"),sQuery(id+"FHMxAyK4CFUKdhS_1.wireOp",EDGE,"1cb9c079-ea9b-4899-8069-e0e3048e911d.sketch_text.stroke-132"),sQuery(id+"FHMxAyK4CFUKdhS_1.wireOp",EDGE,"1cb9c079-ea9b-4899-8069-e0e3048e911d.sketch_text.stroke-133"),sQuery(id+"FHMxAyK4CFUKdhS_1.wireOp",EDGE,"1cb9c079-ea9b-4899-8069-e0e3048e911d.sketch_text.stroke-134"),sQuery(id+"FHMxAyK4CFUKdhS_1.wireOp",EDGE,"1cb9c079-ea9b-4899-8069-e0e3048e911d.sketch_text.stroke-135"),sQuery(id+"FHMxAyK4CFUKdhS_1.wireOp",EDGE,"1cb9c079-ea9b-4899-8069-e0e3048e911d.sketch_text.stroke-136"),sQuery(id+"FHMxAyK4CFUKdhS_1.wireOp",EDGE,"1cb9c079-ea9b-4899-8069-e0e3048e911d.sketch_text.stroke-137"),sQuery(id+"FHMxAyK4CFUKdhS_1.wireOp",EDGE,"1cb9c079-ea9b-4899-8069-e0e3048e911d.sketch_text.stroke-138"),sQuery(id+"FHMxAyK4CFUKdhS_1.wireOp",EDGE,"1cb9c079-ea9b-4899-8069-e0e3048e911d.sketch_text.stroke-139"),sQuery(id+"FHMxAyK4CFUKdhS_1.wireOp",EDGE,"1cb9c079-ea9b-4899-8069-e0e3048e911d.sketch_text.stroke-140"),sQuery(id+"FHMxAyK4CFUKdhS_1.wireOp",EDGE,"1cb9c079-ea9b-4899-8069-e0e3048e911d.sketch_text.stroke-141"),sQuery(id+"FHMxAyK4CFUKdhS_1.wireOp",EDGE,"1cb9c079-ea9b-4899-8069-e0e3048e911d.sketch_text.stroke-142"),sQuery(id+"FHMxAyK4CFUKdhS_1.wireOp",EDGE,"1cb9c079-ea9b-4899-8069-e0e3048e911d.sketch_text.stroke-143"),sQuery(id+"FHMxAyK4CFUKdhS_1.wireOp",EDGE,"1cb9c079-ea9b-4899-8069-e0e3048e911d.sketch_text.stroke-144"),sQuery(id+"FHMxAyK4CFUKdhS_1.wireOp",EDGE,"1cb9c079-ea9b-4899-8069-e0e3048e911d.sketch_text.stroke-145"),sQuery(id+"FHMxAyK4CFUKdhS_1.wireOp",EDGE,"1cb9c079-ea9b-4899-8069-e0e3048e911d.sketch_text.stroke-146"),sQuery(id+"FHMxAyK4CFUKdhS_1.wireOp",EDGE,"1cb9c079-ea9b-4899-8069-e0e3048e911d.sketch_text.stroke-147"),sQuery(id+"FHMxAyK4CFUKdhS_1.wireOp",EDGE,"1cb9c079-ea9b-4899-8069-e0e3048e911d.sketch_text.stroke-148"),sQuery(id+"FHMxAyK4CFUKdhS_1.wireOp",EDGE,"1cb9c079-ea9b-4899-8069-e0e3048e911d.sketch_text.stroke-149"),sQuery(id+"FHMxAyK4CFUKdhS_1.wireOp",EDGE,"1cb9c079-ea9b-4899-8069-e0e3048e911d.sketch_text.stroke-150"),sQuery(id+"FHMxAyK4CFUKdhS_1.wireOp",EDGE,"1cb9c079-ea9b-4899-8069-e0e3048e911d.sketch_text.stroke-151"),sQuery(id+"FHMxAyK4CFUKdhS_1.wireOp",EDGE,"1cb9c079-ea9b-4899-8069-e0e3048e911d.sketch_text.stroke-152"),sQuery(id+"FHMxAyK4CFUKdhS_1.wireOp",EDGE,"1cb9c079-ea9b-4899-8069-e0e3048e911d.sketch_text.stroke-153"),sQuery(id+"FHMxAyK4CFUKdhS_1.wireOp",EDGE,"1cb9c079-ea9b-4899-8069-e0e3048e911d.sketch_text.stroke-159"),sQuery(id+"FHMxAyK4CFUKdhS_1.wireOp",EDGE,"1cb9c079-ea9b-4899-8069-e0e3048e911d.sketch_text.stroke-160"),sQuery(id+"FHMxAyK4CFUKdhS_1.wireOp",EDGE,"1cb9c079-ea9b-4899-8069-e0e3048e911d.sketch_text.stroke-161"),sQuery(id+"FHMxAyK4CFUKdhS_1.wireOp",EDGE,"1cb9c079-ea9b-4899-8069-e0e3048e911d.sketch_text.stroke-162"),sQuery(id+"FHMxAyK4CFUKdhS_1.wireOp",EDGE,"1cb9c079-ea9b-4899-8069-e0e3048e911d.sketch_text.stroke-163"),sQuery(id+"FHMxAyK4CFUKdhS_1.wireOp",EDGE,"1cb9c079-ea9b-4899-8069-e0e3048e911d.sketch_text.stroke-164"),sQuery(id+"FHMxAyK4CFUKdhS_1.wireOp",EDGE,"1cb9c079-ea9b-4899-8069-e0e3048e911d.sketch_text.stroke-165"),sQuery(id+"FHMxAyK4CFUKdhS_1.wireOp",EDGE,"1cb9c079-ea9b-4899-8069-e0e3048e911d.sketch_text.stroke-166"),sQuery(id+"FHMxAyK4CFUKdhS_1.wireOp",EDGE,"1cb9c079-ea9b-4899-8069-e0e3048e911d.sketch_text.stroke-167"),sQuery(id+"FHMxAyK4CFUKdhS_1.wireOp",EDGE,"1cb9c079-ea9b-4899-8069-e0e3048e911d.sketch_text.stroke-168"),sQuery(id+"FHMxAyK4CFUKdhS_1.wireOp",EDGE,"1cb9c079-ea9b-4899-8069-e0e3048e911d.sketch_text.stroke-169"),sQuery(id+"FHMxAyK4CFUKdhS_1.wireOp",EDGE,"1cb9c079-ea9b-4899-8069-e0e3048e911d.sketch_text.stroke-170"),sQuery(id+"FHMxAyK4CFUKdhS_1.wireOp",EDGE,"1cb9c079-ea9b-4899-8069-e0e3048e911d.sketch_text.stroke-171"),sQuery(id+"FHMxAyK4CFUKdhS_1.wireOp",EDGE,"1cb9c079-ea9b-4899-8069-e0e3048e911d.sketch_text.stroke-172"),sQuery(id+"FHMxAyK4CFUKdhS_1.wireOp",EDGE,"1cb9c079-ea9b-4899-8069-e0e3048e911d.sketch_text.stroke-173"),sQuery(id+"FHMxAyK4CFUKdhS_1.wireOp",EDGE,"1cb9c079-ea9b-4899-8069-e0e3048e911d.sketch_text.stroke-174"),sQuery(id+"FHMxAyK4CFUKdhS_1.wireOp",EDGE,"1cb9c079-ea9b-4899-8069-e0e3048e911d.sketch_text.stroke-175"),sQuery(id+"FHMxAyK4CFUKdhS_1.wireOp",EDGE,"1cb9c079-ea9b-4899-8069-e0e3048e911d.sketch_text.stroke-176"),sQuery(id+"FHMxAyK4CFUKdhS_1.wireOp",EDGE,"1cb9c079-ea9b-4899-8069-e0e3048e911d.sketch_text.stroke-177"),sQuery(id+"FHMxAyK4CFUKdhS_1.wireOp",EDGE,"1cb9c079-ea9b-4899-8069-e0e3048e911d.sketch_text.stroke-178"),sQuery(id+"FHMxAyK4CFUKdhS_1.wireOp",EDGE,"1cb9c079-ea9b-4899-8069-e0e3048e911d.sketch_text.stroke-179"),sQuery(id+"FHMxAyK4CFUKdhS_1.wireOp",EDGE,"1cb9c079-ea9b-4899-8069-e0e3048e911d.sketch_text.stroke-180"),subQ2,sQuery(id+"F3.wireOp",EDGE,"E29")])],"isStart":true})]),OD(0.0)],"derivedFrom":makeQuery(id+"F1.opExtrude","CAP_EDGE",EDGE,{"disambiguationData":[OSD([subQ0])],"isStart":false})});}
            var Q26;
            {var subQ0=sQuery(id+"F0.wireOp",EDGE,"E0.top");var subQ1=sQuery(id+"F0.wireOp",EDGE,"E0.bottom");var subQ2=sQuery(id+"F3.wireOp",EDGE,"E29");Q26=makeQuery(id+"F4.boolean.opBoolean","SPLIT",EDGE,{"disambiguationData":[TD([makeQuery(id+"F1.opExtrude","CAP_FACE",FACE,{"disambiguationData":[OSD([subQ1,subQ0,sQuery(id+"F0.wireOp",EDGE,"E0.left"),sQuery(id+"F0.wireOp",EDGE,"E0.right")])],"isStart":false}),makeQuery(id+"F1.opExtrude","SWEPT_FACE",FACE,{"disambiguationData":[OSD([subQ0])]}),makeQuery(id+"F4.opExtrude","CAP_FACE",FACE,{"disambiguationData":[OSD([subQ1,sQuery(id+"F2.wireOp",EDGE,"fcba4419-a2ee-464f-be9d-58f11bf3418b.sketch_text.stroke-0"),sQuery(id+"F2.wireOp",EDGE,"fcba4419-a2ee-464f-be9d-58f11bf3418b.sketch_text.stroke-1"),sQuery(id+"F2.wireOp",EDGE,"fcba4419-a2ee-464f-be9d-58f11bf3418b.sketch_text.stroke-2"),sQuery(id+"F2.wireOp",EDGE,"fcba4419-a2ee-464f-be9d-58f11bf3418b.sketch_text.stroke-3"),sQuery(id+"F2.wireOp",EDGE,"fcba4419-a2ee-464f-be9d-58f11bf3418b.sketch_text.stroke-4"),sQuery(id+"F2.wireOp",EDGE,"fcba4419-a2ee-464f-be9d-58f11bf3418b.sketch_text.stroke-5"),sQuery(id+"F2.wireOp",EDGE,"fcba4419-a2ee-464f-be9d-58f11bf3418b.sketch_text.stroke-6"),sQuery(id+"F2.wireOp",EDGE,"fcba4419-a2ee-464f-be9d-58f11bf3418b.sketch_text.stroke-7"),sQuery(id+"F2.wireOp",EDGE,"fcba4419-a2ee-464f-be9d-58f11bf3418b.sketch_text.stroke-8"),sQuery(id+"F2.wireOp",EDGE,"fcba4419-a2ee-464f-be9d-58f11bf3418b.sketch_text.stroke-9"),sQuery(id+"F2.wireOp",EDGE,"fcba4419-a2ee-464f-be9d-58f11bf3418b.sketch_text.stroke-10"),sQuery(id+"F2.wireOp",EDGE,"fcba4419-a2ee-464f-be9d-58f11bf3418b.sketch_text.stroke-11"),sQuery(id+"F2.wireOp",EDGE,"fcba4419-a2ee-464f-be9d-58f11bf3418b.sketch_text.stroke-12"),sQuery(id+"F2.wireOp",EDGE,"fcba4419-a2ee-464f-be9d-58f11bf3418b.sketch_text.stroke-13"),sQuery(id+"F2.wireOp",EDGE,"fcba4419-a2ee-464f-be9d-58f11bf3418b.sketch_text.stroke-14"),sQuery(id+"F2.wireOp",EDGE,"fcba4419-a2ee-464f-be9d-58f11bf3418b.sketch_text.stroke-15"),sQuery(id+"F2.wireOp",EDGE,"fcba4419-a2ee-464f-be9d-58f11bf3418b.sketch_text.stroke-16"),sQuery(id+"F2.wireOp",EDGE,"fcba4419-a2ee-464f-be9d-58f11bf3418b.sketch_text.stroke-17"),sQuery(id+"F2.wireOp",EDGE,"fcba4419-a2ee-464f-be9d-58f11bf3418b.sketch_text.stroke-18"),sQuery(id+"F2.wireOp",EDGE,"fcba4419-a2ee-464f-be9d-58f11bf3418b.sketch_text.stroke-19"),sQuery(id+"F2.wireOp",EDGE,"fcba4419-a2ee-464f-be9d-58f11bf3418b.sketch_text.stroke-20"),sQuery(id+"F2.wireOp",EDGE,"fcba4419-a2ee-464f-be9d-58f11bf3418b.sketch_text.stroke-21"),sQuery(id+"F2.wireOp",EDGE,"fcba4419-a2ee-464f-be9d-58f11bf3418b.sketch_text.stroke-22"),sQuery(id+"F2.wireOp",EDGE,"fcba4419-a2ee-464f-be9d-58f11bf3418b.sketch_text.stroke-23"),sQuery(id+"F2.wireOp",EDGE,"fcba4419-a2ee-464f-be9d-58f11bf3418b.sketch_text.stroke-24"),sQuery(id+"F2.wireOp",EDGE,"fcba4419-a2ee-464f-be9d-58f11bf3418b.sketch_text.stroke-25"),sQuery(id+"F2.wireOp",EDGE,"fcba4419-a2ee-464f-be9d-58f11bf3418b.sketch_text.stroke-26"),sQuery(id+"F2.wireOp",EDGE,"fcba4419-a2ee-464f-be9d-58f11bf3418b.sketch_text.stroke-27"),sQuery(id+"F2.wireOp",EDGE,"fcba4419-a2ee-464f-be9d-58f11bf3418b.sketch_text.stroke-28"),sQuery(id+"F2.wireOp",EDGE,"fcba4419-a2ee-464f-be9d-58f11bf3418b.sketch_text.stroke-29"),sQuery(id+"F2.wireOp",EDGE,"fcba4419-a2ee-464f-be9d-58f11bf3418b.sketch_text.stroke-30"),sQuery(id+"F2.wireOp",EDGE,"fcba4419-a2ee-464f-be9d-58f11bf3418b.sketch_text.stroke-31"),sQuery(id+"F2.wireOp",EDGE,"fcba4419-a2ee-464f-be9d-58f11bf3418b.sketch_text.stroke-32"),sQuery(id+"F2.wireOp",EDGE,"fcba4419-a2ee-464f-be9d-58f11bf3418b.sketch_text.stroke-33"),sQuery(id+"F2.wireOp",EDGE,"fcba4419-a2ee-464f-be9d-58f11bf3418b.sketch_text.stroke-34"),sQuery(id+"F2.wireOp",EDGE,"fcba4419-a2ee-464f-be9d-58f11bf3418b.sketch_text.stroke-35"),sQuery(id+"F2.wireOp",EDGE,"fcba4419-a2ee-464f-be9d-58f11bf3418b.sketch_text.stroke-36"),sQuery(id+"F2.wireOp",EDGE,"fcba4419-a2ee-464f-be9d-58f11bf3418b.sketch_text.stroke-37"),sQuery(id+"F2.wireOp",EDGE,"fcba4419-a2ee-464f-be9d-58f11bf3418b.sketch_text.stroke-38"),sQuery(id+"F2.wireOp",EDGE,"fcba4419-a2ee-464f-be9d-58f11bf3418b.sketch_text.stroke-39"),sQuery(id+"F2.wireOp",EDGE,"fcba4419-a2ee-464f-be9d-58f11bf3418b.sketch_text.stroke-40"),sQuery(id+"F2.wireOp",EDGE,"fcba4419-a2ee-464f-be9d-58f11bf3418b.sketch_text.stroke-41"),sQuery(id+"F2.wireOp",EDGE,"fcba4419-a2ee-464f-be9d-58f11bf3418b.sketch_text.stroke-42"),sQuery(id+"F2.wireOp",EDGE,"fcba4419-a2ee-464f-be9d-58f11bf3418b.sketch_text.stroke-43"),sQuery(id+"F2.wireOp",EDGE,"fcba4419-a2ee-464f-be9d-58f11bf3418b.sketch_text.stroke-44"),sQuery(id+"F2.wireOp",EDGE,"fcba4419-a2ee-464f-be9d-58f11bf3418b.sketch_text.stroke-45"),sQuery(id+"F2.wireOp",EDGE,"fcba4419-a2ee-464f-be9d-58f11bf3418b.sketch_text.stroke-46"),sQuery(id+"F2.wireOp",EDGE,"fcba4419-a2ee-464f-be9d-58f11bf3418b.sketch_text.stroke-47"),sQuery(id+"F2.wireOp",EDGE,"fcba4419-a2ee-464f-be9d-58f11bf3418b.sketch_text.stroke-48"),sQuery(id+"F2.wireOp",EDGE,"fcba4419-a2ee-464f-be9d-58f11bf3418b.sketch_text.stroke-49"),sQuery(id+"F2.wireOp",EDGE,"fcba4419-a2ee-464f-be9d-58f11bf3418b.sketch_text.stroke-50"),sQuery(id+"F2.wireOp",EDGE,"fcba4419-a2ee-464f-be9d-58f11bf3418b.sketch_text.stroke-51"),sQuery(id+"F2.wireOp",EDGE,"fcba4419-a2ee-464f-be9d-58f11bf3418b.sketch_text.stroke-52"),sQuery(id+"F2.wireOp",EDGE,"fcba4419-a2ee-464f-be9d-58f11bf3418b.sketch_text.stroke-53"),sQuery(id+"F2.wireOp",EDGE,"fcba4419-a2ee-464f-be9d-58f11bf3418b.sketch_text.stroke-54"),sQuery(id+"F2.wireOp",EDGE,"fcba4419-a2ee-464f-be9d-58f11bf3418b.sketch_text.stroke-55"),sQuery(id+"F2.wireOp",EDGE,"fcba4419-a2ee-464f-be9d-58f11bf3418b.sketch_text.stroke-56"),sQuery(id+"F2.wireOp",EDGE,"fcba4419-a2ee-464f-be9d-58f11bf3418b.sketch_text.stroke-57"),sQuery(id+"F2.wireOp",EDGE,"fcba4419-a2ee-464f-be9d-58f11bf3418b.sketch_text.stroke-58"),sQuery(id+"F2.wireOp",EDGE,"fcba4419-a2ee-464f-be9d-58f11bf3418b.sketch_text.stroke-59"),sQuery(id+"F2.wireOp",EDGE,"fcba4419-a2ee-464f-be9d-58f11bf3418b.sketch_text.stroke-60"),sQuery(id+"F2.wireOp",EDGE,"fcba4419-a2ee-464f-be9d-58f11bf3418b.sketch_text.stroke-61"),sQuery(id+"F2.wireOp",EDGE,"fcba4419-a2ee-464f-be9d-58f11bf3418b.sketch_text.stroke-62"),sQuery(id+"F2.wireOp",EDGE,"fcba4419-a2ee-464f-be9d-58f11bf3418b.sketch_text.stroke-63"),sQuery(id+"F2.wireOp",EDGE,"fcba4419-a2ee-464f-be9d-58f11bf3418b.sketch_text.stroke-64"),sQuery(id+"F2.wireOp",EDGE,"fcba4419-a2ee-464f-be9d-58f11bf3418b.sketch_text.stroke-65"),sQuery(id+"F2.wireOp",EDGE,"fcba4419-a2ee-464f-be9d-58f11bf3418b.sketch_text.stroke-66"),sQuery(id+"F2.wireOp",EDGE,"fcba4419-a2ee-464f-be9d-58f11bf3418b.sketch_text.stroke-67"),sQuery(id+"F2.wireOp",EDGE,"fcba4419-a2ee-464f-be9d-58f11bf3418b.sketch_text.stroke-68"),sQuery(id+"F2.wireOp",EDGE,"fcba4419-a2ee-464f-be9d-58f11bf3418b.sketch_text.stroke-69"),sQuery(id+"F2.wireOp",EDGE,"fcba4419-a2ee-464f-be9d-58f11bf3418b.sketch_text.stroke-70"),sQuery(id+"F2.wireOp",EDGE,"fcba4419-a2ee-464f-be9d-58f11bf3418b.sketch_text.stroke-71"),sQuery(id+"F2.wireOp",EDGE,"fcba4419-a2ee-464f-be9d-58f11bf3418b.sketch_text.stroke-72"),sQuery(id+"F2.wireOp",EDGE,"fcba4419-a2ee-464f-be9d-58f11bf3418b.sketch_text.stroke-73"),sQuery(id+"F2.wireOp",EDGE,"fcba4419-a2ee-464f-be9d-58f11bf3418b.sketch_text.stroke-74"),sQuery(id+"F2.wireOp",EDGE,"fcba4419-a2ee-464f-be9d-58f11bf3418b.sketch_text.stroke-75"),sQuery(id+"F2.wireOp",EDGE,"fcba4419-a2ee-464f-be9d-58f11bf3418b.sketch_text.stroke-76"),sQuery(id+"F2.wireOp",EDGE,"fcba4419-a2ee-464f-be9d-58f11bf3418b.sketch_text.stroke-77"),sQuery(id+"F2.wireOp",EDGE,"fcba4419-a2ee-464f-be9d-58f11bf3418b.sketch_text.stroke-78"),sQuery(id+"F2.wireOp",EDGE,"fcba4419-a2ee-464f-be9d-58f11bf3418b.sketch_text.stroke-79"),sQuery(id+"F2.wireOp",EDGE,"fcba4419-a2ee-464f-be9d-58f11bf3418b.sketch_text.stroke-80"),sQuery(id+"F2.wireOp",EDGE,"fcba4419-a2ee-464f-be9d-58f11bf3418b.sketch_text.stroke-81"),sQuery(id+"F2.wireOp",EDGE,"fcba4419-a2ee-464f-be9d-58f11bf3418b.sketch_text.stroke-82"),sQuery(id+"F2.wireOp",EDGE,"fcba4419-a2ee-464f-be9d-58f11bf3418b.sketch_text.stroke-83"),sQuery(id+"F2.wireOp",EDGE,"fcba4419-a2ee-464f-be9d-58f11bf3418b.sketch_text.stroke-84"),sQuery(id+"F2.wireOp",EDGE,"fcba4419-a2ee-464f-be9d-58f11bf3418b.sketch_text.stroke-85"),sQuery(id+"F2.wireOp",EDGE,"fcba4419-a2ee-464f-be9d-58f11bf3418b.sketch_text.stroke-86"),sQuery(id+"F2.wireOp",EDGE,"fcba4419-a2ee-464f-be9d-58f11bf3418b.sketch_text.stroke-87"),sQuery(id+"F2.wireOp",EDGE,"fcba4419-a2ee-464f-be9d-58f11bf3418b.sketch_text.stroke-88"),sQuery(id+"F2.wireOp",EDGE,"fcba4419-a2ee-464f-be9d-58f11bf3418b.sketch_text.stroke-89"),sQuery(id+"F2.wireOp",EDGE,"fcba4419-a2ee-464f-be9d-58f11bf3418b.sketch_text.stroke-90"),sQuery(id+"F2.wireOp",EDGE,"fcba4419-a2ee-464f-be9d-58f11bf3418b.sketch_text.stroke-91"),sQuery(id+"F2.wireOp",EDGE,"fcba4419-a2ee-464f-be9d-58f11bf3418b.sketch_text.stroke-92"),sQuery(id+"F2.wireOp",EDGE,"fcba4419-a2ee-464f-be9d-58f11bf3418b.sketch_text.stroke-93"),sQuery(id+"F2.wireOp",EDGE,"fcba4419-a2ee-464f-be9d-58f11bf3418b.sketch_text.stroke-94"),sQuery(id+"F2.wireOp",EDGE,"fcba4419-a2ee-464f-be9d-58f11bf3418b.sketch_text.stroke-95"),sQuery(id+"F2.wireOp",EDGE,"fcba4419-a2ee-464f-be9d-58f11bf3418b.sketch_text.stroke-96"),sQuery(id+"F2.wireOp",EDGE,"fcba4419-a2ee-464f-be9d-58f11bf3418b.sketch_text.stroke-97"),sQuery(id+"F2.wireOp",EDGE,"fcba4419-a2ee-464f-be9d-58f11bf3418b.sketch_text.stroke-98"),sQuery(id+"F2.wireOp",EDGE,"fcba4419-a2ee-464f-be9d-58f11bf3418b.sketch_text.stroke-99"),sQuery(id+"F2.wireOp",EDGE,"fcba4419-a2ee-464f-be9d-58f11bf3418b.sketch_text.stroke-100"),sQuery(id+"F2.wireOp",EDGE,"fcba4419-a2ee-464f-be9d-58f11bf3418b.sketch_text.stroke-101"),sQuery(id+"F2.wireOp",EDGE,"fcba4419-a2ee-464f-be9d-58f11bf3418b.sketch_text.stroke-102"),sQuery(id+"F2.wireOp",EDGE,"fcba4419-a2ee-464f-be9d-58f11bf3418b.sketch_text.stroke-103"),sQuery(id+"F2.wireOp",EDGE,"fcba4419-a2ee-464f-be9d-58f11bf3418b.sketch_text.stroke-104"),sQuery(id+"F2.wireOp",EDGE,"fcba4419-a2ee-464f-be9d-58f11bf3418b.sketch_text.stroke-105"),sQuery(id+"F2.wireOp",EDGE,"fcba4419-a2ee-464f-be9d-58f11bf3418b.sketch_text.stroke-106"),sQuery(id+"F2.wireOp",EDGE,"fcba4419-a2ee-464f-be9d-58f11bf3418b.sketch_text.stroke-107"),sQuery(id+"F2.wireOp",EDGE,"fcba4419-a2ee-464f-be9d-58f11bf3418b.sketch_text.stroke-108"),sQuery(id+"F2.wireOp",EDGE,"fcba4419-a2ee-464f-be9d-58f11bf3418b.sketch_text.stroke-109"),sQuery(id+"F2.wireOp",EDGE,"fcba4419-a2ee-464f-be9d-58f11bf3418b.sketch_text.stroke-110"),sQuery(id+"F2.wireOp",EDGE,"fcba4419-a2ee-464f-be9d-58f11bf3418b.sketch_text.stroke-111"),sQuery(id+"F2.wireOp",EDGE,"fcba4419-a2ee-464f-be9d-58f11bf3418b.sketch_text.stroke-112"),sQuery(id+"F2.wireOp",EDGE,"fcba4419-a2ee-464f-be9d-58f11bf3418b.sketch_text.stroke-113"),sQuery(id+"F2.wireOp",EDGE,"fcba4419-a2ee-464f-be9d-58f11bf3418b.sketch_text.stroke-114"),sQuery(id+"F2.wireOp",EDGE,"fcba4419-a2ee-464f-be9d-58f11bf3418b.sketch_text.stroke-115"),sQuery(id+"F2.wireOp",EDGE,"fcba4419-a2ee-464f-be9d-58f11bf3418b.sketch_text.stroke-116"),sQuery(id+"F2.wireOp",EDGE,"fcba4419-a2ee-464f-be9d-58f11bf3418b.sketch_text.stroke-117"),sQuery(id+"F2.wireOp",EDGE,"fcba4419-a2ee-464f-be9d-58f11bf3418b.sketch_text.stroke-118"),sQuery(id+"F2.wireOp",EDGE,"fcba4419-a2ee-464f-be9d-58f11bf3418b.sketch_text.stroke-119"),sQuery(id+"F2.wireOp",EDGE,"fcba4419-a2ee-464f-be9d-58f11bf3418b.sketch_text.stroke-120"),sQuery(id+"F2.wireOp",EDGE,"fcba4419-a2ee-464f-be9d-58f11bf3418b.sketch_text.stroke-121"),sQuery(id+"F2.wireOp",EDGE,"fcba4419-a2ee-464f-be9d-58f11bf3418b.sketch_text.stroke-122"),sQuery(id+"F2.wireOp",EDGE,"fcba4419-a2ee-464f-be9d-58f11bf3418b.sketch_text.stroke-123"),sQuery(id+"F2.wireOp",EDGE,"fcba4419-a2ee-464f-be9d-58f11bf3418b.sketch_text.stroke-124"),sQuery(id+"F2.wireOp",EDGE,"fcba4419-a2ee-464f-be9d-58f11bf3418b.sketch_text.stroke-125"),sQuery(id+"F2.wireOp",EDGE,"fcba4419-a2ee-464f-be9d-58f11bf3418b.sketch_text.stroke-126"),sQuery(id+"F2.wireOp",EDGE,"fcba4419-a2ee-464f-be9d-58f11bf3418b.sketch_text.stroke-127"),sQuery(id+"F2.wireOp",EDGE,"fcba4419-a2ee-464f-be9d-58f11bf3418b.sketch_text.stroke-128"),sQuery(id+"F2.wireOp",EDGE,"fcba4419-a2ee-464f-be9d-58f11bf3418b.sketch_text.stroke-129"),sQuery(id+"F2.wireOp",EDGE,"fcba4419-a2ee-464f-be9d-58f11bf3418b.sketch_text.stroke-130"),sQuery(id+"F2.wireOp",EDGE,"fcba4419-a2ee-464f-be9d-58f11bf3418b.sketch_text.stroke-131"),sQuery(id+"F2.wireOp",EDGE,"fcba4419-a2ee-464f-be9d-58f11bf3418b.sketch_text.stroke-132"),sQuery(id+"F2.wireOp",EDGE,"fcba4419-a2ee-464f-be9d-58f11bf3418b.sketch_text.stroke-133"),sQuery(id+"F2.wireOp",EDGE,"fcba4419-a2ee-464f-be9d-58f11bf3418b.sketch_text.stroke-134"),sQuery(id+"F2.wireOp",EDGE,"fcba4419-a2ee-464f-be9d-58f11bf3418b.sketch_text.stroke-135"),sQuery(id+"F2.wireOp",EDGE,"fcba4419-a2ee-464f-be9d-58f11bf3418b.sketch_text.stroke-136"),sQuery(id+"F2.wireOp",EDGE,"fcba4419-a2ee-464f-be9d-58f11bf3418b.sketch_text.stroke-137"),sQuery(id+"F2.wireOp",EDGE,"fcba4419-a2ee-464f-be9d-58f11bf3418b.sketch_text.stroke-138"),sQuery(id+"F2.wireOp",EDGE,"fcba4419-a2ee-464f-be9d-58f11bf3418b.sketch_text.stroke-139"),sQuery(id+"F2.wireOp",EDGE,"fcba4419-a2ee-464f-be9d-58f11bf3418b.sketch_text.stroke-140"),sQuery(id+"F2.wireOp",EDGE,"fcba4419-a2ee-464f-be9d-58f11bf3418b.sketch_text.stroke-141"),sQuery(id+"F2.wireOp",EDGE,"fcba4419-a2ee-464f-be9d-58f11bf3418b.sketch_text.stroke-142"),sQuery(id+"F2.wireOp",EDGE,"fcba4419-a2ee-464f-be9d-58f11bf3418b.sketch_text.stroke-143"),sQuery(id+"F2.wireOp",EDGE,"fcba4419-a2ee-464f-be9d-58f11bf3418b.sketch_text.stroke-144"),sQuery(id+"F2.wireOp",EDGE,"fcba4419-a2ee-464f-be9d-58f11bf3418b.sketch_text.stroke-145"),sQuery(id+"F2.wireOp",EDGE,"fcba4419-a2ee-464f-be9d-58f11bf3418b.sketch_text.stroke-146"),sQuery(id+"F2.wireOp",EDGE,"fcba4419-a2ee-464f-be9d-58f11bf3418b.sketch_text.stroke-147"),sQuery(id+"F2.wireOp",EDGE,"fcba4419-a2ee-464f-be9d-58f11bf3418b.sketch_text.stroke-148"),sQuery(id+"F2.wireOp",EDGE,"fcba4419-a2ee-464f-be9d-58f11bf3418b.sketch_text.stroke-149"),sQuery(id+"F2.wireOp",EDGE,"fcba4419-a2ee-464f-be9d-58f11bf3418b.sketch_text.stroke-150"),sQuery(id+"F2.wireOp",EDGE,"fcba4419-a2ee-464f-be9d-58f11bf3418b.sketch_text.stroke-151"),sQuery(id+"F2.wireOp",EDGE,"fcba4419-a2ee-464f-be9d-58f11bf3418b.sketch_text.stroke-152"),sQuery(id+"F2.wireOp",EDGE,"fcba4419-a2ee-464f-be9d-58f11bf3418b.sketch_text.stroke-153"),sQuery(id+"F2.wireOp",EDGE,"fcba4419-a2ee-464f-be9d-58f11bf3418b.sketch_text.stroke-154"),sQuery(id+"F2.wireOp",EDGE,"fcba4419-a2ee-464f-be9d-58f11bf3418b.sketch_text.stroke-155"),sQuery(id+"F2.wireOp",EDGE,"fcba4419-a2ee-464f-be9d-58f11bf3418b.sketch_text.stroke-156"),sQuery(id+"F2.wireOp",EDGE,"fcba4419-a2ee-464f-be9d-58f11bf3418b.sketch_text.stroke-157"),sQuery(id+"F2.wireOp",EDGE,"fcba4419-a2ee-464f-be9d-58f11bf3418b.sketch_text.stroke-158"),sQuery(id+"F2.wireOp",EDGE,"fcba4419-a2ee-464f-be9d-58f11bf3418b.sketch_text.stroke-159"),sQuery(id+"F2.wireOp",EDGE,"fcba4419-a2ee-464f-be9d-58f11bf3418b.sketch_text.stroke-160"),sQuery(id+"F2.wireOp",EDGE,"fcba4419-a2ee-464f-be9d-58f11bf3418b.sketch_text.stroke-161"),sQuery(id+"F2.wireOp",EDGE,"fcba4419-a2ee-464f-be9d-58f11bf3418b.sketch_text.stroke-162"),sQuery(id+"F2.wireOp",EDGE,"fcba4419-a2ee-464f-be9d-58f11bf3418b.sketch_text.stroke-163"),sQuery(id+"F2.wireOp",EDGE,"fcba4419-a2ee-464f-be9d-58f11bf3418b.sketch_text.stroke-164"),sQuery(id+"F2.wireOp",EDGE,"fcba4419-a2ee-464f-be9d-58f11bf3418b.sketch_text.stroke-165"),sQuery(id+"F2.wireOp",EDGE,"fcba4419-a2ee-464f-be9d-58f11bf3418b.sketch_text.stroke-166"),sQuery(id+"F2.wireOp",EDGE,"fcba4419-a2ee-464f-be9d-58f11bf3418b.sketch_text.stroke-167"),sQuery(id+"F2.wireOp",EDGE,"fcba4419-a2ee-464f-be9d-58f11bf3418b.sketch_text.stroke-168"),sQuery(id+"F2.wireOp",EDGE,"fcba4419-a2ee-464f-be9d-58f11bf3418b.sketch_text.stroke-169"),sQuery(id+"F2.wireOp",EDGE,"fcba4419-a2ee-464f-be9d-58f11bf3418b.sketch_text.stroke-170"),sQuery(id+"F2.wireOp",EDGE,"fcba4419-a2ee-464f-be9d-58f11bf3418b.sketch_text.stroke-171"),sQuery(id+"F2.wireOp",EDGE,"fcba4419-a2ee-464f-be9d-58f11bf3418b.sketch_text.stroke-172"),sQuery(id+"F2.wireOp",EDGE,"fcba4419-a2ee-464f-be9d-58f11bf3418b.sketch_text.stroke-173"),sQuery(id+"FHMxAyK4CFUKdhS_1.wireOp",EDGE,"1cb9c079-ea9b-4899-8069-e0e3048e911d.sketch_text.stroke-0"),sQuery(id+"FHMxAyK4CFUKdhS_1.wireOp",EDGE,"1cb9c079-ea9b-4899-8069-e0e3048e911d.sketch_text.stroke-1"),sQuery(id+"FHMxAyK4CFUKdhS_1.wireOp",EDGE,"1cb9c079-ea9b-4899-8069-e0e3048e911d.sketch_text.stroke-2"),sQuery(id+"FHMxAyK4CFUKdhS_1.wireOp",EDGE,"1cb9c079-ea9b-4899-8069-e0e3048e911d.sketch_text.stroke-3"),sQuery(id+"FHMxAyK4CFUKdhS_1.wireOp",EDGE,"1cb9c079-ea9b-4899-8069-e0e3048e911d.sketch_text.stroke-4"),sQuery(id+"FHMxAyK4CFUKdhS_1.wireOp",EDGE,"1cb9c079-ea9b-4899-8069-e0e3048e911d.sketch_text.stroke-5"),sQuery(id+"FHMxAyK4CFUKdhS_1.wireOp",EDGE,"1cb9c079-ea9b-4899-8069-e0e3048e911d.sketch_text.stroke-6"),sQuery(id+"FHMxAyK4CFUKdhS_1.wireOp",EDGE,"1cb9c079-ea9b-4899-8069-e0e3048e911d.sketch_text.stroke-7"),sQuery(id+"FHMxAyK4CFUKdhS_1.wireOp",EDGE,"1cb9c079-ea9b-4899-8069-e0e3048e911d.sketch_text.stroke-8"),sQuery(id+"FHMxAyK4CFUKdhS_1.wireOp",EDGE,"1cb9c079-ea9b-4899-8069-e0e3048e911d.sketch_text.stroke-9"),sQuery(id+"FHMxAyK4CFUKdhS_1.wireOp",EDGE,"1cb9c079-ea9b-4899-8069-e0e3048e911d.sketch_text.stroke-10"),sQuery(id+"FHMxAyK4CFUKdhS_1.wireOp",EDGE,"1cb9c079-ea9b-4899-8069-e0e3048e911d.sketch_text.stroke-11"),sQuery(id+"FHMxAyK4CFUKdhS_1.wireOp",EDGE,"1cb9c079-ea9b-4899-8069-e0e3048e911d.sketch_text.stroke-12"),sQuery(id+"FHMxAyK4CFUKdhS_1.wireOp",EDGE,"1cb9c079-ea9b-4899-8069-e0e3048e911d.sketch_text.stroke-13"),sQuery(id+"FHMxAyK4CFUKdhS_1.wireOp",EDGE,"1cb9c079-ea9b-4899-8069-e0e3048e911d.sketch_text.stroke-14"),sQuery(id+"FHMxAyK4CFUKdhS_1.wireOp",EDGE,"1cb9c079-ea9b-4899-8069-e0e3048e911d.sketch_text.stroke-15"),sQuery(id+"FHMxAyK4CFUKdhS_1.wireOp",EDGE,"1cb9c079-ea9b-4899-8069-e0e3048e911d.sketch_text.stroke-16"),sQuery(id+"FHMxAyK4CFUKdhS_1.wireOp",EDGE,"1cb9c079-ea9b-4899-8069-e0e3048e911d.sketch_text.stroke-17"),sQuery(id+"FHMxAyK4CFUKdhS_1.wireOp",EDGE,"1cb9c079-ea9b-4899-8069-e0e3048e911d.sketch_text.stroke-18"),sQuery(id+"FHMxAyK4CFUKdhS_1.wireOp",EDGE,"1cb9c079-ea9b-4899-8069-e0e3048e911d.sketch_text.stroke-19"),sQuery(id+"FHMxAyK4CFUKdhS_1.wireOp",EDGE,"1cb9c079-ea9b-4899-8069-e0e3048e911d.sketch_text.stroke-20"),sQuery(id+"FHMxAyK4CFUKdhS_1.wireOp",EDGE,"1cb9c079-ea9b-4899-8069-e0e3048e911d.sketch_text.stroke-21"),sQuery(id+"FHMxAyK4CFUKdhS_1.wireOp",EDGE,"1cb9c079-ea9b-4899-8069-e0e3048e911d.sketch_text.stroke-22"),sQuery(id+"FHMxAyK4CFUKdhS_1.wireOp",EDGE,"1cb9c079-ea9b-4899-8069-e0e3048e911d.sketch_text.stroke-23"),sQuery(id+"FHMxAyK4CFUKdhS_1.wireOp",EDGE,"1cb9c079-ea9b-4899-8069-e0e3048e911d.sketch_text.stroke-24"),sQuery(id+"FHMxAyK4CFUKdhS_1.wireOp",EDGE,"1cb9c079-ea9b-4899-8069-e0e3048e911d.sketch_text.stroke-25"),sQuery(id+"FHMxAyK4CFUKdhS_1.wireOp",EDGE,"1cb9c079-ea9b-4899-8069-e0e3048e911d.sketch_text.stroke-26"),sQuery(id+"FHMxAyK4CFUKdhS_1.wireOp",EDGE,"1cb9c079-ea9b-4899-8069-e0e3048e911d.sketch_text.stroke-27"),sQuery(id+"FHMxAyK4CFUKdhS_1.wireOp",EDGE,"1cb9c079-ea9b-4899-8069-e0e3048e911d.sketch_text.stroke-28"),sQuery(id+"FHMxAyK4CFUKdhS_1.wireOp",EDGE,"1cb9c079-ea9b-4899-8069-e0e3048e911d.sketch_text.stroke-29"),sQuery(id+"FHMxAyK4CFUKdhS_1.wireOp",EDGE,"1cb9c079-ea9b-4899-8069-e0e3048e911d.sketch_text.stroke-30"),sQuery(id+"FHMxAyK4CFUKdhS_1.wireOp",EDGE,"1cb9c079-ea9b-4899-8069-e0e3048e911d.sketch_text.stroke-31"),sQuery(id+"FHMxAyK4CFUKdhS_1.wireOp",EDGE,"1cb9c079-ea9b-4899-8069-e0e3048e911d.sketch_text.stroke-32"),sQuery(id+"FHMxAyK4CFUKdhS_1.wireOp",EDGE,"1cb9c079-ea9b-4899-8069-e0e3048e911d.sketch_text.stroke-33"),sQuery(id+"FHMxAyK4CFUKdhS_1.wireOp",EDGE,"1cb9c079-ea9b-4899-8069-e0e3048e911d.sketch_text.stroke-34"),sQuery(id+"FHMxAyK4CFUKdhS_1.wireOp",EDGE,"1cb9c079-ea9b-4899-8069-e0e3048e911d.sketch_text.stroke-35"),sQuery(id+"FHMxAyK4CFUKdhS_1.wireOp",EDGE,"1cb9c079-ea9b-4899-8069-e0e3048e911d.sketch_text.stroke-36"),sQuery(id+"FHMxAyK4CFUKdhS_1.wireOp",EDGE,"1cb9c079-ea9b-4899-8069-e0e3048e911d.sketch_text.stroke-37"),sQuery(id+"FHMxAyK4CFUKdhS_1.wireOp",EDGE,"1cb9c079-ea9b-4899-8069-e0e3048e911d.sketch_text.stroke-38"),sQuery(id+"FHMxAyK4CFUKdhS_1.wireOp",EDGE,"1cb9c079-ea9b-4899-8069-e0e3048e911d.sketch_text.stroke-39"),sQuery(id+"FHMxAyK4CFUKdhS_1.wireOp",EDGE,"1cb9c079-ea9b-4899-8069-e0e3048e911d.sketch_text.stroke-40"),sQuery(id+"FHMxAyK4CFUKdhS_1.wireOp",EDGE,"1cb9c079-ea9b-4899-8069-e0e3048e911d.sketch_text.stroke-41"),sQuery(id+"FHMxAyK4CFUKdhS_1.wireOp",EDGE,"1cb9c079-ea9b-4899-8069-e0e3048e911d.sketch_text.stroke-42"),sQuery(id+"FHMxAyK4CFUKdhS_1.wireOp",EDGE,"1cb9c079-ea9b-4899-8069-e0e3048e911d.sketch_text.stroke-43"),sQuery(id+"FHMxAyK4CFUKdhS_1.wireOp",EDGE,"1cb9c079-ea9b-4899-8069-e0e3048e911d.sketch_text.stroke-44"),sQuery(id+"FHMxAyK4CFUKdhS_1.wireOp",EDGE,"1cb9c079-ea9b-4899-8069-e0e3048e911d.sketch_text.stroke-45"),sQuery(id+"FHMxAyK4CFUKdhS_1.wireOp",EDGE,"1cb9c079-ea9b-4899-8069-e0e3048e911d.sketch_text.stroke-46"),sQuery(id+"FHMxAyK4CFUKdhS_1.wireOp",EDGE,"1cb9c079-ea9b-4899-8069-e0e3048e911d.sketch_text.stroke-47"),sQuery(id+"FHMxAyK4CFUKdhS_1.wireOp",EDGE,"1cb9c079-ea9b-4899-8069-e0e3048e911d.sketch_text.stroke-48"),sQuery(id+"FHMxAyK4CFUKdhS_1.wireOp",EDGE,"1cb9c079-ea9b-4899-8069-e0e3048e911d.sketch_text.stroke-49"),sQuery(id+"FHMxAyK4CFUKdhS_1.wireOp",EDGE,"1cb9c079-ea9b-4899-8069-e0e3048e911d.sketch_text.stroke-50"),sQuery(id+"FHMxAyK4CFUKdhS_1.wireOp",EDGE,"1cb9c079-ea9b-4899-8069-e0e3048e911d.sketch_text.stroke-51"),sQuery(id+"FHMxAyK4CFUKdhS_1.wireOp",EDGE,"1cb9c079-ea9b-4899-8069-e0e3048e911d.sketch_text.stroke-52"),sQuery(id+"FHMxAyK4CFUKdhS_1.wireOp",EDGE,"1cb9c079-ea9b-4899-8069-e0e3048e911d.sketch_text.stroke-53"),sQuery(id+"FHMxAyK4CFUKdhS_1.wireOp",EDGE,"1cb9c079-ea9b-4899-8069-e0e3048e911d.sketch_text.stroke-54"),sQuery(id+"FHMxAyK4CFUKdhS_1.wireOp",EDGE,"1cb9c079-ea9b-4899-8069-e0e3048e911d.sketch_text.stroke-55"),sQuery(id+"FHMxAyK4CFUKdhS_1.wireOp",EDGE,"1cb9c079-ea9b-4899-8069-e0e3048e911d.sketch_text.stroke-56"),sQuery(id+"FHMxAyK4CFUKdhS_1.wireOp",EDGE,"1cb9c079-ea9b-4899-8069-e0e3048e911d.sketch_text.stroke-57"),sQuery(id+"FHMxAyK4CFUKdhS_1.wireOp",EDGE,"1cb9c079-ea9b-4899-8069-e0e3048e911d.sketch_text.stroke-58"),sQuery(id+"FHMxAyK4CFUKdhS_1.wireOp",EDGE,"1cb9c079-ea9b-4899-8069-e0e3048e911d.sketch_text.stroke-59"),sQuery(id+"FHMxAyK4CFUKdhS_1.wireOp",EDGE,"1cb9c079-ea9b-4899-8069-e0e3048e911d.sketch_text.stroke-60"),sQuery(id+"FHMxAyK4CFUKdhS_1.wireOp",EDGE,"1cb9c079-ea9b-4899-8069-e0e3048e911d.sketch_text.stroke-61"),sQuery(id+"FHMxAyK4CFUKdhS_1.wireOp",EDGE,"1cb9c079-ea9b-4899-8069-e0e3048e911d.sketch_text.stroke-62"),sQuery(id+"FHMxAyK4CFUKdhS_1.wireOp",EDGE,"1cb9c079-ea9b-4899-8069-e0e3048e911d.sketch_text.stroke-71"),sQuery(id+"FHMxAyK4CFUKdhS_1.wireOp",EDGE,"1cb9c079-ea9b-4899-8069-e0e3048e911d.sketch_text.stroke-72"),sQuery(id+"FHMxAyK4CFUKdhS_1.wireOp",EDGE,"1cb9c079-ea9b-4899-8069-e0e3048e911d.sketch_text.stroke-73"),sQuery(id+"FHMxAyK4CFUKdhS_1.wireOp",EDGE,"1cb9c079-ea9b-4899-8069-e0e3048e911d.sketch_text.stroke-74"),sQuery(id+"FHMxAyK4CFUKdhS_1.wireOp",EDGE,"1cb9c079-ea9b-4899-8069-e0e3048e911d.sketch_text.stroke-75"),sQuery(id+"FHMxAyK4CFUKdhS_1.wireOp",EDGE,"1cb9c079-ea9b-4899-8069-e0e3048e911d.sketch_text.stroke-76"),sQuery(id+"FHMxAyK4CFUKdhS_1.wireOp",EDGE,"1cb9c079-ea9b-4899-8069-e0e3048e911d.sketch_text.stroke-77"),sQuery(id+"FHMxAyK4CFUKdhS_1.wireOp",EDGE,"1cb9c079-ea9b-4899-8069-e0e3048e911d.sketch_text.stroke-78"),sQuery(id+"FHMxAyK4CFUKdhS_1.wireOp",EDGE,"1cb9c079-ea9b-4899-8069-e0e3048e911d.sketch_text.stroke-79"),sQuery(id+"FHMxAyK4CFUKdhS_1.wireOp",EDGE,"1cb9c079-ea9b-4899-8069-e0e3048e911d.sketch_text.stroke-80"),sQuery(id+"FHMxAyK4CFUKdhS_1.wireOp",EDGE,"1cb9c079-ea9b-4899-8069-e0e3048e911d.sketch_text.stroke-81"),sQuery(id+"FHMxAyK4CFUKdhS_1.wireOp",EDGE,"1cb9c079-ea9b-4899-8069-e0e3048e911d.sketch_text.stroke-82"),sQuery(id+"FHMxAyK4CFUKdhS_1.wireOp",EDGE,"1cb9c079-ea9b-4899-8069-e0e3048e911d.sketch_text.stroke-83"),sQuery(id+"FHMxAyK4CFUKdhS_1.wireOp",EDGE,"1cb9c079-ea9b-4899-8069-e0e3048e911d.sketch_text.stroke-84"),sQuery(id+"FHMxAyK4CFUKdhS_1.wireOp",EDGE,"1cb9c079-ea9b-4899-8069-e0e3048e911d.sketch_text.stroke-85"),sQuery(id+"FHMxAyK4CFUKdhS_1.wireOp",EDGE,"1cb9c079-ea9b-4899-8069-e0e3048e911d.sketch_text.stroke-86"),sQuery(id+"FHMxAyK4CFUKdhS_1.wireOp",EDGE,"1cb9c079-ea9b-4899-8069-e0e3048e911d.sketch_text.stroke-87"),sQuery(id+"FHMxAyK4CFUKdhS_1.wireOp",EDGE,"1cb9c079-ea9b-4899-8069-e0e3048e911d.sketch_text.stroke-88"),sQuery(id+"FHMxAyK4CFUKdhS_1.wireOp",EDGE,"1cb9c079-ea9b-4899-8069-e0e3048e911d.sketch_text.stroke-89"),sQuery(id+"FHMxAyK4CFUKdhS_1.wireOp",EDGE,"1cb9c079-ea9b-4899-8069-e0e3048e911d.sketch_text.stroke-90"),sQuery(id+"FHMxAyK4CFUKdhS_1.wireOp",EDGE,"1cb9c079-ea9b-4899-8069-e0e3048e911d.sketch_text.stroke-91"),sQuery(id+"FHMxAyK4CFUKdhS_1.wireOp",EDGE,"1cb9c079-ea9b-4899-8069-e0e3048e911d.sketch_text.stroke-92"),sQuery(id+"FHMxAyK4CFUKdhS_1.wireOp",EDGE,"1cb9c079-ea9b-4899-8069-e0e3048e911d.sketch_text.stroke-93"),sQuery(id+"FHMxAyK4CFUKdhS_1.wireOp",EDGE,"1cb9c079-ea9b-4899-8069-e0e3048e911d.sketch_text.stroke-94"),sQuery(id+"FHMxAyK4CFUKdhS_1.wireOp",EDGE,"1cb9c079-ea9b-4899-8069-e0e3048e911d.sketch_text.stroke-95"),sQuery(id+"FHMxAyK4CFUKdhS_1.wireOp",EDGE,"1cb9c079-ea9b-4899-8069-e0e3048e911d.sketch_text.stroke-96"),sQuery(id+"FHMxAyK4CFUKdhS_1.wireOp",EDGE,"1cb9c079-ea9b-4899-8069-e0e3048e911d.sketch_text.stroke-97"),sQuery(id+"FHMxAyK4CFUKdhS_1.wireOp",EDGE,"1cb9c079-ea9b-4899-8069-e0e3048e911d.sketch_text.stroke-103"),sQuery(id+"FHMxAyK4CFUKdhS_1.wireOp",EDGE,"1cb9c079-ea9b-4899-8069-e0e3048e911d.sketch_text.stroke-104"),sQuery(id+"FHMxAyK4CFUKdhS_1.wireOp",EDGE,"1cb9c079-ea9b-4899-8069-e0e3048e911d.sketch_text.stroke-105"),sQuery(id+"FHMxAyK4CFUKdhS_1.wireOp",EDGE,"1cb9c079-ea9b-4899-8069-e0e3048e911d.sketch_text.stroke-106"),sQuery(id+"FHMxAyK4CFUKdhS_1.wireOp",EDGE,"1cb9c079-ea9b-4899-8069-e0e3048e911d.sketch_text.stroke-107"),sQuery(id+"FHMxAyK4CFUKdhS_1.wireOp",EDGE,"1cb9c079-ea9b-4899-8069-e0e3048e911d.sketch_text.stroke-108"),sQuery(id+"FHMxAyK4CFUKdhS_1.wireOp",EDGE,"1cb9c079-ea9b-4899-8069-e0e3048e911d.sketch_text.stroke-109"),sQuery(id+"FHMxAyK4CFUKdhS_1.wireOp",EDGE,"1cb9c079-ea9b-4899-8069-e0e3048e911d.sketch_text.stroke-110"),sQuery(id+"FHMxAyK4CFUKdhS_1.wireOp",EDGE,"1cb9c079-ea9b-4899-8069-e0e3048e911d.sketch_text.stroke-111"),sQuery(id+"FHMxAyK4CFUKdhS_1.wireOp",EDGE,"1cb9c079-ea9b-4899-8069-e0e3048e911d.sketch_text.stroke-112"),sQuery(id+"FHMxAyK4CFUKdhS_1.wireOp",EDGE,"1cb9c079-ea9b-4899-8069-e0e3048e911d.sketch_text.stroke-113"),sQuery(id+"FHMxAyK4CFUKdhS_1.wireOp",EDGE,"1cb9c079-ea9b-4899-8069-e0e3048e911d.sketch_text.stroke-114"),sQuery(id+"FHMxAyK4CFUKdhS_1.wireOp",EDGE,"1cb9c079-ea9b-4899-8069-e0e3048e911d.sketch_text.stroke-115"),sQuery(id+"FHMxAyK4CFUKdhS_1.wireOp",EDGE,"1cb9c079-ea9b-4899-8069-e0e3048e911d.sketch_text.stroke-116"),sQuery(id+"FHMxAyK4CFUKdhS_1.wireOp",EDGE,"1cb9c079-ea9b-4899-8069-e0e3048e911d.sketch_text.stroke-117"),sQuery(id+"FHMxAyK4CFUKdhS_1.wireOp",EDGE,"1cb9c079-ea9b-4899-8069-e0e3048e911d.sketch_text.stroke-118"),sQuery(id+"FHMxAyK4CFUKdhS_1.wireOp",EDGE,"1cb9c079-ea9b-4899-8069-e0e3048e911d.sketch_text.stroke-119"),sQuery(id+"FHMxAyK4CFUKdhS_1.wireOp",EDGE,"1cb9c079-ea9b-4899-8069-e0e3048e911d.sketch_text.stroke-120"),sQuery(id+"FHMxAyK4CFUKdhS_1.wireOp",EDGE,"1cb9c079-ea9b-4899-8069-e0e3048e911d.sketch_text.stroke-121"),sQuery(id+"FHMxAyK4CFUKdhS_1.wireOp",EDGE,"1cb9c079-ea9b-4899-8069-e0e3048e911d.sketch_text.stroke-122"),sQuery(id+"FHMxAyK4CFUKdhS_1.wireOp",EDGE,"1cb9c079-ea9b-4899-8069-e0e3048e911d.sketch_text.stroke-123"),sQuery(id+"FHMxAyK4CFUKdhS_1.wireOp",EDGE,"1cb9c079-ea9b-4899-8069-e0e3048e911d.sketch_text.stroke-124"),sQuery(id+"FHMxAyK4CFUKdhS_1.wireOp",EDGE,"1cb9c079-ea9b-4899-8069-e0e3048e911d.sketch_text.stroke-125"),sQuery(id+"FHMxAyK4CFUKdhS_1.wireOp",EDGE,"1cb9c079-ea9b-4899-8069-e0e3048e911d.sketch_text.stroke-126"),sQuery(id+"FHMxAyK4CFUKdhS_1.wireOp",EDGE,"1cb9c079-ea9b-4899-8069-e0e3048e911d.sketch_text.stroke-127"),sQuery(id+"FHMxAyK4CFUKdhS_1.wireOp",EDGE,"1cb9c079-ea9b-4899-8069-e0e3048e911d.sketch_text.stroke-128"),sQuery(id+"FHMxAyK4CFUKdhS_1.wireOp",EDGE,"1cb9c079-ea9b-4899-8069-e0e3048e911d.sketch_text.stroke-129"),sQuery(id+"FHMxAyK4CFUKdhS_1.wireOp",EDGE,"1cb9c079-ea9b-4899-8069-e0e3048e911d.sketch_text.stroke-130"),sQuery(id+"FHMxAyK4CFUKdhS_1.wireOp",EDGE,"1cb9c079-ea9b-4899-8069-e0e3048e911d.sketch_text.stroke-131"),sQuery(id+"FHMxAyK4CFUKdhS_1.wireOp",EDGE,"1cb9c079-ea9b-4899-8069-e0e3048e911d.sketch_text.stroke-132"),sQuery(id+"FHMxAyK4CFUKdhS_1.wireOp",EDGE,"1cb9c079-ea9b-4899-8069-e0e3048e911d.sketch_text.stroke-133"),sQuery(id+"FHMxAyK4CFUKdhS_1.wireOp",EDGE,"1cb9c079-ea9b-4899-8069-e0e3048e911d.sketch_text.stroke-134"),sQuery(id+"FHMxAyK4CFUKdhS_1.wireOp",EDGE,"1cb9c079-ea9b-4899-8069-e0e3048e911d.sketch_text.stroke-135"),sQuery(id+"FHMxAyK4CFUKdhS_1.wireOp",EDGE,"1cb9c079-ea9b-4899-8069-e0e3048e911d.sketch_text.stroke-136"),sQuery(id+"FHMxAyK4CFUKdhS_1.wireOp",EDGE,"1cb9c079-ea9b-4899-8069-e0e3048e911d.sketch_text.stroke-137"),sQuery(id+"FHMxAyK4CFUKdhS_1.wireOp",EDGE,"1cb9c079-ea9b-4899-8069-e0e3048e911d.sketch_text.stroke-138"),sQuery(id+"FHMxAyK4CFUKdhS_1.wireOp",EDGE,"1cb9c079-ea9b-4899-8069-e0e3048e911d.sketch_text.stroke-139"),sQuery(id+"FHMxAyK4CFUKdhS_1.wireOp",EDGE,"1cb9c079-ea9b-4899-8069-e0e3048e911d.sketch_text.stroke-140"),sQuery(id+"FHMxAyK4CFUKdhS_1.wireOp",EDGE,"1cb9c079-ea9b-4899-8069-e0e3048e911d.sketch_text.stroke-141"),sQuery(id+"FHMxAyK4CFUKdhS_1.wireOp",EDGE,"1cb9c079-ea9b-4899-8069-e0e3048e911d.sketch_text.stroke-142"),sQuery(id+"FHMxAyK4CFUKdhS_1.wireOp",EDGE,"1cb9c079-ea9b-4899-8069-e0e3048e911d.sketch_text.stroke-143"),sQuery(id+"FHMxAyK4CFUKdhS_1.wireOp",EDGE,"1cb9c079-ea9b-4899-8069-e0e3048e911d.sketch_text.stroke-144"),sQuery(id+"FHMxAyK4CFUKdhS_1.wireOp",EDGE,"1cb9c079-ea9b-4899-8069-e0e3048e911d.sketch_text.stroke-145"),sQuery(id+"FHMxAyK4CFUKdhS_1.wireOp",EDGE,"1cb9c079-ea9b-4899-8069-e0e3048e911d.sketch_text.stroke-146"),sQuery(id+"FHMxAyK4CFUKdhS_1.wireOp",EDGE,"1cb9c079-ea9b-4899-8069-e0e3048e911d.sketch_text.stroke-147"),sQuery(id+"FHMxAyK4CFUKdhS_1.wireOp",EDGE,"1cb9c079-ea9b-4899-8069-e0e3048e911d.sketch_text.stroke-148"),sQuery(id+"FHMxAyK4CFUKdhS_1.wireOp",EDGE,"1cb9c079-ea9b-4899-8069-e0e3048e911d.sketch_text.stroke-149"),sQuery(id+"FHMxAyK4CFUKdhS_1.wireOp",EDGE,"1cb9c079-ea9b-4899-8069-e0e3048e911d.sketch_text.stroke-150"),sQuery(id+"FHMxAyK4CFUKdhS_1.wireOp",EDGE,"1cb9c079-ea9b-4899-8069-e0e3048e911d.sketch_text.stroke-151"),sQuery(id+"FHMxAyK4CFUKdhS_1.wireOp",EDGE,"1cb9c079-ea9b-4899-8069-e0e3048e911d.sketch_text.stroke-152"),sQuery(id+"FHMxAyK4CFUKdhS_1.wireOp",EDGE,"1cb9c079-ea9b-4899-8069-e0e3048e911d.sketch_text.stroke-153"),sQuery(id+"FHMxAyK4CFUKdhS_1.wireOp",EDGE,"1cb9c079-ea9b-4899-8069-e0e3048e911d.sketch_text.stroke-159"),sQuery(id+"FHMxAyK4CFUKdhS_1.wireOp",EDGE,"1cb9c079-ea9b-4899-8069-e0e3048e911d.sketch_text.stroke-160"),sQuery(id+"FHMxAyK4CFUKdhS_1.wireOp",EDGE,"1cb9c079-ea9b-4899-8069-e0e3048e911d.sketch_text.stroke-161"),sQuery(id+"FHMxAyK4CFUKdhS_1.wireOp",EDGE,"1cb9c079-ea9b-4899-8069-e0e3048e911d.sketch_text.stroke-162"),sQuery(id+"FHMxAyK4CFUKdhS_1.wireOp",EDGE,"1cb9c079-ea9b-4899-8069-e0e3048e911d.sketch_text.stroke-163"),sQuery(id+"FHMxAyK4CFUKdhS_1.wireOp",EDGE,"1cb9c079-ea9b-4899-8069-e0e3048e911d.sketch_text.stroke-164"),sQuery(id+"FHMxAyK4CFUKdhS_1.wireOp",EDGE,"1cb9c079-ea9b-4899-8069-e0e3048e911d.sketch_text.stroke-165"),sQuery(id+"FHMxAyK4CFUKdhS_1.wireOp",EDGE,"1cb9c079-ea9b-4899-8069-e0e3048e911d.sketch_text.stroke-166"),sQuery(id+"FHMxAyK4CFUKdhS_1.wireOp",EDGE,"1cb9c079-ea9b-4899-8069-e0e3048e911d.sketch_text.stroke-167"),sQuery(id+"FHMxAyK4CFUKdhS_1.wireOp",EDGE,"1cb9c079-ea9b-4899-8069-e0e3048e911d.sketch_text.stroke-168"),sQuery(id+"FHMxAyK4CFUKdhS_1.wireOp",EDGE,"1cb9c079-ea9b-4899-8069-e0e3048e911d.sketch_text.stroke-169"),sQuery(id+"FHMxAyK4CFUKdhS_1.wireOp",EDGE,"1cb9c079-ea9b-4899-8069-e0e3048e911d.sketch_text.stroke-170"),sQuery(id+"FHMxAyK4CFUKdhS_1.wireOp",EDGE,"1cb9c079-ea9b-4899-8069-e0e3048e911d.sketch_text.stroke-171"),sQuery(id+"FHMxAyK4CFUKdhS_1.wireOp",EDGE,"1cb9c079-ea9b-4899-8069-e0e3048e911d.sketch_text.stroke-172"),sQuery(id+"FHMxAyK4CFUKdhS_1.wireOp",EDGE,"1cb9c079-ea9b-4899-8069-e0e3048e911d.sketch_text.stroke-173"),sQuery(id+"FHMxAyK4CFUKdhS_1.wireOp",EDGE,"1cb9c079-ea9b-4899-8069-e0e3048e911d.sketch_text.stroke-174"),sQuery(id+"FHMxAyK4CFUKdhS_1.wireOp",EDGE,"1cb9c079-ea9b-4899-8069-e0e3048e911d.sketch_text.stroke-175"),sQuery(id+"FHMxAyK4CFUKdhS_1.wireOp",EDGE,"1cb9c079-ea9b-4899-8069-e0e3048e911d.sketch_text.stroke-176"),sQuery(id+"FHMxAyK4CFUKdhS_1.wireOp",EDGE,"1cb9c079-ea9b-4899-8069-e0e3048e911d.sketch_text.stroke-177"),sQuery(id+"FHMxAyK4CFUKdhS_1.wireOp",EDGE,"1cb9c079-ea9b-4899-8069-e0e3048e911d.sketch_text.stroke-178"),sQuery(id+"FHMxAyK4CFUKdhS_1.wireOp",EDGE,"1cb9c079-ea9b-4899-8069-e0e3048e911d.sketch_text.stroke-179"),sQuery(id+"FHMxAyK4CFUKdhS_1.wireOp",EDGE,"1cb9c079-ea9b-4899-8069-e0e3048e911d.sketch_text.stroke-180"),sQuery(id+"F3.wireOp",EDGE,"E28"),subQ2])],"isStart":true}),makeQuery(id+"F4.opExtrude","SWEPT_FACE",FACE,{"disambiguationData":[OSD([subQ2])]})]),OD(0.0)],"derivedFrom":makeQuery(id+"F1.opExtrude","CAP_EDGE",EDGE,{"disambiguationData":[OSD([subQ0])],"isStart":false})});}
            var Q27;
            {var subQ0=sQuery(id+"F0.wireOp",EDGE,"E0.top");var subQ1=sQuery(id+"F0.wireOp",EDGE,"E0.bottom");var subQ2=sQuery(id+"F3.wireOp",EDGE,"E29");Q27=makeQuery(id+"F4.boolean.opBoolean","SPLIT",EDGE,{"disambiguationData":[TD([makeQuery(id+"F1.opExtrude","CAP_FACE",FACE,{"disambiguationData":[OSD([subQ1,subQ0,sQuery(id+"F0.wireOp",EDGE,"E0.left"),sQuery(id+"F0.wireOp",EDGE,"E0.right")])],"isStart":false}),makeQuery(id+"F1.opExtrude","SWEPT_FACE",FACE,{"disambiguationData":[OSD([subQ0])]}),makeQuery(id+"F4.opExtrude","CAP_FACE",FACE,{"disambiguationData":[OSD([subQ1,sQuery(id+"F2.wireOp",EDGE,"fcba4419-a2ee-464f-be9d-58f11bf3418b.sketch_text.stroke-0"),sQuery(id+"F2.wireOp",EDGE,"fcba4419-a2ee-464f-be9d-58f11bf3418b.sketch_text.stroke-1"),sQuery(id+"F2.wireOp",EDGE,"fcba4419-a2ee-464f-be9d-58f11bf3418b.sketch_text.stroke-2"),sQuery(id+"F2.wireOp",EDGE,"fcba4419-a2ee-464f-be9d-58f11bf3418b.sketch_text.stroke-3"),sQuery(id+"F2.wireOp",EDGE,"fcba4419-a2ee-464f-be9d-58f11bf3418b.sketch_text.stroke-4"),sQuery(id+"F2.wireOp",EDGE,"fcba4419-a2ee-464f-be9d-58f11bf3418b.sketch_text.stroke-5"),sQuery(id+"F2.wireOp",EDGE,"fcba4419-a2ee-464f-be9d-58f11bf3418b.sketch_text.stroke-6"),sQuery(id+"F2.wireOp",EDGE,"fcba4419-a2ee-464f-be9d-58f11bf3418b.sketch_text.stroke-7"),sQuery(id+"F2.wireOp",EDGE,"fcba4419-a2ee-464f-be9d-58f11bf3418b.sketch_text.stroke-8"),sQuery(id+"F2.wireOp",EDGE,"fcba4419-a2ee-464f-be9d-58f11bf3418b.sketch_text.stroke-9"),sQuery(id+"F2.wireOp",EDGE,"fcba4419-a2ee-464f-be9d-58f11bf3418b.sketch_text.stroke-10"),sQuery(id+"F2.wireOp",EDGE,"fcba4419-a2ee-464f-be9d-58f11bf3418b.sketch_text.stroke-11"),sQuery(id+"F2.wireOp",EDGE,"fcba4419-a2ee-464f-be9d-58f11bf3418b.sketch_text.stroke-12"),sQuery(id+"F2.wireOp",EDGE,"fcba4419-a2ee-464f-be9d-58f11bf3418b.sketch_text.stroke-13"),sQuery(id+"F2.wireOp",EDGE,"fcba4419-a2ee-464f-be9d-58f11bf3418b.sketch_text.stroke-14"),sQuery(id+"F2.wireOp",EDGE,"fcba4419-a2ee-464f-be9d-58f11bf3418b.sketch_text.stroke-15"),sQuery(id+"F2.wireOp",EDGE,"fcba4419-a2ee-464f-be9d-58f11bf3418b.sketch_text.stroke-16"),sQuery(id+"F2.wireOp",EDGE,"fcba4419-a2ee-464f-be9d-58f11bf3418b.sketch_text.stroke-17"),sQuery(id+"F2.wireOp",EDGE,"fcba4419-a2ee-464f-be9d-58f11bf3418b.sketch_text.stroke-18"),sQuery(id+"F2.wireOp",EDGE,"fcba4419-a2ee-464f-be9d-58f11bf3418b.sketch_text.stroke-19"),sQuery(id+"F2.wireOp",EDGE,"fcba4419-a2ee-464f-be9d-58f11bf3418b.sketch_text.stroke-20"),sQuery(id+"F2.wireOp",EDGE,"fcba4419-a2ee-464f-be9d-58f11bf3418b.sketch_text.stroke-21"),sQuery(id+"F2.wireOp",EDGE,"fcba4419-a2ee-464f-be9d-58f11bf3418b.sketch_text.stroke-22"),sQuery(id+"F2.wireOp",EDGE,"fcba4419-a2ee-464f-be9d-58f11bf3418b.sketch_text.stroke-23"),sQuery(id+"F2.wireOp",EDGE,"fcba4419-a2ee-464f-be9d-58f11bf3418b.sketch_text.stroke-24"),sQuery(id+"F2.wireOp",EDGE,"fcba4419-a2ee-464f-be9d-58f11bf3418b.sketch_text.stroke-25"),sQuery(id+"F2.wireOp",EDGE,"fcba4419-a2ee-464f-be9d-58f11bf3418b.sketch_text.stroke-26"),sQuery(id+"F2.wireOp",EDGE,"fcba4419-a2ee-464f-be9d-58f11bf3418b.sketch_text.stroke-27"),sQuery(id+"F2.wireOp",EDGE,"fcba4419-a2ee-464f-be9d-58f11bf3418b.sketch_text.stroke-28"),sQuery(id+"F2.wireOp",EDGE,"fcba4419-a2ee-464f-be9d-58f11bf3418b.sketch_text.stroke-29"),sQuery(id+"F2.wireOp",EDGE,"fcba4419-a2ee-464f-be9d-58f11bf3418b.sketch_text.stroke-30"),sQuery(id+"F2.wireOp",EDGE,"fcba4419-a2ee-464f-be9d-58f11bf3418b.sketch_text.stroke-31"),sQuery(id+"F2.wireOp",EDGE,"fcba4419-a2ee-464f-be9d-58f11bf3418b.sketch_text.stroke-32"),sQuery(id+"F2.wireOp",EDGE,"fcba4419-a2ee-464f-be9d-58f11bf3418b.sketch_text.stroke-33"),sQuery(id+"F2.wireOp",EDGE,"fcba4419-a2ee-464f-be9d-58f11bf3418b.sketch_text.stroke-34"),sQuery(id+"F2.wireOp",EDGE,"fcba4419-a2ee-464f-be9d-58f11bf3418b.sketch_text.stroke-35"),sQuery(id+"F2.wireOp",EDGE,"fcba4419-a2ee-464f-be9d-58f11bf3418b.sketch_text.stroke-36"),sQuery(id+"F2.wireOp",EDGE,"fcba4419-a2ee-464f-be9d-58f11bf3418b.sketch_text.stroke-37"),sQuery(id+"F2.wireOp",EDGE,"fcba4419-a2ee-464f-be9d-58f11bf3418b.sketch_text.stroke-38"),sQuery(id+"F2.wireOp",EDGE,"fcba4419-a2ee-464f-be9d-58f11bf3418b.sketch_text.stroke-39"),sQuery(id+"F2.wireOp",EDGE,"fcba4419-a2ee-464f-be9d-58f11bf3418b.sketch_text.stroke-40"),sQuery(id+"F2.wireOp",EDGE,"fcba4419-a2ee-464f-be9d-58f11bf3418b.sketch_text.stroke-41"),sQuery(id+"F2.wireOp",EDGE,"fcba4419-a2ee-464f-be9d-58f11bf3418b.sketch_text.stroke-42"),sQuery(id+"F2.wireOp",EDGE,"fcba4419-a2ee-464f-be9d-58f11bf3418b.sketch_text.stroke-43"),sQuery(id+"F2.wireOp",EDGE,"fcba4419-a2ee-464f-be9d-58f11bf3418b.sketch_text.stroke-44"),sQuery(id+"F2.wireOp",EDGE,"fcba4419-a2ee-464f-be9d-58f11bf3418b.sketch_text.stroke-45"),sQuery(id+"F2.wireOp",EDGE,"fcba4419-a2ee-464f-be9d-58f11bf3418b.sketch_text.stroke-46"),sQuery(id+"F2.wireOp",EDGE,"fcba4419-a2ee-464f-be9d-58f11bf3418b.sketch_text.stroke-47"),sQuery(id+"F2.wireOp",EDGE,"fcba4419-a2ee-464f-be9d-58f11bf3418b.sketch_text.stroke-48"),sQuery(id+"F2.wireOp",EDGE,"fcba4419-a2ee-464f-be9d-58f11bf3418b.sketch_text.stroke-49"),sQuery(id+"F2.wireOp",EDGE,"fcba4419-a2ee-464f-be9d-58f11bf3418b.sketch_text.stroke-50"),sQuery(id+"F2.wireOp",EDGE,"fcba4419-a2ee-464f-be9d-58f11bf3418b.sketch_text.stroke-51"),sQuery(id+"F2.wireOp",EDGE,"fcba4419-a2ee-464f-be9d-58f11bf3418b.sketch_text.stroke-52"),sQuery(id+"F2.wireOp",EDGE,"fcba4419-a2ee-464f-be9d-58f11bf3418b.sketch_text.stroke-53"),sQuery(id+"F2.wireOp",EDGE,"fcba4419-a2ee-464f-be9d-58f11bf3418b.sketch_text.stroke-54"),sQuery(id+"F2.wireOp",EDGE,"fcba4419-a2ee-464f-be9d-58f11bf3418b.sketch_text.stroke-55"),sQuery(id+"F2.wireOp",EDGE,"fcba4419-a2ee-464f-be9d-58f11bf3418b.sketch_text.stroke-56"),sQuery(id+"F2.wireOp",EDGE,"fcba4419-a2ee-464f-be9d-58f11bf3418b.sketch_text.stroke-57"),sQuery(id+"F2.wireOp",EDGE,"fcba4419-a2ee-464f-be9d-58f11bf3418b.sketch_text.stroke-58"),sQuery(id+"F2.wireOp",EDGE,"fcba4419-a2ee-464f-be9d-58f11bf3418b.sketch_text.stroke-59"),sQuery(id+"F2.wireOp",EDGE,"fcba4419-a2ee-464f-be9d-58f11bf3418b.sketch_text.stroke-60"),sQuery(id+"F2.wireOp",EDGE,"fcba4419-a2ee-464f-be9d-58f11bf3418b.sketch_text.stroke-61"),sQuery(id+"F2.wireOp",EDGE,"fcba4419-a2ee-464f-be9d-58f11bf3418b.sketch_text.stroke-62"),sQuery(id+"F2.wireOp",EDGE,"fcba4419-a2ee-464f-be9d-58f11bf3418b.sketch_text.stroke-63"),sQuery(id+"F2.wireOp",EDGE,"fcba4419-a2ee-464f-be9d-58f11bf3418b.sketch_text.stroke-64"),sQuery(id+"F2.wireOp",EDGE,"fcba4419-a2ee-464f-be9d-58f11bf3418b.sketch_text.stroke-65"),sQuery(id+"F2.wireOp",EDGE,"fcba4419-a2ee-464f-be9d-58f11bf3418b.sketch_text.stroke-66"),sQuery(id+"F2.wireOp",EDGE,"fcba4419-a2ee-464f-be9d-58f11bf3418b.sketch_text.stroke-67"),sQuery(id+"F2.wireOp",EDGE,"fcba4419-a2ee-464f-be9d-58f11bf3418b.sketch_text.stroke-68"),sQuery(id+"F2.wireOp",EDGE,"fcba4419-a2ee-464f-be9d-58f11bf3418b.sketch_text.stroke-69"),sQuery(id+"F2.wireOp",EDGE,"fcba4419-a2ee-464f-be9d-58f11bf3418b.sketch_text.stroke-70"),sQuery(id+"F2.wireOp",EDGE,"fcba4419-a2ee-464f-be9d-58f11bf3418b.sketch_text.stroke-71"),sQuery(id+"F2.wireOp",EDGE,"fcba4419-a2ee-464f-be9d-58f11bf3418b.sketch_text.stroke-72"),sQuery(id+"F2.wireOp",EDGE,"fcba4419-a2ee-464f-be9d-58f11bf3418b.sketch_text.stroke-73"),sQuery(id+"F2.wireOp",EDGE,"fcba4419-a2ee-464f-be9d-58f11bf3418b.sketch_text.stroke-74"),sQuery(id+"F2.wireOp",EDGE,"fcba4419-a2ee-464f-be9d-58f11bf3418b.sketch_text.stroke-75"),sQuery(id+"F2.wireOp",EDGE,"fcba4419-a2ee-464f-be9d-58f11bf3418b.sketch_text.stroke-76"),sQuery(id+"F2.wireOp",EDGE,"fcba4419-a2ee-464f-be9d-58f11bf3418b.sketch_text.stroke-77"),sQuery(id+"F2.wireOp",EDGE,"fcba4419-a2ee-464f-be9d-58f11bf3418b.sketch_text.stroke-78"),sQuery(id+"F2.wireOp",EDGE,"fcba4419-a2ee-464f-be9d-58f11bf3418b.sketch_text.stroke-79"),sQuery(id+"F2.wireOp",EDGE,"fcba4419-a2ee-464f-be9d-58f11bf3418b.sketch_text.stroke-80"),sQuery(id+"F2.wireOp",EDGE,"fcba4419-a2ee-464f-be9d-58f11bf3418b.sketch_text.stroke-81"),sQuery(id+"F2.wireOp",EDGE,"fcba4419-a2ee-464f-be9d-58f11bf3418b.sketch_text.stroke-82"),sQuery(id+"F2.wireOp",EDGE,"fcba4419-a2ee-464f-be9d-58f11bf3418b.sketch_text.stroke-83"),sQuery(id+"F2.wireOp",EDGE,"fcba4419-a2ee-464f-be9d-58f11bf3418b.sketch_text.stroke-84"),sQuery(id+"F2.wireOp",EDGE,"fcba4419-a2ee-464f-be9d-58f11bf3418b.sketch_text.stroke-85"),sQuery(id+"F2.wireOp",EDGE,"fcba4419-a2ee-464f-be9d-58f11bf3418b.sketch_text.stroke-86"),sQuery(id+"F2.wireOp",EDGE,"fcba4419-a2ee-464f-be9d-58f11bf3418b.sketch_text.stroke-87"),sQuery(id+"F2.wireOp",EDGE,"fcba4419-a2ee-464f-be9d-58f11bf3418b.sketch_text.stroke-88"),sQuery(id+"F2.wireOp",EDGE,"fcba4419-a2ee-464f-be9d-58f11bf3418b.sketch_text.stroke-89"),sQuery(id+"F2.wireOp",EDGE,"fcba4419-a2ee-464f-be9d-58f11bf3418b.sketch_text.stroke-90"),sQuery(id+"F2.wireOp",EDGE,"fcba4419-a2ee-464f-be9d-58f11bf3418b.sketch_text.stroke-91"),sQuery(id+"F2.wireOp",EDGE,"fcba4419-a2ee-464f-be9d-58f11bf3418b.sketch_text.stroke-92"),sQuery(id+"F2.wireOp",EDGE,"fcba4419-a2ee-464f-be9d-58f11bf3418b.sketch_text.stroke-93"),sQuery(id+"F2.wireOp",EDGE,"fcba4419-a2ee-464f-be9d-58f11bf3418b.sketch_text.stroke-94"),sQuery(id+"F2.wireOp",EDGE,"fcba4419-a2ee-464f-be9d-58f11bf3418b.sketch_text.stroke-95"),sQuery(id+"F2.wireOp",EDGE,"fcba4419-a2ee-464f-be9d-58f11bf3418b.sketch_text.stroke-96"),sQuery(id+"F2.wireOp",EDGE,"fcba4419-a2ee-464f-be9d-58f11bf3418b.sketch_text.stroke-97"),sQuery(id+"F2.wireOp",EDGE,"fcba4419-a2ee-464f-be9d-58f11bf3418b.sketch_text.stroke-98"),sQuery(id+"F2.wireOp",EDGE,"fcba4419-a2ee-464f-be9d-58f11bf3418b.sketch_text.stroke-99"),sQuery(id+"F2.wireOp",EDGE,"fcba4419-a2ee-464f-be9d-58f11bf3418b.sketch_text.stroke-100"),sQuery(id+"F2.wireOp",EDGE,"fcba4419-a2ee-464f-be9d-58f11bf3418b.sketch_text.stroke-101"),sQuery(id+"F2.wireOp",EDGE,"fcba4419-a2ee-464f-be9d-58f11bf3418b.sketch_text.stroke-102"),sQuery(id+"F2.wireOp",EDGE,"fcba4419-a2ee-464f-be9d-58f11bf3418b.sketch_text.stroke-103"),sQuery(id+"F2.wireOp",EDGE,"fcba4419-a2ee-464f-be9d-58f11bf3418b.sketch_text.stroke-104"),sQuery(id+"F2.wireOp",EDGE,"fcba4419-a2ee-464f-be9d-58f11bf3418b.sketch_text.stroke-105"),sQuery(id+"F2.wireOp",EDGE,"fcba4419-a2ee-464f-be9d-58f11bf3418b.sketch_text.stroke-106"),sQuery(id+"F2.wireOp",EDGE,"fcba4419-a2ee-464f-be9d-58f11bf3418b.sketch_text.stroke-107"),sQuery(id+"F2.wireOp",EDGE,"fcba4419-a2ee-464f-be9d-58f11bf3418b.sketch_text.stroke-108"),sQuery(id+"F2.wireOp",EDGE,"fcba4419-a2ee-464f-be9d-58f11bf3418b.sketch_text.stroke-109"),sQuery(id+"F2.wireOp",EDGE,"fcba4419-a2ee-464f-be9d-58f11bf3418b.sketch_text.stroke-110"),sQuery(id+"F2.wireOp",EDGE,"fcba4419-a2ee-464f-be9d-58f11bf3418b.sketch_text.stroke-111"),sQuery(id+"F2.wireOp",EDGE,"fcba4419-a2ee-464f-be9d-58f11bf3418b.sketch_text.stroke-112"),sQuery(id+"F2.wireOp",EDGE,"fcba4419-a2ee-464f-be9d-58f11bf3418b.sketch_text.stroke-113"),sQuery(id+"F2.wireOp",EDGE,"fcba4419-a2ee-464f-be9d-58f11bf3418b.sketch_text.stroke-114"),sQuery(id+"F2.wireOp",EDGE,"fcba4419-a2ee-464f-be9d-58f11bf3418b.sketch_text.stroke-115"),sQuery(id+"F2.wireOp",EDGE,"fcba4419-a2ee-464f-be9d-58f11bf3418b.sketch_text.stroke-116"),sQuery(id+"F2.wireOp",EDGE,"fcba4419-a2ee-464f-be9d-58f11bf3418b.sketch_text.stroke-117"),sQuery(id+"F2.wireOp",EDGE,"fcba4419-a2ee-464f-be9d-58f11bf3418b.sketch_text.stroke-118"),sQuery(id+"F2.wireOp",EDGE,"fcba4419-a2ee-464f-be9d-58f11bf3418b.sketch_text.stroke-119"),sQuery(id+"F2.wireOp",EDGE,"fcba4419-a2ee-464f-be9d-58f11bf3418b.sketch_text.stroke-120"),sQuery(id+"F2.wireOp",EDGE,"fcba4419-a2ee-464f-be9d-58f11bf3418b.sketch_text.stroke-121"),sQuery(id+"F2.wireOp",EDGE,"fcba4419-a2ee-464f-be9d-58f11bf3418b.sketch_text.stroke-122"),sQuery(id+"F2.wireOp",EDGE,"fcba4419-a2ee-464f-be9d-58f11bf3418b.sketch_text.stroke-123"),sQuery(id+"F2.wireOp",EDGE,"fcba4419-a2ee-464f-be9d-58f11bf3418b.sketch_text.stroke-124"),sQuery(id+"F2.wireOp",EDGE,"fcba4419-a2ee-464f-be9d-58f11bf3418b.sketch_text.stroke-125"),sQuery(id+"F2.wireOp",EDGE,"fcba4419-a2ee-464f-be9d-58f11bf3418b.sketch_text.stroke-126"),sQuery(id+"F2.wireOp",EDGE,"fcba4419-a2ee-464f-be9d-58f11bf3418b.sketch_text.stroke-127"),sQuery(id+"F2.wireOp",EDGE,"fcba4419-a2ee-464f-be9d-58f11bf3418b.sketch_text.stroke-128"),sQuery(id+"F2.wireOp",EDGE,"fcba4419-a2ee-464f-be9d-58f11bf3418b.sketch_text.stroke-129"),sQuery(id+"F2.wireOp",EDGE,"fcba4419-a2ee-464f-be9d-58f11bf3418b.sketch_text.stroke-130"),sQuery(id+"F2.wireOp",EDGE,"fcba4419-a2ee-464f-be9d-58f11bf3418b.sketch_text.stroke-131"),sQuery(id+"F2.wireOp",EDGE,"fcba4419-a2ee-464f-be9d-58f11bf3418b.sketch_text.stroke-132"),sQuery(id+"F2.wireOp",EDGE,"fcba4419-a2ee-464f-be9d-58f11bf3418b.sketch_text.stroke-133"),sQuery(id+"F2.wireOp",EDGE,"fcba4419-a2ee-464f-be9d-58f11bf3418b.sketch_text.stroke-134"),sQuery(id+"F2.wireOp",EDGE,"fcba4419-a2ee-464f-be9d-58f11bf3418b.sketch_text.stroke-135"),sQuery(id+"F2.wireOp",EDGE,"fcba4419-a2ee-464f-be9d-58f11bf3418b.sketch_text.stroke-136"),sQuery(id+"F2.wireOp",EDGE,"fcba4419-a2ee-464f-be9d-58f11bf3418b.sketch_text.stroke-137"),sQuery(id+"F2.wireOp",EDGE,"fcba4419-a2ee-464f-be9d-58f11bf3418b.sketch_text.stroke-138"),sQuery(id+"F2.wireOp",EDGE,"fcba4419-a2ee-464f-be9d-58f11bf3418b.sketch_text.stroke-139"),sQuery(id+"F2.wireOp",EDGE,"fcba4419-a2ee-464f-be9d-58f11bf3418b.sketch_text.stroke-140"),sQuery(id+"F2.wireOp",EDGE,"fcba4419-a2ee-464f-be9d-58f11bf3418b.sketch_text.stroke-141"),sQuery(id+"F2.wireOp",EDGE,"fcba4419-a2ee-464f-be9d-58f11bf3418b.sketch_text.stroke-142"),sQuery(id+"F2.wireOp",EDGE,"fcba4419-a2ee-464f-be9d-58f11bf3418b.sketch_text.stroke-143"),sQuery(id+"F2.wireOp",EDGE,"fcba4419-a2ee-464f-be9d-58f11bf3418b.sketch_text.stroke-144"),sQuery(id+"F2.wireOp",EDGE,"fcba4419-a2ee-464f-be9d-58f11bf3418b.sketch_text.stroke-145"),sQuery(id+"F2.wireOp",EDGE,"fcba4419-a2ee-464f-be9d-58f11bf3418b.sketch_text.stroke-146"),sQuery(id+"F2.wireOp",EDGE,"fcba4419-a2ee-464f-be9d-58f11bf3418b.sketch_text.stroke-147"),sQuery(id+"F2.wireOp",EDGE,"fcba4419-a2ee-464f-be9d-58f11bf3418b.sketch_text.stroke-148"),sQuery(id+"F2.wireOp",EDGE,"fcba4419-a2ee-464f-be9d-58f11bf3418b.sketch_text.stroke-149"),sQuery(id+"F2.wireOp",EDGE,"fcba4419-a2ee-464f-be9d-58f11bf3418b.sketch_text.stroke-150"),sQuery(id+"F2.wireOp",EDGE,"fcba4419-a2ee-464f-be9d-58f11bf3418b.sketch_text.stroke-151"),sQuery(id+"F2.wireOp",EDGE,"fcba4419-a2ee-464f-be9d-58f11bf3418b.sketch_text.stroke-152"),sQuery(id+"F2.wireOp",EDGE,"fcba4419-a2ee-464f-be9d-58f11bf3418b.sketch_text.stroke-153"),sQuery(id+"F2.wireOp",EDGE,"fcba4419-a2ee-464f-be9d-58f11bf3418b.sketch_text.stroke-154"),sQuery(id+"F2.wireOp",EDGE,"fcba4419-a2ee-464f-be9d-58f11bf3418b.sketch_text.stroke-155"),sQuery(id+"F2.wireOp",EDGE,"fcba4419-a2ee-464f-be9d-58f11bf3418b.sketch_text.stroke-156"),sQuery(id+"F2.wireOp",EDGE,"fcba4419-a2ee-464f-be9d-58f11bf3418b.sketch_text.stroke-157"),sQuery(id+"F2.wireOp",EDGE,"fcba4419-a2ee-464f-be9d-58f11bf3418b.sketch_text.stroke-158"),sQuery(id+"F2.wireOp",EDGE,"fcba4419-a2ee-464f-be9d-58f11bf3418b.sketch_text.stroke-159"),sQuery(id+"F2.wireOp",EDGE,"fcba4419-a2ee-464f-be9d-58f11bf3418b.sketch_text.stroke-160"),sQuery(id+"F2.wireOp",EDGE,"fcba4419-a2ee-464f-be9d-58f11bf3418b.sketch_text.stroke-161"),sQuery(id+"F2.wireOp",EDGE,"fcba4419-a2ee-464f-be9d-58f11bf3418b.sketch_text.stroke-162"),sQuery(id+"F2.wireOp",EDGE,"fcba4419-a2ee-464f-be9d-58f11bf3418b.sketch_text.stroke-163"),sQuery(id+"F2.wireOp",EDGE,"fcba4419-a2ee-464f-be9d-58f11bf3418b.sketch_text.stroke-164"),sQuery(id+"F2.wireOp",EDGE,"fcba4419-a2ee-464f-be9d-58f11bf3418b.sketch_text.stroke-165"),sQuery(id+"F2.wireOp",EDGE,"fcba4419-a2ee-464f-be9d-58f11bf3418b.sketch_text.stroke-166"),sQuery(id+"F2.wireOp",EDGE,"fcba4419-a2ee-464f-be9d-58f11bf3418b.sketch_text.stroke-167"),sQuery(id+"F2.wireOp",EDGE,"fcba4419-a2ee-464f-be9d-58f11bf3418b.sketch_text.stroke-168"),sQuery(id+"F2.wireOp",EDGE,"fcba4419-a2ee-464f-be9d-58f11bf3418b.sketch_text.stroke-169"),sQuery(id+"F2.wireOp",EDGE,"fcba4419-a2ee-464f-be9d-58f11bf3418b.sketch_text.stroke-170"),sQuery(id+"F2.wireOp",EDGE,"fcba4419-a2ee-464f-be9d-58f11bf3418b.sketch_text.stroke-171"),sQuery(id+"F2.wireOp",EDGE,"fcba4419-a2ee-464f-be9d-58f11bf3418b.sketch_text.stroke-172"),sQuery(id+"F2.wireOp",EDGE,"fcba4419-a2ee-464f-be9d-58f11bf3418b.sketch_text.stroke-173"),sQuery(id+"FHMxAyK4CFUKdhS_1.wireOp",EDGE,"1cb9c079-ea9b-4899-8069-e0e3048e911d.sketch_text.stroke-0"),sQuery(id+"FHMxAyK4CFUKdhS_1.wireOp",EDGE,"1cb9c079-ea9b-4899-8069-e0e3048e911d.sketch_text.stroke-1"),sQuery(id+"FHMxAyK4CFUKdhS_1.wireOp",EDGE,"1cb9c079-ea9b-4899-8069-e0e3048e911d.sketch_text.stroke-2"),sQuery(id+"FHMxAyK4CFUKdhS_1.wireOp",EDGE,"1cb9c079-ea9b-4899-8069-e0e3048e911d.sketch_text.stroke-3"),sQuery(id+"FHMxAyK4CFUKdhS_1.wireOp",EDGE,"1cb9c079-ea9b-4899-8069-e0e3048e911d.sketch_text.stroke-4"),sQuery(id+"FHMxAyK4CFUKdhS_1.wireOp",EDGE,"1cb9c079-ea9b-4899-8069-e0e3048e911d.sketch_text.stroke-5"),sQuery(id+"FHMxAyK4CFUKdhS_1.wireOp",EDGE,"1cb9c079-ea9b-4899-8069-e0e3048e911d.sketch_text.stroke-6"),sQuery(id+"FHMxAyK4CFUKdhS_1.wireOp",EDGE,"1cb9c079-ea9b-4899-8069-e0e3048e911d.sketch_text.stroke-7"),sQuery(id+"FHMxAyK4CFUKdhS_1.wireOp",EDGE,"1cb9c079-ea9b-4899-8069-e0e3048e911d.sketch_text.stroke-8"),sQuery(id+"FHMxAyK4CFUKdhS_1.wireOp",EDGE,"1cb9c079-ea9b-4899-8069-e0e3048e911d.sketch_text.stroke-9"),sQuery(id+"FHMxAyK4CFUKdhS_1.wireOp",EDGE,"1cb9c079-ea9b-4899-8069-e0e3048e911d.sketch_text.stroke-10"),sQuery(id+"FHMxAyK4CFUKdhS_1.wireOp",EDGE,"1cb9c079-ea9b-4899-8069-e0e3048e911d.sketch_text.stroke-11"),sQuery(id+"FHMxAyK4CFUKdhS_1.wireOp",EDGE,"1cb9c079-ea9b-4899-8069-e0e3048e911d.sketch_text.stroke-12"),sQuery(id+"FHMxAyK4CFUKdhS_1.wireOp",EDGE,"1cb9c079-ea9b-4899-8069-e0e3048e911d.sketch_text.stroke-13"),sQuery(id+"FHMxAyK4CFUKdhS_1.wireOp",EDGE,"1cb9c079-ea9b-4899-8069-e0e3048e911d.sketch_text.stroke-14"),sQuery(id+"FHMxAyK4CFUKdhS_1.wireOp",EDGE,"1cb9c079-ea9b-4899-8069-e0e3048e911d.sketch_text.stroke-15"),sQuery(id+"FHMxAyK4CFUKdhS_1.wireOp",EDGE,"1cb9c079-ea9b-4899-8069-e0e3048e911d.sketch_text.stroke-16"),sQuery(id+"FHMxAyK4CFUKdhS_1.wireOp",EDGE,"1cb9c079-ea9b-4899-8069-e0e3048e911d.sketch_text.stroke-17"),sQuery(id+"FHMxAyK4CFUKdhS_1.wireOp",EDGE,"1cb9c079-ea9b-4899-8069-e0e3048e911d.sketch_text.stroke-18"),sQuery(id+"FHMxAyK4CFUKdhS_1.wireOp",EDGE,"1cb9c079-ea9b-4899-8069-e0e3048e911d.sketch_text.stroke-19"),sQuery(id+"FHMxAyK4CFUKdhS_1.wireOp",EDGE,"1cb9c079-ea9b-4899-8069-e0e3048e911d.sketch_text.stroke-20"),sQuery(id+"FHMxAyK4CFUKdhS_1.wireOp",EDGE,"1cb9c079-ea9b-4899-8069-e0e3048e911d.sketch_text.stroke-21"),sQuery(id+"FHMxAyK4CFUKdhS_1.wireOp",EDGE,"1cb9c079-ea9b-4899-8069-e0e3048e911d.sketch_text.stroke-22"),sQuery(id+"FHMxAyK4CFUKdhS_1.wireOp",EDGE,"1cb9c079-ea9b-4899-8069-e0e3048e911d.sketch_text.stroke-23"),sQuery(id+"FHMxAyK4CFUKdhS_1.wireOp",EDGE,"1cb9c079-ea9b-4899-8069-e0e3048e911d.sketch_text.stroke-24"),sQuery(id+"FHMxAyK4CFUKdhS_1.wireOp",EDGE,"1cb9c079-ea9b-4899-8069-e0e3048e911d.sketch_text.stroke-25"),sQuery(id+"FHMxAyK4CFUKdhS_1.wireOp",EDGE,"1cb9c079-ea9b-4899-8069-e0e3048e911d.sketch_text.stroke-26"),sQuery(id+"FHMxAyK4CFUKdhS_1.wireOp",EDGE,"1cb9c079-ea9b-4899-8069-e0e3048e911d.sketch_text.stroke-27"),sQuery(id+"FHMxAyK4CFUKdhS_1.wireOp",EDGE,"1cb9c079-ea9b-4899-8069-e0e3048e911d.sketch_text.stroke-28"),sQuery(id+"FHMxAyK4CFUKdhS_1.wireOp",EDGE,"1cb9c079-ea9b-4899-8069-e0e3048e911d.sketch_text.stroke-29"),sQuery(id+"FHMxAyK4CFUKdhS_1.wireOp",EDGE,"1cb9c079-ea9b-4899-8069-e0e3048e911d.sketch_text.stroke-30"),sQuery(id+"FHMxAyK4CFUKdhS_1.wireOp",EDGE,"1cb9c079-ea9b-4899-8069-e0e3048e911d.sketch_text.stroke-31"),sQuery(id+"FHMxAyK4CFUKdhS_1.wireOp",EDGE,"1cb9c079-ea9b-4899-8069-e0e3048e911d.sketch_text.stroke-32"),sQuery(id+"FHMxAyK4CFUKdhS_1.wireOp",EDGE,"1cb9c079-ea9b-4899-8069-e0e3048e911d.sketch_text.stroke-33"),sQuery(id+"FHMxAyK4CFUKdhS_1.wireOp",EDGE,"1cb9c079-ea9b-4899-8069-e0e3048e911d.sketch_text.stroke-34"),sQuery(id+"FHMxAyK4CFUKdhS_1.wireOp",EDGE,"1cb9c079-ea9b-4899-8069-e0e3048e911d.sketch_text.stroke-35"),sQuery(id+"FHMxAyK4CFUKdhS_1.wireOp",EDGE,"1cb9c079-ea9b-4899-8069-e0e3048e911d.sketch_text.stroke-36"),sQuery(id+"FHMxAyK4CFUKdhS_1.wireOp",EDGE,"1cb9c079-ea9b-4899-8069-e0e3048e911d.sketch_text.stroke-37"),sQuery(id+"FHMxAyK4CFUKdhS_1.wireOp",EDGE,"1cb9c079-ea9b-4899-8069-e0e3048e911d.sketch_text.stroke-38"),sQuery(id+"FHMxAyK4CFUKdhS_1.wireOp",EDGE,"1cb9c079-ea9b-4899-8069-e0e3048e911d.sketch_text.stroke-39"),sQuery(id+"FHMxAyK4CFUKdhS_1.wireOp",EDGE,"1cb9c079-ea9b-4899-8069-e0e3048e911d.sketch_text.stroke-40"),sQuery(id+"FHMxAyK4CFUKdhS_1.wireOp",EDGE,"1cb9c079-ea9b-4899-8069-e0e3048e911d.sketch_text.stroke-41"),sQuery(id+"FHMxAyK4CFUKdhS_1.wireOp",EDGE,"1cb9c079-ea9b-4899-8069-e0e3048e911d.sketch_text.stroke-42"),sQuery(id+"FHMxAyK4CFUKdhS_1.wireOp",EDGE,"1cb9c079-ea9b-4899-8069-e0e3048e911d.sketch_text.stroke-43"),sQuery(id+"FHMxAyK4CFUKdhS_1.wireOp",EDGE,"1cb9c079-ea9b-4899-8069-e0e3048e911d.sketch_text.stroke-44"),sQuery(id+"FHMxAyK4CFUKdhS_1.wireOp",EDGE,"1cb9c079-ea9b-4899-8069-e0e3048e911d.sketch_text.stroke-45"),sQuery(id+"FHMxAyK4CFUKdhS_1.wireOp",EDGE,"1cb9c079-ea9b-4899-8069-e0e3048e911d.sketch_text.stroke-46"),sQuery(id+"FHMxAyK4CFUKdhS_1.wireOp",EDGE,"1cb9c079-ea9b-4899-8069-e0e3048e911d.sketch_text.stroke-47"),sQuery(id+"FHMxAyK4CFUKdhS_1.wireOp",EDGE,"1cb9c079-ea9b-4899-8069-e0e3048e911d.sketch_text.stroke-48"),sQuery(id+"FHMxAyK4CFUKdhS_1.wireOp",EDGE,"1cb9c079-ea9b-4899-8069-e0e3048e911d.sketch_text.stroke-49"),sQuery(id+"FHMxAyK4CFUKdhS_1.wireOp",EDGE,"1cb9c079-ea9b-4899-8069-e0e3048e911d.sketch_text.stroke-50"),sQuery(id+"FHMxAyK4CFUKdhS_1.wireOp",EDGE,"1cb9c079-ea9b-4899-8069-e0e3048e911d.sketch_text.stroke-51"),sQuery(id+"FHMxAyK4CFUKdhS_1.wireOp",EDGE,"1cb9c079-ea9b-4899-8069-e0e3048e911d.sketch_text.stroke-52"),sQuery(id+"FHMxAyK4CFUKdhS_1.wireOp",EDGE,"1cb9c079-ea9b-4899-8069-e0e3048e911d.sketch_text.stroke-53"),sQuery(id+"FHMxAyK4CFUKdhS_1.wireOp",EDGE,"1cb9c079-ea9b-4899-8069-e0e3048e911d.sketch_text.stroke-54"),sQuery(id+"FHMxAyK4CFUKdhS_1.wireOp",EDGE,"1cb9c079-ea9b-4899-8069-e0e3048e911d.sketch_text.stroke-55"),sQuery(id+"FHMxAyK4CFUKdhS_1.wireOp",EDGE,"1cb9c079-ea9b-4899-8069-e0e3048e911d.sketch_text.stroke-56"),sQuery(id+"FHMxAyK4CFUKdhS_1.wireOp",EDGE,"1cb9c079-ea9b-4899-8069-e0e3048e911d.sketch_text.stroke-57"),sQuery(id+"FHMxAyK4CFUKdhS_1.wireOp",EDGE,"1cb9c079-ea9b-4899-8069-e0e3048e911d.sketch_text.stroke-58"),sQuery(id+"FHMxAyK4CFUKdhS_1.wireOp",EDGE,"1cb9c079-ea9b-4899-8069-e0e3048e911d.sketch_text.stroke-59"),sQuery(id+"FHMxAyK4CFUKdhS_1.wireOp",EDGE,"1cb9c079-ea9b-4899-8069-e0e3048e911d.sketch_text.stroke-60"),sQuery(id+"FHMxAyK4CFUKdhS_1.wireOp",EDGE,"1cb9c079-ea9b-4899-8069-e0e3048e911d.sketch_text.stroke-61"),sQuery(id+"FHMxAyK4CFUKdhS_1.wireOp",EDGE,"1cb9c079-ea9b-4899-8069-e0e3048e911d.sketch_text.stroke-62"),sQuery(id+"FHMxAyK4CFUKdhS_1.wireOp",EDGE,"1cb9c079-ea9b-4899-8069-e0e3048e911d.sketch_text.stroke-71"),sQuery(id+"FHMxAyK4CFUKdhS_1.wireOp",EDGE,"1cb9c079-ea9b-4899-8069-e0e3048e911d.sketch_text.stroke-72"),sQuery(id+"FHMxAyK4CFUKdhS_1.wireOp",EDGE,"1cb9c079-ea9b-4899-8069-e0e3048e911d.sketch_text.stroke-73"),sQuery(id+"FHMxAyK4CFUKdhS_1.wireOp",EDGE,"1cb9c079-ea9b-4899-8069-e0e3048e911d.sketch_text.stroke-74"),sQuery(id+"FHMxAyK4CFUKdhS_1.wireOp",EDGE,"1cb9c079-ea9b-4899-8069-e0e3048e911d.sketch_text.stroke-75"),sQuery(id+"FHMxAyK4CFUKdhS_1.wireOp",EDGE,"1cb9c079-ea9b-4899-8069-e0e3048e911d.sketch_text.stroke-76"),sQuery(id+"FHMxAyK4CFUKdhS_1.wireOp",EDGE,"1cb9c079-ea9b-4899-8069-e0e3048e911d.sketch_text.stroke-77"),sQuery(id+"FHMxAyK4CFUKdhS_1.wireOp",EDGE,"1cb9c079-ea9b-4899-8069-e0e3048e911d.sketch_text.stroke-78"),sQuery(id+"FHMxAyK4CFUKdhS_1.wireOp",EDGE,"1cb9c079-ea9b-4899-8069-e0e3048e911d.sketch_text.stroke-79"),sQuery(id+"FHMxAyK4CFUKdhS_1.wireOp",EDGE,"1cb9c079-ea9b-4899-8069-e0e3048e911d.sketch_text.stroke-80"),sQuery(id+"FHMxAyK4CFUKdhS_1.wireOp",EDGE,"1cb9c079-ea9b-4899-8069-e0e3048e911d.sketch_text.stroke-81"),sQuery(id+"FHMxAyK4CFUKdhS_1.wireOp",EDGE,"1cb9c079-ea9b-4899-8069-e0e3048e911d.sketch_text.stroke-82"),sQuery(id+"FHMxAyK4CFUKdhS_1.wireOp",EDGE,"1cb9c079-ea9b-4899-8069-e0e3048e911d.sketch_text.stroke-83"),sQuery(id+"FHMxAyK4CFUKdhS_1.wireOp",EDGE,"1cb9c079-ea9b-4899-8069-e0e3048e911d.sketch_text.stroke-84"),sQuery(id+"FHMxAyK4CFUKdhS_1.wireOp",EDGE,"1cb9c079-ea9b-4899-8069-e0e3048e911d.sketch_text.stroke-85"),sQuery(id+"FHMxAyK4CFUKdhS_1.wireOp",EDGE,"1cb9c079-ea9b-4899-8069-e0e3048e911d.sketch_text.stroke-86"),sQuery(id+"FHMxAyK4CFUKdhS_1.wireOp",EDGE,"1cb9c079-ea9b-4899-8069-e0e3048e911d.sketch_text.stroke-87"),sQuery(id+"FHMxAyK4CFUKdhS_1.wireOp",EDGE,"1cb9c079-ea9b-4899-8069-e0e3048e911d.sketch_text.stroke-88"),sQuery(id+"FHMxAyK4CFUKdhS_1.wireOp",EDGE,"1cb9c079-ea9b-4899-8069-e0e3048e911d.sketch_text.stroke-89"),sQuery(id+"FHMxAyK4CFUKdhS_1.wireOp",EDGE,"1cb9c079-ea9b-4899-8069-e0e3048e911d.sketch_text.stroke-90"),sQuery(id+"FHMxAyK4CFUKdhS_1.wireOp",EDGE,"1cb9c079-ea9b-4899-8069-e0e3048e911d.sketch_text.stroke-91"),sQuery(id+"FHMxAyK4CFUKdhS_1.wireOp",EDGE,"1cb9c079-ea9b-4899-8069-e0e3048e911d.sketch_text.stroke-92"),sQuery(id+"FHMxAyK4CFUKdhS_1.wireOp",EDGE,"1cb9c079-ea9b-4899-8069-e0e3048e911d.sketch_text.stroke-93"),sQuery(id+"FHMxAyK4CFUKdhS_1.wireOp",EDGE,"1cb9c079-ea9b-4899-8069-e0e3048e911d.sketch_text.stroke-94"),sQuery(id+"FHMxAyK4CFUKdhS_1.wireOp",EDGE,"1cb9c079-ea9b-4899-8069-e0e3048e911d.sketch_text.stroke-95"),sQuery(id+"FHMxAyK4CFUKdhS_1.wireOp",EDGE,"1cb9c079-ea9b-4899-8069-e0e3048e911d.sketch_text.stroke-96"),sQuery(id+"FHMxAyK4CFUKdhS_1.wireOp",EDGE,"1cb9c079-ea9b-4899-8069-e0e3048e911d.sketch_text.stroke-97"),sQuery(id+"FHMxAyK4CFUKdhS_1.wireOp",EDGE,"1cb9c079-ea9b-4899-8069-e0e3048e911d.sketch_text.stroke-103"),sQuery(id+"FHMxAyK4CFUKdhS_1.wireOp",EDGE,"1cb9c079-ea9b-4899-8069-e0e3048e911d.sketch_text.stroke-104"),sQuery(id+"FHMxAyK4CFUKdhS_1.wireOp",EDGE,"1cb9c079-ea9b-4899-8069-e0e3048e911d.sketch_text.stroke-105"),sQuery(id+"FHMxAyK4CFUKdhS_1.wireOp",EDGE,"1cb9c079-ea9b-4899-8069-e0e3048e911d.sketch_text.stroke-106"),sQuery(id+"FHMxAyK4CFUKdhS_1.wireOp",EDGE,"1cb9c079-ea9b-4899-8069-e0e3048e911d.sketch_text.stroke-107"),sQuery(id+"FHMxAyK4CFUKdhS_1.wireOp",EDGE,"1cb9c079-ea9b-4899-8069-e0e3048e911d.sketch_text.stroke-108"),sQuery(id+"FHMxAyK4CFUKdhS_1.wireOp",EDGE,"1cb9c079-ea9b-4899-8069-e0e3048e911d.sketch_text.stroke-109"),sQuery(id+"FHMxAyK4CFUKdhS_1.wireOp",EDGE,"1cb9c079-ea9b-4899-8069-e0e3048e911d.sketch_text.stroke-110"),sQuery(id+"FHMxAyK4CFUKdhS_1.wireOp",EDGE,"1cb9c079-ea9b-4899-8069-e0e3048e911d.sketch_text.stroke-111"),sQuery(id+"FHMxAyK4CFUKdhS_1.wireOp",EDGE,"1cb9c079-ea9b-4899-8069-e0e3048e911d.sketch_text.stroke-112"),sQuery(id+"FHMxAyK4CFUKdhS_1.wireOp",EDGE,"1cb9c079-ea9b-4899-8069-e0e3048e911d.sketch_text.stroke-113"),sQuery(id+"FHMxAyK4CFUKdhS_1.wireOp",EDGE,"1cb9c079-ea9b-4899-8069-e0e3048e911d.sketch_text.stroke-114"),sQuery(id+"FHMxAyK4CFUKdhS_1.wireOp",EDGE,"1cb9c079-ea9b-4899-8069-e0e3048e911d.sketch_text.stroke-115"),sQuery(id+"FHMxAyK4CFUKdhS_1.wireOp",EDGE,"1cb9c079-ea9b-4899-8069-e0e3048e911d.sketch_text.stroke-116"),sQuery(id+"FHMxAyK4CFUKdhS_1.wireOp",EDGE,"1cb9c079-ea9b-4899-8069-e0e3048e911d.sketch_text.stroke-117"),sQuery(id+"FHMxAyK4CFUKdhS_1.wireOp",EDGE,"1cb9c079-ea9b-4899-8069-e0e3048e911d.sketch_text.stroke-118"),sQuery(id+"FHMxAyK4CFUKdhS_1.wireOp",EDGE,"1cb9c079-ea9b-4899-8069-e0e3048e911d.sketch_text.stroke-119"),sQuery(id+"FHMxAyK4CFUKdhS_1.wireOp",EDGE,"1cb9c079-ea9b-4899-8069-e0e3048e911d.sketch_text.stroke-120"),sQuery(id+"FHMxAyK4CFUKdhS_1.wireOp",EDGE,"1cb9c079-ea9b-4899-8069-e0e3048e911d.sketch_text.stroke-121"),sQuery(id+"FHMxAyK4CFUKdhS_1.wireOp",EDGE,"1cb9c079-ea9b-4899-8069-e0e3048e911d.sketch_text.stroke-122"),sQuery(id+"FHMxAyK4CFUKdhS_1.wireOp",EDGE,"1cb9c079-ea9b-4899-8069-e0e3048e911d.sketch_text.stroke-123"),sQuery(id+"FHMxAyK4CFUKdhS_1.wireOp",EDGE,"1cb9c079-ea9b-4899-8069-e0e3048e911d.sketch_text.stroke-124"),sQuery(id+"FHMxAyK4CFUKdhS_1.wireOp",EDGE,"1cb9c079-ea9b-4899-8069-e0e3048e911d.sketch_text.stroke-125"),sQuery(id+"FHMxAyK4CFUKdhS_1.wireOp",EDGE,"1cb9c079-ea9b-4899-8069-e0e3048e911d.sketch_text.stroke-126"),sQuery(id+"FHMxAyK4CFUKdhS_1.wireOp",EDGE,"1cb9c079-ea9b-4899-8069-e0e3048e911d.sketch_text.stroke-127"),sQuery(id+"FHMxAyK4CFUKdhS_1.wireOp",EDGE,"1cb9c079-ea9b-4899-8069-e0e3048e911d.sketch_text.stroke-128"),sQuery(id+"FHMxAyK4CFUKdhS_1.wireOp",EDGE,"1cb9c079-ea9b-4899-8069-e0e3048e911d.sketch_text.stroke-129"),sQuery(id+"FHMxAyK4CFUKdhS_1.wireOp",EDGE,"1cb9c079-ea9b-4899-8069-e0e3048e911d.sketch_text.stroke-130"),sQuery(id+"FHMxAyK4CFUKdhS_1.wireOp",EDGE,"1cb9c079-ea9b-4899-8069-e0e3048e911d.sketch_text.stroke-131"),sQuery(id+"FHMxAyK4CFUKdhS_1.wireOp",EDGE,"1cb9c079-ea9b-4899-8069-e0e3048e911d.sketch_text.stroke-132"),sQuery(id+"FHMxAyK4CFUKdhS_1.wireOp",EDGE,"1cb9c079-ea9b-4899-8069-e0e3048e911d.sketch_text.stroke-133"),sQuery(id+"FHMxAyK4CFUKdhS_1.wireOp",EDGE,"1cb9c079-ea9b-4899-8069-e0e3048e911d.sketch_text.stroke-134"),sQuery(id+"FHMxAyK4CFUKdhS_1.wireOp",EDGE,"1cb9c079-ea9b-4899-8069-e0e3048e911d.sketch_text.stroke-135"),sQuery(id+"FHMxAyK4CFUKdhS_1.wireOp",EDGE,"1cb9c079-ea9b-4899-8069-e0e3048e911d.sketch_text.stroke-136"),sQuery(id+"FHMxAyK4CFUKdhS_1.wireOp",EDGE,"1cb9c079-ea9b-4899-8069-e0e3048e911d.sketch_text.stroke-137"),sQuery(id+"FHMxAyK4CFUKdhS_1.wireOp",EDGE,"1cb9c079-ea9b-4899-8069-e0e3048e911d.sketch_text.stroke-138"),sQuery(id+"FHMxAyK4CFUKdhS_1.wireOp",EDGE,"1cb9c079-ea9b-4899-8069-e0e3048e911d.sketch_text.stroke-139"),sQuery(id+"FHMxAyK4CFUKdhS_1.wireOp",EDGE,"1cb9c079-ea9b-4899-8069-e0e3048e911d.sketch_text.stroke-140"),sQuery(id+"FHMxAyK4CFUKdhS_1.wireOp",EDGE,"1cb9c079-ea9b-4899-8069-e0e3048e911d.sketch_text.stroke-141"),sQuery(id+"FHMxAyK4CFUKdhS_1.wireOp",EDGE,"1cb9c079-ea9b-4899-8069-e0e3048e911d.sketch_text.stroke-142"),sQuery(id+"FHMxAyK4CFUKdhS_1.wireOp",EDGE,"1cb9c079-ea9b-4899-8069-e0e3048e911d.sketch_text.stroke-143"),sQuery(id+"FHMxAyK4CFUKdhS_1.wireOp",EDGE,"1cb9c079-ea9b-4899-8069-e0e3048e911d.sketch_text.stroke-144"),sQuery(id+"FHMxAyK4CFUKdhS_1.wireOp",EDGE,"1cb9c079-ea9b-4899-8069-e0e3048e911d.sketch_text.stroke-145"),sQuery(id+"FHMxAyK4CFUKdhS_1.wireOp",EDGE,"1cb9c079-ea9b-4899-8069-e0e3048e911d.sketch_text.stroke-146"),sQuery(id+"FHMxAyK4CFUKdhS_1.wireOp",EDGE,"1cb9c079-ea9b-4899-8069-e0e3048e911d.sketch_text.stroke-147"),sQuery(id+"FHMxAyK4CFUKdhS_1.wireOp",EDGE,"1cb9c079-ea9b-4899-8069-e0e3048e911d.sketch_text.stroke-148"),sQuery(id+"FHMxAyK4CFUKdhS_1.wireOp",EDGE,"1cb9c079-ea9b-4899-8069-e0e3048e911d.sketch_text.stroke-149"),sQuery(id+"FHMxAyK4CFUKdhS_1.wireOp",EDGE,"1cb9c079-ea9b-4899-8069-e0e3048e911d.sketch_text.stroke-150"),sQuery(id+"FHMxAyK4CFUKdhS_1.wireOp",EDGE,"1cb9c079-ea9b-4899-8069-e0e3048e911d.sketch_text.stroke-151"),sQuery(id+"FHMxAyK4CFUKdhS_1.wireOp",EDGE,"1cb9c079-ea9b-4899-8069-e0e3048e911d.sketch_text.stroke-152"),sQuery(id+"FHMxAyK4CFUKdhS_1.wireOp",EDGE,"1cb9c079-ea9b-4899-8069-e0e3048e911d.sketch_text.stroke-153"),sQuery(id+"FHMxAyK4CFUKdhS_1.wireOp",EDGE,"1cb9c079-ea9b-4899-8069-e0e3048e911d.sketch_text.stroke-159"),sQuery(id+"FHMxAyK4CFUKdhS_1.wireOp",EDGE,"1cb9c079-ea9b-4899-8069-e0e3048e911d.sketch_text.stroke-160"),sQuery(id+"FHMxAyK4CFUKdhS_1.wireOp",EDGE,"1cb9c079-ea9b-4899-8069-e0e3048e911d.sketch_text.stroke-161"),sQuery(id+"FHMxAyK4CFUKdhS_1.wireOp",EDGE,"1cb9c079-ea9b-4899-8069-e0e3048e911d.sketch_text.stroke-162"),sQuery(id+"FHMxAyK4CFUKdhS_1.wireOp",EDGE,"1cb9c079-ea9b-4899-8069-e0e3048e911d.sketch_text.stroke-163"),sQuery(id+"FHMxAyK4CFUKdhS_1.wireOp",EDGE,"1cb9c079-ea9b-4899-8069-e0e3048e911d.sketch_text.stroke-164"),sQuery(id+"FHMxAyK4CFUKdhS_1.wireOp",EDGE,"1cb9c079-ea9b-4899-8069-e0e3048e911d.sketch_text.stroke-165"),sQuery(id+"FHMxAyK4CFUKdhS_1.wireOp",EDGE,"1cb9c079-ea9b-4899-8069-e0e3048e911d.sketch_text.stroke-166"),sQuery(id+"FHMxAyK4CFUKdhS_1.wireOp",EDGE,"1cb9c079-ea9b-4899-8069-e0e3048e911d.sketch_text.stroke-167"),sQuery(id+"FHMxAyK4CFUKdhS_1.wireOp",EDGE,"1cb9c079-ea9b-4899-8069-e0e3048e911d.sketch_text.stroke-168"),sQuery(id+"FHMxAyK4CFUKdhS_1.wireOp",EDGE,"1cb9c079-ea9b-4899-8069-e0e3048e911d.sketch_text.stroke-169"),sQuery(id+"FHMxAyK4CFUKdhS_1.wireOp",EDGE,"1cb9c079-ea9b-4899-8069-e0e3048e911d.sketch_text.stroke-170"),sQuery(id+"FHMxAyK4CFUKdhS_1.wireOp",EDGE,"1cb9c079-ea9b-4899-8069-e0e3048e911d.sketch_text.stroke-171"),sQuery(id+"FHMxAyK4CFUKdhS_1.wireOp",EDGE,"1cb9c079-ea9b-4899-8069-e0e3048e911d.sketch_text.stroke-172"),sQuery(id+"FHMxAyK4CFUKdhS_1.wireOp",EDGE,"1cb9c079-ea9b-4899-8069-e0e3048e911d.sketch_text.stroke-173"),sQuery(id+"FHMxAyK4CFUKdhS_1.wireOp",EDGE,"1cb9c079-ea9b-4899-8069-e0e3048e911d.sketch_text.stroke-174"),sQuery(id+"FHMxAyK4CFUKdhS_1.wireOp",EDGE,"1cb9c079-ea9b-4899-8069-e0e3048e911d.sketch_text.stroke-175"),sQuery(id+"FHMxAyK4CFUKdhS_1.wireOp",EDGE,"1cb9c079-ea9b-4899-8069-e0e3048e911d.sketch_text.stroke-176"),sQuery(id+"FHMxAyK4CFUKdhS_1.wireOp",EDGE,"1cb9c079-ea9b-4899-8069-e0e3048e911d.sketch_text.stroke-177"),sQuery(id+"FHMxAyK4CFUKdhS_1.wireOp",EDGE,"1cb9c079-ea9b-4899-8069-e0e3048e911d.sketch_text.stroke-178"),sQuery(id+"FHMxAyK4CFUKdhS_1.wireOp",EDGE,"1cb9c079-ea9b-4899-8069-e0e3048e911d.sketch_text.stroke-179"),sQuery(id+"FHMxAyK4CFUKdhS_1.wireOp",EDGE,"1cb9c079-ea9b-4899-8069-e0e3048e911d.sketch_text.stroke-180"),sQuery(id+"F3.wireOp",EDGE,"E28"),subQ2])],"isStart":true}),makeQuery(id+"F4.opExtrude","SWEPT_FACE",FACE,{"disambiguationData":[OSD([subQ2])]})]),OD(1.0)],"derivedFrom":makeQuery(id+"F1.opExtrude","CAP_EDGE",EDGE,{"disambiguationData":[OSD([subQ0])],"isStart":false})});}
            fillet(context, id + "F5", {"entities" : qUnion([Q0, Q1, Q2, Q3, Q4, Q5, Q6, Q7, Q8, Q9, Q10, Q11, Q12, Q13, Q14, Q15, Q16, Q17, Q18, Q19, Q20, Q21, Q22, Q23, Q24, Q25, Q26, Q27]), "radius" : 5.08 * mm, "tangentPropagation" : true, "allowEdgeOverflow" : false});
        }
    });
